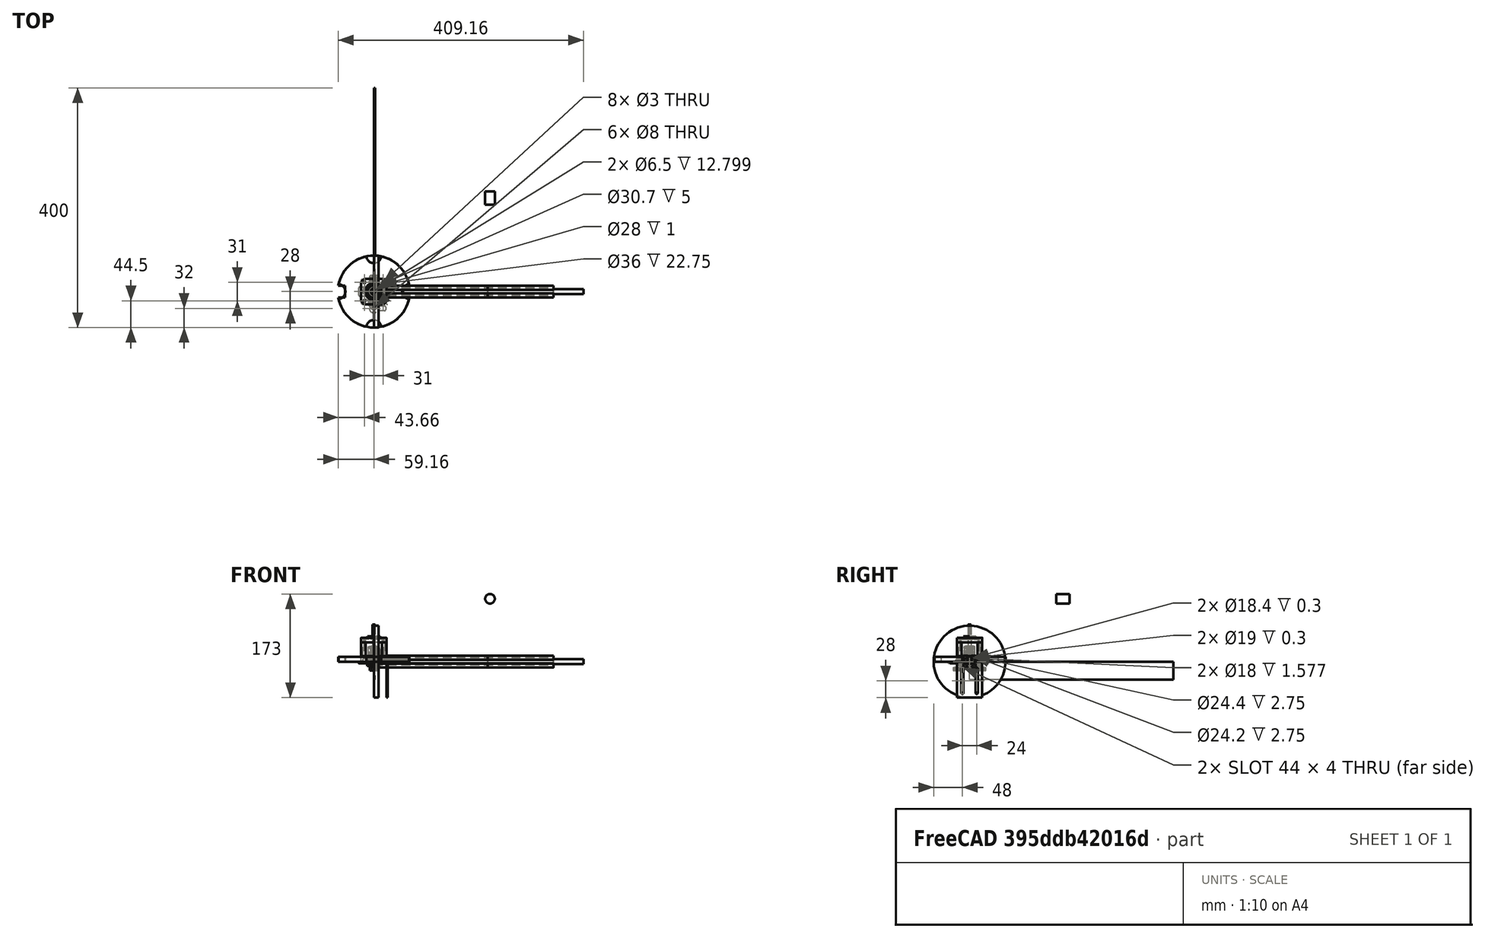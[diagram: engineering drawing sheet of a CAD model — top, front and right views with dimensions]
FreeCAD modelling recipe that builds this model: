
FCSTD DOCUMENT  (FreeCAD 0.19R)
Label: soloRuedas
License: All rights reserved
LicenseURL: http://en.wikipedia.org/wiki/All_rights_reserved
objects: Sketcher::SketchObject×358, PartDesign::Body×267, PartDesign::Pad×215, PartDesign::Fillet×183, App::Part×128, PartDesign::Pocket×123, PartDesign::FeatureBase×92, PartDesign::Revolution×52, App::DocumentObjectGroup×42, App::LinkGroup×30, PartDesign::PolarPattern×29, PartDesign::Chamfer×21, PartDesign::Groove×8, Part::FeaturePython×8, PartDesign::Mirrored×6, PartDesign::ShapeBinder×5, PartDesign::Hole×2, PartDesign::Draft×2, PartDesign::LinearPattern×2, PartDesign::Plane×2, +5 more types
note: 1994 computed .brp shape members not serialized (recipe doc carries the construction recipe); baked Part::Feature solids carry a one-line shape summary decoded from their .brp

FEATURE [Sketcher::SketchObject] Sketch001
  FullyConstrained = false
  MapMode = 5
  Support = -> [XY_Plane003]
  sketch-geometry (46):
    g0: LineSegment StartX=3.4 StartY=2.65 StartZ=0 EndX=3.4 EndY=-2.6657 EndZ=0
    g1: LineSegment StartX=2.63162 StartY=-3.4 StartZ=0 EndX=-2.65 EndY=-3.4 EndZ=0
    g2: LineSegment StartX=-3.4 StartY=-2.63136 StartZ=0 EndX=-3.4 EndY=2.61487 EndZ=0
    g3: LineSegment StartX=-10 StartY=10 StartZ=0 EndX=-3.125 EndY=10 EndZ=0
    g4: LineSegment StartX=10 StartY=10 StartZ=0 EndX=10 EndY=3.125 EndZ=0
    g5: LineSegment StartX=10 StartY=-10 StartZ=0 EndX=3.125 EndY=-10 EndZ=0
    g6: LineSegment StartX=-10 StartY=-10 StartZ=0 EndX=-10 EndY=-3.125 EndZ=0
    g7: GeomPoint X=3e-16 Y=0 Z=0
    g8: Circle CenterX=3e-16 CenterY=0 CenterZ=0 NormalX=0 NormalY=0 NormalZ=1 AngleXU=0 Radius=2.1
    g9: LineSegment StartX=-4.76483 StartY=8.08721 StartZ=0 EndX=-3.55 EndY=8.08721 EndZ=0
    g10: LineSegment StartX=8.24722 StartY=4.75 StartZ=0 EndX=8.24722 EndY=3.55 EndZ=0
    g11: LineSegment StartX=-8.2 StartY=-4.73729 StartZ=0 EndX=-8.2 EndY=-3.55 EndZ=0
    g12: LineSegment StartX=5.5 StartY=4.75 StartZ=0 EndX=8.24722 EndY=4.75 EndZ=0
    g13: LineSegment StartX=4.75 StartY=5.50457 StartZ=0 EndX=2.65 EndY=3.4 EndZ=0
    g14: LineSegment StartX=4.75 StartY=5.50457 StartZ=0 EndX=4.75 EndY=8.08721 EndZ=0
    g15: LineSegment StartX=3.4 StartY=2.65 StartZ=0 EndX=5.5 EndY=4.75 EndZ=0
    g16: LineSegment StartX=-4.76483 StartY=5.50457 StartZ=0 EndX=-2.66166 EndY=3.4 EndZ=0
    g17: LineSegment StartX=-5.5 StartY=4.70904 StartZ=0 EndX=-3.4 EndY=2.61487 EndZ=0
    g18: LineSegment StartX=-4.76483 StartY=5.50457 StartZ=0 EndX=-4.76483 EndY=8.08721 EndZ=0
    g19: LineSegment StartX=-5.5 StartY=4.70904 StartZ=0 EndX=-8.2 EndY=4.70904 EndZ=0
    g20: LineSegment StartX=-10 StartY=3.125 StartZ=0 EndX=-10 EndY=10 EndZ=0
    g21: LineSegment StartX=-8.2 StartY=3.55 StartZ=0 EndX=-8.2 EndY=4.70904 EndZ=0
    g22: LineSegment StartX=3.55 StartY=8.08721 StartZ=0 EndX=4.75 EndY=8.08721 EndZ=0
    g23: LineSegment StartX=3.125 StartY=10 StartZ=0 EndX=10 EndY=10 EndZ=0
    g24: LineSegment StartX=-5.5 StartY=-4.73729 StartZ=0 EndX=-8.2 EndY=-4.73729 EndZ=0
    g25: LineSegment StartX=-4.75 StartY=-5.5 StartZ=0 EndX=-2.65 EndY=-3.4 EndZ=0
    g26: LineSegment StartX=-4.75 StartY=-5.5 StartZ=0 EndX=-4.75 EndY=-8.2 EndZ=0
    g27: LineSegment StartX=4.73747 StartY=-5.5 StartZ=0 EndX=4.73747 EndY=-8.2 EndZ=0
    g28: LineSegment StartX=5.5 StartY=-4.7671 StartZ=0 EndX=8.24722 EndY=-4.7671 EndZ=0
    g29: LineSegment StartX=-3.125 StartY=-10 StartZ=0 EndX=-10 EndY=-10 EndZ=0
    g30: LineSegment StartX=-3.55 StartY=-8.2 StartZ=0 EndX=-4.75 EndY=-8.2 EndZ=0
    g31: LineSegment StartX=4.73747 StartY=-8.2 StartZ=0 EndX=3.55 EndY=-8.2 EndZ=0
    g32: LineSegment StartX=10 StartY=-3.125 StartZ=0 EndX=10 EndY=-10 EndZ=0
    g33: LineSegment StartX=8.24722 StartY=-3.55 StartZ=0 EndX=8.24722 EndY=-4.7671 EndZ=0
    g34: LineSegment StartX=-2.66166 StartY=3.4 StartZ=0 EndX=2.65 EndY=3.4 EndZ=0
    g35: LineSegment StartX=-3.4 StartY=-2.63136 StartZ=0 EndX=-5.5 EndY=-4.73729 EndZ=0
    g36: LineSegment StartX=3.4 StartY=-2.6657 StartZ=0 EndX=5.5 EndY=-4.7671 EndZ=0
    g37: LineSegment StartX=2.63162 StartY=-3.4 StartZ=0 EndX=4.73747 EndY=-5.5 EndZ=0
    g38: LineSegment StartX=-3.55 StartY=-8.2 StartZ=0 EndX=-3.125 EndY=-10 EndZ=0
    g39: LineSegment StartX=3.55 StartY=-8.2 StartZ=0 EndX=3.125 EndY=-10 EndZ=0
    g40: LineSegment StartX=-3.125 StartY=10 StartZ=0 EndX=-3.55 EndY=8.08721 EndZ=0
    g41: LineSegment StartX=3.125 StartY=10 StartZ=0 EndX=3.55 EndY=8.08721 EndZ=0
    g42: LineSegment StartX=8.24722 StartY=3.55 StartZ=0 EndX=10 EndY=3.125 EndZ=0
    g43: LineSegment StartX=10 StartY=-3.125 StartZ=0 EndX=8.24722 EndY=-3.55 EndZ=0
    g44: LineSegment StartX=-10 StartY=-3.125 StartZ=0 EndX=-8.2 EndY=-3.55 EndZ=0
    g45: LineSegment StartX=-10 StartY=3.125 StartZ=0 EndX=-8.2 EndY=3.55 EndZ=0
  constraints (61):
    c: Horizontal(g1)
    c: Vertical(g0)
    c: Vertical(g2)
    c: Coincident(g23,g4)
    c: Coincident(g32,g5)
    c: Coincident(g29,g6)
    c: Coincident(g20,g3)
    c: Horizontal(g3)
    c: Horizontal(g5)
    c: Vertical(g4)
    c: Vertical(g6)
    c: PointOnObject(g7,g-1)
    c: DistanceX(g3,g7) = 10
    c: DistanceX(g-1,g23) = 10
    c: DistanceY(g7,g3) = 10
    c: DistanceX(g3,g-1) = 10
    c: DistanceY(g32,g7) = 10
    c: Coincident(g8,g7)
    c: Radius(g8) = 2.1
    c: Horizontal(g9)
    c: Vertical(g10)
    c: Vertical(g11)
    c: Coincident(g12,g15)
    c: Horizontal(g12)
    c: Coincident(g14,g13)
    c: Vertical(g14)
    c: Coincident(g15,g0)
    c: Coincident(g13,g34)
    c: Coincident(g14,g22)
    c: Coincident(g18,g16)
    c: Vertical(g18)
    c: Coincident(g19,g17)
    c: Horizontal(g19)
    c: Coincident(g9,g18)
    c: Coincident(g21,g19)
    c: Coincident(g24,g35)
    c: Horizontal(g24)
    c: Coincident(g26,g25)
    c: Vertical(g26)
    c: Coincident(g27,g37)
    c: Vertical(g27)
    c: Coincident(g28,g36)
    c: Horizontal(g28)
    c: Coincident(g11,g24)
    c: Coincident(g26,g30)
    c: Coincident(g31,g27)
    c: Coincident(g12,g10)
    c: Coincident(g28,g33)
    c: Coincident(g25,g1)
    c: Coincident(g35,g2)
    c: Coincident(g17,g2)
    c: Coincident(g16,g34)
    c: Coincident(g1,g37)
    c: Coincident(g0,g36)
    c: Coincident(g39,g5)
    c: Coincident(g40,g3)
    c: Coincident(g42,g4)
    c: Coincident(g44,g6)
    c: Coincident(g21,g45)
    c: Coincident(g33,g43)
    c: Coincident(g10,g42)
FEATURE [PartDesign::Pad] Pad001
  Direction = (0,0,1)
  Length = 300
  Length2 = 10
  Profile = -> Sketch001
  Type = 0
FEATURE [PartDesign::Fillet] Fillet011
  Base = -> Pad001 [Edge53]
  BaseFeature = -> Pad001
  Radius = 1
  SupportTransform = false
FEATURE [PartDesign::Fillet] Fillet012
  Base = -> Fillet011 [Edge114]
  BaseFeature = -> Fillet011
  Radius = 1
  SupportTransform = false
FEATURE [PartDesign::Fillet] Fillet013
  Base = -> Fillet012 [Edge137,Edge95]
  BaseFeature = -> Fillet012
  Radius = 0.5
  SupportTransform = false
FEATURE [PartDesign::Fillet] Fillet014
  Base = -> Fillet013 [Edge103]
  BaseFeature = -> Fillet013
  Radius = 0.5
  SupportTransform = false
FEATURE [PartDesign::Fillet] Fillet015
  Base = -> Fillet014 [Edge96]
  BaseFeature = -> Fillet014
  Radius = 0.5
  SupportTransform = false
FEATURE [PartDesign::Fillet] Fillet016
  Base = -> Fillet015 [Edge77]
  BaseFeature = -> Fillet015
  Radius = 0.5
  SupportTransform = false
FEATURE [PartDesign::Fillet] Fillet017
  Base = -> Fillet016 [Edge102]
  BaseFeature = -> Fillet016
  Radius = 0.5
  SupportTransform = false
FEATURE [PartDesign::Fillet] Fillet018
  Base = -> Fillet017 [Edge85]
  BaseFeature = -> Fillet017
  Radius = 0.5
  SupportTransform = false
FEATURE [PartDesign::Fillet] Fillet019
  Base = -> Fillet018 [Edge78]
  BaseFeature = -> Fillet018
  Radius = 0.5
  SupportTransform = false
FEATURE [PartDesign::Fillet] Fillet020
  Base = -> Fillet019 [Edge107]
  BaseFeature = -> Fillet019
  Radius = 0.5
  SupportTransform = false
FEATURE [PartDesign::Fillet] Fillet021
  Base = -> Fillet020 [Edge74]
  BaseFeature = -> Fillet020
  Radius = 0.5
  SupportTransform = false
FEATURE [PartDesign::Body] Body001
  Group = -> [Sketch001,Pad001,Fillet011,Fillet012,Fillet013,Fillet014,Fillet015,Fillet016,Fillet017,Fillet018,Fillet019,Fillet020,Fillet021]
  Origin = -> Origin003
  Placement = pos=(0,0,0) rot=(0,1,0;1.5708rad)
  Tip = -> Fillet021
FEATURE [App::Part] Part001  label="2020-300-002"
  Group = -> [Body001]
  Origin = -> Origin002
  Placement = pos=(20,330,10) rot=(0,0,1;0rad)
FEATURE [Sketcher::SketchObject] Sketch002
  FullyConstrained = false
  MapMode = 5
  Support = -> [XY_Plane005]
  sketch-geometry (46):
    g0: LineSegment StartX=3.4 StartY=2.65 StartZ=0 EndX=3.4 EndY=-2.6657 EndZ=0
    g1: LineSegment StartX=2.63162 StartY=-3.4 StartZ=0 EndX=-2.65 EndY=-3.4 EndZ=0
    g2: LineSegment StartX=-3.4 StartY=-2.63136 StartZ=0 EndX=-3.4 EndY=2.61487 EndZ=0
    g3: LineSegment StartX=-10 StartY=10 StartZ=0 EndX=-3.125 EndY=10 EndZ=0
    g4: LineSegment StartX=10 StartY=10 StartZ=0 EndX=10 EndY=3.125 EndZ=0
    g5: LineSegment StartX=10 StartY=-10 StartZ=0 EndX=3.125 EndY=-10 EndZ=0
    g6: LineSegment StartX=-10 StartY=-10 StartZ=0 EndX=-10 EndY=-3.125 EndZ=0
    g7: GeomPoint X=3e-16 Y=0 Z=0
    g8: Circle CenterX=3e-16 CenterY=0 CenterZ=0 NormalX=0 NormalY=0 NormalZ=1 AngleXU=0 Radius=2.1
    g9: LineSegment StartX=-4.76483 StartY=8.08721 StartZ=0 EndX=-3.55 EndY=8.08721 EndZ=0
    g10: LineSegment StartX=8.24722 StartY=4.75 StartZ=0 EndX=8.24722 EndY=3.55 EndZ=0
    g11: LineSegment StartX=-8.2 StartY=-4.73729 StartZ=0 EndX=-8.2 EndY=-3.55 EndZ=0
    g12: LineSegment StartX=5.5 StartY=4.75 StartZ=0 EndX=8.24722 EndY=4.75 EndZ=0
    g13: LineSegment StartX=4.75 StartY=5.50457 StartZ=0 EndX=2.65 EndY=3.4 EndZ=0
    g14: LineSegment StartX=4.75 StartY=5.50457 StartZ=0 EndX=4.75 EndY=8.08721 EndZ=0
    g15: LineSegment StartX=3.4 StartY=2.65 StartZ=0 EndX=5.5 EndY=4.75 EndZ=0
    g16: LineSegment StartX=-4.76483 StartY=5.50457 StartZ=0 EndX=-2.66166 EndY=3.4 EndZ=0
    g17: LineSegment StartX=-5.5 StartY=4.70904 StartZ=0 EndX=-3.4 EndY=2.61487 EndZ=0
    g18: LineSegment StartX=-4.76483 StartY=5.50457 StartZ=0 EndX=-4.76483 EndY=8.08721 EndZ=0
    g19: LineSegment StartX=-5.5 StartY=4.70904 StartZ=0 EndX=-8.2 EndY=4.70904 EndZ=0
    g20: LineSegment StartX=-10 StartY=3.125 StartZ=0 EndX=-10 EndY=10 EndZ=0
    g21: LineSegment StartX=-8.2 StartY=3.55 StartZ=0 EndX=-8.2 EndY=4.70904 EndZ=0
    g22: LineSegment StartX=3.55 StartY=8.08721 StartZ=0 EndX=4.75 EndY=8.08721 EndZ=0
    g23: LineSegment StartX=3.125 StartY=10 StartZ=0 EndX=10 EndY=10 EndZ=0
    g24: LineSegment StartX=-5.5 StartY=-4.73729 StartZ=0 EndX=-8.2 EndY=-4.73729 EndZ=0
    g25: LineSegment StartX=-4.75 StartY=-5.5 StartZ=0 EndX=-2.65 EndY=-3.4 EndZ=0
    g26: LineSegment StartX=-4.75 StartY=-5.5 StartZ=0 EndX=-4.75 EndY=-8.2 EndZ=0
    g27: LineSegment StartX=4.73747 StartY=-5.5 StartZ=0 EndX=4.73747 EndY=-8.2 EndZ=0
    g28: LineSegment StartX=5.5 StartY=-4.7671 StartZ=0 EndX=8.24722 EndY=-4.7671 EndZ=0
    g29: LineSegment StartX=-3.125 StartY=-10 StartZ=0 EndX=-10 EndY=-10 EndZ=0
    g30: LineSegment StartX=-3.55 StartY=-8.2 StartZ=0 EndX=-4.75 EndY=-8.2 EndZ=0
    g31: LineSegment StartX=4.73747 StartY=-8.2 StartZ=0 EndX=3.55 EndY=-8.2 EndZ=0
    g32: LineSegment StartX=10 StartY=-3.125 StartZ=0 EndX=10 EndY=-10 EndZ=0
    g33: LineSegment StartX=8.24722 StartY=-3.55 StartZ=0 EndX=8.24722 EndY=-4.7671 EndZ=0
    g34: LineSegment StartX=-2.66166 StartY=3.4 StartZ=0 EndX=2.65 EndY=3.4 EndZ=0
    g35: LineSegment StartX=-3.4 StartY=-2.63136 StartZ=0 EndX=-5.5 EndY=-4.73729 EndZ=0
    g36: LineSegment StartX=3.4 StartY=-2.6657 StartZ=0 EndX=5.5 EndY=-4.7671 EndZ=0
    g37: LineSegment StartX=2.63162 StartY=-3.4 StartZ=0 EndX=4.73747 EndY=-5.5 EndZ=0
    g38: LineSegment StartX=-3.55 StartY=-8.2 StartZ=0 EndX=-3.125 EndY=-10 EndZ=0
    g39: LineSegment StartX=3.55 StartY=-8.2 StartZ=0 EndX=3.125 EndY=-10 EndZ=0
    g40: LineSegment StartX=-3.125 StartY=10 StartZ=0 EndX=-3.55 EndY=8.08721 EndZ=0
    g41: LineSegment StartX=3.125 StartY=10 StartZ=0 EndX=3.55 EndY=8.08721 EndZ=0
    g42: LineSegment StartX=8.24722 StartY=3.55 StartZ=0 EndX=10 EndY=3.125 EndZ=0
    g43: LineSegment StartX=10 StartY=-3.125 StartZ=0 EndX=8.24722 EndY=-3.55 EndZ=0
    g44: LineSegment StartX=-10 StartY=-3.125 StartZ=0 EndX=-8.2 EndY=-3.55 EndZ=0
    g45: LineSegment StartX=-10 StartY=3.125 StartZ=0 EndX=-8.2 EndY=3.55 EndZ=0
  constraints (61):
    c: Horizontal(g1)
    c: Vertical(g0)
    c: Vertical(g2)
    c: Coincident(g23,g4)
    c: Coincident(g32,g5)
    c: Coincident(g29,g6)
    c: Coincident(g20,g3)
    c: Horizontal(g3)
    c: Horizontal(g5)
    c: Vertical(g4)
    c: Vertical(g6)
    c: PointOnObject(g7,g-1)
    c: DistanceX(g3,g7) = 10
    c: DistanceX(g-1,g23) = 10
    c: DistanceY(g7,g3) = 10
    c: DistanceX(g3,g-1) = 10
    c: DistanceY(g32,g7) = 10
    c: Coincident(g8,g7)
    c: Radius(g8) = 2.1
    c: Horizontal(g9)
    c: Vertical(g10)
    c: Vertical(g11)
    c: Coincident(g12,g15)
    c: Horizontal(g12)
    c: Coincident(g14,g13)
    c: Vertical(g14)
    c: Coincident(g15,g0)
    c: Coincident(g13,g34)
    c: Coincident(g14,g22)
    c: Coincident(g18,g16)
    c: Vertical(g18)
    c: Coincident(g19,g17)
    c: Horizontal(g19)
    c: Coincident(g9,g18)
    c: Coincident(g21,g19)
    c: Coincident(g24,g35)
    c: Horizontal(g24)
    c: Coincident(g26,g25)
    c: Vertical(g26)
    c: Coincident(g27,g37)
    c: Vertical(g27)
    c: Coincident(g28,g36)
    c: Horizontal(g28)
    c: Coincident(g11,g24)
    c: Coincident(g26,g30)
    c: Coincident(g31,g27)
    c: Coincident(g12,g10)
    c: Coincident(g28,g33)
    c: Coincident(g25,g1)
    c: Coincident(g35,g2)
    c: Coincident(g17,g2)
    c: Coincident(g16,g34)
    c: Coincident(g1,g37)
    c: Coincident(g0,g36)
    c: Coincident(g39,g5)
    c: Coincident(g40,g3)
    c: Coincident(g42,g4)
    c: Coincident(g44,g6)
    c: Coincident(g21,g45)
    c: Coincident(g33,g43)
    c: Coincident(g10,g42)
FEATURE [PartDesign::Pad] Pad002
  Direction = (0,0,1)
  Length = 300
  Length2 = 10
  Profile = -> Sketch002
  Type = 0
FEATURE [PartDesign::Fillet] Fillet022
  Base = -> Pad002 [Edge53]
  BaseFeature = -> Pad002
  Radius = 1
  SupportTransform = false
FEATURE [PartDesign::Fillet] Fillet023
  Base = -> Fillet022 [Edge114]
  BaseFeature = -> Fillet022
  Radius = 1
  SupportTransform = false
FEATURE [PartDesign::Fillet] Fillet024
  Base = -> Fillet023 [Edge137,Edge95]
  BaseFeature = -> Fillet023
  Radius = 0.5
  SupportTransform = false
FEATURE [PartDesign::Fillet] Fillet025
  Base = -> Fillet024 [Edge103]
  BaseFeature = -> Fillet024
  Radius = 0.5
  SupportTransform = false
FEATURE [PartDesign::Fillet] Fillet026
  Base = -> Fillet025 [Edge96]
  BaseFeature = -> Fillet025
  Radius = 0.5
  SupportTransform = false
FEATURE [PartDesign::Fillet] Fillet027
  Base = -> Fillet026 [Edge77]
  BaseFeature = -> Fillet026
  Radius = 0.5
  SupportTransform = false
FEATURE [PartDesign::Fillet] Fillet028
  Base = -> Fillet027 [Edge102]
  BaseFeature = -> Fillet027
  Radius = 0.5
  SupportTransform = false
FEATURE [PartDesign::Fillet] Fillet029
  Base = -> Fillet028 [Edge85]
  BaseFeature = -> Fillet028
  Radius = 0.5
  SupportTransform = false
FEATURE [PartDesign::Fillet] Fillet030
  Base = -> Fillet029 [Edge78]
  BaseFeature = -> Fillet029
  Radius = 0.5
  SupportTransform = false
FEATURE [PartDesign::Fillet] Fillet031
  Base = -> Fillet030 [Edge107]
  BaseFeature = -> Fillet030
  Radius = 0.5
  SupportTransform = false
FEATURE [PartDesign::Fillet] Fillet032
  Base = -> Fillet031 [Edge74]
  BaseFeature = -> Fillet031
  Radius = 0.5
  SupportTransform = false
FEATURE [PartDesign::Body] Body002
  Group = -> [Sketch002,Pad002,Fillet022,Fillet023,Fillet024,Fillet025,Fillet026,Fillet027,Fillet028,Fillet029,Fillet030,Fillet031,Fillet032]
  Origin = -> Origin005
  Placement = pos=(0,0,0) rot=(0,1,0;1.5708rad)
  Tip = -> Fillet032
FEATURE [App::Part] Part002  label="2020-300-003"
  Group = -> [Body002]
  Origin = -> Origin004
  Placement = pos=(10,20,10) rot=(0,0,1;1.5708rad)
FEATURE [Sketcher::SketchObject] Sketch003
  FullyConstrained = false
  MapMode = 5
  Support = -> [XY_Plane007]
  sketch-geometry (46):
    g0: LineSegment StartX=3.4 StartY=2.65 StartZ=0 EndX=3.4 EndY=-2.6657 EndZ=0
    g1: LineSegment StartX=2.63162 StartY=-3.4 StartZ=0 EndX=-2.65 EndY=-3.4 EndZ=0
    g2: LineSegment StartX=-3.4 StartY=-2.63136 StartZ=0 EndX=-3.4 EndY=2.61487 EndZ=0
    g3: LineSegment StartX=-10 StartY=10 StartZ=0 EndX=-3.125 EndY=10 EndZ=0
    g4: LineSegment StartX=10 StartY=10 StartZ=0 EndX=10 EndY=3.125 EndZ=0
    g5: LineSegment StartX=10 StartY=-10 StartZ=0 EndX=3.125 EndY=-10 EndZ=0
    g6: LineSegment StartX=-10 StartY=-10 StartZ=0 EndX=-10 EndY=-3.125 EndZ=0
    g7: GeomPoint X=3e-16 Y=0 Z=0
    g8: Circle CenterX=3e-16 CenterY=0 CenterZ=0 NormalX=0 NormalY=0 NormalZ=1 AngleXU=0 Radius=2.1
    g9: LineSegment StartX=-4.76483 StartY=8.08721 StartZ=0 EndX=-3.55 EndY=8.08721 EndZ=0
    g10: LineSegment StartX=8.24722 StartY=4.75 StartZ=0 EndX=8.24722 EndY=3.55 EndZ=0
    g11: LineSegment StartX=-8.2 StartY=-4.73729 StartZ=0 EndX=-8.2 EndY=-3.55 EndZ=0
    g12: LineSegment StartX=5.5 StartY=4.75 StartZ=0 EndX=8.24722 EndY=4.75 EndZ=0
    g13: LineSegment StartX=4.75 StartY=5.50457 StartZ=0 EndX=2.65 EndY=3.4 EndZ=0
    g14: LineSegment StartX=4.75 StartY=5.50457 StartZ=0 EndX=4.75 EndY=8.08721 EndZ=0
    g15: LineSegment StartX=3.4 StartY=2.65 StartZ=0 EndX=5.5 EndY=4.75 EndZ=0
    g16: LineSegment StartX=-4.76483 StartY=5.50457 StartZ=0 EndX=-2.66166 EndY=3.4 EndZ=0
    g17: LineSegment StartX=-5.5 StartY=4.70904 StartZ=0 EndX=-3.4 EndY=2.61487 EndZ=0
    g18: LineSegment StartX=-4.76483 StartY=5.50457 StartZ=0 EndX=-4.76483 EndY=8.08721 EndZ=0
    g19: LineSegment StartX=-5.5 StartY=4.70904 StartZ=0 EndX=-8.2 EndY=4.70904 EndZ=0
    g20: LineSegment StartX=-10 StartY=3.125 StartZ=0 EndX=-10 EndY=10 EndZ=0
    g21: LineSegment StartX=-8.2 StartY=3.55 StartZ=0 EndX=-8.2 EndY=4.70904 EndZ=0
    g22: LineSegment StartX=3.55 StartY=8.08721 StartZ=0 EndX=4.75 EndY=8.08721 EndZ=0
    g23: LineSegment StartX=3.125 StartY=10 StartZ=0 EndX=10 EndY=10 EndZ=0
    g24: LineSegment StartX=-5.5 StartY=-4.73729 StartZ=0 EndX=-8.2 EndY=-4.73729 EndZ=0
    g25: LineSegment StartX=-4.75 StartY=-5.5 StartZ=0 EndX=-2.65 EndY=-3.4 EndZ=0
    g26: LineSegment StartX=-4.75 StartY=-5.5 StartZ=0 EndX=-4.75 EndY=-8.2 EndZ=0
    g27: LineSegment StartX=4.73747 StartY=-5.5 StartZ=0 EndX=4.73747 EndY=-8.2 EndZ=0
    g28: LineSegment StartX=5.5 StartY=-4.7671 StartZ=0 EndX=8.24722 EndY=-4.7671 EndZ=0
    g29: LineSegment StartX=-3.125 StartY=-10 StartZ=0 EndX=-10 EndY=-10 EndZ=0
    g30: LineSegment StartX=-3.55 StartY=-8.2 StartZ=0 EndX=-4.75 EndY=-8.2 EndZ=0
    g31: LineSegment StartX=4.73747 StartY=-8.2 StartZ=0 EndX=3.55 EndY=-8.2 EndZ=0
    g32: LineSegment StartX=10 StartY=-3.125 StartZ=0 EndX=10 EndY=-10 EndZ=0
    g33: LineSegment StartX=8.24722 StartY=-3.55 StartZ=0 EndX=8.24722 EndY=-4.7671 EndZ=0
    g34: LineSegment StartX=-2.66166 StartY=3.4 StartZ=0 EndX=2.65 EndY=3.4 EndZ=0
    g35: LineSegment StartX=-3.4 StartY=-2.63136 StartZ=0 EndX=-5.5 EndY=-4.73729 EndZ=0
    g36: LineSegment StartX=3.4 StartY=-2.6657 StartZ=0 EndX=5.5 EndY=-4.7671 EndZ=0
    g37: LineSegment StartX=2.63162 StartY=-3.4 StartZ=0 EndX=4.73747 EndY=-5.5 EndZ=0
    g38: LineSegment StartX=-3.55 StartY=-8.2 StartZ=0 EndX=-3.125 EndY=-10 EndZ=0
    g39: LineSegment StartX=3.55 StartY=-8.2 StartZ=0 EndX=3.125 EndY=-10 EndZ=0
    g40: LineSegment StartX=-3.125 StartY=10 StartZ=0 EndX=-3.55 EndY=8.08721 EndZ=0
    g41: LineSegment StartX=3.125 StartY=10 StartZ=0 EndX=3.55 EndY=8.08721 EndZ=0
    g42: LineSegment StartX=8.24722 StartY=3.55 StartZ=0 EndX=10 EndY=3.125 EndZ=0
    g43: LineSegment StartX=10 StartY=-3.125 StartZ=0 EndX=8.24722 EndY=-3.55 EndZ=0
    g44: LineSegment StartX=-10 StartY=-3.125 StartZ=0 EndX=-8.2 EndY=-3.55 EndZ=0
    g45: LineSegment StartX=-10 StartY=3.125 StartZ=0 EndX=-8.2 EndY=3.55 EndZ=0
  constraints (61):
    c: Horizontal(g1)
    c: Vertical(g0)
    c: Vertical(g2)
    c: Coincident(g23,g4)
    c: Coincident(g32,g5)
    c: Coincident(g29,g6)
    c: Coincident(g20,g3)
    c: Horizontal(g3)
    c: Horizontal(g5)
    c: Vertical(g4)
    c: Vertical(g6)
    c: PointOnObject(g7,g-1)
    c: DistanceX(g3,g7) = 10
    c: DistanceX(g-1,g23) = 10
    c: DistanceY(g7,g3) = 10
    c: DistanceX(g3,g-1) = 10
    c: DistanceY(g32,g7) = 10
    c: Coincident(g8,g7)
    c: Radius(g8) = 2.1
    c: Horizontal(g9)
    c: Vertical(g10)
    c: Vertical(g11)
    c: Coincident(g12,g15)
    c: Horizontal(g12)
    c: Coincident(g14,g13)
    c: Vertical(g14)
    c: Coincident(g15,g0)
    c: Coincident(g13,g34)
    c: Coincident(g14,g22)
    c: Coincident(g18,g16)
    c: Vertical(g18)
    c: Coincident(g19,g17)
    c: Horizontal(g19)
    c: Coincident(g9,g18)
    c: Coincident(g21,g19)
    c: Coincident(g24,g35)
    c: Horizontal(g24)
    c: Coincident(g26,g25)
    c: Vertical(g26)
    c: Coincident(g27,g37)
    c: Vertical(g27)
    c: Coincident(g28,g36)
    c: Horizontal(g28)
    c: Coincident(g11,g24)
    c: Coincident(g26,g30)
    c: Coincident(g31,g27)
    c: Coincident(g12,g10)
    c: Coincident(g28,g33)
    c: Coincident(g25,g1)
    c: Coincident(g35,g2)
    c: Coincident(g17,g2)
    c: Coincident(g16,g34)
    c: Coincident(g1,g37)
    c: Coincident(g0,g36)
    c: Coincident(g39,g5)
    c: Coincident(g40,g3)
    c: Coincident(g42,g4)
    c: Coincident(g44,g6)
    c: Coincident(g21,g45)
    c: Coincident(g33,g43)
    c: Coincident(g10,g42)
FEATURE [PartDesign::Pad] Pad003
  Direction = (0,0,1)
  Length = 300
  Length2 = 10
  Profile = -> Sketch003
  Type = 0
FEATURE [PartDesign::Fillet] Fillet033
  Base = -> Pad003 [Edge53]
  BaseFeature = -> Pad003
  Radius = 1
  SupportTransform = false
FEATURE [PartDesign::Fillet] Fillet034
  Base = -> Fillet033 [Edge114]
  BaseFeature = -> Fillet033
  Radius = 1
  SupportTransform = false
FEATURE [PartDesign::Fillet] Fillet035
  Base = -> Fillet034 [Edge137,Edge95]
  BaseFeature = -> Fillet034
  Radius = 0.5
  SupportTransform = false
FEATURE [PartDesign::Fillet] Fillet036
  Base = -> Fillet035 [Edge103]
  BaseFeature = -> Fillet035
  Radius = 0.5
  SupportTransform = false
FEATURE [PartDesign::Fillet] Fillet037
  Base = -> Fillet036 [Edge96]
  BaseFeature = -> Fillet036
  Radius = 0.5
  SupportTransform = false
FEATURE [PartDesign::Fillet] Fillet038
  Base = -> Fillet037 [Edge77]
  BaseFeature = -> Fillet037
  Radius = 0.5
  SupportTransform = false
FEATURE [PartDesign::Fillet] Fillet039
  Base = -> Fillet038 [Edge102]
  BaseFeature = -> Fillet038
  Radius = 0.5
  SupportTransform = false
FEATURE [PartDesign::Fillet] Fillet040
  Base = -> Fillet039 [Edge85]
  BaseFeature = -> Fillet039
  Radius = 0.5
  SupportTransform = false
FEATURE [PartDesign::Fillet] Fillet041
  Base = -> Fillet040 [Edge78]
  BaseFeature = -> Fillet040
  Radius = 0.5
  SupportTransform = false
FEATURE [PartDesign::Fillet] Fillet042
  Base = -> Fillet041 [Edge107]
  BaseFeature = -> Fillet041
  Radius = 0.5
  SupportTransform = false
FEATURE [PartDesign::Fillet] Fillet043
  Base = -> Fillet042 [Edge74]
  BaseFeature = -> Fillet042
  Radius = 0.5
  SupportTransform = false
FEATURE [PartDesign::Body] Body003
  Group = -> [Sketch003,Pad003,Fillet033,Fillet034,Fillet035,Fillet036,Fillet037,Fillet038,Fillet039,Fillet040,Fillet041,Fillet042,Fillet043]
  Origin = -> Origin007
  Placement = pos=(0,0,0) rot=(0,1,0;1.5708rad)
  Tip = -> Fillet043
FEATURE [App::Part] Part003  label="2020-300-004"
  Group = -> [Body003]
  Origin = -> Origin006
  Placement = pos=(330,20,10) rot=(0,0,1;1.5708rad)
FEATURE [Sketcher::SketchObject] Sketch004
  FullyConstrained = false
  MapMode = 5
  Support = -> [XY_Plane009]
  sketch-geometry (46):
    g0: LineSegment StartX=3.4 StartY=2.65 StartZ=0 EndX=3.4 EndY=-2.6657 EndZ=0
    g1: LineSegment StartX=2.63162 StartY=-3.4 StartZ=0 EndX=-2.65 EndY=-3.4 EndZ=0
    g2: LineSegment StartX=-3.4 StartY=-2.63136 StartZ=0 EndX=-3.4 EndY=2.61487 EndZ=0
    g3: LineSegment StartX=-10 StartY=10 StartZ=0 EndX=-3.125 EndY=10 EndZ=0
    g4: LineSegment StartX=10 StartY=10 StartZ=0 EndX=10 EndY=3.125 EndZ=0
    g5: LineSegment StartX=10 StartY=-10 StartZ=0 EndX=3.125 EndY=-10 EndZ=0
    g6: LineSegment StartX=-10 StartY=-10 StartZ=0 EndX=-10 EndY=-3.125 EndZ=0
    g7: GeomPoint X=3e-16 Y=0 Z=0
    g8: Circle CenterX=3e-16 CenterY=0 CenterZ=0 NormalX=0 NormalY=0 NormalZ=1 AngleXU=0 Radius=2.1
    g9: LineSegment StartX=-4.76483 StartY=8.08721 StartZ=0 EndX=-3.55 EndY=8.08721 EndZ=0
    g10: LineSegment StartX=8.24722 StartY=4.75 StartZ=0 EndX=8.24722 EndY=3.55 EndZ=0
    g11: LineSegment StartX=-8.2 StartY=-4.73729 StartZ=0 EndX=-8.2 EndY=-3.55 EndZ=0
    g12: LineSegment StartX=5.5 StartY=4.75 StartZ=0 EndX=8.24722 EndY=4.75 EndZ=0
    g13: LineSegment StartX=4.75 StartY=5.50457 StartZ=0 EndX=2.65 EndY=3.4 EndZ=0
    g14: LineSegment StartX=4.75 StartY=5.50457 StartZ=0 EndX=4.75 EndY=8.08721 EndZ=0
    g15: LineSegment StartX=3.4 StartY=2.65 StartZ=0 EndX=5.5 EndY=4.75 EndZ=0
    g16: LineSegment StartX=-4.76483 StartY=5.50457 StartZ=0 EndX=-2.66166 EndY=3.4 EndZ=0
    g17: LineSegment StartX=-5.5 StartY=4.70904 StartZ=0 EndX=-3.4 EndY=2.61487 EndZ=0
    g18: LineSegment StartX=-4.76483 StartY=5.50457 StartZ=0 EndX=-4.76483 EndY=8.08721 EndZ=0
    g19: LineSegment StartX=-5.5 StartY=4.70904 StartZ=0 EndX=-8.2 EndY=4.70904 EndZ=0
    g20: LineSegment StartX=-10 StartY=3.125 StartZ=0 EndX=-10 EndY=10 EndZ=0
    g21: LineSegment StartX=-8.2 StartY=3.55 StartZ=0 EndX=-8.2 EndY=4.70904 EndZ=0
    g22: LineSegment StartX=3.55 StartY=8.08721 StartZ=0 EndX=4.75 EndY=8.08721 EndZ=0
    g23: LineSegment StartX=3.125 StartY=10 StartZ=0 EndX=10 EndY=10 EndZ=0
    g24: LineSegment StartX=-5.5 StartY=-4.73729 StartZ=0 EndX=-8.2 EndY=-4.73729 EndZ=0
    g25: LineSegment StartX=-4.75 StartY=-5.5 StartZ=0 EndX=-2.65 EndY=-3.4 EndZ=0
    g26: LineSegment StartX=-4.75 StartY=-5.5 StartZ=0 EndX=-4.75 EndY=-8.2 EndZ=0
    g27: LineSegment StartX=4.73747 StartY=-5.5 StartZ=0 EndX=4.73747 EndY=-8.2 EndZ=0
    g28: LineSegment StartX=5.5 StartY=-4.7671 StartZ=0 EndX=8.24722 EndY=-4.7671 EndZ=0
    g29: LineSegment StartX=-3.125 StartY=-10 StartZ=0 EndX=-10 EndY=-10 EndZ=0
    g30: LineSegment StartX=-3.55 StartY=-8.2 StartZ=0 EndX=-4.75 EndY=-8.2 EndZ=0
    g31: LineSegment StartX=4.73747 StartY=-8.2 StartZ=0 EndX=3.55 EndY=-8.2 EndZ=0
    g32: LineSegment StartX=10 StartY=-3.125 StartZ=0 EndX=10 EndY=-10 EndZ=0
    g33: LineSegment StartX=8.24722 StartY=-3.55 StartZ=0 EndX=8.24722 EndY=-4.7671 EndZ=0
    g34: LineSegment StartX=-2.66166 StartY=3.4 StartZ=0 EndX=2.65 EndY=3.4 EndZ=0
    g35: LineSegment StartX=-3.4 StartY=-2.63136 StartZ=0 EndX=-5.5 EndY=-4.73729 EndZ=0
    g36: LineSegment StartX=3.4 StartY=-2.6657 StartZ=0 EndX=5.5 EndY=-4.7671 EndZ=0
    g37: LineSegment StartX=2.63162 StartY=-3.4 StartZ=0 EndX=4.73747 EndY=-5.5 EndZ=0
    g38: LineSegment StartX=-3.55 StartY=-8.2 StartZ=0 EndX=-3.125 EndY=-10 EndZ=0
    g39: LineSegment StartX=3.55 StartY=-8.2 StartZ=0 EndX=3.125 EndY=-10 EndZ=0
    g40: LineSegment StartX=-3.125 StartY=10 StartZ=0 EndX=-3.55 EndY=8.08721 EndZ=0
    g41: LineSegment StartX=3.125 StartY=10 StartZ=0 EndX=3.55 EndY=8.08721 EndZ=0
    g42: LineSegment StartX=8.24722 StartY=3.55 StartZ=0 EndX=10 EndY=3.125 EndZ=0
    g43: LineSegment StartX=10 StartY=-3.125 StartZ=0 EndX=8.24722 EndY=-3.55 EndZ=0
    g44: LineSegment StartX=-10 StartY=-3.125 StartZ=0 EndX=-8.2 EndY=-3.55 EndZ=0
    g45: LineSegment StartX=-10 StartY=3.125 StartZ=0 EndX=-8.2 EndY=3.55 EndZ=0
  constraints (61):
    c: Horizontal(g1)
    c: Vertical(g0)
    c: Vertical(g2)
    c: Coincident(g23,g4)
    c: Coincident(g32,g5)
    c: Coincident(g29,g6)
    c: Coincident(g20,g3)
    c: Horizontal(g3)
    c: Horizontal(g5)
    c: Vertical(g4)
    c: Vertical(g6)
    c: PointOnObject(g7,g-1)
    c: DistanceX(g3,g7) = 10
    c: DistanceX(g-1,g23) = 10
    c: DistanceY(g7,g3) = 10
    c: DistanceX(g3,g-1) = 10
    c: DistanceY(g32,g7) = 10
    c: Coincident(g8,g7)
    c: Radius(g8) = 2.1
    c: Horizontal(g9)
    c: Vertical(g10)
    c: Vertical(g11)
    c: Coincident(g12,g15)
    c: Horizontal(g12)
    c: Coincident(g14,g13)
    c: Vertical(g14)
    c: Coincident(g15,g0)
    c: Coincident(g13,g34)
    c: Coincident(g14,g22)
    c: Coincident(g18,g16)
    c: Vertical(g18)
    c: Coincident(g19,g17)
    c: Horizontal(g19)
    c: Coincident(g9,g18)
    c: Coincident(g21,g19)
    c: Coincident(g24,g35)
    c: Horizontal(g24)
    c: Coincident(g26,g25)
    c: Vertical(g26)
    c: Coincident(g27,g37)
    c: Vertical(g27)
    c: Coincident(g28,g36)
    c: Horizontal(g28)
    c: Coincident(g11,g24)
    c: Coincident(g26,g30)
    c: Coincident(g31,g27)
    c: Coincident(g12,g10)
    c: Coincident(g28,g33)
    c: Coincident(g25,g1)
    c: Coincident(g35,g2)
    c: Coincident(g17,g2)
    c: Coincident(g16,g34)
    c: Coincident(g1,g37)
    c: Coincident(g0,g36)
    c: Coincident(g39,g5)
    c: Coincident(g40,g3)
    c: Coincident(g42,g4)
    c: Coincident(g44,g6)
    c: Coincident(g21,g45)
    c: Coincident(g33,g43)
    c: Coincident(g10,g42)
FEATURE [PartDesign::Pad] Pad004
  Direction = (0,0,1)
  Length = 190
  Length2 = 10
  Profile = -> Sketch004
  Type = 0
FEATURE [PartDesign::Fillet] Fillet044
  Base = -> Pad004 [Edge53]
  BaseFeature = -> Pad004
  Radius = 1
  SupportTransform = false
FEATURE [PartDesign::Fillet] Fillet045
  Base = -> Fillet044 [Edge114]
  BaseFeature = -> Fillet044
  Radius = 1
  SupportTransform = false
FEATURE [PartDesign::Fillet] Fillet046
  Base = -> Fillet045 [Edge137,Edge95]
  BaseFeature = -> Fillet045
  Radius = 0.5
  SupportTransform = false
FEATURE [PartDesign::Fillet] Fillet047
  Base = -> Fillet046 [Edge103]
  BaseFeature = -> Fillet046
  Radius = 0.5
  SupportTransform = false
FEATURE [PartDesign::Fillet] Fillet048
  Base = -> Fillet047 [Edge96]
  BaseFeature = -> Fillet047
  Radius = 0.5
  SupportTransform = false
FEATURE [PartDesign::Fillet] Fillet049
  Base = -> Fillet048 [Edge77]
  BaseFeature = -> Fillet048
  Radius = 0.5
  SupportTransform = false
FEATURE [PartDesign::Fillet] Fillet050
  Base = -> Fillet049 [Edge102]
  BaseFeature = -> Fillet049
  Radius = 0.5
  SupportTransform = false
FEATURE [PartDesign::Fillet] Fillet051
  Base = -> Fillet050 [Edge85]
  BaseFeature = -> Fillet050
  Radius = 0.5
  SupportTransform = false
FEATURE [PartDesign::Fillet] Fillet052
  Base = -> Fillet051 [Edge78]
  BaseFeature = -> Fillet051
  Radius = 0.5
  SupportTransform = false
FEATURE [PartDesign::Fillet] Fillet053
  Base = -> Fillet052 [Edge107]
  BaseFeature = -> Fillet052
  Radius = 0.5
  SupportTransform = false
FEATURE [PartDesign::Fillet] Fillet054
  Base = -> Fillet053 [Edge74]
  BaseFeature = -> Fillet053
  Radius = 0.5
  SupportTransform = false
FEATURE [PartDesign::Body] Body004
  Group = -> [Sketch004,Pad004,Fillet044,Fillet045,Fillet046,Fillet047,Fillet048,Fillet049,Fillet050,Fillet051,Fillet052,Fillet053,Fillet054]
  Origin = -> Origin009
  Placement = pos=(0,0,0) rot=(0,1,0;1.5708rad)
  Tip = -> Fillet054
FEATURE [Sketcher::SketchObject] Sketch
  FullyConstrained = false
  MapMode = 4
  Placement = pos=(0,0,0) rot=(0.707107,0.707107,0;3.14159rad)
  Support = -> [Body004]
  sketch-geometry (46):
    g0: LineSegment StartX=3.4 StartY=2.65 StartZ=0 EndX=3.4 EndY=-2.6657 EndZ=0
    g1: LineSegment StartX=2.63162 StartY=-3.4 StartZ=0 EndX=-2.65 EndY=-3.4 EndZ=0
    g2: LineSegment StartX=-3.4 StartY=-2.63136 StartZ=0 EndX=-3.4 EndY=2.61487 EndZ=0
    g3: LineSegment StartX=-10 StartY=10 StartZ=0 EndX=-3.125 EndY=10 EndZ=0
    g4: LineSegment StartX=10 StartY=10 StartZ=0 EndX=10 EndY=3.125 EndZ=0
    g5: LineSegment StartX=10 StartY=-10 StartZ=0 EndX=3.125 EndY=-10 EndZ=0
    g6: LineSegment StartX=-10 StartY=-10 StartZ=0 EndX=-10 EndY=-3.125 EndZ=0
    g7: GeomPoint X=3e-16 Y=0 Z=0
    g8: Circle CenterX=3e-16 CenterY=0 CenterZ=0 NormalX=0 NormalY=0 NormalZ=1 AngleXU=0 Radius=2.1
    g9: LineSegment StartX=-4.76483 StartY=8.08721 StartZ=0 EndX=-3.55 EndY=8.08721 EndZ=0
    g10: LineSegment StartX=8.24722 StartY=4.75 StartZ=0 EndX=8.24722 EndY=3.55 EndZ=0
    g11: LineSegment StartX=-8.2 StartY=-4.73729 StartZ=0 EndX=-8.2 EndY=-3.55 EndZ=0
    g12: LineSegment StartX=5.5 StartY=4.75 StartZ=0 EndX=8.24722 EndY=4.75 EndZ=0
    g13: LineSegment StartX=4.75 StartY=5.50457 StartZ=0 EndX=2.65 EndY=3.4 EndZ=0
    g14: LineSegment StartX=4.75 StartY=5.50457 StartZ=0 EndX=4.75 EndY=8.08721 EndZ=0
    g15: LineSegment StartX=3.4 StartY=2.65 StartZ=0 EndX=5.5 EndY=4.75 EndZ=0
    g16: LineSegment StartX=-4.76483 StartY=5.50457 StartZ=0 EndX=-2.66166 EndY=3.4 EndZ=0
    g17: LineSegment StartX=-5.5 StartY=4.70904 StartZ=0 EndX=-3.4 EndY=2.61487 EndZ=0
    g18: LineSegment StartX=-4.76483 StartY=5.50457 StartZ=0 EndX=-4.76483 EndY=8.08721 EndZ=0
    g19: LineSegment StartX=-5.5 StartY=4.70904 StartZ=0 EndX=-8.2 EndY=4.70904 EndZ=0
    g20: LineSegment StartX=-10 StartY=3.125 StartZ=0 EndX=-10 EndY=10 EndZ=0
    g21: LineSegment StartX=-8.2 StartY=3.55 StartZ=0 EndX=-8.2 EndY=4.70904 EndZ=0
    g22: LineSegment StartX=3.55 StartY=8.08721 StartZ=0 EndX=4.75 EndY=8.08721 EndZ=0
    g23: LineSegment StartX=3.125 StartY=10 StartZ=0 EndX=10 EndY=10 EndZ=0
    g24: LineSegment StartX=-5.5 StartY=-4.73729 StartZ=0 EndX=-8.2 EndY=-4.73729 EndZ=0
    g25: LineSegment StartX=-4.75 StartY=-5.5 StartZ=0 EndX=-2.65 EndY=-3.4 EndZ=0
    g26: LineSegment StartX=-4.75 StartY=-5.5 StartZ=0 EndX=-4.75 EndY=-8.2 EndZ=0
    g27: LineSegment StartX=4.73747 StartY=-5.5 StartZ=0 EndX=4.73747 EndY=-8.2 EndZ=0
    g28: LineSegment StartX=5.5 StartY=-4.7671 StartZ=0 EndX=8.24722 EndY=-4.7671 EndZ=0
    g29: LineSegment StartX=-3.125 StartY=-10 StartZ=0 EndX=-10 EndY=-10 EndZ=0
    g30: LineSegment StartX=-3.55 StartY=-8.2 StartZ=0 EndX=-4.75 EndY=-8.2 EndZ=0
    g31: LineSegment StartX=4.73747 StartY=-8.2 StartZ=0 EndX=3.55 EndY=-8.2 EndZ=0
    g32: LineSegment StartX=10 StartY=-3.125 StartZ=0 EndX=10 EndY=-10 EndZ=0
    g33: LineSegment StartX=8.24722 StartY=-3.55 StartZ=0 EndX=8.24722 EndY=-4.7671 EndZ=0
    g34: LineSegment StartX=-2.66166 StartY=3.4 StartZ=0 EndX=2.65 EndY=3.4 EndZ=0
    g35: LineSegment StartX=-3.4 StartY=-2.63136 StartZ=0 EndX=-5.5 EndY=-4.73729 EndZ=0
    g36: LineSegment StartX=3.4 StartY=-2.6657 StartZ=0 EndX=5.5 EndY=-4.7671 EndZ=0
    g37: LineSegment StartX=2.63162 StartY=-3.4 StartZ=0 EndX=4.73747 EndY=-5.5 EndZ=0
    g38: LineSegment StartX=-3.55 StartY=-8.2 StartZ=0 EndX=-3.125 EndY=-10 EndZ=0
    g39: LineSegment StartX=3.55 StartY=-8.2 StartZ=0 EndX=3.125 EndY=-10 EndZ=0
    g40: LineSegment StartX=-3.125 StartY=10 StartZ=0 EndX=-3.55 EndY=8.08721 EndZ=0
    g41: LineSegment StartX=3.125 StartY=10 StartZ=0 EndX=3.55 EndY=8.08721 EndZ=0
    g42: LineSegment StartX=8.24722 StartY=3.55 StartZ=0 EndX=10 EndY=3.125 EndZ=0
    g43: LineSegment StartX=10 StartY=-3.125 StartZ=0 EndX=8.24722 EndY=-3.55 EndZ=0
    g44: LineSegment StartX=-10 StartY=-3.125 StartZ=0 EndX=-8.2 EndY=-3.55 EndZ=0
    g45: LineSegment StartX=-10 StartY=3.125 StartZ=0 EndX=-8.2 EndY=3.55 EndZ=0
  constraints (61):
    c: Horizontal(g1)
    c: Vertical(g0)
    c: Vertical(g2)
    c: Coincident(g23,g4)
    c: Coincident(g32,g5)
    c: Coincident(g29,g6)
    c: Coincident(g20,g3)
    c: Horizontal(g3)
    c: Horizontal(g5)
    c: Vertical(g4)
    c: Vertical(g6)
    c: PointOnObject(g7,g-1)
    c: DistanceX(g3,g7) = 10
    c: DistanceX(g-1,g23) = 10
    c: DistanceY(g7,g3) = 10
    c: DistanceX(g3,g-1) = 10
    c: DistanceY(g32,g7) = 10
    c: Coincident(g8,g7)
    c: Radius(g8) = 2.1
    c: Horizontal(g9)
    c: Vertical(g10)
    c: Vertical(g11)
    c: Coincident(g12,g15)
    c: Horizontal(g12)
    c: Coincident(g14,g13)
    c: Vertical(g14)
    c: Coincident(g15,g0)
    c: Coincident(g13,g34)
    c: Coincident(g14,g22)
    c: Coincident(g18,g16)
    c: Vertical(g18)
    c: Coincident(g19,g17)
    c: Horizontal(g19)
    c: Coincident(g9,g18)
    c: Coincident(g21,g19)
    c: Coincident(g24,g35)
    c: Horizontal(g24)
    c: Coincident(g26,g25)
    c: Vertical(g26)
    c: Coincident(g27,g37)
    c: Vertical(g27)
    c: Coincident(g28,g36)
    c: Horizontal(g28)
    c: Coincident(g11,g24)
    c: Coincident(g26,g30)
    c: Coincident(g31,g27)
    c: Coincident(g12,g10)
    c: Coincident(g28,g33)
    c: Coincident(g25,g1)
    c: Coincident(g35,g2)
    c: Coincident(g17,g2)
    c: Coincident(g16,g34)
    c: Coincident(g1,g37)
    c: Coincident(g0,g36)
    c: Coincident(g39,g5)
    c: Coincident(g40,g3)
    c: Coincident(g42,g4)
    c: Coincident(g44,g6)
    c: Coincident(g21,g45)
    c: Coincident(g33,g43)
    c: Coincident(g10,g42)
FEATURE [PartDesign::Pad] Pad
  Direction = (2e-16,0,-1)
  Length = 300
  Length2 = 10
  Placement = pos=(0,0,0) rot=(0,1,0;1.5708rad)
  Profile = -> Sketch
  Type = 0
FEATURE [PartDesign::Fillet] Fillet
  Base = -> Pad [Edge53]
  BaseFeature = -> Pad
  Placement = pos=(0,0,0) rot=(0,1,0;1.5708rad)
  Radius = 1
  SupportTransform = false
FEATURE [PartDesign::Fillet] Fillet001
  Base = -> Fillet [Edge114]
  BaseFeature = -> Fillet
  Placement = pos=(0,0,0) rot=(0,1,0;1.5708rad)
  Radius = 1
  SupportTransform = false
FEATURE [PartDesign::Fillet] Fillet002
  Base = -> Fillet001 [Edge137,Edge95]
  BaseFeature = -> Fillet001
  Placement = pos=(0,0,0) rot=(0,1,0;1.5708rad)
  Radius = 0.5
  SupportTransform = false
FEATURE [PartDesign::Fillet] Fillet003
  Base = -> Fillet002 [Edge103]
  BaseFeature = -> Fillet002
  Placement = pos=(0,0,0) rot=(0.57735,0.57735,0.57735;2.0944rad)
  Radius = 0.5
  SupportTransform = false
FEATURE [PartDesign::Fillet] Fillet004
  Base = -> Fillet003 [Edge96]
  BaseFeature = -> Fillet003
  Placement = pos=(0,0,0) rot=(0.57735,0.57735,0.57735;2.0944rad)
  Radius = 0.5
  SupportTransform = false
FEATURE [PartDesign::Fillet] Fillet005
  Base = -> Fillet004 [Edge77]
  BaseFeature = -> Fillet004
  Placement = pos=(0,0,0) rot=(0.57735,0.57735,0.57735;2.0944rad)
  Radius = 0.5
  SupportTransform = false
FEATURE [PartDesign::Fillet] Fillet006
  Base = -> Fillet005 [Edge102]
  BaseFeature = -> Fillet005
  Placement = pos=(0,0,0) rot=(0.57735,0.57735,0.57735;2.0944rad)
  Radius = 0.5
  SupportTransform = false
FEATURE [PartDesign::Fillet] Fillet007
  Base = -> Fillet006 [Edge85]
  BaseFeature = -> Fillet006
  Placement = pos=(0,0,0) rot=(0.57735,0.57735,0.57735;2.0944rad)
  Radius = 0.5
  SupportTransform = false
FEATURE [PartDesign::Fillet] Fillet008
  Base = -> Fillet007 [Edge78]
  BaseFeature = -> Fillet007
  Placement = pos=(0,0,0) rot=(0.57735,0.57735,0.57735;2.0944rad)
  Radius = 0.5
  SupportTransform = false
FEATURE [PartDesign::Fillet] Fillet009
  Base = -> Fillet008 [Edge107]
  BaseFeature = -> Fillet008
  Placement = pos=(0,0,0) rot=(0.57735,0.57735,0.57735;2.0944rad)
  Radius = 0.5
  SupportTransform = false
FEATURE [PartDesign::Fillet] Fillet010
  Base = -> Fillet009 [Edge74]
  BaseFeature = -> Fillet009
  Radius = 0.5
  SupportTransform = false
FEATURE [PartDesign::Body] Body
  Group = -> [Sketch,Pad,Fillet,Fillet001,Fillet002,Fillet003,Fillet004,Fillet005,Fillet006,Fillet007,Fillet008,Fillet009,Fillet010]
  Origin = -> Origin001
  Placement = pos=(0,0,0) rot=(0,1,0;1.5708rad)
  Tip = -> Fillet010
FEATURE [App::Part] Part  label="2020-300-001"
  Group = -> [Body]
  Origin = -> Origin
  Placement = pos=(20,10,10) rot=(0,0,1;0rad)
FEATURE [App::Part] Part004  label="2020-300-005"
  Group = -> [Body004]
  Origin = -> Origin008
  Placement = pos=(10,10,0) rot=(0,1,0;4.71239rad)
FEATURE [Sketcher::SketchObject] Sketch005
  FullyConstrained = false
  MapMode = 5
  Support = -> [XY_Plane011]
  sketch-geometry (46):
    g0: LineSegment StartX=3.4 StartY=2.65 StartZ=0 EndX=3.4 EndY=-2.6657 EndZ=0
    g1: LineSegment StartX=2.63162 StartY=-3.4 StartZ=0 EndX=-2.65 EndY=-3.4 EndZ=0
    g2: LineSegment StartX=-3.4 StartY=-2.63136 StartZ=0 EndX=-3.4 EndY=2.61487 EndZ=0
    g3: LineSegment StartX=-10 StartY=10 StartZ=0 EndX=-3.125 EndY=10 EndZ=0
    g4: LineSegment StartX=10 StartY=10 StartZ=0 EndX=10 EndY=3.125 EndZ=0
    g5: LineSegment StartX=10 StartY=-10 StartZ=0 EndX=3.125 EndY=-10 EndZ=0
    g6: LineSegment StartX=-10 StartY=-10 StartZ=0 EndX=-10 EndY=-3.125 EndZ=0
    g7: GeomPoint X=3e-16 Y=0 Z=0
    g8: Circle CenterX=3e-16 CenterY=0 CenterZ=0 NormalX=0 NormalY=0 NormalZ=1 AngleXU=0 Radius=2.1
    g9: LineSegment StartX=-4.76483 StartY=8.08721 StartZ=0 EndX=-3.55 EndY=8.08721 EndZ=0
    g10: LineSegment StartX=8.24722 StartY=4.75 StartZ=0 EndX=8.24722 EndY=3.55 EndZ=0
    g11: LineSegment StartX=-8.2 StartY=-4.73729 StartZ=0 EndX=-8.2 EndY=-3.55 EndZ=0
    g12: LineSegment StartX=5.5 StartY=4.75 StartZ=0 EndX=8.24722 EndY=4.75 EndZ=0
    g13: LineSegment StartX=4.75 StartY=5.50457 StartZ=0 EndX=2.65 EndY=3.4 EndZ=0
    g14: LineSegment StartX=4.75 StartY=5.50457 StartZ=0 EndX=4.75 EndY=8.08721 EndZ=0
    g15: LineSegment StartX=3.4 StartY=2.65 StartZ=0 EndX=5.5 EndY=4.75 EndZ=0
    g16: LineSegment StartX=-4.76483 StartY=5.50457 StartZ=0 EndX=-2.66166 EndY=3.4 EndZ=0
    g17: LineSegment StartX=-5.5 StartY=4.70904 StartZ=0 EndX=-3.4 EndY=2.61487 EndZ=0
    g18: LineSegment StartX=-4.76483 StartY=5.50457 StartZ=0 EndX=-4.76483 EndY=8.08721 EndZ=0
    g19: LineSegment StartX=-5.5 StartY=4.70904 StartZ=0 EndX=-8.2 EndY=4.70904 EndZ=0
    g20: LineSegment StartX=-10 StartY=3.125 StartZ=0 EndX=-10 EndY=10 EndZ=0
    g21: LineSegment StartX=-8.2 StartY=3.55 StartZ=0 EndX=-8.2 EndY=4.70904 EndZ=0
    g22: LineSegment StartX=3.55 StartY=8.08721 StartZ=0 EndX=4.75 EndY=8.08721 EndZ=0
    g23: LineSegment StartX=3.125 StartY=10 StartZ=0 EndX=10 EndY=10 EndZ=0
    g24: LineSegment StartX=-5.5 StartY=-4.73729 StartZ=0 EndX=-8.2 EndY=-4.73729 EndZ=0
    g25: LineSegment StartX=-4.75 StartY=-5.5 StartZ=0 EndX=-2.65 EndY=-3.4 EndZ=0
    g26: LineSegment StartX=-4.75 StartY=-5.5 StartZ=0 EndX=-4.75 EndY=-8.2 EndZ=0
    g27: LineSegment StartX=4.73747 StartY=-5.5 StartZ=0 EndX=4.73747 EndY=-8.2 EndZ=0
    g28: LineSegment StartX=5.5 StartY=-4.7671 StartZ=0 EndX=8.24722 EndY=-4.7671 EndZ=0
    g29: LineSegment StartX=-3.125 StartY=-10 StartZ=0 EndX=-10 EndY=-10 EndZ=0
    g30: LineSegment StartX=-3.55 StartY=-8.2 StartZ=0 EndX=-4.75 EndY=-8.2 EndZ=0
    g31: LineSegment StartX=4.73747 StartY=-8.2 StartZ=0 EndX=3.55 EndY=-8.2 EndZ=0
    g32: LineSegment StartX=10 StartY=-3.125 StartZ=0 EndX=10 EndY=-10 EndZ=0
    g33: LineSegment StartX=8.24722 StartY=-3.55 StartZ=0 EndX=8.24722 EndY=-4.7671 EndZ=0
    g34: LineSegment StartX=-2.66166 StartY=3.4 StartZ=0 EndX=2.65 EndY=3.4 EndZ=0
    g35: LineSegment StartX=-3.4 StartY=-2.63136 StartZ=0 EndX=-5.5 EndY=-4.73729 EndZ=0
    g36: LineSegment StartX=3.4 StartY=-2.6657 StartZ=0 EndX=5.5 EndY=-4.7671 EndZ=0
    g37: LineSegment StartX=2.63162 StartY=-3.4 StartZ=0 EndX=4.73747 EndY=-5.5 EndZ=0
    g38: LineSegment StartX=-3.55 StartY=-8.2 StartZ=0 EndX=-3.125 EndY=-10 EndZ=0
    g39: LineSegment StartX=3.55 StartY=-8.2 StartZ=0 EndX=3.125 EndY=-10 EndZ=0
    g40: LineSegment StartX=-3.125 StartY=10 StartZ=0 EndX=-3.55 EndY=8.08721 EndZ=0
    g41: LineSegment StartX=3.125 StartY=10 StartZ=0 EndX=3.55 EndY=8.08721 EndZ=0
    g42: LineSegment StartX=8.24722 StartY=3.55 StartZ=0 EndX=10 EndY=3.125 EndZ=0
    g43: LineSegment StartX=10 StartY=-3.125 StartZ=0 EndX=8.24722 EndY=-3.55 EndZ=0
    g44: LineSegment StartX=-10 StartY=-3.125 StartZ=0 EndX=-8.2 EndY=-3.55 EndZ=0
    g45: LineSegment StartX=-10 StartY=3.125 StartZ=0 EndX=-8.2 EndY=3.55 EndZ=0
  constraints (61):
    c: Horizontal(g1)
    c: Vertical(g0)
    c: Vertical(g2)
    c: Coincident(g23,g4)
    c: Coincident(g32,g5)
    c: Coincident(g29,g6)
    c: Coincident(g20,g3)
    c: Horizontal(g3)
    c: Horizontal(g5)
    c: Vertical(g4)
    c: Vertical(g6)
    c: PointOnObject(g7,g-1)
    c: DistanceX(g3,g7) = 10
    c: DistanceX(g-1,g23) = 10
    c: DistanceY(g7,g3) = 10
    c: DistanceX(g3,g-1) = 10
    c: DistanceY(g32,g7) = 10
    c: Coincident(g8,g7)
    c: Radius(g8) = 2.1
    c: Horizontal(g9)
    c: Vertical(g10)
    c: Vertical(g11)
    c: Coincident(g12,g15)
    c: Horizontal(g12)
    c: Coincident(g14,g13)
    c: Vertical(g14)
    c: Coincident(g15,g0)
    c: Coincident(g13,g34)
    c: Coincident(g14,g22)
    c: Coincident(g18,g16)
    c: Vertical(g18)
    c: Coincident(g19,g17)
    c: Horizontal(g19)
    c: Coincident(g9,g18)
    c: Coincident(g21,g19)
    c: Coincident(g24,g35)
    c: Horizontal(g24)
    c: Coincident(g26,g25)
    c: Vertical(g26)
    c: Coincident(g27,g37)
    c: Vertical(g27)
    c: Coincident(g28,g36)
    c: Horizontal(g28)
    c: Coincident(g11,g24)
    c: Coincident(g26,g30)
    c: Coincident(g31,g27)
    c: Coincident(g12,g10)
    c: Coincident(g28,g33)
    c: Coincident(g25,g1)
    c: Coincident(g35,g2)
    c: Coincident(g17,g2)
    c: Coincident(g16,g34)
    c: Coincident(g1,g37)
    c: Coincident(g0,g36)
    c: Coincident(g39,g5)
    c: Coincident(g40,g3)
    c: Coincident(g42,g4)
    c: Coincident(g44,g6)
    c: Coincident(g21,g45)
    c: Coincident(g33,g43)
    c: Coincident(g10,g42)
FEATURE [PartDesign::Pad] Pad005
  Direction = (0,0,1)
  Length = 190
  Length2 = 10
  Profile = -> Sketch005
  Type = 0
FEATURE [PartDesign::Fillet] Fillet055
  Base = -> Pad005 [Edge53]
  BaseFeature = -> Pad005
  Radius = 1
  SupportTransform = false
FEATURE [PartDesign::Fillet] Fillet056
  Base = -> Fillet055 [Edge114]
  BaseFeature = -> Fillet055
  Radius = 1
  SupportTransform = false
FEATURE [PartDesign::Fillet] Fillet057
  Base = -> Fillet056 [Edge137,Edge95]
  BaseFeature = -> Fillet056
  Radius = 0.5
  SupportTransform = false
FEATURE [PartDesign::Fillet] Fillet058
  Base = -> Fillet057 [Edge103]
  BaseFeature = -> Fillet057
  Radius = 0.5
  SupportTransform = false
FEATURE [PartDesign::Fillet] Fillet059
  Base = -> Fillet058 [Edge96]
  BaseFeature = -> Fillet058
  Radius = 0.5
  SupportTransform = false
FEATURE [PartDesign::Fillet] Fillet060
  Base = -> Fillet059 [Edge77]
  BaseFeature = -> Fillet059
  Radius = 0.5
  SupportTransform = false
FEATURE [PartDesign::Fillet] Fillet061
  Base = -> Fillet060 [Edge102]
  BaseFeature = -> Fillet060
  Radius = 0.5
  SupportTransform = false
FEATURE [PartDesign::Fillet] Fillet062
  Base = -> Fillet061 [Edge85]
  BaseFeature = -> Fillet061
  Radius = 0.5
  SupportTransform = false
FEATURE [PartDesign::Fillet] Fillet063
  Base = -> Fillet062 [Edge78]
  BaseFeature = -> Fillet062
  Radius = 0.5
  SupportTransform = false
FEATURE [PartDesign::Fillet] Fillet064
  Base = -> Fillet063 [Edge107]
  BaseFeature = -> Fillet063
  Radius = 0.5
  SupportTransform = false
FEATURE [PartDesign::Fillet] Fillet065
  Base = -> Fillet064 [Edge74]
  BaseFeature = -> Fillet064
  Radius = 0.5
  SupportTransform = false
FEATURE [PartDesign::Body] Body005
  Group = -> [Sketch005,Pad005,Fillet055,Fillet056,Fillet057,Fillet058,Fillet059,Fillet060,Fillet061,Fillet062,Fillet063,Fillet064,Fillet065]
  Origin = -> Origin011
  Placement = pos=(0,0,0) rot=(0,1,0;1.5708rad)
  Tip = -> Fillet065
FEATURE [App::Part] Part005  label="2020-300-006"
  Group = -> [Body005]
  Origin = -> Origin010
  Placement = pos=(10,330,0) rot=(0,1,0;4.71239rad)
FEATURE [Sketcher::SketchObject] Sketch006
  FullyConstrained = false
  MapMode = 5
  Support = -> [XY_Plane013]
  sketch-geometry (46):
    g0: LineSegment StartX=3.4 StartY=2.65 StartZ=0 EndX=3.4 EndY=-2.6657 EndZ=0
    g1: LineSegment StartX=2.63162 StartY=-3.4 StartZ=0 EndX=-2.65 EndY=-3.4 EndZ=0
    g2: LineSegment StartX=-3.4 StartY=-2.63136 StartZ=0 EndX=-3.4 EndY=2.61487 EndZ=0
    g3: LineSegment StartX=-10 StartY=10 StartZ=0 EndX=-3.125 EndY=10 EndZ=0
    g4: LineSegment StartX=10 StartY=10 StartZ=0 EndX=10 EndY=3.125 EndZ=0
    g5: LineSegment StartX=10 StartY=-10 StartZ=0 EndX=3.125 EndY=-10 EndZ=0
    g6: LineSegment StartX=-10 StartY=-10 StartZ=0 EndX=-10 EndY=-3.125 EndZ=0
    g7: GeomPoint X=3e-16 Y=0 Z=0
    g8: Circle CenterX=3e-16 CenterY=0 CenterZ=0 NormalX=0 NormalY=0 NormalZ=1 AngleXU=0 Radius=2.1
    g9: LineSegment StartX=-4.76483 StartY=8.08721 StartZ=0 EndX=-3.55 EndY=8.08721 EndZ=0
    g10: LineSegment StartX=8.24722 StartY=4.75 StartZ=0 EndX=8.24722 EndY=3.55 EndZ=0
    g11: LineSegment StartX=-8.2 StartY=-4.73729 StartZ=0 EndX=-8.2 EndY=-3.55 EndZ=0
    g12: LineSegment StartX=5.5 StartY=4.75 StartZ=0 EndX=8.24722 EndY=4.75 EndZ=0
    g13: LineSegment StartX=4.75 StartY=5.50457 StartZ=0 EndX=2.65 EndY=3.4 EndZ=0
    g14: LineSegment StartX=4.75 StartY=5.50457 StartZ=0 EndX=4.75 EndY=8.08721 EndZ=0
    g15: LineSegment StartX=3.4 StartY=2.65 StartZ=0 EndX=5.5 EndY=4.75 EndZ=0
    g16: LineSegment StartX=-4.76483 StartY=5.50457 StartZ=0 EndX=-2.66166 EndY=3.4 EndZ=0
    g17: LineSegment StartX=-5.5 StartY=4.70904 StartZ=0 EndX=-3.4 EndY=2.61487 EndZ=0
    g18: LineSegment StartX=-4.76483 StartY=5.50457 StartZ=0 EndX=-4.76483 EndY=8.08721 EndZ=0
    g19: LineSegment StartX=-5.5 StartY=4.70904 StartZ=0 EndX=-8.2 EndY=4.70904 EndZ=0
    g20: LineSegment StartX=-10 StartY=3.125 StartZ=0 EndX=-10 EndY=10 EndZ=0
    g21: LineSegment StartX=-8.2 StartY=3.55 StartZ=0 EndX=-8.2 EndY=4.70904 EndZ=0
    g22: LineSegment StartX=3.55 StartY=8.08721 StartZ=0 EndX=4.75 EndY=8.08721 EndZ=0
    g23: LineSegment StartX=3.125 StartY=10 StartZ=0 EndX=10 EndY=10 EndZ=0
    g24: LineSegment StartX=-5.5 StartY=-4.73729 StartZ=0 EndX=-8.2 EndY=-4.73729 EndZ=0
    g25: LineSegment StartX=-4.75 StartY=-5.5 StartZ=0 EndX=-2.65 EndY=-3.4 EndZ=0
    g26: LineSegment StartX=-4.75 StartY=-5.5 StartZ=0 EndX=-4.75 EndY=-8.2 EndZ=0
    g27: LineSegment StartX=4.73747 StartY=-5.5 StartZ=0 EndX=4.73747 EndY=-8.2 EndZ=0
    g28: LineSegment StartX=5.5 StartY=-4.7671 StartZ=0 EndX=8.24722 EndY=-4.7671 EndZ=0
    g29: LineSegment StartX=-3.125 StartY=-10 StartZ=0 EndX=-10 EndY=-10 EndZ=0
    g30: LineSegment StartX=-3.55 StartY=-8.2 StartZ=0 EndX=-4.75 EndY=-8.2 EndZ=0
    g31: LineSegment StartX=4.73747 StartY=-8.2 StartZ=0 EndX=3.55 EndY=-8.2 EndZ=0
    g32: LineSegment StartX=10 StartY=-3.125 StartZ=0 EndX=10 EndY=-10 EndZ=0
    g33: LineSegment StartX=8.24722 StartY=-3.55 StartZ=0 EndX=8.24722 EndY=-4.7671 EndZ=0
    g34: LineSegment StartX=-2.66166 StartY=3.4 StartZ=0 EndX=2.65 EndY=3.4 EndZ=0
    g35: LineSegment StartX=-3.4 StartY=-2.63136 StartZ=0 EndX=-5.5 EndY=-4.73729 EndZ=0
    g36: LineSegment StartX=3.4 StartY=-2.6657 StartZ=0 EndX=5.5 EndY=-4.7671 EndZ=0
    g37: LineSegment StartX=2.63162 StartY=-3.4 StartZ=0 EndX=4.73747 EndY=-5.5 EndZ=0
    g38: LineSegment StartX=-3.55 StartY=-8.2 StartZ=0 EndX=-3.125 EndY=-10 EndZ=0
    g39: LineSegment StartX=3.55 StartY=-8.2 StartZ=0 EndX=3.125 EndY=-10 EndZ=0
    g40: LineSegment StartX=-3.125 StartY=10 StartZ=0 EndX=-3.55 EndY=8.08721 EndZ=0
    g41: LineSegment StartX=3.125 StartY=10 StartZ=0 EndX=3.55 EndY=8.08721 EndZ=0
    g42: LineSegment StartX=8.24722 StartY=3.55 StartZ=0 EndX=10 EndY=3.125 EndZ=0
    g43: LineSegment StartX=10 StartY=-3.125 StartZ=0 EndX=8.24722 EndY=-3.55 EndZ=0
    g44: LineSegment StartX=-10 StartY=-3.125 StartZ=0 EndX=-8.2 EndY=-3.55 EndZ=0
    g45: LineSegment StartX=-10 StartY=3.125 StartZ=0 EndX=-8.2 EndY=3.55 EndZ=0
  constraints (61):
    c: Horizontal(g1)
    c: Vertical(g0)
    c: Vertical(g2)
    c: Coincident(g23,g4)
    c: Coincident(g32,g5)
    c: Coincident(g29,g6)
    c: Coincident(g20,g3)
    c: Horizontal(g3)
    c: Horizontal(g5)
    c: Vertical(g4)
    c: Vertical(g6)
    c: PointOnObject(g7,g-1)
    c: DistanceX(g3,g7) = 10
    c: DistanceX(g-1,g23) = 10
    c: DistanceY(g7,g3) = 10
    c: DistanceX(g3,g-1) = 10
    c: DistanceY(g32,g7) = 10
    c: Coincident(g8,g7)
    c: Radius(g8) = 2.1
    c: Horizontal(g9)
    c: Vertical(g10)
    c: Vertical(g11)
    c: Coincident(g12,g15)
    c: Horizontal(g12)
    c: Coincident(g14,g13)
    c: Vertical(g14)
    c: Coincident(g15,g0)
    c: Coincident(g13,g34)
    c: Coincident(g14,g22)
    c: Coincident(g18,g16)
    c: Vertical(g18)
    c: Coincident(g19,g17)
    c: Horizontal(g19)
    c: Coincident(g9,g18)
    c: Coincident(g21,g19)
    c: Coincident(g24,g35)
    c: Horizontal(g24)
    c: Coincident(g26,g25)
    c: Vertical(g26)
    c: Coincident(g27,g37)
    c: Vertical(g27)
    c: Coincident(g28,g36)
    c: Horizontal(g28)
    c: Coincident(g11,g24)
    c: Coincident(g26,g30)
    c: Coincident(g31,g27)
    c: Coincident(g12,g10)
    c: Coincident(g28,g33)
    c: Coincident(g25,g1)
    c: Coincident(g35,g2)
    c: Coincident(g17,g2)
    c: Coincident(g16,g34)
    c: Coincident(g1,g37)
    c: Coincident(g0,g36)
    c: Coincident(g39,g5)
    c: Coincident(g40,g3)
    c: Coincident(g42,g4)
    c: Coincident(g44,g6)
    c: Coincident(g21,g45)
    c: Coincident(g33,g43)
    c: Coincident(g10,g42)
FEATURE [PartDesign::Pad] Pad006
  Direction = (0,0,1)
  Length = 190
  Length2 = 10
  Profile = -> Sketch006
  Type = 0
FEATURE [PartDesign::Fillet] Fillet066
  Base = -> Pad006 [Edge53]
  BaseFeature = -> Pad006
  Radius = 1
  SupportTransform = false
FEATURE [PartDesign::Fillet] Fillet067
  Base = -> Fillet066 [Edge114]
  BaseFeature = -> Fillet066
  Radius = 1
  SupportTransform = false
FEATURE [PartDesign::Fillet] Fillet068
  Base = -> Fillet067 [Edge137,Edge95]
  BaseFeature = -> Fillet067
  Radius = 0.5
  SupportTransform = false
FEATURE [PartDesign::Fillet] Fillet069
  Base = -> Fillet068 [Edge103]
  BaseFeature = -> Fillet068
  Radius = 0.5
  SupportTransform = false
FEATURE [PartDesign::Fillet] Fillet070
  Base = -> Fillet069 [Edge96]
  BaseFeature = -> Fillet069
  Radius = 0.5
  SupportTransform = false
FEATURE [PartDesign::Fillet] Fillet071
  Base = -> Fillet070 [Edge77]
  BaseFeature = -> Fillet070
  Radius = 0.5
  SupportTransform = false
FEATURE [PartDesign::Fillet] Fillet072
  Base = -> Fillet071 [Edge102]
  BaseFeature = -> Fillet071
  Radius = 0.5
  SupportTransform = false
FEATURE [PartDesign::Fillet] Fillet073
  Base = -> Fillet072 [Edge85]
  BaseFeature = -> Fillet072
  Radius = 0.5
  SupportTransform = false
FEATURE [PartDesign::Fillet] Fillet074
  Base = -> Fillet073 [Edge78]
  BaseFeature = -> Fillet073
  Radius = 0.5
  SupportTransform = false
FEATURE [PartDesign::Fillet] Fillet075
  Base = -> Fillet074 [Edge107]
  BaseFeature = -> Fillet074
  Radius = 0.5
  SupportTransform = false
FEATURE [PartDesign::Fillet] Fillet076
  Base = -> Fillet075 [Edge74]
  BaseFeature = -> Fillet075
  Radius = 0.5
  SupportTransform = false
FEATURE [PartDesign::Body] Body006
  Group = -> [Sketch006,Pad006,Fillet066,Fillet067,Fillet068,Fillet069,Fillet070,Fillet071,Fillet072,Fillet073,Fillet074,Fillet075,Fillet076]
  Origin = -> Origin013
  Placement = pos=(0,0,0) rot=(0,1,0;1.5708rad)
  Tip = -> Fillet076
FEATURE [App::Part] Part006  label="2020-300-007"
  Group = -> [Body006]
  Origin = -> Origin012
  Placement = pos=(330,10,0) rot=(0,1,0;4.71239rad)
FEATURE [Sketcher::SketchObject] Sketch007
  FullyConstrained = false
  MapMode = 5
  Support = -> [XY_Plane015]
  sketch-geometry (46):
    g0: LineSegment StartX=3.4 StartY=2.65 StartZ=0 EndX=3.4 EndY=-2.6657 EndZ=0
    g1: LineSegment StartX=2.63162 StartY=-3.4 StartZ=0 EndX=-2.65 EndY=-3.4 EndZ=0
    g2: LineSegment StartX=-3.4 StartY=-2.63136 StartZ=0 EndX=-3.4 EndY=2.61487 EndZ=0
    g3: LineSegment StartX=-10 StartY=10 StartZ=0 EndX=-3.125 EndY=10 EndZ=0
    g4: LineSegment StartX=10 StartY=10 StartZ=0 EndX=10 EndY=3.125 EndZ=0
    g5: LineSegment StartX=10 StartY=-10 StartZ=0 EndX=3.125 EndY=-10 EndZ=0
    g6: LineSegment StartX=-10 StartY=-10 StartZ=0 EndX=-10 EndY=-3.125 EndZ=0
    g7: GeomPoint X=3e-16 Y=0 Z=0
    g8: Circle CenterX=3e-16 CenterY=0 CenterZ=0 NormalX=0 NormalY=0 NormalZ=1 AngleXU=0 Radius=2.1
    g9: LineSegment StartX=-4.76483 StartY=8.08721 StartZ=0 EndX=-3.55 EndY=8.08721 EndZ=0
    g10: LineSegment StartX=8.24722 StartY=4.75 StartZ=0 EndX=8.24722 EndY=3.55 EndZ=0
    g11: LineSegment StartX=-8.2 StartY=-4.73729 StartZ=0 EndX=-8.2 EndY=-3.55 EndZ=0
    g12: LineSegment StartX=5.5 StartY=4.75 StartZ=0 EndX=8.24722 EndY=4.75 EndZ=0
    g13: LineSegment StartX=4.75 StartY=5.50457 StartZ=0 EndX=2.65 EndY=3.4 EndZ=0
    g14: LineSegment StartX=4.75 StartY=5.50457 StartZ=0 EndX=4.75 EndY=8.08721 EndZ=0
    g15: LineSegment StartX=3.4 StartY=2.65 StartZ=0 EndX=5.5 EndY=4.75 EndZ=0
    g16: LineSegment StartX=-4.76483 StartY=5.50457 StartZ=0 EndX=-2.66166 EndY=3.4 EndZ=0
    g17: LineSegment StartX=-5.5 StartY=4.70904 StartZ=0 EndX=-3.4 EndY=2.61487 EndZ=0
    g18: LineSegment StartX=-4.76483 StartY=5.50457 StartZ=0 EndX=-4.76483 EndY=8.08721 EndZ=0
    g19: LineSegment StartX=-5.5 StartY=4.70904 StartZ=0 EndX=-8.2 EndY=4.70904 EndZ=0
    g20: LineSegment StartX=-10 StartY=3.125 StartZ=0 EndX=-10 EndY=10 EndZ=0
    g21: LineSegment StartX=-8.2 StartY=3.55 StartZ=0 EndX=-8.2 EndY=4.70904 EndZ=0
    g22: LineSegment StartX=3.55 StartY=8.08721 StartZ=0 EndX=4.75 EndY=8.08721 EndZ=0
    g23: LineSegment StartX=3.125 StartY=10 StartZ=0 EndX=10 EndY=10 EndZ=0
    g24: LineSegment StartX=-5.5 StartY=-4.73729 StartZ=0 EndX=-8.2 EndY=-4.73729 EndZ=0
    g25: LineSegment StartX=-4.75 StartY=-5.5 StartZ=0 EndX=-2.65 EndY=-3.4 EndZ=0
    g26: LineSegment StartX=-4.75 StartY=-5.5 StartZ=0 EndX=-4.75 EndY=-8.2 EndZ=0
    g27: LineSegment StartX=4.73747 StartY=-5.5 StartZ=0 EndX=4.73747 EndY=-8.2 EndZ=0
    g28: LineSegment StartX=5.5 StartY=-4.7671 StartZ=0 EndX=8.24722 EndY=-4.7671 EndZ=0
    g29: LineSegment StartX=-3.125 StartY=-10 StartZ=0 EndX=-10 EndY=-10 EndZ=0
    g30: LineSegment StartX=-3.55 StartY=-8.2 StartZ=0 EndX=-4.75 EndY=-8.2 EndZ=0
    g31: LineSegment StartX=4.73747 StartY=-8.2 StartZ=0 EndX=3.55 EndY=-8.2 EndZ=0
    g32: LineSegment StartX=10 StartY=-3.125 StartZ=0 EndX=10 EndY=-10 EndZ=0
    g33: LineSegment StartX=8.24722 StartY=-3.55 StartZ=0 EndX=8.24722 EndY=-4.7671 EndZ=0
    g34: LineSegment StartX=-2.66166 StartY=3.4 StartZ=0 EndX=2.65 EndY=3.4 EndZ=0
    g35: LineSegment StartX=-3.4 StartY=-2.63136 StartZ=0 EndX=-5.5 EndY=-4.73729 EndZ=0
    g36: LineSegment StartX=3.4 StartY=-2.6657 StartZ=0 EndX=5.5 EndY=-4.7671 EndZ=0
    g37: LineSegment StartX=2.63162 StartY=-3.4 StartZ=0 EndX=4.73747 EndY=-5.5 EndZ=0
    g38: LineSegment StartX=-3.55 StartY=-8.2 StartZ=0 EndX=-3.125 EndY=-10 EndZ=0
    g39: LineSegment StartX=3.55 StartY=-8.2 StartZ=0 EndX=3.125 EndY=-10 EndZ=0
    g40: LineSegment StartX=-3.125 StartY=10 StartZ=0 EndX=-3.55 EndY=8.08721 EndZ=0
    g41: LineSegment StartX=3.125 StartY=10 StartZ=0 EndX=3.55 EndY=8.08721 EndZ=0
    g42: LineSegment StartX=8.24722 StartY=3.55 StartZ=0 EndX=10 EndY=3.125 EndZ=0
    g43: LineSegment StartX=10 StartY=-3.125 StartZ=0 EndX=8.24722 EndY=-3.55 EndZ=0
    g44: LineSegment StartX=-10 StartY=-3.125 StartZ=0 EndX=-8.2 EndY=-3.55 EndZ=0
    g45: LineSegment StartX=-10 StartY=3.125 StartZ=0 EndX=-8.2 EndY=3.55 EndZ=0
  constraints (61):
    c: Horizontal(g1)
    c: Vertical(g0)
    c: Vertical(g2)
    c: Coincident(g23,g4)
    c: Coincident(g32,g5)
    c: Coincident(g29,g6)
    c: Coincident(g20,g3)
    c: Horizontal(g3)
    c: Horizontal(g5)
    c: Vertical(g4)
    c: Vertical(g6)
    c: PointOnObject(g7,g-1)
    c: DistanceX(g3,g7) = 10
    c: DistanceX(g-1,g23) = 10
    c: DistanceY(g7,g3) = 10
    c: DistanceX(g3,g-1) = 10
    c: DistanceY(g32,g7) = 10
    c: Coincident(g8,g7)
    c: Radius(g8) = 2.1
    c: Horizontal(g9)
    c: Vertical(g10)
    c: Vertical(g11)
    c: Coincident(g12,g15)
    c: Horizontal(g12)
    c: Coincident(g14,g13)
    c: Vertical(g14)
    c: Coincident(g15,g0)
    c: Coincident(g13,g34)
    c: Coincident(g14,g22)
    c: Coincident(g18,g16)
    c: Vertical(g18)
    c: Coincident(g19,g17)
    c: Horizontal(g19)
    c: Coincident(g9,g18)
    c: Coincident(g21,g19)
    c: Coincident(g24,g35)
    c: Horizontal(g24)
    c: Coincident(g26,g25)
    c: Vertical(g26)
    c: Coincident(g27,g37)
    c: Vertical(g27)
    c: Coincident(g28,g36)
    c: Horizontal(g28)
    c: Coincident(g11,g24)
    c: Coincident(g26,g30)
    c: Coincident(g31,g27)
    c: Coincident(g12,g10)
    c: Coincident(g28,g33)
    c: Coincident(g25,g1)
    c: Coincident(g35,g2)
    c: Coincident(g17,g2)
    c: Coincident(g16,g34)
    c: Coincident(g1,g37)
    c: Coincident(g0,g36)
    c: Coincident(g39,g5)
    c: Coincident(g40,g3)
    c: Coincident(g42,g4)
    c: Coincident(g44,g6)
    c: Coincident(g21,g45)
    c: Coincident(g33,g43)
    c: Coincident(g10,g42)
FEATURE [PartDesign::Pad] Pad007
  Direction = (0,0,1)
  Length = 190
  Length2 = 10
  Profile = -> Sketch007
  Type = 0
FEATURE [PartDesign::Fillet] Fillet077
  Base = -> Pad007 [Edge53]
  BaseFeature = -> Pad007
  Radius = 1
  SupportTransform = false
FEATURE [PartDesign::Fillet] Fillet078
  Base = -> Fillet077 [Edge114]
  BaseFeature = -> Fillet077
  Radius = 1
  SupportTransform = false
FEATURE [PartDesign::Fillet] Fillet079
  Base = -> Fillet078 [Edge137,Edge95]
  BaseFeature = -> Fillet078
  Radius = 0.5
  SupportTransform = false
FEATURE [PartDesign::Fillet] Fillet080
  Base = -> Fillet079 [Edge103]
  BaseFeature = -> Fillet079
  Radius = 0.5
  SupportTransform = false
FEATURE [PartDesign::Fillet] Fillet081
  Base = -> Fillet080 [Edge96]
  BaseFeature = -> Fillet080
  Radius = 0.5
  SupportTransform = false
FEATURE [PartDesign::Fillet] Fillet082
  Base = -> Fillet081 [Edge77]
  BaseFeature = -> Fillet081
  Radius = 0.5
  SupportTransform = false
FEATURE [PartDesign::Fillet] Fillet083
  Base = -> Fillet082 [Edge102]
  BaseFeature = -> Fillet082
  Radius = 0.5
  SupportTransform = false
FEATURE [PartDesign::Fillet] Fillet084
  Base = -> Fillet083 [Edge85]
  BaseFeature = -> Fillet083
  Radius = 0.5
  SupportTransform = false
FEATURE [PartDesign::Fillet] Fillet085
  Base = -> Fillet084 [Edge78]
  BaseFeature = -> Fillet084
  Radius = 0.5
  SupportTransform = false
FEATURE [PartDesign::Fillet] Fillet086
  Base = -> Fillet085 [Edge107]
  BaseFeature = -> Fillet085
  Radius = 0.5
  SupportTransform = false
FEATURE [PartDesign::Fillet] Fillet087
  Base = -> Fillet086 [Edge74]
  BaseFeature = -> Fillet086
  Radius = 0.5
  SupportTransform = false
FEATURE [PartDesign::Body] Body007
  Group = -> [Sketch007,Pad007,Fillet077,Fillet078,Fillet079,Fillet080,Fillet081,Fillet082,Fillet083,Fillet084,Fillet085,Fillet086,Fillet087]
  Origin = -> Origin015
  Placement = pos=(0,0,0) rot=(0,1,0;1.5708rad)
  Tip = -> Fillet087
FEATURE [App::Part] Part007  label="2020-300-008"
  Group = -> [Body007]
  Origin = -> Origin014
  Placement = pos=(330,330,0) rot=(0,1,0;4.71239rad)
FEATURE [Sketcher::SketchObject] Sketch008
  FullyConstrained = false
  MapMode = 5
  Support = -> [XY_Plane017]
  sketch-geometry (46):
    g0: LineSegment StartX=3.4 StartY=2.65 StartZ=0 EndX=3.4 EndY=-2.6657 EndZ=0
    g1: LineSegment StartX=2.63162 StartY=-3.4 StartZ=0 EndX=-2.65 EndY=-3.4 EndZ=0
    g2: LineSegment StartX=-3.4 StartY=-2.63136 StartZ=0 EndX=-3.4 EndY=2.61487 EndZ=0
    g3: LineSegment StartX=-10 StartY=10 StartZ=0 EndX=-3.125 EndY=10 EndZ=0
    g4: LineSegment StartX=10 StartY=10 StartZ=0 EndX=10 EndY=3.125 EndZ=0
    g5: LineSegment StartX=10 StartY=-10 StartZ=0 EndX=3.125 EndY=-10 EndZ=0
    g6: LineSegment StartX=-10 StartY=-10 StartZ=0 EndX=-10 EndY=-3.125 EndZ=0
    g7: GeomPoint X=3e-16 Y=0 Z=0
    g8: Circle CenterX=3e-16 CenterY=0 CenterZ=0 NormalX=0 NormalY=0 NormalZ=1 AngleXU=0 Radius=2.1
    g9: LineSegment StartX=-4.76483 StartY=8.08721 StartZ=0 EndX=-3.55 EndY=8.08721 EndZ=0
    g10: LineSegment StartX=8.24722 StartY=4.75 StartZ=0 EndX=8.24722 EndY=3.55 EndZ=0
    g11: LineSegment StartX=-8.2 StartY=-4.73729 StartZ=0 EndX=-8.2 EndY=-3.55 EndZ=0
    g12: LineSegment StartX=5.5 StartY=4.75 StartZ=0 EndX=8.24722 EndY=4.75 EndZ=0
    g13: LineSegment StartX=4.75 StartY=5.50457 StartZ=0 EndX=2.65 EndY=3.4 EndZ=0
    g14: LineSegment StartX=4.75 StartY=5.50457 StartZ=0 EndX=4.75 EndY=8.08721 EndZ=0
    g15: LineSegment StartX=3.4 StartY=2.65 StartZ=0 EndX=5.5 EndY=4.75 EndZ=0
    g16: LineSegment StartX=-4.76483 StartY=5.50457 StartZ=0 EndX=-2.66166 EndY=3.4 EndZ=0
    g17: LineSegment StartX=-5.5 StartY=4.70904 StartZ=0 EndX=-3.4 EndY=2.61487 EndZ=0
    g18: LineSegment StartX=-4.76483 StartY=5.50457 StartZ=0 EndX=-4.76483 EndY=8.08721 EndZ=0
    g19: LineSegment StartX=-5.5 StartY=4.70904 StartZ=0 EndX=-8.2 EndY=4.70904 EndZ=0
    g20: LineSegment StartX=-10 StartY=3.125 StartZ=0 EndX=-10 EndY=10 EndZ=0
    g21: LineSegment StartX=-8.2 StartY=3.55 StartZ=0 EndX=-8.2 EndY=4.70904 EndZ=0
    g22: LineSegment StartX=3.55 StartY=8.08721 StartZ=0 EndX=4.75 EndY=8.08721 EndZ=0
    g23: LineSegment StartX=3.125 StartY=10 StartZ=0 EndX=10 EndY=10 EndZ=0
    g24: LineSegment StartX=-5.5 StartY=-4.73729 StartZ=0 EndX=-8.2 EndY=-4.73729 EndZ=0
    g25: LineSegment StartX=-4.75 StartY=-5.5 StartZ=0 EndX=-2.65 EndY=-3.4 EndZ=0
    g26: LineSegment StartX=-4.75 StartY=-5.5 StartZ=0 EndX=-4.75 EndY=-8.2 EndZ=0
    g27: LineSegment StartX=4.73747 StartY=-5.5 StartZ=0 EndX=4.73747 EndY=-8.2 EndZ=0
    g28: LineSegment StartX=5.5 StartY=-4.7671 StartZ=0 EndX=8.24722 EndY=-4.7671 EndZ=0
    g29: LineSegment StartX=-3.125 StartY=-10 StartZ=0 EndX=-10 EndY=-10 EndZ=0
    g30: LineSegment StartX=-3.55 StartY=-8.2 StartZ=0 EndX=-4.75 EndY=-8.2 EndZ=0
    g31: LineSegment StartX=4.73747 StartY=-8.2 StartZ=0 EndX=3.55 EndY=-8.2 EndZ=0
    g32: LineSegment StartX=10 StartY=-3.125 StartZ=0 EndX=10 EndY=-10 EndZ=0
    g33: LineSegment StartX=8.24722 StartY=-3.55 StartZ=0 EndX=8.24722 EndY=-4.7671 EndZ=0
    g34: LineSegment StartX=-2.66166 StartY=3.4 StartZ=0 EndX=2.65 EndY=3.4 EndZ=0
    g35: LineSegment StartX=-3.4 StartY=-2.63136 StartZ=0 EndX=-5.5 EndY=-4.73729 EndZ=0
    g36: LineSegment StartX=3.4 StartY=-2.6657 StartZ=0 EndX=5.5 EndY=-4.7671 EndZ=0
    g37: LineSegment StartX=2.63162 StartY=-3.4 StartZ=0 EndX=4.73747 EndY=-5.5 EndZ=0
    g38: LineSegment StartX=-3.55 StartY=-8.2 StartZ=0 EndX=-3.125 EndY=-10 EndZ=0
    g39: LineSegment StartX=3.55 StartY=-8.2 StartZ=0 EndX=3.125 EndY=-10 EndZ=0
    g40: LineSegment StartX=-3.125 StartY=10 StartZ=0 EndX=-3.55 EndY=8.08721 EndZ=0
    g41: LineSegment StartX=3.125 StartY=10 StartZ=0 EndX=3.55 EndY=8.08721 EndZ=0
    g42: LineSegment StartX=8.24722 StartY=3.55 StartZ=0 EndX=10 EndY=3.125 EndZ=0
    g43: LineSegment StartX=10 StartY=-3.125 StartZ=0 EndX=8.24722 EndY=-3.55 EndZ=0
    g44: LineSegment StartX=-10 StartY=-3.125 StartZ=0 EndX=-8.2 EndY=-3.55 EndZ=0
    g45: LineSegment StartX=-10 StartY=3.125 StartZ=0 EndX=-8.2 EndY=3.55 EndZ=0
  constraints (61):
    c: Horizontal(g1)
    c: Vertical(g0)
    c: Vertical(g2)
    c: Coincident(g23,g4)
    c: Coincident(g32,g5)
    c: Coincident(g29,g6)
    c: Coincident(g20,g3)
    c: Horizontal(g3)
    c: Horizontal(g5)
    c: Vertical(g4)
    c: Vertical(g6)
    c: PointOnObject(g7,g-1)
    c: DistanceX(g3,g7) = 10
    c: DistanceX(g-1,g23) = 10
    c: DistanceY(g7,g3) = 10
    c: DistanceX(g3,g-1) = 10
    c: DistanceY(g32,g7) = 10
    c: Coincident(g8,g7)
    c: Radius(g8) = 2.1
    c: Horizontal(g9)
    c: Vertical(g10)
    c: Vertical(g11)
    c: Coincident(g12,g15)
    c: Horizontal(g12)
    c: Coincident(g14,g13)
    c: Vertical(g14)
    c: Coincident(g15,g0)
    c: Coincident(g13,g34)
    c: Coincident(g14,g22)
    c: Coincident(g18,g16)
    c: Vertical(g18)
    c: Coincident(g19,g17)
    c: Horizontal(g19)
    c: Coincident(g9,g18)
    c: Coincident(g21,g19)
    c: Coincident(g24,g35)
    c: Horizontal(g24)
    c: Coincident(g26,g25)
    c: Vertical(g26)
    c: Coincident(g27,g37)
    c: Vertical(g27)
    c: Coincident(g28,g36)
    c: Horizontal(g28)
    c: Coincident(g11,g24)
    c: Coincident(g26,g30)
    c: Coincident(g31,g27)
    c: Coincident(g12,g10)
    c: Coincident(g28,g33)
    c: Coincident(g25,g1)
    c: Coincident(g35,g2)
    c: Coincident(g17,g2)
    c: Coincident(g16,g34)
    c: Coincident(g1,g37)
    c: Coincident(g0,g36)
    c: Coincident(g39,g5)
    c: Coincident(g40,g3)
    c: Coincident(g42,g4)
    c: Coincident(g44,g6)
    c: Coincident(g21,g45)
    c: Coincident(g33,g43)
    c: Coincident(g10,g42)
FEATURE [PartDesign::Pad] Pad008
  Direction = (0,0,1)
  Length = 300
  Length2 = 10
  Profile = -> Sketch008
  Type = 0
FEATURE [PartDesign::Fillet] Fillet088
  Base = -> Pad008 [Edge53]
  BaseFeature = -> Pad008
  Radius = 1
  SupportTransform = false
FEATURE [PartDesign::Fillet] Fillet089
  Base = -> Fillet088 [Edge114]
  BaseFeature = -> Fillet088
  Radius = 1
  SupportTransform = false
FEATURE [PartDesign::Fillet] Fillet090
  Base = -> Fillet089 [Edge137,Edge95]
  BaseFeature = -> Fillet089
  Radius = 0.5
  SupportTransform = false
FEATURE [PartDesign::Fillet] Fillet091
  Base = -> Fillet090 [Edge103]
  BaseFeature = -> Fillet090
  Radius = 0.5
  SupportTransform = false
FEATURE [PartDesign::Fillet] Fillet092
  Base = -> Fillet091 [Edge96]
  BaseFeature = -> Fillet091
  Radius = 0.5
  SupportTransform = false
FEATURE [PartDesign::Fillet] Fillet093
  Base = -> Fillet092 [Edge77]
  BaseFeature = -> Fillet092
  Radius = 0.5
  SupportTransform = false
FEATURE [PartDesign::Fillet] Fillet094
  Base = -> Fillet093 [Edge102]
  BaseFeature = -> Fillet093
  Radius = 0.5
  SupportTransform = false
FEATURE [PartDesign::Fillet] Fillet095
  Base = -> Fillet094 [Edge85]
  BaseFeature = -> Fillet094
  Radius = 0.5
  SupportTransform = false
FEATURE [PartDesign::Fillet] Fillet096
  Base = -> Fillet095 [Edge78]
  BaseFeature = -> Fillet095
  Radius = 0.5
  SupportTransform = false
FEATURE [PartDesign::Fillet] Fillet097
  Base = -> Fillet096 [Edge107]
  BaseFeature = -> Fillet096
  Radius = 0.5
  SupportTransform = false
FEATURE [PartDesign::Fillet] Fillet098
  Base = -> Fillet097 [Edge74]
  BaseFeature = -> Fillet097
  Radius = 0.5
  SupportTransform = false
FEATURE [PartDesign::Body] Body008
  Group = -> [Sketch008,Pad008,Fillet088,Fillet089,Fillet090,Fillet091,Fillet092,Fillet093,Fillet094,Fillet095,Fillet096,Fillet097,Fillet098]
  Origin = -> Origin017
  Placement = pos=(0,0,0) rot=(0,1,0;1.5708rad)
  Tip = -> Fillet098
FEATURE [App::Part] Part008  label="2020-300-009"
  Group = -> [Body008]
  Origin = -> Origin016
  Placement = pos=(20,330,180) rot=(0,0,1;0rad)
FEATURE [Sketcher::SketchObject] Sketch009
  FullyConstrained = false
  MapMode = 5
  Support = -> [XY_Plane019]
  sketch-geometry (46):
    g0: LineSegment StartX=3.4 StartY=2.65 StartZ=0 EndX=3.4 EndY=-2.6657 EndZ=0
    g1: LineSegment StartX=2.63162 StartY=-3.4 StartZ=0 EndX=-2.65 EndY=-3.4 EndZ=0
    g2: LineSegment StartX=-3.4 StartY=-2.63136 StartZ=0 EndX=-3.4 EndY=2.61487 EndZ=0
    g3: LineSegment StartX=-10 StartY=10 StartZ=0 EndX=-3.125 EndY=10 EndZ=0
    g4: LineSegment StartX=10 StartY=10 StartZ=0 EndX=10 EndY=3.125 EndZ=0
    g5: LineSegment StartX=10 StartY=-10 StartZ=0 EndX=3.125 EndY=-10 EndZ=0
    g6: LineSegment StartX=-10 StartY=-10 StartZ=0 EndX=-10 EndY=-3.125 EndZ=0
    g7: GeomPoint X=3e-16 Y=0 Z=0
    g8: Circle CenterX=3e-16 CenterY=0 CenterZ=0 NormalX=0 NormalY=0 NormalZ=1 AngleXU=0 Radius=2.1
    g9: LineSegment StartX=-4.76483 StartY=8.08721 StartZ=0 EndX=-3.55 EndY=8.08721 EndZ=0
    g10: LineSegment StartX=8.24722 StartY=4.75 StartZ=0 EndX=8.24722 EndY=3.55 EndZ=0
    g11: LineSegment StartX=-8.2 StartY=-4.73729 StartZ=0 EndX=-8.2 EndY=-3.55 EndZ=0
    g12: LineSegment StartX=5.5 StartY=4.75 StartZ=0 EndX=8.24722 EndY=4.75 EndZ=0
    g13: LineSegment StartX=4.75 StartY=5.50457 StartZ=0 EndX=2.65 EndY=3.4 EndZ=0
    g14: LineSegment StartX=4.75 StartY=5.50457 StartZ=0 EndX=4.75 EndY=8.08721 EndZ=0
    g15: LineSegment StartX=3.4 StartY=2.65 StartZ=0 EndX=5.5 EndY=4.75 EndZ=0
    g16: LineSegment StartX=-4.76483 StartY=5.50457 StartZ=0 EndX=-2.66166 EndY=3.4 EndZ=0
    g17: LineSegment StartX=-5.5 StartY=4.70904 StartZ=0 EndX=-3.4 EndY=2.61487 EndZ=0
    g18: LineSegment StartX=-4.76483 StartY=5.50457 StartZ=0 EndX=-4.76483 EndY=8.08721 EndZ=0
    g19: LineSegment StartX=-5.5 StartY=4.70904 StartZ=0 EndX=-8.2 EndY=4.70904 EndZ=0
    g20: LineSegment StartX=-10 StartY=3.125 StartZ=0 EndX=-10 EndY=10 EndZ=0
    g21: LineSegment StartX=-8.2 StartY=3.55 StartZ=0 EndX=-8.2 EndY=4.70904 EndZ=0
    g22: LineSegment StartX=3.55 StartY=8.08721 StartZ=0 EndX=4.75 EndY=8.08721 EndZ=0
    g23: LineSegment StartX=3.125 StartY=10 StartZ=0 EndX=10 EndY=10 EndZ=0
    g24: LineSegment StartX=-5.5 StartY=-4.73729 StartZ=0 EndX=-8.2 EndY=-4.73729 EndZ=0
    g25: LineSegment StartX=-4.75 StartY=-5.5 StartZ=0 EndX=-2.65 EndY=-3.4 EndZ=0
    g26: LineSegment StartX=-4.75 StartY=-5.5 StartZ=0 EndX=-4.75 EndY=-8.2 EndZ=0
    g27: LineSegment StartX=4.73747 StartY=-5.5 StartZ=0 EndX=4.73747 EndY=-8.2 EndZ=0
    g28: LineSegment StartX=5.5 StartY=-4.7671 StartZ=0 EndX=8.24722 EndY=-4.7671 EndZ=0
    g29: LineSegment StartX=-3.125 StartY=-10 StartZ=0 EndX=-10 EndY=-10 EndZ=0
    g30: LineSegment StartX=-3.55 StartY=-8.2 StartZ=0 EndX=-4.75 EndY=-8.2 EndZ=0
    g31: LineSegment StartX=4.73747 StartY=-8.2 StartZ=0 EndX=3.55 EndY=-8.2 EndZ=0
    g32: LineSegment StartX=10 StartY=-3.125 StartZ=0 EndX=10 EndY=-10 EndZ=0
    g33: LineSegment StartX=8.24722 StartY=-3.55 StartZ=0 EndX=8.24722 EndY=-4.7671 EndZ=0
    g34: LineSegment StartX=-2.66166 StartY=3.4 StartZ=0 EndX=2.65 EndY=3.4 EndZ=0
    g35: LineSegment StartX=-3.4 StartY=-2.63136 StartZ=0 EndX=-5.5 EndY=-4.73729 EndZ=0
    g36: LineSegment StartX=3.4 StartY=-2.6657 StartZ=0 EndX=5.5 EndY=-4.7671 EndZ=0
    g37: LineSegment StartX=2.63162 StartY=-3.4 StartZ=0 EndX=4.73747 EndY=-5.5 EndZ=0
    g38: LineSegment StartX=-3.55 StartY=-8.2 StartZ=0 EndX=-3.125 EndY=-10 EndZ=0
    g39: LineSegment StartX=3.55 StartY=-8.2 StartZ=0 EndX=3.125 EndY=-10 EndZ=0
    g40: LineSegment StartX=-3.125 StartY=10 StartZ=0 EndX=-3.55 EndY=8.08721 EndZ=0
    g41: LineSegment StartX=3.125 StartY=10 StartZ=0 EndX=3.55 EndY=8.08721 EndZ=0
    g42: LineSegment StartX=8.24722 StartY=3.55 StartZ=0 EndX=10 EndY=3.125 EndZ=0
    g43: LineSegment StartX=10 StartY=-3.125 StartZ=0 EndX=8.24722 EndY=-3.55 EndZ=0
    g44: LineSegment StartX=-10 StartY=-3.125 StartZ=0 EndX=-8.2 EndY=-3.55 EndZ=0
    g45: LineSegment StartX=-10 StartY=3.125 StartZ=0 EndX=-8.2 EndY=3.55 EndZ=0
  constraints (61):
    c: Horizontal(g1)
    c: Vertical(g0)
    c: Vertical(g2)
    c: Coincident(g23,g4)
    c: Coincident(g32,g5)
    c: Coincident(g29,g6)
    c: Coincident(g20,g3)
    c: Horizontal(g3)
    c: Horizontal(g5)
    c: Vertical(g4)
    c: Vertical(g6)
    c: PointOnObject(g7,g-1)
    c: DistanceX(g3,g7) = 10
    c: DistanceX(g-1,g23) = 10
    c: DistanceY(g7,g3) = 10
    c: DistanceX(g3,g-1) = 10
    c: DistanceY(g32,g7) = 10
    c: Coincident(g8,g7)
    c: Radius(g8) = 2.1
    c: Horizontal(g9)
    c: Vertical(g10)
    c: Vertical(g11)
    c: Coincident(g12,g15)
    c: Horizontal(g12)
    c: Coincident(g14,g13)
    c: Vertical(g14)
    c: Coincident(g15,g0)
    c: Coincident(g13,g34)
    c: Coincident(g14,g22)
    c: Coincident(g18,g16)
    c: Vertical(g18)
    c: Coincident(g19,g17)
    c: Horizontal(g19)
    c: Coincident(g9,g18)
    c: Coincident(g21,g19)
    c: Coincident(g24,g35)
    c: Horizontal(g24)
    c: Coincident(g26,g25)
    c: Vertical(g26)
    c: Coincident(g27,g37)
    c: Vertical(g27)
    c: Coincident(g28,g36)
    c: Horizontal(g28)
    c: Coincident(g11,g24)
    c: Coincident(g26,g30)
    c: Coincident(g31,g27)
    c: Coincident(g12,g10)
    c: Coincident(g28,g33)
    c: Coincident(g25,g1)
    c: Coincident(g35,g2)
    c: Coincident(g17,g2)
    c: Coincident(g16,g34)
    c: Coincident(g1,g37)
    c: Coincident(g0,g36)
    c: Coincident(g39,g5)
    c: Coincident(g40,g3)
    c: Coincident(g42,g4)
    c: Coincident(g44,g6)
    c: Coincident(g21,g45)
    c: Coincident(g33,g43)
    c: Coincident(g10,g42)
FEATURE [PartDesign::Pad] Pad009
  Direction = (0,0,1)
  Length = 300
  Length2 = 10
  Profile = -> Sketch009
  Type = 0
FEATURE [PartDesign::Fillet] Fillet099
  Base = -> Pad009 [Edge53]
  BaseFeature = -> Pad009
  Radius = 1
  SupportTransform = false
FEATURE [PartDesign::Fillet] Fillet100
  Base = -> Fillet099 [Edge114]
  BaseFeature = -> Fillet099
  Radius = 1
  SupportTransform = false
FEATURE [PartDesign::Fillet] Fillet101
  Base = -> Fillet100 [Edge137,Edge95]
  BaseFeature = -> Fillet100
  Radius = 0.5
  SupportTransform = false
FEATURE [PartDesign::Fillet] Fillet102
  Base = -> Fillet101 [Edge103]
  BaseFeature = -> Fillet101
  Radius = 0.5
  SupportTransform = false
FEATURE [PartDesign::Fillet] Fillet103
  Base = -> Fillet102 [Edge96]
  BaseFeature = -> Fillet102
  Radius = 0.5
  SupportTransform = false
FEATURE [PartDesign::Fillet] Fillet104
  Base = -> Fillet103 [Edge77]
  BaseFeature = -> Fillet103
  Radius = 0.5
  SupportTransform = false
FEATURE [PartDesign::Fillet] Fillet105
  Base = -> Fillet104 [Edge102]
  BaseFeature = -> Fillet104
  Radius = 0.5
  SupportTransform = false
FEATURE [PartDesign::Fillet] Fillet106
  Base = -> Fillet105 [Edge85]
  BaseFeature = -> Fillet105
  Radius = 0.5
  SupportTransform = false
FEATURE [PartDesign::Fillet] Fillet107
  Base = -> Fillet106 [Edge78]
  BaseFeature = -> Fillet106
  Radius = 0.5
  SupportTransform = false
FEATURE [PartDesign::Fillet] Fillet108
  Base = -> Fillet107 [Edge107]
  BaseFeature = -> Fillet107
  Radius = 0.5
  SupportTransform = false
FEATURE [PartDesign::Fillet] Fillet109
  Base = -> Fillet108 [Edge74]
  BaseFeature = -> Fillet108
  Radius = 0.5
  SupportTransform = false
FEATURE [PartDesign::Body] Body009
  Group = -> [Sketch009,Pad009,Fillet099,Fillet100,Fillet101,Fillet102,Fillet103,Fillet104,Fillet105,Fillet106,Fillet107,Fillet108,Fillet109]
  Origin = -> Origin019
  Placement = pos=(0,0,0) rot=(0,1,0;1.5708rad)
  Tip = -> Fillet109
FEATURE [App::Part] Part009  label="2020-300-010"
  Group = -> [Body009]
  Origin = -> Origin018
  Placement = pos=(20,10,180) rot=(0,0,1;0rad)
FEATURE [Sketcher::SketchObject] Sketch010
  FullyConstrained = false
  MapMode = 5
  Support = -> [XY_Plane021]
  sketch-geometry (46):
    g0: LineSegment StartX=3.4 StartY=2.65 StartZ=0 EndX=3.4 EndY=-2.6657 EndZ=0
    g1: LineSegment StartX=2.63162 StartY=-3.4 StartZ=0 EndX=-2.65 EndY=-3.4 EndZ=0
    g2: LineSegment StartX=-3.4 StartY=-2.63136 StartZ=0 EndX=-3.4 EndY=2.61487 EndZ=0
    g3: LineSegment StartX=-10 StartY=10 StartZ=0 EndX=-3.125 EndY=10 EndZ=0
    g4: LineSegment StartX=10 StartY=10 StartZ=0 EndX=10 EndY=3.125 EndZ=0
    g5: LineSegment StartX=10 StartY=-10 StartZ=0 EndX=3.125 EndY=-10 EndZ=0
    g6: LineSegment StartX=-10 StartY=-10 StartZ=0 EndX=-10 EndY=-3.125 EndZ=0
    g7: GeomPoint X=3e-16 Y=0 Z=0
    g8: Circle CenterX=3e-16 CenterY=0 CenterZ=0 NormalX=0 NormalY=0 NormalZ=1 AngleXU=0 Radius=2.1
    g9: LineSegment StartX=-4.76483 StartY=8.08721 StartZ=0 EndX=-3.55 EndY=8.08721 EndZ=0
    g10: LineSegment StartX=8.24722 StartY=4.75 StartZ=0 EndX=8.24722 EndY=3.55 EndZ=0
    g11: LineSegment StartX=-8.2 StartY=-4.73729 StartZ=0 EndX=-8.2 EndY=-3.55 EndZ=0
    g12: LineSegment StartX=5.5 StartY=4.75 StartZ=0 EndX=8.24722 EndY=4.75 EndZ=0
    g13: LineSegment StartX=4.75 StartY=5.50457 StartZ=0 EndX=2.65 EndY=3.4 EndZ=0
    g14: LineSegment StartX=4.75 StartY=5.50457 StartZ=0 EndX=4.75 EndY=8.08721 EndZ=0
    g15: LineSegment StartX=3.4 StartY=2.65 StartZ=0 EndX=5.5 EndY=4.75 EndZ=0
    g16: LineSegment StartX=-4.76483 StartY=5.50457 StartZ=0 EndX=-2.66166 EndY=3.4 EndZ=0
    g17: LineSegment StartX=-5.5 StartY=4.70904 StartZ=0 EndX=-3.4 EndY=2.61487 EndZ=0
    g18: LineSegment StartX=-4.76483 StartY=5.50457 StartZ=0 EndX=-4.76483 EndY=8.08721 EndZ=0
    g19: LineSegment StartX=-5.5 StartY=4.70904 StartZ=0 EndX=-8.2 EndY=4.70904 EndZ=0
    g20: LineSegment StartX=-10 StartY=3.125 StartZ=0 EndX=-10 EndY=10 EndZ=0
    g21: LineSegment StartX=-8.2 StartY=3.55 StartZ=0 EndX=-8.2 EndY=4.70904 EndZ=0
    g22: LineSegment StartX=3.55 StartY=8.08721 StartZ=0 EndX=4.75 EndY=8.08721 EndZ=0
    g23: LineSegment StartX=3.125 StartY=10 StartZ=0 EndX=10 EndY=10 EndZ=0
    g24: LineSegment StartX=-5.5 StartY=-4.73729 StartZ=0 EndX=-8.2 EndY=-4.73729 EndZ=0
    g25: LineSegment StartX=-4.75 StartY=-5.5 StartZ=0 EndX=-2.65 EndY=-3.4 EndZ=0
    g26: LineSegment StartX=-4.75 StartY=-5.5 StartZ=0 EndX=-4.75 EndY=-8.2 EndZ=0
    g27: LineSegment StartX=4.73747 StartY=-5.5 StartZ=0 EndX=4.73747 EndY=-8.2 EndZ=0
    g28: LineSegment StartX=5.5 StartY=-4.7671 StartZ=0 EndX=8.24722 EndY=-4.7671 EndZ=0
    g29: LineSegment StartX=-3.125 StartY=-10 StartZ=0 EndX=-10 EndY=-10 EndZ=0
    g30: LineSegment StartX=-3.55 StartY=-8.2 StartZ=0 EndX=-4.75 EndY=-8.2 EndZ=0
    g31: LineSegment StartX=4.73747 StartY=-8.2 StartZ=0 EndX=3.55 EndY=-8.2 EndZ=0
    g32: LineSegment StartX=10 StartY=-3.125 StartZ=0 EndX=10 EndY=-10 EndZ=0
    g33: LineSegment StartX=8.24722 StartY=-3.55 StartZ=0 EndX=8.24722 EndY=-4.7671 EndZ=0
    g34: LineSegment StartX=-2.66166 StartY=3.4 StartZ=0 EndX=2.65 EndY=3.4 EndZ=0
    g35: LineSegment StartX=-3.4 StartY=-2.63136 StartZ=0 EndX=-5.5 EndY=-4.73729 EndZ=0
    g36: LineSegment StartX=3.4 StartY=-2.6657 StartZ=0 EndX=5.5 EndY=-4.7671 EndZ=0
    g37: LineSegment StartX=2.63162 StartY=-3.4 StartZ=0 EndX=4.73747 EndY=-5.5 EndZ=0
    g38: LineSegment StartX=-3.55 StartY=-8.2 StartZ=0 EndX=-3.125 EndY=-10 EndZ=0
    g39: LineSegment StartX=3.55 StartY=-8.2 StartZ=0 EndX=3.125 EndY=-10 EndZ=0
    g40: LineSegment StartX=-3.125 StartY=10 StartZ=0 EndX=-3.55 EndY=8.08721 EndZ=0
    g41: LineSegment StartX=3.125 StartY=10 StartZ=0 EndX=3.55 EndY=8.08721 EndZ=0
    g42: LineSegment StartX=8.24722 StartY=3.55 StartZ=0 EndX=10 EndY=3.125 EndZ=0
    g43: LineSegment StartX=10 StartY=-3.125 StartZ=0 EndX=8.24722 EndY=-3.55 EndZ=0
    g44: LineSegment StartX=-10 StartY=-3.125 StartZ=0 EndX=-8.2 EndY=-3.55 EndZ=0
    g45: LineSegment StartX=-10 StartY=3.125 StartZ=0 EndX=-8.2 EndY=3.55 EndZ=0
  constraints (61):
    c: Horizontal(g1)
    c: Vertical(g0)
    c: Vertical(g2)
    c: Coincident(g23,g4)
    c: Coincident(g32,g5)
    c: Coincident(g29,g6)
    c: Coincident(g20,g3)
    c: Horizontal(g3)
    c: Horizontal(g5)
    c: Vertical(g4)
    c: Vertical(g6)
    c: PointOnObject(g7,g-1)
    c: DistanceX(g3,g7) = 10
    c: DistanceX(g-1,g23) = 10
    c: DistanceY(g7,g3) = 10
    c: DistanceX(g3,g-1) = 10
    c: DistanceY(g32,g7) = 10
    c: Coincident(g8,g7)
    c: Radius(g8) = 2.1
    c: Horizontal(g9)
    c: Vertical(g10)
    c: Vertical(g11)
    c: Coincident(g12,g15)
    c: Horizontal(g12)
    c: Coincident(g14,g13)
    c: Vertical(g14)
    c: Coincident(g15,g0)
    c: Coincident(g13,g34)
    c: Coincident(g14,g22)
    c: Coincident(g18,g16)
    c: Vertical(g18)
    c: Coincident(g19,g17)
    c: Horizontal(g19)
    c: Coincident(g9,g18)
    c: Coincident(g21,g19)
    c: Coincident(g24,g35)
    c: Horizontal(g24)
    c: Coincident(g26,g25)
    c: Vertical(g26)
    c: Coincident(g27,g37)
    c: Vertical(g27)
    c: Coincident(g28,g36)
    c: Horizontal(g28)
    c: Coincident(g11,g24)
    c: Coincident(g26,g30)
    c: Coincident(g31,g27)
    c: Coincident(g12,g10)
    c: Coincident(g28,g33)
    c: Coincident(g25,g1)
    c: Coincident(g35,g2)
    c: Coincident(g17,g2)
    c: Coincident(g16,g34)
    c: Coincident(g1,g37)
    c: Coincident(g0,g36)
    c: Coincident(g39,g5)
    c: Coincident(g40,g3)
    c: Coincident(g42,g4)
    c: Coincident(g44,g6)
    c: Coincident(g21,g45)
    c: Coincident(g33,g43)
    c: Coincident(g10,g42)
FEATURE [PartDesign::Pad] Pad010
  Direction = (0,0,1)
  Length = 300
  Length2 = 10
  Profile = -> Sketch010
  Type = 0
FEATURE [PartDesign::Fillet] Fillet110
  Base = -> Pad010 [Edge53]
  BaseFeature = -> Pad010
  Radius = 1
  SupportTransform = false
FEATURE [PartDesign::Fillet] Fillet111
  Base = -> Fillet110 [Edge114]
  BaseFeature = -> Fillet110
  Radius = 1
  SupportTransform = false
FEATURE [PartDesign::Fillet] Fillet112
  Base = -> Fillet111 [Edge137,Edge95]
  BaseFeature = -> Fillet111
  Radius = 0.5
  SupportTransform = false
FEATURE [PartDesign::Fillet] Fillet113
  Base = -> Fillet112 [Edge103]
  BaseFeature = -> Fillet112
  Radius = 0.5
  SupportTransform = false
FEATURE [PartDesign::Fillet] Fillet114
  Base = -> Fillet113 [Edge96]
  BaseFeature = -> Fillet113
  Radius = 0.5
  SupportTransform = false
FEATURE [PartDesign::Fillet] Fillet115
  Base = -> Fillet114 [Edge77]
  BaseFeature = -> Fillet114
  Radius = 0.5
  SupportTransform = false
FEATURE [PartDesign::Fillet] Fillet116
  Base = -> Fillet115 [Edge102]
  BaseFeature = -> Fillet115
  Radius = 0.5
  SupportTransform = false
FEATURE [PartDesign::Fillet] Fillet117
  Base = -> Fillet116 [Edge85]
  BaseFeature = -> Fillet116
  Radius = 0.5
  SupportTransform = false
FEATURE [PartDesign::Fillet] Fillet118
  Base = -> Fillet117 [Edge78]
  BaseFeature = -> Fillet117
  Radius = 0.5
  SupportTransform = false
FEATURE [PartDesign::Fillet] Fillet119
  Base = -> Fillet118 [Edge107]
  BaseFeature = -> Fillet118
  Radius = 0.5
  SupportTransform = false
FEATURE [PartDesign::Fillet] Fillet120
  Base = -> Fillet119 [Edge74]
  BaseFeature = -> Fillet119
  Radius = 0.5
  SupportTransform = false
FEATURE [PartDesign::Body] Body010
  Group = -> [Sketch010,Pad010,Fillet110,Fillet111,Fillet112,Fillet113,Fillet114,Fillet115,Fillet116,Fillet117,Fillet118,Fillet119,Fillet120]
  Origin = -> Origin021
  Placement = pos=(0,0,0) rot=(0,1,0;1.5708rad)
  Tip = -> Fillet120
FEATURE [App::Part] Part010  label="2020-300-011"
  Group = -> [Body010]
  Origin = -> Origin020
  Placement = pos=(10,20,179) rot=(0,0,1;1.5708rad)
FEATURE [Sketcher::SketchObject] Sketch011
  FullyConstrained = false
  MapMode = 5
  Support = -> [XY_Plane023]
  sketch-geometry (46):
    g0: LineSegment StartX=3.4 StartY=2.65 StartZ=0 EndX=3.4 EndY=-2.6657 EndZ=0
    g1: LineSegment StartX=2.63162 StartY=-3.4 StartZ=0 EndX=-2.65 EndY=-3.4 EndZ=0
    g2: LineSegment StartX=-3.4 StartY=-2.63136 StartZ=0 EndX=-3.4 EndY=2.61487 EndZ=0
    g3: LineSegment StartX=-10 StartY=10 StartZ=0 EndX=-3.125 EndY=10 EndZ=0
    g4: LineSegment StartX=10 StartY=10 StartZ=0 EndX=10 EndY=3.125 EndZ=0
    g5: LineSegment StartX=10 StartY=-10 StartZ=0 EndX=3.125 EndY=-10 EndZ=0
    g6: LineSegment StartX=-10 StartY=-10 StartZ=0 EndX=-10 EndY=-3.125 EndZ=0
    g7: GeomPoint X=3e-16 Y=0 Z=0
    g8: Circle CenterX=3e-16 CenterY=0 CenterZ=0 NormalX=0 NormalY=0 NormalZ=1 AngleXU=0 Radius=2.1
    g9: LineSegment StartX=-4.76483 StartY=8.08721 StartZ=0 EndX=-3.55 EndY=8.08721 EndZ=0
    g10: LineSegment StartX=8.24722 StartY=4.75 StartZ=0 EndX=8.24722 EndY=3.55 EndZ=0
    g11: LineSegment StartX=-8.2 StartY=-4.73729 StartZ=0 EndX=-8.2 EndY=-3.55 EndZ=0
    g12: LineSegment StartX=5.5 StartY=4.75 StartZ=0 EndX=8.24722 EndY=4.75 EndZ=0
    g13: LineSegment StartX=4.75 StartY=5.50457 StartZ=0 EndX=2.65 EndY=3.4 EndZ=0
    g14: LineSegment StartX=4.75 StartY=5.50457 StartZ=0 EndX=4.75 EndY=8.08721 EndZ=0
    g15: LineSegment StartX=3.4 StartY=2.65 StartZ=0 EndX=5.5 EndY=4.75 EndZ=0
    g16: LineSegment StartX=-4.76483 StartY=5.50457 StartZ=0 EndX=-2.66166 EndY=3.4 EndZ=0
    g17: LineSegment StartX=-5.5 StartY=4.70904 StartZ=0 EndX=-3.4 EndY=2.61487 EndZ=0
    g18: LineSegment StartX=-4.76483 StartY=5.50457 StartZ=0 EndX=-4.76483 EndY=8.08721 EndZ=0
    g19: LineSegment StartX=-5.5 StartY=4.70904 StartZ=0 EndX=-8.2 EndY=4.70904 EndZ=0
    g20: LineSegment StartX=-10 StartY=3.125 StartZ=0 EndX=-10 EndY=10 EndZ=0
    g21: LineSegment StartX=-8.2 StartY=3.55 StartZ=0 EndX=-8.2 EndY=4.70904 EndZ=0
    g22: LineSegment StartX=3.55 StartY=8.08721 StartZ=0 EndX=4.75 EndY=8.08721 EndZ=0
    g23: LineSegment StartX=3.125 StartY=10 StartZ=0 EndX=10 EndY=10 EndZ=0
    g24: LineSegment StartX=-5.5 StartY=-4.73729 StartZ=0 EndX=-8.2 EndY=-4.73729 EndZ=0
    g25: LineSegment StartX=-4.75 StartY=-5.5 StartZ=0 EndX=-2.65 EndY=-3.4 EndZ=0
    g26: LineSegment StartX=-4.75 StartY=-5.5 StartZ=0 EndX=-4.75 EndY=-8.2 EndZ=0
    g27: LineSegment StartX=4.73747 StartY=-5.5 StartZ=0 EndX=4.73747 EndY=-8.2 EndZ=0
    g28: LineSegment StartX=5.5 StartY=-4.7671 StartZ=0 EndX=8.24722 EndY=-4.7671 EndZ=0
    g29: LineSegment StartX=-3.125 StartY=-10 StartZ=0 EndX=-10 EndY=-10 EndZ=0
    g30: LineSegment StartX=-3.55 StartY=-8.2 StartZ=0 EndX=-4.75 EndY=-8.2 EndZ=0
    g31: LineSegment StartX=4.73747 StartY=-8.2 StartZ=0 EndX=3.55 EndY=-8.2 EndZ=0
    g32: LineSegment StartX=10 StartY=-3.125 StartZ=0 EndX=10 EndY=-10 EndZ=0
    g33: LineSegment StartX=8.24722 StartY=-3.55 StartZ=0 EndX=8.24722 EndY=-4.7671 EndZ=0
    g34: LineSegment StartX=-2.66166 StartY=3.4 StartZ=0 EndX=2.65 EndY=3.4 EndZ=0
    g35: LineSegment StartX=-3.4 StartY=-2.63136 StartZ=0 EndX=-5.5 EndY=-4.73729 EndZ=0
    g36: LineSegment StartX=3.4 StartY=-2.6657 StartZ=0 EndX=5.5 EndY=-4.7671 EndZ=0
    g37: LineSegment StartX=2.63162 StartY=-3.4 StartZ=0 EndX=4.73747 EndY=-5.5 EndZ=0
    g38: LineSegment StartX=-3.55 StartY=-8.2 StartZ=0 EndX=-3.125 EndY=-10 EndZ=0
    g39: LineSegment StartX=3.55 StartY=-8.2 StartZ=0 EndX=3.125 EndY=-10 EndZ=0
    g40: LineSegment StartX=-3.125 StartY=10 StartZ=0 EndX=-3.55 EndY=8.08721 EndZ=0
    g41: LineSegment StartX=3.125 StartY=10 StartZ=0 EndX=3.55 EndY=8.08721 EndZ=0
    g42: LineSegment StartX=8.24722 StartY=3.55 StartZ=0 EndX=10 EndY=3.125 EndZ=0
    g43: LineSegment StartX=10 StartY=-3.125 StartZ=0 EndX=8.24722 EndY=-3.55 EndZ=0
    g44: LineSegment StartX=-10 StartY=-3.125 StartZ=0 EndX=-8.2 EndY=-3.55 EndZ=0
    g45: LineSegment StartX=-10 StartY=3.125 StartZ=0 EndX=-8.2 EndY=3.55 EndZ=0
  constraints (61):
    c: Horizontal(g1)
    c: Vertical(g0)
    c: Vertical(g2)
    c: Coincident(g23,g4)
    c: Coincident(g32,g5)
    c: Coincident(g29,g6)
    c: Coincident(g20,g3)
    c: Horizontal(g3)
    c: Horizontal(g5)
    c: Vertical(g4)
    c: Vertical(g6)
    c: PointOnObject(g7,g-1)
    c: DistanceX(g3,g7) = 10
    c: DistanceX(g-1,g23) = 10
    c: DistanceY(g7,g3) = 10
    c: DistanceX(g3,g-1) = 10
    c: DistanceY(g32,g7) = 10
    c: Coincident(g8,g7)
    c: Radius(g8) = 2.1
    c: Horizontal(g9)
    c: Vertical(g10)
    c: Vertical(g11)
    c: Coincident(g12,g15)
    c: Horizontal(g12)
    c: Coincident(g14,g13)
    c: Vertical(g14)
    c: Coincident(g15,g0)
    c: Coincident(g13,g34)
    c: Coincident(g14,g22)
    c: Coincident(g18,g16)
    c: Vertical(g18)
    c: Coincident(g19,g17)
    c: Horizontal(g19)
    c: Coincident(g9,g18)
    c: Coincident(g21,g19)
    c: Coincident(g24,g35)
    c: Horizontal(g24)
    c: Coincident(g26,g25)
    c: Vertical(g26)
    c: Coincident(g27,g37)
    c: Vertical(g27)
    c: Coincident(g28,g36)
    c: Horizontal(g28)
    c: Coincident(g11,g24)
    c: Coincident(g26,g30)
    c: Coincident(g31,g27)
    c: Coincident(g12,g10)
    c: Coincident(g28,g33)
    c: Coincident(g25,g1)
    c: Coincident(g35,g2)
    c: Coincident(g17,g2)
    c: Coincident(g16,g34)
    c: Coincident(g1,g37)
    c: Coincident(g0,g36)
    c: Coincident(g39,g5)
    c: Coincident(g40,g3)
    c: Coincident(g42,g4)
    c: Coincident(g44,g6)
    c: Coincident(g21,g45)
    c: Coincident(g33,g43)
    c: Coincident(g10,g42)
FEATURE [PartDesign::Pad] Pad011
  Direction = (0,0,1)
  Length = 300
  Length2 = 10
  Profile = -> Sketch011
  Type = 0
FEATURE [PartDesign::Fillet] Fillet121
  Base = -> Pad011 [Edge53]
  BaseFeature = -> Pad011
  Radius = 1
  SupportTransform = false
FEATURE [PartDesign::Fillet] Fillet122
  Base = -> Fillet121 [Edge114]
  BaseFeature = -> Fillet121
  Radius = 1
  SupportTransform = false
FEATURE [PartDesign::Fillet] Fillet123
  Base = -> Fillet122 [Edge137,Edge95]
  BaseFeature = -> Fillet122
  Radius = 0.5
  SupportTransform = false
FEATURE [PartDesign::Fillet] Fillet124
  Base = -> Fillet123 [Edge103]
  BaseFeature = -> Fillet123
  Radius = 0.5
  SupportTransform = false
FEATURE [PartDesign::Fillet] Fillet125
  Base = -> Fillet124 [Edge96]
  BaseFeature = -> Fillet124
  Radius = 0.5
  SupportTransform = false
FEATURE [PartDesign::Fillet] Fillet126
  Base = -> Fillet125 [Edge77]
  BaseFeature = -> Fillet125
  Radius = 0.5
  SupportTransform = false
FEATURE [PartDesign::Fillet] Fillet127
  Base = -> Fillet126 [Edge102]
  BaseFeature = -> Fillet126
  Radius = 0.5
  SupportTransform = false
FEATURE [PartDesign::Fillet] Fillet128
  Base = -> Fillet127 [Edge85]
  BaseFeature = -> Fillet127
  Radius = 0.5
  SupportTransform = false
FEATURE [PartDesign::Fillet] Fillet129
  Base = -> Fillet128 [Edge78]
  BaseFeature = -> Fillet128
  Radius = 0.5
  SupportTransform = false
FEATURE [PartDesign::Fillet] Fillet130
  Base = -> Fillet129 [Edge107]
  BaseFeature = -> Fillet129
  Radius = 0.5
  SupportTransform = false
FEATURE [PartDesign::Fillet] Fillet131
  Base = -> Fillet130 [Edge74]
  BaseFeature = -> Fillet130
  Radius = 0.5
  SupportTransform = false
FEATURE [PartDesign::Body] Body011
  Group = -> [Sketch011,Pad011,Fillet121,Fillet122,Fillet123,Fillet124,Fillet125,Fillet126,Fillet127,Fillet128,Fillet129,Fillet130,Fillet131]
  Origin = -> Origin023
  Placement = pos=(0,0,0) rot=(0,1,0;1.5708rad)
  Tip = -> Fillet131
FEATURE [App::Part] Part011  label="2020-300-012"
  Group = -> [Body011]
  Origin = -> Origin022
  Placement = pos=(330,20,180) rot=(0,0,1;1.5708rad)
FEATURE [Sketcher::SketchObject] Sketch012
  FullyConstrained = false
  MapMode = 5
  Support = -> [XY_Plane025]
  sketch-geometry (46):
    g0: LineSegment StartX=3.4 StartY=2.65 StartZ=0 EndX=3.4 EndY=-2.6657 EndZ=0
    g1: LineSegment StartX=2.63162 StartY=-3.4 StartZ=0 EndX=-2.65 EndY=-3.4 EndZ=0
    g2: LineSegment StartX=-3.4 StartY=-2.63136 StartZ=0 EndX=-3.4 EndY=2.61487 EndZ=0
    g3: LineSegment StartX=-10 StartY=10 StartZ=0 EndX=-3.125 EndY=10 EndZ=0
    g4: LineSegment StartX=10 StartY=10 StartZ=0 EndX=10 EndY=3.125 EndZ=0
    g5: LineSegment StartX=10 StartY=-10 StartZ=0 EndX=3.125 EndY=-10 EndZ=0
    g6: LineSegment StartX=-10 StartY=-10 StartZ=0 EndX=-10 EndY=-3.125 EndZ=0
    g7: GeomPoint X=3e-16 Y=0 Z=0
    g8: Circle CenterX=3e-16 CenterY=0 CenterZ=0 NormalX=0 NormalY=0 NormalZ=1 AngleXU=0 Radius=2.1
    g9: LineSegment StartX=-4.76483 StartY=8.08721 StartZ=0 EndX=-3.55 EndY=8.08721 EndZ=0
    g10: LineSegment StartX=8.24722 StartY=4.75 StartZ=0 EndX=8.24722 EndY=3.55 EndZ=0
    g11: LineSegment StartX=-8.2 StartY=-4.73729 StartZ=0 EndX=-8.2 EndY=-3.55 EndZ=0
    g12: LineSegment StartX=5.5 StartY=4.75 StartZ=0 EndX=8.24722 EndY=4.75 EndZ=0
    g13: LineSegment StartX=4.75 StartY=5.50457 StartZ=0 EndX=2.65 EndY=3.4 EndZ=0
    g14: LineSegment StartX=4.75 StartY=5.50457 StartZ=0 EndX=4.75 EndY=8.08721 EndZ=0
    g15: LineSegment StartX=3.4 StartY=2.65 StartZ=0 EndX=5.5 EndY=4.75 EndZ=0
    g16: LineSegment StartX=-4.76483 StartY=5.50457 StartZ=0 EndX=-2.66166 EndY=3.4 EndZ=0
    g17: LineSegment StartX=-5.5 StartY=4.70904 StartZ=0 EndX=-3.4 EndY=2.61487 EndZ=0
    g18: LineSegment StartX=-4.76483 StartY=5.50457 StartZ=0 EndX=-4.76483 EndY=8.08721 EndZ=0
    g19: LineSegment StartX=-5.5 StartY=4.70904 StartZ=0 EndX=-8.2 EndY=4.70904 EndZ=0
    g20: LineSegment StartX=-10 StartY=3.125 StartZ=0 EndX=-10 EndY=10 EndZ=0
    g21: LineSegment StartX=-8.2 StartY=3.55 StartZ=0 EndX=-8.2 EndY=4.70904 EndZ=0
    g22: LineSegment StartX=3.55 StartY=8.08721 StartZ=0 EndX=4.75 EndY=8.08721 EndZ=0
    g23: LineSegment StartX=3.125 StartY=10 StartZ=0 EndX=10 EndY=10 EndZ=0
    g24: LineSegment StartX=-5.5 StartY=-4.73729 StartZ=0 EndX=-8.2 EndY=-4.73729 EndZ=0
    g25: LineSegment StartX=-4.75 StartY=-5.5 StartZ=0 EndX=-2.65 EndY=-3.4 EndZ=0
    g26: LineSegment StartX=-4.75 StartY=-5.5 StartZ=0 EndX=-4.75 EndY=-8.2 EndZ=0
    g27: LineSegment StartX=4.73747 StartY=-5.5 StartZ=0 EndX=4.73747 EndY=-8.2 EndZ=0
    g28: LineSegment StartX=5.5 StartY=-4.7671 StartZ=0 EndX=8.24722 EndY=-4.7671 EndZ=0
    g29: LineSegment StartX=-3.125 StartY=-10 StartZ=0 EndX=-10 EndY=-10 EndZ=0
    g30: LineSegment StartX=-3.55 StartY=-8.2 StartZ=0 EndX=-4.75 EndY=-8.2 EndZ=0
    g31: LineSegment StartX=4.73747 StartY=-8.2 StartZ=0 EndX=3.55 EndY=-8.2 EndZ=0
    g32: LineSegment StartX=10 StartY=-3.125 StartZ=0 EndX=10 EndY=-10 EndZ=0
    g33: LineSegment StartX=8.24722 StartY=-3.55 StartZ=0 EndX=8.24722 EndY=-4.7671 EndZ=0
    g34: LineSegment StartX=-2.66166 StartY=3.4 StartZ=0 EndX=2.65 EndY=3.4 EndZ=0
    g35: LineSegment StartX=-3.4 StartY=-2.63136 StartZ=0 EndX=-5.5 EndY=-4.73729 EndZ=0
    g36: LineSegment StartX=3.4 StartY=-2.6657 StartZ=0 EndX=5.5 EndY=-4.7671 EndZ=0
    g37: LineSegment StartX=2.63162 StartY=-3.4 StartZ=0 EndX=4.73747 EndY=-5.5 EndZ=0
    g38: LineSegment StartX=-3.55 StartY=-8.2 StartZ=0 EndX=-3.125 EndY=-10 EndZ=0
    g39: LineSegment StartX=3.55 StartY=-8.2 StartZ=0 EndX=3.125 EndY=-10 EndZ=0
    g40: LineSegment StartX=-3.125 StartY=10 StartZ=0 EndX=-3.55 EndY=8.08721 EndZ=0
    g41: LineSegment StartX=3.125 StartY=10 StartZ=0 EndX=3.55 EndY=8.08721 EndZ=0
    g42: LineSegment StartX=8.24722 StartY=3.55 StartZ=0 EndX=10 EndY=3.125 EndZ=0
    g43: LineSegment StartX=10 StartY=-3.125 StartZ=0 EndX=8.24722 EndY=-3.55 EndZ=0
    g44: LineSegment StartX=-10 StartY=-3.125 StartZ=0 EndX=-8.2 EndY=-3.55 EndZ=0
    g45: LineSegment StartX=-10 StartY=3.125 StartZ=0 EndX=-8.2 EndY=3.55 EndZ=0
  constraints (61):
    c: Horizontal(g1)
    c: Vertical(g0)
    c: Vertical(g2)
    c: Coincident(g23,g4)
    c: Coincident(g32,g5)
    c: Coincident(g29,g6)
    c: Coincident(g20,g3)
    c: Horizontal(g3)
    c: Horizontal(g5)
    c: Vertical(g4)
    c: Vertical(g6)
    c: PointOnObject(g7,g-1)
    c: DistanceX(g3,g7) = 10
    c: DistanceX(g-1,g23) = 10
    c: DistanceY(g7,g3) = 10
    c: DistanceX(g3,g-1) = 10
    c: DistanceY(g32,g7) = 10
    c: Coincident(g8,g7)
    c: Radius(g8) = 2.1
    c: Horizontal(g9)
    c: Vertical(g10)
    c: Vertical(g11)
    c: Coincident(g12,g15)
    c: Horizontal(g12)
    c: Coincident(g14,g13)
    c: Vertical(g14)
    c: Coincident(g15,g0)
    c: Coincident(g13,g34)
    c: Coincident(g14,g22)
    c: Coincident(g18,g16)
    c: Vertical(g18)
    c: Coincident(g19,g17)
    c: Horizontal(g19)
    c: Coincident(g9,g18)
    c: Coincident(g21,g19)
    c: Coincident(g24,g35)
    c: Horizontal(g24)
    c: Coincident(g26,g25)
    c: Vertical(g26)
    c: Coincident(g27,g37)
    c: Vertical(g27)
    c: Coincident(g28,g36)
    c: Horizontal(g28)
    c: Coincident(g11,g24)
    c: Coincident(g26,g30)
    c: Coincident(g31,g27)
    c: Coincident(g12,g10)
    c: Coincident(g28,g33)
    c: Coincident(g25,g1)
    c: Coincident(g35,g2)
    c: Coincident(g17,g2)
    c: Coincident(g16,g34)
    c: Coincident(g1,g37)
    c: Coincident(g0,g36)
    c: Coincident(g39,g5)
    c: Coincident(g40,g3)
    c: Coincident(g42,g4)
    c: Coincident(g44,g6)
    c: Coincident(g21,g45)
    c: Coincident(g33,g43)
    c: Coincident(g10,g42)
FEATURE [PartDesign::Pad] Pad012
  Direction = (0,0,1)
  Length = 300
  Length2 = 10
  Profile = -> Sketch012
  Type = 0
FEATURE [PartDesign::Fillet] Fillet132
  Base = -> Pad012 [Edge53]
  BaseFeature = -> Pad012
  Radius = 1
  SupportTransform = false
FEATURE [PartDesign::Fillet] Fillet133
  Base = -> Fillet132 [Edge114]
  BaseFeature = -> Fillet132
  Radius = 1
  SupportTransform = false
FEATURE [PartDesign::Fillet] Fillet134
  Base = -> Fillet133 [Edge137,Edge95]
  BaseFeature = -> Fillet133
  Radius = 0.5
  SupportTransform = false
FEATURE [PartDesign::Fillet] Fillet135
  Base = -> Fillet134 [Edge103]
  BaseFeature = -> Fillet134
  Radius = 0.5
  SupportTransform = false
FEATURE [PartDesign::Fillet] Fillet136
  Base = -> Fillet135 [Edge96]
  BaseFeature = -> Fillet135
  Radius = 0.5
  SupportTransform = false
FEATURE [PartDesign::Fillet] Fillet137
  Base = -> Fillet136 [Edge77]
  BaseFeature = -> Fillet136
  Radius = 0.5
  SupportTransform = false
FEATURE [PartDesign::Fillet] Fillet138
  Base = -> Fillet137 [Edge102]
  BaseFeature = -> Fillet137
  Radius = 0.5
  SupportTransform = false
FEATURE [PartDesign::Fillet] Fillet139
  Base = -> Fillet138 [Edge85]
  BaseFeature = -> Fillet138
  Radius = 0.5
  SupportTransform = false
FEATURE [PartDesign::Fillet] Fillet140
  Base = -> Fillet139 [Edge78]
  BaseFeature = -> Fillet139
  Radius = 0.5
  SupportTransform = false
FEATURE [PartDesign::Fillet] Fillet141
  Base = -> Fillet140 [Edge107]
  BaseFeature = -> Fillet140
  Radius = 0.5
  SupportTransform = false
FEATURE [PartDesign::Fillet] Fillet142
  Base = -> Fillet141 [Edge74]
  BaseFeature = -> Fillet141
  Radius = 0.5
  SupportTransform = false
FEATURE [PartDesign::Body] Body012
  Group = -> [Sketch012,Pad012,Fillet132,Fillet133,Fillet134,Fillet135,Fillet136,Fillet137,Fillet138,Fillet139,Fillet140,Fillet141,Fillet142]
  Origin = -> Origin025
  Placement = pos=(0,0,0) rot=(0,1,0;1.5708rad)
  Tip = -> Fillet142
FEATURE [App::Part] Part012  label="2020-300-013"
  Group = -> [Body012]
  Origin = -> Origin024
  Placement = pos=(10,20,80) rot=(0,0,1;1.5708rad)
FEATURE [Sketcher::SketchObject] Sketch013
  FullyConstrained = false
  MapMode = 5
  Support = -> [XY_Plane027]
  sketch-geometry (46):
    g0: LineSegment StartX=3.4 StartY=2.65 StartZ=0 EndX=3.4 EndY=-2.6657 EndZ=0
    g1: LineSegment StartX=2.63162 StartY=-3.4 StartZ=0 EndX=-2.65 EndY=-3.4 EndZ=0
    g2: LineSegment StartX=-3.4 StartY=-2.63136 StartZ=0 EndX=-3.4 EndY=2.61487 EndZ=0
    g3: LineSegment StartX=-10 StartY=10 StartZ=0 EndX=-3.125 EndY=10 EndZ=0
    g4: LineSegment StartX=10 StartY=10 StartZ=0 EndX=10 EndY=3.125 EndZ=0
    g5: LineSegment StartX=10 StartY=-10 StartZ=0 EndX=3.125 EndY=-10 EndZ=0
    g6: LineSegment StartX=-10 StartY=-10 StartZ=0 EndX=-10 EndY=-3.125 EndZ=0
    g7: GeomPoint X=3e-16 Y=0 Z=0
    g8: Circle CenterX=3e-16 CenterY=0 CenterZ=0 NormalX=0 NormalY=0 NormalZ=1 AngleXU=0 Radius=2.1
    g9: LineSegment StartX=-4.76483 StartY=8.08721 StartZ=0 EndX=-3.55 EndY=8.08721 EndZ=0
    g10: LineSegment StartX=8.24722 StartY=4.75 StartZ=0 EndX=8.24722 EndY=3.55 EndZ=0
    g11: LineSegment StartX=-8.2 StartY=-4.73729 StartZ=0 EndX=-8.2 EndY=-3.55 EndZ=0
    g12: LineSegment StartX=5.5 StartY=4.75 StartZ=0 EndX=8.24722 EndY=4.75 EndZ=0
    g13: LineSegment StartX=4.75 StartY=5.50457 StartZ=0 EndX=2.65 EndY=3.4 EndZ=0
    g14: LineSegment StartX=4.75 StartY=5.50457 StartZ=0 EndX=4.75 EndY=8.08721 EndZ=0
    g15: LineSegment StartX=3.4 StartY=2.65 StartZ=0 EndX=5.5 EndY=4.75 EndZ=0
    g16: LineSegment StartX=-4.76483 StartY=5.50457 StartZ=0 EndX=-2.66166 EndY=3.4 EndZ=0
    g17: LineSegment StartX=-5.5 StartY=4.70904 StartZ=0 EndX=-3.4 EndY=2.61487 EndZ=0
    g18: LineSegment StartX=-4.76483 StartY=5.50457 StartZ=0 EndX=-4.76483 EndY=8.08721 EndZ=0
    g19: LineSegment StartX=-5.5 StartY=4.70904 StartZ=0 EndX=-8.2 EndY=4.70904 EndZ=0
    g20: LineSegment StartX=-10 StartY=3.125 StartZ=0 EndX=-10 EndY=10 EndZ=0
    g21: LineSegment StartX=-8.2 StartY=3.55 StartZ=0 EndX=-8.2 EndY=4.70904 EndZ=0
    g22: LineSegment StartX=3.55 StartY=8.08721 StartZ=0 EndX=4.75 EndY=8.08721 EndZ=0
    g23: LineSegment StartX=3.125 StartY=10 StartZ=0 EndX=10 EndY=10 EndZ=0
    g24: LineSegment StartX=-5.5 StartY=-4.73729 StartZ=0 EndX=-8.2 EndY=-4.73729 EndZ=0
    g25: LineSegment StartX=-4.75 StartY=-5.5 StartZ=0 EndX=-2.65 EndY=-3.4 EndZ=0
    g26: LineSegment StartX=-4.75 StartY=-5.5 StartZ=0 EndX=-4.75 EndY=-8.2 EndZ=0
    g27: LineSegment StartX=4.73747 StartY=-5.5 StartZ=0 EndX=4.73747 EndY=-8.2 EndZ=0
    g28: LineSegment StartX=5.5 StartY=-4.7671 StartZ=0 EndX=8.24722 EndY=-4.7671 EndZ=0
    g29: LineSegment StartX=-3.125 StartY=-10 StartZ=0 EndX=-10 EndY=-10 EndZ=0
    g30: LineSegment StartX=-3.55 StartY=-8.2 StartZ=0 EndX=-4.75 EndY=-8.2 EndZ=0
    g31: LineSegment StartX=4.73747 StartY=-8.2 StartZ=0 EndX=3.55 EndY=-8.2 EndZ=0
    g32: LineSegment StartX=10 StartY=-3.125 StartZ=0 EndX=10 EndY=-10 EndZ=0
    g33: LineSegment StartX=8.24722 StartY=-3.55 StartZ=0 EndX=8.24722 EndY=-4.7671 EndZ=0
    g34: LineSegment StartX=-2.66166 StartY=3.4 StartZ=0 EndX=2.65 EndY=3.4 EndZ=0
    g35: LineSegment StartX=-3.4 StartY=-2.63136 StartZ=0 EndX=-5.5 EndY=-4.73729 EndZ=0
    g36: LineSegment StartX=3.4 StartY=-2.6657 StartZ=0 EndX=5.5 EndY=-4.7671 EndZ=0
    g37: LineSegment StartX=2.63162 StartY=-3.4 StartZ=0 EndX=4.73747 EndY=-5.5 EndZ=0
    g38: LineSegment StartX=-3.55 StartY=-8.2 StartZ=0 EndX=-3.125 EndY=-10 EndZ=0
    g39: LineSegment StartX=3.55 StartY=-8.2 StartZ=0 EndX=3.125 EndY=-10 EndZ=0
    g40: LineSegment StartX=-3.125 StartY=10 StartZ=0 EndX=-3.55 EndY=8.08721 EndZ=0
    g41: LineSegment StartX=3.125 StartY=10 StartZ=0 EndX=3.55 EndY=8.08721 EndZ=0
    g42: LineSegment StartX=8.24722 StartY=3.55 StartZ=0 EndX=10 EndY=3.125 EndZ=0
    g43: LineSegment StartX=10 StartY=-3.125 StartZ=0 EndX=8.24722 EndY=-3.55 EndZ=0
    g44: LineSegment StartX=-10 StartY=-3.125 StartZ=0 EndX=-8.2 EndY=-3.55 EndZ=0
    g45: LineSegment StartX=-10 StartY=3.125 StartZ=0 EndX=-8.2 EndY=3.55 EndZ=0
  constraints (61):
    c: Horizontal(g1)
    c: Vertical(g0)
    c: Vertical(g2)
    c: Coincident(g23,g4)
    c: Coincident(g32,g5)
    c: Coincident(g29,g6)
    c: Coincident(g20,g3)
    c: Horizontal(g3)
    c: Horizontal(g5)
    c: Vertical(g4)
    c: Vertical(g6)
    c: PointOnObject(g7,g-1)
    c: DistanceX(g3,g7) = 10
    c: DistanceX(g-1,g23) = 10
    c: DistanceY(g7,g3) = 10
    c: DistanceX(g3,g-1) = 10
    c: DistanceY(g32,g7) = 10
    c: Coincident(g8,g7)
    c: Radius(g8) = 2.1
    c: Horizontal(g9)
    c: Vertical(g10)
    c: Vertical(g11)
    c: Coincident(g12,g15)
    c: Horizontal(g12)
    c: Coincident(g14,g13)
    c: Vertical(g14)
    c: Coincident(g15,g0)
    c: Coincident(g13,g34)
    c: Coincident(g14,g22)
    c: Coincident(g18,g16)
    c: Vertical(g18)
    c: Coincident(g19,g17)
    c: Horizontal(g19)
    c: Coincident(g9,g18)
    c: Coincident(g21,g19)
    c: Coincident(g24,g35)
    c: Horizontal(g24)
    c: Coincident(g26,g25)
    c: Vertical(g26)
    c: Coincident(g27,g37)
    c: Vertical(g27)
    c: Coincident(g28,g36)
    c: Horizontal(g28)
    c: Coincident(g11,g24)
    c: Coincident(g26,g30)
    c: Coincident(g31,g27)
    c: Coincident(g12,g10)
    c: Coincident(g28,g33)
    c: Coincident(g25,g1)
    c: Coincident(g35,g2)
    c: Coincident(g17,g2)
    c: Coincident(g16,g34)
    c: Coincident(g1,g37)
    c: Coincident(g0,g36)
    c: Coincident(g39,g5)
    c: Coincident(g40,g3)
    c: Coincident(g42,g4)
    c: Coincident(g44,g6)
    c: Coincident(g21,g45)
    c: Coincident(g33,g43)
    c: Coincident(g10,g42)
FEATURE [PartDesign::Pad] Pad013
  Direction = (0,0,1)
  Length = 300
  Length2 = 10
  Profile = -> Sketch013
  Type = 0
FEATURE [PartDesign::Fillet] Fillet143
  Base = -> Pad013 [Edge53]
  BaseFeature = -> Pad013
  Radius = 1
  SupportTransform = false
FEATURE [PartDesign::Fillet] Fillet144
  Base = -> Fillet143 [Edge114]
  BaseFeature = -> Fillet143
  Radius = 1
  SupportTransform = false
FEATURE [PartDesign::Fillet] Fillet145
  Base = -> Fillet144 [Edge137,Edge95]
  BaseFeature = -> Fillet144
  Radius = 0.5
  SupportTransform = false
FEATURE [PartDesign::Fillet] Fillet146
  Base = -> Fillet145 [Edge103]
  BaseFeature = -> Fillet145
  Radius = 0.5
  SupportTransform = false
FEATURE [PartDesign::Fillet] Fillet147
  Base = -> Fillet146 [Edge96]
  BaseFeature = -> Fillet146
  Radius = 0.5
  SupportTransform = false
FEATURE [PartDesign::Fillet] Fillet148
  Base = -> Fillet147 [Edge77]
  BaseFeature = -> Fillet147
  Radius = 0.5
  SupportTransform = false
FEATURE [PartDesign::Fillet] Fillet149
  Base = -> Fillet148 [Edge102]
  BaseFeature = -> Fillet148
  Radius = 0.5
  SupportTransform = false
FEATURE [PartDesign::Fillet] Fillet150
  Base = -> Fillet149 [Edge85]
  BaseFeature = -> Fillet149
  Radius = 0.5
  SupportTransform = false
FEATURE [PartDesign::Fillet] Fillet151
  Base = -> Fillet150 [Edge78]
  BaseFeature = -> Fillet150
  Radius = 0.5
  SupportTransform = false
FEATURE [PartDesign::Fillet] Fillet152
  Base = -> Fillet151 [Edge107]
  BaseFeature = -> Fillet151
  Radius = 0.5
  SupportTransform = false
FEATURE [PartDesign::Fillet] Fillet153
  Base = -> Fillet152 [Edge74]
  BaseFeature = -> Fillet152
  Radius = 0.5
  SupportTransform = false
FEATURE [PartDesign::Body] Body013
  Group = -> [Sketch013,Pad013,Fillet143,Fillet144,Fillet145,Fillet146,Fillet147,Fillet148,Fillet149,Fillet150,Fillet151,Fillet152,Fillet153]
  Origin = -> Origin027
  Placement = pos=(0,0,0) rot=(0,1,0;1.5708rad)
  Tip = -> Fillet153
FEATURE [App::Part] Part013  label="2020-300-014"
  Group = -> [Body013]
  Origin = -> Origin026
  Placement = pos=(330,20,80) rot=(0,0,1;1.5708rad)
FEATURE [Sketcher::SketchObject] Sketch014
  FullyConstrained = true
  MapMode = 5
  Placement = pos=(0,0,0) rot=(-0.57735,0.57735,0.57735;4.18879rad)
  Support = -> [YZ_Plane036]
  sketch-geometry (1):
    g0: Circle CenterX=0 CenterY=-7.5 CenterZ=0 NormalX=0 NormalY=0 NormalZ=1 AngleXU=0 Radius=0.25
  constraints (3):
    c: PointOnObject(g0,g-2)
    c: DistanceY(g0) = -7.5
    c: Diameter(g0) = 0.5
FEATURE [Sketcher::SketchObject] Sketch015
  FullyConstrained = true
  MapMode = 5
  Support = -> [XY_Plane029]
  sketch-geometry (2):
    g0: LineSegment StartX=0 StartY=5.5 StartZ=0 EndX=6e-16 EndY=9.5 EndZ=0
    g1: ArcOfCircle CenterX=0 CenterY=7.5 CenterZ=0 NormalX=0 NormalY=0 NormalZ=1 AngleXU=0 Radius=2 StartAngle=4.71239 EndAngle=7.85398
  constraints (7):
    c: PointOnObject(g0,g-2)
    c: PointOnObject(g0,g-2)
    c: PointOnObject(g1,g0)
    c: Coincident(g1,g0)
    c: Coincident(g1,g0)
    c: Radius(g1) = 2
    c: DistanceY(g1) = 7.5
FEATURE [PartDesign::Revolution] Revolution
  Angle = 360
  Axis = (0,1,0)
  Base = (0,0,0)
  Profile = -> Sketch015
  ReferenceAxis = -> Sketch015 [V_Axis]
  Reversed = true
FEATURE [PartDesign::Body] Body015  label="Ball 001"
  Group = -> [Sketch015,Revolution]
  Origin = -> Origin029
  Tip = -> Revolution
FEATURE [PartDesign::FeatureBase] Clone
  BaseFeature = -> Body015
FEATURE [PartDesign::Body] Body016  label="Ball 002"
  BaseFeature = -> Body015
  Group = -> [Clone]
  Origin = -> Origin030
  Placement = pos=(0,0,0) rot=(-1,0,0;0.897598rad)
  Tip = -> Clone
FEATURE [PartDesign::FeatureBase] Clone001
  BaseFeature = -> Body015
FEATURE [PartDesign::Body] Body017  label="Ball 003"
  BaseFeature = -> Body015
  Group = -> [Clone001]
  Origin = -> Origin031
  Placement = pos=(0,0,0) rot=(-1,0,0;1.7952rad)
  Tip = -> Clone001
FEATURE [PartDesign::FeatureBase] Clone002
  BaseFeature = -> Body015
FEATURE [PartDesign::Body] Body018  label="Ball 004"
  BaseFeature = -> Body015
  Group = -> [Clone002]
  Origin = -> Origin032
  Placement = pos=(0,0,0) rot=(1,0,0;3.59039rad)
  Tip = -> Clone002
FEATURE [PartDesign::FeatureBase] Clone003
  BaseFeature = -> Body015
FEATURE [PartDesign::Body] Body019  label="Ball 005"
  BaseFeature = -> Body015
  Group = -> [Clone003]
  Origin = -> Origin033
  Placement = pos=(0,0,0) rot=(1,0,0;2.69279rad)
  Tip = -> Clone003
FEATURE [PartDesign::FeatureBase] Clone004
  BaseFeature = -> Body015
FEATURE [PartDesign::Body] Body020  label="Ball 006"
  BaseFeature = -> Body015
  Group = -> [Clone004]
  Origin = -> Origin034
  Placement = pos=(0,0,0) rot=(1,0,0;1.7952rad)
  Tip = -> Clone004
FEATURE [PartDesign::FeatureBase] Clone005
  BaseFeature = -> Body015
FEATURE [PartDesign::Body] Body021  label="Ball 007"
  BaseFeature = -> Body015
  Group = -> [Clone005]
  Origin = -> Origin035
  Placement = pos=(0,0,0) rot=(1,0,0;0.897598rad)
  Tip = -> Clone005
FEATURE [App::DocumentObjectGroup] Group  label="Balls"
  Group = -> [Body015,Body016,Body017,Body018,Body019,Body020,Body021]
FEATURE [Sketcher::SketchObject] Sketch019
  FullyConstrained = true
  MapMode = 5
  Support = -> [XY_Plane038]
  sketch-geometry (7):
    g0: LineSegment StartX=-5 StartY=7.5 StartZ=0 EndX=5 EndY=7.5 EndZ=0
    g1: LineSegment StartX=-0.210977 StartY=7.5 StartZ=0 EndX=0.210977 EndY=7.5 EndZ=0
    g2: ArcOfCircle CenterX=0.25 CenterY=7.5 CenterZ=0 NormalX=0 NormalY=0 NormalZ=1 AngleXU=0 Radius=0.460977 StartAngle=2.43297 EndAngle=3.14159
    g3: ArcOfCircle CenterX=-0.25 CenterY=7.5 CenterZ=0 NormalX=0 NormalY=0 NormalZ=1 AngleXU=0 Radius=0.460977 StartAngle=9.792e-13 EndAngle=0.708626
    g4: LineSegment StartX=-0.1 StartY=7.8 StartZ=0 EndX=-0.1 EndY=7.75 EndZ=0
    g5: LineSegment StartX=-0.1 StartY=7.75 StartZ=0 EndX=0.1 EndY=7.75 EndZ=0
    g6: LineSegment StartX=0.1 StartY=7.75 StartZ=0 EndX=0.1 EndY=7.8 EndZ=0
  constraints (22):
    c: DistanceY(g-1,g0) = 7.5
    c: Symmetric(g0,g0,g-2)
    c: DistanceX(g0,g0) = 10
    c: PointOnObject(g1,g0)
    c: PointOnObject(g1,g0)
    c: Coincident(g3,g1)
    c: Coincident(g2,g1)
    c: Coincident(g2,g4)
    c: Coincident(g4,g5)
    c: Horizontal(g5)
    c: Coincident(g5,g6)
    c: Coincident(g6,g3)
    c: Vertical(g6)
    c: Equal(g3,g2)
    c: Vertical(g4)
    c: Symmetric(g2,g3,g-2)
    c: DistanceX(g5,g5) = 0.2
    c: Distance(g5,g1) = 0.25
    c: DistanceX(g3,g-1) = 0.25
    c: PointOnObject(g3,g1)
    c: PointOnObject(g2,g1)
    c: Distance(g3,g1) = 0.3
FEATURE [PartDesign::Revolution] Revolution005
  Angle = 360
  Axis = (10,0,0)
  Base = (-5,7.5,0)
  Profile = -> Sketch019
  ReferenceAxis = -> Sketch019 [Axis]
FEATURE [PartDesign::Body] Body024  label="Rivet 001"
  Group = -> [Sketch019,Revolution005]
  Origin = -> Origin038
  Placement = pos=(0,0,0) rot=(1,0,0;0.448799rad)
  Tip = -> Revolution005
FEATURE [PartDesign::FeatureBase] Clone007
  BaseFeature = -> Body024
  Placement = pos=(0,0,0) rot=(1,0,0;0.448799rad)
FEATURE [PartDesign::Body] Body025  label="Rivet 002"
  BaseFeature = -> Body024
  Group = -> [Clone007]
  Origin = -> Origin039
  Placement = pos=(0,0,0) rot=(1,0,0;0.897598rad)
  Tip = -> Clone007
FEATURE [PartDesign::FeatureBase] Clone008
  BaseFeature = -> Body024
  Placement = pos=(0,0,0) rot=(1,0,0;0.448799rad)
FEATURE [PartDesign::Body] Body026  label="Rivet 003"
  BaseFeature = -> Body024
  Group = -> [Clone008]
  Origin = -> Origin040
  Placement = pos=(0,0,0) rot=(1,0,0;1.7952rad)
  Tip = -> Clone008
FEATURE [PartDesign::FeatureBase] Clone009
  BaseFeature = -> Body024
  Placement = pos=(0,0,0) rot=(1,0,0;0.448799rad)
FEATURE [PartDesign::Body] Body027  label="Rivet 004"
  BaseFeature = -> Body024
  Group = -> [Clone009]
  Origin = -> Origin041
  Placement = pos=(0,0,0) rot=(1,0,0;2.69279rad)
  Tip = -> Clone009
FEATURE [PartDesign::FeatureBase] Clone010
  BaseFeature = -> Body024
  Placement = pos=(0,0,0) rot=(1,0,0;0.448799rad)
FEATURE [PartDesign::Body] Body028  label="Rivet 005"
  BaseFeature = -> Body024
  Group = -> [Clone010]
  Origin = -> Origin042
  Placement = pos=(0,0,0) rot=(1,0,0;3.59039rad)
  Tip = -> Clone010
FEATURE [PartDesign::FeatureBase] Clone011
  BaseFeature = -> Body024
  Placement = pos=(0,0,0) rot=(1,0,0;0.448799rad)
FEATURE [PartDesign::Body] Body029  label="Rivet 006"
  BaseFeature = -> Body024
  Group = -> [Clone011]
  Origin = -> Origin043
  Placement = pos=(0,0,0) rot=(-1,0,0;1.7952rad)
  Tip = -> Clone011
FEATURE [PartDesign::FeatureBase] Clone012
  BaseFeature = -> Body024
  Placement = pos=(0,0,0) rot=(1,0,0;0.448799rad)
FEATURE [PartDesign::Body] Body030  label="Rivet 007"
  BaseFeature = -> Body024
  Group = -> [Clone012]
  Origin = -> Origin044
  Placement = pos=(0,0,0) rot=(-1,0,0;0.897598rad)
  Tip = -> Clone012
FEATURE [App::DocumentObjectGroup] Group002  label="Rivets"
  Group = -> [Body024,Body025,Body026,Body027,Body028,Body029,Body030]
FEATURE [Sketcher::SketchObject] Sketch023
  FullyConstrained = true
  MapMode = 5
  Placement = pos=(0,0,0) rot=(1,0,0;1.5708rad)
  Support = -> [XZ_Plane036]
  sketch-geometry (4):
    g0: LineSegment StartX=0 StartY=8.5 StartZ=0 EndX=0.1 EndY=8.5 EndZ=0
    g1: LineSegment StartX=0.1 StartY=8.5 StartZ=0 EndX=0.1 EndY=6.5 EndZ=0
    g2: LineSegment StartX=0.1 StartY=6.5 StartZ=0 EndX=0 EndY=6.5 EndZ=0
    g3: LineSegment StartX=0 StartY=6.5 StartZ=0 EndX=0 EndY=8.5 EndZ=0
  constraints (12):
    c: Coincident(g0,g1)
    c: Coincident(g1,g2)
    c: Coincident(g2,g3)
    c: Coincident(g3,g0)
    c: Horizontal(g0)
    c: Horizontal(g2)
    c: Vertical(g1)
    c: Vertical(g3)
    c: PointOnObject(g0,g-2)
    c: DistanceX(g0,g0) = 0.1
    c: DistanceY(g0) = 8.5
    c: DistanceY(g1) = 6.5
FEATURE [PartDesign::Revolution] Revolution006
  Angle = 360
  Axis = (1,0,0)
  Base = (0,0,0)
  Placement = pos=(0,0,0) rot=(1,0,0;1.5708rad)
  Profile = -> Sketch023
  ReferenceAxis = -> Sketch023 [H_Axis]
FEATURE [Sketcher::SketchObject] Sketch025
  FullyConstrained = true
  MapMode = 5
  Placement = pos=(0,0,0) rot=(0.57735,0.57735,0.57735;2.0944rad)
  Support = -> [YZ_Plane036]
  sketch-geometry (5):
    g0: ArcOfCircle CenterX=0 CenterY=7.5 CenterZ=0 NormalX=0 NormalY=0 NormalZ=1 AngleXU=0 Radius=2.11 StartAngle=5.66076 EndAngle=6.65667
    g1: LineSegment StartX=5e-16 StartY=8.5 StartZ=0 EndX=0 EndY=6.26986 EndZ=0
    g2: ArcOfCircle CenterX=0 CenterY=0 CenterZ=0 NormalX=0 NormalY=0 NormalZ=1 AngleXU=0 Radius=6.5 StartAngle=1.3039 EndAngle=1.5708
    g3: LineSegment StartX=1.71431 StartY=6.26986 StartZ=0 EndX=0 EndY=6.26986 EndZ=0
    g4: ArcOfCircle CenterX=0 CenterY=0 CenterZ=0 NormalX=0 NormalY=0 NormalZ=1 AngleXU=0 Radius=8.5 StartAngle=1.33757 EndAngle=1.5708
  constraints (16):
    c: PointOnObject(g0,g-2)
    c: DistanceY(g0) = 7.5
    c: Radius(g0) = 2.11
    c: PointOnObject(g2,g1)
    c: DistanceY(g2) = 6.5
    c: Coincident(g2,g-1)
    c: Coincident(g3,g2)
    c: Horizontal(g3)
    c: Coincident(g0,g2)
    c: Coincident(g1,g3)
    c: PointOnObject(g1,g-2)
    c: PointOnObject(g1,g-2)
    c: Coincident(g4,g-1)
    c: Coincident(g4,g1)
    c: DistanceY(g1) = 8.5
    c: Coincident(g0,g4)
FEATURE [PartDesign::Revolution] Revolution007
  Angle = 180
  Axis = (-2e-16,3e-16,1)
  Base = (0,0,0)
  BaseFeature = -> Revolution006
  Placement = pos=(0,0,0) rot=(1,0,0;1.5708rad)
  Profile = -> Sketch025
  ReferenceAxis = -> Sketch025 [V_Axis]
  Reversed = true
FEATURE [PartDesign::PolarPattern] PolarPattern
  Angle = 360
  Axis = -> Sketch025 [N_Axis]
  BaseFeature = -> Revolution007
  Occurrences = 3
  Originals = -> [Revolution007]
  Placement = pos=(0,0,0) rot=(1,0,0;1.5708rad)
  Refine = true
FEATURE [Sketcher::SketchObject] Sketch026
  FullyConstrained = true
  MapMode = 5
  Placement = pos=(0,0,0) rot=(0.57735,0.57735,0.57735;2.0944rad)
  Support = -> [YZ_Plane036]
  sketch-geometry (4):
    g0: ArcOfCircle CenterX=0 CenterY=7.5 CenterZ=0 NormalX=0 NormalY=0 NormalZ=1 AngleXU=0 Radius=2.01 StartAngle=5.57985 EndAngle=6.86228
    g1: LineSegment StartX=0 StartY=6.2 StartZ=0 EndX=1.533 EndY=6.2 EndZ=0
    g2: LineSegment StartX=0 StartY=8.6 StartZ=0 EndX=0 EndY=6.2 EndZ=0
    g3: LineSegment StartX=0 StartY=8.6 StartZ=0 EndX=1.68229 EndY=8.6 EndZ=0
  constraints (13):
    c: PointOnObject(g0,g-2)
    c: DistanceY(g0) = 7.5
    c: Radius(g0) = 2.01
    c: PointOnObject(g1,g-2)
    c: Horizontal(g1)
    c: Coincident(g0,g1)
    c: DistanceY(g1) = 6.2
    c: DistanceY(g2) = 8.6
    c: Coincident(g2,g1)
    c: PointOnObject(g2,g-2)
    c: Coincident(g3,g2)
    c: Horizontal(g3)
    c: Coincident(g0,g3)
FEATURE [PartDesign::Groove] Groove
  Angle = 360
  Axis = (-2e-16,3e-16,1)
  Base = (0,0,0)
  BaseFeature = -> PolarPattern
  Placement = pos=(0,0,0) rot=(1,0,0;1.5708rad)
  Profile = -> Sketch026
  ReferenceAxis = -> Sketch026 [V_Axis]
FEATURE [PartDesign::PolarPattern] PolarPattern001
  Angle = 360
  Axis = -> Sketch026 [N_Axis]
  BaseFeature = -> Groove
  Occurrences = 3
  Originals = -> [Groove]
  Placement = pos=(0,0,0) rot=(1,0,0;1.5708rad)
FEATURE [PartDesign::Pocket] Pocket
  BaseFeature = -> PolarPattern001
  Length = 5
  Length2 = 100
  Placement = pos=(0,0,0) rot=(1,0,0;1.5708rad)
  Profile = -> Sketch014
  Type = 1
FEATURE [PartDesign::PolarPattern] PolarPattern002
  Angle = 360
  Axis = -> Sketch014 [N_Axis]
  BaseFeature = -> Pocket
  Occurrences = 3
  Originals = -> [Pocket]
  Placement = pos=(0,0,0) rot=(1,0,0;1.5708rad)
FEATURE [PartDesign::Body] Body022  label="Cage 001"
  Group = -> [Sketch023,Revolution006,Sketch025,Revolution007,PolarPattern,Sketch026,Groove,PolarPattern001,Sketch014,Pocket,PolarPattern002]
  Origin = -> Origin036
  Placement = pos=(0,0,0) rot=(-1,0,0;1.5708rad)
  Tip = -> PolarPattern002
FEATURE [PartDesign::FeatureBase] Clone006
  BaseFeature = -> Body022
  Placement = pos=(0,0,0) rot=(-1,0,0;1.5708rad)
FEATURE [PartDesign::Body] Body023  label="Cage 002"
  BaseFeature = -> Body022
  Group = -> [Clone006]
  Origin = -> Origin037
  Placement = pos=(0,0,0) rot=(0,1,0;3.14159rad)
  Tip = -> Clone006
FEATURE [App::DocumentObjectGroup] Group001  label="Cages"
  Group = -> [Body022,Body023]
FEATURE [Sketcher::SketchObject] Sketch027
  FullyConstrained = true
  MapMode = 5
  Support = -> [XY_Plane045]
  sketch-geometry (14):
    g0: ArcOfCircle CenterX=-1e-16 CenterY=7.5 CenterZ=0 NormalX=0 NormalY=0 NormalZ=1 AngleXU=0 Radius=2 StartAngle=0.848062 EndAngle=2.29353
    g1: LineSegment StartX=-3.5 StartY=11 StartZ=0 EndX=3.5 EndY=11 EndZ=0
    g2: LineSegment StartX=3.5 StartY=11 StartZ=0 EndX=3.5 EndY=9.2 EndZ=0
    g3: LineSegment StartX=2.9 StartY=9 StartZ=0 EndX=1.32288 EndY=9 EndZ=0
    g4: LineSegment StartX=-3.5 StartY=9.2 StartZ=0 EndX=-3.5 EndY=11 EndZ=0
    g5: LineSegment StartX=-1.32288 StartY=9 StartZ=0 EndX=-2.9 EndY=9 EndZ=0
    g6: LineSegment StartX=2.9 StartY=9 StartZ=0 EndX=2.9 EndY=9.5 EndZ=0
    g7: LineSegment StartX=2.9 StartY=9.5 StartZ=0 EndX=3.2 EndY=9.5 EndZ=0
    g8: LineSegment StartX=3.2 StartY=9.5 StartZ=0 EndX=3.2 EndY=9.2 EndZ=0
    g9: LineSegment StartX=3.2 StartY=9.2 StartZ=0 EndX=3.5 EndY=9.2 EndZ=0
    g10: LineSegment StartX=-3.5 StartY=9.2 StartZ=0 EndX=-3.2 EndY=9.2 EndZ=0
    g11: LineSegment StartX=-3.2 StartY=9.2 StartZ=0 EndX=-3.2 EndY=9.5 EndZ=0
    g12: LineSegment StartX=-3.2 StartY=9.5 StartZ=0 EndX=-2.9 EndY=9.5 EndZ=0
    g13: LineSegment StartX=-2.9 StartY=9.5 StartZ=0 EndX=-2.9 EndY=9 EndZ=0
  constraints (41):
    c: Coincident(g1,g2)
    c: Coincident(g4,g1)
    c: Horizontal(g3)
    c: Vertical(g2)
    c: Vertical(g4)
    c: Coincident(g0,g5)
    c: Coincident(g0,g3)
    c: DistanceY(g-1,g0) = 7.5
    c: Radius(g0) = 2
    c: Symmetric(g1,g1,g-2)
    c: Symmetric(g0,g0,g-2)
    c: DistanceY(g1) = 11
    c: DistanceX(g1,g1) = 7
    c: Vertical(g6)
    c: Coincident(g6,g7)
    c: Horizontal(g7)
    c: Coincident(g7,g8)
    c: Vertical(g8)
    c: Coincident(g8,g9)
    c: Coincident(g3,g6)
    c: Coincident(g2,g9)
    c: Horizontal(g10)
    c: Coincident(g10,g11)
    c: Coincident(g11,g12)
    c: Horizontal(g12)
    c: Coincident(g12,g13)
    c: Vertical(g13)
    c: Vertical(g11)
    c: Coincident(g4,g10)
    c: Coincident(g5,g13)
    c: DistanceY(g13,g13) = 0.5
    c: DistanceX(g12,g12) = 0.3
    c: DistanceY(g5,g10) = 0.2
    c: Symmetric(g5,g3,g-2)
    c: DistanceY(g3) = 9
    c: DistanceY(g6) = 9.5
    c: Equal(g7,g12)
    c: Equal(g13,g6)
    c: Horizontal(g9)
    c: Horizontal(g8,g10)
    c: Equal(g12,g10)
FEATURE [PartDesign::Revolution] Revolution008
  Angle = 360
  Axis = (1,0,0)
  Base = (0,0,0)
  Profile = -> Sketch027
  ReferenceAxis = -> X_Axis045
FEATURE [PartDesign::Fillet] Fillet154
  Base = -> Revolution008 [Edge14,Edge15]
  BaseFeature = -> Revolution008
  Radius = 0.3
  SupportTransform = false
FEATURE [PartDesign::Body] Body031  label="Outer Ring001"
  Group = -> [Sketch027,Revolution008,Fillet154]
  Origin = -> Origin045
  Tip = -> Fillet154
FEATURE [Sketcher::SketchObject] Sketch028
  FullyConstrained = true
  MapMode = 5
  Support = -> [XY_Plane046]
  sketch-geometry (14):
    g0: LineSegment StartX=-2.9 StartY=6 StartZ=0 EndX=-1.32288 EndY=6 EndZ=0
    g1: LineSegment StartX=-3.5 StartY=4 StartZ=0 EndX=-3.5 EndY=5.7 EndZ=0
    g2: ArcOfCircle CenterX=-1e-16 CenterY=7.5 CenterZ=0 NormalX=0 NormalY=0 NormalZ=1 AngleXU=0 Radius=2 StartAngle=3.98965 EndAngle=5.43512
    g3: LineSegment StartX=1.32288 StartY=6 StartZ=0 EndX=2.9 EndY=6 EndZ=0
    g4: LineSegment StartX=-3.5 StartY=5.7 StartZ=0 EndX=-3.2 EndY=5.7 EndZ=0
    g5: LineSegment StartX=-3.2 StartY=5.7 StartZ=0 EndX=-3.2 EndY=5.5 EndZ=0
    g6: LineSegment StartX=-3.2 StartY=5.5 StartZ=0 EndX=-2.9 EndY=5.5 EndZ=0
    g7: LineSegment StartX=-2.9 StartY=5.5 StartZ=0 EndX=-2.9 EndY=6 EndZ=0
    g8: LineSegment StartX=8.5 StartY=6 StartZ=0 EndX=3.2 EndY=6 EndZ=0
    g9: LineSegment StartX=3.2 StartY=6 StartZ=0 EndX=3.2 EndY=5.5 EndZ=0
    g10: LineSegment StartX=3.2 StartY=5.5 StartZ=0 EndX=2.9 EndY=5.5 EndZ=0
    g11: LineSegment StartX=2.9 StartY=5.5 StartZ=0 EndX=2.9 EndY=6 EndZ=0
    g12: LineSegment StartX=8.5 StartY=4 StartZ=0 EndX=8.5 EndY=6 EndZ=0
    g13: LineSegment StartX=-3.5 StartY=4 StartZ=0 EndX=8.5 EndY=4 EndZ=0
  constraints (43):
    c: Horizontal(g0)
    c: Vertical(g1)
    c: DistanceY(g1) = 4
    c: Coincident(g2,g0)
    c: Coincident(g2,g3)
    c: Horizontal(g3)
    c: Radius(g2) = 2
    c: DistanceY(g2) = 7.5
    c: Symmetric(g0,g2,g-2)
    c: Horizontal(g4)
    c: Coincident(g4,g5)
    c: Vertical(g5)
    c: Coincident(g5,g6)
    c: Horizontal(g6)
    c: Coincident(g6,g7)
    c: Vertical(g7)
    c: Horizontal(g8)
    c: Coincident(g8,g9)
    c: Vertical(g9)
    c: Coincident(g9,g10)
    c: Horizontal(g10)
    c: Coincident(g10,g11)
    c: Vertical(g11)
    c: Coincident(g3,g11)
    c: Coincident(g0,g7)
    c: Coincident(g1,g4)
    c: DistanceY(g3) = 6
    c: DistanceY(g6,g0) = 0.5
    c: DistanceX(g4,g4) = 0.3
    c: DistanceX(g6,g6) = 0.3
    c: DistanceY(g5,g4) = 0.2
    c: Vertical(g12)
    c: Equal(g11,g7)
    c: DistanceY(g1,g0) = 2
    c: DistanceX(g8,g8) = 5.3
    c: Coincident(g13,g1)
    c: Coincident(g13,g12)
    c: Horizontal(g13)
    c: DistanceX(g13,g13) = 12
    c: DistanceX(g1,g2) = 3.5
    c: Coincident(g8,g12)
    c: Equal(g7,g9)
    c: Equal(g6,g10)
FEATURE [PartDesign::Revolution] Revolution009
  Angle = 360
  Axis = (1,0,0)
  Base = (0,0,0)
  Profile = -> Sketch028
  ReferenceAxis = -> X_Axis046
FEATURE [PartDesign::Fillet] Fillet155
  Base = -> Revolution009 [Edge13,Edge11]
  BaseFeature = -> Revolution009
  Radius = 0.2
  SupportTransform = false
FEATURE [PartDesign::Body] Body032  label="Inner Ring001"
  Group = -> [Sketch028,Revolution009,Fillet155]
  Origin = -> Origin046
  Tip = -> Fillet155
FEATURE [App::DocumentObjectGroup] Group004  label="Rings"
  Group = -> [Body031,Body032]
FEATURE [Sketcher::SketchObject] Sketch029
  FullyConstrained = true
  MapMode = 5
  Placement = pos=(0,0,0) rot=(1,0,0;1.5708rad)
  Support = -> [XZ_Plane047]
  sketch-geometry (12):
    g0: LineSegment StartX=2.9 StartY=9.5 StartZ=0 EndX=2.9 EndY=8.5 EndZ=0
    g1: LineSegment StartX=2.9 StartY=8.5 StartZ=0 EndX=3.2 EndY=8.5 EndZ=0
    g2: LineSegment StartX=3.2 StartY=8.5 StartZ=0 EndX=3.2 EndY=6.5 EndZ=0
    g3: LineSegment StartX=3.2 StartY=6.5 StartZ=0 EndX=2.9 EndY=6.5 EndZ=0
    g4: LineSegment StartX=2.9 StartY=6.5 StartZ=0 EndX=2.9 EndY=5.5 EndZ=0
    g5: LineSegment StartX=2.9 StartY=5.5 StartZ=0 EndX=3.2 EndY=5.5 EndZ=0
    g6: LineSegment StartX=3.2 StartY=5.5 StartZ=0 EndX=3.2 EndY=6 EndZ=0
    g7: LineSegment StartX=3.2 StartY=6 StartZ=0 EndX=3.5 EndY=6 EndZ=0
    g8: LineSegment StartX=3.5 StartY=6 StartZ=0 EndX=3.5 EndY=9 EndZ=0
    g9: LineSegment StartX=3.5 StartY=9 StartZ=0 EndX=3.2 EndY=9 EndZ=0
    g10: LineSegment StartX=3.2 StartY=9 StartZ=0 EndX=3.2 EndY=9.5 EndZ=0
    g11: LineSegment StartX=3.2 StartY=9.5 StartZ=0 EndX=2.9 EndY=9.5 EndZ=0
  constraints (36):
    c: Vertical(g0)
    c: Coincident(g0,g1)
    c: Horizontal(g1)
    c: Coincident(g1,g2)
    c: Vertical(g2)
    c: Coincident(g2,g3)
    c: Horizontal(g3)
    c: Coincident(g3,g4)
    c: Vertical(g4)
    c: Coincident(g4,g5)
    c: Horizontal(g5)
    c: Coincident(g5,g6)
    c: Vertical(g6)
    c: Coincident(g6,g7)
    c: Horizontal(g7)
    c: Coincident(g7,g8)
    c: Vertical(g8)
    c: Coincident(g8,g9)
    c: Horizontal(g9)
    c: Coincident(g9,g10)
    c: Vertical(g10)
    c: Coincident(g10,g11)
    c: Coincident(g11,g0)
    c: Horizontal(g11)
    c: DistanceY(g4) = 5.5
    c: DistanceX(g4) = 2.9
    c: DistanceY(g5,g6) = 0.5
    c: DistanceY(g6,g2) = 0.5
    c: DistanceX(g5,g5) = 0.3
    c: Equal(g5,g7)
    c: Equal(g7,g3)
    c: Equal(g3,g1)
    c: Equal(g1,g9)
    c: Equal(g4,g0)
    c: Equal(g6,g10)
    c: DistanceY(g4,g0) = 4
FEATURE [PartDesign::Revolution] Revolution010
  Angle = 360
  Axis = (1,0,0)
  Base = (0,0,0)
  Placement = pos=(0,0,0) rot=(1,0,0;1.5708rad)
  Profile = -> Sketch029
  ReferenceAxis = -> Sketch029 [H_Axis]
FEATURE [PartDesign::Fillet] Fillet156
  Base = -> Revolution010 [Edge14,Edge12]
  BaseFeature = -> Revolution010
  Placement = pos=(0,0,0) rot=(1,0,0;1.5708rad)
  Radius = 0.2
  SupportTransform = false
FEATURE [PartDesign::Body] Body033  label="Seal 001"
  Group = -> [Sketch029,Revolution010,Fillet156]
  Origin = -> Origin047
  Tip = -> Fillet156
FEATURE [PartDesign::FeatureBase] Clone013
  BaseFeature = -> Body033
FEATURE [PartDesign::Body] Body034  label="Seal 002"
  BaseFeature = -> Body033
  Group = -> [Clone013]
  Origin = -> Origin048
  Placement = pos=(0,0,0) rot=(0,1,0;3.14159rad)
  Tip = -> Clone013
FEATURE [App::DocumentObjectGroup] Group003  label="Seals"
  Group = -> [Body033,Body034]
FEATURE [Sketcher::SketchObject] Sketch030
  AttachmentOffset = pos=(0,0,4) rot=(0,0,1;0rad)
  FullyConstrained = true
  MapMode = 5
  Placement = pos=(0,0,4) rot=(0,0,1;0rad)
  Support = -> [XY_Plane028]
  sketch-geometry (1):
    g0: Circle CenterX=6 CenterY=0 CenterZ=0 NormalX=0 NormalY=0 NormalZ=1 AngleXU=0 Radius=1.5
  constraints (3):
    c: PointOnObject(g0,g-1)
    c: Diameter(g0) = 3
    c: DistanceX(g-1,g0) = 6
FEATURE [PartDesign::Pad] Pad014
  Direction = (0,0,1)
  Length = 3
  Length2 = 100
  Profile = -> Sketch030
  Type = 0
FEATURE [Sketcher::SketchObject] Sketch031
  ExternalGeometry = -> [Pad014]
  FullyConstrained = true
  MapMode = 5
  Placement = pos=(0,0,7) rot=(0,0,1;0rad)
  Support = -> [Pad014]
  sketch-geometry (7):
    g0: LineSegment StartX=6.43301 StartY=-0.75 StartZ=0 EndX=6.86603 EndY=0 EndZ=0
    g1: LineSegment StartX=6.86603 StartY=0 StartZ=0 EndX=6.43301 EndY=0.75 EndZ=0
    g2: LineSegment StartX=6.43301 StartY=0.75 StartZ=0 EndX=5.56699 EndY=0.75 EndZ=0
    g3: LineSegment StartX=5.56699 StartY=0.75 StartZ=0 EndX=5.13397 EndY=-1e-16 EndZ=0
    g4: LineSegment StartX=5.13397 StartY=-1e-16 StartZ=0 EndX=5.56699 EndY=-0.75 EndZ=0
    g5: LineSegment StartX=5.56699 StartY=-0.75 StartZ=0 EndX=6.43301 EndY=-0.75 EndZ=0
    g6: Circle CenterX=6 CenterY=0 CenterZ=0 NormalX=0 NormalY=0 NormalZ=1 AngleXU=0 Radius=0.866025
  constraints (16):
    c: Coincident(g0,g1)
    c: Coincident(g1,g2)
    c: Coincident(g2,g3)
    c: Coincident(g3,g4)
    c: Coincident(g4,g5)
    c: Coincident(g5,g0)
    c: Equal(g0, g1-g5) x5
    c: PointOnObject(g0,g6)
    c: PointOnObject(g1,g6)
    c: PointOnObject(g2,g6)
    c: PointOnObject(g3,g6)
    c: PointOnObject(g4,g6)
    c: PointOnObject(g5,g6)
    c: Coincident(g6,g-3)
    c: Horizontal(g5)
    c: DistanceY(g4,g2) = 1.5
FEATURE [PartDesign::Pocket] Pocket001
  BaseFeature = -> Pad014
  Length = 0.9
  Length2 = 100
  Profile = -> Sketch031
  Type = 0
FEATURE [PartDesign::PolarPattern] PolarPattern003
  Angle = 120
  Axis = -> X_Axis028
  BaseFeature = -> Pocket001
  Occurrences = 3
  Originals = -> [Pad014,Pocket001]
FEATURE [PartDesign::Body] Body014
  Group = -> [Sketch030,Pad014,Sketch031,Pocket001,PolarPattern003]
  Origin = -> Origin028
  Tip = -> PolarPattern003
FEATURE [App::DocumentObjectGroup] Group005  label="Set screws"
  Group = -> [Body014]
FEATURE [Sketcher::SketchObject] Sketch032
  AttachmentOffset = pos=(0,0,-6.5) rot=(0,0,1;0rad)
  FullyConstrained = true
  MapMode = 5
  Placement = pos=(-6.5,1.4e-15,-1.4e-15) rot=(0.57735,0.57735,0.57735;2.0944rad)
  Support = -> [YZ_Plane049]
  sketch-geometry (14):
    g0: Circle CenterX=0 CenterY=0 CenterZ=0 NormalX=0 NormalY=0 NormalZ=1 AngleXU=0 Radius=11
    g1: ArcOfCircle CenterX=0 CenterY=0 CenterZ=0 NormalX=0 NormalY=0 NormalZ=1 AngleXU=0 Radius=13.5 StartAngle=0.0668757 EndAngle=3.07472
    g2: LineSegment StartX=-13.4698 StartY=0.902148 StartZ=0 EndX=-14.2 EndY=-10 EndZ=0
    g3: LineSegment StartX=-14.2 StartY=-10 StartZ=0 EndX=-27.5 EndY=-10 EndZ=0
    g4: LineSegment StartX=-27.5 StartY=-10 StartZ=0 EndX=-27.5 EndY=-15 EndZ=0
    g5: LineSegment StartX=-27.5 StartY=-15 StartZ=0 EndX=-12.3 EndY=-15 EndZ=0
    g6: LineSegment StartX=27.5 StartY=-15 StartZ=0 EndX=27.5 EndY=-10 EndZ=0
    g7: LineSegment StartX=27.5 StartY=-10 StartZ=0 EndX=14.2 EndY=-10 EndZ=0
    g8: LineSegment StartX=14.2 StartY=-10 StartZ=0 EndX=13.4698 EndY=0.902148 EndZ=0
    g9: LineSegment StartX=12.3 StartY=-15 StartZ=0 EndX=12.1995 EndY=-13.5 EndZ=0
    g10: LineSegment StartX=12.1995 StartY=-13.5 StartZ=0 EndX=-12.1995 EndY=-13.5 EndZ=0
    g11: LineSegment StartX=-12.1995 StartY=-13.5 StartZ=0 EndX=-12.3 EndY=-15 EndZ=0
    g12: LineSegment StartX=12.3 StartY=-15 StartZ=0 EndX=27.5 EndY=-15 EndZ=0
    g13: GeomPoint X=0 Y=13.5 Z=0
  constraints (39):
    c: Coincident(g0,g-1)
    c: Radius(g0) = 11
    c: Coincident(g1,g0)
    c: Coincident(g2,g3)
    c: Coincident(g3,g4)
    c: Coincident(g4,g5)
    c: Horizontal(g5)
    c: Coincident(g12,g6)
    c: Coincident(g6,g7)
    c: Horizontal(g7)
    c: Coincident(g7,g8)
    c: Coincident(g9,g10)
    c: Horizontal(g10)
    c: Coincident(g10,g11)
    c: Coincident(g5,g11)
    c: Coincident(g12,g9)
    c: Horizontal(g3)
    c: Vertical(g6)
    c: Vertical(g4)
    c: Equal(g9,g11)
    c: Horizontal(g12)
    c: Horizontal(g5,g9)
    c: Equal(g6,g4)
    c: Equal(g12,g5)
    c: Equal(g7,g3)
    c: DistanceX(g4,g6) = 55
    c: DistanceY(g6,g0) = 15
    c: Equal(g8,g2)
    c: DistanceY(g6,g6) = 5
    c: Parallel(g9,g8)
    c: DistanceY(g9,g9) = 1.5
    c: DistanceX(g5,g5) = 15.2
    c: Diameter(g1) = 27
    c: PointOnObject(g13,g1)
    c: PointOnObject(g13,g-2)
    c: DistanceY(g6,g13) = 28.5
    c: Tangent(g1,g2) = -1.5708
    c: Tangent(g1,g8) = -1.5708
    c: DistanceX(g3,g3) = 13.3
FEATURE [PartDesign::Pad] Pad015
  Direction = (1,-2e-16,3e-16)
  Length = 13
  Length2 = 100
  Placement = pos=(0,0,0) rot=(0.57735,0.57735,0.57735;2.0944rad)
  Profile = -> Sketch032
  Type = 0
FEATURE [Sketcher::SketchObject] Sketch033
  ExternalGeometry = -> [Pad015]
  FullyConstrained = true
  MapMode = 5
  Placement = pos=(4.2e-15,-6.6e-15,-15) rot=(0.707107,0.707107,0;3.14159rad)
  Support = -> [Pad015]
  sketch-geometry (7):
    g0: LineSegment StartX=-24.9 StartY=4.15 StartZ=0 EndX=-14.9 EndY=4.15 EndZ=0
    g1: LineSegment StartX=-14.9 StartY=4.15 StartZ=0 EndX=-14.9 EndY=-4.15 EndZ=0
    g2: LineSegment StartX=-14.9 StartY=-4.15 StartZ=0 EndX=-24.9 EndY=-4.15 EndZ=0
    g3: LineSegment StartX=-24.9 StartY=-4.15 StartZ=0 EndX=-24.9 EndY=4.15 EndZ=0
    g4: LineSegment StartX=-27.5 StartY=6.5 StartZ=0 EndX=-12.3 EndY=-6.5 EndZ=0
    g5: LineSegment StartX=-27.5 StartY=-6.5 StartZ=0 EndX=-12.3 EndY=6.5 EndZ=0
    g6: GeomPoint X=-19.9 Y=2.6e-15 Z=0
  constraints (17):
    c: Coincident(g0,g1)
    c: Coincident(g1,g2)
    c: Coincident(g2,g3)
    c: Coincident(g3,g0)
    c: Horizontal(g0)
    c: Horizontal(g2)
    c: Vertical(g1)
    c: Vertical(g3)
    c: DistanceX(g0,g0) = 10
    c: DistanceY(g1,g1) = 8.3
    c: Coincident(g4,g-3)
    c: Coincident(g4,g-4)
    c: Coincident(g5,g-4)
    c: Coincident(g5,g-3)
    c: PointOnObject(g6,g4)
    c: PointOnObject(g6,g5)
    c: Symmetric(g0,g1,g6)
FEATURE [PartDesign::Pocket] Pocket002
  BaseFeature = -> Pad015
  Length = 2.3
  Length2 = 100
  Placement = pos=(0,0,0) rot=(0.57735,0.57735,0.57735;2.0944rad)
  Profile = -> Sketch033
  Type = 0
FEATURE [Sketcher::SketchObject] Sketch034
  ExternalGeometry = -> [Pocket002]
  FullyConstrained = true
  MapMode = 5
  Placement = pos=(2.8e-15,-4.4e-15,-10) rot=(0,0,-1;1.5708rad)
  Support = -> [Pocket002]
  sketch-geometry (2):
    g0: Circle CenterX=21.2 CenterY=2.1e-15 CenterZ=0 NormalX=0 NormalY=0 NormalZ=1 AngleXU=0 Radius=2.5
    g1: LineSegment StartX=21.2 StartY=2.1e-15 StartZ=0 EndX=27.5 EndY=2.1e-15 EndZ=0
  constraints (5):
    c: Diameter(g0) = 5
    c: DistanceX(g0,g-3) = 6.3
    c: Coincident(g1,g0)
    c: Horizontal(g1)
    c: Symmetric(g-5,g-5,g1)
FEATURE [PartDesign::Pocket] Pocket003
  BaseFeature = -> Pocket002
  Length = 5
  Length2 = 100
  Placement = pos=(0,0,0) rot=(0.57735,0.57735,0.57735;2.0944rad)
  Profile = -> Sketch034
  Type = 2
FEATURE [Sketcher::SketchObject] Sketch035
  ExternalGeometry = -> [Pocket003]
  FullyConstrained = true
  MapMode = 5
  Placement = pos=(6.5,-1.4e-15,1.5e-15) rot=(0.57735,0.57735,0.57735;2.0944rad)
  Support = -> [Pocket003]
  sketch-geometry (6):
    g0: LineSegment StartX=-24.6 StartY=-13.7 StartZ=0 EndX=-24.6 EndY=-11.3 EndZ=0
    g1: LineSegment StartX=-24.6 StartY=-11.3 StartZ=0 EndX=-14.2 EndY=-11.3 EndZ=0
    g2: LineSegment StartX=-14.2 StartY=-11.3 StartZ=0 EndX=-14.2 EndY=-13.7 EndZ=0
    g3: LineSegment StartX=-14.2 StartY=-13.7 StartZ=0 EndX=-24.6 EndY=-13.7 EndZ=0
    g4: GeomPoint X=-19.4 Y=-12.5 Z=0
    g5: LineSegment StartX=-19.4 StartY=-12.5 StartZ=0 EndX=-27.5 EndY=-12.5 EndZ=0
  constraints (15):
    c: Coincident(g0,g1)
    c: Coincident(g1,g2)
    c: Coincident(g2,g3)
    c: Coincident(g3,g0)
    c: Horizontal(g1)
    c: Horizontal(g3)
    c: Vertical(g0)
    c: Vertical(g2)
    c: Symmetric(g1,g0,g4)
    c: DistanceX(g1,g1) = 10.4
    c: DistanceY(g2,g2) = 2.4
    c: DistanceX(g2,g-4) = 1.9
    c: Coincident(g5,g4)
    c: Horizontal(g5)
    c: Symmetric(g-5,g-5,g5)
FEATURE [PartDesign::Pocket] Pocket004
  BaseFeature = -> Pocket003
  Length = 0.4
  Length2 = 100
  Placement = pos=(0,0,0) rot=(0.57735,0.57735,0.57735;2.0944rad)
  Profile = -> Sketch035
  Type = 0
FEATURE [PartDesign::Mirrored] Mirrored
  BaseFeature = -> Pocket004
  MirrorPlane = -> Sketch033 [V_Axis]
  Originals = -> [Pocket002,Pocket003,Pocket004]
  Placement = pos=(0,0,0) rot=(0.57735,0.57735,0.57735;2.0944rad)
FEATURE [Sketcher::SketchObject] Sketch036
  ExternalGeometry = -> [Mirrored]
  FullyConstrained = true
  MapMode = 5
  Placement = pos=(0,0,0) rot=(1,0,0;1.5708rad)
  Support = -> [XZ_Plane049]
  sketch-geometry (9):
    g0: GeomPoint X=-6.5 Y=13.5 Z=0
    g1: LineSegment StartX=6.5 StartY=-10 StartZ=0 EndX=6.5 EndY=13.5 EndZ=0
    g2: LineSegment StartX=6.5 StartY=13.5 StartZ=0 EndX=4.75 EndY=13.5 EndZ=0
    g3: LineSegment StartX=-6.5 StartY=13.5 StartZ=0 EndX=-4.75 EndY=13.5 EndZ=0
    g4: LineSegment StartX=-6.5 StartY=-10 StartZ=0 EndX=-6.5 EndY=13.5 EndZ=0
    g5: LineSegment StartX=6.5 StartY=-10 StartZ=0 EndX=4.75 EndY=-1 EndZ=0
    g6: LineSegment StartX=4.75 StartY=-1 StartZ=0 EndX=4.75 EndY=13.5 EndZ=0
    g7: LineSegment StartX=-4.75 StartY=13.5 StartZ=0 EndX=-4.75 EndY=-1 EndZ=0
    g8: LineSegment StartX=-4.75 StartY=-1 StartZ=0 EndX=-6.5 EndY=-10 EndZ=0
  constraints (24):
    c: Vertical(g0,g-4)
    c: Horizontal(g-3,g0)
    c: Coincident(g1,g-3)
    c: Coincident(g1,g2)
    c: Horizontal(g2)
    c: Coincident(g3,g0)
    c: Horizontal(g3)
    c: Coincident(g4,g3)
    c: Vertical(g4,g-4)
    c: DistanceX(g3,g2) = 9.5
    c: Equal(g2,g3)
    c: Horizontal(g1,g4)
    c: Coincident(g1,g-5)
    c: Coincident(g1,g5)
    c: Coincident(g5,g6)
    c: Coincident(g6,g2)
    c: Vertical(g6)
    c: DistanceY(g1,g5) = 9
    c: Coincident(g3,g7)
    c: Vertical(g7)
    c: Coincident(g7,g8)
    c: Coincident(g8,g4)
    c: Horizontal(g7,g5)
    c: DistanceX(g2,g2) = 1.75
FEATURE [PartDesign::Pocket] Pocket005
  BaseFeature = -> Mirrored
  Length = 15
  Length2 = 15
  Placement = pos=(0,0,0) rot=(0.57735,0.57735,0.57735;2.0944rad)
  Profile = -> Sketch036
  Type = 4
FEATURE [Sketcher::SketchObject] Sketch037
  FullyConstrained = true
  MapMode = 5
  Placement = pos=(-6.5,1.4e-15,-1.5e-15) rot=(0.57735,0.57735,-0.57735;4.18879rad)
  Support = -> [Pocket005]
  sketch-geometry (1):
    g0: Circle CenterX=0 CenterY=0 CenterZ=0 NormalX=0 NormalY=0 NormalZ=1 AngleXU=0 Radius=12.2
  constraints (2):
    c: Coincident(g0,g-1)
    c: Diameter(g0) = 24.4
FEATURE [PartDesign::Pocket] Pocket006
  BaseFeature = -> Pocket005
  Length = 2.75
  Length2 = 100
  Placement = pos=(0,0,0) rot=(0.57735,0.57735,0.57735;2.0944rad)
  Profile = -> Sketch037
  Type = 0
FEATURE [Sketcher::SketchObject] Sketch038
  FullyConstrained = true
  MapMode = 5
  Placement = pos=(6.5,-1.4e-15,1.5e-15) rot=(0.57735,0.57735,0.57735;2.0944rad)
  Support = -> [Pocket006]
  sketch-geometry (1):
    g0: Circle CenterX=0 CenterY=0 CenterZ=0 NormalX=0 NormalY=0 NormalZ=1 AngleXU=0 Radius=12.1
  constraints (2):
    c: Coincident(g0,g-1)
    c: Diameter(g0) = 24.2
FEATURE [PartDesign::Pocket] Pocket007
  BaseFeature = -> Pocket006
  Length = 2.75
  Length2 = 100
  Placement = pos=(0,0,0) rot=(0.57735,0.57735,0.57735;2.0944rad)
  Profile = -> Sketch038
  Type = 0
FEATURE [Sketcher::SketchObject] Sketch039
  ExternalGeometry = -> [Pocket007]
  FullyConstrained = true
  MapMode = 5
  Placement = pos=(6.5,-1.4e-15,1.5e-15) rot=(0.57735,0.57735,0.57735;2.0944rad)
  Support = -> [Pocket007]
  sketch-geometry (6):
    g0: ArcOfCircle CenterX=0 CenterY=0 CenterZ=0 NormalX=0 NormalY=0 NormalZ=1 AngleXU=0 Radius=13.5 StartAngle=3.79664 EndAngle=5.62814
    g1: LineSegment StartX=-11.8698 StartY=-8.57666 StartZ=0 EndX=-12.3 EndY=-15 EndZ=0
    g2: LineSegment StartX=-12.3 StartY=-15 StartZ=0 EndX=12.3 EndY=-15 EndZ=0
    g3: LineSegment StartX=12.3 StartY=-15 StartZ=0 EndX=11.8698 EndY=-8.57666 EndZ=0
    g4: ArcOfCircle CenterX=11.2212 CenterY=-8.6201 CenterZ=0 NormalX=0 NormalY=0 NormalZ=1 AngleXU=0 Radius=0.65 StartAngle=0.0668757 EndAngle=2.48655
    g5: ArcOfCircle CenterX=-11.2212 CenterY=-8.6201 CenterZ=0 NormalX=0 NormalY=0 NormalZ=1 AngleXU=0 Radius=0.65 StartAngle=0.655044 EndAngle=3.07472
  constraints (14):
    c: Coincident(g0,g-1)
    c: Diameter(g0) = 27
    c: Coincident(g1,g2)
    c: Coincident(g2,g3)
    c: Coincident(g1,g-3)
    c: Coincident(g2,g-4)
    c: Tangent(g3,g4) = -1.5708
    c: Tangent(g0,g4) = 1.5708
    c: Tangent(g0,g5) = 1.5708
    c: Tangent(g1,g5) = -1.5708
    c: Equal(g4,g5)
    c: Horizontal(g4,g5)
    c: Parallel(g-4,g3)
    c: Radius(g4) = 0.65
FEATURE [PartDesign::Pocket] Pocket008
  BaseFeature = -> Pocket007
  Length = 5.25
  Length2 = 100
  Placement = pos=(0,0,0) rot=(0.57735,0.57735,0.57735;2.0944rad)
  Profile = -> Sketch039
  Type = 0
FEATURE [Sketcher::SketchObject] Sketch040
  ExternalGeometry = -> [Pocket008]
  FullyConstrained = true
  MapMode = 5
  Placement = pos=(-6.5,1.4e-15,-1.5e-15) rot=(0.57735,0.57735,-0.57735;4.18879rad)
  Support = -> [Pocket008]
  sketch-geometry (6):
    g0: ArcOfCircle CenterX=0 CenterY=0 CenterZ=0 NormalX=0 NormalY=0 NormalZ=1 AngleXU=0 Radius=13.5 StartAngle=0.655044 EndAngle=2.48655
    g1: LineSegment StartX=11.8698 StartY=8.57666 StartZ=0 EndX=12.3 EndY=15 EndZ=0
    g2: LineSegment StartX=12.3 StartY=15 StartZ=0 EndX=-12.3 EndY=15 EndZ=0
    g3: LineSegment StartX=-12.3 StartY=15 StartZ=0 EndX=-11.8698 EndY=8.57666 EndZ=0
    g4: ArcOfCircle CenterX=-11.2212 CenterY=8.6201 CenterZ=0 NormalX=0 NormalY=0 NormalZ=1 AngleXU=0 Radius=0.65 StartAngle=3.20847 EndAngle=5.62814
    g5: ArcOfCircle CenterX=11.2212 CenterY=8.6201 CenterZ=0 NormalX=0 NormalY=0 NormalZ=1 AngleXU=0 Radius=0.65 StartAngle=3.79664 EndAngle=6.21631
  constraints (14):
    c: Coincident(g0,g-1)
    c: Radius(g0) = 13.5
    c: Coincident(g1,g2)
    c: Coincident(g2,g-3)
    c: Coincident(g2,g3)
    c: Coincident(g-4,g1)
    c: Tangent(g3,g4) = -1.5708
    c: Tangent(g0,g4) = 1.5708
    c: Tangent(g0,g5) = 1.5708
    c: Tangent(g1,g5) = -1.5708
    c: Equal(g4,g5)
    c: Radius(g4) = 0.65
    c: Parallel(g-4,g1)
    c: Parallel(g3,g-3)
FEATURE [PartDesign::Pocket] Pocket009
  BaseFeature = -> Pocket008
  Length = 5.25
  Length2 = 100
  Placement = pos=(0,0,0) rot=(0.57735,0.57735,0.57735;2.0944rad)
  Profile = -> Sketch040
  Type = 0
FEATURE [PartDesign::Chamfer] Chamfer
  Angle = 45
  Base = -> Pocket009 [Edge159,Edge155,Edge22,Edge27]
  BaseFeature = -> Pocket009
  ChamferType = 0
  FlipDirection = false
  Placement = pos=(0,0,0) rot=(0.57735,0.57735,0.57735;2.0944rad)
  Size = 2
  Size2 = 1
  SupportTransform = false
FEATURE [Sketcher::SketchObject] Sketch041
  ExternalGeometry = -> [Chamfer]
  FullyConstrained = true
  MapMode = 5
  Placement = pos=(-3.75,5e-15,-2.7e-15) rot=(-0.57735,-0.57735,0.57735;2.0944rad)
  Support = -> [Chamfer]
  sketch-geometry (13):
    g0: ArcOfCircle CenterX=-6.9e-15 CenterY=-3.7e-15 CenterZ=0 NormalX=0 NormalY=0 NormalZ=1 AngleXU=0 Radius=11 StartAngle=5.75419 EndAngle=6.81218
    g1: ArcOfCircle CenterX=-6.9e-15 CenterY=-3.7e-15 CenterZ=0 NormalX=0 NormalY=0 NormalZ=1 AngleXU=0 Radius=12.2 StartAngle=5.94045 EndAngle=6.62592
    g2: ArcOfCircle CenterX=-6.9e-15 CenterY=-3.7e-15 CenterZ=0 NormalX=0 NormalY=0 NormalZ=1 AngleXU=0 Radius=11 StartAngle=2.6126 EndAngle=3.67059
    g3: ArcOfCircle CenterX=-6.9e-15 CenterY=-3.7e-15 CenterZ=0 NormalX=0 NormalY=0 NormalZ=1 AngleXU=0 Radius=12.2 StartAngle=2.79886 EndAngle=3.48433
    g4: Ellipse CenterX=-6.9e-15 CenterY=-3.7e-15 CenterZ=0 NormalX=0 NormalY=0 NormalZ=1 MajorRadius=13.5 MinorRadius=7.81051 AngleXU=-3e-16
    g5: LineSegment StartX=13.5 StartY=-7.4e-15 StartZ=0 EndX=-13.5 EndY=0 EndZ=0
    g6: LineSegment StartX=-4.8e-15 StartY=7.81051 StartZ=0 EndX=-9.1e-15 EndY=-7.81051 EndZ=0
    g7: GeomPoint X=11.0112 Y=-6.8e-15 Z=0
    g8: GeomPoint X=-11.0112 Y=-7e-16 Z=0
    g9: LineSegment StartX=-11.4904 StartY=4.1 StartZ=0 EndX=-9.49645 EndY=5.55135 EndZ=0
    g10: LineSegment StartX=-11.4904 StartY=-4.1 StartZ=0 EndX=-9.49645 EndY=-5.55135 EndZ=0
    g11: LineSegment StartX=9.49645 StartY=-5.55135 StartZ=0 EndX=11.4904 EndY=-4.1 EndZ=0
    g12: LineSegment StartX=11.4904 StartY=4.1 StartZ=0 EndX=9.49645 EndY=5.55135 EndZ=0
  constraints (29):
    c: Coincident(g0,g-4)
    c: PointOnObject(g0,g-4)
    c: Coincident(g1,g0)
    c: PointOnObject(g1,g-3)
    c: Coincident(g2,g0)
    c: PointOnObject(g2,g-4)
    c: Coincident(g3,g0)
    c: PointOnObject(g3,g-3)
    c: InternalAlignment(g5-g8 -> g4) x4
    c: Coincident(g4,g0)
    c: PointOnObject(g3,g4)
    c: PointOnObject(g2,g4)
    c: PointOnObject(g3,g4)
    c: PointOnObject(g2,g4)
    c: PointOnObject(g0,g4)
    c: PointOnObject(g1,g4)
    c: PointOnObject(g1,g4)
    c: PointOnObject(g0,g4)
    c: PointOnObject(g5,g-1)
    c: DistanceX(g5,g5) = 27
    c: DistanceY(g3,g3) = 8.2
    c: Coincident(g9,g3)
    c: Coincident(g9,g2)
    c: Coincident(g10,g3)
    c: Coincident(g10,g2)
    c: Coincident(g11,g0)
    c: Coincident(g11,g1)
    c: Coincident(g12,g1)
    c: Coincident(g12,g0)
FEATURE [PartDesign::Pocket] Pocket010
  BaseFeature = -> Chamfer
  Length = 5
  Length2 = 100
  Placement = pos=(0,0,0) rot=(0.57735,0.57735,0.57735;2.0944rad)
  Profile = -> Sketch041
  Type = 0
FEATURE [PartDesign::Body] Body035  label="Metal case"
  Group = -> [Sketch032,Pad015,Sketch033,Pocket002,Sketch034,Pocket003,Sketch035,Pocket004,Mirrored,Sketch036,Pocket005,Sketch037,Pocket006,Sketch038,Pocket007,Sketch039,Pocket008,Sketch040,Pocket009,Chamfer,Sketch041,Pocket010]
  Origin = -> Origin049
  Tip = -> Pocket010
FEATURE [App::DocumentObjectGroup] Group006  label="Case"
  Group = -> [Body035]
FEATURE [App::Part] Part014  label="KP08-001"
  Group = -> [Group,Body016,Body015,Body020,Body017,Body021,Body019,Body018,Group001,Body023,Body022,Group002,Body028,Body027,Body030,Body026,Body029,Body025,Body024,Group003,Body034,Body033,Group004,Body031,Body032,Group005,Body014,Group006,Body035]
  Origin = -> Origin050
  Placement = pos=(10,246,105) rot=(0,0,1;0rad)
FEATURE [Sketcher::SketchObject] Sketch042
  FullyConstrained = true
  MapMode = 5
  Placement = pos=(0,0,0) rot=(-0.57735,0.57735,0.57735;4.18879rad)
  Support = -> [YZ_Plane058]
  sketch-geometry (1):
    g0: Circle CenterX=0 CenterY=-7.5 CenterZ=0 NormalX=0 NormalY=0 NormalZ=1 AngleXU=0 Radius=0.25
  constraints (3):
    c: PointOnObject(g0,g-2)
    c: DistanceY(g0) = -7.5
    c: Diameter(g0) = 0.5
FEATURE [Sketcher::SketchObject] Sketch043
  FullyConstrained = true
  MapMode = 5
  Support = -> [XY_Plane051]
  sketch-geometry (2):
    g0: LineSegment StartX=0 StartY=5.5 StartZ=0 EndX=6e-16 EndY=9.5 EndZ=0
    g1: ArcOfCircle CenterX=0 CenterY=7.5 CenterZ=0 NormalX=0 NormalY=0 NormalZ=1 AngleXU=0 Radius=2 StartAngle=4.71239 EndAngle=7.85398
  constraints (7):
    c: PointOnObject(g0,g-2)
    c: PointOnObject(g0,g-2)
    c: PointOnObject(g1,g0)
    c: Coincident(g1,g0)
    c: Coincident(g1,g0)
    c: Radius(g1) = 2
    c: DistanceY(g1) = 7.5
FEATURE [PartDesign::Revolution] Revolution011
  Angle = 360
  Axis = (0,1,0)
  Base = (0,0,0)
  Profile = -> Sketch043
  ReferenceAxis = -> Sketch043 [V_Axis]
  Reversed = true
FEATURE [PartDesign::Body] Body037  label="Ball 008"
  Group = -> [Sketch043,Revolution011]
  Origin = -> Origin052
  Tip = -> Revolution011
FEATURE [PartDesign::FeatureBase] Clone014
  BaseFeature = -> Body037
FEATURE [PartDesign::Body] Body038  label="Ball 009"
  BaseFeature = -> Body037
  Group = -> [Clone014]
  Origin = -> Origin053
  Placement = pos=(0,0,0) rot=(-1,0,0;0.897598rad)
  Tip = -> Clone014
FEATURE [PartDesign::FeatureBase] Clone015
  BaseFeature = -> Body037
FEATURE [PartDesign::Body] Body039  label="Ball 010"
  BaseFeature = -> Body037
  Group = -> [Clone015]
  Origin = -> Origin054
  Placement = pos=(0,0,0) rot=(-1,0,0;1.7952rad)
  Tip = -> Clone015
FEATURE [PartDesign::FeatureBase] Clone016
  BaseFeature = -> Body037
FEATURE [PartDesign::Body] Body040  label="Ball 011"
  BaseFeature = -> Body037
  Group = -> [Clone016]
  Origin = -> Origin055
  Placement = pos=(0,0,0) rot=(1,0,0;3.59039rad)
  Tip = -> Clone016
FEATURE [PartDesign::FeatureBase] Clone017
  BaseFeature = -> Body037
FEATURE [PartDesign::Body] Body041  label="Ball 012"
  BaseFeature = -> Body037
  Group = -> [Clone017]
  Origin = -> Origin056
  Placement = pos=(0,0,0) rot=(1,0,0;2.69279rad)
  Tip = -> Clone017
FEATURE [PartDesign::FeatureBase] Clone018
  BaseFeature = -> Body037
FEATURE [PartDesign::Body] Body042  label="Ball 013"
  BaseFeature = -> Body037
  Group = -> [Clone018]
  Origin = -> Origin057
  Placement = pos=(0,0,0) rot=(1,0,0;1.7952rad)
  Tip = -> Clone018
FEATURE [PartDesign::FeatureBase] Clone019
  BaseFeature = -> Body037
FEATURE [PartDesign::Body] Body043  label="Ball 014"
  BaseFeature = -> Body037
  Group = -> [Clone019]
  Origin = -> Origin058
  Placement = pos=(0,0,0) rot=(1,0,0;0.897598rad)
  Tip = -> Clone019
FEATURE [App::DocumentObjectGroup] Group007  label="Balls001"
  Group = -> [Body037,Body038,Body039,Body040,Body041,Body042,Body043]
FEATURE [Sketcher::SketchObject] Sketch044
  FullyConstrained = true
  MapMode = 5
  Support = -> [XY_Plane060]
  sketch-geometry (7):
    g0: LineSegment StartX=-5 StartY=7.5 StartZ=0 EndX=5 EndY=7.5 EndZ=0
    g1: LineSegment StartX=-0.210977 StartY=7.5 StartZ=0 EndX=0.210977 EndY=7.5 EndZ=0
    g2: ArcOfCircle CenterX=0.25 CenterY=7.5 CenterZ=0 NormalX=0 NormalY=0 NormalZ=1 AngleXU=0 Radius=0.460977 StartAngle=2.43297 EndAngle=3.14159
    g3: ArcOfCircle CenterX=-0.25 CenterY=7.5 CenterZ=0 NormalX=0 NormalY=0 NormalZ=1 AngleXU=0 Radius=0.460977 StartAngle=9.792e-13 EndAngle=0.708626
    g4: LineSegment StartX=-0.1 StartY=7.8 StartZ=0 EndX=-0.1 EndY=7.75 EndZ=0
    g5: LineSegment StartX=-0.1 StartY=7.75 StartZ=0 EndX=0.1 EndY=7.75 EndZ=0
    g6: LineSegment StartX=0.1 StartY=7.75 StartZ=0 EndX=0.1 EndY=7.8 EndZ=0
  constraints (22):
    c: DistanceY(g-1,g0) = 7.5
    c: Symmetric(g0,g0,g-2)
    c: DistanceX(g0,g0) = 10
    c: PointOnObject(g1,g0)
    c: PointOnObject(g1,g0)
    c: Coincident(g3,g1)
    c: Coincident(g2,g1)
    c: Coincident(g2,g4)
    c: Coincident(g4,g5)
    c: Horizontal(g5)
    c: Coincident(g5,g6)
    c: Coincident(g6,g3)
    c: Vertical(g6)
    c: Equal(g3,g2)
    c: Vertical(g4)
    c: Symmetric(g2,g3,g-2)
    c: DistanceX(g5,g5) = 0.2
    c: Distance(g5,g1) = 0.25
    c: DistanceX(g3,g-1) = 0.25
    c: PointOnObject(g3,g1)
    c: PointOnObject(g2,g1)
    c: Distance(g3,g1) = 0.3
FEATURE [PartDesign::Revolution] Revolution012
  Angle = 360
  Axis = (10,0,0)
  Base = (-5,7.5,0)
  Profile = -> Sketch044
  ReferenceAxis = -> Sketch044 [Axis]
FEATURE [PartDesign::Body] Body046  label="Rivet 008"
  Group = -> [Sketch044,Revolution012]
  Origin = -> Origin061
  Placement = pos=(0,0,0) rot=(1,0,0;0.448799rad)
  Tip = -> Revolution012
FEATURE [PartDesign::FeatureBase] Clone021
  BaseFeature = -> Body046
  Placement = pos=(0,0,0) rot=(1,0,0;0.448799rad)
FEATURE [PartDesign::Body] Body047  label="Rivet 009"
  BaseFeature = -> Body046
  Group = -> [Clone021]
  Origin = -> Origin062
  Placement = pos=(0,0,0) rot=(1,0,0;0.897598rad)
  Tip = -> Clone021
FEATURE [PartDesign::FeatureBase] Clone022
  BaseFeature = -> Body046
  Placement = pos=(0,0,0) rot=(1,0,0;0.448799rad)
FEATURE [PartDesign::Body] Body048  label="Rivet 010"
  BaseFeature = -> Body046
  Group = -> [Clone022]
  Origin = -> Origin063
  Placement = pos=(0,0,0) rot=(1,0,0;1.7952rad)
  Tip = -> Clone022
FEATURE [PartDesign::FeatureBase] Clone023
  BaseFeature = -> Body046
  Placement = pos=(0,0,0) rot=(1,0,0;0.448799rad)
FEATURE [PartDesign::Body] Body049  label="Rivet 011"
  BaseFeature = -> Body046
  Group = -> [Clone023]
  Origin = -> Origin064
  Placement = pos=(0,0,0) rot=(1,0,0;2.69279rad)
  Tip = -> Clone023
FEATURE [PartDesign::FeatureBase] Clone024
  BaseFeature = -> Body046
  Placement = pos=(0,0,0) rot=(1,0,0;0.448799rad)
FEATURE [PartDesign::Body] Body050  label="Rivet 012"
  BaseFeature = -> Body046
  Group = -> [Clone024]
  Origin = -> Origin065
  Placement = pos=(0,0,0) rot=(1,0,0;3.59039rad)
  Tip = -> Clone024
FEATURE [PartDesign::FeatureBase] Clone025
  BaseFeature = -> Body046
  Placement = pos=(0,0,0) rot=(1,0,0;0.448799rad)
FEATURE [PartDesign::Body] Body051  label="Rivet 013"
  BaseFeature = -> Body046
  Group = -> [Clone025]
  Origin = -> Origin066
  Placement = pos=(0,0,0) rot=(-1,0,0;1.7952rad)
  Tip = -> Clone025
FEATURE [PartDesign::FeatureBase] Clone026
  BaseFeature = -> Body046
  Placement = pos=(0,0,0) rot=(1,0,0;0.448799rad)
FEATURE [PartDesign::Body] Body052  label="Rivet 014"
  BaseFeature = -> Body046
  Group = -> [Clone026]
  Origin = -> Origin067
  Placement = pos=(0,0,0) rot=(-1,0,0;0.897598rad)
  Tip = -> Clone026
FEATURE [App::DocumentObjectGroup] Group009  label="Rivets001"
  Group = -> [Body046,Body047,Body048,Body049,Body050,Body051,Body052]
FEATURE [Sketcher::SketchObject] Sketch045
  FullyConstrained = true
  MapMode = 5
  Placement = pos=(0,0,0) rot=(1,0,0;1.5708rad)
  Support = -> [XZ_Plane058]
  sketch-geometry (4):
    g0: LineSegment StartX=0 StartY=8.5 StartZ=0 EndX=0.1 EndY=8.5 EndZ=0
    g1: LineSegment StartX=0.1 StartY=8.5 StartZ=0 EndX=0.1 EndY=6.5 EndZ=0
    g2: LineSegment StartX=0.1 StartY=6.5 StartZ=0 EndX=0 EndY=6.5 EndZ=0
    g3: LineSegment StartX=0 StartY=6.5 StartZ=0 EndX=0 EndY=8.5 EndZ=0
  constraints (12):
    c: Coincident(g0,g1)
    c: Coincident(g1,g2)
    c: Coincident(g2,g3)
    c: Coincident(g3,g0)
    c: Horizontal(g0)
    c: Horizontal(g2)
    c: Vertical(g1)
    c: Vertical(g3)
    c: PointOnObject(g0,g-2)
    c: DistanceX(g0,g0) = 0.1
    c: DistanceY(g0) = 8.5
    c: DistanceY(g1) = 6.5
FEATURE [PartDesign::Revolution] Revolution013
  Angle = 360
  Axis = (1,0,0)
  Base = (0,0,0)
  Placement = pos=(0,0,0) rot=(1,0,0;1.5708rad)
  Profile = -> Sketch045
  ReferenceAxis = -> Sketch045 [H_Axis]
FEATURE [Sketcher::SketchObject] Sketch046
  FullyConstrained = true
  MapMode = 5
  Placement = pos=(0,0,0) rot=(0.57735,0.57735,0.57735;2.0944rad)
  Support = -> [YZ_Plane058]
  sketch-geometry (5):
    g0: ArcOfCircle CenterX=0 CenterY=7.5 CenterZ=0 NormalX=0 NormalY=0 NormalZ=1 AngleXU=0 Radius=2.11 StartAngle=5.66076 EndAngle=6.65667
    g1: LineSegment StartX=5e-16 StartY=8.5 StartZ=0 EndX=0 EndY=6.26986 EndZ=0
    g2: ArcOfCircle CenterX=0 CenterY=0 CenterZ=0 NormalX=0 NormalY=0 NormalZ=1 AngleXU=0 Radius=6.5 StartAngle=1.3039 EndAngle=1.5708
    g3: LineSegment StartX=1.71431 StartY=6.26986 StartZ=0 EndX=0 EndY=6.26986 EndZ=0
    g4: ArcOfCircle CenterX=0 CenterY=0 CenterZ=0 NormalX=0 NormalY=0 NormalZ=1 AngleXU=0 Radius=8.5 StartAngle=1.33757 EndAngle=1.5708
  constraints (16):
    c: PointOnObject(g0,g-2)
    c: DistanceY(g0) = 7.5
    c: Radius(g0) = 2.11
    c: PointOnObject(g2,g1)
    c: DistanceY(g2) = 6.5
    c: Coincident(g2,g-1)
    c: Coincident(g3,g2)
    c: Horizontal(g3)
    c: Coincident(g0,g2)
    c: Coincident(g1,g3)
    c: PointOnObject(g1,g-2)
    c: PointOnObject(g1,g-2)
    c: Coincident(g4,g-1)
    c: Coincident(g4,g1)
    c: DistanceY(g1) = 8.5
    c: Coincident(g0,g4)
FEATURE [PartDesign::Revolution] Revolution014
  Angle = 180
  Axis = (-2e-16,3e-16,1)
  Base = (0,0,0)
  BaseFeature = -> Revolution013
  Placement = pos=(0,0,0) rot=(1,0,0;1.5708rad)
  Profile = -> Sketch046
  ReferenceAxis = -> Sketch046 [V_Axis]
  Reversed = true
FEATURE [PartDesign::PolarPattern] PolarPattern004
  Angle = 360
  Axis = -> Sketch046 [N_Axis]
  BaseFeature = -> Revolution014
  Occurrences = 3
  Originals = -> [Revolution014]
  Placement = pos=(0,0,0) rot=(1,0,0;1.5708rad)
  Refine = true
FEATURE [Sketcher::SketchObject] Sketch047
  FullyConstrained = true
  MapMode = 5
  Placement = pos=(0,0,0) rot=(0.57735,0.57735,0.57735;2.0944rad)
  Support = -> [YZ_Plane058]
  sketch-geometry (4):
    g0: ArcOfCircle CenterX=0 CenterY=7.5 CenterZ=0 NormalX=0 NormalY=0 NormalZ=1 AngleXU=0 Radius=2.01 StartAngle=5.57985 EndAngle=6.86228
    g1: LineSegment StartX=0 StartY=6.2 StartZ=0 EndX=1.533 EndY=6.2 EndZ=0
    g2: LineSegment StartX=0 StartY=8.6 StartZ=0 EndX=0 EndY=6.2 EndZ=0
    g3: LineSegment StartX=0 StartY=8.6 StartZ=0 EndX=1.68229 EndY=8.6 EndZ=0
  constraints (13):
    c: PointOnObject(g0,g-2)
    c: DistanceY(g0) = 7.5
    c: Radius(g0) = 2.01
    c: PointOnObject(g1,g-2)
    c: Horizontal(g1)
    c: Coincident(g0,g1)
    c: DistanceY(g1) = 6.2
    c: DistanceY(g2) = 8.6
    c: Coincident(g2,g1)
    c: PointOnObject(g2,g-2)
    c: Coincident(g3,g2)
    c: Horizontal(g3)
    c: Coincident(g0,g3)
FEATURE [PartDesign::Groove] Groove001
  Angle = 360
  Axis = (-2e-16,3e-16,1)
  Base = (0,0,0)
  BaseFeature = -> PolarPattern004
  Placement = pos=(0,0,0) rot=(1,0,0;1.5708rad)
  Profile = -> Sketch047
  ReferenceAxis = -> Sketch047 [V_Axis]
FEATURE [PartDesign::PolarPattern] PolarPattern005
  Angle = 360
  Axis = -> Sketch047 [N_Axis]
  BaseFeature = -> Groove001
  Occurrences = 3
  Originals = -> [Groove001]
  Placement = pos=(0,0,0) rot=(1,0,0;1.5708rad)
FEATURE [PartDesign::Pocket] Pocket011
  BaseFeature = -> PolarPattern005
  Length = 5
  Length2 = 100
  Placement = pos=(0,0,0) rot=(1,0,0;1.5708rad)
  Profile = -> Sketch042
  Type = 1
FEATURE [PartDesign::PolarPattern] PolarPattern006
  Angle = 360
  Axis = -> Sketch042 [N_Axis]
  BaseFeature = -> Pocket011
  Occurrences = 3
  Originals = -> [Pocket011]
  Placement = pos=(0,0,0) rot=(1,0,0;1.5708rad)
FEATURE [PartDesign::Body] Body044  label="Cage 003"
  Group = -> [Sketch045,Revolution013,Sketch046,Revolution014,PolarPattern004,Sketch047,Groove001,PolarPattern005,Sketch042,Pocket011,PolarPattern006]
  Origin = -> Origin059
  Placement = pos=(0,0,0) rot=(-1,0,0;1.5708rad)
  Tip = -> PolarPattern006
FEATURE [PartDesign::FeatureBase] Clone020
  BaseFeature = -> Body044
  Placement = pos=(0,0,0) rot=(-1,0,0;1.5708rad)
FEATURE [PartDesign::Body] Body045  label="Cage 004"
  BaseFeature = -> Body044
  Group = -> [Clone020]
  Origin = -> Origin060
  Placement = pos=(0,0,0) rot=(0,1,0;3.14159rad)
  Tip = -> Clone020
FEATURE [App::DocumentObjectGroup] Group008  label="Cages001"
  Group = -> [Body044,Body045]
FEATURE [Sketcher::SketchObject] Sketch048
  FullyConstrained = true
  MapMode = 5
  Support = -> [XY_Plane067]
  sketch-geometry (14):
    g0: ArcOfCircle CenterX=-1e-16 CenterY=7.5 CenterZ=0 NormalX=0 NormalY=0 NormalZ=1 AngleXU=0 Radius=2 StartAngle=0.848062 EndAngle=2.29353
    g1: LineSegment StartX=-3.5 StartY=11 StartZ=0 EndX=3.5 EndY=11 EndZ=0
    g2: LineSegment StartX=3.5 StartY=11 StartZ=0 EndX=3.5 EndY=9.2 EndZ=0
    g3: LineSegment StartX=2.9 StartY=9 StartZ=0 EndX=1.32288 EndY=9 EndZ=0
    g4: LineSegment StartX=-3.5 StartY=9.2 StartZ=0 EndX=-3.5 EndY=11 EndZ=0
    g5: LineSegment StartX=-1.32288 StartY=9 StartZ=0 EndX=-2.9 EndY=9 EndZ=0
    g6: LineSegment StartX=2.9 StartY=9 StartZ=0 EndX=2.9 EndY=9.5 EndZ=0
    g7: LineSegment StartX=2.9 StartY=9.5 StartZ=0 EndX=3.2 EndY=9.5 EndZ=0
    g8: LineSegment StartX=3.2 StartY=9.5 StartZ=0 EndX=3.2 EndY=9.2 EndZ=0
    g9: LineSegment StartX=3.2 StartY=9.2 StartZ=0 EndX=3.5 EndY=9.2 EndZ=0
    g10: LineSegment StartX=-3.5 StartY=9.2 StartZ=0 EndX=-3.2 EndY=9.2 EndZ=0
    g11: LineSegment StartX=-3.2 StartY=9.2 StartZ=0 EndX=-3.2 EndY=9.5 EndZ=0
    g12: LineSegment StartX=-3.2 StartY=9.5 StartZ=0 EndX=-2.9 EndY=9.5 EndZ=0
    g13: LineSegment StartX=-2.9 StartY=9.5 StartZ=0 EndX=-2.9 EndY=9 EndZ=0
  constraints (41):
    c: Coincident(g1,g2)
    c: Coincident(g4,g1)
    c: Horizontal(g3)
    c: Vertical(g2)
    c: Vertical(g4)
    c: Coincident(g0,g5)
    c: Coincident(g0,g3)
    c: DistanceY(g-1,g0) = 7.5
    c: Radius(g0) = 2
    c: Symmetric(g1,g1,g-2)
    c: Symmetric(g0,g0,g-2)
    c: DistanceY(g1) = 11
    c: DistanceX(g1,g1) = 7
    c: Vertical(g6)
    c: Coincident(g6,g7)
    c: Horizontal(g7)
    c: Coincident(g7,g8)
    c: Vertical(g8)
    c: Coincident(g8,g9)
    c: Coincident(g3,g6)
    c: Coincident(g2,g9)
    c: Horizontal(g10)
    c: Coincident(g10,g11)
    c: Coincident(g11,g12)
    c: Horizontal(g12)
    c: Coincident(g12,g13)
    c: Vertical(g13)
    c: Vertical(g11)
    c: Coincident(g4,g10)
    c: Coincident(g5,g13)
    c: DistanceY(g13,g13) = 0.5
    c: DistanceX(g12,g12) = 0.3
    c: DistanceY(g5,g10) = 0.2
    c: Symmetric(g5,g3,g-2)
    c: DistanceY(g3) = 9
    c: DistanceY(g6) = 9.5
    c: Equal(g7,g12)
    c: Equal(g13,g6)
    c: Horizontal(g9)
    c: Horizontal(g8,g10)
    c: Equal(g12,g10)
FEATURE [PartDesign::Revolution] Revolution015
  Angle = 360
  Axis = (1,0,0)
  Base = (0,0,0)
  Profile = -> Sketch048
  ReferenceAxis = -> X_Axis067
FEATURE [PartDesign::Fillet] Fillet157
  Base = -> Revolution015 [Edge14,Edge15]
  BaseFeature = -> Revolution015
  Radius = 0.3
  SupportTransform = false
FEATURE [PartDesign::Body] Body053  label="Outer Ring002"
  Group = -> [Sketch048,Revolution015,Fillet157]
  Origin = -> Origin068
  Tip = -> Fillet157
FEATURE [Sketcher::SketchObject] Sketch049
  FullyConstrained = true
  MapMode = 5
  Support = -> [XY_Plane068]
  sketch-geometry (14):
    g0: LineSegment StartX=-2.9 StartY=6 StartZ=0 EndX=-1.32288 EndY=6 EndZ=0
    g1: LineSegment StartX=-3.5 StartY=4 StartZ=0 EndX=-3.5 EndY=5.7 EndZ=0
    g2: ArcOfCircle CenterX=-1e-16 CenterY=7.5 CenterZ=0 NormalX=0 NormalY=0 NormalZ=1 AngleXU=0 Radius=2 StartAngle=3.98965 EndAngle=5.43512
    g3: LineSegment StartX=1.32288 StartY=6 StartZ=0 EndX=2.9 EndY=6 EndZ=0
    g4: LineSegment StartX=-3.5 StartY=5.7 StartZ=0 EndX=-3.2 EndY=5.7 EndZ=0
    g5: LineSegment StartX=-3.2 StartY=5.7 StartZ=0 EndX=-3.2 EndY=5.5 EndZ=0
    g6: LineSegment StartX=-3.2 StartY=5.5 StartZ=0 EndX=-2.9 EndY=5.5 EndZ=0
    g7: LineSegment StartX=-2.9 StartY=5.5 StartZ=0 EndX=-2.9 EndY=6 EndZ=0
    g8: LineSegment StartX=8.5 StartY=6 StartZ=0 EndX=3.2 EndY=6 EndZ=0
    g9: LineSegment StartX=3.2 StartY=6 StartZ=0 EndX=3.2 EndY=5.5 EndZ=0
    g10: LineSegment StartX=3.2 StartY=5.5 StartZ=0 EndX=2.9 EndY=5.5 EndZ=0
    g11: LineSegment StartX=2.9 StartY=5.5 StartZ=0 EndX=2.9 EndY=6 EndZ=0
    g12: LineSegment StartX=8.5 StartY=4 StartZ=0 EndX=8.5 EndY=6 EndZ=0
    g13: LineSegment StartX=-3.5 StartY=4 StartZ=0 EndX=8.5 EndY=4 EndZ=0
  constraints (43):
    c: Horizontal(g0)
    c: Vertical(g1)
    c: DistanceY(g1) = 4
    c: Coincident(g2,g0)
    c: Coincident(g2,g3)
    c: Horizontal(g3)
    c: Radius(g2) = 2
    c: DistanceY(g2) = 7.5
    c: Symmetric(g0,g2,g-2)
    c: Horizontal(g4)
    c: Coincident(g4,g5)
    c: Vertical(g5)
    c: Coincident(g5,g6)
    c: Horizontal(g6)
    c: Coincident(g6,g7)
    c: Vertical(g7)
    c: Horizontal(g8)
    c: Coincident(g8,g9)
    c: Vertical(g9)
    c: Coincident(g9,g10)
    c: Horizontal(g10)
    c: Coincident(g10,g11)
    c: Vertical(g11)
    c: Coincident(g3,g11)
    c: Coincident(g0,g7)
    c: Coincident(g1,g4)
    c: DistanceY(g3) = 6
    c: DistanceY(g6,g0) = 0.5
    c: DistanceX(g4,g4) = 0.3
    c: DistanceX(g6,g6) = 0.3
    c: DistanceY(g5,g4) = 0.2
    c: Vertical(g12)
    c: Equal(g11,g7)
    c: DistanceY(g1,g0) = 2
    c: DistanceX(g8,g8) = 5.3
    c: Coincident(g13,g1)
    c: Coincident(g13,g12)
    c: Horizontal(g13)
    c: DistanceX(g13,g13) = 12
    c: DistanceX(g1,g2) = 3.5
    c: Coincident(g8,g12)
    c: Equal(g7,g9)
    c: Equal(g6,g10)
FEATURE [PartDesign::Revolution] Revolution016
  Angle = 360
  Axis = (1,0,0)
  Base = (0,0,0)
  Profile = -> Sketch049
  ReferenceAxis = -> X_Axis068
FEATURE [PartDesign::Fillet] Fillet158
  Base = -> Revolution016 [Edge13,Edge11]
  BaseFeature = -> Revolution016
  Radius = 0.2
  SupportTransform = false
FEATURE [PartDesign::Body] Body054  label="Inner Ring002"
  Group = -> [Sketch049,Revolution016,Fillet158]
  Origin = -> Origin069
  Tip = -> Fillet158
FEATURE [App::DocumentObjectGroup] Group011  label="Rings001"
  Group = -> [Body053,Body054]
FEATURE [Sketcher::SketchObject] Sketch050
  FullyConstrained = true
  MapMode = 5
  Placement = pos=(0,0,0) rot=(1,0,0;1.5708rad)
  Support = -> [XZ_Plane069]
  sketch-geometry (12):
    g0: LineSegment StartX=2.9 StartY=9.5 StartZ=0 EndX=2.9 EndY=8.5 EndZ=0
    g1: LineSegment StartX=2.9 StartY=8.5 StartZ=0 EndX=3.2 EndY=8.5 EndZ=0
    g2: LineSegment StartX=3.2 StartY=8.5 StartZ=0 EndX=3.2 EndY=6.5 EndZ=0
    g3: LineSegment StartX=3.2 StartY=6.5 StartZ=0 EndX=2.9 EndY=6.5 EndZ=0
    g4: LineSegment StartX=2.9 StartY=6.5 StartZ=0 EndX=2.9 EndY=5.5 EndZ=0
    g5: LineSegment StartX=2.9 StartY=5.5 StartZ=0 EndX=3.2 EndY=5.5 EndZ=0
    g6: LineSegment StartX=3.2 StartY=5.5 StartZ=0 EndX=3.2 EndY=6 EndZ=0
    g7: LineSegment StartX=3.2 StartY=6 StartZ=0 EndX=3.5 EndY=6 EndZ=0
    g8: LineSegment StartX=3.5 StartY=6 StartZ=0 EndX=3.5 EndY=9 EndZ=0
    g9: LineSegment StartX=3.5 StartY=9 StartZ=0 EndX=3.2 EndY=9 EndZ=0
    g10: LineSegment StartX=3.2 StartY=9 StartZ=0 EndX=3.2 EndY=9.5 EndZ=0
    g11: LineSegment StartX=3.2 StartY=9.5 StartZ=0 EndX=2.9 EndY=9.5 EndZ=0
  constraints (36):
    c: Vertical(g0)
    c: Coincident(g0,g1)
    c: Horizontal(g1)
    c: Coincident(g1,g2)
    c: Vertical(g2)
    c: Coincident(g2,g3)
    c: Horizontal(g3)
    c: Coincident(g3,g4)
    c: Vertical(g4)
    c: Coincident(g4,g5)
    c: Horizontal(g5)
    c: Coincident(g5,g6)
    c: Vertical(g6)
    c: Coincident(g6,g7)
    c: Horizontal(g7)
    c: Coincident(g7,g8)
    c: Vertical(g8)
    c: Coincident(g8,g9)
    c: Horizontal(g9)
    c: Coincident(g9,g10)
    c: Vertical(g10)
    c: Coincident(g10,g11)
    c: Coincident(g11,g0)
    c: Horizontal(g11)
    c: DistanceY(g4) = 5.5
    c: DistanceX(g4) = 2.9
    c: DistanceY(g5,g6) = 0.5
    c: DistanceY(g6,g2) = 0.5
    c: DistanceX(g5,g5) = 0.3
    c: Equal(g5,g7)
    c: Equal(g7,g3)
    c: Equal(g3,g1)
    c: Equal(g1,g9)
    c: Equal(g4,g0)
    c: Equal(g6,g10)
    c: DistanceY(g4,g0) = 4
FEATURE [PartDesign::Revolution] Revolution017
  Angle = 360
  Axis = (1,0,0)
  Base = (0,0,0)
  Placement = pos=(0,0,0) rot=(1,0,0;1.5708rad)
  Profile = -> Sketch050
  ReferenceAxis = -> Sketch050 [H_Axis]
FEATURE [PartDesign::Fillet] Fillet159
  Base = -> Revolution017 [Edge14,Edge12]
  BaseFeature = -> Revolution017
  Placement = pos=(0,0,0) rot=(1,0,0;1.5708rad)
  Radius = 0.2
  SupportTransform = false
FEATURE [PartDesign::Body] Body055  label="Seal 003"
  Group = -> [Sketch050,Revolution017,Fillet159]
  Origin = -> Origin070
  Tip = -> Fillet159
FEATURE [PartDesign::FeatureBase] Clone027
  BaseFeature = -> Body055
FEATURE [PartDesign::Body] Body056  label="Seal 004"
  BaseFeature = -> Body055
  Group = -> [Clone027]
  Origin = -> Origin071
  Placement = pos=(0,0,0) rot=(0,1,0;3.14159rad)
  Tip = -> Clone027
FEATURE [App::DocumentObjectGroup] Group010  label="Seals001"
  Group = -> [Body055,Body056]
FEATURE [Sketcher::SketchObject] Sketch051
  AttachmentOffset = pos=(0,0,4) rot=(0,0,1;0rad)
  FullyConstrained = true
  MapMode = 5
  Placement = pos=(0,0,4) rot=(0,0,1;0rad)
  Support = -> [XY_Plane050]
  sketch-geometry (1):
    g0: Circle CenterX=6 CenterY=0 CenterZ=0 NormalX=0 NormalY=0 NormalZ=1 AngleXU=0 Radius=1.5
  constraints (3):
    c: PointOnObject(g0,g-1)
    c: Diameter(g0) = 3
    c: DistanceX(g-1,g0) = 6
FEATURE [PartDesign::Pad] Pad016
  Direction = (0,0,1)
  Length = 3
  Length2 = 100
  Profile = -> Sketch051
  Type = 0
FEATURE [Sketcher::SketchObject] Sketch052
  ExternalGeometry = -> [Pad016]
  FullyConstrained = true
  MapMode = 5
  Placement = pos=(0,0,7) rot=(0,0,1;0rad)
  Support = -> [Pad016]
  sketch-geometry (7):
    g0: LineSegment StartX=6.43301 StartY=-0.75 StartZ=0 EndX=6.86603 EndY=0 EndZ=0
    g1: LineSegment StartX=6.86603 StartY=0 StartZ=0 EndX=6.43301 EndY=0.75 EndZ=0
    g2: LineSegment StartX=6.43301 StartY=0.75 StartZ=0 EndX=5.56699 EndY=0.75 EndZ=0
    g3: LineSegment StartX=5.56699 StartY=0.75 StartZ=0 EndX=5.13397 EndY=-1e-16 EndZ=0
    g4: LineSegment StartX=5.13397 StartY=-1e-16 StartZ=0 EndX=5.56699 EndY=-0.75 EndZ=0
    g5: LineSegment StartX=5.56699 StartY=-0.75 StartZ=0 EndX=6.43301 EndY=-0.75 EndZ=0
    g6: Circle CenterX=6 CenterY=0 CenterZ=0 NormalX=0 NormalY=0 NormalZ=1 AngleXU=0 Radius=0.866025
  constraints (16):
    c: Coincident(g0,g1)
    c: Coincident(g1,g2)
    c: Coincident(g2,g3)
    c: Coincident(g3,g4)
    c: Coincident(g4,g5)
    c: Coincident(g5,g0)
    c: Equal(g0, g1-g5) x5
    c: PointOnObject(g0,g6)
    c: PointOnObject(g1,g6)
    c: PointOnObject(g2,g6)
    c: PointOnObject(g3,g6)
    c: PointOnObject(g4,g6)
    c: PointOnObject(g5,g6)
    c: Coincident(g6,g-3)
    c: Horizontal(g5)
    c: DistanceY(g4,g2) = 1.5
FEATURE [PartDesign::Pocket] Pocket012
  BaseFeature = -> Pad016
  Length = 0.9
  Length2 = 100
  Profile = -> Sketch052
  Type = 0
FEATURE [PartDesign::PolarPattern] PolarPattern007
  Angle = 120
  Axis = -> X_Axis050
  BaseFeature = -> Pocket012
  Occurrences = 3
  Originals = -> [Pad016,Pocket012]
FEATURE [PartDesign::Body] Body036
  Group = -> [Sketch051,Pad016,Sketch052,Pocket012,PolarPattern007]
  Origin = -> Origin051
  Tip = -> PolarPattern007
FEATURE [App::DocumentObjectGroup] Group012  label="Set screws001"
  Group = -> [Body036]
FEATURE [Sketcher::SketchObject] Sketch053
  AttachmentOffset = pos=(0,0,-6.5) rot=(0,0,1;0rad)
  FullyConstrained = true
  MapMode = 5
  Placement = pos=(-6.5,1.4e-15,-1.4e-15) rot=(0.57735,0.57735,0.57735;2.0944rad)
  Support = -> [YZ_Plane071]
  sketch-geometry (14):
    g0: Circle CenterX=0 CenterY=0 CenterZ=0 NormalX=0 NormalY=0 NormalZ=1 AngleXU=0 Radius=11
    g1: ArcOfCircle CenterX=0 CenterY=0 CenterZ=0 NormalX=0 NormalY=0 NormalZ=1 AngleXU=0 Radius=13.5 StartAngle=0.0668757 EndAngle=3.07472
    g2: LineSegment StartX=-13.4698 StartY=0.902148 StartZ=0 EndX=-14.2 EndY=-10 EndZ=0
    g3: LineSegment StartX=-14.2 StartY=-10 StartZ=0 EndX=-27.5 EndY=-10 EndZ=0
    g4: LineSegment StartX=-27.5 StartY=-10 StartZ=0 EndX=-27.5 EndY=-15 EndZ=0
    g5: LineSegment StartX=-27.5 StartY=-15 StartZ=0 EndX=-12.3 EndY=-15 EndZ=0
    g6: LineSegment StartX=27.5 StartY=-15 StartZ=0 EndX=27.5 EndY=-10 EndZ=0
    g7: LineSegment StartX=27.5 StartY=-10 StartZ=0 EndX=14.2 EndY=-10 EndZ=0
    g8: LineSegment StartX=14.2 StartY=-10 StartZ=0 EndX=13.4698 EndY=0.902148 EndZ=0
    g9: LineSegment StartX=12.3 StartY=-15 StartZ=0 EndX=12.1995 EndY=-13.5 EndZ=0
    g10: LineSegment StartX=12.1995 StartY=-13.5 StartZ=0 EndX=-12.1995 EndY=-13.5 EndZ=0
    g11: LineSegment StartX=-12.1995 StartY=-13.5 StartZ=0 EndX=-12.3 EndY=-15 EndZ=0
    g12: LineSegment StartX=12.3 StartY=-15 StartZ=0 EndX=27.5 EndY=-15 EndZ=0
    g13: GeomPoint X=0 Y=13.5 Z=0
  constraints (39):
    c: Coincident(g0,g-1)
    c: Radius(g0) = 11
    c: Coincident(g1,g0)
    c: Coincident(g2,g3)
    c: Coincident(g3,g4)
    c: Coincident(g4,g5)
    c: Horizontal(g5)
    c: Coincident(g12,g6)
    c: Coincident(g6,g7)
    c: Horizontal(g7)
    c: Coincident(g7,g8)
    c: Coincident(g9,g10)
    c: Horizontal(g10)
    c: Coincident(g10,g11)
    c: Coincident(g5,g11)
    c: Coincident(g12,g9)
    c: Horizontal(g3)
    c: Vertical(g6)
    c: Vertical(g4)
    c: Equal(g9,g11)
    c: Horizontal(g12)
    c: Horizontal(g5,g9)
    c: Equal(g6,g4)
    c: Equal(g12,g5)
    c: Equal(g7,g3)
    c: DistanceX(g4,g6) = 55
    c: DistanceY(g6,g0) = 15
    c: Equal(g8,g2)
    c: DistanceY(g6,g6) = 5
    c: Parallel(g9,g8)
    c: DistanceY(g9,g9) = 1.5
    c: DistanceX(g5,g5) = 15.2
    c: Diameter(g1) = 27
    c: PointOnObject(g13,g1)
    c: PointOnObject(g13,g-2)
    c: DistanceY(g6,g13) = 28.5
    c: Tangent(g1,g2) = -1.5708
    c: Tangent(g1,g8) = -1.5708
    c: DistanceX(g3,g3) = 13.3
FEATURE [PartDesign::Pad] Pad017
  Direction = (1,-2e-16,3e-16)
  Length = 13
  Length2 = 100
  Placement = pos=(0,0,0) rot=(0.57735,0.57735,0.57735;2.0944rad)
  Profile = -> Sketch053
  Type = 0
FEATURE [Sketcher::SketchObject] Sketch054
  ExternalGeometry = -> [Pad017]
  FullyConstrained = true
  MapMode = 5
  Placement = pos=(4.2e-15,-6.6e-15,-15) rot=(0.707107,0.707107,0;3.14159rad)
  Support = -> [Pad017]
  sketch-geometry (7):
    g0: LineSegment StartX=-24.9 StartY=4.15 StartZ=0 EndX=-14.9 EndY=4.15 EndZ=0
    g1: LineSegment StartX=-14.9 StartY=4.15 StartZ=0 EndX=-14.9 EndY=-4.15 EndZ=0
    g2: LineSegment StartX=-14.9 StartY=-4.15 StartZ=0 EndX=-24.9 EndY=-4.15 EndZ=0
    g3: LineSegment StartX=-24.9 StartY=-4.15 StartZ=0 EndX=-24.9 EndY=4.15 EndZ=0
    g4: LineSegment StartX=-27.5 StartY=6.5 StartZ=0 EndX=-12.3 EndY=-6.5 EndZ=0
    g5: LineSegment StartX=-27.5 StartY=-6.5 StartZ=0 EndX=-12.3 EndY=6.5 EndZ=0
    g6: GeomPoint X=-19.9 Y=2.6e-15 Z=0
  constraints (17):
    c: Coincident(g0,g1)
    c: Coincident(g1,g2)
    c: Coincident(g2,g3)
    c: Coincident(g3,g0)
    c: Horizontal(g0)
    c: Horizontal(g2)
    c: Vertical(g1)
    c: Vertical(g3)
    c: DistanceX(g0,g0) = 10
    c: DistanceY(g1,g1) = 8.3
    c: Coincident(g4,g-3)
    c: Coincident(g4,g-4)
    c: Coincident(g5,g-4)
    c: Coincident(g5,g-3)
    c: PointOnObject(g6,g4)
    c: PointOnObject(g6,g5)
    c: Symmetric(g0,g1,g6)
FEATURE [PartDesign::Pocket] Pocket013
  BaseFeature = -> Pad017
  Length = 2.3
  Length2 = 100
  Placement = pos=(0,0,0) rot=(0.57735,0.57735,0.57735;2.0944rad)
  Profile = -> Sketch054
  Type = 0
FEATURE [Sketcher::SketchObject] Sketch055
  ExternalGeometry = -> [Pocket013]
  FullyConstrained = true
  MapMode = 5
  Placement = pos=(2.8e-15,-4.4e-15,-10) rot=(0,0,-1;1.5708rad)
  Support = -> [Pocket013]
  sketch-geometry (2):
    g0: Circle CenterX=21.2 CenterY=2.1e-15 CenterZ=0 NormalX=0 NormalY=0 NormalZ=1 AngleXU=0 Radius=2.5
    g1: LineSegment StartX=21.2 StartY=2.1e-15 StartZ=0 EndX=27.5 EndY=2.1e-15 EndZ=0
  constraints (5):
    c: Diameter(g0) = 5
    c: DistanceX(g0,g-3) = 6.3
    c: Coincident(g1,g0)
    c: Horizontal(g1)
    c: Symmetric(g-5,g-5,g1)
FEATURE [PartDesign::Pocket] Pocket014
  BaseFeature = -> Pocket013
  Length = 5
  Length2 = 100
  Placement = pos=(0,0,0) rot=(0.57735,0.57735,0.57735;2.0944rad)
  Profile = -> Sketch055
  Type = 2
FEATURE [Sketcher::SketchObject] Sketch056
  ExternalGeometry = -> [Pocket014]
  FullyConstrained = true
  MapMode = 5
  Placement = pos=(6.5,-1.4e-15,1.5e-15) rot=(0.57735,0.57735,0.57735;2.0944rad)
  Support = -> [Pocket014]
  sketch-geometry (6):
    g0: LineSegment StartX=-24.6 StartY=-13.7 StartZ=0 EndX=-24.6 EndY=-11.3 EndZ=0
    g1: LineSegment StartX=-24.6 StartY=-11.3 StartZ=0 EndX=-14.2 EndY=-11.3 EndZ=0
    g2: LineSegment StartX=-14.2 StartY=-11.3 StartZ=0 EndX=-14.2 EndY=-13.7 EndZ=0
    g3: LineSegment StartX=-14.2 StartY=-13.7 StartZ=0 EndX=-24.6 EndY=-13.7 EndZ=0
    g4: GeomPoint X=-19.4 Y=-12.5 Z=0
    g5: LineSegment StartX=-19.4 StartY=-12.5 StartZ=0 EndX=-27.5 EndY=-12.5 EndZ=0
  constraints (15):
    c: Coincident(g0,g1)
    c: Coincident(g1,g2)
    c: Coincident(g2,g3)
    c: Coincident(g3,g0)
    c: Horizontal(g1)
    c: Horizontal(g3)
    c: Vertical(g0)
    c: Vertical(g2)
    c: Symmetric(g1,g0,g4)
    c: DistanceX(g1,g1) = 10.4
    c: DistanceY(g2,g2) = 2.4
    c: DistanceX(g2,g-4) = 1.9
    c: Coincident(g5,g4)
    c: Horizontal(g5)
    c: Symmetric(g-5,g-5,g5)
FEATURE [PartDesign::Pocket] Pocket015
  BaseFeature = -> Pocket014
  Length = 0.4
  Length2 = 100
  Placement = pos=(0,0,0) rot=(0.57735,0.57735,0.57735;2.0944rad)
  Profile = -> Sketch056
  Type = 0
FEATURE [PartDesign::Mirrored] Mirrored001
  BaseFeature = -> Pocket015
  MirrorPlane = -> Sketch054 [V_Axis]
  Originals = -> [Pocket013,Pocket014,Pocket015]
  Placement = pos=(0,0,0) rot=(0.57735,0.57735,0.57735;2.0944rad)
FEATURE [Sketcher::SketchObject] Sketch057
  ExternalGeometry = -> [Mirrored001]
  FullyConstrained = true
  MapMode = 5
  Placement = pos=(0,0,0) rot=(1,0,0;1.5708rad)
  Support = -> [XZ_Plane071]
  sketch-geometry (9):
    g0: GeomPoint X=-6.5 Y=13.5 Z=0
    g1: LineSegment StartX=6.5 StartY=-10 StartZ=0 EndX=6.5 EndY=13.5 EndZ=0
    g2: LineSegment StartX=6.5 StartY=13.5 StartZ=0 EndX=4.75 EndY=13.5 EndZ=0
    g3: LineSegment StartX=-6.5 StartY=13.5 StartZ=0 EndX=-4.75 EndY=13.5 EndZ=0
    g4: LineSegment StartX=-6.5 StartY=-10 StartZ=0 EndX=-6.5 EndY=13.5 EndZ=0
    g5: LineSegment StartX=6.5 StartY=-10 StartZ=0 EndX=4.75 EndY=-1 EndZ=0
    g6: LineSegment StartX=4.75 StartY=-1 StartZ=0 EndX=4.75 EndY=13.5 EndZ=0
    g7: LineSegment StartX=-4.75 StartY=13.5 StartZ=0 EndX=-4.75 EndY=-1 EndZ=0
    g8: LineSegment StartX=-4.75 StartY=-1 StartZ=0 EndX=-6.5 EndY=-10 EndZ=0
  constraints (24):
    c: Vertical(g0,g-4)
    c: Horizontal(g-3,g0)
    c: Coincident(g1,g-3)
    c: Coincident(g1,g2)
    c: Horizontal(g2)
    c: Coincident(g3,g0)
    c: Horizontal(g3)
    c: Coincident(g4,g3)
    c: Vertical(g4,g-4)
    c: DistanceX(g3,g2) = 9.5
    c: Equal(g2,g3)
    c: Horizontal(g1,g4)
    c: Coincident(g1,g-5)
    c: Coincident(g1,g5)
    c: Coincident(g5,g6)
    c: Coincident(g6,g2)
    c: Vertical(g6)
    c: DistanceY(g1,g5) = 9
    c: Coincident(g3,g7)
    c: Vertical(g7)
    c: Coincident(g7,g8)
    c: Coincident(g8,g4)
    c: Horizontal(g7,g5)
    c: DistanceX(g2,g2) = 1.75
FEATURE [PartDesign::Pocket] Pocket016
  BaseFeature = -> Mirrored001
  Length = 15
  Length2 = 15
  Placement = pos=(0,0,0) rot=(0.57735,0.57735,0.57735;2.0944rad)
  Profile = -> Sketch057
  Type = 4
FEATURE [Sketcher::SketchObject] Sketch058
  FullyConstrained = true
  MapMode = 5
  Placement = pos=(-6.5,1.4e-15,-1.5e-15) rot=(0.57735,0.57735,-0.57735;4.18879rad)
  Support = -> [Pocket016]
  sketch-geometry (1):
    g0: Circle CenterX=0 CenterY=0 CenterZ=0 NormalX=0 NormalY=0 NormalZ=1 AngleXU=0 Radius=12.2
  constraints (2):
    c: Coincident(g0,g-1)
    c: Diameter(g0) = 24.4
FEATURE [PartDesign::Pocket] Pocket017
  BaseFeature = -> Pocket016
  Length = 2.75
  Length2 = 100
  Placement = pos=(0,0,0) rot=(0.57735,0.57735,0.57735;2.0944rad)
  Profile = -> Sketch058
  Type = 0
FEATURE [Sketcher::SketchObject] Sketch059
  FullyConstrained = true
  MapMode = 5
  Placement = pos=(6.5,-1.4e-15,1.5e-15) rot=(0.57735,0.57735,0.57735;2.0944rad)
  Support = -> [Pocket017]
  sketch-geometry (1):
    g0: Circle CenterX=0 CenterY=0 CenterZ=0 NormalX=0 NormalY=0 NormalZ=1 AngleXU=0 Radius=12.1
  constraints (2):
    c: Coincident(g0,g-1)
    c: Diameter(g0) = 24.2
FEATURE [PartDesign::Pocket] Pocket018
  BaseFeature = -> Pocket017
  Length = 2.75
  Length2 = 100
  Placement = pos=(0,0,0) rot=(0.57735,0.57735,0.57735;2.0944rad)
  Profile = -> Sketch059
  Type = 0
FEATURE [Sketcher::SketchObject] Sketch060
  ExternalGeometry = -> [Pocket018]
  FullyConstrained = true
  MapMode = 5
  Placement = pos=(6.5,-1.4e-15,1.5e-15) rot=(0.57735,0.57735,0.57735;2.0944rad)
  Support = -> [Pocket018]
  sketch-geometry (6):
    g0: ArcOfCircle CenterX=0 CenterY=0 CenterZ=0 NormalX=0 NormalY=0 NormalZ=1 AngleXU=0 Radius=13.5 StartAngle=3.79664 EndAngle=5.62814
    g1: LineSegment StartX=-11.8698 StartY=-8.57666 StartZ=0 EndX=-12.3 EndY=-15 EndZ=0
    g2: LineSegment StartX=-12.3 StartY=-15 StartZ=0 EndX=12.3 EndY=-15 EndZ=0
    g3: LineSegment StartX=12.3 StartY=-15 StartZ=0 EndX=11.8698 EndY=-8.57666 EndZ=0
    g4: ArcOfCircle CenterX=11.2212 CenterY=-8.6201 CenterZ=0 NormalX=0 NormalY=0 NormalZ=1 AngleXU=0 Radius=0.65 StartAngle=0.0668757 EndAngle=2.48655
    g5: ArcOfCircle CenterX=-11.2212 CenterY=-8.6201 CenterZ=0 NormalX=0 NormalY=0 NormalZ=1 AngleXU=0 Radius=0.65 StartAngle=0.655044 EndAngle=3.07472
  constraints (14):
    c: Coincident(g0,g-1)
    c: Diameter(g0) = 27
    c: Coincident(g1,g2)
    c: Coincident(g2,g3)
    c: Coincident(g1,g-3)
    c: Coincident(g2,g-4)
    c: Tangent(g3,g4) = -1.5708
    c: Tangent(g0,g4) = 1.5708
    c: Tangent(g0,g5) = 1.5708
    c: Tangent(g1,g5) = -1.5708
    c: Equal(g4,g5)
    c: Horizontal(g4,g5)
    c: Parallel(g-4,g3)
    c: Radius(g4) = 0.65
FEATURE [PartDesign::Pocket] Pocket019
  BaseFeature = -> Pocket018
  Length = 5.25
  Length2 = 100
  Placement = pos=(0,0,0) rot=(0.57735,0.57735,0.57735;2.0944rad)
  Profile = -> Sketch060
  Type = 0
FEATURE [Sketcher::SketchObject] Sketch061
  ExternalGeometry = -> [Pocket019]
  FullyConstrained = true
  MapMode = 5
  Placement = pos=(-6.5,1.4e-15,-1.5e-15) rot=(0.57735,0.57735,-0.57735;4.18879rad)
  Support = -> [Pocket019]
  sketch-geometry (6):
    g0: ArcOfCircle CenterX=0 CenterY=0 CenterZ=0 NormalX=0 NormalY=0 NormalZ=1 AngleXU=0 Radius=13.5 StartAngle=0.655044 EndAngle=2.48655
    g1: LineSegment StartX=11.8698 StartY=8.57666 StartZ=0 EndX=12.3 EndY=15 EndZ=0
    g2: LineSegment StartX=12.3 StartY=15 StartZ=0 EndX=-12.3 EndY=15 EndZ=0
    g3: LineSegment StartX=-12.3 StartY=15 StartZ=0 EndX=-11.8698 EndY=8.57666 EndZ=0
    g4: ArcOfCircle CenterX=-11.2212 CenterY=8.6201 CenterZ=0 NormalX=0 NormalY=0 NormalZ=1 AngleXU=0 Radius=0.65 StartAngle=3.20847 EndAngle=5.62814
    g5: ArcOfCircle CenterX=11.2212 CenterY=8.6201 CenterZ=0 NormalX=0 NormalY=0 NormalZ=1 AngleXU=0 Radius=0.65 StartAngle=3.79664 EndAngle=6.21631
  constraints (14):
    c: Coincident(g0,g-1)
    c: Radius(g0) = 13.5
    c: Coincident(g1,g2)
    c: Coincident(g2,g-3)
    c: Coincident(g2,g3)
    c: Coincident(g-4,g1)
    c: Tangent(g3,g4) = -1.5708
    c: Tangent(g0,g4) = 1.5708
    c: Tangent(g0,g5) = 1.5708
    c: Tangent(g1,g5) = -1.5708
    c: Equal(g4,g5)
    c: Radius(g4) = 0.65
    c: Parallel(g-4,g1)
    c: Parallel(g3,g-3)
FEATURE [PartDesign::Pocket] Pocket020
  BaseFeature = -> Pocket019
  Length = 5.25
  Length2 = 100
  Placement = pos=(0,0,0) rot=(0.57735,0.57735,0.57735;2.0944rad)
  Profile = -> Sketch061
  Type = 0
FEATURE [PartDesign::Chamfer] Chamfer001
  Angle = 45
  Base = -> Pocket020 [Edge159,Edge155,Edge22,Edge27]
  BaseFeature = -> Pocket020
  ChamferType = 0
  FlipDirection = false
  Placement = pos=(0,0,0) rot=(0.57735,0.57735,0.57735;2.0944rad)
  Size = 2
  Size2 = 1
  SupportTransform = false
FEATURE [Sketcher::SketchObject] Sketch062
  ExternalGeometry = -> [Chamfer001]
  FullyConstrained = true
  MapMode = 5
  Placement = pos=(-3.75,5e-15,-2.7e-15) rot=(-0.57735,-0.57735,0.57735;2.0944rad)
  Support = -> [Chamfer001]
  sketch-geometry (13):
    g0: ArcOfCircle CenterX=-6.9e-15 CenterY=-3.7e-15 CenterZ=0 NormalX=0 NormalY=0 NormalZ=1 AngleXU=0 Radius=11 StartAngle=5.75419 EndAngle=6.81218
    g1: ArcOfCircle CenterX=-6.9e-15 CenterY=-3.7e-15 CenterZ=0 NormalX=0 NormalY=0 NormalZ=1 AngleXU=0 Radius=12.2 StartAngle=5.94045 EndAngle=6.62592
    g2: ArcOfCircle CenterX=-6.9e-15 CenterY=-3.7e-15 CenterZ=0 NormalX=0 NormalY=0 NormalZ=1 AngleXU=0 Radius=11 StartAngle=2.6126 EndAngle=3.67059
    g3: ArcOfCircle CenterX=-6.9e-15 CenterY=-3.7e-15 CenterZ=0 NormalX=0 NormalY=0 NormalZ=1 AngleXU=0 Radius=12.2 StartAngle=2.79886 EndAngle=3.48433
    g4: Ellipse CenterX=-6.9e-15 CenterY=-3.7e-15 CenterZ=0 NormalX=0 NormalY=0 NormalZ=1 MajorRadius=13.5 MinorRadius=7.81051 AngleXU=-3e-16
    g5: LineSegment StartX=13.5 StartY=-7.4e-15 StartZ=0 EndX=-13.5 EndY=0 EndZ=0
    g6: LineSegment StartX=-4.8e-15 StartY=7.81051 StartZ=0 EndX=-9.1e-15 EndY=-7.81051 EndZ=0
    g7: GeomPoint X=11.0112 Y=-6.8e-15 Z=0
    g8: GeomPoint X=-11.0112 Y=-7e-16 Z=0
    g9: LineSegment StartX=-11.4904 StartY=4.1 StartZ=0 EndX=-9.49645 EndY=5.55135 EndZ=0
    g10: LineSegment StartX=-11.4904 StartY=-4.1 StartZ=0 EndX=-9.49645 EndY=-5.55135 EndZ=0
    g11: LineSegment StartX=9.49645 StartY=-5.55135 StartZ=0 EndX=11.4904 EndY=-4.1 EndZ=0
    g12: LineSegment StartX=11.4904 StartY=4.1 StartZ=0 EndX=9.49645 EndY=5.55135 EndZ=0
  constraints (29):
    c: Coincident(g0,g-4)
    c: PointOnObject(g0,g-4)
    c: Coincident(g1,g0)
    c: PointOnObject(g1,g-3)
    c: Coincident(g2,g0)
    c: PointOnObject(g2,g-4)
    c: Coincident(g3,g0)
    c: PointOnObject(g3,g-3)
    c: InternalAlignment(g5-g8 -> g4) x4
    c: Coincident(g4,g0)
    c: PointOnObject(g3,g4)
    c: PointOnObject(g2,g4)
    c: PointOnObject(g3,g4)
    c: PointOnObject(g2,g4)
    c: PointOnObject(g0,g4)
    c: PointOnObject(g1,g4)
    c: PointOnObject(g1,g4)
    c: PointOnObject(g0,g4)
    c: PointOnObject(g5,g-1)
    c: DistanceX(g5,g5) = 27
    c: DistanceY(g3,g3) = 8.2
    c: Coincident(g9,g3)
    c: Coincident(g9,g2)
    c: Coincident(g10,g3)
    c: Coincident(g10,g2)
    c: Coincident(g11,g0)
    c: Coincident(g11,g1)
    c: Coincident(g12,g1)
    c: Coincident(g12,g0)
FEATURE [PartDesign::Pocket] Pocket021
  BaseFeature = -> Chamfer001
  Length = 5
  Length2 = 100
  Placement = pos=(0,0,0) rot=(0.57735,0.57735,0.57735;2.0944rad)
  Profile = -> Sketch062
  Type = 0
FEATURE [PartDesign::Body] Body057  label="Metal case001"
  Group = -> [Sketch053,Pad017,Sketch054,Pocket013,Sketch055,Pocket014,Sketch056,Pocket015,Mirrored001,Sketch057,Pocket016,Sketch058,Pocket017,Sketch059,Pocket018,Sketch060,Pocket019,Sketch061,Pocket020,Chamfer001,Sketch062,Pocket021]
  Origin = -> Origin072
  Tip = -> Pocket021
FEATURE [App::DocumentObjectGroup] Group013  label="Case001"
  Group = -> [Body057]
FEATURE [App::Part] Part015  label="KP08-002"
  Group = -> [Group007,Body038,Body037,Body042,Body039,Body043,Body041,Body040,Group008,Body045,Body044,Group009,Body050,Body049,Body052,Body048,Body051,Body047,Body046,Group010,Body056,Body055,Group011,Body053,Body054,Group012,Body036,Group013,Body057]
  Origin = -> Origin073
  Placement = pos=(10,120,105) rot=(0,0,1;0rad)
FEATURE [Sketcher::SketchObject] Sketch063
  FullyConstrained = true
  MapMode = 5
  Placement = pos=(0,0,0) rot=(-0.57735,0.57735,0.57735;4.18879rad)
  Support = -> [YZ_Plane080]
  sketch-geometry (1):
    g0: Circle CenterX=0 CenterY=-7.5 CenterZ=0 NormalX=0 NormalY=0 NormalZ=1 AngleXU=0 Radius=0.25
  constraints (3):
    c: PointOnObject(g0,g-2)
    c: DistanceY(g0) = -7.5
    c: Diameter(g0) = 0.5
FEATURE [Sketcher::SketchObject] Sketch064
  FullyConstrained = true
  MapMode = 5
  Support = -> [XY_Plane073]
  sketch-geometry (2):
    g0: LineSegment StartX=0 StartY=5.5 StartZ=0 EndX=6e-16 EndY=9.5 EndZ=0
    g1: ArcOfCircle CenterX=0 CenterY=7.5 CenterZ=0 NormalX=0 NormalY=0 NormalZ=1 AngleXU=0 Radius=2 StartAngle=4.71239 EndAngle=7.85398
  constraints (7):
    c: PointOnObject(g0,g-2)
    c: PointOnObject(g0,g-2)
    c: PointOnObject(g1,g0)
    c: Coincident(g1,g0)
    c: Coincident(g1,g0)
    c: Radius(g1) = 2
    c: DistanceY(g1) = 7.5
FEATURE [PartDesign::Revolution] Revolution018
  Angle = 360
  Axis = (0,1,0)
  Base = (0,0,0)
  Profile = -> Sketch064
  ReferenceAxis = -> Sketch064 [V_Axis]
  Reversed = true
FEATURE [PartDesign::Body] Body059  label="Ball 015"
  Group = -> [Sketch064,Revolution018]
  Origin = -> Origin075
  Tip = -> Revolution018
FEATURE [PartDesign::FeatureBase] Clone028
  BaseFeature = -> Body059
FEATURE [PartDesign::Body] Body060  label="Ball 016"
  BaseFeature = -> Body059
  Group = -> [Clone028]
  Origin = -> Origin076
  Placement = pos=(0,0,0) rot=(-1,0,0;0.897598rad)
  Tip = -> Clone028
FEATURE [PartDesign::FeatureBase] Clone029
  BaseFeature = -> Body059
FEATURE [PartDesign::Body] Body061  label="Ball 017"
  BaseFeature = -> Body059
  Group = -> [Clone029]
  Origin = -> Origin077
  Placement = pos=(0,0,0) rot=(-1,0,0;1.7952rad)
  Tip = -> Clone029
FEATURE [PartDesign::FeatureBase] Clone030
  BaseFeature = -> Body059
FEATURE [PartDesign::Body] Body062  label="Ball 018"
  BaseFeature = -> Body059
  Group = -> [Clone030]
  Origin = -> Origin078
  Placement = pos=(0,0,0) rot=(1,0,0;3.59039rad)
  Tip = -> Clone030
FEATURE [PartDesign::FeatureBase] Clone031
  BaseFeature = -> Body059
FEATURE [PartDesign::Body] Body063  label="Ball 019"
  BaseFeature = -> Body059
  Group = -> [Clone031]
  Origin = -> Origin079
  Placement = pos=(0,0,0) rot=(1,0,0;2.69279rad)
  Tip = -> Clone031
FEATURE [PartDesign::FeatureBase] Clone032
  BaseFeature = -> Body059
FEATURE [PartDesign::Body] Body064  label="Ball 020"
  BaseFeature = -> Body059
  Group = -> [Clone032]
  Origin = -> Origin080
  Placement = pos=(0,0,0) rot=(1,0,0;1.7952rad)
  Tip = -> Clone032
FEATURE [PartDesign::FeatureBase] Clone033
  BaseFeature = -> Body059
FEATURE [PartDesign::Body] Body065  label="Ball 021"
  BaseFeature = -> Body059
  Group = -> [Clone033]
  Origin = -> Origin081
  Placement = pos=(0,0,0) rot=(1,0,0;0.897598rad)
  Tip = -> Clone033
FEATURE [App::DocumentObjectGroup] Group014  label="Balls002"
  Group = -> [Body059,Body060,Body061,Body062,Body063,Body064,Body065]
FEATURE [Sketcher::SketchObject] Sketch065
  FullyConstrained = true
  MapMode = 5
  Support = -> [XY_Plane082]
  sketch-geometry (7):
    g0: LineSegment StartX=-5 StartY=7.5 StartZ=0 EndX=5 EndY=7.5 EndZ=0
    g1: LineSegment StartX=-0.210977 StartY=7.5 StartZ=0 EndX=0.210977 EndY=7.5 EndZ=0
    g2: ArcOfCircle CenterX=0.25 CenterY=7.5 CenterZ=0 NormalX=0 NormalY=0 NormalZ=1 AngleXU=0 Radius=0.460977 StartAngle=2.43297 EndAngle=3.14159
    g3: ArcOfCircle CenterX=-0.25 CenterY=7.5 CenterZ=0 NormalX=0 NormalY=0 NormalZ=1 AngleXU=0 Radius=0.460977 StartAngle=9.792e-13 EndAngle=0.708626
    g4: LineSegment StartX=-0.1 StartY=7.8 StartZ=0 EndX=-0.1 EndY=7.75 EndZ=0
    g5: LineSegment StartX=-0.1 StartY=7.75 StartZ=0 EndX=0.1 EndY=7.75 EndZ=0
    g6: LineSegment StartX=0.1 StartY=7.75 StartZ=0 EndX=0.1 EndY=7.8 EndZ=0
  constraints (22):
    c: DistanceY(g-1,g0) = 7.5
    c: Symmetric(g0,g0,g-2)
    c: DistanceX(g0,g0) = 10
    c: PointOnObject(g1,g0)
    c: PointOnObject(g1,g0)
    c: Coincident(g3,g1)
    c: Coincident(g2,g1)
    c: Coincident(g2,g4)
    c: Coincident(g4,g5)
    c: Horizontal(g5)
    c: Coincident(g5,g6)
    c: Coincident(g6,g3)
    c: Vertical(g6)
    c: Equal(g3,g2)
    c: Vertical(g4)
    c: Symmetric(g2,g3,g-2)
    c: DistanceX(g5,g5) = 0.2
    c: Distance(g5,g1) = 0.25
    c: DistanceX(g3,g-1) = 0.25
    c: PointOnObject(g3,g1)
    c: PointOnObject(g2,g1)
    c: Distance(g3,g1) = 0.3
FEATURE [PartDesign::Revolution] Revolution019
  Angle = 360
  Axis = (10,0,0)
  Base = (-5,7.5,0)
  Profile = -> Sketch065
  ReferenceAxis = -> Sketch065 [Axis]
FEATURE [PartDesign::Body] Body068  label="Rivet 015"
  Group = -> [Sketch065,Revolution019]
  Origin = -> Origin084
  Placement = pos=(0,0,0) rot=(1,0,0;0.448799rad)
  Tip = -> Revolution019
FEATURE [PartDesign::FeatureBase] Clone035
  BaseFeature = -> Body068
  Placement = pos=(0,0,0) rot=(1,0,0;0.448799rad)
FEATURE [PartDesign::Body] Body069  label="Rivet 016"
  BaseFeature = -> Body068
  Group = -> [Clone035]
  Origin = -> Origin085
  Placement = pos=(0,0,0) rot=(1,0,0;0.897598rad)
  Tip = -> Clone035
FEATURE [PartDesign::FeatureBase] Clone036
  BaseFeature = -> Body068
  Placement = pos=(0,0,0) rot=(1,0,0;0.448799rad)
FEATURE [PartDesign::Body] Body070  label="Rivet 017"
  BaseFeature = -> Body068
  Group = -> [Clone036]
  Origin = -> Origin086
  Placement = pos=(0,0,0) rot=(1,0,0;1.7952rad)
  Tip = -> Clone036
FEATURE [PartDesign::FeatureBase] Clone037
  BaseFeature = -> Body068
  Placement = pos=(0,0,0) rot=(1,0,0;0.448799rad)
FEATURE [PartDesign::Body] Body071  label="Rivet 018"
  BaseFeature = -> Body068
  Group = -> [Clone037]
  Origin = -> Origin087
  Placement = pos=(0,0,0) rot=(1,0,0;2.69279rad)
  Tip = -> Clone037
FEATURE [PartDesign::FeatureBase] Clone038
  BaseFeature = -> Body068
  Placement = pos=(0,0,0) rot=(1,0,0;0.448799rad)
FEATURE [PartDesign::Body] Body072  label="Rivet 019"
  BaseFeature = -> Body068
  Group = -> [Clone038]
  Origin = -> Origin088
  Placement = pos=(0,0,0) rot=(1,0,0;3.59039rad)
  Tip = -> Clone038
FEATURE [PartDesign::FeatureBase] Clone039
  BaseFeature = -> Body068
  Placement = pos=(0,0,0) rot=(1,0,0;0.448799rad)
FEATURE [PartDesign::Body] Body073  label="Rivet 020"
  BaseFeature = -> Body068
  Group = -> [Clone039]
  Origin = -> Origin089
  Placement = pos=(0,0,0) rot=(-1,0,0;1.7952rad)
  Tip = -> Clone039
FEATURE [PartDesign::FeatureBase] Clone040
  BaseFeature = -> Body068
  Placement = pos=(0,0,0) rot=(1,0,0;0.448799rad)
FEATURE [PartDesign::Body] Body074  label="Rivet 021"
  BaseFeature = -> Body068
  Group = -> [Clone040]
  Origin = -> Origin090
  Placement = pos=(0,0,0) rot=(-1,0,0;0.897598rad)
  Tip = -> Clone040
FEATURE [App::DocumentObjectGroup] Group016  label="Rivets002"
  Group = -> [Body068,Body069,Body070,Body071,Body072,Body073,Body074]
FEATURE [Sketcher::SketchObject] Sketch066
  FullyConstrained = true
  MapMode = 5
  Placement = pos=(0,0,0) rot=(1,0,0;1.5708rad)
  Support = -> [XZ_Plane080]
  sketch-geometry (4):
    g0: LineSegment StartX=0 StartY=8.5 StartZ=0 EndX=0.1 EndY=8.5 EndZ=0
    g1: LineSegment StartX=0.1 StartY=8.5 StartZ=0 EndX=0.1 EndY=6.5 EndZ=0
    g2: LineSegment StartX=0.1 StartY=6.5 StartZ=0 EndX=0 EndY=6.5 EndZ=0
    g3: LineSegment StartX=0 StartY=6.5 StartZ=0 EndX=0 EndY=8.5 EndZ=0
  constraints (12):
    c: Coincident(g0,g1)
    c: Coincident(g1,g2)
    c: Coincident(g2,g3)
    c: Coincident(g3,g0)
    c: Horizontal(g0)
    c: Horizontal(g2)
    c: Vertical(g1)
    c: Vertical(g3)
    c: PointOnObject(g0,g-2)
    c: DistanceX(g0,g0) = 0.1
    c: DistanceY(g0) = 8.5
    c: DistanceY(g1) = 6.5
FEATURE [PartDesign::Revolution] Revolution020
  Angle = 360
  Axis = (1,0,0)
  Base = (0,0,0)
  Placement = pos=(0,0,0) rot=(1,0,0;1.5708rad)
  Profile = -> Sketch066
  ReferenceAxis = -> Sketch066 [H_Axis]
FEATURE [Sketcher::SketchObject] Sketch067
  FullyConstrained = true
  MapMode = 5
  Placement = pos=(0,0,0) rot=(0.57735,0.57735,0.57735;2.0944rad)
  Support = -> [YZ_Plane080]
  sketch-geometry (5):
    g0: ArcOfCircle CenterX=0 CenterY=7.5 CenterZ=0 NormalX=0 NormalY=0 NormalZ=1 AngleXU=0 Radius=2.11 StartAngle=5.66076 EndAngle=6.65667
    g1: LineSegment StartX=5e-16 StartY=8.5 StartZ=0 EndX=0 EndY=6.26986 EndZ=0
    g2: ArcOfCircle CenterX=0 CenterY=0 CenterZ=0 NormalX=0 NormalY=0 NormalZ=1 AngleXU=0 Radius=6.5 StartAngle=1.3039 EndAngle=1.5708
    g3: LineSegment StartX=1.71431 StartY=6.26986 StartZ=0 EndX=0 EndY=6.26986 EndZ=0
    g4: ArcOfCircle CenterX=0 CenterY=0 CenterZ=0 NormalX=0 NormalY=0 NormalZ=1 AngleXU=0 Radius=8.5 StartAngle=1.33757 EndAngle=1.5708
  constraints (16):
    c: PointOnObject(g0,g-2)
    c: DistanceY(g0) = 7.5
    c: Radius(g0) = 2.11
    c: PointOnObject(g2,g1)
    c: DistanceY(g2) = 6.5
    c: Coincident(g2,g-1)
    c: Coincident(g3,g2)
    c: Horizontal(g3)
    c: Coincident(g0,g2)
    c: Coincident(g1,g3)
    c: PointOnObject(g1,g-2)
    c: PointOnObject(g1,g-2)
    c: Coincident(g4,g-1)
    c: Coincident(g4,g1)
    c: DistanceY(g1) = 8.5
    c: Coincident(g0,g4)
FEATURE [PartDesign::Revolution] Revolution021
  Angle = 180
  Axis = (-2e-16,3e-16,1)
  Base = (0,0,0)
  BaseFeature = -> Revolution020
  Placement = pos=(0,0,0) rot=(1,0,0;1.5708rad)
  Profile = -> Sketch067
  ReferenceAxis = -> Sketch067 [V_Axis]
  Reversed = true
FEATURE [PartDesign::PolarPattern] PolarPattern008
  Angle = 360
  Axis = -> Sketch067 [N_Axis]
  BaseFeature = -> Revolution021
  Occurrences = 3
  Originals = -> [Revolution021]
  Placement = pos=(0,0,0) rot=(1,0,0;1.5708rad)
  Refine = true
FEATURE [Sketcher::SketchObject] Sketch068
  FullyConstrained = true
  MapMode = 5
  Placement = pos=(0,0,0) rot=(0.57735,0.57735,0.57735;2.0944rad)
  Support = -> [YZ_Plane080]
  sketch-geometry (4):
    g0: ArcOfCircle CenterX=0 CenterY=7.5 CenterZ=0 NormalX=0 NormalY=0 NormalZ=1 AngleXU=0 Radius=2.01 StartAngle=5.57985 EndAngle=6.86228
    g1: LineSegment StartX=0 StartY=6.2 StartZ=0 EndX=1.533 EndY=6.2 EndZ=0
    g2: LineSegment StartX=0 StartY=8.6 StartZ=0 EndX=0 EndY=6.2 EndZ=0
    g3: LineSegment StartX=0 StartY=8.6 StartZ=0 EndX=1.68229 EndY=8.6 EndZ=0
  constraints (13):
    c: PointOnObject(g0,g-2)
    c: DistanceY(g0) = 7.5
    c: Radius(g0) = 2.01
    c: PointOnObject(g1,g-2)
    c: Horizontal(g1)
    c: Coincident(g0,g1)
    c: DistanceY(g1) = 6.2
    c: DistanceY(g2) = 8.6
    c: Coincident(g2,g1)
    c: PointOnObject(g2,g-2)
    c: Coincident(g3,g2)
    c: Horizontal(g3)
    c: Coincident(g0,g3)
FEATURE [PartDesign::Groove] Groove002
  Angle = 360
  Axis = (-2e-16,3e-16,1)
  Base = (0,0,0)
  BaseFeature = -> PolarPattern008
  Placement = pos=(0,0,0) rot=(1,0,0;1.5708rad)
  Profile = -> Sketch068
  ReferenceAxis = -> Sketch068 [V_Axis]
FEATURE [PartDesign::PolarPattern] PolarPattern009
  Angle = 360
  Axis = -> Sketch068 [N_Axis]
  BaseFeature = -> Groove002
  Occurrences = 3
  Originals = -> [Groove002]
  Placement = pos=(0,0,0) rot=(1,0,0;1.5708rad)
FEATURE [PartDesign::Pocket] Pocket022
  BaseFeature = -> PolarPattern009
  Length = 5
  Length2 = 100
  Placement = pos=(0,0,0) rot=(1,0,0;1.5708rad)
  Profile = -> Sketch063
  Type = 1
FEATURE [PartDesign::PolarPattern] PolarPattern010
  Angle = 360
  Axis = -> Sketch063 [N_Axis]
  BaseFeature = -> Pocket022
  Occurrences = 3
  Originals = -> [Pocket022]
  Placement = pos=(0,0,0) rot=(1,0,0;1.5708rad)
FEATURE [PartDesign::Body] Body066  label="Cage 005"
  Group = -> [Sketch066,Revolution020,Sketch067,Revolution021,PolarPattern008,Sketch068,Groove002,PolarPattern009,Sketch063,Pocket022,PolarPattern010]
  Origin = -> Origin082
  Placement = pos=(0,0,0) rot=(-1,0,0;1.5708rad)
  Tip = -> PolarPattern010
FEATURE [PartDesign::FeatureBase] Clone034
  BaseFeature = -> Body066
  Placement = pos=(0,0,0) rot=(-1,0,0;1.5708rad)
FEATURE [PartDesign::Body] Body067  label="Cage 006"
  BaseFeature = -> Body066
  Group = -> [Clone034]
  Origin = -> Origin083
  Placement = pos=(0,0,0) rot=(0,1,0;3.14159rad)
  Tip = -> Clone034
FEATURE [App::DocumentObjectGroup] Group015  label="Cages002"
  Group = -> [Body066,Body067]
FEATURE [Sketcher::SketchObject] Sketch069
  FullyConstrained = true
  MapMode = 5
  Support = -> [XY_Plane089]
  sketch-geometry (14):
    g0: ArcOfCircle CenterX=-1e-16 CenterY=7.5 CenterZ=0 NormalX=0 NormalY=0 NormalZ=1 AngleXU=0 Radius=2 StartAngle=0.848062 EndAngle=2.29353
    g1: LineSegment StartX=-3.5 StartY=11 StartZ=0 EndX=3.5 EndY=11 EndZ=0
    g2: LineSegment StartX=3.5 StartY=11 StartZ=0 EndX=3.5 EndY=9.2 EndZ=0
    g3: LineSegment StartX=2.9 StartY=9 StartZ=0 EndX=1.32288 EndY=9 EndZ=0
    g4: LineSegment StartX=-3.5 StartY=9.2 StartZ=0 EndX=-3.5 EndY=11 EndZ=0
    g5: LineSegment StartX=-1.32288 StartY=9 StartZ=0 EndX=-2.9 EndY=9 EndZ=0
    g6: LineSegment StartX=2.9 StartY=9 StartZ=0 EndX=2.9 EndY=9.5 EndZ=0
    g7: LineSegment StartX=2.9 StartY=9.5 StartZ=0 EndX=3.2 EndY=9.5 EndZ=0
    g8: LineSegment StartX=3.2 StartY=9.5 StartZ=0 EndX=3.2 EndY=9.2 EndZ=0
    g9: LineSegment StartX=3.2 StartY=9.2 StartZ=0 EndX=3.5 EndY=9.2 EndZ=0
    g10: LineSegment StartX=-3.5 StartY=9.2 StartZ=0 EndX=-3.2 EndY=9.2 EndZ=0
    g11: LineSegment StartX=-3.2 StartY=9.2 StartZ=0 EndX=-3.2 EndY=9.5 EndZ=0
    g12: LineSegment StartX=-3.2 StartY=9.5 StartZ=0 EndX=-2.9 EndY=9.5 EndZ=0
    g13: LineSegment StartX=-2.9 StartY=9.5 StartZ=0 EndX=-2.9 EndY=9 EndZ=0
  constraints (41):
    c: Coincident(g1,g2)
    c: Coincident(g4,g1)
    c: Horizontal(g3)
    c: Vertical(g2)
    c: Vertical(g4)
    c: Coincident(g0,g5)
    c: Coincident(g0,g3)
    c: DistanceY(g-1,g0) = 7.5
    c: Radius(g0) = 2
    c: Symmetric(g1,g1,g-2)
    c: Symmetric(g0,g0,g-2)
    c: DistanceY(g1) = 11
    c: DistanceX(g1,g1) = 7
    c: Vertical(g6)
    c: Coincident(g6,g7)
    c: Horizontal(g7)
    c: Coincident(g7,g8)
    c: Vertical(g8)
    c: Coincident(g8,g9)
    c: Coincident(g3,g6)
    c: Coincident(g2,g9)
    c: Horizontal(g10)
    c: Coincident(g10,g11)
    c: Coincident(g11,g12)
    c: Horizontal(g12)
    c: Coincident(g12,g13)
    c: Vertical(g13)
    c: Vertical(g11)
    c: Coincident(g4,g10)
    c: Coincident(g5,g13)
    c: DistanceY(g13,g13) = 0.5
    c: DistanceX(g12,g12) = 0.3
    c: DistanceY(g5,g10) = 0.2
    c: Symmetric(g5,g3,g-2)
    c: DistanceY(g3) = 9
    c: DistanceY(g6) = 9.5
    c: Equal(g7,g12)
    c: Equal(g13,g6)
    c: Horizontal(g9)
    c: Horizontal(g8,g10)
    c: Equal(g12,g10)
FEATURE [PartDesign::Revolution] Revolution022
  Angle = 360
  Axis = (1,0,0)
  Base = (0,0,0)
  Profile = -> Sketch069
  ReferenceAxis = -> X_Axis089
FEATURE [PartDesign::Fillet] Fillet160
  Base = -> Revolution022 [Edge14,Edge15]
  BaseFeature = -> Revolution022
  Radius = 0.3
  SupportTransform = false
FEATURE [PartDesign::Body] Body075  label="Outer Ring003"
  Group = -> [Sketch069,Revolution022,Fillet160]
  Origin = -> Origin091
  Tip = -> Fillet160
FEATURE [Sketcher::SketchObject] Sketch070
  FullyConstrained = true
  MapMode = 5
  Support = -> [XY_Plane090]
  sketch-geometry (14):
    g0: LineSegment StartX=-2.9 StartY=6 StartZ=0 EndX=-1.32288 EndY=6 EndZ=0
    g1: LineSegment StartX=-3.5 StartY=4 StartZ=0 EndX=-3.5 EndY=5.7 EndZ=0
    g2: ArcOfCircle CenterX=-1e-16 CenterY=7.5 CenterZ=0 NormalX=0 NormalY=0 NormalZ=1 AngleXU=0 Radius=2 StartAngle=3.98965 EndAngle=5.43512
    g3: LineSegment StartX=1.32288 StartY=6 StartZ=0 EndX=2.9 EndY=6 EndZ=0
    g4: LineSegment StartX=-3.5 StartY=5.7 StartZ=0 EndX=-3.2 EndY=5.7 EndZ=0
    g5: LineSegment StartX=-3.2 StartY=5.7 StartZ=0 EndX=-3.2 EndY=5.5 EndZ=0
    g6: LineSegment StartX=-3.2 StartY=5.5 StartZ=0 EndX=-2.9 EndY=5.5 EndZ=0
    g7: LineSegment StartX=-2.9 StartY=5.5 StartZ=0 EndX=-2.9 EndY=6 EndZ=0
    g8: LineSegment StartX=8.5 StartY=6 StartZ=0 EndX=3.2 EndY=6 EndZ=0
    g9: LineSegment StartX=3.2 StartY=6 StartZ=0 EndX=3.2 EndY=5.5 EndZ=0
    g10: LineSegment StartX=3.2 StartY=5.5 StartZ=0 EndX=2.9 EndY=5.5 EndZ=0
    g11: LineSegment StartX=2.9 StartY=5.5 StartZ=0 EndX=2.9 EndY=6 EndZ=0
    g12: LineSegment StartX=8.5 StartY=4 StartZ=0 EndX=8.5 EndY=6 EndZ=0
    g13: LineSegment StartX=-3.5 StartY=4 StartZ=0 EndX=8.5 EndY=4 EndZ=0
  constraints (43):
    c: Horizontal(g0)
    c: Vertical(g1)
    c: DistanceY(g1) = 4
    c: Coincident(g2,g0)
    c: Coincident(g2,g3)
    c: Horizontal(g3)
    c: Radius(g2) = 2
    c: DistanceY(g2) = 7.5
    c: Symmetric(g0,g2,g-2)
    c: Horizontal(g4)
    c: Coincident(g4,g5)
    c: Vertical(g5)
    c: Coincident(g5,g6)
    c: Horizontal(g6)
    c: Coincident(g6,g7)
    c: Vertical(g7)
    c: Horizontal(g8)
    c: Coincident(g8,g9)
    c: Vertical(g9)
    c: Coincident(g9,g10)
    c: Horizontal(g10)
    c: Coincident(g10,g11)
    c: Vertical(g11)
    c: Coincident(g3,g11)
    c: Coincident(g0,g7)
    c: Coincident(g1,g4)
    c: DistanceY(g3) = 6
    c: DistanceY(g6,g0) = 0.5
    c: DistanceX(g4,g4) = 0.3
    c: DistanceX(g6,g6) = 0.3
    c: DistanceY(g5,g4) = 0.2
    c: Vertical(g12)
    c: Equal(g11,g7)
    c: DistanceY(g1,g0) = 2
    c: DistanceX(g8,g8) = 5.3
    c: Coincident(g13,g1)
    c: Coincident(g13,g12)
    c: Horizontal(g13)
    c: DistanceX(g13,g13) = 12
    c: DistanceX(g1,g2) = 3.5
    c: Coincident(g8,g12)
    c: Equal(g7,g9)
    c: Equal(g6,g10)
FEATURE [PartDesign::Revolution] Revolution023
  Angle = 360
  Axis = (1,0,0)
  Base = (0,0,0)
  Profile = -> Sketch070
  ReferenceAxis = -> X_Axis090
FEATURE [PartDesign::Fillet] Fillet161
  Base = -> Revolution023 [Edge13,Edge11]
  BaseFeature = -> Revolution023
  Radius = 0.2
  SupportTransform = false
FEATURE [PartDesign::Body] Body076  label="Inner Ring003"
  Group = -> [Sketch070,Revolution023,Fillet161]
  Origin = -> Origin092
  Tip = -> Fillet161
FEATURE [App::DocumentObjectGroup] Group018  label="Rings002"
  Group = -> [Body075,Body076]
FEATURE [Sketcher::SketchObject] Sketch071
  FullyConstrained = true
  MapMode = 5
  Placement = pos=(0,0,0) rot=(1,0,0;1.5708rad)
  Support = -> [XZ_Plane091]
  sketch-geometry (12):
    g0: LineSegment StartX=2.9 StartY=9.5 StartZ=0 EndX=2.9 EndY=8.5 EndZ=0
    g1: LineSegment StartX=2.9 StartY=8.5 StartZ=0 EndX=3.2 EndY=8.5 EndZ=0
    g2: LineSegment StartX=3.2 StartY=8.5 StartZ=0 EndX=3.2 EndY=6.5 EndZ=0
    g3: LineSegment StartX=3.2 StartY=6.5 StartZ=0 EndX=2.9 EndY=6.5 EndZ=0
    g4: LineSegment StartX=2.9 StartY=6.5 StartZ=0 EndX=2.9 EndY=5.5 EndZ=0
    g5: LineSegment StartX=2.9 StartY=5.5 StartZ=0 EndX=3.2 EndY=5.5 EndZ=0
    g6: LineSegment StartX=3.2 StartY=5.5 StartZ=0 EndX=3.2 EndY=6 EndZ=0
    g7: LineSegment StartX=3.2 StartY=6 StartZ=0 EndX=3.5 EndY=6 EndZ=0
    g8: LineSegment StartX=3.5 StartY=6 StartZ=0 EndX=3.5 EndY=9 EndZ=0
    g9: LineSegment StartX=3.5 StartY=9 StartZ=0 EndX=3.2 EndY=9 EndZ=0
    g10: LineSegment StartX=3.2 StartY=9 StartZ=0 EndX=3.2 EndY=9.5 EndZ=0
    g11: LineSegment StartX=3.2 StartY=9.5 StartZ=0 EndX=2.9 EndY=9.5 EndZ=0
  constraints (36):
    c: Vertical(g0)
    c: Coincident(g0,g1)
    c: Horizontal(g1)
    c: Coincident(g1,g2)
    c: Vertical(g2)
    c: Coincident(g2,g3)
    c: Horizontal(g3)
    c: Coincident(g3,g4)
    c: Vertical(g4)
    c: Coincident(g4,g5)
    c: Horizontal(g5)
    c: Coincident(g5,g6)
    c: Vertical(g6)
    c: Coincident(g6,g7)
    c: Horizontal(g7)
    c: Coincident(g7,g8)
    c: Vertical(g8)
    c: Coincident(g8,g9)
    c: Horizontal(g9)
    c: Coincident(g9,g10)
    c: Vertical(g10)
    c: Coincident(g10,g11)
    c: Coincident(g11,g0)
    c: Horizontal(g11)
    c: DistanceY(g4) = 5.5
    c: DistanceX(g4) = 2.9
    c: DistanceY(g5,g6) = 0.5
    c: DistanceY(g6,g2) = 0.5
    c: DistanceX(g5,g5) = 0.3
    c: Equal(g5,g7)
    c: Equal(g7,g3)
    c: Equal(g3,g1)
    c: Equal(g1,g9)
    c: Equal(g4,g0)
    c: Equal(g6,g10)
    c: DistanceY(g4,g0) = 4
FEATURE [PartDesign::Revolution] Revolution024
  Angle = 360
  Axis = (1,0,0)
  Base = (0,0,0)
  Placement = pos=(0,0,0) rot=(1,0,0;1.5708rad)
  Profile = -> Sketch071
  ReferenceAxis = -> Sketch071 [H_Axis]
FEATURE [PartDesign::Fillet] Fillet162
  Base = -> Revolution024 [Edge14,Edge12]
  BaseFeature = -> Revolution024
  Placement = pos=(0,0,0) rot=(1,0,0;1.5708rad)
  Radius = 0.2
  SupportTransform = false
FEATURE [PartDesign::Body] Body077  label="Seal 005"
  Group = -> [Sketch071,Revolution024,Fillet162]
  Origin = -> Origin093
  Tip = -> Fillet162
FEATURE [PartDesign::FeatureBase] Clone041
  BaseFeature = -> Body077
FEATURE [PartDesign::Body] Body078  label="Seal 006"
  BaseFeature = -> Body077
  Group = -> [Clone041]
  Origin = -> Origin094
  Placement = pos=(0,0,0) rot=(0,1,0;3.14159rad)
  Tip = -> Clone041
FEATURE [App::DocumentObjectGroup] Group017  label="Seals002"
  Group = -> [Body077,Body078]
FEATURE [Sketcher::SketchObject] Sketch072
  AttachmentOffset = pos=(0,0,4) rot=(0,0,1;0rad)
  FullyConstrained = true
  MapMode = 5
  Placement = pos=(0,0,4) rot=(0,0,1;0rad)
  Support = -> [XY_Plane072]
  sketch-geometry (1):
    g0: Circle CenterX=6 CenterY=0 CenterZ=0 NormalX=0 NormalY=0 NormalZ=1 AngleXU=0 Radius=1.5
  constraints (3):
    c: PointOnObject(g0,g-1)
    c: Diameter(g0) = 3
    c: DistanceX(g-1,g0) = 6
FEATURE [PartDesign::Pad] Pad018
  Direction = (0,0,1)
  Length = 3
  Length2 = 100
  Profile = -> Sketch072
  Type = 0
FEATURE [Sketcher::SketchObject] Sketch073
  ExternalGeometry = -> [Pad018]
  FullyConstrained = true
  MapMode = 5
  Placement = pos=(0,0,7) rot=(0,0,1;0rad)
  Support = -> [Pad018]
  sketch-geometry (7):
    g0: LineSegment StartX=6.43301 StartY=-0.75 StartZ=0 EndX=6.86603 EndY=0 EndZ=0
    g1: LineSegment StartX=6.86603 StartY=0 StartZ=0 EndX=6.43301 EndY=0.75 EndZ=0
    g2: LineSegment StartX=6.43301 StartY=0.75 StartZ=0 EndX=5.56699 EndY=0.75 EndZ=0
    g3: LineSegment StartX=5.56699 StartY=0.75 StartZ=0 EndX=5.13397 EndY=-1e-16 EndZ=0
    g4: LineSegment StartX=5.13397 StartY=-1e-16 StartZ=0 EndX=5.56699 EndY=-0.75 EndZ=0
    g5: LineSegment StartX=5.56699 StartY=-0.75 StartZ=0 EndX=6.43301 EndY=-0.75 EndZ=0
    g6: Circle CenterX=6 CenterY=0 CenterZ=0 NormalX=0 NormalY=0 NormalZ=1 AngleXU=0 Radius=0.866025
  constraints (16):
    c: Coincident(g0,g1)
    c: Coincident(g1,g2)
    c: Coincident(g2,g3)
    c: Coincident(g3,g4)
    c: Coincident(g4,g5)
    c: Coincident(g5,g0)
    c: Equal(g0, g1-g5) x5
    c: PointOnObject(g0,g6)
    c: PointOnObject(g1,g6)
    c: PointOnObject(g2,g6)
    c: PointOnObject(g3,g6)
    c: PointOnObject(g4,g6)
    c: PointOnObject(g5,g6)
    c: Coincident(g6,g-3)
    c: Horizontal(g5)
    c: DistanceY(g4,g2) = 1.5
FEATURE [PartDesign::Pocket] Pocket023
  BaseFeature = -> Pad018
  Length = 0.9
  Length2 = 100
  Profile = -> Sketch073
  Type = 0
FEATURE [PartDesign::PolarPattern] PolarPattern011
  Angle = 120
  Axis = -> X_Axis072
  BaseFeature = -> Pocket023
  Occurrences = 3
  Originals = -> [Pad018,Pocket023]
FEATURE [PartDesign::Body] Body058
  Group = -> [Sketch072,Pad018,Sketch073,Pocket023,PolarPattern011]
  Origin = -> Origin074
  Tip = -> PolarPattern011
FEATURE [App::DocumentObjectGroup] Group019  label="Set screws002"
  Group = -> [Body058]
FEATURE [Sketcher::SketchObject] Sketch074
  AttachmentOffset = pos=(0,0,-6.5) rot=(0,0,1;0rad)
  FullyConstrained = true
  MapMode = 5
  Placement = pos=(-6.5,1.4e-15,-1.4e-15) rot=(0.57735,0.57735,0.57735;2.0944rad)
  Support = -> [YZ_Plane093]
  sketch-geometry (14):
    g0: Circle CenterX=0 CenterY=0 CenterZ=0 NormalX=0 NormalY=0 NormalZ=1 AngleXU=0 Radius=11
    g1: ArcOfCircle CenterX=0 CenterY=0 CenterZ=0 NormalX=0 NormalY=0 NormalZ=1 AngleXU=0 Radius=13.5 StartAngle=0.0668757 EndAngle=3.07472
    g2: LineSegment StartX=-13.4698 StartY=0.902148 StartZ=0 EndX=-14.2 EndY=-10 EndZ=0
    g3: LineSegment StartX=-14.2 StartY=-10 StartZ=0 EndX=-27.5 EndY=-10 EndZ=0
    g4: LineSegment StartX=-27.5 StartY=-10 StartZ=0 EndX=-27.5 EndY=-15 EndZ=0
    g5: LineSegment StartX=-27.5 StartY=-15 StartZ=0 EndX=-12.3 EndY=-15 EndZ=0
    g6: LineSegment StartX=27.5 StartY=-15 StartZ=0 EndX=27.5 EndY=-10 EndZ=0
    g7: LineSegment StartX=27.5 StartY=-10 StartZ=0 EndX=14.2 EndY=-10 EndZ=0
    g8: LineSegment StartX=14.2 StartY=-10 StartZ=0 EndX=13.4698 EndY=0.902148 EndZ=0
    g9: LineSegment StartX=12.3 StartY=-15 StartZ=0 EndX=12.1995 EndY=-13.5 EndZ=0
    g10: LineSegment StartX=12.1995 StartY=-13.5 StartZ=0 EndX=-12.1995 EndY=-13.5 EndZ=0
    g11: LineSegment StartX=-12.1995 StartY=-13.5 StartZ=0 EndX=-12.3 EndY=-15 EndZ=0
    g12: LineSegment StartX=12.3 StartY=-15 StartZ=0 EndX=27.5 EndY=-15 EndZ=0
    g13: GeomPoint X=0 Y=13.5 Z=0
  constraints (39):
    c: Coincident(g0,g-1)
    c: Radius(g0) = 11
    c: Coincident(g1,g0)
    c: Coincident(g2,g3)
    c: Coincident(g3,g4)
    c: Coincident(g4,g5)
    c: Horizontal(g5)
    c: Coincident(g12,g6)
    c: Coincident(g6,g7)
    c: Horizontal(g7)
    c: Coincident(g7,g8)
    c: Coincident(g9,g10)
    c: Horizontal(g10)
    c: Coincident(g10,g11)
    c: Coincident(g5,g11)
    c: Coincident(g12,g9)
    c: Horizontal(g3)
    c: Vertical(g6)
    c: Vertical(g4)
    c: Equal(g9,g11)
    c: Horizontal(g12)
    c: Horizontal(g5,g9)
    c: Equal(g6,g4)
    c: Equal(g12,g5)
    c: Equal(g7,g3)
    c: DistanceX(g4,g6) = 55
    c: DistanceY(g6,g0) = 15
    c: Equal(g8,g2)
    c: DistanceY(g6,g6) = 5
    c: Parallel(g9,g8)
    c: DistanceY(g9,g9) = 1.5
    c: DistanceX(g5,g5) = 15.2
    c: Diameter(g1) = 27
    c: PointOnObject(g13,g1)
    c: PointOnObject(g13,g-2)
    c: DistanceY(g6,g13) = 28.5
    c: Tangent(g1,g2) = -1.5708
    c: Tangent(g1,g8) = -1.5708
    c: DistanceX(g3,g3) = 13.3
FEATURE [PartDesign::Pad] Pad019
  Direction = (1,-2e-16,3e-16)
  Length = 13
  Length2 = 100
  Placement = pos=(0,0,0) rot=(0.57735,0.57735,0.57735;2.0944rad)
  Profile = -> Sketch074
  Type = 0
FEATURE [Sketcher::SketchObject] Sketch075
  ExternalGeometry = -> [Pad019]
  FullyConstrained = true
  MapMode = 5
  Placement = pos=(4.2e-15,-6.6e-15,-15) rot=(0.707107,0.707107,0;3.14159rad)
  Support = -> [Pad019]
  sketch-geometry (7):
    g0: LineSegment StartX=-24.9 StartY=4.15 StartZ=0 EndX=-14.9 EndY=4.15 EndZ=0
    g1: LineSegment StartX=-14.9 StartY=4.15 StartZ=0 EndX=-14.9 EndY=-4.15 EndZ=0
    g2: LineSegment StartX=-14.9 StartY=-4.15 StartZ=0 EndX=-24.9 EndY=-4.15 EndZ=0
    g3: LineSegment StartX=-24.9 StartY=-4.15 StartZ=0 EndX=-24.9 EndY=4.15 EndZ=0
    g4: LineSegment StartX=-27.5 StartY=6.5 StartZ=0 EndX=-12.3 EndY=-6.5 EndZ=0
    g5: LineSegment StartX=-27.5 StartY=-6.5 StartZ=0 EndX=-12.3 EndY=6.5 EndZ=0
    g6: GeomPoint X=-19.9 Y=2.6e-15 Z=0
  constraints (17):
    c: Coincident(g0,g1)
    c: Coincident(g1,g2)
    c: Coincident(g2,g3)
    c: Coincident(g3,g0)
    c: Horizontal(g0)
    c: Horizontal(g2)
    c: Vertical(g1)
    c: Vertical(g3)
    c: DistanceX(g0,g0) = 10
    c: DistanceY(g1,g1) = 8.3
    c: Coincident(g4,g-3)
    c: Coincident(g4,g-4)
    c: Coincident(g5,g-4)
    c: Coincident(g5,g-3)
    c: PointOnObject(g6,g4)
    c: PointOnObject(g6,g5)
    c: Symmetric(g0,g1,g6)
FEATURE [PartDesign::Pocket] Pocket024
  BaseFeature = -> Pad019
  Length = 2.3
  Length2 = 100
  Placement = pos=(0,0,0) rot=(0.57735,0.57735,0.57735;2.0944rad)
  Profile = -> Sketch075
  Type = 0
FEATURE [Sketcher::SketchObject] Sketch076
  ExternalGeometry = -> [Pocket024]
  FullyConstrained = true
  MapMode = 5
  Placement = pos=(2.8e-15,-4.4e-15,-10) rot=(0,0,-1;1.5708rad)
  Support = -> [Pocket024]
  sketch-geometry (2):
    g0: Circle CenterX=21.2 CenterY=2.1e-15 CenterZ=0 NormalX=0 NormalY=0 NormalZ=1 AngleXU=0 Radius=2.5
    g1: LineSegment StartX=21.2 StartY=2.1e-15 StartZ=0 EndX=27.5 EndY=2.1e-15 EndZ=0
  constraints (5):
    c: Diameter(g0) = 5
    c: DistanceX(g0,g-3) = 6.3
    c: Coincident(g1,g0)
    c: Horizontal(g1)
    c: Symmetric(g-5,g-5,g1)
FEATURE [PartDesign::Pocket] Pocket025
  BaseFeature = -> Pocket024
  Length = 5
  Length2 = 100
  Placement = pos=(0,0,0) rot=(0.57735,0.57735,0.57735;2.0944rad)
  Profile = -> Sketch076
  Type = 2
FEATURE [Sketcher::SketchObject] Sketch077
  ExternalGeometry = -> [Pocket025]
  FullyConstrained = true
  MapMode = 5
  Placement = pos=(6.5,-1.4e-15,1.5e-15) rot=(0.57735,0.57735,0.57735;2.0944rad)
  Support = -> [Pocket025]
  sketch-geometry (6):
    g0: LineSegment StartX=-24.6 StartY=-13.7 StartZ=0 EndX=-24.6 EndY=-11.3 EndZ=0
    g1: LineSegment StartX=-24.6 StartY=-11.3 StartZ=0 EndX=-14.2 EndY=-11.3 EndZ=0
    g2: LineSegment StartX=-14.2 StartY=-11.3 StartZ=0 EndX=-14.2 EndY=-13.7 EndZ=0
    g3: LineSegment StartX=-14.2 StartY=-13.7 StartZ=0 EndX=-24.6 EndY=-13.7 EndZ=0
    g4: GeomPoint X=-19.4 Y=-12.5 Z=0
    g5: LineSegment StartX=-19.4 StartY=-12.5 StartZ=0 EndX=-27.5 EndY=-12.5 EndZ=0
  constraints (15):
    c: Coincident(g0,g1)
    c: Coincident(g1,g2)
    c: Coincident(g2,g3)
    c: Coincident(g3,g0)
    c: Horizontal(g1)
    c: Horizontal(g3)
    c: Vertical(g0)
    c: Vertical(g2)
    c: Symmetric(g1,g0,g4)
    c: DistanceX(g1,g1) = 10.4
    c: DistanceY(g2,g2) = 2.4
    c: DistanceX(g2,g-4) = 1.9
    c: Coincident(g5,g4)
    c: Horizontal(g5)
    c: Symmetric(g-5,g-5,g5)
FEATURE [PartDesign::Pocket] Pocket026
  BaseFeature = -> Pocket025
  Length = 0.4
  Length2 = 100
  Placement = pos=(0,0,0) rot=(0.57735,0.57735,0.57735;2.0944rad)
  Profile = -> Sketch077
  Type = 0
FEATURE [PartDesign::Mirrored] Mirrored002
  BaseFeature = -> Pocket026
  MirrorPlane = -> Sketch075 [V_Axis]
  Originals = -> [Pocket024,Pocket025,Pocket026]
  Placement = pos=(0,0,0) rot=(0.57735,0.57735,0.57735;2.0944rad)
FEATURE [Sketcher::SketchObject] Sketch078
  ExternalGeometry = -> [Mirrored002]
  FullyConstrained = true
  MapMode = 5
  Placement = pos=(0,0,0) rot=(1,0,0;1.5708rad)
  Support = -> [XZ_Plane093]
  sketch-geometry (9):
    g0: GeomPoint X=-6.5 Y=13.5 Z=0
    g1: LineSegment StartX=6.5 StartY=-10 StartZ=0 EndX=6.5 EndY=13.5 EndZ=0
    g2: LineSegment StartX=6.5 StartY=13.5 StartZ=0 EndX=4.75 EndY=13.5 EndZ=0
    g3: LineSegment StartX=-6.5 StartY=13.5 StartZ=0 EndX=-4.75 EndY=13.5 EndZ=0
    g4: LineSegment StartX=-6.5 StartY=-10 StartZ=0 EndX=-6.5 EndY=13.5 EndZ=0
    g5: LineSegment StartX=6.5 StartY=-10 StartZ=0 EndX=4.75 EndY=-1 EndZ=0
    g6: LineSegment StartX=4.75 StartY=-1 StartZ=0 EndX=4.75 EndY=13.5 EndZ=0
    g7: LineSegment StartX=-4.75 StartY=13.5 StartZ=0 EndX=-4.75 EndY=-1 EndZ=0
    g8: LineSegment StartX=-4.75 StartY=-1 StartZ=0 EndX=-6.5 EndY=-10 EndZ=0
  constraints (24):
    c: Vertical(g0,g-4)
    c: Horizontal(g-3,g0)
    c: Coincident(g1,g-3)
    c: Coincident(g1,g2)
    c: Horizontal(g2)
    c: Coincident(g3,g0)
    c: Horizontal(g3)
    c: Coincident(g4,g3)
    c: Vertical(g4,g-4)
    c: DistanceX(g3,g2) = 9.5
    c: Equal(g2,g3)
    c: Horizontal(g1,g4)
    c: Coincident(g1,g-5)
    c: Coincident(g1,g5)
    c: Coincident(g5,g6)
    c: Coincident(g6,g2)
    c: Vertical(g6)
    c: DistanceY(g1,g5) = 9
    c: Coincident(g3,g7)
    c: Vertical(g7)
    c: Coincident(g7,g8)
    c: Coincident(g8,g4)
    c: Horizontal(g7,g5)
    c: DistanceX(g2,g2) = 1.75
FEATURE [PartDesign::Pocket] Pocket027
  BaseFeature = -> Mirrored002
  Length = 15
  Length2 = 15
  Placement = pos=(0,0,0) rot=(0.57735,0.57735,0.57735;2.0944rad)
  Profile = -> Sketch078
  Type = 4
FEATURE [Sketcher::SketchObject] Sketch079
  FullyConstrained = true
  MapMode = 5
  Placement = pos=(-6.5,1.4e-15,-1.5e-15) rot=(0.57735,0.57735,-0.57735;4.18879rad)
  Support = -> [Pocket027]
  sketch-geometry (1):
    g0: Circle CenterX=0 CenterY=0 CenterZ=0 NormalX=0 NormalY=0 NormalZ=1 AngleXU=0 Radius=12.2
  constraints (2):
    c: Coincident(g0,g-1)
    c: Diameter(g0) = 24.4
FEATURE [PartDesign::Pocket] Pocket028
  BaseFeature = -> Pocket027
  Length = 2.75
  Length2 = 100
  Placement = pos=(0,0,0) rot=(0.57735,0.57735,0.57735;2.0944rad)
  Profile = -> Sketch079
  Type = 0
FEATURE [Sketcher::SketchObject] Sketch080
  FullyConstrained = true
  MapMode = 5
  Placement = pos=(6.5,-1.4e-15,1.5e-15) rot=(0.57735,0.57735,0.57735;2.0944rad)
  Support = -> [Pocket028]
  sketch-geometry (1):
    g0: Circle CenterX=0 CenterY=0 CenterZ=0 NormalX=0 NormalY=0 NormalZ=1 AngleXU=0 Radius=12.1
  constraints (2):
    c: Coincident(g0,g-1)
    c: Diameter(g0) = 24.2
FEATURE [PartDesign::Pocket] Pocket029
  BaseFeature = -> Pocket028
  Length = 2.75
  Length2 = 100
  Placement = pos=(0,0,0) rot=(0.57735,0.57735,0.57735;2.0944rad)
  Profile = -> Sketch080
  Type = 0
FEATURE [Sketcher::SketchObject] Sketch081
  ExternalGeometry = -> [Pocket029]
  FullyConstrained = true
  MapMode = 5
  Placement = pos=(6.5,-1.4e-15,1.5e-15) rot=(0.57735,0.57735,0.57735;2.0944rad)
  Support = -> [Pocket029]
  sketch-geometry (6):
    g0: ArcOfCircle CenterX=0 CenterY=0 CenterZ=0 NormalX=0 NormalY=0 NormalZ=1 AngleXU=0 Radius=13.5 StartAngle=3.79664 EndAngle=5.62814
    g1: LineSegment StartX=-11.8698 StartY=-8.57666 StartZ=0 EndX=-12.3 EndY=-15 EndZ=0
    g2: LineSegment StartX=-12.3 StartY=-15 StartZ=0 EndX=12.3 EndY=-15 EndZ=0
    g3: LineSegment StartX=12.3 StartY=-15 StartZ=0 EndX=11.8698 EndY=-8.57666 EndZ=0
    g4: ArcOfCircle CenterX=11.2212 CenterY=-8.6201 CenterZ=0 NormalX=0 NormalY=0 NormalZ=1 AngleXU=0 Radius=0.65 StartAngle=0.0668757 EndAngle=2.48655
    g5: ArcOfCircle CenterX=-11.2212 CenterY=-8.6201 CenterZ=0 NormalX=0 NormalY=0 NormalZ=1 AngleXU=0 Radius=0.65 StartAngle=0.655044 EndAngle=3.07472
  constraints (14):
    c: Coincident(g0,g-1)
    c: Diameter(g0) = 27
    c: Coincident(g1,g2)
    c: Coincident(g2,g3)
    c: Coincident(g1,g-3)
    c: Coincident(g2,g-4)
    c: Tangent(g3,g4) = -1.5708
    c: Tangent(g0,g4) = 1.5708
    c: Tangent(g0,g5) = 1.5708
    c: Tangent(g1,g5) = -1.5708
    c: Equal(g4,g5)
    c: Horizontal(g4,g5)
    c: Parallel(g-4,g3)
    c: Radius(g4) = 0.65
FEATURE [PartDesign::Pocket] Pocket030
  BaseFeature = -> Pocket029
  Length = 5.25
  Length2 = 100
  Placement = pos=(0,0,0) rot=(0.57735,0.57735,0.57735;2.0944rad)
  Profile = -> Sketch081
  Type = 0
FEATURE [Sketcher::SketchObject] Sketch082
  ExternalGeometry = -> [Pocket030]
  FullyConstrained = true
  MapMode = 5
  Placement = pos=(-6.5,1.4e-15,-1.5e-15) rot=(0.57735,0.57735,-0.57735;4.18879rad)
  Support = -> [Pocket030]
  sketch-geometry (6):
    g0: ArcOfCircle CenterX=0 CenterY=0 CenterZ=0 NormalX=0 NormalY=0 NormalZ=1 AngleXU=0 Radius=13.5 StartAngle=0.655044 EndAngle=2.48655
    g1: LineSegment StartX=11.8698 StartY=8.57666 StartZ=0 EndX=12.3 EndY=15 EndZ=0
    g2: LineSegment StartX=12.3 StartY=15 StartZ=0 EndX=-12.3 EndY=15 EndZ=0
    g3: LineSegment StartX=-12.3 StartY=15 StartZ=0 EndX=-11.8698 EndY=8.57666 EndZ=0
    g4: ArcOfCircle CenterX=-11.2212 CenterY=8.6201 CenterZ=0 NormalX=0 NormalY=0 NormalZ=1 AngleXU=0 Radius=0.65 StartAngle=3.20847 EndAngle=5.62814
    g5: ArcOfCircle CenterX=11.2212 CenterY=8.6201 CenterZ=0 NormalX=0 NormalY=0 NormalZ=1 AngleXU=0 Radius=0.65 StartAngle=3.79664 EndAngle=6.21631
  constraints (14):
    c: Coincident(g0,g-1)
    c: Radius(g0) = 13.5
    c: Coincident(g1,g2)
    c: Coincident(g2,g-3)
    c: Coincident(g2,g3)
    c: Coincident(g-4,g1)
    c: Tangent(g3,g4) = -1.5708
    c: Tangent(g0,g4) = 1.5708
    c: Tangent(g0,g5) = 1.5708
    c: Tangent(g1,g5) = -1.5708
    c: Equal(g4,g5)
    c: Radius(g4) = 0.65
    c: Parallel(g-4,g1)
    c: Parallel(g3,g-3)
FEATURE [PartDesign::Pocket] Pocket031
  BaseFeature = -> Pocket030
  Length = 5.25
  Length2 = 100
  Placement = pos=(0,0,0) rot=(0.57735,0.57735,0.57735;2.0944rad)
  Profile = -> Sketch082
  Type = 0
FEATURE [PartDesign::Chamfer] Chamfer002
  Angle = 45
  Base = -> Pocket031 [Edge159,Edge155,Edge22,Edge27]
  BaseFeature = -> Pocket031
  ChamferType = 0
  FlipDirection = false
  Placement = pos=(0,0,0) rot=(0.57735,0.57735,0.57735;2.0944rad)
  Size = 2
  Size2 = 1
  SupportTransform = false
FEATURE [Sketcher::SketchObject] Sketch083
  ExternalGeometry = -> [Chamfer002]
  FullyConstrained = true
  MapMode = 5
  Placement = pos=(-3.75,5e-15,-2.7e-15) rot=(-0.57735,-0.57735,0.57735;2.0944rad)
  Support = -> [Chamfer002]
  sketch-geometry (13):
    g0: ArcOfCircle CenterX=-6.9e-15 CenterY=-3.7e-15 CenterZ=0 NormalX=0 NormalY=0 NormalZ=1 AngleXU=0 Radius=11 StartAngle=5.75419 EndAngle=6.81218
    g1: ArcOfCircle CenterX=-6.9e-15 CenterY=-3.7e-15 CenterZ=0 NormalX=0 NormalY=0 NormalZ=1 AngleXU=0 Radius=12.2 StartAngle=5.94045 EndAngle=6.62592
    g2: ArcOfCircle CenterX=-6.9e-15 CenterY=-3.7e-15 CenterZ=0 NormalX=0 NormalY=0 NormalZ=1 AngleXU=0 Radius=11 StartAngle=2.6126 EndAngle=3.67059
    g3: ArcOfCircle CenterX=-6.9e-15 CenterY=-3.7e-15 CenterZ=0 NormalX=0 NormalY=0 NormalZ=1 AngleXU=0 Radius=12.2 StartAngle=2.79886 EndAngle=3.48433
    g4: Ellipse CenterX=-6.9e-15 CenterY=-3.7e-15 CenterZ=0 NormalX=0 NormalY=0 NormalZ=1 MajorRadius=13.5 MinorRadius=7.81051 AngleXU=-3e-16
    g5: LineSegment StartX=13.5 StartY=-7.4e-15 StartZ=0 EndX=-13.5 EndY=0 EndZ=0
    g6: LineSegment StartX=-4.8e-15 StartY=7.81051 StartZ=0 EndX=-9.1e-15 EndY=-7.81051 EndZ=0
    g7: GeomPoint X=11.0112 Y=-6.8e-15 Z=0
    g8: GeomPoint X=-11.0112 Y=-7e-16 Z=0
    g9: LineSegment StartX=-11.4904 StartY=4.1 StartZ=0 EndX=-9.49645 EndY=5.55135 EndZ=0
    g10: LineSegment StartX=-11.4904 StartY=-4.1 StartZ=0 EndX=-9.49645 EndY=-5.55135 EndZ=0
    g11: LineSegment StartX=9.49645 StartY=-5.55135 StartZ=0 EndX=11.4904 EndY=-4.1 EndZ=0
    g12: LineSegment StartX=11.4904 StartY=4.1 StartZ=0 EndX=9.49645 EndY=5.55135 EndZ=0
  constraints (29):
    c: Coincident(g0,g-4)
    c: PointOnObject(g0,g-4)
    c: Coincident(g1,g0)
    c: PointOnObject(g1,g-3)
    c: Coincident(g2,g0)
    c: PointOnObject(g2,g-4)
    c: Coincident(g3,g0)
    c: PointOnObject(g3,g-3)
    c: InternalAlignment(g5-g8 -> g4) x4
    c: Coincident(g4,g0)
    c: PointOnObject(g3,g4)
    c: PointOnObject(g2,g4)
    c: PointOnObject(g3,g4)
    c: PointOnObject(g2,g4)
    c: PointOnObject(g0,g4)
    c: PointOnObject(g1,g4)
    c: PointOnObject(g1,g4)
    c: PointOnObject(g0,g4)
    c: PointOnObject(g5,g-1)
    c: DistanceX(g5,g5) = 27
    c: DistanceY(g3,g3) = 8.2
    c: Coincident(g9,g3)
    c: Coincident(g9,g2)
    c: Coincident(g10,g3)
    c: Coincident(g10,g2)
    c: Coincident(g11,g0)
    c: Coincident(g11,g1)
    c: Coincident(g12,g1)
    c: Coincident(g12,g0)
FEATURE [PartDesign::Pocket] Pocket032
  BaseFeature = -> Chamfer002
  Length = 5
  Length2 = 100
  Placement = pos=(0,0,0) rot=(0.57735,0.57735,0.57735;2.0944rad)
  Profile = -> Sketch083
  Type = 0
FEATURE [PartDesign::Body] Body079  label="Metal case002"
  Group = -> [Sketch074,Pad019,Sketch075,Pocket024,Sketch076,Pocket025,Sketch077,Pocket026,Mirrored002,Sketch078,Pocket027,Sketch079,Pocket028,Sketch080,Pocket029,Sketch081,Pocket030,Sketch082,Pocket031,Chamfer002,Sketch083,Pocket032]
  Origin = -> Origin095
  Tip = -> Pocket032
FEATURE [App::DocumentObjectGroup] Group020  label="Case002"
  Group = -> [Body079]
FEATURE [App::Part] Part016  label="KP08-003"
  Group = -> [Group014,Body060,Body059,Body064,Body061,Body065,Body063,Body062,Group015,Body067,Body066,Group016,Body072,Body071,Body074,Body070,Body073,Body069,Body068,Group017,Body078,Body077,Group018,Body075,Body076,Group019,Body058,Group020,Body079]
  Origin = -> Origin096
  Placement = pos=(332,120,105) rot=(0,0,1;3.14159rad)
FEATURE [Sketcher::SketchObject] Sketch084
  FullyConstrained = true
  MapMode = 5
  Placement = pos=(0,0,0) rot=(-0.57735,0.57735,0.57735;4.18879rad)
  Support = -> [YZ_Plane102]
  sketch-geometry (1):
    g0: Circle CenterX=0 CenterY=-7.5 CenterZ=0 NormalX=0 NormalY=0 NormalZ=1 AngleXU=0 Radius=0.25
  constraints (3):
    c: PointOnObject(g0,g-2)
    c: DistanceY(g0) = -7.5
    c: Diameter(g0) = 0.5
FEATURE [Sketcher::SketchObject] Sketch085
  FullyConstrained = true
  MapMode = 5
  Support = -> [XY_Plane095]
  sketch-geometry (2):
    g0: LineSegment StartX=0 StartY=5.5 StartZ=0 EndX=6e-16 EndY=9.5 EndZ=0
    g1: ArcOfCircle CenterX=0 CenterY=7.5 CenterZ=0 NormalX=0 NormalY=0 NormalZ=1 AngleXU=0 Radius=2 StartAngle=4.71239 EndAngle=7.85398
  constraints (7):
    c: PointOnObject(g0,g-2)
    c: PointOnObject(g0,g-2)
    c: PointOnObject(g1,g0)
    c: Coincident(g1,g0)
    c: Coincident(g1,g0)
    c: Radius(g1) = 2
    c: DistanceY(g1) = 7.5
FEATURE [PartDesign::Revolution] Revolution025
  Angle = 360
  Axis = (0,1,0)
  Base = (0,0,0)
  Profile = -> Sketch085
  ReferenceAxis = -> Sketch085 [V_Axis]
  Reversed = true
FEATURE [PartDesign::Body] Body081  label="Ball 022"
  Group = -> [Sketch085,Revolution025]
  Origin = -> Origin098
  Tip = -> Revolution025
FEATURE [PartDesign::FeatureBase] Clone042
  BaseFeature = -> Body081
FEATURE [PartDesign::Body] Body082  label="Ball 023"
  BaseFeature = -> Body081
  Group = -> [Clone042]
  Origin = -> Origin099
  Placement = pos=(0,0,0) rot=(-1,0,0;0.897598rad)
  Tip = -> Clone042
FEATURE [PartDesign::FeatureBase] Clone043
  BaseFeature = -> Body081
FEATURE [PartDesign::Body] Body083  label="Ball 024"
  BaseFeature = -> Body081
  Group = -> [Clone043]
  Origin = -> Origin100
  Placement = pos=(0,0,0) rot=(-1,0,0;1.7952rad)
  Tip = -> Clone043
FEATURE [PartDesign::FeatureBase] Clone044
  BaseFeature = -> Body081
FEATURE [PartDesign::Body] Body084  label="Ball 025"
  BaseFeature = -> Body081
  Group = -> [Clone044]
  Origin = -> Origin101
  Placement = pos=(0,0,0) rot=(1,0,0;3.59039rad)
  Tip = -> Clone044
FEATURE [PartDesign::FeatureBase] Clone045
  BaseFeature = -> Body081
FEATURE [PartDesign::Body] Body085  label="Ball 026"
  BaseFeature = -> Body081
  Group = -> [Clone045]
  Origin = -> Origin102
  Placement = pos=(0,0,0) rot=(1,0,0;2.69279rad)
  Tip = -> Clone045
FEATURE [PartDesign::FeatureBase] Clone046
  BaseFeature = -> Body081
FEATURE [PartDesign::Body] Body086  label="Ball 027"
  BaseFeature = -> Body081
  Group = -> [Clone046]
  Origin = -> Origin103
  Placement = pos=(0,0,0) rot=(1,0,0;1.7952rad)
  Tip = -> Clone046
FEATURE [PartDesign::FeatureBase] Clone047
  BaseFeature = -> Body081
FEATURE [PartDesign::Body] Body087  label="Ball 028"
  BaseFeature = -> Body081
  Group = -> [Clone047]
  Origin = -> Origin104
  Placement = pos=(0,0,0) rot=(1,0,0;0.897598rad)
  Tip = -> Clone047
FEATURE [App::DocumentObjectGroup] Group021  label="Balls003"
  Group = -> [Body081,Body082,Body083,Body084,Body085,Body086,Body087]
FEATURE [Sketcher::SketchObject] Sketch086
  FullyConstrained = true
  MapMode = 5
  Support = -> [XY_Plane104]
  sketch-geometry (7):
    g0: LineSegment StartX=-5 StartY=7.5 StartZ=0 EndX=5 EndY=7.5 EndZ=0
    g1: LineSegment StartX=-0.210977 StartY=7.5 StartZ=0 EndX=0.210977 EndY=7.5 EndZ=0
    g2: ArcOfCircle CenterX=0.25 CenterY=7.5 CenterZ=0 NormalX=0 NormalY=0 NormalZ=1 AngleXU=0 Radius=0.460977 StartAngle=2.43297 EndAngle=3.14159
    g3: ArcOfCircle CenterX=-0.25 CenterY=7.5 CenterZ=0 NormalX=0 NormalY=0 NormalZ=1 AngleXU=0 Radius=0.460977 StartAngle=9.792e-13 EndAngle=0.708626
    g4: LineSegment StartX=-0.1 StartY=7.8 StartZ=0 EndX=-0.1 EndY=7.75 EndZ=0
    g5: LineSegment StartX=-0.1 StartY=7.75 StartZ=0 EndX=0.1 EndY=7.75 EndZ=0
    g6: LineSegment StartX=0.1 StartY=7.75 StartZ=0 EndX=0.1 EndY=7.8 EndZ=0
  constraints (22):
    c: DistanceY(g-1,g0) = 7.5
    c: Symmetric(g0,g0,g-2)
    c: DistanceX(g0,g0) = 10
    c: PointOnObject(g1,g0)
    c: PointOnObject(g1,g0)
    c: Coincident(g3,g1)
    c: Coincident(g2,g1)
    c: Coincident(g2,g4)
    c: Coincident(g4,g5)
    c: Horizontal(g5)
    c: Coincident(g5,g6)
    c: Coincident(g6,g3)
    c: Vertical(g6)
    c: Equal(g3,g2)
    c: Vertical(g4)
    c: Symmetric(g2,g3,g-2)
    c: DistanceX(g5,g5) = 0.2
    c: Distance(g5,g1) = 0.25
    c: DistanceX(g3,g-1) = 0.25
    c: PointOnObject(g3,g1)
    c: PointOnObject(g2,g1)
    c: Distance(g3,g1) = 0.3
FEATURE [PartDesign::Revolution] Revolution026
  Angle = 360
  Axis = (10,0,0)
  Base = (-5,7.5,0)
  Profile = -> Sketch086
  ReferenceAxis = -> Sketch086 [Axis]
FEATURE [PartDesign::Body] Body090  label="Rivet 022"
  Group = -> [Sketch086,Revolution026]
  Origin = -> Origin107
  Placement = pos=(0,0,0) rot=(1,0,0;0.448799rad)
  Tip = -> Revolution026
FEATURE [PartDesign::FeatureBase] Clone049
  BaseFeature = -> Body090
  Placement = pos=(0,0,0) rot=(1,0,0;0.448799rad)
FEATURE [PartDesign::Body] Body091  label="Rivet 023"
  BaseFeature = -> Body090
  Group = -> [Clone049]
  Origin = -> Origin108
  Placement = pos=(0,0,0) rot=(1,0,0;0.897598rad)
  Tip = -> Clone049
FEATURE [PartDesign::FeatureBase] Clone050
  BaseFeature = -> Body090
  Placement = pos=(0,0,0) rot=(1,0,0;0.448799rad)
FEATURE [PartDesign::Body] Body092  label="Rivet 024"
  BaseFeature = -> Body090
  Group = -> [Clone050]
  Origin = -> Origin109
  Placement = pos=(0,0,0) rot=(1,0,0;1.7952rad)
  Tip = -> Clone050
FEATURE [PartDesign::FeatureBase] Clone051
  BaseFeature = -> Body090
  Placement = pos=(0,0,0) rot=(1,0,0;0.448799rad)
FEATURE [PartDesign::Body] Body093  label="Rivet 025"
  BaseFeature = -> Body090
  Group = -> [Clone051]
  Origin = -> Origin110
  Placement = pos=(0,0,0) rot=(1,0,0;2.69279rad)
  Tip = -> Clone051
FEATURE [PartDesign::FeatureBase] Clone052
  BaseFeature = -> Body090
  Placement = pos=(0,0,0) rot=(1,0,0;0.448799rad)
FEATURE [PartDesign::Body] Body094  label="Rivet 026"
  BaseFeature = -> Body090
  Group = -> [Clone052]
  Origin = -> Origin111
  Placement = pos=(0,0,0) rot=(1,0,0;3.59039rad)
  Tip = -> Clone052
FEATURE [PartDesign::FeatureBase] Clone053
  BaseFeature = -> Body090
  Placement = pos=(0,0,0) rot=(1,0,0;0.448799rad)
FEATURE [PartDesign::Body] Body095  label="Rivet 027"
  BaseFeature = -> Body090
  Group = -> [Clone053]
  Origin = -> Origin112
  Placement = pos=(0,0,0) rot=(-1,0,0;1.7952rad)
  Tip = -> Clone053
FEATURE [PartDesign::FeatureBase] Clone054
  BaseFeature = -> Body090
  Placement = pos=(0,0,0) rot=(1,0,0;0.448799rad)
FEATURE [PartDesign::Body] Body096  label="Rivet 028"
  BaseFeature = -> Body090
  Group = -> [Clone054]
  Origin = -> Origin113
  Placement = pos=(0,0,0) rot=(-1,0,0;0.897598rad)
  Tip = -> Clone054
FEATURE [App::DocumentObjectGroup] Group023  label="Rivets003"
  Group = -> [Body090,Body091,Body092,Body093,Body094,Body095,Body096]
FEATURE [Sketcher::SketchObject] Sketch087
  FullyConstrained = true
  MapMode = 5
  Placement = pos=(0,0,0) rot=(1,0,0;1.5708rad)
  Support = -> [XZ_Plane102]
  sketch-geometry (4):
    g0: LineSegment StartX=0 StartY=8.5 StartZ=0 EndX=0.1 EndY=8.5 EndZ=0
    g1: LineSegment StartX=0.1 StartY=8.5 StartZ=0 EndX=0.1 EndY=6.5 EndZ=0
    g2: LineSegment StartX=0.1 StartY=6.5 StartZ=0 EndX=0 EndY=6.5 EndZ=0
    g3: LineSegment StartX=0 StartY=6.5 StartZ=0 EndX=0 EndY=8.5 EndZ=0
  constraints (12):
    c: Coincident(g0,g1)
    c: Coincident(g1,g2)
    c: Coincident(g2,g3)
    c: Coincident(g3,g0)
    c: Horizontal(g0)
    c: Horizontal(g2)
    c: Vertical(g1)
    c: Vertical(g3)
    c: PointOnObject(g0,g-2)
    c: DistanceX(g0,g0) = 0.1
    c: DistanceY(g0) = 8.5
    c: DistanceY(g1) = 6.5
FEATURE [PartDesign::Revolution] Revolution027
  Angle = 360
  Axis = (1,0,0)
  Base = (0,0,0)
  Placement = pos=(0,0,0) rot=(1,0,0;1.5708rad)
  Profile = -> Sketch087
  ReferenceAxis = -> Sketch087 [H_Axis]
FEATURE [Sketcher::SketchObject] Sketch088
  FullyConstrained = true
  MapMode = 5
  Placement = pos=(0,0,0) rot=(0.57735,0.57735,0.57735;2.0944rad)
  Support = -> [YZ_Plane102]
  sketch-geometry (5):
    g0: ArcOfCircle CenterX=0 CenterY=7.5 CenterZ=0 NormalX=0 NormalY=0 NormalZ=1 AngleXU=0 Radius=2.11 StartAngle=5.66076 EndAngle=6.65667
    g1: LineSegment StartX=5e-16 StartY=8.5 StartZ=0 EndX=0 EndY=6.26986 EndZ=0
    g2: ArcOfCircle CenterX=0 CenterY=0 CenterZ=0 NormalX=0 NormalY=0 NormalZ=1 AngleXU=0 Radius=6.5 StartAngle=1.3039 EndAngle=1.5708
    g3: LineSegment StartX=1.71431 StartY=6.26986 StartZ=0 EndX=0 EndY=6.26986 EndZ=0
    g4: ArcOfCircle CenterX=0 CenterY=0 CenterZ=0 NormalX=0 NormalY=0 NormalZ=1 AngleXU=0 Radius=8.5 StartAngle=1.33757 EndAngle=1.5708
  constraints (16):
    c: PointOnObject(g0,g-2)
    c: DistanceY(g0) = 7.5
    c: Radius(g0) = 2.11
    c: PointOnObject(g2,g1)
    c: DistanceY(g2) = 6.5
    c: Coincident(g2,g-1)
    c: Coincident(g3,g2)
    c: Horizontal(g3)
    c: Coincident(g0,g2)
    c: Coincident(g1,g3)
    c: PointOnObject(g1,g-2)
    c: PointOnObject(g1,g-2)
    c: Coincident(g4,g-1)
    c: Coincident(g4,g1)
    c: DistanceY(g1) = 8.5
    c: Coincident(g0,g4)
FEATURE [PartDesign::Revolution] Revolution028
  Angle = 180
  Axis = (-2e-16,3e-16,1)
  Base = (0,0,0)
  BaseFeature = -> Revolution027
  Placement = pos=(0,0,0) rot=(1,0,0;1.5708rad)
  Profile = -> Sketch088
  ReferenceAxis = -> Sketch088 [V_Axis]
  Reversed = true
FEATURE [PartDesign::PolarPattern] PolarPattern012
  Angle = 360
  Axis = -> Sketch088 [N_Axis]
  BaseFeature = -> Revolution028
  Occurrences = 3
  Originals = -> [Revolution028]
  Placement = pos=(0,0,0) rot=(1,0,0;1.5708rad)
  Refine = true
FEATURE [Sketcher::SketchObject] Sketch089
  FullyConstrained = true
  MapMode = 5
  Placement = pos=(0,0,0) rot=(0.57735,0.57735,0.57735;2.0944rad)
  Support = -> [YZ_Plane102]
  sketch-geometry (4):
    g0: ArcOfCircle CenterX=0 CenterY=7.5 CenterZ=0 NormalX=0 NormalY=0 NormalZ=1 AngleXU=0 Radius=2.01 StartAngle=5.57985 EndAngle=6.86228
    g1: LineSegment StartX=0 StartY=6.2 StartZ=0 EndX=1.533 EndY=6.2 EndZ=0
    g2: LineSegment StartX=0 StartY=8.6 StartZ=0 EndX=0 EndY=6.2 EndZ=0
    g3: LineSegment StartX=0 StartY=8.6 StartZ=0 EndX=1.68229 EndY=8.6 EndZ=0
  constraints (13):
    c: PointOnObject(g0,g-2)
    c: DistanceY(g0) = 7.5
    c: Radius(g0) = 2.01
    c: PointOnObject(g1,g-2)
    c: Horizontal(g1)
    c: Coincident(g0,g1)
    c: DistanceY(g1) = 6.2
    c: DistanceY(g2) = 8.6
    c: Coincident(g2,g1)
    c: PointOnObject(g2,g-2)
    c: Coincident(g3,g2)
    c: Horizontal(g3)
    c: Coincident(g0,g3)
FEATURE [PartDesign::Groove] Groove003
  Angle = 360
  Axis = (-2e-16,3e-16,1)
  Base = (0,0,0)
  BaseFeature = -> PolarPattern012
  Placement = pos=(0,0,0) rot=(1,0,0;1.5708rad)
  Profile = -> Sketch089
  ReferenceAxis = -> Sketch089 [V_Axis]
FEATURE [PartDesign::PolarPattern] PolarPattern013
  Angle = 360
  Axis = -> Sketch089 [N_Axis]
  BaseFeature = -> Groove003
  Occurrences = 3
  Originals = -> [Groove003]
  Placement = pos=(0,0,0) rot=(1,0,0;1.5708rad)
FEATURE [PartDesign::Pocket] Pocket033
  BaseFeature = -> PolarPattern013
  Length = 5
  Length2 = 100
  Placement = pos=(0,0,0) rot=(1,0,0;1.5708rad)
  Profile = -> Sketch084
  Type = 1
FEATURE [PartDesign::PolarPattern] PolarPattern014
  Angle = 360
  Axis = -> Sketch084 [N_Axis]
  BaseFeature = -> Pocket033
  Occurrences = 3
  Originals = -> [Pocket033]
  Placement = pos=(0,0,0) rot=(1,0,0;1.5708rad)
FEATURE [PartDesign::Body] Body088  label="Cage 007"
  Group = -> [Sketch087,Revolution027,Sketch088,Revolution028,PolarPattern012,Sketch089,Groove003,PolarPattern013,Sketch084,Pocket033,PolarPattern014]
  Origin = -> Origin105
  Placement = pos=(0,0,0) rot=(-1,0,0;1.5708rad)
  Tip = -> PolarPattern014
FEATURE [PartDesign::FeatureBase] Clone048
  BaseFeature = -> Body088
  Placement = pos=(0,0,0) rot=(-1,0,0;1.5708rad)
FEATURE [PartDesign::Body] Body089  label="Cage 008"
  BaseFeature = -> Body088
  Group = -> [Clone048]
  Origin = -> Origin106
  Placement = pos=(0,0,0) rot=(0,1,0;3.14159rad)
  Tip = -> Clone048
FEATURE [App::DocumentObjectGroup] Group022  label="Cages003"
  Group = -> [Body088,Body089]
FEATURE [Sketcher::SketchObject] Sketch090
  FullyConstrained = true
  MapMode = 5
  Support = -> [XY_Plane111]
  sketch-geometry (14):
    g0: ArcOfCircle CenterX=-1e-16 CenterY=7.5 CenterZ=0 NormalX=0 NormalY=0 NormalZ=1 AngleXU=0 Radius=2 StartAngle=0.848062 EndAngle=2.29353
    g1: LineSegment StartX=-3.5 StartY=11 StartZ=0 EndX=3.5 EndY=11 EndZ=0
    g2: LineSegment StartX=3.5 StartY=11 StartZ=0 EndX=3.5 EndY=9.2 EndZ=0
    g3: LineSegment StartX=2.9 StartY=9 StartZ=0 EndX=1.32288 EndY=9 EndZ=0
    g4: LineSegment StartX=-3.5 StartY=9.2 StartZ=0 EndX=-3.5 EndY=11 EndZ=0
    g5: LineSegment StartX=-1.32288 StartY=9 StartZ=0 EndX=-2.9 EndY=9 EndZ=0
    g6: LineSegment StartX=2.9 StartY=9 StartZ=0 EndX=2.9 EndY=9.5 EndZ=0
    g7: LineSegment StartX=2.9 StartY=9.5 StartZ=0 EndX=3.2 EndY=9.5 EndZ=0
    g8: LineSegment StartX=3.2 StartY=9.5 StartZ=0 EndX=3.2 EndY=9.2 EndZ=0
    g9: LineSegment StartX=3.2 StartY=9.2 StartZ=0 EndX=3.5 EndY=9.2 EndZ=0
    g10: LineSegment StartX=-3.5 StartY=9.2 StartZ=0 EndX=-3.2 EndY=9.2 EndZ=0
    g11: LineSegment StartX=-3.2 StartY=9.2 StartZ=0 EndX=-3.2 EndY=9.5 EndZ=0
    g12: LineSegment StartX=-3.2 StartY=9.5 StartZ=0 EndX=-2.9 EndY=9.5 EndZ=0
    g13: LineSegment StartX=-2.9 StartY=9.5 StartZ=0 EndX=-2.9 EndY=9 EndZ=0
  constraints (41):
    c: Coincident(g1,g2)
    c: Coincident(g4,g1)
    c: Horizontal(g3)
    c: Vertical(g2)
    c: Vertical(g4)
    c: Coincident(g0,g5)
    c: Coincident(g0,g3)
    c: DistanceY(g-1,g0) = 7.5
    c: Radius(g0) = 2
    c: Symmetric(g1,g1,g-2)
    c: Symmetric(g0,g0,g-2)
    c: DistanceY(g1) = 11
    c: DistanceX(g1,g1) = 7
    c: Vertical(g6)
    c: Coincident(g6,g7)
    c: Horizontal(g7)
    c: Coincident(g7,g8)
    c: Vertical(g8)
    c: Coincident(g8,g9)
    c: Coincident(g3,g6)
    c: Coincident(g2,g9)
    c: Horizontal(g10)
    c: Coincident(g10,g11)
    c: Coincident(g11,g12)
    c: Horizontal(g12)
    c: Coincident(g12,g13)
    c: Vertical(g13)
    c: Vertical(g11)
    c: Coincident(g4,g10)
    c: Coincident(g5,g13)
    c: DistanceY(g13,g13) = 0.5
    c: DistanceX(g12,g12) = 0.3
    c: DistanceY(g5,g10) = 0.2
    c: Symmetric(g5,g3,g-2)
    c: DistanceY(g3) = 9
    c: DistanceY(g6) = 9.5
    c: Equal(g7,g12)
    c: Equal(g13,g6)
    c: Horizontal(g9)
    c: Horizontal(g8,g10)
    c: Equal(g12,g10)
FEATURE [PartDesign::Revolution] Revolution029
  Angle = 360
  Axis = (1,0,0)
  Base = (0,0,0)
  Profile = -> Sketch090
  ReferenceAxis = -> X_Axis111
FEATURE [PartDesign::Fillet] Fillet163
  Base = -> Revolution029 [Edge14,Edge15]
  BaseFeature = -> Revolution029
  Radius = 0.3
  SupportTransform = false
FEATURE [PartDesign::Body] Body097  label="Outer Ring004"
  Group = -> [Sketch090,Revolution029,Fillet163]
  Origin = -> Origin114
  Tip = -> Fillet163
FEATURE [Sketcher::SketchObject] Sketch091
  FullyConstrained = true
  MapMode = 5
  Support = -> [XY_Plane112]
  sketch-geometry (14):
    g0: LineSegment StartX=-2.9 StartY=6 StartZ=0 EndX=-1.32288 EndY=6 EndZ=0
    g1: LineSegment StartX=-3.5 StartY=4 StartZ=0 EndX=-3.5 EndY=5.7 EndZ=0
    g2: ArcOfCircle CenterX=-1e-16 CenterY=7.5 CenterZ=0 NormalX=0 NormalY=0 NormalZ=1 AngleXU=0 Radius=2 StartAngle=3.98965 EndAngle=5.43512
    g3: LineSegment StartX=1.32288 StartY=6 StartZ=0 EndX=2.9 EndY=6 EndZ=0
    g4: LineSegment StartX=-3.5 StartY=5.7 StartZ=0 EndX=-3.2 EndY=5.7 EndZ=0
    g5: LineSegment StartX=-3.2 StartY=5.7 StartZ=0 EndX=-3.2 EndY=5.5 EndZ=0
    g6: LineSegment StartX=-3.2 StartY=5.5 StartZ=0 EndX=-2.9 EndY=5.5 EndZ=0
    g7: LineSegment StartX=-2.9 StartY=5.5 StartZ=0 EndX=-2.9 EndY=6 EndZ=0
    g8: LineSegment StartX=8.5 StartY=6 StartZ=0 EndX=3.2 EndY=6 EndZ=0
    g9: LineSegment StartX=3.2 StartY=6 StartZ=0 EndX=3.2 EndY=5.5 EndZ=0
    g10: LineSegment StartX=3.2 StartY=5.5 StartZ=0 EndX=2.9 EndY=5.5 EndZ=0
    g11: LineSegment StartX=2.9 StartY=5.5 StartZ=0 EndX=2.9 EndY=6 EndZ=0
    g12: LineSegment StartX=8.5 StartY=4 StartZ=0 EndX=8.5 EndY=6 EndZ=0
    g13: LineSegment StartX=-3.5 StartY=4 StartZ=0 EndX=8.5 EndY=4 EndZ=0
  constraints (43):
    c: Horizontal(g0)
    c: Vertical(g1)
    c: DistanceY(g1) = 4
    c: Coincident(g2,g0)
    c: Coincident(g2,g3)
    c: Horizontal(g3)
    c: Radius(g2) = 2
    c: DistanceY(g2) = 7.5
    c: Symmetric(g0,g2,g-2)
    c: Horizontal(g4)
    c: Coincident(g4,g5)
    c: Vertical(g5)
    c: Coincident(g5,g6)
    c: Horizontal(g6)
    c: Coincident(g6,g7)
    c: Vertical(g7)
    c: Horizontal(g8)
    c: Coincident(g8,g9)
    c: Vertical(g9)
    c: Coincident(g9,g10)
    c: Horizontal(g10)
    c: Coincident(g10,g11)
    c: Vertical(g11)
    c: Coincident(g3,g11)
    c: Coincident(g0,g7)
    c: Coincident(g1,g4)
    c: DistanceY(g3) = 6
    c: DistanceY(g6,g0) = 0.5
    c: DistanceX(g4,g4) = 0.3
    c: DistanceX(g6,g6) = 0.3
    c: DistanceY(g5,g4) = 0.2
    c: Vertical(g12)
    c: Equal(g11,g7)
    c: DistanceY(g1,g0) = 2
    c: DistanceX(g8,g8) = 5.3
    c: Coincident(g13,g1)
    c: Coincident(g13,g12)
    c: Horizontal(g13)
    c: DistanceX(g13,g13) = 12
    c: DistanceX(g1,g2) = 3.5
    c: Coincident(g8,g12)
    c: Equal(g7,g9)
    c: Equal(g6,g10)
FEATURE [PartDesign::Revolution] Revolution030
  Angle = 360
  Axis = (1,0,0)
  Base = (0,0,0)
  Profile = -> Sketch091
  ReferenceAxis = -> X_Axis112
FEATURE [PartDesign::Fillet] Fillet164
  Base = -> Revolution030 [Edge13,Edge11]
  BaseFeature = -> Revolution030
  Radius = 0.2
  SupportTransform = false
FEATURE [PartDesign::Body] Body098  label="Inner Ring004"
  Group = -> [Sketch091,Revolution030,Fillet164]
  Origin = -> Origin115
  Tip = -> Fillet164
FEATURE [App::DocumentObjectGroup] Group025  label="Rings003"
  Group = -> [Body097,Body098]
FEATURE [Sketcher::SketchObject] Sketch092
  FullyConstrained = true
  MapMode = 5
  Placement = pos=(0,0,0) rot=(1,0,0;1.5708rad)
  Support = -> [XZ_Plane113]
  sketch-geometry (12):
    g0: LineSegment StartX=2.9 StartY=9.5 StartZ=0 EndX=2.9 EndY=8.5 EndZ=0
    g1: LineSegment StartX=2.9 StartY=8.5 StartZ=0 EndX=3.2 EndY=8.5 EndZ=0
    g2: LineSegment StartX=3.2 StartY=8.5 StartZ=0 EndX=3.2 EndY=6.5 EndZ=0
    g3: LineSegment StartX=3.2 StartY=6.5 StartZ=0 EndX=2.9 EndY=6.5 EndZ=0
    g4: LineSegment StartX=2.9 StartY=6.5 StartZ=0 EndX=2.9 EndY=5.5 EndZ=0
    g5: LineSegment StartX=2.9 StartY=5.5 StartZ=0 EndX=3.2 EndY=5.5 EndZ=0
    g6: LineSegment StartX=3.2 StartY=5.5 StartZ=0 EndX=3.2 EndY=6 EndZ=0
    g7: LineSegment StartX=3.2 StartY=6 StartZ=0 EndX=3.5 EndY=6 EndZ=0
    g8: LineSegment StartX=3.5 StartY=6 StartZ=0 EndX=3.5 EndY=9 EndZ=0
    g9: LineSegment StartX=3.5 StartY=9 StartZ=0 EndX=3.2 EndY=9 EndZ=0
    g10: LineSegment StartX=3.2 StartY=9 StartZ=0 EndX=3.2 EndY=9.5 EndZ=0
    g11: LineSegment StartX=3.2 StartY=9.5 StartZ=0 EndX=2.9 EndY=9.5 EndZ=0
  constraints (36):
    c: Vertical(g0)
    c: Coincident(g0,g1)
    c: Horizontal(g1)
    c: Coincident(g1,g2)
    c: Vertical(g2)
    c: Coincident(g2,g3)
    c: Horizontal(g3)
    c: Coincident(g3,g4)
    c: Vertical(g4)
    c: Coincident(g4,g5)
    c: Horizontal(g5)
    c: Coincident(g5,g6)
    c: Vertical(g6)
    c: Coincident(g6,g7)
    c: Horizontal(g7)
    c: Coincident(g7,g8)
    c: Vertical(g8)
    c: Coincident(g8,g9)
    c: Horizontal(g9)
    c: Coincident(g9,g10)
    c: Vertical(g10)
    c: Coincident(g10,g11)
    c: Coincident(g11,g0)
    c: Horizontal(g11)
    c: DistanceY(g4) = 5.5
    c: DistanceX(g4) = 2.9
    c: DistanceY(g5,g6) = 0.5
    c: DistanceY(g6,g2) = 0.5
    c: DistanceX(g5,g5) = 0.3
    c: Equal(g5,g7)
    c: Equal(g7,g3)
    c: Equal(g3,g1)
    c: Equal(g1,g9)
    c: Equal(g4,g0)
    c: Equal(g6,g10)
    c: DistanceY(g4,g0) = 4
FEATURE [PartDesign::Revolution] Revolution031
  Angle = 360
  Axis = (1,0,0)
  Base = (0,0,0)
  Placement = pos=(0,0,0) rot=(1,0,0;1.5708rad)
  Profile = -> Sketch092
  ReferenceAxis = -> Sketch092 [H_Axis]
FEATURE [PartDesign::Fillet] Fillet165
  Base = -> Revolution031 [Edge14,Edge12]
  BaseFeature = -> Revolution031
  Placement = pos=(0,0,0) rot=(1,0,0;1.5708rad)
  Radius = 0.2
  SupportTransform = false
FEATURE [PartDesign::Body] Body099  label="Seal 007"
  Group = -> [Sketch092,Revolution031,Fillet165]
  Origin = -> Origin116
  Tip = -> Fillet165
FEATURE [PartDesign::FeatureBase] Clone055
  BaseFeature = -> Body099
FEATURE [PartDesign::Body] Body100  label="Seal 008"
  BaseFeature = -> Body099
  Group = -> [Clone055]
  Origin = -> Origin117
  Placement = pos=(0,0,0) rot=(0,1,0;3.14159rad)
  Tip = -> Clone055
FEATURE [App::DocumentObjectGroup] Group024  label="Seals003"
  Group = -> [Body099,Body100]
FEATURE [Sketcher::SketchObject] Sketch093
  AttachmentOffset = pos=(0,0,4) rot=(0,0,1;0rad)
  FullyConstrained = true
  MapMode = 5
  Placement = pos=(0,0,4) rot=(0,0,1;0rad)
  Support = -> [XY_Plane094]
  sketch-geometry (1):
    g0: Circle CenterX=6 CenterY=0 CenterZ=0 NormalX=0 NormalY=0 NormalZ=1 AngleXU=0 Radius=1.5
  constraints (3):
    c: PointOnObject(g0,g-1)
    c: Diameter(g0) = 3
    c: DistanceX(g-1,g0) = 6
FEATURE [PartDesign::Pad] Pad020
  Direction = (0,0,1)
  Length = 3
  Length2 = 100
  Profile = -> Sketch093
  Type = 0
FEATURE [Sketcher::SketchObject] Sketch094
  ExternalGeometry = -> [Pad020]
  FullyConstrained = true
  MapMode = 5
  Placement = pos=(0,0,7) rot=(0,0,1;0rad)
  Support = -> [Pad020]
  sketch-geometry (7):
    g0: LineSegment StartX=6.43301 StartY=-0.75 StartZ=0 EndX=6.86603 EndY=0 EndZ=0
    g1: LineSegment StartX=6.86603 StartY=0 StartZ=0 EndX=6.43301 EndY=0.75 EndZ=0
    g2: LineSegment StartX=6.43301 StartY=0.75 StartZ=0 EndX=5.56699 EndY=0.75 EndZ=0
    g3: LineSegment StartX=5.56699 StartY=0.75 StartZ=0 EndX=5.13397 EndY=-1e-16 EndZ=0
    g4: LineSegment StartX=5.13397 StartY=-1e-16 StartZ=0 EndX=5.56699 EndY=-0.75 EndZ=0
    g5: LineSegment StartX=5.56699 StartY=-0.75 StartZ=0 EndX=6.43301 EndY=-0.75 EndZ=0
    g6: Circle CenterX=6 CenterY=0 CenterZ=0 NormalX=0 NormalY=0 NormalZ=1 AngleXU=0 Radius=0.866025
  constraints (16):
    c: Coincident(g0,g1)
    c: Coincident(g1,g2)
    c: Coincident(g2,g3)
    c: Coincident(g3,g4)
    c: Coincident(g4,g5)
    c: Coincident(g5,g0)
    c: Equal(g0, g1-g5) x5
    c: PointOnObject(g0,g6)
    c: PointOnObject(g1,g6)
    c: PointOnObject(g2,g6)
    c: PointOnObject(g3,g6)
    c: PointOnObject(g4,g6)
    c: PointOnObject(g5,g6)
    c: Coincident(g6,g-3)
    c: Horizontal(g5)
    c: DistanceY(g4,g2) = 1.5
FEATURE [PartDesign::Pocket] Pocket034
  BaseFeature = -> Pad020
  Length = 0.9
  Length2 = 100
  Profile = -> Sketch094
  Type = 0
FEATURE [PartDesign::PolarPattern] PolarPattern015
  Angle = 120
  Axis = -> X_Axis094
  BaseFeature = -> Pocket034
  Occurrences = 3
  Originals = -> [Pad020,Pocket034]
FEATURE [PartDesign::Body] Body080
  Group = -> [Sketch093,Pad020,Sketch094,Pocket034,PolarPattern015]
  Origin = -> Origin097
  Tip = -> PolarPattern015
FEATURE [App::DocumentObjectGroup] Group026  label="Set screws003"
  Group = -> [Body080]
FEATURE [Sketcher::SketchObject] Sketch095
  AttachmentOffset = pos=(0,0,-6.5) rot=(0,0,1;0rad)
  FullyConstrained = true
  MapMode = 5
  Placement = pos=(-6.5,1.4e-15,-1.4e-15) rot=(0.57735,0.57735,0.57735;2.0944rad)
  Support = -> [YZ_Plane115]
  sketch-geometry (14):
    g0: Circle CenterX=0 CenterY=0 CenterZ=0 NormalX=0 NormalY=0 NormalZ=1 AngleXU=0 Radius=11
    g1: ArcOfCircle CenterX=0 CenterY=0 CenterZ=0 NormalX=0 NormalY=0 NormalZ=1 AngleXU=0 Radius=13.5 StartAngle=0.0668757 EndAngle=3.07472
    g2: LineSegment StartX=-13.4698 StartY=0.902148 StartZ=0 EndX=-14.2 EndY=-10 EndZ=0
    g3: LineSegment StartX=-14.2 StartY=-10 StartZ=0 EndX=-27.5 EndY=-10 EndZ=0
    g4: LineSegment StartX=-27.5 StartY=-10 StartZ=0 EndX=-27.5 EndY=-15 EndZ=0
    g5: LineSegment StartX=-27.5 StartY=-15 StartZ=0 EndX=-12.3 EndY=-15 EndZ=0
    g6: LineSegment StartX=27.5 StartY=-15 StartZ=0 EndX=27.5 EndY=-10 EndZ=0
    g7: LineSegment StartX=27.5 StartY=-10 StartZ=0 EndX=14.2 EndY=-10 EndZ=0
    g8: LineSegment StartX=14.2 StartY=-10 StartZ=0 EndX=13.4698 EndY=0.902148 EndZ=0
    g9: LineSegment StartX=12.3 StartY=-15 StartZ=0 EndX=12.1995 EndY=-13.5 EndZ=0
    g10: LineSegment StartX=12.1995 StartY=-13.5 StartZ=0 EndX=-12.1995 EndY=-13.5 EndZ=0
    g11: LineSegment StartX=-12.1995 StartY=-13.5 StartZ=0 EndX=-12.3 EndY=-15 EndZ=0
    g12: LineSegment StartX=12.3 StartY=-15 StartZ=0 EndX=27.5 EndY=-15 EndZ=0
    g13: GeomPoint X=0 Y=13.5 Z=0
  constraints (39):
    c: Coincident(g0,g-1)
    c: Radius(g0) = 11
    c: Coincident(g1,g0)
    c: Coincident(g2,g3)
    c: Coincident(g3,g4)
    c: Coincident(g4,g5)
    c: Horizontal(g5)
    c: Coincident(g12,g6)
    c: Coincident(g6,g7)
    c: Horizontal(g7)
    c: Coincident(g7,g8)
    c: Coincident(g9,g10)
    c: Horizontal(g10)
    c: Coincident(g10,g11)
    c: Coincident(g5,g11)
    c: Coincident(g12,g9)
    c: Horizontal(g3)
    c: Vertical(g6)
    c: Vertical(g4)
    c: Equal(g9,g11)
    c: Horizontal(g12)
    c: Horizontal(g5,g9)
    c: Equal(g6,g4)
    c: Equal(g12,g5)
    c: Equal(g7,g3)
    c: DistanceX(g4,g6) = 55
    c: DistanceY(g6,g0) = 15
    c: Equal(g8,g2)
    c: DistanceY(g6,g6) = 5
    c: Parallel(g9,g8)
    c: DistanceY(g9,g9) = 1.5
    c: DistanceX(g5,g5) = 15.2
    c: Diameter(g1) = 27
    c: PointOnObject(g13,g1)
    c: PointOnObject(g13,g-2)
    c: DistanceY(g6,g13) = 28.5
    c: Tangent(g1,g2) = -1.5708
    c: Tangent(g1,g8) = -1.5708
    c: DistanceX(g3,g3) = 13.3
FEATURE [PartDesign::Pad] Pad021
  Direction = (1,-2e-16,3e-16)
  Length = 13
  Length2 = 100
  Placement = pos=(0,0,0) rot=(0.57735,0.57735,0.57735;2.0944rad)
  Profile = -> Sketch095
  Type = 0
FEATURE [Sketcher::SketchObject] Sketch096
  ExternalGeometry = -> [Pad021]
  FullyConstrained = true
  MapMode = 5
  Placement = pos=(4.2e-15,-6.6e-15,-15) rot=(0.707107,0.707107,0;3.14159rad)
  Support = -> [Pad021]
  sketch-geometry (7):
    g0: LineSegment StartX=-24.9 StartY=4.15 StartZ=0 EndX=-14.9 EndY=4.15 EndZ=0
    g1: LineSegment StartX=-14.9 StartY=4.15 StartZ=0 EndX=-14.9 EndY=-4.15 EndZ=0
    g2: LineSegment StartX=-14.9 StartY=-4.15 StartZ=0 EndX=-24.9 EndY=-4.15 EndZ=0
    g3: LineSegment StartX=-24.9 StartY=-4.15 StartZ=0 EndX=-24.9 EndY=4.15 EndZ=0
    g4: LineSegment StartX=-27.5 StartY=6.5 StartZ=0 EndX=-12.3 EndY=-6.5 EndZ=0
    g5: LineSegment StartX=-27.5 StartY=-6.5 StartZ=0 EndX=-12.3 EndY=6.5 EndZ=0
    g6: GeomPoint X=-19.9 Y=2.6e-15 Z=0
  constraints (17):
    c: Coincident(g0,g1)
    c: Coincident(g1,g2)
    c: Coincident(g2,g3)
    c: Coincident(g3,g0)
    c: Horizontal(g0)
    c: Horizontal(g2)
    c: Vertical(g1)
    c: Vertical(g3)
    c: DistanceX(g0,g0) = 10
    c: DistanceY(g1,g1) = 8.3
    c: Coincident(g4,g-3)
    c: Coincident(g4,g-4)
    c: Coincident(g5,g-4)
    c: Coincident(g5,g-3)
    c: PointOnObject(g6,g4)
    c: PointOnObject(g6,g5)
    c: Symmetric(g0,g1,g6)
FEATURE [PartDesign::Pocket] Pocket035
  BaseFeature = -> Pad021
  Length = 2.3
  Length2 = 100
  Placement = pos=(0,0,0) rot=(0.57735,0.57735,0.57735;2.0944rad)
  Profile = -> Sketch096
  Type = 0
FEATURE [Sketcher::SketchObject] Sketch097
  ExternalGeometry = -> [Pocket035]
  FullyConstrained = true
  MapMode = 5
  Placement = pos=(2.8e-15,-4.4e-15,-10) rot=(0,0,-1;1.5708rad)
  Support = -> [Pocket035]
  sketch-geometry (2):
    g0: Circle CenterX=21.2 CenterY=2.1e-15 CenterZ=0 NormalX=0 NormalY=0 NormalZ=1 AngleXU=0 Radius=2.5
    g1: LineSegment StartX=21.2 StartY=2.1e-15 StartZ=0 EndX=27.5 EndY=2.1e-15 EndZ=0
  constraints (5):
    c: Diameter(g0) = 5
    c: DistanceX(g0,g-3) = 6.3
    c: Coincident(g1,g0)
    c: Horizontal(g1)
    c: Symmetric(g-5,g-5,g1)
FEATURE [PartDesign::Pocket] Pocket036
  BaseFeature = -> Pocket035
  Length = 5
  Length2 = 100
  Placement = pos=(0,0,0) rot=(0.57735,0.57735,0.57735;2.0944rad)
  Profile = -> Sketch097
  Type = 2
FEATURE [Sketcher::SketchObject] Sketch098
  ExternalGeometry = -> [Pocket036]
  FullyConstrained = true
  MapMode = 5
  Placement = pos=(6.5,-1.4e-15,1.5e-15) rot=(0.57735,0.57735,0.57735;2.0944rad)
  Support = -> [Pocket036]
  sketch-geometry (6):
    g0: LineSegment StartX=-24.6 StartY=-13.7 StartZ=0 EndX=-24.6 EndY=-11.3 EndZ=0
    g1: LineSegment StartX=-24.6 StartY=-11.3 StartZ=0 EndX=-14.2 EndY=-11.3 EndZ=0
    g2: LineSegment StartX=-14.2 StartY=-11.3 StartZ=0 EndX=-14.2 EndY=-13.7 EndZ=0
    g3: LineSegment StartX=-14.2 StartY=-13.7 StartZ=0 EndX=-24.6 EndY=-13.7 EndZ=0
    g4: GeomPoint X=-19.4 Y=-12.5 Z=0
    g5: LineSegment StartX=-19.4 StartY=-12.5 StartZ=0 EndX=-27.5 EndY=-12.5 EndZ=0
  constraints (15):
    c: Coincident(g0,g1)
    c: Coincident(g1,g2)
    c: Coincident(g2,g3)
    c: Coincident(g3,g0)
    c: Horizontal(g1)
    c: Horizontal(g3)
    c: Vertical(g0)
    c: Vertical(g2)
    c: Symmetric(g1,g0,g4)
    c: DistanceX(g1,g1) = 10.4
    c: DistanceY(g2,g2) = 2.4
    c: DistanceX(g2,g-4) = 1.9
    c: Coincident(g5,g4)
    c: Horizontal(g5)
    c: Symmetric(g-5,g-5,g5)
FEATURE [PartDesign::Pocket] Pocket037
  BaseFeature = -> Pocket036
  Length = 0.4
  Length2 = 100
  Placement = pos=(0,0,0) rot=(0.57735,0.57735,0.57735;2.0944rad)
  Profile = -> Sketch098
  Type = 0
FEATURE [PartDesign::Mirrored] Mirrored003
  BaseFeature = -> Pocket037
  MirrorPlane = -> Sketch096 [V_Axis]
  Originals = -> [Pocket035,Pocket036,Pocket037]
  Placement = pos=(0,0,0) rot=(0.57735,0.57735,0.57735;2.0944rad)
FEATURE [Sketcher::SketchObject] Sketch099
  ExternalGeometry = -> [Mirrored003]
  FullyConstrained = true
  MapMode = 5
  Placement = pos=(0,0,0) rot=(1,0,0;1.5708rad)
  Support = -> [XZ_Plane115]
  sketch-geometry (9):
    g0: GeomPoint X=-6.5 Y=13.5 Z=0
    g1: LineSegment StartX=6.5 StartY=-10 StartZ=0 EndX=6.5 EndY=13.5 EndZ=0
    g2: LineSegment StartX=6.5 StartY=13.5 StartZ=0 EndX=4.75 EndY=13.5 EndZ=0
    g3: LineSegment StartX=-6.5 StartY=13.5 StartZ=0 EndX=-4.75 EndY=13.5 EndZ=0
    g4: LineSegment StartX=-6.5 StartY=-10 StartZ=0 EndX=-6.5 EndY=13.5 EndZ=0
    g5: LineSegment StartX=6.5 StartY=-10 StartZ=0 EndX=4.75 EndY=-1 EndZ=0
    g6: LineSegment StartX=4.75 StartY=-1 StartZ=0 EndX=4.75 EndY=13.5 EndZ=0
    g7: LineSegment StartX=-4.75 StartY=13.5 StartZ=0 EndX=-4.75 EndY=-1 EndZ=0
    g8: LineSegment StartX=-4.75 StartY=-1 StartZ=0 EndX=-6.5 EndY=-10 EndZ=0
  constraints (24):
    c: Vertical(g0,g-4)
    c: Horizontal(g-3,g0)
    c: Coincident(g1,g-3)
    c: Coincident(g1,g2)
    c: Horizontal(g2)
    c: Coincident(g3,g0)
    c: Horizontal(g3)
    c: Coincident(g4,g3)
    c: Vertical(g4,g-4)
    c: DistanceX(g3,g2) = 9.5
    c: Equal(g2,g3)
    c: Horizontal(g1,g4)
    c: Coincident(g1,g-5)
    c: Coincident(g1,g5)
    c: Coincident(g5,g6)
    c: Coincident(g6,g2)
    c: Vertical(g6)
    c: DistanceY(g1,g5) = 9
    c: Coincident(g3,g7)
    c: Vertical(g7)
    c: Coincident(g7,g8)
    c: Coincident(g8,g4)
    c: Horizontal(g7,g5)
    c: DistanceX(g2,g2) = 1.75
FEATURE [PartDesign::Pocket] Pocket038
  BaseFeature = -> Mirrored003
  Length = 15
  Length2 = 15
  Placement = pos=(0,0,0) rot=(0.57735,0.57735,0.57735;2.0944rad)
  Profile = -> Sketch099
  Type = 4
FEATURE [Sketcher::SketchObject] Sketch100
  FullyConstrained = true
  MapMode = 5
  Placement = pos=(-6.5,1.4e-15,-1.5e-15) rot=(0.57735,0.57735,-0.57735;4.18879rad)
  Support = -> [Pocket038]
  sketch-geometry (1):
    g0: Circle CenterX=0 CenterY=0 CenterZ=0 NormalX=0 NormalY=0 NormalZ=1 AngleXU=0 Radius=12.2
  constraints (2):
    c: Coincident(g0,g-1)
    c: Diameter(g0) = 24.4
FEATURE [PartDesign::Pocket] Pocket039
  BaseFeature = -> Pocket038
  Length = 2.75
  Length2 = 100
  Placement = pos=(0,0,0) rot=(0.57735,0.57735,0.57735;2.0944rad)
  Profile = -> Sketch100
  Type = 0
FEATURE [Sketcher::SketchObject] Sketch101
  FullyConstrained = true
  MapMode = 5
  Placement = pos=(6.5,-1.4e-15,1.5e-15) rot=(0.57735,0.57735,0.57735;2.0944rad)
  Support = -> [Pocket039]
  sketch-geometry (1):
    g0: Circle CenterX=0 CenterY=0 CenterZ=0 NormalX=0 NormalY=0 NormalZ=1 AngleXU=0 Radius=12.1
  constraints (2):
    c: Coincident(g0,g-1)
    c: Diameter(g0) = 24.2
FEATURE [PartDesign::Pocket] Pocket040
  BaseFeature = -> Pocket039
  Length = 2.75
  Length2 = 100
  Placement = pos=(0,0,0) rot=(0.57735,0.57735,0.57735;2.0944rad)
  Profile = -> Sketch101
  Type = 0
FEATURE [Sketcher::SketchObject] Sketch102
  ExternalGeometry = -> [Pocket040]
  FullyConstrained = true
  MapMode = 5
  Placement = pos=(6.5,-1.4e-15,1.5e-15) rot=(0.57735,0.57735,0.57735;2.0944rad)
  Support = -> [Pocket040]
  sketch-geometry (6):
    g0: ArcOfCircle CenterX=0 CenterY=0 CenterZ=0 NormalX=0 NormalY=0 NormalZ=1 AngleXU=0 Radius=13.5 StartAngle=3.79664 EndAngle=5.62814
    g1: LineSegment StartX=-11.8698 StartY=-8.57666 StartZ=0 EndX=-12.3 EndY=-15 EndZ=0
    g2: LineSegment StartX=-12.3 StartY=-15 StartZ=0 EndX=12.3 EndY=-15 EndZ=0
    g3: LineSegment StartX=12.3 StartY=-15 StartZ=0 EndX=11.8698 EndY=-8.57666 EndZ=0
    g4: ArcOfCircle CenterX=11.2212 CenterY=-8.6201 CenterZ=0 NormalX=0 NormalY=0 NormalZ=1 AngleXU=0 Radius=0.65 StartAngle=0.0668757 EndAngle=2.48655
    g5: ArcOfCircle CenterX=-11.2212 CenterY=-8.6201 CenterZ=0 NormalX=0 NormalY=0 NormalZ=1 AngleXU=0 Radius=0.65 StartAngle=0.655044 EndAngle=3.07472
  constraints (14):
    c: Coincident(g0,g-1)
    c: Diameter(g0) = 27
    c: Coincident(g1,g2)
    c: Coincident(g2,g3)
    c: Coincident(g1,g-3)
    c: Coincident(g2,g-4)
    c: Tangent(g3,g4) = -1.5708
    c: Tangent(g0,g4) = 1.5708
    c: Tangent(g0,g5) = 1.5708
    c: Tangent(g1,g5) = -1.5708
    c: Equal(g4,g5)
    c: Horizontal(g4,g5)
    c: Parallel(g-4,g3)
    c: Radius(g4) = 0.65
FEATURE [PartDesign::Pocket] Pocket041
  BaseFeature = -> Pocket040
  Length = 5.25
  Length2 = 100
  Placement = pos=(0,0,0) rot=(0.57735,0.57735,0.57735;2.0944rad)
  Profile = -> Sketch102
  Type = 0
FEATURE [Sketcher::SketchObject] Sketch103
  ExternalGeometry = -> [Pocket041]
  FullyConstrained = true
  MapMode = 5
  Placement = pos=(-6.5,1.4e-15,-1.5e-15) rot=(0.57735,0.57735,-0.57735;4.18879rad)
  Support = -> [Pocket041]
  sketch-geometry (6):
    g0: ArcOfCircle CenterX=0 CenterY=0 CenterZ=0 NormalX=0 NormalY=0 NormalZ=1 AngleXU=0 Radius=13.5 StartAngle=0.655044 EndAngle=2.48655
    g1: LineSegment StartX=11.8698 StartY=8.57666 StartZ=0 EndX=12.3 EndY=15 EndZ=0
    g2: LineSegment StartX=12.3 StartY=15 StartZ=0 EndX=-12.3 EndY=15 EndZ=0
    g3: LineSegment StartX=-12.3 StartY=15 StartZ=0 EndX=-11.8698 EndY=8.57666 EndZ=0
    g4: ArcOfCircle CenterX=-11.2212 CenterY=8.6201 CenterZ=0 NormalX=0 NormalY=0 NormalZ=1 AngleXU=0 Radius=0.65 StartAngle=3.20847 EndAngle=5.62814
    g5: ArcOfCircle CenterX=11.2212 CenterY=8.6201 CenterZ=0 NormalX=0 NormalY=0 NormalZ=1 AngleXU=0 Radius=0.65 StartAngle=3.79664 EndAngle=6.21631
  constraints (14):
    c: Coincident(g0,g-1)
    c: Radius(g0) = 13.5
    c: Coincident(g1,g2)
    c: Coincident(g2,g-3)
    c: Coincident(g2,g3)
    c: Coincident(g-4,g1)
    c: Tangent(g3,g4) = -1.5708
    c: Tangent(g0,g4) = 1.5708
    c: Tangent(g0,g5) = 1.5708
    c: Tangent(g1,g5) = -1.5708
    c: Equal(g4,g5)
    c: Radius(g4) = 0.65
    c: Parallel(g-4,g1)
    c: Parallel(g3,g-3)
FEATURE [PartDesign::Pocket] Pocket042
  BaseFeature = -> Pocket041
  Length = 5.25
  Length2 = 100
  Placement = pos=(0,0,0) rot=(0.57735,0.57735,0.57735;2.0944rad)
  Profile = -> Sketch103
  Type = 0
FEATURE [PartDesign::Chamfer] Chamfer003
  Angle = 45
  Base = -> Pocket042 [Edge159,Edge155,Edge22,Edge27]
  BaseFeature = -> Pocket042
  ChamferType = 0
  FlipDirection = false
  Placement = pos=(0,0,0) rot=(0.57735,0.57735,0.57735;2.0944rad)
  Size = 2
  Size2 = 1
  SupportTransform = false
FEATURE [Sketcher::SketchObject] Sketch104
  ExternalGeometry = -> [Chamfer003]
  FullyConstrained = true
  MapMode = 5
  Placement = pos=(-3.75,5e-15,-2.7e-15) rot=(-0.57735,-0.57735,0.57735;2.0944rad)
  Support = -> [Chamfer003]
  sketch-geometry (13):
    g0: ArcOfCircle CenterX=-6.9e-15 CenterY=-3.7e-15 CenterZ=0 NormalX=0 NormalY=0 NormalZ=1 AngleXU=0 Radius=11 StartAngle=5.75419 EndAngle=6.81218
    g1: ArcOfCircle CenterX=-6.9e-15 CenterY=-3.7e-15 CenterZ=0 NormalX=0 NormalY=0 NormalZ=1 AngleXU=0 Radius=12.2 StartAngle=5.94045 EndAngle=6.62592
    g2: ArcOfCircle CenterX=-6.9e-15 CenterY=-3.7e-15 CenterZ=0 NormalX=0 NormalY=0 NormalZ=1 AngleXU=0 Radius=11 StartAngle=2.6126 EndAngle=3.67059
    g3: ArcOfCircle CenterX=-6.9e-15 CenterY=-3.7e-15 CenterZ=0 NormalX=0 NormalY=0 NormalZ=1 AngleXU=0 Radius=12.2 StartAngle=2.79886 EndAngle=3.48433
    g4: Ellipse CenterX=-6.9e-15 CenterY=-3.7e-15 CenterZ=0 NormalX=0 NormalY=0 NormalZ=1 MajorRadius=13.5 MinorRadius=7.81051 AngleXU=-3e-16
    g5: LineSegment StartX=13.5 StartY=-7.4e-15 StartZ=0 EndX=-13.5 EndY=0 EndZ=0
    g6: LineSegment StartX=-4.8e-15 StartY=7.81051 StartZ=0 EndX=-9.1e-15 EndY=-7.81051 EndZ=0
    g7: GeomPoint X=11.0112 Y=-6.8e-15 Z=0
    g8: GeomPoint X=-11.0112 Y=-7e-16 Z=0
    g9: LineSegment StartX=-11.4904 StartY=4.1 StartZ=0 EndX=-9.49645 EndY=5.55135 EndZ=0
    g10: LineSegment StartX=-11.4904 StartY=-4.1 StartZ=0 EndX=-9.49645 EndY=-5.55135 EndZ=0
    g11: LineSegment StartX=9.49645 StartY=-5.55135 StartZ=0 EndX=11.4904 EndY=-4.1 EndZ=0
    g12: LineSegment StartX=11.4904 StartY=4.1 StartZ=0 EndX=9.49645 EndY=5.55135 EndZ=0
  constraints (29):
    c: Coincident(g0,g-4)
    c: PointOnObject(g0,g-4)
    c: Coincident(g1,g0)
    c: PointOnObject(g1,g-3)
    c: Coincident(g2,g0)
    c: PointOnObject(g2,g-4)
    c: Coincident(g3,g0)
    c: PointOnObject(g3,g-3)
    c: InternalAlignment(g5-g8 -> g4) x4
    c: Coincident(g4,g0)
    c: PointOnObject(g3,g4)
    c: PointOnObject(g2,g4)
    c: PointOnObject(g3,g4)
    c: PointOnObject(g2,g4)
    c: PointOnObject(g0,g4)
    c: PointOnObject(g1,g4)
    c: PointOnObject(g1,g4)
    c: PointOnObject(g0,g4)
    c: PointOnObject(g5,g-1)
    c: DistanceX(g5,g5) = 27
    c: DistanceY(g3,g3) = 8.2
    c: Coincident(g9,g3)
    c: Coincident(g9,g2)
    c: Coincident(g10,g3)
    c: Coincident(g10,g2)
    c: Coincident(g11,g0)
    c: Coincident(g11,g1)
    c: Coincident(g12,g1)
    c: Coincident(g12,g0)
FEATURE [PartDesign::Pocket] Pocket043
  BaseFeature = -> Chamfer003
  Length = 5
  Length2 = 100
  Placement = pos=(0,0,0) rot=(0.57735,0.57735,0.57735;2.0944rad)
  Profile = -> Sketch104
  Type = 0
FEATURE [PartDesign::Body] Body101  label="Metal case003"
  Group = -> [Sketch095,Pad021,Sketch096,Pocket035,Sketch097,Pocket036,Sketch098,Pocket037,Mirrored003,Sketch099,Pocket038,Sketch100,Pocket039,Sketch101,Pocket040,Sketch102,Pocket041,Sketch103,Pocket042,Chamfer003,Sketch104,Pocket043]
  Origin = -> Origin118
  Tip = -> Pocket043
FEATURE [App::DocumentObjectGroup] Group027  label="Case003"
  Group = -> [Body101]
FEATURE [App::Part] Part017  label="KP08-004"
  Group = -> [Group021,Body082,Body081,Body086,Body083,Body087,Body085,Body084,Group022,Body089,Body088,Group023,Body094,Body093,Body096,Body092,Body095,Body091,Body090,Group024,Body100,Body099,Group025,Body097,Body098,Group026,Body080,Group027,Body101]
  Origin = -> Origin119
  Placement = pos=(332,246,105) rot=(0,0,1;3.14159rad)
FEATURE [Sketcher::SketchObject] Sketch105
  FullyConstrained = true
  MapMode = 5
  Placement = pos=(0,0,0) rot=(-0.57735,0.57735,0.57735;4.18879rad)
  Support = -> [YZ_Plane124]
  sketch-geometry (1):
    g0: Circle CenterX=0 CenterY=-7.5 CenterZ=0 NormalX=0 NormalY=0 NormalZ=1 AngleXU=0 Radius=0.25
  constraints (3):
    c: PointOnObject(g0,g-2)
    c: DistanceY(g0) = -7.5
    c: Diameter(g0) = 0.5
FEATURE [Sketcher::SketchObject] Sketch106
  FullyConstrained = true
  MapMode = 5
  Support = -> [XY_Plane117]
  sketch-geometry (2):
    g0: LineSegment StartX=0 StartY=5.5 StartZ=0 EndX=6e-16 EndY=9.5 EndZ=0
    g1: ArcOfCircle CenterX=0 CenterY=7.5 CenterZ=0 NormalX=0 NormalY=0 NormalZ=1 AngleXU=0 Radius=2 StartAngle=4.71239 EndAngle=7.85398
  constraints (7):
    c: PointOnObject(g0,g-2)
    c: PointOnObject(g0,g-2)
    c: PointOnObject(g1,g0)
    c: Coincident(g1,g0)
    c: Coincident(g1,g0)
    c: Radius(g1) = 2
    c: DistanceY(g1) = 7.5
FEATURE [PartDesign::Revolution] Revolution032
  Angle = 360
  Axis = (0,1,0)
  Base = (0,0,0)
  Profile = -> Sketch106
  ReferenceAxis = -> Sketch106 [V_Axis]
  Reversed = true
FEATURE [PartDesign::Body] Body103  label="Ball 029"
  Group = -> [Sketch106,Revolution032]
  Origin = -> Origin121
  Tip = -> Revolution032
FEATURE [PartDesign::FeatureBase] Clone056
  BaseFeature = -> Body103
FEATURE [PartDesign::Body] Body104  label="Ball 030"
  BaseFeature = -> Body103
  Group = -> [Clone056]
  Origin = -> Origin122
  Placement = pos=(0,0,0) rot=(-1,0,0;0.897598rad)
  Tip = -> Clone056
FEATURE [PartDesign::FeatureBase] Clone057
  BaseFeature = -> Body103
FEATURE [PartDesign::Body] Body105  label="Ball 031"
  BaseFeature = -> Body103
  Group = -> [Clone057]
  Origin = -> Origin123
  Placement = pos=(0,0,0) rot=(-1,0,0;1.7952rad)
  Tip = -> Clone057
FEATURE [PartDesign::FeatureBase] Clone058
  BaseFeature = -> Body103
FEATURE [PartDesign::Body] Body106  label="Ball 032"
  BaseFeature = -> Body103
  Group = -> [Clone058]
  Origin = -> Origin124
  Placement = pos=(0,0,0) rot=(1,0,0;3.59039rad)
  Tip = -> Clone058
FEATURE [PartDesign::FeatureBase] Clone059
  BaseFeature = -> Body103
FEATURE [PartDesign::Body] Body107  label="Ball 033"
  BaseFeature = -> Body103
  Group = -> [Clone059]
  Origin = -> Origin125
  Placement = pos=(0,0,0) rot=(1,0,0;2.69279rad)
  Tip = -> Clone059
FEATURE [PartDesign::FeatureBase] Clone060
  BaseFeature = -> Body103
FEATURE [PartDesign::Body] Body108  label="Ball 034"
  BaseFeature = -> Body103
  Group = -> [Clone060]
  Origin = -> Origin126
  Placement = pos=(0,0,0) rot=(1,0,0;1.7952rad)
  Tip = -> Clone060
FEATURE [PartDesign::FeatureBase] Clone061
  BaseFeature = -> Body103
FEATURE [PartDesign::Body] Body109  label="Ball 035"
  BaseFeature = -> Body103
  Group = -> [Clone061]
  Origin = -> Origin127
  Placement = pos=(0,0,0) rot=(1,0,0;0.897598rad)
  Tip = -> Clone061
FEATURE [App::DocumentObjectGroup] Group028  label="Balls004"
  Group = -> [Body103,Body104,Body105,Body106,Body107,Body108,Body109]
FEATURE [Sketcher::SketchObject] Sketch107
  FullyConstrained = true
  MapMode = 5
  Support = -> [XY_Plane126]
  sketch-geometry (7):
    g0: LineSegment StartX=-5 StartY=7.5 StartZ=0 EndX=5 EndY=7.5 EndZ=0
    g1: LineSegment StartX=-0.210977 StartY=7.5 StartZ=0 EndX=0.210977 EndY=7.5 EndZ=0
    g2: ArcOfCircle CenterX=0.25 CenterY=7.5 CenterZ=0 NormalX=0 NormalY=0 NormalZ=1 AngleXU=0 Radius=0.460977 StartAngle=2.43297 EndAngle=3.14159
    g3: ArcOfCircle CenterX=-0.25 CenterY=7.5 CenterZ=0 NormalX=0 NormalY=0 NormalZ=1 AngleXU=0 Radius=0.460977 StartAngle=9.792e-13 EndAngle=0.708626
    g4: LineSegment StartX=-0.1 StartY=7.8 StartZ=0 EndX=-0.1 EndY=7.75 EndZ=0
    g5: LineSegment StartX=-0.1 StartY=7.75 StartZ=0 EndX=0.1 EndY=7.75 EndZ=0
    g6: LineSegment StartX=0.1 StartY=7.75 StartZ=0 EndX=0.1 EndY=7.8 EndZ=0
  constraints (22):
    c: DistanceY(g-1,g0) = 7.5
    c: Symmetric(g0,g0,g-2)
    c: DistanceX(g0,g0) = 10
    c: PointOnObject(g1,g0)
    c: PointOnObject(g1,g0)
    c: Coincident(g3,g1)
    c: Coincident(g2,g1)
    c: Coincident(g2,g4)
    c: Coincident(g4,g5)
    c: Horizontal(g5)
    c: Coincident(g5,g6)
    c: Coincident(g6,g3)
    c: Vertical(g6)
    c: Equal(g3,g2)
    c: Vertical(g4)
    c: Symmetric(g2,g3,g-2)
    c: DistanceX(g5,g5) = 0.2
    c: Distance(g5,g1) = 0.25
    c: DistanceX(g3,g-1) = 0.25
    c: PointOnObject(g3,g1)
    c: PointOnObject(g2,g1)
    c: Distance(g3,g1) = 0.3
FEATURE [PartDesign::Revolution] Revolution033
  Angle = 360
  Axis = (10,0,0)
  Base = (-5,7.5,0)
  Profile = -> Sketch107
  ReferenceAxis = -> Sketch107 [Axis]
FEATURE [PartDesign::Body] Body112  label="Rivet 029"
  Group = -> [Sketch107,Revolution033]
  Origin = -> Origin130
  Placement = pos=(0,0,0) rot=(1,0,0;0.448799rad)
  Tip = -> Revolution033
FEATURE [PartDesign::FeatureBase] Clone063
  BaseFeature = -> Body112
  Placement = pos=(0,0,0) rot=(1,0,0;0.448799rad)
FEATURE [PartDesign::Body] Body113  label="Rivet 030"
  BaseFeature = -> Body112
  Group = -> [Clone063]
  Origin = -> Origin131
  Placement = pos=(0,0,0) rot=(1,0,0;0.897598rad)
  Tip = -> Clone063
FEATURE [PartDesign::FeatureBase] Clone064
  BaseFeature = -> Body112
  Placement = pos=(0,0,0) rot=(1,0,0;0.448799rad)
FEATURE [PartDesign::Body] Body114  label="Rivet 031"
  BaseFeature = -> Body112
  Group = -> [Clone064]
  Origin = -> Origin132
  Placement = pos=(0,0,0) rot=(1,0,0;1.7952rad)
  Tip = -> Clone064
FEATURE [PartDesign::FeatureBase] Clone065
  BaseFeature = -> Body112
  Placement = pos=(0,0,0) rot=(1,0,0;0.448799rad)
FEATURE [PartDesign::Body] Body115  label="Rivet 032"
  BaseFeature = -> Body112
  Group = -> [Clone065]
  Origin = -> Origin133
  Placement = pos=(0,0,0) rot=(1,0,0;2.69279rad)
  Tip = -> Clone065
FEATURE [PartDesign::FeatureBase] Clone066
  BaseFeature = -> Body112
  Placement = pos=(0,0,0) rot=(1,0,0;0.448799rad)
FEATURE [PartDesign::Body] Body116  label="Rivet 033"
  BaseFeature = -> Body112
  Group = -> [Clone066]
  Origin = -> Origin134
  Placement = pos=(0,0,0) rot=(1,0,0;3.59039rad)
  Tip = -> Clone066
FEATURE [PartDesign::FeatureBase] Clone067
  BaseFeature = -> Body112
  Placement = pos=(0,0,0) rot=(1,0,0;0.448799rad)
FEATURE [PartDesign::Body] Body117  label="Rivet 034"
  BaseFeature = -> Body112
  Group = -> [Clone067]
  Origin = -> Origin135
  Placement = pos=(0,0,0) rot=(-1,0,0;1.7952rad)
  Tip = -> Clone067
FEATURE [PartDesign::FeatureBase] Clone068
  BaseFeature = -> Body112
  Placement = pos=(0,0,0) rot=(1,0,0;0.448799rad)
FEATURE [PartDesign::Body] Body118  label="Rivet 035"
  BaseFeature = -> Body112
  Group = -> [Clone068]
  Origin = -> Origin136
  Placement = pos=(0,0,0) rot=(-1,0,0;0.897598rad)
  Tip = -> Clone068
FEATURE [App::DocumentObjectGroup] Group030  label="Rivets004"
  Group = -> [Body112,Body113,Body114,Body115,Body116,Body117,Body118]
FEATURE [Sketcher::SketchObject] Sketch108
  FullyConstrained = true
  MapMode = 5
  Placement = pos=(0,0,0) rot=(1,0,0;1.5708rad)
  Support = -> [XZ_Plane124]
  sketch-geometry (4):
    g0: LineSegment StartX=0 StartY=8.5 StartZ=0 EndX=0.1 EndY=8.5 EndZ=0
    g1: LineSegment StartX=0.1 StartY=8.5 StartZ=0 EndX=0.1 EndY=6.5 EndZ=0
    g2: LineSegment StartX=0.1 StartY=6.5 StartZ=0 EndX=0 EndY=6.5 EndZ=0
    g3: LineSegment StartX=0 StartY=6.5 StartZ=0 EndX=0 EndY=8.5 EndZ=0
  constraints (12):
    c: Coincident(g0,g1)
    c: Coincident(g1,g2)
    c: Coincident(g2,g3)
    c: Coincident(g3,g0)
    c: Horizontal(g0)
    c: Horizontal(g2)
    c: Vertical(g1)
    c: Vertical(g3)
    c: PointOnObject(g0,g-2)
    c: DistanceX(g0,g0) = 0.1
    c: DistanceY(g0) = 8.5
    c: DistanceY(g1) = 6.5
FEATURE [PartDesign::Revolution] Revolution034
  Angle = 360
  Axis = (1,0,0)
  Base = (0,0,0)
  Placement = pos=(0,0,0) rot=(1,0,0;1.5708rad)
  Profile = -> Sketch108
  ReferenceAxis = -> Sketch108 [H_Axis]
FEATURE [Sketcher::SketchObject] Sketch109
  FullyConstrained = true
  MapMode = 5
  Placement = pos=(0,0,0) rot=(0.57735,0.57735,0.57735;2.0944rad)
  Support = -> [YZ_Plane124]
  sketch-geometry (5):
    g0: ArcOfCircle CenterX=0 CenterY=7.5 CenterZ=0 NormalX=0 NormalY=0 NormalZ=1 AngleXU=0 Radius=2.11 StartAngle=5.66076 EndAngle=6.65667
    g1: LineSegment StartX=5e-16 StartY=8.5 StartZ=0 EndX=0 EndY=6.26986 EndZ=0
    g2: ArcOfCircle CenterX=0 CenterY=0 CenterZ=0 NormalX=0 NormalY=0 NormalZ=1 AngleXU=0 Radius=6.5 StartAngle=1.3039 EndAngle=1.5708
    g3: LineSegment StartX=1.71431 StartY=6.26986 StartZ=0 EndX=0 EndY=6.26986 EndZ=0
    g4: ArcOfCircle CenterX=0 CenterY=0 CenterZ=0 NormalX=0 NormalY=0 NormalZ=1 AngleXU=0 Radius=8.5 StartAngle=1.33757 EndAngle=1.5708
  constraints (16):
    c: PointOnObject(g0,g-2)
    c: DistanceY(g0) = 7.5
    c: Radius(g0) = 2.11
    c: PointOnObject(g2,g1)
    c: DistanceY(g2) = 6.5
    c: Coincident(g2,g-1)
    c: Coincident(g3,g2)
    c: Horizontal(g3)
    c: Coincident(g0,g2)
    c: Coincident(g1,g3)
    c: PointOnObject(g1,g-2)
    c: PointOnObject(g1,g-2)
    c: Coincident(g4,g-1)
    c: Coincident(g4,g1)
    c: DistanceY(g1) = 8.5
    c: Coincident(g0,g4)
FEATURE [PartDesign::Revolution] Revolution035
  Angle = 180
  Axis = (-2e-16,3e-16,1)
  Base = (0,0,0)
  BaseFeature = -> Revolution034
  Placement = pos=(0,0,0) rot=(1,0,0;1.5708rad)
  Profile = -> Sketch109
  ReferenceAxis = -> Sketch109 [V_Axis]
  Reversed = true
FEATURE [PartDesign::PolarPattern] PolarPattern016
  Angle = 360
  Axis = -> Sketch109 [N_Axis]
  BaseFeature = -> Revolution035
  Occurrences = 3
  Originals = -> [Revolution035]
  Placement = pos=(0,0,0) rot=(1,0,0;1.5708rad)
  Refine = true
FEATURE [Sketcher::SketchObject] Sketch110
  FullyConstrained = true
  MapMode = 5
  Placement = pos=(0,0,0) rot=(0.57735,0.57735,0.57735;2.0944rad)
  Support = -> [YZ_Plane124]
  sketch-geometry (4):
    g0: ArcOfCircle CenterX=0 CenterY=7.5 CenterZ=0 NormalX=0 NormalY=0 NormalZ=1 AngleXU=0 Radius=2.01 StartAngle=5.57985 EndAngle=6.86228
    g1: LineSegment StartX=0 StartY=6.2 StartZ=0 EndX=1.533 EndY=6.2 EndZ=0
    g2: LineSegment StartX=0 StartY=8.6 StartZ=0 EndX=0 EndY=6.2 EndZ=0
    g3: LineSegment StartX=0 StartY=8.6 StartZ=0 EndX=1.68229 EndY=8.6 EndZ=0
  constraints (13):
    c: PointOnObject(g0,g-2)
    c: DistanceY(g0) = 7.5
    c: Radius(g0) = 2.01
    c: PointOnObject(g1,g-2)
    c: Horizontal(g1)
    c: Coincident(g0,g1)
    c: DistanceY(g1) = 6.2
    c: DistanceY(g2) = 8.6
    c: Coincident(g2,g1)
    c: PointOnObject(g2,g-2)
    c: Coincident(g3,g2)
    c: Horizontal(g3)
    c: Coincident(g0,g3)
FEATURE [PartDesign::Groove] Groove004
  Angle = 360
  Axis = (-2e-16,3e-16,1)
  Base = (0,0,0)
  BaseFeature = -> PolarPattern016
  Placement = pos=(0,0,0) rot=(1,0,0;1.5708rad)
  Profile = -> Sketch110
  ReferenceAxis = -> Sketch110 [V_Axis]
FEATURE [PartDesign::PolarPattern] PolarPattern017
  Angle = 360
  Axis = -> Sketch110 [N_Axis]
  BaseFeature = -> Groove004
  Occurrences = 3
  Originals = -> [Groove004]
  Placement = pos=(0,0,0) rot=(1,0,0;1.5708rad)
FEATURE [PartDesign::Pocket] Pocket044
  BaseFeature = -> PolarPattern017
  Length = 5
  Length2 = 100
  Placement = pos=(0,0,0) rot=(1,0,0;1.5708rad)
  Profile = -> Sketch105
  Type = 1
FEATURE [PartDesign::PolarPattern] PolarPattern018
  Angle = 360
  Axis = -> Sketch105 [N_Axis]
  BaseFeature = -> Pocket044
  Occurrences = 3
  Originals = -> [Pocket044]
  Placement = pos=(0,0,0) rot=(1,0,0;1.5708rad)
FEATURE [PartDesign::Body] Body110  label="Cage 009"
  Group = -> [Sketch108,Revolution034,Sketch109,Revolution035,PolarPattern016,Sketch110,Groove004,PolarPattern017,Sketch105,Pocket044,PolarPattern018]
  Origin = -> Origin128
  Placement = pos=(0,0,0) rot=(-1,0,0;1.5708rad)
  Tip = -> PolarPattern018
FEATURE [PartDesign::FeatureBase] Clone062
  BaseFeature = -> Body110
  Placement = pos=(0,0,0) rot=(-1,0,0;1.5708rad)
FEATURE [PartDesign::Body] Body111  label="Cage 010"
  BaseFeature = -> Body110
  Group = -> [Clone062]
  Origin = -> Origin129
  Placement = pos=(0,0,0) rot=(0,1,0;3.14159rad)
  Tip = -> Clone062
FEATURE [App::DocumentObjectGroup] Group029  label="Cages004"
  Group = -> [Body110,Body111]
FEATURE [Sketcher::SketchObject] Sketch111
  FullyConstrained = true
  MapMode = 5
  Support = -> [XY_Plane133]
  sketch-geometry (14):
    g0: ArcOfCircle CenterX=-1e-16 CenterY=7.5 CenterZ=0 NormalX=0 NormalY=0 NormalZ=1 AngleXU=0 Radius=2 StartAngle=0.848062 EndAngle=2.29353
    g1: LineSegment StartX=-3.5 StartY=11 StartZ=0 EndX=3.5 EndY=11 EndZ=0
    g2: LineSegment StartX=3.5 StartY=11 StartZ=0 EndX=3.5 EndY=9.2 EndZ=0
    g3: LineSegment StartX=2.9 StartY=9 StartZ=0 EndX=1.32288 EndY=9 EndZ=0
    g4: LineSegment StartX=-3.5 StartY=9.2 StartZ=0 EndX=-3.5 EndY=11 EndZ=0
    g5: LineSegment StartX=-1.32288 StartY=9 StartZ=0 EndX=-2.9 EndY=9 EndZ=0
    g6: LineSegment StartX=2.9 StartY=9 StartZ=0 EndX=2.9 EndY=9.5 EndZ=0
    g7: LineSegment StartX=2.9 StartY=9.5 StartZ=0 EndX=3.2 EndY=9.5 EndZ=0
    g8: LineSegment StartX=3.2 StartY=9.5 StartZ=0 EndX=3.2 EndY=9.2 EndZ=0
    g9: LineSegment StartX=3.2 StartY=9.2 StartZ=0 EndX=3.5 EndY=9.2 EndZ=0
    g10: LineSegment StartX=-3.5 StartY=9.2 StartZ=0 EndX=-3.2 EndY=9.2 EndZ=0
    g11: LineSegment StartX=-3.2 StartY=9.2 StartZ=0 EndX=-3.2 EndY=9.5 EndZ=0
    g12: LineSegment StartX=-3.2 StartY=9.5 StartZ=0 EndX=-2.9 EndY=9.5 EndZ=0
    g13: LineSegment StartX=-2.9 StartY=9.5 StartZ=0 EndX=-2.9 EndY=9 EndZ=0
  constraints (41):
    c: Coincident(g1,g2)
    c: Coincident(g4,g1)
    c: Horizontal(g3)
    c: Vertical(g2)
    c: Vertical(g4)
    c: Coincident(g0,g5)
    c: Coincident(g0,g3)
    c: DistanceY(g-1,g0) = 7.5
    c: Radius(g0) = 2
    c: Symmetric(g1,g1,g-2)
    c: Symmetric(g0,g0,g-2)
    c: DistanceY(g1) = 11
    c: DistanceX(g1,g1) = 7
    c: Vertical(g6)
    c: Coincident(g6,g7)
    c: Horizontal(g7)
    c: Coincident(g7,g8)
    c: Vertical(g8)
    c: Coincident(g8,g9)
    c: Coincident(g3,g6)
    c: Coincident(g2,g9)
    c: Horizontal(g10)
    c: Coincident(g10,g11)
    c: Coincident(g11,g12)
    c: Horizontal(g12)
    c: Coincident(g12,g13)
    c: Vertical(g13)
    c: Vertical(g11)
    c: Coincident(g4,g10)
    c: Coincident(g5,g13)
    c: DistanceY(g13,g13) = 0.5
    c: DistanceX(g12,g12) = 0.3
    c: DistanceY(g5,g10) = 0.2
    c: Symmetric(g5,g3,g-2)
    c: DistanceY(g3) = 9
    c: DistanceY(g6) = 9.5
    c: Equal(g7,g12)
    c: Equal(g13,g6)
    c: Horizontal(g9)
    c: Horizontal(g8,g10)
    c: Equal(g12,g10)
FEATURE [PartDesign::Revolution] Revolution036
  Angle = 360
  Axis = (1,0,0)
  Base = (0,0,0)
  Profile = -> Sketch111
  ReferenceAxis = -> X_Axis133
FEATURE [PartDesign::Fillet] Fillet167
  Base = -> Revolution036 [Edge14,Edge15]
  BaseFeature = -> Revolution036
  Radius = 0.3
  SupportTransform = false
FEATURE [PartDesign::Body] Body119  label="Outer Ring005"
  Group = -> [Sketch111,Revolution036,Fillet167]
  Origin = -> Origin137
  Tip = -> Fillet167
FEATURE [Sketcher::SketchObject] Sketch112
  FullyConstrained = true
  MapMode = 5
  Support = -> [XY_Plane134]
  sketch-geometry (14):
    g0: LineSegment StartX=-2.9 StartY=6 StartZ=0 EndX=-1.32288 EndY=6 EndZ=0
    g1: LineSegment StartX=-3.5 StartY=4 StartZ=0 EndX=-3.5 EndY=5.7 EndZ=0
    g2: ArcOfCircle CenterX=1e-16 CenterY=7.5 CenterZ=0 NormalX=0 NormalY=0 NormalZ=1 AngleXU=0 Radius=2 StartAngle=3.98965 EndAngle=5.43512
    g3: LineSegment StartX=1.32288 StartY=6 StartZ=0 EndX=2.9 EndY=6 EndZ=0
    g4: LineSegment StartX=-3.5 StartY=5.7 StartZ=0 EndX=-3.2 EndY=5.7 EndZ=0
    g5: LineSegment StartX=-3.2 StartY=5.7 StartZ=0 EndX=-3.2 EndY=5.5 EndZ=0
    g6: LineSegment StartX=-3.2 StartY=5.5 StartZ=0 EndX=-2.9 EndY=5.5 EndZ=0
    g7: LineSegment StartX=-2.9 StartY=5.5 StartZ=0 EndX=-2.9 EndY=6 EndZ=0
    g8: LineSegment StartX=8.5 StartY=5.7 StartZ=0 EndX=3.2 EndY=5.7 EndZ=0
    g9: LineSegment StartX=3.2 StartY=5.7 StartZ=0 EndX=3.2 EndY=5.5 EndZ=0
    g10: LineSegment StartX=3.2 StartY=5.5 StartZ=0 EndX=2.9 EndY=5.5 EndZ=0
    g11: LineSegment StartX=2.9 StartY=5.5 StartZ=0 EndX=2.9 EndY=6 EndZ=0
    g12: LineSegment StartX=8.5 StartY=4 StartZ=0 EndX=8.5 EndY=5.7 EndZ=0
    g13: LineSegment StartX=-3.5 StartY=4 StartZ=0 EndX=8.5 EndY=4 EndZ=0
  constraints (43):
    c: Horizontal(g0)
    c: Vertical(g1)
    c: DistanceY(g1) = 4
    c: Coincident(g2,g0)
    c: Coincident(g2,g3)
    c: Horizontal(g3)
    c: Radius(g2) = 2
    c: DistanceY(g2) = 7.5
    c: Symmetric(g0,g2,g-2)
    c: Horizontal(g4)
    c: Coincident(g4,g5)
    c: Vertical(g5)
    c: Coincident(g5,g6)
    c: Horizontal(g6)
    c: Coincident(g6,g7)
    c: Vertical(g7)
    c: Horizontal(g8)
    c: Coincident(g8,g9)
    c: Vertical(g9)
    c: Coincident(g9,g10)
    c: Horizontal(g10)
    c: Coincident(g10,g11)
    c: Vertical(g11)
    c: Coincident(g3,g11)
    c: Coincident(g0,g7)
    c: Coincident(g1,g4)
    c: DistanceY(g3) = 6
    c: DistanceY(g6,g0) = 0.5
    c: DistanceX(g4,g4) = 0.3
    c: DistanceX(g6,g6) = 0.3
    c: DistanceY(g5,g4) = 0.2
    c: Vertical(g12)
    c: Equal(g11,g7)
    c: Equal(g5,g9)
    c: DistanceY(g1,g0) = 2
    c: Coincident(g13,g1)
    c: Coincident(g13,g12)
    c: Horizontal(g13)
    c: DistanceX(g13,g13) = 12
    c: DistanceX(g1,g2) = 3.5
    c: Coincident(g8,g12)
    c: DistanceX(g8,g8) = 5.3
    c: Equal(g6,g10)
FEATURE [PartDesign::Revolution] Revolution037
  Angle = 360
  Axis = (1,0,0)
  Base = (0,0,0)
  Profile = -> Sketch112
  ReferenceAxis = -> X_Axis134
FEATURE [PartDesign::Fillet] Fillet168
  Base = -> Revolution037 [Edge13,Edge11]
  BaseFeature = -> Revolution037
  Radius = 0.2
  SupportTransform = false
FEATURE [PartDesign::Body] Body120  label="Inner Ring005"
  Group = -> [Sketch112,Revolution037,Fillet168]
  Origin = -> Origin138
  Tip = -> Fillet168
FEATURE [App::DocumentObjectGroup] Group032  label="Rings004"
  Group = -> [Body119,Body120]
FEATURE [Sketcher::SketchObject] Sketch113
  FullyConstrained = true
  MapMode = 5
  Placement = pos=(0,0,0) rot=(1,0,0;1.5708rad)
  Support = -> [XZ_Plane135]
  sketch-geometry (12):
    g0: LineSegment StartX=2.9 StartY=9.5 StartZ=0 EndX=2.9 EndY=8.5 EndZ=0
    g1: LineSegment StartX=2.9 StartY=8.5 StartZ=0 EndX=3.2 EndY=8.5 EndZ=0
    g2: LineSegment StartX=3.2 StartY=8.5 StartZ=0 EndX=3.2 EndY=6.5 EndZ=0
    g3: LineSegment StartX=3.2 StartY=6.5 StartZ=0 EndX=2.9 EndY=6.5 EndZ=0
    g4: LineSegment StartX=2.9 StartY=6.5 StartZ=0 EndX=2.9 EndY=5.5 EndZ=0
    g5: LineSegment StartX=2.9 StartY=5.5 StartZ=0 EndX=3.2 EndY=5.5 EndZ=0
    g6: LineSegment StartX=3.2 StartY=5.5 StartZ=0 EndX=3.2 EndY=6 EndZ=0
    g7: LineSegment StartX=3.2 StartY=6 StartZ=0 EndX=3.5 EndY=6 EndZ=0
    g8: LineSegment StartX=3.5 StartY=6 StartZ=0 EndX=3.5 EndY=9 EndZ=0
    g9: LineSegment StartX=3.5 StartY=9 StartZ=0 EndX=3.2 EndY=9 EndZ=0
    g10: LineSegment StartX=3.2 StartY=9 StartZ=0 EndX=3.2 EndY=9.5 EndZ=0
    g11: LineSegment StartX=3.2 StartY=9.5 StartZ=0 EndX=2.9 EndY=9.5 EndZ=0
  constraints (36):
    c: Vertical(g0)
    c: Coincident(g0,g1)
    c: Horizontal(g1)
    c: Coincident(g1,g2)
    c: Vertical(g2)
    c: Coincident(g2,g3)
    c: Horizontal(g3)
    c: Coincident(g3,g4)
    c: Vertical(g4)
    c: Coincident(g4,g5)
    c: Horizontal(g5)
    c: Coincident(g5,g6)
    c: Vertical(g6)
    c: Coincident(g6,g7)
    c: Horizontal(g7)
    c: Coincident(g7,g8)
    c: Vertical(g8)
    c: Coincident(g8,g9)
    c: Horizontal(g9)
    c: Coincident(g9,g10)
    c: Vertical(g10)
    c: Coincident(g10,g11)
    c: Coincident(g11,g0)
    c: Horizontal(g11)
    c: DistanceY(g4) = 5.5
    c: DistanceX(g4) = 2.9
    c: DistanceY(g5,g6) = 0.5
    c: DistanceY(g6,g2) = 0.5
    c: DistanceX(g5,g5) = 0.3
    c: Equal(g5,g7)
    c: Equal(g7,g3)
    c: Equal(g3,g1)
    c: Equal(g1,g9)
    c: Equal(g4,g0)
    c: Equal(g6,g10)
    c: DistanceY(g4,g0) = 4
FEATURE [PartDesign::Revolution] Revolution038
  Angle = 360
  Axis = (1,0,0)
  Base = (0,0,0)
  Placement = pos=(0,0,0) rot=(1,0,0;1.5708rad)
  Profile = -> Sketch113
  ReferenceAxis = -> Sketch113 [H_Axis]
FEATURE [PartDesign::Fillet] Fillet169
  Base = -> Revolution038 [Edge14,Edge12]
  BaseFeature = -> Revolution038
  Placement = pos=(0,0,0) rot=(1,0,0;1.5708rad)
  Radius = 0.2
  SupportTransform = false
FEATURE [PartDesign::Body] Body121  label="Seal 009"
  Group = -> [Sketch113,Revolution038,Fillet169]
  Origin = -> Origin139
  Tip = -> Fillet169
FEATURE [PartDesign::FeatureBase] Clone069
  BaseFeature = -> Body121
FEATURE [PartDesign::Body] Body122  label="Seal 010"
  BaseFeature = -> Body121
  Group = -> [Clone069]
  Origin = -> Origin140
  Placement = pos=(0,0,0) rot=(0,1,0;3.14159rad)
  Tip = -> Clone069
FEATURE [App::DocumentObjectGroup] Group031  label="Seals004"
  Group = -> [Body121,Body122]
FEATURE [Sketcher::SketchObject] Sketch114
  AttachmentOffset = pos=(0,0,4) rot=(0,0,1;0rad)
  FullyConstrained = true
  MapMode = 5
  Placement = pos=(0,0,4) rot=(0,0,1;0rad)
  Support = -> [XY_Plane116]
  sketch-geometry (1):
    g0: Circle CenterX=6 CenterY=0 CenterZ=0 NormalX=0 NormalY=0 NormalZ=1 AngleXU=0 Radius=1.5
  constraints (3):
    c: PointOnObject(g0,g-1)
    c: Diameter(g0) = 3
    c: DistanceX(g0,g-3) = 2.5
FEATURE [PartDesign::Pad] Pad022
  Direction = (0,0,1)
  Length = 3
  Length2 = 100
  Profile = -> Sketch114
  Type = 0
FEATURE [Sketcher::SketchObject] Sketch115
  ExternalGeometry = -> [Pad022]
  FullyConstrained = true
  MapMode = 5
  Placement = pos=(0,0,7) rot=(0,0,1;0rad)
  Support = -> [Pad022]
  sketch-geometry (7):
    g0: LineSegment StartX=6.43301 StartY=-0.75 StartZ=0 EndX=6.86603 EndY=-5.43e-14 EndZ=0
    g1: LineSegment StartX=6.86603 StartY=-5.43e-14 StartZ=0 EndX=6.43301 EndY=0.75 EndZ=0
    g2: LineSegment StartX=6.43301 StartY=0.75 StartZ=0 EndX=5.56699 EndY=0.75 EndZ=0
    g3: LineSegment StartX=5.56699 StartY=0.75 StartZ=0 EndX=5.13397 EndY=1.086e-13 EndZ=0
    g4: LineSegment StartX=5.13397 StartY=1.086e-13 StartZ=0 EndX=5.56699 EndY=-0.75 EndZ=0
    g5: LineSegment StartX=5.56699 StartY=-0.75 StartZ=0 EndX=6.43301 EndY=-0.75 EndZ=0
    g6: Circle CenterX=6 CenterY=0 CenterZ=0 NormalX=0 NormalY=0 NormalZ=1 AngleXU=0 Radius=0.866025
  constraints (16):
    c: Coincident(g0,g1)
    c: Coincident(g1,g2)
    c: Coincident(g2,g3)
    c: Coincident(g3,g4)
    c: Coincident(g4,g5)
    c: Coincident(g5,g0)
    c: Equal(g0, g1-g5) x5
    c: PointOnObject(g0,g6)
    c: PointOnObject(g1,g6)
    c: PointOnObject(g2,g6)
    c: PointOnObject(g3,g6)
    c: PointOnObject(g4,g6)
    c: PointOnObject(g5,g6)
    c: Coincident(g6,g-3)
    c: Horizontal(g5)
    c: DistanceY(g4,g2) = 1.5
FEATURE [PartDesign::Pocket] Pocket045
  BaseFeature = -> Pad022
  Length = 1
  Length2 = 100
  Profile = -> Sketch115
  Type = 0
FEATURE [PartDesign::PolarPattern] PolarPattern019
  Angle = 120
  Axis = -> X_Axis116
  BaseFeature = -> Pocket045
  Occurrences = 3
  Originals = -> [Pad022,Pocket045]
FEATURE [PartDesign::Body] Body102
  Group = -> [Sketch114,Pad022,Sketch115,Pocket045,PolarPattern019]
  Origin = -> Origin120
  Tip = -> PolarPattern019
FEATURE [App::DocumentObjectGroup] Group033  label="Set screws004"
  Group = -> [Body102]
FEATURE [Sketcher::SketchObject] Sketch116
  AttachmentOffset = pos=(0,0,-4.1) rot=(0,0,1;0rad)
  FullyConstrained = true
  MapMode = 5
  Placement = pos=(-4.1,9e-16,-9e-16) rot=(0.57735,0.57735,0.57735;2.0944rad)
  Support = -> [YZ_Plane137]
  sketch-geometry (13):
    g0: ArcOfCircle CenterX=0 CenterY=0 CenterZ=0 NormalX=0 NormalY=0 NormalZ=1 AngleXU=0 Radius=13.5 StartAngle=1.12361 EndAngle=2.01799
    g1: ArcOfCircle CenterX=-18.5 CenterY=0 CenterZ=0 NormalX=0 NormalY=0 NormalZ=1 AngleXU=0 Radius=5.5 StartAngle=2.01799 EndAngle=4.2652
    g2: Circle CenterX=-18.5 CenterY=0 CenterZ=0 NormalX=0 NormalY=0 NormalZ=1 AngleXU=0 Radius=2.75
    g3: ArcOfCircle CenterX=18.5 CenterY=0 CenterZ=0 NormalX=0 NormalY=0 NormalZ=1 AngleXU=0 Radius=5.5 StartAngle=5.15958 EndAngle=7.40679
    g4: Circle CenterX=18.5 CenterY=0 CenterZ=0 NormalX=0 NormalY=0 NormalZ=1 AngleXU=0 Radius=2.75
    g5: Circle CenterX=0 CenterY=0 CenterZ=0 NormalX=0 NormalY=0 NormalZ=1 AngleXU=0 Radius=11
    g6: GeomPoint X=-24 Y=0 Z=0
    g7: GeomPoint X=24 Y=0 Z=0
    g8: LineSegment StartX=-20.8784 StartY=4.95916 StartZ=0 EndX=-5.83784 EndY=12.1725 EndZ=0
    g9: LineSegment StartX=-20.8784 StartY=-4.95916 StartZ=0 EndX=-5.83784 EndY=-12.1725 EndZ=0
    g10: LineSegment StartX=5.83784 StartY=-12.1725 StartZ=0 EndX=20.8784 EndY=-4.95916 EndZ=0
    g11: LineSegment StartX=20.8784 StartY=4.95916 StartZ=0 EndX=5.83784 EndY=12.1725 EndZ=0
    g12: ArcOfCircle CenterX=0 CenterY=0 CenterZ=0 NormalX=0 NormalY=0 NormalZ=1 AngleXU=0 Radius=13.5 StartAngle=4.2652 EndAngle=5.15958
  constraints (27):
    c: Coincident(g0,g-1)
    c: PointOnObject(g1,g-1)
    c: Coincident(g2,g1)
    c: Coincident(g4,g3)
    c: Equal(g2,g4)
    c: Equal(g1,g3)
    c: Coincident(g5,g0)
    c: Diameter(g0) = 27
    c: Diameter(g5) = 22
    c: Diameter(g4) = 5.5
    c: Symmetric(g3,g1,g0)
    c: DistanceX(g1,g3) = 37
    c: PointOnObject(g6,g1)
    c: PointOnObject(g7,g3)
    c: PointOnObject(g7,g-1)
    c: PointOnObject(g6,g-1)
    c: DistanceX(g6,g7) = 48
    c: Tangent(g3,g11) = -1.5708
    c: Tangent(g0,g11) = -1.5708
    c: Tangent(g3,g10) = -1.5708
    c: Tangent(g1,g9) = -1.5708
    c: Equal(g0,g12)
    c: Tangent(g12,g9) = -1.5708
    c: Coincident(g0,g12)
    c: Tangent(g0,g8) = 1.5708
    c: Tangent(g1,g8) = 1.5708
    c: Tangent(g12,g10) = -1.5708
FEATURE [PartDesign::Pad] Pad023
  Direction = (1,-2e-16,3e-16)
  Length = 3.3
  Length2 = 100
  Placement = pos=(0,0,0) rot=(0.57735,0.57735,0.57735;2.0944rad)
  Profile = -> Sketch116
  Type = 0
FEATURE [Sketcher::SketchObject] Sketch117
  ExternalGeometry = -> [Pad023]
  FullyConstrained = true
  MapMode = 5
  Placement = pos=(-4.1,9e-16,-1e-15) rot=(0.57735,0.57735,-0.57735;4.18879rad)
  Support = -> [Pad023]
  sketch-geometry (12):
    g0: ArcOfCircle CenterX=0 CenterY=0 CenterZ=0 NormalX=0 NormalY=0 NormalZ=1 AngleXU=0 Radius=12.3 StartAngle=4.2652 EndAngle=5.15958
    g1: ArcOfCircle CenterX=-18.5 CenterY=-1.04e-14 CenterZ=0 NormalX=0 NormalY=0 NormalZ=1 AngleXU=0 Radius=4.55 StartAngle=4.98418 EndAngle=7.58219
    g2: ArcOfCircle CenterX=18.5 CenterY=1.02e-14 CenterZ=0 NormalX=0 NormalY=0 NormalZ=1 AngleXU=0 Radius=4.55 StartAngle=1.84259 EndAngle=4.44059
    g3: LineSegment StartX=-17.3605 StartY=5.31545 StartZ=0 EndX=-5.31892 EndY=11.0905 EndZ=0
    g4: LineSegment StartX=-17.3605 StartY=-5.31545 StartZ=0 EndX=-5.31892 EndY=-11.0905 EndZ=0
    g5: LineSegment StartX=5.31892 StartY=-11.0905 StartZ=0 EndX=17.3605 EndY=-5.31545 EndZ=0
    g6: LineSegment StartX=17.3605 StartY=5.31545 StartZ=0 EndX=5.31892 EndY=11.0905 EndZ=0
    g7: ArcOfCircle CenterX=0 CenterY=0 CenterZ=0 NormalX=0 NormalY=0 NormalZ=1 AngleXU=0 Radius=12.3 StartAngle=1.12361 EndAngle=2.01799
    g8: ArcOfCircle CenterX=-17.1443 CenterY=4.86462 CenterZ=0 NormalX=0 NormalY=0 NormalZ=1 AngleXU=0 Radius=0.5 StartAngle=2.01799 EndAngle=4.44059
    g9: ArcOfCircle CenterX=-17.1443 CenterY=-4.86462 CenterZ=0 NormalX=0 NormalY=0 NormalZ=1 AngleXU=0 Radius=0.5 StartAngle=1.84259 EndAngle=4.2652
    g10: ArcOfCircle CenterX=17.1443 CenterY=-4.86462 CenterZ=0 NormalX=0 NormalY=0 NormalZ=1 AngleXU=0 Radius=0.5 StartAngle=5.15958 EndAngle=7.58219
    g11: ArcOfCircle CenterX=17.1443 CenterY=4.86462 CenterZ=0 NormalX=0 NormalY=0 NormalZ=1 AngleXU=0 Radius=0.5 StartAngle=4.98418 EndAngle=7.40679
  constraints (30):
    c: Coincident(g0,g-1)
    c: Coincident(g1,g-3)
    c: Coincident(g2,g-4)
    c: Equal(g2,g1)
    c: Parallel(g3,g-5)
    c: Distance(g3,g-5) = 1.2
    c: Coincident(g7,g3) = 1.5708
    c: Tangent(g0,g4) = -1.5708
    c: Equal(g0,g7)
    c: Tangent(g0,g5) = -1.5708
    c: Tangent(g7,g6) = -1.5708
    c: Coincident(g0,g7)
    c: Vertical(g0,g3)
    c: Tangent(g1,g8) = 1.5708
    c: Tangent(g3,g8) = 1.5708
    c: Tangent(g4,g9) = -1.5708
    c: Tangent(g1,g9) = 1.5708
    c: Tangent(g2,g10) = 1.5708
    c: Tangent(g5,g10) = -1.5708
    c: Tangent(g6,g11) = -1.5708
    c: Tangent(g2,g11) = 1.5708
    c: Equal(g8,g9)
    c: Equal(g9,g10)
    c: Equal(g10,g11)
    c: Parallel(g-6,g6)
    c: Parallel(g5,g3)
    c: Parallel(g4,g6)
    c: Radius(g-4) = 2.75
    c: Radius(g2) = 4.55
    c: Radius(g11) = 0.5
FEATURE [PartDesign::Pocket] Pocket046
  BaseFeature = -> Pad023
  Length = 0.6
  Length2 = 100
  Placement = pos=(0,0,0) rot=(0.57735,0.57735,0.57735;2.0944rad)
  Profile = -> Sketch117
  Type = 0
FEATURE [Sketcher::SketchObject] Sketch118
  ExternalGeometry = -> [Pocket046]
  FullyConstrained = true
  MapMode = 5
  Placement = pos=(-0.8,2e-16,-2e-16) rot=(0.57735,0.57735,0.57735;2.0944rad)
  Support = -> [Pocket046]
  sketch-geometry (7):
    g0: Circle CenterX=-18.5 CenterY=1.66e-14 CenterZ=0 NormalX=0 NormalY=0 NormalZ=1 AngleXU=0 Radius=2.75
    g1: LineSegment StartX=-20.8784 StartY=4.95916 StartZ=0 EndX=-14.8432 EndY=7.85358 EndZ=0
    g2: LineSegment StartX=-20.8784 StartY=-4.95916 StartZ=0 EndX=-14.8432 EndY=-7.85358 EndZ=0
    g3: ArcOfCircle CenterX=-18.5 CenterY=1.66e-14 CenterZ=0 NormalX=0 NormalY=0 NormalZ=1 AngleXU=0 Radius=5.5 StartAngle=2.01799 EndAngle=4.2652
    g4: ArcOfCircle CenterX=0 CenterY=0 CenterZ=0 NormalX=0 NormalY=0 NormalZ=1 AngleXU=0 Radius=15 StartAngle=2.69212 EndAngle=3.59107
    g5: ArcOfCircle CenterX=-14.4108 CenterY=6.95191 CenterZ=0 NormalX=0 NormalY=0 NormalZ=1 AngleXU=0 Radius=1 StartAngle=5.83371 EndAngle=8.30117
    g6: ArcOfCircle CenterX=-14.4108 CenterY=-6.95191 CenterZ=0 NormalX=0 NormalY=0 NormalZ=1 AngleXU=0 Radius=1 StartAngle=4.2652 EndAngle=6.73266
  constraints (17):
    c: Coincident(g0,g-6)
    c: Equal(g-5,g0)
    c: Coincident(g1,g-6)
    c: Coincident(g2,g-6)
    c: Coincident(g3,g0)
    c: Coincident(g3,g1)
    c: Coincident(g3,g2)
    c: Coincident(g4,g-1)
    c: Radius(g4) = 15
    c: Tangent(g1,g5) = 1.5708
    c: Tangent(g4,g5) = 1.5708
    c: Tangent(g2,g6) = -1.5708
    c: Tangent(g4,g6) = 1.5708
    c: Radius(g6) = 1
    c: PointOnObject(g2,g-4)
    c: Equal(g5,g6)
    c: PointOnObject(g1,g-3)
FEATURE [PartDesign::Pad] Pad024
  BaseFeature = -> Pocket046
  Direction = (1,-9e-16,6e-16)
  Length = 0.7
  Length2 = 100
  Placement = pos=(0,0,0) rot=(0.57735,0.57735,0.57735;2.0944rad)
  Profile = -> Sketch118
  Type = 0
FEATURE [PartDesign::Mirrored] Mirrored004
  BaseFeature = -> Pad024
  MirrorPlane = -> Sketch118 [V_Axis]
  Originals = -> [Pad024,XZ_Plane137]
  Placement = pos=(0,0,0) rot=(0.57735,0.57735,0.57735;2.0944rad)
FEATURE [Sketcher::SketchObject] Sketch119
  FullyConstrained = true
  MapMode = 5
  Placement = pos=(-0.8,2e-16,-2e-16) rot=(0.57735,0.57735,0.57735;2.0944rad)
  Support = -> [Mirrored004]
  sketch-geometry (2):
    g0: Circle CenterX=0 CenterY=0 CenterZ=0 NormalX=0 NormalY=0 NormalZ=1 AngleXU=0 Radius=11
    g1: Circle CenterX=0 CenterY=0 CenterZ=0 NormalX=0 NormalY=0 NormalZ=1 AngleXU=0 Radius=13.5
  constraints (4):
    c: Coincident(g0,g-1)
    c: Coincident(g1,g0)
    c: Diameter(g1) = 27
    c: Diameter(g0) = 22
FEATURE [PartDesign::Pad] Pad025
  BaseFeature = -> Mirrored004
  Direction = (1,-8e-16,6e-16)
  Length = 4.2
  Length2 = 100
  Placement = pos=(0,0,0) rot=(0.57735,0.57735,0.57735;2.0944rad)
  Profile = -> Sketch119
  Type = 0
FEATURE [Sketcher::SketchObject] Sketch120
  FullyConstrained = true
  MapMode = 5
  Placement = pos=(-3.5,1.5e-15,-1.5e-15) rot=(0.57735,0.57735,-0.57735;4.18879rad)
  Support = -> [Pad025]
  sketch-geometry (13):
    g0: Ellipse CenterX=0 CenterY=0 CenterZ=0 NormalX=0 NormalY=0 NormalZ=1 MajorRadius=15 MinorRadius=6.38796 AngleXU=0
    g1: LineSegment StartX=15 StartY=0 StartZ=0 EndX=-15 EndY=0 EndZ=0
    g2: LineSegment StartX=0 StartY=6.38796 StartZ=0 EndX=0 EndY=-6.38796 EndZ=0
    g3: GeomPoint X=13.5718 Y=0 Z=0
    g4: GeomPoint X=-13.5718 Y=0 Z=0
    g5: ArcOfCircle CenterX=0 CenterY=0 CenterZ=0 NormalX=0 NormalY=0 NormalZ=1 AngleXU=0 Radius=11 StartAngle=2.69004 EndAngle=3.59315
    g6: ArcOfCircle CenterX=0 CenterY=0 CenterZ=0 NormalX=0 NormalY=0 NormalZ=1 AngleXU=0 Radius=11.5 StartAngle=2.73643 EndAngle=3.54676
    g7: ArcOfCircle CenterX=0 CenterY=0 CenterZ=0 NormalX=0 NormalY=0 NormalZ=1 AngleXU=0 Radius=11 StartAngle=5.83163 EndAngle=6.73474
    g8: ArcOfCircle CenterX=0 CenterY=0 CenterZ=0 NormalX=0 NormalY=0 NormalZ=1 AngleXU=0 Radius=11.5 StartAngle=5.87802 EndAngle=6.68835
    g9: LineSegment StartX=10.5689 StartY=4.53296 StartZ=0 EndX=9.89747 EndY=4.8 EndZ=0
    g10: LineSegment StartX=9.89747 StartY=-4.8 StartZ=0 EndX=10.5689 EndY=-4.53296 EndZ=0
    g11: LineSegment StartX=-10.5689 StartY=4.53296 StartZ=0 EndX=-9.89747 EndY=4.8 EndZ=0
    g12: LineSegment StartX=-9.89747 StartY=-4.8 StartZ=0 EndX=-10.5689 EndY=-4.53296 EndZ=0
  constraints (29):
    c: InternalAlignment(g1-g4 -> g0) x4
    c: Coincident(g0,g-1)
    c: Coincident(g5,g0)
    c: PointOnObject(g5,g0)
    c: PointOnObject(g5,g0)
    c: Coincident(g6,g5)
    c: PointOnObject(g6,g0)
    c: PointOnObject(g6,g0)
    c: Coincident(g7,g5)
    c: PointOnObject(g7,g0)
    c: PointOnObject(g7,g0)
    c: Coincident(g8,g5)
    c: PointOnObject(g8,g0)
    c: PointOnObject(g8,g0)
    c: Radius(g7) = 11
    c: Radius(g8) = 11.5
    c: PointOnObject(g1,g-1)
    c: Radius(g5) = 11
    c: Radius(g6) = 11.5
    c: DistanceY(g5,g5) = 9.6
    c: DistanceX(g1) = 15
    c: Coincident(g9,g8)
    c: Coincident(g9,g7)
    c: Coincident(g10,g7)
    c: Coincident(g10,g8)
    c: Coincident(g11,g6)
    c: Coincident(g5,g11)
    c: Coincident(g12,g5)
    c: Coincident(g12,g6)
FEATURE [PartDesign::Pocket] Pocket047
  BaseFeature = -> Pad025
  Length = 3.3
  Length2 = 100
  Placement = pos=(0,0,0) rot=(0.57735,0.57735,0.57735;2.0944rad)
  Profile = -> Sketch120
  Type = 0
FEATURE [PartDesign::Fillet] Fillet166
  Base = -> Pocket047 [Edge13,Edge14,Edge10,Edge6,Edge3,Edge15,Edge17,Edge16,Edge37,Edge104,Edge94]
  BaseFeature = -> Pocket047
  Placement = pos=(0,0,0) rot=(0.57735,0.57735,0.57735;2.0944rad)
  Radius = 0.2
  SupportTransform = false
FEATURE [PartDesign::Body] Body123  label="Case004"
  Group = -> [Sketch116,Pad023,Sketch117,Pocket046,Sketch118,Pad024,Mirrored004,Sketch119,Pad025,Sketch120,Pocket047,Fillet166]
  Origin = -> Origin141
  Tip = -> Fillet166
FEATURE [App::DocumentObjectGroup] Group034  label="Case005"
  Group = -> [Body123]
FEATURE [App::Part] Part018  label="KFL08-001"
  Group = -> [Group028,Body103,Body104,Body105,Body106,Body107,Body108,Body109,Group029,Body110,Body111,Group030,Body112,Body113,Body114,Body115,Body116,Body117,Body118,Group031,Body121,Body122,Group032,Body119,Body120,Group033,Body102,Group034,Body123]
  Origin = -> Origin142
  Placement = pos=(316,120,80) rot=(0,0,1;3.14159rad)
FEATURE [Sketcher::SketchObject] Sketch121
  FullyConstrained = true
  MapMode = 5
  Placement = pos=(0,0,0) rot=(-0.57735,0.57735,0.57735;4.18879rad)
  Support = -> [YZ_Plane146]
  sketch-geometry (1):
    g0: Circle CenterX=0 CenterY=-7.5 CenterZ=0 NormalX=0 NormalY=0 NormalZ=1 AngleXU=0 Radius=0.25
  constraints (3):
    c: PointOnObject(g0,g-2)
    c: DistanceY(g0) = -7.5
    c: Diameter(g0) = 0.5
FEATURE [Sketcher::SketchObject] Sketch122
  FullyConstrained = true
  MapMode = 5
  Support = -> [XY_Plane139]
  sketch-geometry (2):
    g0: LineSegment StartX=0 StartY=5.5 StartZ=0 EndX=6e-16 EndY=9.5 EndZ=0
    g1: ArcOfCircle CenterX=0 CenterY=7.5 CenterZ=0 NormalX=0 NormalY=0 NormalZ=1 AngleXU=0 Radius=2 StartAngle=4.71239 EndAngle=7.85398
  constraints (7):
    c: PointOnObject(g0,g-2)
    c: PointOnObject(g0,g-2)
    c: PointOnObject(g1,g0)
    c: Coincident(g1,g0)
    c: Coincident(g1,g0)
    c: Radius(g1) = 2
    c: DistanceY(g1) = 7.5
FEATURE [PartDesign::Revolution] Revolution039
  Angle = 360
  Axis = (0,1,0)
  Base = (0,0,0)
  Profile = -> Sketch122
  ReferenceAxis = -> Sketch122 [V_Axis]
  Reversed = true
FEATURE [PartDesign::Body] Body125  label="Ball 036"
  Group = -> [Sketch122,Revolution039]
  Origin = -> Origin144
  Tip = -> Revolution039
FEATURE [PartDesign::FeatureBase] Clone070
  BaseFeature = -> Body125
FEATURE [PartDesign::Body] Body126  label="Ball 037"
  BaseFeature = -> Body125
  Group = -> [Clone070]
  Origin = -> Origin145
  Placement = pos=(0,0,0) rot=(-1,0,0;0.897598rad)
  Tip = -> Clone070
FEATURE [PartDesign::FeatureBase] Clone071
  BaseFeature = -> Body125
FEATURE [PartDesign::Body] Body127  label="Ball 038"
  BaseFeature = -> Body125
  Group = -> [Clone071]
  Origin = -> Origin146
  Placement = pos=(0,0,0) rot=(-1,0,0;1.7952rad)
  Tip = -> Clone071
FEATURE [PartDesign::FeatureBase] Clone072
  BaseFeature = -> Body125
FEATURE [PartDesign::Body] Body128  label="Ball 039"
  BaseFeature = -> Body125
  Group = -> [Clone072]
  Origin = -> Origin147
  Placement = pos=(0,0,0) rot=(1,0,0;3.59039rad)
  Tip = -> Clone072
FEATURE [PartDesign::FeatureBase] Clone073
  BaseFeature = -> Body125
FEATURE [PartDesign::Body] Body129  label="Ball 040"
  BaseFeature = -> Body125
  Group = -> [Clone073]
  Origin = -> Origin148
  Placement = pos=(0,0,0) rot=(1,0,0;2.69279rad)
  Tip = -> Clone073
FEATURE [PartDesign::FeatureBase] Clone074
  BaseFeature = -> Body125
FEATURE [PartDesign::Body] Body130  label="Ball 041"
  BaseFeature = -> Body125
  Group = -> [Clone074]
  Origin = -> Origin149
  Placement = pos=(0,0,0) rot=(1,0,0;1.7952rad)
  Tip = -> Clone074
FEATURE [PartDesign::FeatureBase] Clone075
  BaseFeature = -> Body125
FEATURE [PartDesign::Body] Body131  label="Ball 042"
  BaseFeature = -> Body125
  Group = -> [Clone075]
  Origin = -> Origin150
  Placement = pos=(0,0,0) rot=(1,0,0;0.897598rad)
  Tip = -> Clone075
FEATURE [App::DocumentObjectGroup] Group035  label="Balls005"
  Group = -> [Body125,Body126,Body127,Body128,Body129,Body130,Body131]
FEATURE [Sketcher::SketchObject] Sketch123
  FullyConstrained = true
  MapMode = 5
  Support = -> [XY_Plane148]
  sketch-geometry (7):
    g0: LineSegment StartX=-5 StartY=7.5 StartZ=0 EndX=5 EndY=7.5 EndZ=0
    g1: LineSegment StartX=-0.210977 StartY=7.5 StartZ=0 EndX=0.210977 EndY=7.5 EndZ=0
    g2: ArcOfCircle CenterX=0.25 CenterY=7.5 CenterZ=0 NormalX=0 NormalY=0 NormalZ=1 AngleXU=0 Radius=0.460977 StartAngle=2.43297 EndAngle=3.14159
    g3: ArcOfCircle CenterX=-0.25 CenterY=7.5 CenterZ=0 NormalX=0 NormalY=0 NormalZ=1 AngleXU=0 Radius=0.460977 StartAngle=9.792e-13 EndAngle=0.708626
    g4: LineSegment StartX=-0.1 StartY=7.8 StartZ=0 EndX=-0.1 EndY=7.75 EndZ=0
    g5: LineSegment StartX=-0.1 StartY=7.75 StartZ=0 EndX=0.1 EndY=7.75 EndZ=0
    g6: LineSegment StartX=0.1 StartY=7.75 StartZ=0 EndX=0.1 EndY=7.8 EndZ=0
  constraints (22):
    c: DistanceY(g-1,g0) = 7.5
    c: Symmetric(g0,g0,g-2)
    c: DistanceX(g0,g0) = 10
    c: PointOnObject(g1,g0)
    c: PointOnObject(g1,g0)
    c: Coincident(g3,g1)
    c: Coincident(g2,g1)
    c: Coincident(g2,g4)
    c: Coincident(g4,g5)
    c: Horizontal(g5)
    c: Coincident(g5,g6)
    c: Coincident(g6,g3)
    c: Vertical(g6)
    c: Equal(g3,g2)
    c: Vertical(g4)
    c: Symmetric(g2,g3,g-2)
    c: DistanceX(g5,g5) = 0.2
    c: Distance(g5,g1) = 0.25
    c: DistanceX(g3,g-1) = 0.25
    c: PointOnObject(g3,g1)
    c: PointOnObject(g2,g1)
    c: Distance(g3,g1) = 0.3
FEATURE [PartDesign::Revolution] Revolution040
  Angle = 360
  Axis = (10,0,0)
  Base = (-5,7.5,0)
  Profile = -> Sketch123
  ReferenceAxis = -> Sketch123 [Axis]
FEATURE [PartDesign::Body] Body134  label="Rivet 036"
  Group = -> [Sketch123,Revolution040]
  Origin = -> Origin153
  Placement = pos=(0,0,0) rot=(1,0,0;0.448799rad)
  Tip = -> Revolution040
FEATURE [PartDesign::FeatureBase] Clone077
  BaseFeature = -> Body134
  Placement = pos=(0,0,0) rot=(1,0,0;0.448799rad)
FEATURE [PartDesign::Body] Body135  label="Rivet 037"
  BaseFeature = -> Body134
  Group = -> [Clone077]
  Origin = -> Origin154
  Placement = pos=(0,0,0) rot=(1,0,0;0.897598rad)
  Tip = -> Clone077
FEATURE [PartDesign::FeatureBase] Clone078
  BaseFeature = -> Body134
  Placement = pos=(0,0,0) rot=(1,0,0;0.448799rad)
FEATURE [PartDesign::Body] Body136  label="Rivet 038"
  BaseFeature = -> Body134
  Group = -> [Clone078]
  Origin = -> Origin155
  Placement = pos=(0,0,0) rot=(1,0,0;1.7952rad)
  Tip = -> Clone078
FEATURE [PartDesign::FeatureBase] Clone079
  BaseFeature = -> Body134
  Placement = pos=(0,0,0) rot=(1,0,0;0.448799rad)
FEATURE [PartDesign::Body] Body137  label="Rivet 039"
  BaseFeature = -> Body134
  Group = -> [Clone079]
  Origin = -> Origin156
  Placement = pos=(0,0,0) rot=(1,0,0;2.69279rad)
  Tip = -> Clone079
FEATURE [PartDesign::FeatureBase] Clone080
  BaseFeature = -> Body134
  Placement = pos=(0,0,0) rot=(1,0,0;0.448799rad)
FEATURE [PartDesign::Body] Body138  label="Rivet 040"
  BaseFeature = -> Body134
  Group = -> [Clone080]
  Origin = -> Origin157
  Placement = pos=(0,0,0) rot=(1,0,0;3.59039rad)
  Tip = -> Clone080
FEATURE [PartDesign::FeatureBase] Clone081
  BaseFeature = -> Body134
  Placement = pos=(0,0,0) rot=(1,0,0;0.448799rad)
FEATURE [PartDesign::Body] Body139  label="Rivet 041"
  BaseFeature = -> Body134
  Group = -> [Clone081]
  Origin = -> Origin158
  Placement = pos=(0,0,0) rot=(-1,0,0;1.7952rad)
  Tip = -> Clone081
FEATURE [PartDesign::FeatureBase] Clone082
  BaseFeature = -> Body134
  Placement = pos=(0,0,0) rot=(1,0,0;0.448799rad)
FEATURE [PartDesign::Body] Body140  label="Rivet 042"
  BaseFeature = -> Body134
  Group = -> [Clone082]
  Origin = -> Origin159
  Placement = pos=(0,0,0) rot=(-1,0,0;0.897598rad)
  Tip = -> Clone082
FEATURE [App::DocumentObjectGroup] Group037  label="Rivets005"
  Group = -> [Body134,Body135,Body136,Body137,Body138,Body139,Body140]
FEATURE [Sketcher::SketchObject] Sketch124
  FullyConstrained = true
  MapMode = 5
  Placement = pos=(0,0,0) rot=(1,0,0;1.5708rad)
  Support = -> [XZ_Plane146]
  sketch-geometry (4):
    g0: LineSegment StartX=0 StartY=8.5 StartZ=0 EndX=0.1 EndY=8.5 EndZ=0
    g1: LineSegment StartX=0.1 StartY=8.5 StartZ=0 EndX=0.1 EndY=6.5 EndZ=0
    g2: LineSegment StartX=0.1 StartY=6.5 StartZ=0 EndX=0 EndY=6.5 EndZ=0
    g3: LineSegment StartX=0 StartY=6.5 StartZ=0 EndX=0 EndY=8.5 EndZ=0
  constraints (12):
    c: Coincident(g0,g1)
    c: Coincident(g1,g2)
    c: Coincident(g2,g3)
    c: Coincident(g3,g0)
    c: Horizontal(g0)
    c: Horizontal(g2)
    c: Vertical(g1)
    c: Vertical(g3)
    c: PointOnObject(g0,g-2)
    c: DistanceX(g0,g0) = 0.1
    c: DistanceY(g0) = 8.5
    c: DistanceY(g1) = 6.5
FEATURE [PartDesign::Revolution] Revolution041
  Angle = 360
  Axis = (1,0,0)
  Base = (0,0,0)
  Placement = pos=(0,0,0) rot=(1,0,0;1.5708rad)
  Profile = -> Sketch124
  ReferenceAxis = -> Sketch124 [H_Axis]
FEATURE [Sketcher::SketchObject] Sketch125
  FullyConstrained = true
  MapMode = 5
  Placement = pos=(0,0,0) rot=(0.57735,0.57735,0.57735;2.0944rad)
  Support = -> [YZ_Plane146]
  sketch-geometry (5):
    g0: ArcOfCircle CenterX=0 CenterY=7.5 CenterZ=0 NormalX=0 NormalY=0 NormalZ=1 AngleXU=0 Radius=2.11 StartAngle=5.66076 EndAngle=6.65667
    g1: LineSegment StartX=5e-16 StartY=8.5 StartZ=0 EndX=0 EndY=6.26986 EndZ=0
    g2: ArcOfCircle CenterX=0 CenterY=0 CenterZ=0 NormalX=0 NormalY=0 NormalZ=1 AngleXU=0 Radius=6.5 StartAngle=1.3039 EndAngle=1.5708
    g3: LineSegment StartX=1.71431 StartY=6.26986 StartZ=0 EndX=0 EndY=6.26986 EndZ=0
    g4: ArcOfCircle CenterX=0 CenterY=0 CenterZ=0 NormalX=0 NormalY=0 NormalZ=1 AngleXU=0 Radius=8.5 StartAngle=1.33757 EndAngle=1.5708
  constraints (16):
    c: PointOnObject(g0,g-2)
    c: DistanceY(g0) = 7.5
    c: Radius(g0) = 2.11
    c: PointOnObject(g2,g1)
    c: DistanceY(g2) = 6.5
    c: Coincident(g2,g-1)
    c: Coincident(g3,g2)
    c: Horizontal(g3)
    c: Coincident(g0,g2)
    c: Coincident(g1,g3)
    c: PointOnObject(g1,g-2)
    c: PointOnObject(g1,g-2)
    c: Coincident(g4,g-1)
    c: Coincident(g4,g1)
    c: DistanceY(g1) = 8.5
    c: Coincident(g0,g4)
FEATURE [PartDesign::Revolution] Revolution042
  Angle = 180
  Axis = (-2e-16,3e-16,1)
  Base = (0,0,0)
  BaseFeature = -> Revolution041
  Placement = pos=(0,0,0) rot=(1,0,0;1.5708rad)
  Profile = -> Sketch125
  ReferenceAxis = -> Sketch125 [V_Axis]
  Reversed = true
FEATURE [PartDesign::PolarPattern] PolarPattern020
  Angle = 360
  Axis = -> Sketch125 [N_Axis]
  BaseFeature = -> Revolution042
  Occurrences = 3
  Originals = -> [Revolution042]
  Placement = pos=(0,0,0) rot=(1,0,0;1.5708rad)
  Refine = true
FEATURE [Sketcher::SketchObject] Sketch126
  FullyConstrained = true
  MapMode = 5
  Placement = pos=(0,0,0) rot=(0.57735,0.57735,0.57735;2.0944rad)
  Support = -> [YZ_Plane146]
  sketch-geometry (4):
    g0: ArcOfCircle CenterX=0 CenterY=7.5 CenterZ=0 NormalX=0 NormalY=0 NormalZ=1 AngleXU=0 Radius=2.01 StartAngle=5.57985 EndAngle=6.86228
    g1: LineSegment StartX=0 StartY=6.2 StartZ=0 EndX=1.533 EndY=6.2 EndZ=0
    g2: LineSegment StartX=0 StartY=8.6 StartZ=0 EndX=0 EndY=6.2 EndZ=0
    g3: LineSegment StartX=0 StartY=8.6 StartZ=0 EndX=1.68229 EndY=8.6 EndZ=0
  constraints (13):
    c: PointOnObject(g0,g-2)
    c: DistanceY(g0) = 7.5
    c: Radius(g0) = 2.01
    c: PointOnObject(g1,g-2)
    c: Horizontal(g1)
    c: Coincident(g0,g1)
    c: DistanceY(g1) = 6.2
    c: DistanceY(g2) = 8.6
    c: Coincident(g2,g1)
    c: PointOnObject(g2,g-2)
    c: Coincident(g3,g2)
    c: Horizontal(g3)
    c: Coincident(g0,g3)
FEATURE [PartDesign::Groove] Groove005
  Angle = 360
  Axis = (-2e-16,3e-16,1)
  Base = (0,0,0)
  BaseFeature = -> PolarPattern020
  Placement = pos=(0,0,0) rot=(1,0,0;1.5708rad)
  Profile = -> Sketch126
  ReferenceAxis = -> Sketch126 [V_Axis]
FEATURE [PartDesign::PolarPattern] PolarPattern021
  Angle = 360
  Axis = -> Sketch126 [N_Axis]
  BaseFeature = -> Groove005
  Occurrences = 3
  Originals = -> [Groove005]
  Placement = pos=(0,0,0) rot=(1,0,0;1.5708rad)
FEATURE [PartDesign::Pocket] Pocket048
  BaseFeature = -> PolarPattern021
  Length = 5
  Length2 = 100
  Placement = pos=(0,0,0) rot=(1,0,0;1.5708rad)
  Profile = -> Sketch121
  Type = 1
FEATURE [PartDesign::PolarPattern] PolarPattern022
  Angle = 360
  Axis = -> Sketch121 [N_Axis]
  BaseFeature = -> Pocket048
  Occurrences = 3
  Originals = -> [Pocket048]
  Placement = pos=(0,0,0) rot=(1,0,0;1.5708rad)
FEATURE [PartDesign::Body] Body132  label="Cage 011"
  Group = -> [Sketch124,Revolution041,Sketch125,Revolution042,PolarPattern020,Sketch126,Groove005,PolarPattern021,Sketch121,Pocket048,PolarPattern022]
  Origin = -> Origin151
  Placement = pos=(0,0,0) rot=(-1,0,0;1.5708rad)
  Tip = -> PolarPattern022
FEATURE [PartDesign::FeatureBase] Clone076
  BaseFeature = -> Body132
  Placement = pos=(0,0,0) rot=(-1,0,0;1.5708rad)
FEATURE [PartDesign::Body] Body133  label="Cage 012"
  BaseFeature = -> Body132
  Group = -> [Clone076]
  Origin = -> Origin152
  Placement = pos=(0,0,0) rot=(0,1,0;3.14159rad)
  Tip = -> Clone076
FEATURE [App::DocumentObjectGroup] Group036  label="Cages005"
  Group = -> [Body132,Body133]
FEATURE [Sketcher::SketchObject] Sketch127
  FullyConstrained = true
  MapMode = 5
  Support = -> [XY_Plane155]
  sketch-geometry (14):
    g0: ArcOfCircle CenterX=-1e-16 CenterY=7.5 CenterZ=0 NormalX=0 NormalY=0 NormalZ=1 AngleXU=0 Radius=2 StartAngle=0.848062 EndAngle=2.29353
    g1: LineSegment StartX=-3.5 StartY=11 StartZ=0 EndX=3.5 EndY=11 EndZ=0
    g2: LineSegment StartX=3.5 StartY=11 StartZ=0 EndX=3.5 EndY=9.2 EndZ=0
    g3: LineSegment StartX=2.9 StartY=9 StartZ=0 EndX=1.32288 EndY=9 EndZ=0
    g4: LineSegment StartX=-3.5 StartY=9.2 StartZ=0 EndX=-3.5 EndY=11 EndZ=0
    g5: LineSegment StartX=-1.32288 StartY=9 StartZ=0 EndX=-2.9 EndY=9 EndZ=0
    g6: LineSegment StartX=2.9 StartY=9 StartZ=0 EndX=2.9 EndY=9.5 EndZ=0
    g7: LineSegment StartX=2.9 StartY=9.5 StartZ=0 EndX=3.2 EndY=9.5 EndZ=0
    g8: LineSegment StartX=3.2 StartY=9.5 StartZ=0 EndX=3.2 EndY=9.2 EndZ=0
    g9: LineSegment StartX=3.2 StartY=9.2 StartZ=0 EndX=3.5 EndY=9.2 EndZ=0
    g10: LineSegment StartX=-3.5 StartY=9.2 StartZ=0 EndX=-3.2 EndY=9.2 EndZ=0
    g11: LineSegment StartX=-3.2 StartY=9.2 StartZ=0 EndX=-3.2 EndY=9.5 EndZ=0
    g12: LineSegment StartX=-3.2 StartY=9.5 StartZ=0 EndX=-2.9 EndY=9.5 EndZ=0
    g13: LineSegment StartX=-2.9 StartY=9.5 StartZ=0 EndX=-2.9 EndY=9 EndZ=0
  constraints (41):
    c: Coincident(g1,g2)
    c: Coincident(g4,g1)
    c: Horizontal(g3)
    c: Vertical(g2)
    c: Vertical(g4)
    c: Coincident(g0,g5)
    c: Coincident(g0,g3)
    c: DistanceY(g-1,g0) = 7.5
    c: Radius(g0) = 2
    c: Symmetric(g1,g1,g-2)
    c: Symmetric(g0,g0,g-2)
    c: DistanceY(g1) = 11
    c: DistanceX(g1,g1) = 7
    c: Vertical(g6)
    c: Coincident(g6,g7)
    c: Horizontal(g7)
    c: Coincident(g7,g8)
    c: Vertical(g8)
    c: Coincident(g8,g9)
    c: Coincident(g3,g6)
    c: Coincident(g2,g9)
    c: Horizontal(g10)
    c: Coincident(g10,g11)
    c: Coincident(g11,g12)
    c: Horizontal(g12)
    c: Coincident(g12,g13)
    c: Vertical(g13)
    c: Vertical(g11)
    c: Coincident(g4,g10)
    c: Coincident(g5,g13)
    c: DistanceY(g13,g13) = 0.5
    c: DistanceX(g12,g12) = 0.3
    c: DistanceY(g5,g10) = 0.2
    c: Symmetric(g5,g3,g-2)
    c: DistanceY(g3) = 9
    c: DistanceY(g6) = 9.5
    c: Equal(g7,g12)
    c: Equal(g13,g6)
    c: Horizontal(g9)
    c: Horizontal(g8,g10)
    c: Equal(g12,g10)
FEATURE [PartDesign::Revolution] Revolution043
  Angle = 360
  Axis = (1,0,0)
  Base = (0,0,0)
  Profile = -> Sketch127
  ReferenceAxis = -> X_Axis155
FEATURE [PartDesign::Fillet] Fillet171
  Base = -> Revolution043 [Edge14,Edge15]
  BaseFeature = -> Revolution043
  Radius = 0.3
  SupportTransform = false
FEATURE [PartDesign::Body] Body141  label="Outer Ring006"
  Group = -> [Sketch127,Revolution043,Fillet171]
  Origin = -> Origin160
  Tip = -> Fillet171
FEATURE [Sketcher::SketchObject] Sketch128
  FullyConstrained = true
  MapMode = 5
  Support = -> [XY_Plane156]
  sketch-geometry (14):
    g0: LineSegment StartX=-2.9 StartY=6 StartZ=0 EndX=-1.32288 EndY=6 EndZ=0
    g1: LineSegment StartX=-3.5 StartY=4 StartZ=0 EndX=-3.5 EndY=5.7 EndZ=0
    g2: ArcOfCircle CenterX=1e-16 CenterY=7.5 CenterZ=0 NormalX=0 NormalY=0 NormalZ=1 AngleXU=0 Radius=2 StartAngle=3.98965 EndAngle=5.43512
    g3: LineSegment StartX=1.32288 StartY=6 StartZ=0 EndX=2.9 EndY=6 EndZ=0
    g4: LineSegment StartX=-3.5 StartY=5.7 StartZ=0 EndX=-3.2 EndY=5.7 EndZ=0
    g5: LineSegment StartX=-3.2 StartY=5.7 StartZ=0 EndX=-3.2 EndY=5.5 EndZ=0
    g6: LineSegment StartX=-3.2 StartY=5.5 StartZ=0 EndX=-2.9 EndY=5.5 EndZ=0
    g7: LineSegment StartX=-2.9 StartY=5.5 StartZ=0 EndX=-2.9 EndY=6 EndZ=0
    g8: LineSegment StartX=8.5 StartY=5.7 StartZ=0 EndX=3.2 EndY=5.7 EndZ=0
    g9: LineSegment StartX=3.2 StartY=5.7 StartZ=0 EndX=3.2 EndY=5.5 EndZ=0
    g10: LineSegment StartX=3.2 StartY=5.5 StartZ=0 EndX=2.9 EndY=5.5 EndZ=0
    g11: LineSegment StartX=2.9 StartY=5.5 StartZ=0 EndX=2.9 EndY=6 EndZ=0
    g12: LineSegment StartX=8.5 StartY=4 StartZ=0 EndX=8.5 EndY=5.7 EndZ=0
    g13: LineSegment StartX=-3.5 StartY=4 StartZ=0 EndX=8.5 EndY=4 EndZ=0
  constraints (43):
    c: Horizontal(g0)
    c: Vertical(g1)
    c: DistanceY(g1) = 4
    c: Coincident(g2,g0)
    c: Coincident(g2,g3)
    c: Horizontal(g3)
    c: Radius(g2) = 2
    c: DistanceY(g2) = 7.5
    c: Symmetric(g0,g2,g-2)
    c: Horizontal(g4)
    c: Coincident(g4,g5)
    c: Vertical(g5)
    c: Coincident(g5,g6)
    c: Horizontal(g6)
    c: Coincident(g6,g7)
    c: Vertical(g7)
    c: Horizontal(g8)
    c: Coincident(g8,g9)
    c: Vertical(g9)
    c: Coincident(g9,g10)
    c: Horizontal(g10)
    c: Coincident(g10,g11)
    c: Vertical(g11)
    c: Coincident(g3,g11)
    c: Coincident(g0,g7)
    c: Coincident(g1,g4)
    c: DistanceY(g3) = 6
    c: DistanceY(g6,g0) = 0.5
    c: DistanceX(g4,g4) = 0.3
    c: DistanceX(g6,g6) = 0.3
    c: DistanceY(g5,g4) = 0.2
    c: Vertical(g12)
    c: Equal(g11,g7)
    c: Equal(g5,g9)
    c: DistanceY(g1,g0) = 2
    c: Coincident(g13,g1)
    c: Coincident(g13,g12)
    c: Horizontal(g13)
    c: DistanceX(g13,g13) = 12
    c: DistanceX(g1,g2) = 3.5
    c: Coincident(g8,g12)
    c: DistanceX(g8,g8) = 5.3
    c: Equal(g6,g10)
FEATURE [PartDesign::Revolution] Revolution044
  Angle = 360
  Axis = (1,0,0)
  Base = (0,0,0)
  Profile = -> Sketch128
  ReferenceAxis = -> X_Axis156
FEATURE [PartDesign::Fillet] Fillet172
  Base = -> Revolution044 [Edge13,Edge11]
  BaseFeature = -> Revolution044
  Radius = 0.2
  SupportTransform = false
FEATURE [PartDesign::Body] Body142  label="Inner Ring006"
  Group = -> [Sketch128,Revolution044,Fillet172]
  Origin = -> Origin161
  Tip = -> Fillet172
FEATURE [App::DocumentObjectGroup] Group039  label="Rings005"
  Group = -> [Body141,Body142]
FEATURE [Sketcher::SketchObject] Sketch129
  FullyConstrained = true
  MapMode = 5
  Placement = pos=(0,0,0) rot=(1,0,0;1.5708rad)
  Support = -> [XZ_Plane157]
  sketch-geometry (12):
    g0: LineSegment StartX=2.9 StartY=9.5 StartZ=0 EndX=2.9 EndY=8.5 EndZ=0
    g1: LineSegment StartX=2.9 StartY=8.5 StartZ=0 EndX=3.2 EndY=8.5 EndZ=0
    g2: LineSegment StartX=3.2 StartY=8.5 StartZ=0 EndX=3.2 EndY=6.5 EndZ=0
    g3: LineSegment StartX=3.2 StartY=6.5 StartZ=0 EndX=2.9 EndY=6.5 EndZ=0
    g4: LineSegment StartX=2.9 StartY=6.5 StartZ=0 EndX=2.9 EndY=5.5 EndZ=0
    g5: LineSegment StartX=2.9 StartY=5.5 StartZ=0 EndX=3.2 EndY=5.5 EndZ=0
    g6: LineSegment StartX=3.2 StartY=5.5 StartZ=0 EndX=3.2 EndY=6 EndZ=0
    g7: LineSegment StartX=3.2 StartY=6 StartZ=0 EndX=3.5 EndY=6 EndZ=0
    g8: LineSegment StartX=3.5 StartY=6 StartZ=0 EndX=3.5 EndY=9 EndZ=0
    g9: LineSegment StartX=3.5 StartY=9 StartZ=0 EndX=3.2 EndY=9 EndZ=0
    g10: LineSegment StartX=3.2 StartY=9 StartZ=0 EndX=3.2 EndY=9.5 EndZ=0
    g11: LineSegment StartX=3.2 StartY=9.5 StartZ=0 EndX=2.9 EndY=9.5 EndZ=0
  constraints (36):
    c: Vertical(g0)
    c: Coincident(g0,g1)
    c: Horizontal(g1)
    c: Coincident(g1,g2)
    c: Vertical(g2)
    c: Coincident(g2,g3)
    c: Horizontal(g3)
    c: Coincident(g3,g4)
    c: Vertical(g4)
    c: Coincident(g4,g5)
    c: Horizontal(g5)
    c: Coincident(g5,g6)
    c: Vertical(g6)
    c: Coincident(g6,g7)
    c: Horizontal(g7)
    c: Coincident(g7,g8)
    c: Vertical(g8)
    c: Coincident(g8,g9)
    c: Horizontal(g9)
    c: Coincident(g9,g10)
    c: Vertical(g10)
    c: Coincident(g10,g11)
    c: Coincident(g11,g0)
    c: Horizontal(g11)
    c: DistanceY(g4) = 5.5
    c: DistanceX(g4) = 2.9
    c: DistanceY(g5,g6) = 0.5
    c: DistanceY(g6,g2) = 0.5
    c: DistanceX(g5,g5) = 0.3
    c: Equal(g5,g7)
    c: Equal(g7,g3)
    c: Equal(g3,g1)
    c: Equal(g1,g9)
    c: Equal(g4,g0)
    c: Equal(g6,g10)
    c: DistanceY(g4,g0) = 4
FEATURE [PartDesign::Revolution] Revolution045
  Angle = 360
  Axis = (1,0,0)
  Base = (0,0,0)
  Placement = pos=(0,0,0) rot=(1,0,0;1.5708rad)
  Profile = -> Sketch129
  ReferenceAxis = -> Sketch129 [H_Axis]
FEATURE [PartDesign::Fillet] Fillet173
  Base = -> Revolution045 [Edge14,Edge12]
  BaseFeature = -> Revolution045
  Placement = pos=(0,0,0) rot=(1,0,0;1.5708rad)
  Radius = 0.2
  SupportTransform = false
FEATURE [PartDesign::Body] Body143  label="Seal 011"
  Group = -> [Sketch129,Revolution045,Fillet173]
  Origin = -> Origin162
  Tip = -> Fillet173
FEATURE [PartDesign::FeatureBase] Clone083
  BaseFeature = -> Body143
FEATURE [PartDesign::Body] Body144  label="Seal 012"
  BaseFeature = -> Body143
  Group = -> [Clone083]
  Origin = -> Origin163
  Placement = pos=(0,0,0) rot=(0,1,0;3.14159rad)
  Tip = -> Clone083
FEATURE [App::DocumentObjectGroup] Group038  label="Seals005"
  Group = -> [Body143,Body144]
FEATURE [Sketcher::SketchObject] Sketch130
  AttachmentOffset = pos=(0,0,4) rot=(0,0,1;0rad)
  FullyConstrained = true
  MapMode = 5
  Placement = pos=(0,0,4) rot=(0,0,1;0rad)
  Support = -> [XY_Plane138]
  sketch-geometry (1):
    g0: Circle CenterX=6 CenterY=0 CenterZ=0 NormalX=0 NormalY=0 NormalZ=1 AngleXU=0 Radius=1.5
  constraints (3):
    c: PointOnObject(g0,g-1)
    c: Diameter(g0) = 3
    c: DistanceX(g0,g-3) = 2.5
FEATURE [PartDesign::Pad] Pad026
  Direction = (0,0,1)
  Length = 3
  Length2 = 100
  Profile = -> Sketch130
  Type = 0
FEATURE [Sketcher::SketchObject] Sketch131
  ExternalGeometry = -> [Pad026]
  FullyConstrained = true
  MapMode = 5
  Placement = pos=(0,0,7) rot=(0,0,1;0rad)
  Support = -> [Pad026]
  sketch-geometry (7):
    g0: LineSegment StartX=6.43301 StartY=-0.75 StartZ=0 EndX=6.86603 EndY=-5.43e-14 EndZ=0
    g1: LineSegment StartX=6.86603 StartY=-5.43e-14 StartZ=0 EndX=6.43301 EndY=0.75 EndZ=0
    g2: LineSegment StartX=6.43301 StartY=0.75 StartZ=0 EndX=5.56699 EndY=0.75 EndZ=0
    g3: LineSegment StartX=5.56699 StartY=0.75 StartZ=0 EndX=5.13397 EndY=1.086e-13 EndZ=0
    g4: LineSegment StartX=5.13397 StartY=1.086e-13 StartZ=0 EndX=5.56699 EndY=-0.75 EndZ=0
    g5: LineSegment StartX=5.56699 StartY=-0.75 StartZ=0 EndX=6.43301 EndY=-0.75 EndZ=0
    g6: Circle CenterX=6 CenterY=0 CenterZ=0 NormalX=0 NormalY=0 NormalZ=1 AngleXU=0 Radius=0.866025
  constraints (16):
    c: Coincident(g0,g1)
    c: Coincident(g1,g2)
    c: Coincident(g2,g3)
    c: Coincident(g3,g4)
    c: Coincident(g4,g5)
    c: Coincident(g5,g0)
    c: Equal(g0, g1-g5) x5
    c: PointOnObject(g0,g6)
    c: PointOnObject(g1,g6)
    c: PointOnObject(g2,g6)
    c: PointOnObject(g3,g6)
    c: PointOnObject(g4,g6)
    c: PointOnObject(g5,g6)
    c: Coincident(g6,g-3)
    c: Horizontal(g5)
    c: DistanceY(g4,g2) = 1.5
FEATURE [PartDesign::Pocket] Pocket049
  BaseFeature = -> Pad026
  Length = 1
  Length2 = 100
  Profile = -> Sketch131
  Type = 0
FEATURE [PartDesign::PolarPattern] PolarPattern023
  Angle = 120
  Axis = -> X_Axis138
  BaseFeature = -> Pocket049
  Occurrences = 3
  Originals = -> [Pad026,Pocket049]
FEATURE [PartDesign::Body] Body124
  Group = -> [Sketch130,Pad026,Sketch131,Pocket049,PolarPattern023]
  Origin = -> Origin143
  Tip = -> PolarPattern023
FEATURE [App::DocumentObjectGroup] Group040  label="Set screws005"
  Group = -> [Body124]
FEATURE [Sketcher::SketchObject] Sketch132
  AttachmentOffset = pos=(0,0,-4.1) rot=(0,0,1;0rad)
  FullyConstrained = true
  MapMode = 5
  Placement = pos=(-4.1,9e-16,-9e-16) rot=(0.57735,0.57735,0.57735;2.0944rad)
  Support = -> [YZ_Plane159]
  sketch-geometry (13):
    g0: ArcOfCircle CenterX=0 CenterY=0 CenterZ=0 NormalX=0 NormalY=0 NormalZ=1 AngleXU=0 Radius=13.5 StartAngle=1.12361 EndAngle=2.01799
    g1: ArcOfCircle CenterX=-18.5 CenterY=0 CenterZ=0 NormalX=0 NormalY=0 NormalZ=1 AngleXU=0 Radius=5.5 StartAngle=2.01799 EndAngle=4.2652
    g2: Circle CenterX=-18.5 CenterY=0 CenterZ=0 NormalX=0 NormalY=0 NormalZ=1 AngleXU=0 Radius=2.75
    g3: ArcOfCircle CenterX=18.5 CenterY=0 CenterZ=0 NormalX=0 NormalY=0 NormalZ=1 AngleXU=0 Radius=5.5 StartAngle=5.15958 EndAngle=7.40679
    g4: Circle CenterX=18.5 CenterY=0 CenterZ=0 NormalX=0 NormalY=0 NormalZ=1 AngleXU=0 Radius=2.75
    g5: Circle CenterX=0 CenterY=0 CenterZ=0 NormalX=0 NormalY=0 NormalZ=1 AngleXU=0 Radius=11
    g6: GeomPoint X=-24 Y=0 Z=0
    g7: GeomPoint X=24 Y=0 Z=0
    g8: LineSegment StartX=-20.8784 StartY=4.95916 StartZ=0 EndX=-5.83784 EndY=12.1725 EndZ=0
    g9: LineSegment StartX=-20.8784 StartY=-4.95916 StartZ=0 EndX=-5.83784 EndY=-12.1725 EndZ=0
    g10: LineSegment StartX=5.83784 StartY=-12.1725 StartZ=0 EndX=20.8784 EndY=-4.95916 EndZ=0
    g11: LineSegment StartX=20.8784 StartY=4.95916 StartZ=0 EndX=5.83784 EndY=12.1725 EndZ=0
    g12: ArcOfCircle CenterX=0 CenterY=0 CenterZ=0 NormalX=0 NormalY=0 NormalZ=1 AngleXU=0 Radius=13.5 StartAngle=4.2652 EndAngle=5.15958
  constraints (27):
    c: Coincident(g0,g-1)
    c: PointOnObject(g1,g-1)
    c: Coincident(g2,g1)
    c: Coincident(g4,g3)
    c: Equal(g2,g4)
    c: Equal(g1,g3)
    c: Coincident(g5,g0)
    c: Diameter(g0) = 27
    c: Diameter(g5) = 22
    c: Diameter(g4) = 5.5
    c: Symmetric(g3,g1,g0)
    c: DistanceX(g1,g3) = 37
    c: PointOnObject(g6,g1)
    c: PointOnObject(g7,g3)
    c: PointOnObject(g7,g-1)
    c: PointOnObject(g6,g-1)
    c: DistanceX(g6,g7) = 48
    c: Tangent(g3,g11) = -1.5708
    c: Tangent(g0,g11) = -1.5708
    c: Tangent(g3,g10) = -1.5708
    c: Tangent(g1,g9) = -1.5708
    c: Equal(g0,g12)
    c: Tangent(g12,g9) = -1.5708
    c: Coincident(g0,g12)
    c: Tangent(g0,g8) = 1.5708
    c: Tangent(g1,g8) = 1.5708
    c: Tangent(g12,g10) = -1.5708
FEATURE [PartDesign::Pad] Pad027
  Direction = (1,-2e-16,3e-16)
  Length = 3.3
  Length2 = 100
  Placement = pos=(0,0,0) rot=(0.57735,0.57735,0.57735;2.0944rad)
  Profile = -> Sketch132
  Type = 0
FEATURE [Sketcher::SketchObject] Sketch133
  ExternalGeometry = -> [Pad027]
  FullyConstrained = true
  MapMode = 5
  Placement = pos=(-4.1,9e-16,-1e-15) rot=(0.57735,0.57735,-0.57735;4.18879rad)
  Support = -> [Pad027]
  sketch-geometry (12):
    g0: ArcOfCircle CenterX=0 CenterY=0 CenterZ=0 NormalX=0 NormalY=0 NormalZ=1 AngleXU=0 Radius=12.3 StartAngle=4.2652 EndAngle=5.15958
    g1: ArcOfCircle CenterX=-18.5 CenterY=-1.04e-14 CenterZ=0 NormalX=0 NormalY=0 NormalZ=1 AngleXU=0 Radius=4.55 StartAngle=4.98418 EndAngle=7.58219
    g2: ArcOfCircle CenterX=18.5 CenterY=1.02e-14 CenterZ=0 NormalX=0 NormalY=0 NormalZ=1 AngleXU=0 Radius=4.55 StartAngle=1.84259 EndAngle=4.44059
    g3: LineSegment StartX=-17.3605 StartY=5.31545 StartZ=0 EndX=-5.31892 EndY=11.0905 EndZ=0
    g4: LineSegment StartX=-17.3605 StartY=-5.31545 StartZ=0 EndX=-5.31892 EndY=-11.0905 EndZ=0
    g5: LineSegment StartX=5.31892 StartY=-11.0905 StartZ=0 EndX=17.3605 EndY=-5.31545 EndZ=0
    g6: LineSegment StartX=17.3605 StartY=5.31545 StartZ=0 EndX=5.31892 EndY=11.0905 EndZ=0
    g7: ArcOfCircle CenterX=0 CenterY=0 CenterZ=0 NormalX=0 NormalY=0 NormalZ=1 AngleXU=0 Radius=12.3 StartAngle=1.12361 EndAngle=2.01799
    g8: ArcOfCircle CenterX=-17.1443 CenterY=4.86462 CenterZ=0 NormalX=0 NormalY=0 NormalZ=1 AngleXU=0 Radius=0.5 StartAngle=2.01799 EndAngle=4.44059
    g9: ArcOfCircle CenterX=-17.1443 CenterY=-4.86462 CenterZ=0 NormalX=0 NormalY=0 NormalZ=1 AngleXU=0 Radius=0.5 StartAngle=1.84259 EndAngle=4.2652
    g10: ArcOfCircle CenterX=17.1443 CenterY=-4.86462 CenterZ=0 NormalX=0 NormalY=0 NormalZ=1 AngleXU=0 Radius=0.5 StartAngle=5.15958 EndAngle=7.58219
    g11: ArcOfCircle CenterX=17.1443 CenterY=4.86462 CenterZ=0 NormalX=0 NormalY=0 NormalZ=1 AngleXU=0 Radius=0.5 StartAngle=4.98418 EndAngle=7.40679
  constraints (30):
    c: Coincident(g0,g-1)
    c: Coincident(g1,g-3)
    c: Coincident(g2,g-4)
    c: Equal(g2,g1)
    c: Parallel(g3,g-5)
    c: Distance(g3,g-5) = 1.2
    c: Coincident(g7,g3) = 1.5708
    c: Tangent(g0,g4) = -1.5708
    c: Equal(g0,g7)
    c: Tangent(g0,g5) = -1.5708
    c: Tangent(g7,g6) = -1.5708
    c: Coincident(g0,g7)
    c: Vertical(g0,g3)
    c: Tangent(g1,g8) = 1.5708
    c: Tangent(g3,g8) = 1.5708
    c: Tangent(g4,g9) = -1.5708
    c: Tangent(g1,g9) = 1.5708
    c: Tangent(g2,g10) = 1.5708
    c: Tangent(g5,g10) = -1.5708
    c: Tangent(g6,g11) = -1.5708
    c: Tangent(g2,g11) = 1.5708
    c: Equal(g8,g9)
    c: Equal(g9,g10)
    c: Equal(g10,g11)
    c: Parallel(g-6,g6)
    c: Parallel(g5,g3)
    c: Parallel(g4,g6)
    c: Radius(g-4) = 2.75
    c: Radius(g2) = 4.55
    c: Radius(g11) = 0.5
FEATURE [PartDesign::Pocket] Pocket050
  BaseFeature = -> Pad027
  Length = 0.6
  Length2 = 100
  Placement = pos=(0,0,0) rot=(0.57735,0.57735,0.57735;2.0944rad)
  Profile = -> Sketch133
  Type = 0
FEATURE [Sketcher::SketchObject] Sketch134
  ExternalGeometry = -> [Pocket050]
  FullyConstrained = true
  MapMode = 5
  Placement = pos=(-0.8,2e-16,-2e-16) rot=(0.57735,0.57735,0.57735;2.0944rad)
  Support = -> [Pocket050]
  sketch-geometry (7):
    g0: Circle CenterX=-18.5 CenterY=1.66e-14 CenterZ=0 NormalX=0 NormalY=0 NormalZ=1 AngleXU=0 Radius=2.75
    g1: LineSegment StartX=-20.8784 StartY=4.95916 StartZ=0 EndX=-14.8432 EndY=7.85358 EndZ=0
    g2: LineSegment StartX=-20.8784 StartY=-4.95916 StartZ=0 EndX=-14.8432 EndY=-7.85358 EndZ=0
    g3: ArcOfCircle CenterX=-18.5 CenterY=1.66e-14 CenterZ=0 NormalX=0 NormalY=0 NormalZ=1 AngleXU=0 Radius=5.5 StartAngle=2.01799 EndAngle=4.2652
    g4: ArcOfCircle CenterX=0 CenterY=0 CenterZ=0 NormalX=0 NormalY=0 NormalZ=1 AngleXU=0 Radius=15 StartAngle=2.69212 EndAngle=3.59107
    g5: ArcOfCircle CenterX=-14.4108 CenterY=6.95191 CenterZ=0 NormalX=0 NormalY=0 NormalZ=1 AngleXU=0 Radius=1 StartAngle=5.83371 EndAngle=8.30117
    g6: ArcOfCircle CenterX=-14.4108 CenterY=-6.95191 CenterZ=0 NormalX=0 NormalY=0 NormalZ=1 AngleXU=0 Radius=1 StartAngle=4.2652 EndAngle=6.73266
  constraints (17):
    c: Coincident(g0,g-6)
    c: Equal(g-5,g0)
    c: Coincident(g1,g-6)
    c: Coincident(g2,g-6)
    c: Coincident(g3,g0)
    c: Coincident(g3,g1)
    c: Coincident(g3,g2)
    c: Coincident(g4,g-1)
    c: Radius(g4) = 15
    c: Tangent(g1,g5) = 1.5708
    c: Tangent(g4,g5) = 1.5708
    c: Tangent(g2,g6) = -1.5708
    c: Tangent(g4,g6) = 1.5708
    c: Radius(g6) = 1
    c: PointOnObject(g2,g-4)
    c: Equal(g5,g6)
    c: PointOnObject(g1,g-3)
FEATURE [PartDesign::Pad] Pad028
  BaseFeature = -> Pocket050
  Direction = (1,-9e-16,6e-16)
  Length = 0.7
  Length2 = 100
  Placement = pos=(0,0,0) rot=(0.57735,0.57735,0.57735;2.0944rad)
  Profile = -> Sketch134
  Type = 0
FEATURE [PartDesign::Mirrored] Mirrored005
  BaseFeature = -> Pad028
  MirrorPlane = -> Sketch134 [V_Axis]
  Originals = -> [Pad028,XZ_Plane159]
  Placement = pos=(0,0,0) rot=(0.57735,0.57735,0.57735;2.0944rad)
FEATURE [Sketcher::SketchObject] Sketch135
  FullyConstrained = true
  MapMode = 5
  Placement = pos=(-0.8,2e-16,-2e-16) rot=(0.57735,0.57735,0.57735;2.0944rad)
  Support = -> [Mirrored005]
  sketch-geometry (2):
    g0: Circle CenterX=0 CenterY=0 CenterZ=0 NormalX=0 NormalY=0 NormalZ=1 AngleXU=0 Radius=11
    g1: Circle CenterX=0 CenterY=0 CenterZ=0 NormalX=0 NormalY=0 NormalZ=1 AngleXU=0 Radius=13.5
  constraints (4):
    c: Coincident(g0,g-1)
    c: Coincident(g1,g0)
    c: Diameter(g1) = 27
    c: Diameter(g0) = 22
FEATURE [PartDesign::Pad] Pad029
  BaseFeature = -> Mirrored005
  Direction = (1,-8e-16,6e-16)
  Length = 4.2
  Length2 = 100
  Placement = pos=(0,0,0) rot=(0.57735,0.57735,0.57735;2.0944rad)
  Profile = -> Sketch135
  Type = 0
FEATURE [Sketcher::SketchObject] Sketch136
  FullyConstrained = true
  MapMode = 5
  Placement = pos=(-3.5,1.5e-15,-1.5e-15) rot=(0.57735,0.57735,-0.57735;4.18879rad)
  Support = -> [Pad029]
  sketch-geometry (13):
    g0: Ellipse CenterX=0 CenterY=0 CenterZ=0 NormalX=0 NormalY=0 NormalZ=1 MajorRadius=15 MinorRadius=6.38796 AngleXU=0
    g1: LineSegment StartX=15 StartY=0 StartZ=0 EndX=-15 EndY=0 EndZ=0
    g2: LineSegment StartX=0 StartY=6.38796 StartZ=0 EndX=0 EndY=-6.38796 EndZ=0
    g3: GeomPoint X=13.5718 Y=0 Z=0
    g4: GeomPoint X=-13.5718 Y=0 Z=0
    g5: ArcOfCircle CenterX=0 CenterY=0 CenterZ=0 NormalX=0 NormalY=0 NormalZ=1 AngleXU=0 Radius=11 StartAngle=2.69004 EndAngle=3.59315
    g6: ArcOfCircle CenterX=0 CenterY=0 CenterZ=0 NormalX=0 NormalY=0 NormalZ=1 AngleXU=0 Radius=11.5 StartAngle=2.73643 EndAngle=3.54676
    g7: ArcOfCircle CenterX=0 CenterY=0 CenterZ=0 NormalX=0 NormalY=0 NormalZ=1 AngleXU=0 Radius=11 StartAngle=5.83163 EndAngle=6.73474
    g8: ArcOfCircle CenterX=0 CenterY=0 CenterZ=0 NormalX=0 NormalY=0 NormalZ=1 AngleXU=0 Radius=11.5 StartAngle=5.87802 EndAngle=6.68835
    g9: LineSegment StartX=10.5689 StartY=4.53296 StartZ=0 EndX=9.89747 EndY=4.8 EndZ=0
    g10: LineSegment StartX=9.89747 StartY=-4.8 StartZ=0 EndX=10.5689 EndY=-4.53296 EndZ=0
    g11: LineSegment StartX=-10.5689 StartY=4.53296 StartZ=0 EndX=-9.89747 EndY=4.8 EndZ=0
    g12: LineSegment StartX=-9.89747 StartY=-4.8 StartZ=0 EndX=-10.5689 EndY=-4.53296 EndZ=0
  constraints (29):
    c: InternalAlignment(g1-g4 -> g0) x4
    c: Coincident(g0,g-1)
    c: Coincident(g5,g0)
    c: PointOnObject(g5,g0)
    c: PointOnObject(g5,g0)
    c: Coincident(g6,g5)
    c: PointOnObject(g6,g0)
    c: PointOnObject(g6,g0)
    c: Coincident(g7,g5)
    c: PointOnObject(g7,g0)
    c: PointOnObject(g7,g0)
    c: Coincident(g8,g5)
    c: PointOnObject(g8,g0)
    c: PointOnObject(g8,g0)
    c: Radius(g7) = 11
    c: Radius(g8) = 11.5
    c: PointOnObject(g1,g-1)
    c: Radius(g5) = 11
    c: Radius(g6) = 11.5
    c: DistanceY(g5,g5) = 9.6
    c: DistanceX(g1) = 15
    c: Coincident(g9,g8)
    c: Coincident(g9,g7)
    c: Coincident(g10,g7)
    c: Coincident(g10,g8)
    c: Coincident(g11,g6)
    c: Coincident(g5,g11)
    c: Coincident(g12,g5)
    c: Coincident(g12,g6)
FEATURE [PartDesign::Pocket] Pocket051
  BaseFeature = -> Pad029
  Length = 3.3
  Length2 = 100
  Placement = pos=(0,0,0) rot=(0.57735,0.57735,0.57735;2.0944rad)
  Profile = -> Sketch136
  Type = 0
FEATURE [PartDesign::Fillet] Fillet170
  Base = -> Pocket051 [Edge13,Edge14,Edge10,Edge6,Edge3,Edge15,Edge17,Edge16,Edge37,Edge104,Edge94]
  BaseFeature = -> Pocket051
  Placement = pos=(0,0,0) rot=(0.57735,0.57735,0.57735;2.0944rad)
  Radius = 0.2
  SupportTransform = false
FEATURE [PartDesign::Body] Body145  label="Case006"
  Group = -> [Sketch132,Pad027,Sketch133,Pocket050,Sketch134,Pad028,Mirrored005,Sketch135,Pad029,Sketch136,Pocket051,Fillet170]
  Origin = -> Origin164
  Tip = -> Fillet170
FEATURE [App::DocumentObjectGroup] Group041  label="Case007"
  Group = -> [Body145]
FEATURE [App::Part] Part019  label="KFL08-002"
  Group = -> [Group035,Body125,Body126,Body127,Body128,Body129,Body130,Body131,Group036,Body132,Body133,Group037,Body134,Body135,Body136,Body137,Body138,Body139,Body140,Group038,Body143,Body144,Group039,Body141,Body142,Group040,Body124,Group041,Body145]
  Origin = -> Origin165
  Placement = pos=(24,120,80) rot=(0,0,1;0rad)
FEATURE [PartDesign::Body] Body150  label="Stator"
  Origin = -> Origin176
FEATURE [Part::FeaturePython] Screw  label="M2.5x25-Screw"  # Fasteners workbench fastener (typed FeaturePython)
  Placement = pos=(15.5,15.5,4) rot=(0,1,0;3.14159rad)
  diameter = 3
  invert = true
  length = 10
  matchOuter = true
  offset = 1
  thread = true
  type = 16
FEATURE [Part::FeaturePython] Screw001  label="M2.5x25-Screw006"  # Fasteners workbench fastener (typed FeaturePython)
  Placement = pos=(-15.5,-15.5,4) rot=(0,1,0;3.14159rad)
  diameter = 3
  invert = true
  length = 10
  matchOuter = true
  offset = 1
  thread = true
  type = 16
FEATURE [Part::FeaturePython] Screw002  label="M2.5x25-Screw005"  # Fasteners workbench fastener (typed FeaturePython)
  Placement = pos=(15.5,-15.5,4) rot=(0,1,0;3.14159rad)
  diameter = 3
  invert = true
  length = 10
  matchOuter = true
  offset = 1
  thread = true
  type = 16
FEATURE [Part::FeaturePython] Screw003  label="M2.5x25-Screw007"  # Fasteners workbench fastener (typed FeaturePython)
  Placement = pos=(-15.5,15.5,4) rot=(0,1,0;3.14159rad)
  diameter = 3
  invert = true
  length = 10
  matchOuter = true
  offset = 1
  thread = true
  type = 16
FEATURE [App::Part] Part025  label="Screw"
  Group = -> [Screw,Screw001,Screw002,Screw003]
  Origin = -> Origin175
FEATURE [Sketcher::SketchObject] Sketch137
  FullyConstrained = false
  MapMode = 5
  Support = -> [XY_Plane161]
  sketch-geometry (4):
    g0: LineSegment StartX=-21.15 StartY=21.15 StartZ=0 EndX=21.15 EndY=21.15 EndZ=0
    g1: LineSegment StartX=21.15 StartY=21.15 StartZ=0 EndX=21.15 EndY=-21.15 EndZ=0
    g2: LineSegment StartX=21.15 StartY=-21.15 StartZ=0 EndX=-21.15 EndY=-21.15 EndZ=0
    g3: LineSegment StartX=-21.15 StartY=-21.15 StartZ=0 EndX=-21.15 EndY=21.15 EndZ=0
  constraints (11):
    c: Coincident(g0,g1)
    c: Coincident(g1,g2)
    c: Coincident(g2,g3)
    c: Coincident(g3,g0)
    c: Horizontal(g0)
    c: Horizontal(g2)
    c: Vertical(g1)
    c: Vertical(g3)
    c: Symmetric(g0,g1,g-1)
    c: DistanceX(g0,g0) = 42.3
    c: Equal(g0,g3)
FEATURE [PartDesign::Pad] Pad030
  AllowMultiFace = false
  Direction = (1,1,1)
  Length = 9.6
  Length2 = 100
  Profile = -> Sketch137
  Refine = true
  Type = 0
FEATURE [Sketcher::SketchObject] Sketch138
  ExternalGeometry = -> [Pad030]
  FullyConstrained = false
  MapMode = 5
  Support = -> [XY_Plane161]
  sketch-geometry (4):
    g0: LineSegment StartX=21.15 StartY=8.2 StartZ=0 EndX=25.45 EndY=8.2 EndZ=0
    g1: LineSegment StartX=25.45 StartY=8.2 StartZ=0 EndX=25.45 EndY=-8.2 EndZ=0
    g2: LineSegment StartX=25.45 StartY=-8.2 StartZ=0 EndX=21.15 EndY=-8.2 EndZ=0
    g3: LineSegment StartX=21.15 StartY=-8.2 StartZ=0 EndX=21.15 EndY=8.2 EndZ=0
  constraints (11):
    c: Coincident(g0,g1)
    c: Coincident(g1,g2)
    c: Coincident(g2,g3)
    c: Coincident(g3,g0)
    c: Horizontal(g0)
    c: Horizontal(g2)
    c: Vertical(g3)
    c: PointOnObject(g0,g-3)
    c: Symmetric(g1,g0,g-1)
    c: DistanceX(g0,g0) = 4.3
    c: DistanceY(g1,g1) = 16.4
FEATURE [PartDesign::Pad] Pad031
  AllowMultiFace = false
  BaseFeature = -> Pad030
  Direction = (1,1,1)
  Length = 3.6
  Length2 = 100
  Profile = -> Sketch138
  Refine = true
  Type = 0
FEATURE [PartDesign::Chamfer] Chamfer004
  Angle = 45
  Base = -> Pad031 [Edge13,Edge5,Edge1,Edge2]
  BaseFeature = -> Pad031
  ChamferType = 0
  FlipDirection = false
  Size = 5
  Size2 = 1
  SupportTransform = false
FEATURE [PartDesign::Fillet] Fillet174
  Base = -> Chamfer004 [Edge33,Edge28,Edge18,Edge3,Edge2,Edge16,Edge30,Edge25]
  BaseFeature = -> Chamfer004
  Radius = 2
  SupportTransform = false
FEATURE [Sketcher::SketchObject] Sketch139
  FullyConstrained = false
  MapMode = 5
  Support = -> [XY_Plane162]
  sketch-geometry (4):
    g0: LineSegment StartX=-21 StartY=21 StartZ=0 EndX=21 EndY=21 EndZ=0
    g1: LineSegment StartX=21 StartY=21 StartZ=0 EndX=21 EndY=-21 EndZ=0
    g2: LineSegment StartX=21 StartY=-21 StartZ=0 EndX=-21 EndY=-21 EndZ=0
    g3: LineSegment StartX=-21 StartY=-21 StartZ=0 EndX=-21 EndY=21 EndZ=0
  constraints (11):
    c: Coincident(g0,g1)
    c: Coincident(g1,g2)
    c: Coincident(g2,g3)
    c: Coincident(g3,g0)
    c: Horizontal(g0)
    c: Horizontal(g2)
    c: Vertical(g1)
    c: Vertical(g3)
    c: DistanceX(g0,g0) = 42
    c: Symmetric(g0,g1,g-1)
    c: Equal(g0,g3)
FEATURE [PartDesign::Pad] Pad032
  AllowMultiFace = false
  Direction = (1,1,1)
  Length = 22.75
  Length2 = 100
  Profile = -> Sketch139
  Refine = true
  Type = 0
FEATURE [PartDesign::Chamfer] Chamfer005
  Angle = 45
  Base = -> Pad032 [Edge8,Edge1,Edge5,Edge2]
  BaseFeature = -> Pad032
  ChamferType = 0
  FlipDirection = false
  Size = 7.5
  Size2 = 1
  SupportTransform = false
FEATURE [Sketcher::SketchObject] Sketch140
  FullyConstrained = false
  MapMode = 5
  Support = -> [XY_Plane163]
  sketch-geometry (4):
    g0: LineSegment StartX=-21.15 StartY=21.15 StartZ=0 EndX=21.15 EndY=21.15 EndZ=0
    g1: LineSegment StartX=21.15 StartY=21.15 StartZ=0 EndX=21.15 EndY=-21.15 EndZ=0
    g2: LineSegment StartX=21.15 StartY=-21.15 StartZ=0 EndX=-21.15 EndY=-21.15 EndZ=0
    g3: LineSegment StartX=-21.15 StartY=-21.15 StartZ=0 EndX=-21.15 EndY=21.15 EndZ=0
  constraints (11):
    c: Coincident(g0,g1)
    c: Coincident(g1,g2)
    c: Coincident(g2,g3)
    c: Coincident(g3,g0)
    c: Horizontal(g0)
    c: Horizontal(g2)
    c: Vertical(g1)
    c: Vertical(g3)
    c: Symmetric(g0,g1,g-1)
    c: DistanceX(g0,g0) = 42.3
    c: Equal(g0,g3)
FEATURE [PartDesign::Pad] Pad033
  AllowMultiFace = false
  Direction = (1,1,1)
  Length = 7.75
  Length2 = 100
  Profile = -> Sketch140
  Refine = true
  Type = 0
FEATURE [PartDesign::Chamfer] Chamfer006
  Angle = 45
  Base = -> Pad033 [Edge8,Edge5,Edge2,Edge1]
  BaseFeature = -> Pad033
  ChamferType = 0
  FlipDirection = false
  Size = 5
  Size2 = 1
  SupportTransform = false
FEATURE [PartDesign::Fillet] Fillet175
  Base = -> Chamfer006 [Edge22,Edge24,Edge23,Edge21,Edge12,Edge2,Edge3,Edge14]
  BaseFeature = -> Chamfer006
  Radius = 2
  SupportTransform = false
FEATURE [Sketcher::SketchObject] Sketch141
  FullyConstrained = false
  MapMode = 5
  Placement = pos=(0,0,0) rot=(1,0,0;3.14159rad)
  Support = -> [Fillet174]
  sketch-geometry (8):
    g0: LineSegment StartX=-15.5 StartY=15.5 StartZ=0 EndX=15.5 EndY=15.5 EndZ=0
    g1: LineSegment StartX=15.5 StartY=15.5 StartZ=0 EndX=15.5 EndY=-15.5 EndZ=0
    g2: LineSegment StartX=15.5 StartY=-15.5 StartZ=0 EndX=-15.5 EndY=-15.5 EndZ=0
    g3: LineSegment StartX=-15.5 StartY=-15.5 StartZ=0 EndX=-15.5 EndY=15.5 EndZ=0
    g4: Circle CenterX=-15.5 CenterY=15.5 CenterZ=0 NormalX=0 NormalY=0 NormalZ=1 AngleXU=0 Radius=1.225
    g5: Circle CenterX=15.5 CenterY=15.5 CenterZ=0 NormalX=0 NormalY=0 NormalZ=1 AngleXU=0 Radius=1.225
    g6: Circle CenterX=15.5 CenterY=-15.5 CenterZ=0 NormalX=0 NormalY=0 NormalZ=1 AngleXU=0 Radius=1.225
    g7: Circle CenterX=-15.5 CenterY=-15.5 CenterZ=0 NormalX=0 NormalY=0 NormalZ=1 AngleXU=0 Radius=1.225
  constraints (19):
    c: Coincident(g0,g1)
    c: Coincident(g1,g2)
    c: Coincident(g2,g3)
    c: Coincident(g3,g0)
    c: Horizontal(g0)
    c: Horizontal(g2)
    c: Vertical(g1)
    c: Vertical(g3)
    c: Symmetric(g0,g1,g-1)
    c: DistanceX(g0,g0) = 31
    c: Equal(g3,g0)
    c: Coincident(g4,g0)
    c: Coincident(g5,g0)
    c: Coincident(g6,g1)
    c: Coincident(g7,g2)
    c: Equal(g6,g5)
    c: Equal(g5,g4)
    c: Equal(g4,g7)
    c: Radius(g4) = 1.225
FEATURE [PartDesign::Hole] Hole
  AllowMultiFace = false
  BaseFeature = -> Fillet174
  Depth = 25
  DepthType = 0
  Diameter = 3
  DrillForDepth = false
  DrillPoint = 1
  DrillPointAngle = 118
  HoleCutCountersinkAngle = 90
  HoleCutCustomValues = false
  HoleCutDepth = 5
  HoleCutDiameter = 5
  HoleCutType = 1
  ModelActualThread = false
  Profile = -> Sketch141
  Refine = true
  Tapered = false
  TaperedAngle = 90
  ThreadAngle = 0
  ThreadClass = 0
  ThreadCutOffInner = 0
  ThreadCutOffOuter = 0
  ThreadDirection = 0
  ThreadFit = 0
  ThreadPitch = 0
  ThreadSize = 0
  ThreadType = 0
  Threaded = false
FEATURE [Sketcher::SketchObject] Sketch142
  FullyConstrained = false
  MapMode = 5
  Placement = pos=(0,0,0) rot=(1,0,0;3.14159rad)
  Support = -> [Chamfer005]
  sketch-geometry (8):
    g0: LineSegment StartX=-15.5 StartY=15.5 StartZ=0 EndX=15.5 EndY=15.5 EndZ=0
    g1: LineSegment StartX=15.5 StartY=15.5 StartZ=0 EndX=15.5 EndY=-15.5 EndZ=0
    g2: LineSegment StartX=15.5 StartY=-15.5 StartZ=0 EndX=-15.5 EndY=-15.5 EndZ=0
    g3: LineSegment StartX=-15.5 StartY=-15.5 StartZ=0 EndX=-15.5 EndY=15.5 EndZ=0
    g4: Circle CenterX=-15.5 CenterY=15.5 CenterZ=0 NormalX=0 NormalY=0 NormalZ=1 AngleXU=0 Radius=1.22
    g5: Circle CenterX=15.5 CenterY=15.5 CenterZ=0 NormalX=0 NormalY=0 NormalZ=1 AngleXU=0 Radius=1.22
    g6: Circle CenterX=15.5 CenterY=-15.5 CenterZ=0 NormalX=0 NormalY=0 NormalZ=1 AngleXU=0 Radius=1.22
    g7: Circle CenterX=-15.5 CenterY=-15.5 CenterZ=0 NormalX=0 NormalY=0 NormalZ=1 AngleXU=0 Radius=1.22
  constraints (19):
    c: Coincident(g0,g1)
    c: Coincident(g1,g2)
    c: Coincident(g2,g3)
    c: Coincident(g3,g0)
    c: Horizontal(g0)
    c: Horizontal(g2)
    c: Vertical(g1)
    c: Vertical(g3)
    c: Equal(g0,g3)
    c: Symmetric(g0,g1,g-1)
    c: DistanceX(g0,g0) = 31
    c: Coincident(g4,g0)
    c: Coincident(g5,g0)
    c: Coincident(g6,g1)
    c: Coincident(g7,g2)
    c: Equal(g6,g5)
    c: Equal(g5,g4)
    c: Equal(g4,g7)
    c: Radius(g4) = 1.22
FEATURE [PartDesign::Pocket] Pocket053
  AllowMultiFace = false
  BaseFeature = -> Chamfer005
  Length = 5
  Length2 = 100
  Profile = -> Sketch142
  Refine = true
  Type = 1
FEATURE [Sketcher::SketchObject] Sketch143
  FullyConstrained = false
  MapMode = 5
  Placement = pos=(0,0,7.75) rot=(0,0,1;0rad)
  Support = -> [Fillet175]
  sketch-geometry (8):
    g0: LineSegment StartX=-15.5 StartY=15.5 StartZ=0 EndX=15.5 EndY=15.5 EndZ=0
    g1: LineSegment StartX=15.5 StartY=15.5 StartZ=0 EndX=15.5 EndY=-15.5 EndZ=0
    g2: LineSegment StartX=15.5 StartY=-15.5 StartZ=0 EndX=-15.5 EndY=-15.5 EndZ=0
    g3: LineSegment StartX=-15.5 StartY=-15.5 StartZ=0 EndX=-15.5 EndY=15.5 EndZ=0
    g4: Circle CenterX=-15.5 CenterY=15.5 CenterZ=0 NormalX=0 NormalY=0 NormalZ=1 AngleXU=0 Radius=1.225
    g5: Circle CenterX=15.5 CenterY=15.5 CenterZ=0 NormalX=0 NormalY=0 NormalZ=1 AngleXU=0 Radius=1.225
    g6: Circle CenterX=15.5 CenterY=-15.5 CenterZ=0 NormalX=0 NormalY=0 NormalZ=1 AngleXU=0 Radius=1.225
    g7: Circle CenterX=-15.5 CenterY=-15.5 CenterZ=0 NormalX=0 NormalY=0 NormalZ=1 AngleXU=0 Radius=1.225
  constraints (19):
    c: Coincident(g0,g1)
    c: Coincident(g1,g2)
    c: Coincident(g2,g3)
    c: Coincident(g3,g0)
    c: Horizontal(g0)
    c: Horizontal(g2)
    c: Vertical(g1)
    c: Vertical(g3)
    c: Equal(g0,g3)
    c: Symmetric(g0,g1,g-1)
    c: DistanceX(g0,g0) = 31
    c: Coincident(g4,g0)
    c: Coincident(g7,g2)
    c: Coincident(g0,g5)
    c: Coincident(g1,g6)
    c: Equal(g7,g4)
    c: Equal(g4,g5)
    c: Equal(g5,g6)
    c: Radius(g4) = 1.225
FEATURE [PartDesign::Pocket] Pocket054
  AllowMultiFace = false
  BaseFeature = -> Fillet175
  Length = 5
  Length2 = 100
  Profile = -> Sketch143
  Refine = true
  Type = 1
FEATURE [Sketcher::SketchObject] Sketch144
  FullyConstrained = false
  MapMode = 5
  Placement = pos=(0,0,7.75) rot=(0,0,1;0rad)
  Support = -> [Pocket054]
  sketch-geometry (1):
    g0: Circle CenterX=0 CenterY=0 CenterZ=0 NormalX=0 NormalY=0 NormalZ=1 AngleXU=0 Radius=14
  constraints (2):
    c: Coincident(g0,g-1)
    c: Radius(g0) = 14
FEATURE [PartDesign::Pocket] Pocket055
  AllowMultiFace = false
  BaseFeature = -> Pocket054
  Length = 1
  Length2 = 100
  Profile = -> Sketch144
  Refine = true
  Type = 0
FEATURE [Sketcher::SketchObject] Sketch145
  FullyConstrained = false
  MapMode = 5
  Placement = pos=(0,0,6.75) rot=(0,0,1;0rad)
  Support = -> [Pocket055]
  sketch-geometry (1):
    g0: Circle CenterX=0 CenterY=0 CenterZ=0 NormalX=0 NormalY=0 NormalZ=1 AngleXU=0 Radius=11
  constraints (2):
    c: Coincident(g0,g-1)
    c: Radius(g0) = 11
FEATURE [PartDesign::Pad] Pad034
  AllowMultiFace = false
  BaseFeature = -> Pocket055
  Direction = (1,1,1)
  Length = 3
  Length2 = 100
  Profile = -> Sketch145
  Refine = true
  Type = 0
FEATURE [PartDesign::Draft] Draft
  Angle = 10
  Base = -> Pad034 [Face25]
  BaseFeature = -> Pad034
  NeutralPlane = -> Pad034 [Face24]
  SupportTransform = false
FEATURE [Sketcher::SketchObject] Sketch146
  FullyConstrained = false
  MapMode = 5
  Placement = pos=(0,0,9.75) rot=(0,0,1;0rad)
  Support = -> [Draft]
  sketch-geometry (1):
    g0: Circle CenterX=0 CenterY=0 CenterZ=0 NormalX=0 NormalY=0 NormalZ=1 AngleXU=0 Radius=5
  constraints (2):
    c: Coincident(g0,g-1)
    c: Radius(g0) = 5
FEATURE [PartDesign::Pocket] Pocket056
  AllowMultiFace = false
  BaseFeature = -> Draft
  Length = 8
  Length2 = 100
  Profile = -> Sketch146
  Refine = true
  Type = 1
FEATURE [Sketcher::SketchObject] Sketch147
  FullyConstrained = false
  MapMode = 5
  Support = -> [XY_Plane164]
  sketch-geometry (1):
    g0: Circle CenterX=0 CenterY=0 CenterZ=0 NormalX=0 NormalY=0 NormalZ=1 AngleXU=0 Radius=2.5
  constraints (2):
    c: Coincident(g0,g-1)
    c: Radius(g0) = 2.5
FEATURE [PartDesign::Pad] Pad035
  AllowMultiFace = false
  Direction = (1,1,1)
  Length = 60
  Length2 = 100
  Profile = -> Sketch147
  Refine = true
  Type = 0
FEATURE [Sketcher::SketchObject] Sketch148
  FullyConstrained = false
  MapMode = 5
  Placement = pos=(0,0,60) rot=(0,0,1;0rad)
  Support = -> [Pad035]
  sketch-geometry (4):
    g0: LineSegment StartX=2 StartY=2 StartZ=0 EndX=6 EndY=2 EndZ=0
    g1: LineSegment StartX=6 StartY=2 StartZ=0 EndX=6 EndY=-2 EndZ=0
    g2: LineSegment StartX=6 StartY=-2 StartZ=0 EndX=2 EndY=-2 EndZ=0
    g3: LineSegment StartX=2 StartY=-2 StartZ=0 EndX=2 EndY=2 EndZ=0
  constraints (11):
    c: Coincident(g0,g1)
    c: Coincident(g1,g2)
    c: Coincident(g2,g3)
    c: Coincident(g3,g0)
    c: Horizontal(g0)
    c: Horizontal(g2)
    c: Vertical(g1)
    c: Symmetric(g2,g0,g-1)
    c: DistanceX(g-1,g0) = 2
    c: Equal(g0,g3)
    c: DistanceX(g0,g0) = 4
FEATURE [PartDesign::Pocket] Pocket057
  AllowMultiFace = false
  BaseFeature = -> Pad035
  Length = 16
  Length2 = 100
  Profile = -> Sketch148
  Refine = true
  Type = 0
FEATURE [PartDesign::Chamfer] Chamfer007
  Angle = 45
  Base = -> Pocket057 [Edge3,Edge5,Edge9]
  BaseFeature = -> Pocket057
  ChamferType = 0
  FlipDirection = false
  Size = 0.3
  Size2 = 1
  SupportTransform = false
FEATURE [PartDesign::Body] Body149  label="Rotor"
  Group = -> [Sketch147,Pad035,Sketch148,Pocket057,Chamfer007]
  Origin = -> Origin170
  Placement = pos=(0,0,2) rot=(0,0,1;0rad)
  Tip = -> Chamfer007
FEATURE [App::Part] Part024  label="Rotor001"
  Group = -> [Body149]
  Origin = -> Origin174
FEATURE [Sketcher::SketchObject] Sketch149
  FullyConstrained = false
  MapMode = 5
  Placement = pos=(0,0,22.75) rot=(0,0,1;0rad)
  Support = -> [Pocket053]
  sketch-geometry (1):
    g0: Circle CenterX=0 CenterY=0 CenterZ=0 NormalX=0 NormalY=0 NormalZ=1 AngleXU=0 Radius=18
  constraints (2):
    c: Coincident(g0,g-1)
    c: Radius(g0) = 18
FEATURE [PartDesign::Pocket] Pocket052
  AllowMultiFace = false
  BaseFeature = -> Pocket053
  Length = 5
  Length2 = 100
  Profile = -> Sketch149
  Refine = true
  Type = 1
FEATURE [PartDesign::Body] Body147
  Group = -> [Sketch139,Pad032,Chamfer005,Sketch142,Pocket053,Sketch149,Pocket052]
  Origin = -> Origin168
  Placement = pos=(0,0,9.6) rot=(0,0,1;0rad)
  Tip = -> Pocket052
FEATURE [App::Part] Part022  label="Body148"
  Group = -> [Body147,Body150]
  Origin = -> Origin172
FEATURE [Sketcher::SketchObject] Sketch150
  ExternalGeometry = -> [Hole]
  FullyConstrained = false
  MapMode = 5
  Placement = pos=(21.15,0,0) rot=(0.57735,0.57735,0.57735;2.0944rad)
  Support = -> [Hole]
  sketch-geometry (4):
    g0: LineSegment StartX=-8.2 StartY=3.6 StartZ=0 EndX=8.2 EndY=3.6 EndZ=0
    g1: LineSegment StartX=8.2 StartY=3.6 StartZ=0 EndX=8.2 EndY=9.6 EndZ=0
    g2: LineSegment StartX=8.2 StartY=9.6 StartZ=0 EndX=-8.2 EndY=9.6 EndZ=0
    g3: LineSegment StartX=-8.2 StartY=9.6 StartZ=0 EndX=-8.2 EndY=3.6 EndZ=0
  constraints (10):
    c: Coincident(g0,g1)
    c: Coincident(g1,g2)
    c: Coincident(g2,g3)
    c: Coincident(g3,g0)
    c: Horizontal(g0)
    c: Vertical(g1)
    c: Vertical(g3)
    c: Coincident(g0,g-3)
    c: PointOnObject(g1,g-5)
    c: Symmetric(g2,g1,g-2)
FEATURE [PartDesign::Pocket] Pocket058
  AllowMultiFace = false
  BaseFeature = -> Hole
  Length = 4
  Length2 = 100
  Profile = -> Sketch150
  Refine = true
  Type = 0
FEATURE [PartDesign::Body] Body146  label="Aluminium rear001"
  Group = -> [Sketch137,Pad030,Sketch138,Pad031,Chamfer004,Fillet174,Sketch141,Hole,Sketch150,Pocket058]
  Origin = -> Origin167
  Tip = -> Pocket058
FEATURE [App::Part] Part021  label="Aluminium rear"
  Group = -> [Body146]
  Origin = -> Origin171
FEATURE [Sketcher::SketchObject] Sketch151
  FullyConstrained = false
  MapMode = 5
  Placement = pos=(0,0,0) rot=(0.57735,0.57735,0.57735;2.0944rad)
  Support = -> [YZ_Plane172]
  sketch-geometry (4):
    g0: LineSegment StartX=-7.5 StartY=0 StartZ=0 EndX=7.5 EndY=0 EndZ=0
    g1: LineSegment StartX=7.5 StartY=0 StartZ=0 EndX=7.5 EndY=5 EndZ=0
    g2: LineSegment StartX=7.5 StartY=5 StartZ=0 EndX=-7.5 EndY=5 EndZ=0
    g3: LineSegment StartX=-7.5 StartY=5 StartZ=0 EndX=-7.5 EndY=0 EndZ=0
  constraints (11):
    c: Coincident(g0,g1)
    c: Coincident(g1,g2)
    c: Coincident(g2,g3)
    c: Coincident(g3,g0)
    c: Horizontal(g0)
    c: Horizontal(g2)
    c: Vertical(g1)
    c: Vertical(g3)
    c: Symmetric(g0,g0,g-1)
    c: DistanceX(g0,g0) = 15
    c: DistanceY(g3,g3) = 5
FEATURE [PartDesign::Pad] Pad036
  AllowMultiFace = false
  Direction = (1,1,1)
  Length = 10
  Length2 = 100
  Placement = pos=(0,0,0) rot=(0.57735,0.57735,0.57735;2.0944rad)
  Profile = -> Sketch151
  Refine = true
  Type = 0
FEATURE [Sketcher::SketchObject] Sketch152
  ExternalGeometry = -> [Pad036]
  FullyConstrained = false
  MapMode = 5
  Placement = pos=(10,-2.2e-15,2.2e-15) rot=(0.57735,0.57735,0.57735;2.0944rad)
  Support = -> [Pad036]
  sketch-geometry (8):
    g0: LineSegment StartX=-6.5 StartY=4 StartZ=0 EndX=6.5 EndY=4 EndZ=0
    g1: LineSegment StartX=6.5 StartY=4 StartZ=0 EndX=6.5 EndY=1 EndZ=0
    g2: LineSegment StartX=6.5 StartY=1 StartZ=0 EndX=-6.5 EndY=1 EndZ=0
    g3: LineSegment StartX=-6.5 StartY=1 StartZ=0 EndX=-6.5 EndY=4 EndZ=0
    g4: LineSegment StartX=-6.5 StartY=1 StartZ=0 EndX=-7.5 EndY=1 EndZ=0
    g5: LineSegment StartX=-6.5 StartY=1 StartZ=0 EndX=-6.5 EndY=0 EndZ=0
    g6: LineSegment StartX=6.5 StartY=4 StartZ=0 EndX=6.5 EndY=5 EndZ=0
    g7: LineSegment StartX=6.5 StartY=4 StartZ=0 EndX=7.5 EndY=4 EndZ=0
  constraints (23):
    c: Coincident(g0,g1)
    c: Coincident(g1,g2)
    c: Coincident(g2,g3)
    c: Coincident(g3,g0)
    c: Horizontal(g2)
    c: Vertical(g1)
    c: Vertical(g3)
    c: Symmetric(g0,g0,g-2)
    c: Coincident(g4,g2)
    c: PointOnObject(g4,g-4)
    c: Horizontal(g4)
    c: PointOnObject(g5,g-1)
    c: Vertical(g5)
    c: Coincident(g6,g0)
    c: Coincident(g7,g0)
    c: Horizontal(g7)
    c: Vertical(g6)
    c: PointOnObject(g6,g-5)
    c: Equal(g7,g6)
    c: Equal(g6,g4)
    c: Equal(g4,g5)
    c: DistanceX(g4,g4) = 1
    c: Coincident(g5,g2)
FEATURE [PartDesign::Pocket] Pocket059
  AllowMultiFace = false
  BaseFeature = -> Pad036
  Length = 6
  Length2 = 100
  Placement = pos=(0,0,0) rot=(0.57735,0.57735,0.57735;2.0944rad)
  Profile = -> Sketch152
  Refine = true
  Type = 0
FEATURE [Sketcher::SketchObject] Sketch016
  ExternalGeometry = -> [Pocket059]
  FullyConstrained = false
  MapMode = 5
  Placement = pos=(10,-2.2e-15,2.2e-15) rot=(0.57735,0.57735,0.57735;2.0944rad)
  Support = -> [Pocket059]
  sketch-geometry (4):
    g0: LineSegment StartX=-4 StartY=5 StartZ=0 EndX=4 EndY=5 EndZ=0
    g1: LineSegment StartX=4 StartY=5 StartZ=0 EndX=4 EndY=4 EndZ=0
    g2: LineSegment StartX=4 StartY=4 StartZ=0 EndX=-4 EndY=4 EndZ=0
    g3: LineSegment StartX=-4 StartY=4 StartZ=0 EndX=-4 EndY=5 EndZ=0
  constraints (11):
    c: Coincident(g0,g1)
    c: Coincident(g1,g2)
    c: Coincident(g2,g3)
    c: Coincident(g3,g0)
    c: Horizontal(g0)
    c: Vertical(g1)
    c: Vertical(g3)
    c: PointOnObject(g0,g-3)
    c: PointOnObject(g1,g-4)
    c: Symmetric(g1,g2,g-2)
    c: DistanceX(g0,g0) = 8
FEATURE [PartDesign::Pocket] Pocket060
  AllowMultiFace = false
  BaseFeature = -> Pocket059
  Length = 4.5
  Length2 = 100
  Placement = pos=(0,0,0) rot=(0.57735,0.57735,0.57735;2.0944rad)
  Profile = -> Sketch016
  Refine = true
  Type = 0
FEATURE [Sketcher::SketchObject] Sketch017
  ExternalGeometry = -> [Pocket060]
  FullyConstrained = false
  MapMode = 5
  Placement = pos=(-1.4e-15,2.2e-15,5) rot=(0,0,-1;1.5708rad)
  Support = -> [Pocket060]
  sketch-geometry (11):
    g0: LineSegment StartX=-6.49 StartY=8.99 StartZ=0 EndX=-5.01 EndY=8.99 EndZ=0
    g1: LineSegment StartX=-5.01 StartY=8.99 StartZ=0 EndX=-5.01 EndY=4.5 EndZ=0
    g2: LineSegment StartX=-5.01 StartY=4.5 StartZ=0 EndX=-6.49 EndY=4.5 EndZ=0
    g3: LineSegment StartX=-6.49 StartY=4.5 StartZ=0 EndX=-6.49 EndY=8.99 EndZ=0
    g4: LineSegment StartX=5.01 StartY=8.99 StartZ=0 EndX=6.49 EndY=8.99 EndZ=0
    g5: LineSegment StartX=6.49 StartY=8.99 StartZ=0 EndX=6.49 EndY=4.5 EndZ=0
    g6: LineSegment StartX=6.49 StartY=4.5 StartZ=0 EndX=5.01 EndY=4.5 EndZ=0
    g7: LineSegment StartX=5.01 StartY=4.5 StartZ=0 EndX=5.01 EndY=8.99 EndZ=0
    g8: LineSegment StartX=-7.5 StartY=8.99 StartZ=0 EndX=-6.49 EndY=8.99 EndZ=0
    g9: LineSegment StartX=-6.49 StartY=10 StartZ=0 EndX=-6.49 EndY=8.99 EndZ=0
    g10: LineSegment StartX=-5.01 StartY=8.99 StartZ=0 EndX=-4 EndY=8.99 EndZ=0
  constraints (32):
    c: Coincident(g0,g1)
    c: Coincident(g1,g2)
    c: Coincident(g2,g3)
    c: Coincident(g3,g0)
    c: Horizontal(g0)
    c: Horizontal(g2)
    c: Vertical(g1)
    c: Vertical(g3)
    c: Coincident(g4,g5)
    c: Coincident(g5,g6)
    c: Coincident(g6,g7)
    c: Coincident(g7,g4)
    c: Horizontal(g4)
    c: Horizontal(g6)
    c: Vertical(g5)
    c: Vertical(g7)
    c: DistanceX(g4,g4) = 1.48
    c: Equal(g0,g4)
    c: Equal(g7,g1)
    c: PointOnObject(g8,g-4)
    c: Coincident(g8,g0)
    c: Horizontal(g8)
    c: PointOnObject(g9,g-5)
    c: Coincident(g9,g0)
    c: Vertical(g9)
    c: Coincident(g10,g0)
    c: PointOnObject(g10,g-3)
    c: Horizontal(g10)
    c: Symmetric(g4,g0,g-2)
    c: Equal(g10,g9)
    c: Equal(g9,g8)
    c: DistanceY(g3,g3) = 4.49
FEATURE [PartDesign::Pocket] Pocket061
  AllowMultiFace = false
  BaseFeature = -> Pocket060
  Length = 2
  Length2 = 100
  Placement = pos=(0,0,0) rot=(0.57735,0.57735,0.57735;2.0944rad)
  Profile = -> Sketch017
  Refine = true
  Type = 0
FEATURE [PartDesign::Body] Body151  label="conector"
  Group = -> [Sketch151,Pad036,Sketch152,Pocket059,Sketch016,Pocket060,Sketch017,Pocket061]
  Origin = -> Origin178
  Tip = -> Pocket061
FEATURE [Sketcher::SketchObject] Sketch018
  FullyConstrained = false
  MapMode = 5
  Placement = pos=(0,0,0) rot=(0.57735,0.57735,0.57735;2.0944rad)
  Support = -> [YZ_Plane173]
  sketch-geometry (4):
    g0: LineSegment StartX=-5.5 StartY=1 StartZ=0 EndX=5.5 EndY=1 EndZ=0
    g1: LineSegment StartX=5.5 StartY=1 StartZ=0 EndX=5.5 EndY=0 EndZ=0
    g2: LineSegment StartX=5.5 StartY=0 StartZ=0 EndX=-5.5 EndY=0 EndZ=0
    g3: LineSegment StartX=-5.5 StartY=0 StartZ=0 EndX=-5.5 EndY=1 EndZ=0
  constraints (11):
    c: Coincident(g0,g1)
    c: Coincident(g1,g2)
    c: Coincident(g2,g3)
    c: Coincident(g3,g0)
    c: Horizontal(g0)
    c: Vertical(g1)
    c: Vertical(g3)
    c: PointOnObject(g1,g-1)
    c: DistanceY(g3,g3) = 1
    c: DistanceX(g2,g2) = 11
    c: Symmetric(g1,g2,g-2)
FEATURE [PartDesign::Pad] Pad037
  AllowMultiFace = false
  Direction = (1,1,1)
  Length = 1
  Length2 = 100
  Placement = pos=(0,0,0) rot=(0.57735,0.57735,0.57735;2.0944rad)
  Profile = -> Sketch018
  Refine = true
  Type = 0
FEATURE [Sketcher::SketchObject] Sketch153
  ExternalGeometry = -> [Pad037]
  FullyConstrained = false
  MapMode = 5
  Placement = pos=(-3e-16,4e-16,1) rot=(0,0,-1;1.5708rad)
  Support = -> [Pad037]
  sketch-geometry (7):
    g0: LineSegment StartX=-5.5 StartY=1 StartZ=0 EndX=-4.5 EndY=1 EndZ=0
    g1: LineSegment StartX=-4.5 StartY=1 StartZ=0 EndX=-4.5 EndY=8 EndZ=0
    g2: LineSegment StartX=-4.5 StartY=8 StartZ=0 EndX=-5.5 EndY=8 EndZ=0
    g3: LineSegment StartX=-5.5 StartY=8 StartZ=0 EndX=-5.5 EndY=1 EndZ=0
    g4: LineSegment StartX=-5.5 StartY=8 StartZ=0 EndX=-5.25 EndY=8.7 EndZ=0
    g5: LineSegment StartX=-5.25 StartY=8.7 StartZ=0 EndX=-4.75 EndY=8.7 EndZ=0
    g6: LineSegment StartX=-4.75 StartY=8.7 StartZ=0 EndX=-4.5 EndY=8 EndZ=0
  constraints (19):
    c: Coincident(g0,g1)
    c: Coincident(g1,g2)
    c: Coincident(g2,g3)
    c: Coincident(g3,g0)
    c: Horizontal(g0)
    c: Horizontal(g2)
    c: Vertical(g1)
    c: Vertical(g3)
    c: Coincident(g0,g-3)
    c: Coincident(g2,g4)
    c: Coincident(g4,g5)
    c: Horizontal(g5)
    c: Coincident(g5,g6)
    c: Coincident(g6,g1)
    c: DistanceY(g1,g5) = 0.7
    c: DistanceX(g5,g5) = 0.5
    c: Equal(g6,g4)
    c: DistanceX(g0,g0) = 1
    c: DistanceY(g3,g3) = 7
FEATURE [PartDesign::Pad] Pad038
  AllowMultiFace = false
  BaseFeature = -> Pad037
  Direction = (1,1,1)
  Length = 1
  Length2 = 100
  Placement = pos=(0,0,0) rot=(0.57735,0.57735,0.57735;2.0944rad)
  Profile = -> Sketch153
  Refine = true
  Reversed = true
  Type = 0
FEATURE [PartDesign::LinearPattern] LinearPattern
  BaseFeature = -> Pad038
  Direction = -> Pad038 [Edge10]
  Length = 10
  Occurrences = 3
  Originals = -> [Pad038]
  Placement = pos=(0,0,0) rot=(0.57735,0.57735,0.57735;2.0944rad)
  Refine = true
  Reversed = true
FEATURE [PartDesign::Body] Body152  label="pin"
  Group = -> [Sketch018,Pad037,Sketch153,Pad038,LinearPattern]
  Origin = -> Origin179
  Placement = pos=(0,0,2) rot=(0,0,1;0rad)
  Tip = -> LinearPattern
FEATURE [App::Part] Part026  label="Conector"
  Group = -> [Body151,Body152]
  Origin = -> Origin177
  Placement = pos=(17,0,4) rot=(0,0,1;0rad)
FEATURE [Sketcher::SketchObject] Sketch020
  FullyConstrained = false
  MapMode = 5
  Placement = pos=(0,0,0) rot=(1,0,0;3.14159rad)
  Support = -> [Pocket056]
  sketch-geometry (1):
    g0: Circle CenterX=0 CenterY=0 CenterZ=0 NormalX=0 NormalY=0 NormalZ=1 AngleXU=0 Radius=15.35
  constraints (2):
    c: Coincident(g0,g-1)
    c: Radius(g0) = 15.35
FEATURE [PartDesign::Pocket] Pocket062
  AllowMultiFace = false
  BaseFeature = -> Pocket056
  Length = 5
  Length2 = 100
  Profile = -> Sketch020
  Refine = true
  Type = 0
FEATURE [PartDesign::Body] Body148  label="Aluminum front001"
  Group = -> [Sketch140,Pad033,Chamfer006,Fillet175,Sketch143,Pocket054,Sketch144,Pocket055,Sketch145,Pad034,Draft,Sketch146,Pocket056,Sketch020,Pocket062]
  Origin = -> Origin169
  Placement = pos=(0,0,32.35) rot=(0,0,1;0rad)
  Tip = -> Pocket062
FEATURE [App::Part] Part023  label="Aluminum front"
  Group = -> [Body148]
  Origin = -> Origin173
FEATURE [App::Part] Part020  label="Nema 017-001"
  Group = -> [Part021,Part022,Part023,Part024,Part025,Part026]
  Origin = -> Origin166
  Placement = pos=(440,120,104.3) rot=(0,1,0;-1.5708rad)
FEATURE [PartDesign::Body] Body157  label="Stator001"
  Origin = -> Origin190
FEATURE [Part::FeaturePython] Screw004  label="M2.5x25-Screw008"  # Fasteners workbench fastener (typed FeaturePython)
  Placement = pos=(15.5,15.5,4) rot=(0,1,0;3.14159rad)
  diameter = 3
  invert = true
  length = 10
  matchOuter = true
  offset = 1
  thread = true
  type = 16
FEATURE [Part::FeaturePython] Screw005  label="M2.5x25-Screw009"  # Fasteners workbench fastener (typed FeaturePython)
  Placement = pos=(-15.5,-15.5,4) rot=(0,1,0;3.14159rad)
  diameter = 3
  invert = true
  length = 10
  matchOuter = true
  offset = 1
  thread = true
  type = 16
FEATURE [Part::FeaturePython] Screw006  label="M2.5x25-Screw010"  # Fasteners workbench fastener (typed FeaturePython)
  Placement = pos=(15.5,-15.5,4) rot=(0,1,0;3.14159rad)
  diameter = 3
  invert = true
  length = 10
  matchOuter = true
  offset = 1
  thread = true
  type = 16
FEATURE [Part::FeaturePython] Screw007  label="M2.5x25-Screw011"  # Fasteners workbench fastener (typed FeaturePython)
  Placement = pos=(-15.5,15.5,4) rot=(0,1,0;3.14159rad)
  diameter = 3
  invert = true
  length = 10
  matchOuter = true
  offset = 1
  thread = true
  type = 16
FEATURE [App::Part] Part032  label="Screw001"
  Group = -> [Screw004,Screw005,Screw006,Screw007]
  Origin = -> Origin189
FEATURE [Sketcher::SketchObject] Sketch156
  FullyConstrained = false
  MapMode = 5
  Placement = pos=(0,0,0) rot=(0.57735,0.57735,0.57735;2.0944rad)
  Support = -> [YZ_Plane187]
  sketch-geometry (4):
    g0: LineSegment StartX=-5.5 StartY=1 StartZ=0 EndX=5.5 EndY=1 EndZ=0
    g1: LineSegment StartX=5.5 StartY=1 StartZ=0 EndX=5.5 EndY=0 EndZ=0
    g2: LineSegment StartX=5.5 StartY=0 StartZ=0 EndX=-5.5 EndY=0 EndZ=0
    g3: LineSegment StartX=-5.5 StartY=0 StartZ=0 EndX=-5.5 EndY=1 EndZ=0
  constraints (11):
    c: Coincident(g0,g1)
    c: Coincident(g1,g2)
    c: Coincident(g2,g3)
    c: Coincident(g3,g0)
    c: Horizontal(g0)
    c: Vertical(g1)
    c: Vertical(g3)
    c: PointOnObject(g1,g-1)
    c: DistanceY(g3,g3) = 1
    c: DistanceX(g2,g2) = 11
    c: Symmetric(g1,g2,g-2)
FEATURE [PartDesign::Pad] Pad046
  AllowMultiFace = false
  Direction = (1,1,1)
  Length = 1
  Length2 = 100
  Placement = pos=(0,0,0) rot=(0.57735,0.57735,0.57735;2.0944rad)
  Profile = -> Sketch156
  Refine = true
  Type = 0
FEATURE [Sketcher::SketchObject] Sketch158
  FullyConstrained = false
  MapMode = 5
  Support = -> [XY_Plane175]
  sketch-geometry (4):
    g0: LineSegment StartX=-21.15 StartY=21.15 StartZ=0 EndX=21.15 EndY=21.15 EndZ=0
    g1: LineSegment StartX=21.15 StartY=21.15 StartZ=0 EndX=21.15 EndY=-21.15 EndZ=0
    g2: LineSegment StartX=21.15 StartY=-21.15 StartZ=0 EndX=-21.15 EndY=-21.15 EndZ=0
    g3: LineSegment StartX=-21.15 StartY=-21.15 StartZ=0 EndX=-21.15 EndY=21.15 EndZ=0
  constraints (11):
    c: Coincident(g0,g1)
    c: Coincident(g1,g2)
    c: Coincident(g2,g3)
    c: Coincident(g3,g0)
    c: Horizontal(g0)
    c: Horizontal(g2)
    c: Vertical(g1)
    c: Vertical(g3)
    c: Symmetric(g0,g1,g-1)
    c: DistanceX(g0,g0) = 42.3
    c: Equal(g0,g3)
FEATURE [PartDesign::Pad] Pad039
  AllowMultiFace = false
  Direction = (1,1,1)
  Length = 9.6
  Length2 = 100
  Profile = -> Sketch158
  Refine = true
  Type = 0
FEATURE [Sketcher::SketchObject] Sketch159
  ExternalGeometry = -> [Pad039]
  FullyConstrained = false
  MapMode = 5
  Support = -> [XY_Plane175]
  sketch-geometry (4):
    g0: LineSegment StartX=21.15 StartY=8.2 StartZ=0 EndX=25.45 EndY=8.2 EndZ=0
    g1: LineSegment StartX=25.45 StartY=8.2 StartZ=0 EndX=25.45 EndY=-8.2 EndZ=0
    g2: LineSegment StartX=25.45 StartY=-8.2 StartZ=0 EndX=21.15 EndY=-8.2 EndZ=0
    g3: LineSegment StartX=21.15 StartY=-8.2 StartZ=0 EndX=21.15 EndY=8.2 EndZ=0
  constraints (11):
    c: Coincident(g0,g1)
    c: Coincident(g1,g2)
    c: Coincident(g2,g3)
    c: Coincident(g3,g0)
    c: Horizontal(g0)
    c: Horizontal(g2)
    c: Vertical(g3)
    c: PointOnObject(g0,g-3)
    c: Symmetric(g1,g0,g-1)
    c: DistanceX(g0,g0) = 4.3
    c: DistanceY(g1,g1) = 16.4
FEATURE [PartDesign::Pad] Pad040
  AllowMultiFace = false
  BaseFeature = -> Pad039
  Direction = (1,1,1)
  Length = 3.6
  Length2 = 100
  Profile = -> Sketch159
  Refine = true
  Type = 0
FEATURE [PartDesign::Chamfer] Chamfer008
  Angle = 45
  Base = -> Pad040 [Edge13,Edge5,Edge1,Edge2]
  BaseFeature = -> Pad040
  ChamferType = 0
  FlipDirection = false
  Size = 5
  Size2 = 1
  SupportTransform = false
FEATURE [PartDesign::Fillet] Fillet176
  Base = -> Chamfer008 [Edge33,Edge28,Edge18,Edge3,Edge2,Edge16,Edge30,Edge25]
  BaseFeature = -> Chamfer008
  Radius = 2
  SupportTransform = false
FEATURE [Sketcher::SketchObject] Sketch160
  FullyConstrained = false
  MapMode = 5
  Support = -> [XY_Plane176]
  sketch-geometry (4):
    g0: LineSegment StartX=-21 StartY=21 StartZ=0 EndX=21 EndY=21 EndZ=0
    g1: LineSegment StartX=21 StartY=21 StartZ=0 EndX=21 EndY=-21 EndZ=0
    g2: LineSegment StartX=21 StartY=-21 StartZ=0 EndX=-21 EndY=-21 EndZ=0
    g3: LineSegment StartX=-21 StartY=-21 StartZ=0 EndX=-21 EndY=21 EndZ=0
  constraints (11):
    c: Coincident(g0,g1)
    c: Coincident(g1,g2)
    c: Coincident(g2,g3)
    c: Coincident(g3,g0)
    c: Horizontal(g0)
    c: Horizontal(g2)
    c: Vertical(g1)
    c: Vertical(g3)
    c: DistanceX(g0,g0) = 42
    c: Symmetric(g0,g1,g-1)
    c: Equal(g0,g3)
FEATURE [PartDesign::Pad] Pad041
  AllowMultiFace = false
  Direction = (1,1,1)
  Length = 22.75
  Length2 = 100
  Profile = -> Sketch160
  Refine = true
  Type = 0
FEATURE [PartDesign::Chamfer] Chamfer009
  Angle = 45
  Base = -> Pad041 [Edge8,Edge1,Edge5,Edge2]
  BaseFeature = -> Pad041
  ChamferType = 0
  FlipDirection = false
  Size = 7.5
  Size2 = 1
  SupportTransform = false
FEATURE [Sketcher::SketchObject] Sketch161
  FullyConstrained = false
  MapMode = 5
  Support = -> [XY_Plane177]
  sketch-geometry (4):
    g0: LineSegment StartX=-21.15 StartY=21.15 StartZ=0 EndX=21.15 EndY=21.15 EndZ=0
    g1: LineSegment StartX=21.15 StartY=21.15 StartZ=0 EndX=21.15 EndY=-21.15 EndZ=0
    g2: LineSegment StartX=21.15 StartY=-21.15 StartZ=0 EndX=-21.15 EndY=-21.15 EndZ=0
    g3: LineSegment StartX=-21.15 StartY=-21.15 StartZ=0 EndX=-21.15 EndY=21.15 EndZ=0
  constraints (11):
    c: Coincident(g0,g1)
    c: Coincident(g1,g2)
    c: Coincident(g2,g3)
    c: Coincident(g3,g0)
    c: Horizontal(g0)
    c: Horizontal(g2)
    c: Vertical(g1)
    c: Vertical(g3)
    c: Symmetric(g0,g1,g-1)
    c: DistanceX(g0,g0) = 42.3
    c: Equal(g0,g3)
FEATURE [PartDesign::Pad] Pad042
  AllowMultiFace = false
  Direction = (1,1,1)
  Length = 7.75
  Length2 = 100
  Profile = -> Sketch161
  Refine = true
  Type = 0
FEATURE [PartDesign::Chamfer] Chamfer010
  Angle = 45
  Base = -> Pad042 [Edge8,Edge5,Edge2,Edge1]
  BaseFeature = -> Pad042
  ChamferType = 0
  FlipDirection = false
  Size = 5
  Size2 = 1
  SupportTransform = false
FEATURE [PartDesign::Fillet] Fillet177
  Base = -> Chamfer010 [Edge22,Edge24,Edge23,Edge21,Edge12,Edge2,Edge3,Edge14]
  BaseFeature = -> Chamfer010
  Radius = 2
  SupportTransform = false
FEATURE [Sketcher::SketchObject] Sketch162
  FullyConstrained = false
  MapMode = 5
  Placement = pos=(0,0,0) rot=(1,0,0;3.14159rad)
  Support = -> [Fillet176]
  sketch-geometry (8):
    g0: LineSegment StartX=-15.5 StartY=15.5 StartZ=0 EndX=15.5 EndY=15.5 EndZ=0
    g1: LineSegment StartX=15.5 StartY=15.5 StartZ=0 EndX=15.5 EndY=-15.5 EndZ=0
    g2: LineSegment StartX=15.5 StartY=-15.5 StartZ=0 EndX=-15.5 EndY=-15.5 EndZ=0
    g3: LineSegment StartX=-15.5 StartY=-15.5 StartZ=0 EndX=-15.5 EndY=15.5 EndZ=0
    g4: Circle CenterX=-15.5 CenterY=15.5 CenterZ=0 NormalX=0 NormalY=0 NormalZ=1 AngleXU=0 Radius=1.225
    g5: Circle CenterX=15.5 CenterY=15.5 CenterZ=0 NormalX=0 NormalY=0 NormalZ=1 AngleXU=0 Radius=1.225
    g6: Circle CenterX=15.5 CenterY=-15.5 CenterZ=0 NormalX=0 NormalY=0 NormalZ=1 AngleXU=0 Radius=1.225
    g7: Circle CenterX=-15.5 CenterY=-15.5 CenterZ=0 NormalX=0 NormalY=0 NormalZ=1 AngleXU=0 Radius=1.225
  constraints (19):
    c: Coincident(g0,g1)
    c: Coincident(g1,g2)
    c: Coincident(g2,g3)
    c: Coincident(g3,g0)
    c: Horizontal(g0)
    c: Horizontal(g2)
    c: Vertical(g1)
    c: Vertical(g3)
    c: Symmetric(g0,g1,g-1)
    c: DistanceX(g0,g0) = 31
    c: Equal(g3,g0)
    c: Coincident(g4,g0)
    c: Coincident(g5,g0)
    c: Coincident(g6,g1)
    c: Coincident(g7,g2)
    c: Equal(g6,g5)
    c: Equal(g5,g4)
    c: Equal(g4,g7)
    c: Radius(g4) = 1.225
FEATURE [PartDesign::Hole] Hole001
  AllowMultiFace = false
  BaseFeature = -> Fillet176
  Depth = 25
  DepthType = 0
  Diameter = 3
  DrillForDepth = false
  DrillPoint = 1
  DrillPointAngle = 118
  HoleCutCountersinkAngle = 90
  HoleCutCustomValues = false
  HoleCutDepth = 5
  HoleCutDiameter = 5
  HoleCutType = 1
  ModelActualThread = false
  Profile = -> Sketch162
  Refine = true
  Tapered = false
  TaperedAngle = 90
  ThreadAngle = 0
  ThreadClass = 0
  ThreadCutOffInner = 0
  ThreadCutOffOuter = 0
  ThreadDirection = 0
  ThreadFit = 0
  ThreadPitch = 0
  ThreadSize = 0
  ThreadType = 0
  Threaded = false
FEATURE [Sketcher::SketchObject] Sketch163
  FullyConstrained = false
  MapMode = 5
  Placement = pos=(0,0,0) rot=(1,0,0;3.14159rad)
  Support = -> [Chamfer009]
  sketch-geometry (8):
    g0: LineSegment StartX=-15.5 StartY=15.5 StartZ=0 EndX=15.5 EndY=15.5 EndZ=0
    g1: LineSegment StartX=15.5 StartY=15.5 StartZ=0 EndX=15.5 EndY=-15.5 EndZ=0
    g2: LineSegment StartX=15.5 StartY=-15.5 StartZ=0 EndX=-15.5 EndY=-15.5 EndZ=0
    g3: LineSegment StartX=-15.5 StartY=-15.5 StartZ=0 EndX=-15.5 EndY=15.5 EndZ=0
    g4: Circle CenterX=-15.5 CenterY=15.5 CenterZ=0 NormalX=0 NormalY=0 NormalZ=1 AngleXU=0 Radius=1.22
    g5: Circle CenterX=15.5 CenterY=15.5 CenterZ=0 NormalX=0 NormalY=0 NormalZ=1 AngleXU=0 Radius=1.22
    g6: Circle CenterX=15.5 CenterY=-15.5 CenterZ=0 NormalX=0 NormalY=0 NormalZ=1 AngleXU=0 Radius=1.22
    g7: Circle CenterX=-15.5 CenterY=-15.5 CenterZ=0 NormalX=0 NormalY=0 NormalZ=1 AngleXU=0 Radius=1.22
  constraints (19):
    c: Coincident(g0,g1)
    c: Coincident(g1,g2)
    c: Coincident(g2,g3)
    c: Coincident(g3,g0)
    c: Horizontal(g0)
    c: Horizontal(g2)
    c: Vertical(g1)
    c: Vertical(g3)
    c: Equal(g0,g3)
    c: Symmetric(g0,g1,g-1)
    c: DistanceX(g0,g0) = 31
    c: Coincident(g4,g0)
    c: Coincident(g5,g0)
    c: Coincident(g6,g1)
    c: Coincident(g7,g2)
    c: Equal(g6,g5)
    c: Equal(g5,g4)
    c: Equal(g4,g7)
    c: Radius(g4) = 1.22
FEATURE [PartDesign::Pocket] Pocket064
  AllowMultiFace = false
  BaseFeature = -> Chamfer009
  Length = 5
  Length2 = 100
  Profile = -> Sketch163
  Refine = true
  Type = 1
FEATURE [Sketcher::SketchObject] Sketch164
  FullyConstrained = false
  MapMode = 5
  Placement = pos=(0,0,7.75) rot=(0,0,1;0rad)
  Support = -> [Fillet177]
  sketch-geometry (8):
    g0: LineSegment StartX=-15.5 StartY=15.5 StartZ=0 EndX=15.5 EndY=15.5 EndZ=0
    g1: LineSegment StartX=15.5 StartY=15.5 StartZ=0 EndX=15.5 EndY=-15.5 EndZ=0
    g2: LineSegment StartX=15.5 StartY=-15.5 StartZ=0 EndX=-15.5 EndY=-15.5 EndZ=0
    g3: LineSegment StartX=-15.5 StartY=-15.5 StartZ=0 EndX=-15.5 EndY=15.5 EndZ=0
    g4: Circle CenterX=-15.5 CenterY=15.5 CenterZ=0 NormalX=0 NormalY=0 NormalZ=1 AngleXU=0 Radius=1.225
    g5: Circle CenterX=15.5 CenterY=15.5 CenterZ=0 NormalX=0 NormalY=0 NormalZ=1 AngleXU=0 Radius=1.225
    g6: Circle CenterX=15.5 CenterY=-15.5 CenterZ=0 NormalX=0 NormalY=0 NormalZ=1 AngleXU=0 Radius=1.225
    g7: Circle CenterX=-15.5 CenterY=-15.5 CenterZ=0 NormalX=0 NormalY=0 NormalZ=1 AngleXU=0 Radius=1.225
  constraints (19):
    c: Coincident(g0,g1)
    c: Coincident(g1,g2)
    c: Coincident(g2,g3)
    c: Coincident(g3,g0)
    c: Horizontal(g0)
    c: Horizontal(g2)
    c: Vertical(g1)
    c: Vertical(g3)
    c: Equal(g0,g3)
    c: Symmetric(g0,g1,g-1)
    c: DistanceX(g0,g0) = 31
    c: Coincident(g4,g0)
    c: Coincident(g7,g2)
    c: Coincident(g0,g5)
    c: Coincident(g1,g6)
    c: Equal(g7,g4)
    c: Equal(g4,g5)
    c: Equal(g5,g6)
    c: Radius(g4) = 1.225
FEATURE [PartDesign::Pocket] Pocket065
  AllowMultiFace = false
  BaseFeature = -> Fillet177
  Length = 5
  Length2 = 100
  Profile = -> Sketch164
  Refine = true
  Type = 1
FEATURE [Sketcher::SketchObject] Sketch165
  FullyConstrained = false
  MapMode = 5
  Placement = pos=(0,0,7.75) rot=(0,0,1;0rad)
  Support = -> [Pocket065]
  sketch-geometry (1):
    g0: Circle CenterX=0 CenterY=0 CenterZ=0 NormalX=0 NormalY=0 NormalZ=1 AngleXU=0 Radius=14
  constraints (2):
    c: Coincident(g0,g-1)
    c: Radius(g0) = 14
FEATURE [PartDesign::Pocket] Pocket066
  AllowMultiFace = false
  BaseFeature = -> Pocket065
  Length = 1
  Length2 = 100
  Profile = -> Sketch165
  Refine = true
  Type = 0
FEATURE [Sketcher::SketchObject] Sketch166
  FullyConstrained = false
  MapMode = 5
  Placement = pos=(0,0,6.75) rot=(0,0,1;0rad)
  Support = -> [Pocket066]
  sketch-geometry (1):
    g0: Circle CenterX=0 CenterY=0 CenterZ=0 NormalX=0 NormalY=0 NormalZ=1 AngleXU=0 Radius=11
  constraints (2):
    c: Coincident(g0,g-1)
    c: Radius(g0) = 11
FEATURE [PartDesign::Pad] Pad043
  AllowMultiFace = false
  BaseFeature = -> Pocket066
  Direction = (1,1,1)
  Length = 3
  Length2 = 100
  Profile = -> Sketch166
  Refine = true
  Type = 0
FEATURE [PartDesign::Draft] Draft001
  Angle = 10
  Base = -> Pad043 [Face25]
  BaseFeature = -> Pad043
  NeutralPlane = -> Pad043 [Face24]
  SupportTransform = false
FEATURE [Sketcher::SketchObject] Sketch167
  FullyConstrained = false
  MapMode = 5
  Placement = pos=(0,0,9.75) rot=(0,0,1;0rad)
  Support = -> [Draft001]
  sketch-geometry (1):
    g0: Circle CenterX=0 CenterY=0 CenterZ=0 NormalX=0 NormalY=0 NormalZ=1 AngleXU=0 Radius=5
  constraints (2):
    c: Coincident(g0,g-1)
    c: Radius(g0) = 5
FEATURE [PartDesign::Pocket] Pocket067
  AllowMultiFace = false
  BaseFeature = -> Draft001
  Length = 8
  Length2 = 100
  Profile = -> Sketch167
  Refine = true
  Type = 1
FEATURE [Sketcher::SketchObject] Sketch157
  FullyConstrained = false
  MapMode = 5
  Placement = pos=(0,0,0) rot=(1,0,0;3.14159rad)
  Support = -> [Pocket067]
  sketch-geometry (1):
    g0: Circle CenterX=0 CenterY=0 CenterZ=0 NormalX=0 NormalY=0 NormalZ=1 AngleXU=0 Radius=15.35
  constraints (2):
    c: Coincident(g0,g-1)
    c: Radius(g0) = 15.35
FEATURE [PartDesign::Pocket] Pocket073
  AllowMultiFace = false
  BaseFeature = -> Pocket067
  Length = 5
  Length2 = 100
  Profile = -> Sketch157
  Refine = true
  Type = 0
FEATURE [PartDesign::Body] Body155  label="Aluminum front002"
  Group = -> [Sketch161,Pad042,Chamfer010,Fillet177,Sketch164,Pocket065,Sketch165,Pocket066,Sketch166,Pad043,Draft001,Sketch167,Pocket067,Sketch157,Pocket073]
  Origin = -> Origin183
  Placement = pos=(0,0,32.35) rot=(0,0,1;0rad)
  Tip = -> Pocket073
FEATURE [App::Part] Part030  label="Aluminum front003"
  Group = -> [Body155]
  Origin = -> Origin187
FEATURE [Sketcher::SketchObject] Sketch168
  FullyConstrained = false
  MapMode = 5
  Support = -> [XY_Plane178]
  sketch-geometry (1):
    g0: Circle CenterX=0 CenterY=0 CenterZ=0 NormalX=0 NormalY=0 NormalZ=1 AngleXU=0 Radius=2.5
  constraints (2):
    c: Coincident(g0,g-1)
    c: Radius(g0) = 2.5
FEATURE [PartDesign::Pad] Pad044
  AllowMultiFace = false
  Direction = (1,1,1)
  Length = 60
  Length2 = 100
  Profile = -> Sketch168
  Refine = true
  Type = 0
FEATURE [Sketcher::SketchObject] Sketch169
  FullyConstrained = false
  MapMode = 5
  Placement = pos=(0,0,60) rot=(0,0,1;0rad)
  Support = -> [Pad044]
  sketch-geometry (4):
    g0: LineSegment StartX=2 StartY=2 StartZ=0 EndX=6 EndY=2 EndZ=0
    g1: LineSegment StartX=6 StartY=2 StartZ=0 EndX=6 EndY=-2 EndZ=0
    g2: LineSegment StartX=6 StartY=-2 StartZ=0 EndX=2 EndY=-2 EndZ=0
    g3: LineSegment StartX=2 StartY=-2 StartZ=0 EndX=2 EndY=2 EndZ=0
  constraints (11):
    c: Coincident(g0,g1)
    c: Coincident(g1,g2)
    c: Coincident(g2,g3)
    c: Coincident(g3,g0)
    c: Horizontal(g0)
    c: Horizontal(g2)
    c: Vertical(g1)
    c: Symmetric(g2,g0,g-1)
    c: DistanceX(g-1,g0) = 2
    c: Equal(g0,g3)
    c: DistanceX(g0,g0) = 4
FEATURE [PartDesign::Pocket] Pocket068
  AllowMultiFace = false
  BaseFeature = -> Pad044
  Length = 16
  Length2 = 100
  Profile = -> Sketch169
  Refine = true
  Type = 0
FEATURE [PartDesign::Chamfer] Chamfer011
  Angle = 45
  Base = -> Pocket068 [Edge3,Edge5,Edge9]
  BaseFeature = -> Pocket068
  ChamferType = 0
  FlipDirection = false
  Size = 0.3
  Size2 = 1
  SupportTransform = false
FEATURE [PartDesign::Body] Body156  label="Rotor002"
  Group = -> [Sketch168,Pad044,Sketch169,Pocket068,Chamfer011]
  Origin = -> Origin184
  Placement = pos=(0,0,2) rot=(0,0,1;0rad)
  Tip = -> Chamfer011
FEATURE [App::Part] Part031  label="Rotor003"
  Group = -> [Body156]
  Origin = -> Origin188
FEATURE [Sketcher::SketchObject] Sketch170
  FullyConstrained = false
  MapMode = 5
  Placement = pos=(0,0,22.75) rot=(0,0,1;0rad)
  Support = -> [Pocket064]
  sketch-geometry (1):
    g0: Circle CenterX=0 CenterY=0 CenterZ=0 NormalX=0 NormalY=0 NormalZ=1 AngleXU=0 Radius=18
  constraints (2):
    c: Coincident(g0,g-1)
    c: Radius(g0) = 18
FEATURE [PartDesign::Pocket] Pocket063
  AllowMultiFace = false
  BaseFeature = -> Pocket064
  Length = 5
  Length2 = 100
  Profile = -> Sketch170
  Refine = true
  Type = 1
FEATURE [PartDesign::Body] Body154
  Group = -> [Sketch160,Pad041,Chamfer009,Sketch163,Pocket064,Sketch170,Pocket063]
  Origin = -> Origin182
  Placement = pos=(0,0,9.6) rot=(0,0,1;0rad)
  Tip = -> Pocket063
FEATURE [App::Part] Part029  label="Body155"
  Group = -> [Body154,Body157]
  Origin = -> Origin186
FEATURE [Sketcher::SketchObject] Sketch171
  ExternalGeometry = -> [Hole001]
  FullyConstrained = false
  MapMode = 5
  Placement = pos=(21.15,0,0) rot=(0.57735,0.57735,0.57735;2.0944rad)
  Support = -> [Hole001]
  sketch-geometry (4):
    g0: LineSegment StartX=-8.2 StartY=3.6 StartZ=0 EndX=8.2 EndY=3.6 EndZ=0
    g1: LineSegment StartX=8.2 StartY=3.6 StartZ=0 EndX=8.2 EndY=9.6 EndZ=0
    g2: LineSegment StartX=8.2 StartY=9.6 StartZ=0 EndX=-8.2 EndY=9.6 EndZ=0
    g3: LineSegment StartX=-8.2 StartY=9.6 StartZ=0 EndX=-8.2 EndY=3.6 EndZ=0
  constraints (10):
    c: Coincident(g0,g1)
    c: Coincident(g1,g2)
    c: Coincident(g2,g3)
    c: Coincident(g3,g0)
    c: Horizontal(g0)
    c: Vertical(g1)
    c: Vertical(g3)
    c: Coincident(g0,g-3)
    c: PointOnObject(g1,g-5)
    c: Symmetric(g2,g1,g-2)
FEATURE [PartDesign::Pocket] Pocket069
  AllowMultiFace = false
  BaseFeature = -> Hole001
  Length = 4
  Length2 = 100
  Profile = -> Sketch171
  Refine = true
  Type = 0
FEATURE [PartDesign::Body] Body153  label="Aluminium rear002"
  Group = -> [Sketch158,Pad039,Sketch159,Pad040,Chamfer008,Fillet176,Sketch162,Hole001,Sketch171,Pocket069]
  Origin = -> Origin181
  Tip = -> Pocket069
FEATURE [App::Part] Part028  label="Aluminium rear003"
  Group = -> [Body153]
  Origin = -> Origin185
FEATURE [Sketcher::SketchObject] Sketch172
  FullyConstrained = false
  MapMode = 5
  Placement = pos=(0,0,0) rot=(0.57735,0.57735,0.57735;2.0944rad)
  Support = -> [YZ_Plane186]
  sketch-geometry (4):
    g0: LineSegment StartX=-7.5 StartY=0 StartZ=0 EndX=7.5 EndY=0 EndZ=0
    g1: LineSegment StartX=7.5 StartY=0 StartZ=0 EndX=7.5 EndY=5 EndZ=0
    g2: LineSegment StartX=7.5 StartY=5 StartZ=0 EndX=-7.5 EndY=5 EndZ=0
    g3: LineSegment StartX=-7.5 StartY=5 StartZ=0 EndX=-7.5 EndY=0 EndZ=0
  constraints (11):
    c: Coincident(g0,g1)
    c: Coincident(g1,g2)
    c: Coincident(g2,g3)
    c: Coincident(g3,g0)
    c: Horizontal(g0)
    c: Horizontal(g2)
    c: Vertical(g1)
    c: Vertical(g3)
    c: Symmetric(g0,g0,g-1)
    c: DistanceX(g0,g0) = 15
    c: DistanceY(g3,g3) = 5
FEATURE [PartDesign::Pad] Pad045
  AllowMultiFace = false
  Direction = (1,1,1)
  Length = 10
  Length2 = 100
  Placement = pos=(0,0,0) rot=(0.57735,0.57735,0.57735;2.0944rad)
  Profile = -> Sketch172
  Refine = true
  Type = 0
FEATURE [Sketcher::SketchObject] Sketch173
  ExternalGeometry = -> [Pad045]
  FullyConstrained = false
  MapMode = 5
  Placement = pos=(10,-2.2e-15,2.2e-15) rot=(0.57735,0.57735,0.57735;2.0944rad)
  Support = -> [Pad045]
  sketch-geometry (8):
    g0: LineSegment StartX=-6.5 StartY=4 StartZ=0 EndX=6.5 EndY=4 EndZ=0
    g1: LineSegment StartX=6.5 StartY=4 StartZ=0 EndX=6.5 EndY=1 EndZ=0
    g2: LineSegment StartX=6.5 StartY=1 StartZ=0 EndX=-6.5 EndY=1 EndZ=0
    g3: LineSegment StartX=-6.5 StartY=1 StartZ=0 EndX=-6.5 EndY=4 EndZ=0
    g4: LineSegment StartX=-6.5 StartY=1 StartZ=0 EndX=-7.5 EndY=1 EndZ=0
    g5: LineSegment StartX=-6.5 StartY=1 StartZ=0 EndX=-6.5 EndY=0 EndZ=0
    g6: LineSegment StartX=6.5 StartY=4 StartZ=0 EndX=6.5 EndY=5 EndZ=0
    g7: LineSegment StartX=6.5 StartY=4 StartZ=0 EndX=7.5 EndY=4 EndZ=0
  constraints (23):
    c: Coincident(g0,g1)
    c: Coincident(g1,g2)
    c: Coincident(g2,g3)
    c: Coincident(g3,g0)
    c: Horizontal(g2)
    c: Vertical(g1)
    c: Vertical(g3)
    c: Symmetric(g0,g0,g-2)
    c: Coincident(g4,g2)
    c: PointOnObject(g4,g-4)
    c: Horizontal(g4)
    c: PointOnObject(g5,g-1)
    c: Vertical(g5)
    c: Coincident(g6,g0)
    c: Coincident(g7,g0)
    c: Horizontal(g7)
    c: Vertical(g6)
    c: PointOnObject(g6,g-5)
    c: Equal(g7,g6)
    c: Equal(g6,g4)
    c: Equal(g4,g5)
    c: DistanceX(g4,g4) = 1
    c: Coincident(g5,g2)
FEATURE [PartDesign::Pocket] Pocket070
  AllowMultiFace = false
  BaseFeature = -> Pad045
  Length = 6
  Length2 = 100
  Placement = pos=(0,0,0) rot=(0.57735,0.57735,0.57735;2.0944rad)
  Profile = -> Sketch173
  Refine = true
  Type = 0
FEATURE [Sketcher::SketchObject] Sketch154
  ExternalGeometry = -> [Pocket070]
  FullyConstrained = false
  MapMode = 5
  Placement = pos=(10,-2.2e-15,2.2e-15) rot=(0.57735,0.57735,0.57735;2.0944rad)
  Support = -> [Pocket070]
  sketch-geometry (4):
    g0: LineSegment StartX=-4 StartY=5 StartZ=0 EndX=4 EndY=5 EndZ=0
    g1: LineSegment StartX=4 StartY=5 StartZ=0 EndX=4 EndY=4 EndZ=0
    g2: LineSegment StartX=4 StartY=4 StartZ=0 EndX=-4 EndY=4 EndZ=0
    g3: LineSegment StartX=-4 StartY=4 StartZ=0 EndX=-4 EndY=5 EndZ=0
  constraints (11):
    c: Coincident(g0,g1)
    c: Coincident(g1,g2)
    c: Coincident(g2,g3)
    c: Coincident(g3,g0)
    c: Horizontal(g0)
    c: Vertical(g1)
    c: Vertical(g3)
    c: PointOnObject(g0,g-3)
    c: PointOnObject(g1,g-4)
    c: Symmetric(g1,g2,g-2)
    c: DistanceX(g0,g0) = 8
FEATURE [PartDesign::Pocket] Pocket071
  AllowMultiFace = false
  BaseFeature = -> Pocket070
  Length = 4.5
  Length2 = 100
  Placement = pos=(0,0,0) rot=(0.57735,0.57735,0.57735;2.0944rad)
  Profile = -> Sketch154
  Refine = true
  Type = 0
FEATURE [Sketcher::SketchObject] Sketch155
  ExternalGeometry = -> [Pocket071]
  FullyConstrained = false
  MapMode = 5
  Placement = pos=(-1.4e-15,2.2e-15,5) rot=(0,0,-1;1.5708rad)
  Support = -> [Pocket071]
  sketch-geometry (11):
    g0: LineSegment StartX=-6.49 StartY=8.99 StartZ=0 EndX=-5.01 EndY=8.99 EndZ=0
    g1: LineSegment StartX=-5.01 StartY=8.99 StartZ=0 EndX=-5.01 EndY=4.5 EndZ=0
    g2: LineSegment StartX=-5.01 StartY=4.5 StartZ=0 EndX=-6.49 EndY=4.5 EndZ=0
    g3: LineSegment StartX=-6.49 StartY=4.5 StartZ=0 EndX=-6.49 EndY=8.99 EndZ=0
    g4: LineSegment StartX=5.01 StartY=8.99 StartZ=0 EndX=6.49 EndY=8.99 EndZ=0
    g5: LineSegment StartX=6.49 StartY=8.99 StartZ=0 EndX=6.49 EndY=4.5 EndZ=0
    g6: LineSegment StartX=6.49 StartY=4.5 StartZ=0 EndX=5.01 EndY=4.5 EndZ=0
    g7: LineSegment StartX=5.01 StartY=4.5 StartZ=0 EndX=5.01 EndY=8.99 EndZ=0
    g8: LineSegment StartX=-7.5 StartY=8.99 StartZ=0 EndX=-6.49 EndY=8.99 EndZ=0
    g9: LineSegment StartX=-6.49 StartY=10 StartZ=0 EndX=-6.49 EndY=8.99 EndZ=0
    g10: LineSegment StartX=-5.01 StartY=8.99 StartZ=0 EndX=-4 EndY=8.99 EndZ=0
  constraints (32):
    c: Coincident(g0,g1)
    c: Coincident(g1,g2)
    c: Coincident(g2,g3)
    c: Coincident(g3,g0)
    c: Horizontal(g0)
    c: Horizontal(g2)
    c: Vertical(g1)
    c: Vertical(g3)
    c: Coincident(g4,g5)
    c: Coincident(g5,g6)
    c: Coincident(g6,g7)
    c: Coincident(g7,g4)
    c: Horizontal(g4)
    c: Horizontal(g6)
    c: Vertical(g5)
    c: Vertical(g7)
    c: DistanceX(g4,g4) = 1.48
    c: Equal(g0,g4)
    c: Equal(g7,g1)
    c: PointOnObject(g8,g-4)
    c: Coincident(g8,g0)
    c: Horizontal(g8)
    c: PointOnObject(g9,g-5)
    c: Coincident(g9,g0)
    c: Vertical(g9)
    c: Coincident(g10,g0)
    c: PointOnObject(g10,g-3)
    c: Horizontal(g10)
    c: Symmetric(g4,g0,g-2)
    c: Equal(g10,g9)
    c: Equal(g9,g8)
    c: DistanceY(g3,g3) = 4.49
FEATURE [PartDesign::Pocket] Pocket072
  AllowMultiFace = false
  BaseFeature = -> Pocket071
  Length = 2
  Length2 = 100
  Placement = pos=(0,0,0) rot=(0.57735,0.57735,0.57735;2.0944rad)
  Profile = -> Sketch155
  Refine = true
  Type = 0
FEATURE [PartDesign::Body] Body158  label="conector001"
  Group = -> [Sketch172,Pad045,Sketch173,Pocket070,Sketch154,Pocket071,Sketch155,Pocket072]
  Origin = -> Origin192
  Tip = -> Pocket072
FEATURE [Sketcher::SketchObject] Sketch174
  ExternalGeometry = -> [Pad046]
  FullyConstrained = false
  MapMode = 5
  Placement = pos=(-3e-16,4e-16,1) rot=(0,0,-1;1.5708rad)
  Support = -> [Pad046]
  sketch-geometry (7):
    g0: LineSegment StartX=-5.5 StartY=1 StartZ=0 EndX=-4.5 EndY=1 EndZ=0
    g1: LineSegment StartX=-4.5 StartY=1 StartZ=0 EndX=-4.5 EndY=8 EndZ=0
    g2: LineSegment StartX=-4.5 StartY=8 StartZ=0 EndX=-5.5 EndY=8 EndZ=0
    g3: LineSegment StartX=-5.5 StartY=8 StartZ=0 EndX=-5.5 EndY=1 EndZ=0
    g4: LineSegment StartX=-5.5 StartY=8 StartZ=0 EndX=-5.25 EndY=8.7 EndZ=0
    g5: LineSegment StartX=-5.25 StartY=8.7 StartZ=0 EndX=-4.75 EndY=8.7 EndZ=0
    g6: LineSegment StartX=-4.75 StartY=8.7 StartZ=0 EndX=-4.5 EndY=8 EndZ=0
  constraints (19):
    c: Coincident(g0,g1)
    c: Coincident(g1,g2)
    c: Coincident(g2,g3)
    c: Coincident(g3,g0)
    c: Horizontal(g0)
    c: Horizontal(g2)
    c: Vertical(g1)
    c: Vertical(g3)
    c: Coincident(g0,g-3)
    c: Coincident(g2,g4)
    c: Coincident(g4,g5)
    c: Horizontal(g5)
    c: Coincident(g5,g6)
    c: Coincident(g6,g1)
    c: DistanceY(g1,g5) = 0.7
    c: DistanceX(g5,g5) = 0.5
    c: Equal(g6,g4)
    c: DistanceX(g0,g0) = 1
    c: DistanceY(g3,g3) = 7
FEATURE [PartDesign::Pad] Pad047
  AllowMultiFace = false
  BaseFeature = -> Pad046
  Direction = (1,1,1)
  Length = 1
  Length2 = 100
  Placement = pos=(0,0,0) rot=(0.57735,0.57735,0.57735;2.0944rad)
  Profile = -> Sketch174
  Refine = true
  Reversed = true
  Type = 0
FEATURE [PartDesign::LinearPattern] LinearPattern001
  BaseFeature = -> Pad047
  Direction = -> Pad047 [Edge10]
  Length = 10
  Occurrences = 3
  Originals = -> [Pad047]
  Placement = pos=(0,0,0) rot=(0.57735,0.57735,0.57735;2.0944rad)
  Refine = true
  Reversed = true
FEATURE [PartDesign::Body] Body159  label="pin001"
  Group = -> [Sketch156,Pad046,Sketch174,Pad047,LinearPattern001]
  Origin = -> Origin193
  Placement = pos=(0,0,2) rot=(0,0,1;0rad)
  Tip = -> LinearPattern001
FEATURE [App::Part] Part033  label="Conector001"
  Group = -> [Body158,Body159]
  Origin = -> Origin191
  Placement = pos=(17,0,4) rot=(0,0,1;0rad)
FEATURE [App::Part] Part027  label="Nema 017-002"
  Group = -> [Part028,Part029,Part030,Part031,Part032,Part033]
  Origin = -> Origin180
  Placement = pos=(440,247,106) rot=(0,1,0;-1.5708rad)
FEATURE [Sketcher::SketchObject] Sketch175
  FullyConstrained = true
  MapMode = 5
  Placement = pos=(0,0,0) rot=(0.57735,0.57735,0.57735;2.0944rad)
  Support = -> [YZ_Plane189]
  sketch-geometry (1):
    g0: Circle CenterX=0 CenterY=0 CenterZ=0 NormalX=0 NormalY=0 NormalZ=1 AngleXU=0 Radius=4
  constraints (2):
    c: Coincident(g0,g-1)
    c: Radius(g0) = 4
FEATURE [PartDesign::Pad] Pad048
  Direction = (1,-2e-16,3e-16)
  Length = 350
  Length2 = 10
  Placement = pos=(0,0,0) rot=(0.57735,0.57735,0.57735;2.0944rad)
  Profile = -> Sketch175
  Type = 0
FEATURE [PartDesign::Body] Body160
  Group = -> [Sketch175,Pad048]
  Origin = -> Origin195
  Tip = -> Pad048
FEATURE [App::Part] Part034  label="eje-001"
  Group = -> [Body160]
  Origin = -> Origin194
  Placement = pos=(-21,120,105) rot=(0,0,1;0rad)
FEATURE [Sketcher::SketchObject] Sketch176
  FullyConstrained = true
  MapMode = 5
  Placement = pos=(0,0,0) rot=(0.57735,0.57735,0.57735;2.0944rad)
  Support = -> [YZ_Plane191]
  sketch-geometry (1):
    g0: Circle CenterX=0 CenterY=0 CenterZ=0 NormalX=0 NormalY=0 NormalZ=1 AngleXU=0 Radius=4
  constraints (2):
    c: Coincident(g0,g-1)
    c: Radius(g0) = 4
FEATURE [PartDesign::Pad] Pad049
  Direction = (1,-2e-16,3e-16)
  Length = 350
  Length2 = 10
  Placement = pos=(0,0,0) rot=(0.57735,0.57735,0.57735;2.0944rad)
  Profile = -> Sketch176
  Type = 0
FEATURE [PartDesign::Body] Body161
  Group = -> [Sketch176,Pad049]
  Origin = -> Origin197
  Tip = -> Pad049
FEATURE [App::Part] Part035  label="eje-002"
  Group = -> [Body161]
  Origin = -> Origin196
  Placement = pos=(-31,120,80) rot=(0,0,1;0rad)
FEATURE [Sketcher::SketchObject] Sketch177
  FullyConstrained = true
  MapMode = 5
  Placement = pos=(0,0,0) rot=(0.57735,0.57735,0.57735;2.0944rad)
  Support = -> [YZ_Plane193]
  sketch-geometry (1):
    g0: Circle CenterX=0 CenterY=0 CenterZ=0 NormalX=0 NormalY=0 NormalZ=1 AngleXU=0 Radius=4
  constraints (2):
    c: Coincident(g0,g-1)
    c: Radius(g0) = 4
FEATURE [PartDesign::Pad] Pad050
  Direction = (1,-2e-16,3e-16)
  Length = 350
  Length2 = 10
  Placement = pos=(0,0,0) rot=(0.57735,0.57735,0.57735;2.0944rad)
  Profile = -> Sketch177
  Type = 0
FEATURE [PartDesign::Body] Body162
  Group = -> [Sketch177,Pad050]
  Origin = -> Origin199
  Tip = -> Pad050
FEATURE [App::Part] Part036  label="eje-003"
  Group = -> [Body162]
  Origin = -> Origin198
  Placement = pos=(-18,246,105) rot=(0,0,1;0rad)
FEATURE [Sketcher::SketchObject] Sketch178
  FullyConstrained = true
  MapMode = 5
  Placement = pos=(0,0,0) rot=(0.57735,0.57735,0.57735;2.0944rad)
  Support = -> [YZ_Plane195]
  sketch-geometry (1):
    g0: Circle CenterX=0 CenterY=0 CenterZ=0 NormalX=0 NormalY=0 NormalZ=1 AngleXU=0 Radius=60
  constraints (2):
    c: Coincident(g0,g-1)
    c: Radius(g0) = 60
FEATURE [PartDesign::Pad] Pad051
  Direction = (1,-2e-16,3e-16)
  Length = 8
  Length2 = 10
  Placement = pos=(0,0,0) rot=(0.57735,0.57735,0.57735;2.0944rad)
  Profile = -> Sketch178
  Type = 0
FEATURE [PartDesign::Body] Body163
  Group = -> [Sketch178,Pad051]
  Origin = -> Origin201
  Tip = -> Pad051
FEATURE [App::Part] Part037  label="rueda-001"
  Group = -> [Body163]
  Origin = -> Origin200
  Placement = pos=(271,246,105) rot=(0,0,1;0rad)
FEATURE [Sketcher::SketchObject] Sketch179
  FullyConstrained = false
  MapMode = 5
  Placement = pos=(0,0,0) rot=(0.57735,0.57735,0.57735;2.0944rad)
  Support = -> [YZ_Plane197]
  sketch-geometry (8):
    g0: LineSegment StartX=3.44519 StartY=-3.62363 StartZ=0 EndX=4.86075 EndY=1.17181 EndZ=0
    g1: LineSegment StartX=4.86075 StartY=1.17181 StartZ=0 EndX=1.41556 EndY=4.79544 EndZ=0
    g2: LineSegment StartX=1.41556 StartY=4.79544 StartZ=0 EndX=-3.44519 EndY=3.62363 EndZ=0
    g3: LineSegment StartX=-3.44519 StartY=3.62363 StartZ=0 EndX=-4.86075 EndY=-1.17181 EndZ=0
    g4: LineSegment StartX=-4.86075 StartY=-1.17181 StartZ=0 EndX=-1.41556 EndY=-4.79544 EndZ=0
    g5: LineSegment StartX=-1.41556 StartY=-4.79544 StartZ=0 EndX=3.44519 EndY=-3.62363 EndZ=0
    g6: Circle CenterX=0 CenterY=0 CenterZ=0 NormalX=0 NormalY=0 NormalZ=1 AngleXU=0 Radius=5
    g7: Circle CenterX=0 CenterY=0 CenterZ=0 NormalX=0 NormalY=0 NormalZ=1 AngleXU=0 Radius=3
  constraints (17):
    c: Coincident(g0,g1)
    c: Coincident(g1,g2)
    c: Coincident(g2,g3)
    c: Coincident(g3,g4)
    c: Coincident(g4,g5)
    c: Coincident(g5,g0)
    c: Equal(g0, g1-g5) x5
    c: PointOnObject(g0,g6)
    c: PointOnObject(g1,g6)
    c: PointOnObject(g2,g6)
    c: PointOnObject(g3,g6)
    c: PointOnObject(g4,g6)
    c: PointOnObject(g5,g6)
    c: Coincident(g6,g-1)
    c: Coincident(g7,g6)
    c: Radius(g7) = 3
    c: Radius(g6) = 5
FEATURE [PartDesign::Pad] Pad052
  Direction = (1,-2e-16,3e-16)
  Length = 3
  Length2 = 10
  Placement = pos=(0,0,0) rot=(0.57735,0.57735,0.57735;2.0944rad)
  Profile = -> Sketch179
  Type = 0
FEATURE [PartDesign::Pad] Pad053
  BaseFeature = -> Pad052
  Direction = (1,-2e-16,6e-16)
  Length = 50
  Length2 = 10
  Placement = pos=(0,0,0) rot=(0.57735,0.57735,0.57735;2.0944rad)
  Profile = -> Pad052 [Edge20]
  Type = 0
FEATURE [PartDesign::Body] Body164
  Group = -> [Sketch179,Pad052,Pad053]
  Origin = -> Origin203
  Tip = -> Pad053
FEATURE [App::Part] Part038  label="tornillo M6-30-001"
  Group = -> [Body164]
  Origin = -> Origin202
  Placement = pos=(10,-4,181) rot=(0,0,1;1.5708rad)
FEATURE [Sketcher::SketchObject] Sketch180
  FullyConstrained = false
  MapMode = 5
  Placement = pos=(0,0,0) rot=(0.57735,0.57735,0.57735;2.0944rad)
  Support = -> [YZ_Plane199]
  sketch-geometry (8):
    g0: LineSegment StartX=3.44519 StartY=-3.62363 StartZ=0 EndX=4.86075 EndY=1.17181 EndZ=0
    g1: LineSegment StartX=4.86075 StartY=1.17181 StartZ=0 EndX=1.41556 EndY=4.79544 EndZ=0
    g2: LineSegment StartX=1.41556 StartY=4.79544 StartZ=0 EndX=-3.44519 EndY=3.62363 EndZ=0
    g3: LineSegment StartX=-3.44519 StartY=3.62363 StartZ=0 EndX=-4.86075 EndY=-1.17181 EndZ=0
    g4: LineSegment StartX=-4.86075 StartY=-1.17181 StartZ=0 EndX=-1.41556 EndY=-4.79544 EndZ=0
    g5: LineSegment StartX=-1.41556 StartY=-4.79544 StartZ=0 EndX=3.44519 EndY=-3.62363 EndZ=0
    g6: Circle CenterX=0 CenterY=0 CenterZ=0 NormalX=0 NormalY=0 NormalZ=1 AngleXU=0 Radius=5
    g7: Circle CenterX=0 CenterY=0 CenterZ=0 NormalX=0 NormalY=0 NormalZ=1 AngleXU=0 Radius=3
  constraints (17):
    c: Coincident(g0,g1)
    c: Coincident(g1,g2)
    c: Coincident(g2,g3)
    c: Coincident(g3,g4)
    c: Coincident(g4,g5)
    c: Coincident(g5,g0)
    c: Equal(g0, g1-g5) x5
    c: PointOnObject(g0,g6)
    c: PointOnObject(g1,g6)
    c: PointOnObject(g2,g6)
    c: PointOnObject(g3,g6)
    c: PointOnObject(g4,g6)
    c: PointOnObject(g5,g6)
    c: Coincident(g6,g-1)
    c: Coincident(g7,g6)
    c: Radius(g7) = 3
    c: Radius(g6) = 5
FEATURE [PartDesign::Pad] Pad054
  Direction = (1,-2e-16,3e-16)
  Length = 3
  Length2 = 10
  Placement = pos=(0,0,0) rot=(0.57735,0.57735,0.57735;2.0944rad)
  Profile = -> Sketch180
  Type = 0
FEATURE [PartDesign::Pad] Pad055
  BaseFeature = -> Pad054
  Direction = (1,-2e-16,6e-16)
  Length = 50
  Length2 = 10
  Placement = pos=(0,0,0) rot=(0.57735,0.57735,0.57735;2.0944rad)
  Profile = -> Pad054 [Edge20]
  Type = 0
FEATURE [PartDesign::Body] Body165
  Group = -> [Sketch180,Pad054,Pad055]
  Origin = -> Origin205
  Tip = -> Pad055
FEATURE [App::Part] Part039  label="tornillo M6-30-002"
  Group = -> [Body165]
  Origin = -> Origin204
  Placement = pos=(10,-4,10) rot=(0,0,1;1.5708rad)
FEATURE [Sketcher::SketchObject] Sketch181
  FullyConstrained = false
  MapMode = 5
  Placement = pos=(0,0,0) rot=(0.57735,0.57735,0.57735;2.0944rad)
  Support = -> [YZ_Plane201]
  sketch-geometry (8):
    g0: LineSegment StartX=3.44519 StartY=-3.62363 StartZ=0 EndX=4.86075 EndY=1.17181 EndZ=0
    g1: LineSegment StartX=4.86075 StartY=1.17181 StartZ=0 EndX=1.41556 EndY=4.79544 EndZ=0
    g2: LineSegment StartX=1.41556 StartY=4.79544 StartZ=0 EndX=-3.44519 EndY=3.62363 EndZ=0
    g3: LineSegment StartX=-3.44519 StartY=3.62363 StartZ=0 EndX=-4.86075 EndY=-1.17181 EndZ=0
    g4: LineSegment StartX=-4.86075 StartY=-1.17181 StartZ=0 EndX=-1.41556 EndY=-4.79544 EndZ=0
    g5: LineSegment StartX=-1.41556 StartY=-4.79544 StartZ=0 EndX=3.44519 EndY=-3.62363 EndZ=0
    g6: Circle CenterX=0 CenterY=0 CenterZ=0 NormalX=0 NormalY=0 NormalZ=1 AngleXU=0 Radius=5
    g7: Circle CenterX=0 CenterY=0 CenterZ=0 NormalX=0 NormalY=0 NormalZ=1 AngleXU=0 Radius=3
  constraints (17):
    c: Coincident(g0,g1)
    c: Coincident(g1,g2)
    c: Coincident(g2,g3)
    c: Coincident(g3,g4)
    c: Coincident(g4,g5)
    c: Coincident(g5,g0)
    c: Equal(g0, g1-g5) x5
    c: PointOnObject(g0,g6)
    c: PointOnObject(g1,g6)
    c: PointOnObject(g2,g6)
    c: PointOnObject(g3,g6)
    c: PointOnObject(g4,g6)
    c: PointOnObject(g5,g6)
    c: Coincident(g6,g-1)
    c: Coincident(g7,g6)
    c: Radius(g7) = 3
    c: Radius(g6) = 5
FEATURE [PartDesign::Pad] Pad056
  Direction = (1,-2e-16,3e-16)
  Length = 3
  Length2 = 10
  Placement = pos=(0,0,0) rot=(0.57735,0.57735,0.57735;2.0944rad)
  Profile = -> Sketch181
  Type = 0
FEATURE [PartDesign::Pad] Pad057
  BaseFeature = -> Pad056
  Direction = (1,-2e-16,6e-16)
  Length = 50
  Length2 = 10
  Placement = pos=(0,0,0) rot=(0.57735,0.57735,0.57735;2.0944rad)
  Profile = -> Pad056 [Edge20]
  Type = 0
FEATURE [PartDesign::Body] Body166
  Group = -> [Sketch181,Pad056,Pad057]
  Origin = -> Origin207
  Tip = -> Pad057
FEATURE [App::Part] Part040  label="tornillo M6-30-003"
  Group = -> [Body166]
  Origin = -> Origin206
  Placement = pos=(330,-4,9) rot=(0,0,1;1.5708rad)
FEATURE [Sketcher::SketchObject] Sketch182
  FullyConstrained = false
  MapMode = 5
  Placement = pos=(0,0,0) rot=(0.57735,0.57735,0.57735;2.0944rad)
  Support = -> [YZ_Plane203]
  sketch-geometry (8):
    g0: LineSegment StartX=3.44519 StartY=-3.62363 StartZ=0 EndX=4.86075 EndY=1.17181 EndZ=0
    g1: LineSegment StartX=4.86075 StartY=1.17181 StartZ=0 EndX=1.41556 EndY=4.79544 EndZ=0
    g2: LineSegment StartX=1.41556 StartY=4.79544 StartZ=0 EndX=-3.44519 EndY=3.62363 EndZ=0
    g3: LineSegment StartX=-3.44519 StartY=3.62363 StartZ=0 EndX=-4.86075 EndY=-1.17181 EndZ=0
    g4: LineSegment StartX=-4.86075 StartY=-1.17181 StartZ=0 EndX=-1.41556 EndY=-4.79544 EndZ=0
    g5: LineSegment StartX=-1.41556 StartY=-4.79544 StartZ=0 EndX=3.44519 EndY=-3.62363 EndZ=0
    g6: Circle CenterX=0 CenterY=0 CenterZ=0 NormalX=0 NormalY=0 NormalZ=1 AngleXU=0 Radius=5
    g7: Circle CenterX=0 CenterY=0 CenterZ=0 NormalX=0 NormalY=0 NormalZ=1 AngleXU=0 Radius=3
  constraints (17):
    c: Coincident(g0,g1)
    c: Coincident(g1,g2)
    c: Coincident(g2,g3)
    c: Coincident(g3,g4)
    c: Coincident(g4,g5)
    c: Coincident(g5,g0)
    c: Equal(g0, g1-g5) x5
    c: PointOnObject(g0,g6)
    c: PointOnObject(g1,g6)
    c: PointOnObject(g2,g6)
    c: PointOnObject(g3,g6)
    c: PointOnObject(g4,g6)
    c: PointOnObject(g5,g6)
    c: Coincident(g6,g-1)
    c: Coincident(g7,g6)
    c: Radius(g7) = 3
    c: Radius(g6) = 5
FEATURE [PartDesign::Pad] Pad058
  Direction = (1,-2e-16,3e-16)
  Length = 3
  Length2 = 10
  Placement = pos=(0,0,0) rot=(0.57735,0.57735,0.57735;2.0944rad)
  Profile = -> Sketch182
  Type = 0
FEATURE [PartDesign::Pad] Pad059
  BaseFeature = -> Pad058
  Direction = (1,-2e-16,6e-16)
  Length = 50
  Length2 = 10
  Placement = pos=(0,0,0) rot=(0.57735,0.57735,0.57735;2.0944rad)
  Profile = -> Pad058 [Edge20]
  Type = 0
FEATURE [PartDesign::Body] Body167
  Group = -> [Sketch182,Pad058,Pad059]
  Origin = -> Origin209
  Tip = -> Pad059
FEATURE [App::Part] Part041  label="tornillo M6-30-004"
  Group = -> [Body167]
  Origin = -> Origin208
  Placement = pos=(330,-4,181) rot=(0,0,1;1.5708rad)
FEATURE [Sketcher::SketchObject] Sketch183
  FullyConstrained = false
  MapMode = 5
  Placement = pos=(0,0,0) rot=(0.57735,0.57735,0.57735;2.0944rad)
  Support = -> [YZ_Plane205]
  sketch-geometry (8):
    g0: LineSegment StartX=3.44519 StartY=-3.62363 StartZ=0 EndX=4.86075 EndY=1.17181 EndZ=0
    g1: LineSegment StartX=4.86075 StartY=1.17181 StartZ=0 EndX=1.41556 EndY=4.79544 EndZ=0
    g2: LineSegment StartX=1.41556 StartY=4.79544 StartZ=0 EndX=-3.44519 EndY=3.62363 EndZ=0
    g3: LineSegment StartX=-3.44519 StartY=3.62363 StartZ=0 EndX=-4.86075 EndY=-1.17181 EndZ=0
    g4: LineSegment StartX=-4.86075 StartY=-1.17181 StartZ=0 EndX=-1.41556 EndY=-4.79544 EndZ=0
    g5: LineSegment StartX=-1.41556 StartY=-4.79544 StartZ=0 EndX=3.44519 EndY=-3.62363 EndZ=0
    g6: Circle CenterX=0 CenterY=0 CenterZ=0 NormalX=0 NormalY=0 NormalZ=1 AngleXU=0 Radius=5
    g7: Circle CenterX=0 CenterY=0 CenterZ=0 NormalX=0 NormalY=0 NormalZ=1 AngleXU=0 Radius=3
  constraints (17):
    c: Coincident(g0,g1)
    c: Coincident(g1,g2)
    c: Coincident(g2,g3)
    c: Coincident(g3,g4)
    c: Coincident(g4,g5)
    c: Coincident(g5,g0)
    c: Equal(g0, g1-g5) x5
    c: PointOnObject(g0,g6)
    c: PointOnObject(g1,g6)
    c: PointOnObject(g2,g6)
    c: PointOnObject(g3,g6)
    c: PointOnObject(g4,g6)
    c: PointOnObject(g5,g6)
    c: Coincident(g6,g-1)
    c: Coincident(g7,g6)
    c: Radius(g7) = 3
    c: Radius(g6) = 5
FEATURE [PartDesign::Pad] Pad060
  Direction = (1,-2e-16,3e-16)
  Length = 3
  Length2 = 10
  Placement = pos=(0,0,0) rot=(0.57735,0.57735,0.57735;2.0944rad)
  Profile = -> Sketch183
  Type = 0
FEATURE [PartDesign::Pad] Pad061
  BaseFeature = -> Pad060
  Direction = (1,-2e-16,6e-16)
  Length = 50
  Length2 = 10
  Placement = pos=(0,0,0) rot=(0.57735,0.57735,0.57735;2.0944rad)
  Profile = -> Pad060 [Edge20]
  Type = 0
FEATURE [PartDesign::Body] Body168
  Group = -> [Sketch183,Pad060,Pad061]
  Origin = -> Origin211
  Tip = -> Pad061
FEATURE [App::Part] Part042  label="tornillo M6-30-005"
  Group = -> [Body168]
  Origin = -> Origin210
  Placement = pos=(330,344,180) rot=(0,0,1;-1.5708rad)
FEATURE [Sketcher::SketchObject] Sketch184
  FullyConstrained = false
  MapMode = 5
  Placement = pos=(0,0,0) rot=(0.57735,0.57735,0.57735;2.0944rad)
  Support = -> [YZ_Plane207]
  sketch-geometry (8):
    g0: LineSegment StartX=3.44519 StartY=-3.62363 StartZ=0 EndX=4.86075 EndY=1.17181 EndZ=0
    g1: LineSegment StartX=4.86075 StartY=1.17181 StartZ=0 EndX=1.41556 EndY=4.79544 EndZ=0
    g2: LineSegment StartX=1.41556 StartY=4.79544 StartZ=0 EndX=-3.44519 EndY=3.62363 EndZ=0
    g3: LineSegment StartX=-3.44519 StartY=3.62363 StartZ=0 EndX=-4.86075 EndY=-1.17181 EndZ=0
    g4: LineSegment StartX=-4.86075 StartY=-1.17181 StartZ=0 EndX=-1.41556 EndY=-4.79544 EndZ=0
    g5: LineSegment StartX=-1.41556 StartY=-4.79544 StartZ=0 EndX=3.44519 EndY=-3.62363 EndZ=0
    g6: Circle CenterX=0 CenterY=0 CenterZ=0 NormalX=0 NormalY=0 NormalZ=1 AngleXU=0 Radius=5
    g7: Circle CenterX=0 CenterY=0 CenterZ=0 NormalX=0 NormalY=0 NormalZ=1 AngleXU=0 Radius=3
  constraints (17):
    c: Coincident(g0,g1)
    c: Coincident(g1,g2)
    c: Coincident(g2,g3)
    c: Coincident(g3,g4)
    c: Coincident(g4,g5)
    c: Coincident(g5,g0)
    c: Equal(g0, g1-g5) x5
    c: PointOnObject(g0,g6)
    c: PointOnObject(g1,g6)
    c: PointOnObject(g2,g6)
    c: PointOnObject(g3,g6)
    c: PointOnObject(g4,g6)
    c: PointOnObject(g5,g6)
    c: Coincident(g6,g-1)
    c: Coincident(g7,g6)
    c: Radius(g7) = 3
    c: Radius(g6) = 5
FEATURE [PartDesign::Pad] Pad062
  Direction = (1,-2e-16,3e-16)
  Length = 3
  Length2 = 10
  Placement = pos=(0,0,0) rot=(0.57735,0.57735,0.57735;2.0944rad)
  Profile = -> Sketch184
  Type = 0
FEATURE [PartDesign::Pad] Pad063
  BaseFeature = -> Pad062
  Direction = (1,-2e-16,6e-16)
  Length = 50
  Length2 = 10
  Placement = pos=(0,0,0) rot=(0.57735,0.57735,0.57735;2.0944rad)
  Profile = -> Pad062 [Edge20]
  Type = 0
FEATURE [PartDesign::Body] Body169
  Group = -> [Sketch184,Pad062,Pad063]
  Origin = -> Origin213
  Tip = -> Pad063
FEATURE [App::Part] Part043  label="tornillo M6-30-006"
  Group = -> [Body169]
  Origin = -> Origin212
  Placement = pos=(330,344,9) rot=(0,0,1;-1.5708rad)
FEATURE [Sketcher::SketchObject] Sketch185
  FullyConstrained = false
  MapMode = 5
  Placement = pos=(0,0,0) rot=(0.57735,0.57735,0.57735;2.0944rad)
  Support = -> [YZ_Plane209]
  sketch-geometry (8):
    g0: LineSegment StartX=3.44519 StartY=-3.62363 StartZ=0 EndX=4.86075 EndY=1.17181 EndZ=0
    g1: LineSegment StartX=4.86075 StartY=1.17181 StartZ=0 EndX=1.41556 EndY=4.79544 EndZ=0
    g2: LineSegment StartX=1.41556 StartY=4.79544 StartZ=0 EndX=-3.44519 EndY=3.62363 EndZ=0
    g3: LineSegment StartX=-3.44519 StartY=3.62363 StartZ=0 EndX=-4.86075 EndY=-1.17181 EndZ=0
    g4: LineSegment StartX=-4.86075 StartY=-1.17181 StartZ=0 EndX=-1.41556 EndY=-4.79544 EndZ=0
    g5: LineSegment StartX=-1.41556 StartY=-4.79544 StartZ=0 EndX=3.44519 EndY=-3.62363 EndZ=0
    g6: Circle CenterX=0 CenterY=0 CenterZ=0 NormalX=0 NormalY=0 NormalZ=1 AngleXU=0 Radius=5
    g7: Circle CenterX=0 CenterY=0 CenterZ=0 NormalX=0 NormalY=0 NormalZ=1 AngleXU=0 Radius=3
  constraints (17):
    c: Coincident(g0,g1)
    c: Coincident(g1,g2)
    c: Coincident(g2,g3)
    c: Coincident(g3,g4)
    c: Coincident(g4,g5)
    c: Coincident(g5,g0)
    c: Equal(g0, g1-g5) x5
    c: PointOnObject(g0,g6)
    c: PointOnObject(g1,g6)
    c: PointOnObject(g2,g6)
    c: PointOnObject(g3,g6)
    c: PointOnObject(g4,g6)
    c: PointOnObject(g5,g6)
    c: Coincident(g6,g-1)
    c: Coincident(g7,g6)
    c: Radius(g7) = 3
    c: Radius(g6) = 5
FEATURE [PartDesign::Pad] Pad064
  Direction = (1,-2e-16,3e-16)
  Length = 3
  Length2 = 10
  Placement = pos=(0,0,0) rot=(0.57735,0.57735,0.57735;2.0944rad)
  Profile = -> Sketch185
  Type = 0
FEATURE [PartDesign::Pad] Pad065
  BaseFeature = -> Pad064
  Direction = (1,-2e-16,6e-16)
  Length = 50
  Length2 = 10
  Placement = pos=(0,0,0) rot=(0.57735,0.57735,0.57735;2.0944rad)
  Profile = -> Pad064 [Edge20]
  Type = 0
FEATURE [PartDesign::Body] Body170
  Group = -> [Sketch185,Pad064,Pad065]
  Origin = -> Origin215
  Tip = -> Pad065
FEATURE [App::Part] Part044  label="tornillo M6-30-007"
  Group = -> [Body170]
  Origin = -> Origin214
  Placement = pos=(10,344,10) rot=(0,0,1;-1.5708rad)
FEATURE [Sketcher::SketchObject] Sketch186
  FullyConstrained = false
  MapMode = 5
  Placement = pos=(0,0,0) rot=(0.57735,0.57735,0.57735;2.0944rad)
  Support = -> [YZ_Plane211]
  sketch-geometry (8):
    g0: LineSegment StartX=3.44519 StartY=-3.62363 StartZ=0 EndX=4.86075 EndY=1.17181 EndZ=0
    g1: LineSegment StartX=4.86075 StartY=1.17181 StartZ=0 EndX=1.41556 EndY=4.79544 EndZ=0
    g2: LineSegment StartX=1.41556 StartY=4.79544 StartZ=0 EndX=-3.44519 EndY=3.62363 EndZ=0
    g3: LineSegment StartX=-3.44519 StartY=3.62363 StartZ=0 EndX=-4.86075 EndY=-1.17181 EndZ=0
    g4: LineSegment StartX=-4.86075 StartY=-1.17181 StartZ=0 EndX=-1.41556 EndY=-4.79544 EndZ=0
    g5: LineSegment StartX=-1.41556 StartY=-4.79544 StartZ=0 EndX=3.44519 EndY=-3.62363 EndZ=0
    g6: Circle CenterX=0 CenterY=0 CenterZ=0 NormalX=0 NormalY=0 NormalZ=1 AngleXU=0 Radius=5
    g7: Circle CenterX=0 CenterY=0 CenterZ=0 NormalX=0 NormalY=0 NormalZ=1 AngleXU=0 Radius=3
  constraints (17):
    c: Coincident(g0,g1)
    c: Coincident(g1,g2)
    c: Coincident(g2,g3)
    c: Coincident(g3,g4)
    c: Coincident(g4,g5)
    c: Coincident(g5,g0)
    c: Equal(g0, g1-g5) x5
    c: PointOnObject(g0,g6)
    c: PointOnObject(g1,g6)
    c: PointOnObject(g2,g6)
    c: PointOnObject(g3,g6)
    c: PointOnObject(g4,g6)
    c: PointOnObject(g5,g6)
    c: Coincident(g6,g-1)
    c: Coincident(g7,g6)
    c: Radius(g7) = 3
    c: Radius(g6) = 5
FEATURE [PartDesign::Pad] Pad066
  Direction = (1,-2e-16,3e-16)
  Length = 3
  Length2 = 10
  Placement = pos=(0,0,0) rot=(0.57735,0.57735,0.57735;2.0944rad)
  Profile = -> Sketch186
  Type = 0
FEATURE [PartDesign::Pad] Pad067
  BaseFeature = -> Pad066
  Direction = (1,-2e-16,6e-16)
  Length = 50
  Length2 = 10
  Placement = pos=(0,0,0) rot=(0.57735,0.57735,0.57735;2.0944rad)
  Profile = -> Pad066 [Edge20]
  Type = 0
FEATURE [PartDesign::Body] Body171
  Group = -> [Sketch186,Pad066,Pad067]
  Origin = -> Origin217
  Tip = -> Pad067
FEATURE [App::Part] Part045  label="tornillo M6-30-008"
  Group = -> [Body171]
  Origin = -> Origin216
  Placement = pos=(10,344,180) rot=(0,0,1;-1.5708rad)
FEATURE [Sketcher::SketchObject] Sketch187
  FullyConstrained = false
  MapMode = 5
  Placement = pos=(0,0,0) rot=(0.57735,0.57735,0.57735;2.0944rad)
  Support = -> [YZ_Plane213]
  sketch-geometry (8):
    g0: LineSegment StartX=2.8963 StartY=-2.75889 StartZ=0 EndX=3.83742 EndY=1.12882 EndZ=0
    g1: LineSegment StartX=3.83742 StartY=1.12882 StartZ=0 EndX=0.941117 EndY=3.88771 EndZ=0
    g2: LineSegment StartX=0.941117 StartY=3.88771 StartZ=0 EndX=-2.8963 EndY=2.75889 EndZ=0
    g3: LineSegment StartX=-2.8963 StartY=2.75889 StartZ=0 EndX=-3.83742 EndY=-1.12882 EndZ=0
    g4: LineSegment StartX=-3.83742 StartY=-1.12882 StartZ=0 EndX=-0.941117 EndY=-3.88771 EndZ=0
    g5: LineSegment StartX=-0.941117 StartY=-3.88771 StartZ=0 EndX=2.8963 EndY=-2.75889 EndZ=0
    g6: Circle CenterX=0 CenterY=0 CenterZ=0 NormalX=0 NormalY=0 NormalZ=1 AngleXU=0 Radius=4
    g7: Circle CenterX=0 CenterY=0 CenterZ=0 NormalX=0 NormalY=0 NormalZ=1 AngleXU=0 Radius=2.5
  constraints (17):
    c: Coincident(g0,g1)
    c: Coincident(g1,g2)
    c: Coincident(g2,g3)
    c: Coincident(g3,g4)
    c: Coincident(g4,g5)
    c: Coincident(g5,g0)
    c: Equal(g0, g1-g5) x5
    c: PointOnObject(g0,g6)
    c: PointOnObject(g1,g6)
    c: PointOnObject(g2,g6)
    c: PointOnObject(g3,g6)
    c: PointOnObject(g4,g6)
    c: PointOnObject(g5,g6)
    c: Coincident(g6,g-1)
    c: Coincident(g7,g6)
    c: Radius(g7) = 2.5
    c: Radius(g6) = 4
FEATURE [PartDesign::Pad] Pad068
  Direction = (1,-2e-16,3e-16)
  Length = 3
  Length2 = 10
  Placement = pos=(0,0,0) rot=(0.57735,0.57735,0.57735;2.0944rad)
  Profile = -> Sketch187
  Type = 0
FEATURE [PartDesign::Pad] Pad069
  BaseFeature = -> Pad068
  Direction = (1,-2e-16,6e-16)
  Length = 15
  Length2 = 10
  Placement = pos=(0,0,0) rot=(0.57735,0.57735,0.57735;2.0944rad)
  Profile = -> Pad068 [Edge20]
  Type = 0
FEATURE [PartDesign::Body] Body172
  Group = -> [Sketch187,Pad068,Pad069]
  Origin = -> Origin219
  Tip = -> Pad069
FEATURE [App::Part] Part046  label="tornillo M5-15-001"
  Group = -> [Body172]
  Origin = -> Origin218
  Placement = pos=(10,267,98) rot=(0,1,0;1.5708rad)
FEATURE [Sketcher::SketchObject] Sketch188
  FullyConstrained = false
  MapMode = 5
  Placement = pos=(0,0,0) rot=(0.57735,0.57735,0.57735;2.0944rad)
  Support = -> [YZ_Plane215]
  sketch-geometry (8):
    g0: LineSegment StartX=2.8963 StartY=-2.75889 StartZ=0 EndX=3.83742 EndY=1.12882 EndZ=0
    g1: LineSegment StartX=3.83742 StartY=1.12882 StartZ=0 EndX=0.941117 EndY=3.88771 EndZ=0
    g2: LineSegment StartX=0.941117 StartY=3.88771 StartZ=0 EndX=-2.8963 EndY=2.75889 EndZ=0
    g3: LineSegment StartX=-2.8963 StartY=2.75889 StartZ=0 EndX=-3.83742 EndY=-1.12882 EndZ=0
    g4: LineSegment StartX=-3.83742 StartY=-1.12882 StartZ=0 EndX=-0.941117 EndY=-3.88771 EndZ=0
    g5: LineSegment StartX=-0.941117 StartY=-3.88771 StartZ=0 EndX=2.8963 EndY=-2.75889 EndZ=0
    g6: Circle CenterX=0 CenterY=0 CenterZ=0 NormalX=0 NormalY=0 NormalZ=1 AngleXU=0 Radius=4
    g7: Circle CenterX=0 CenterY=0 CenterZ=0 NormalX=0 NormalY=0 NormalZ=1 AngleXU=0 Radius=2.5
  constraints (17):
    c: Coincident(g0,g1)
    c: Coincident(g1,g2)
    c: Coincident(g2,g3)
    c: Coincident(g3,g4)
    c: Coincident(g4,g5)
    c: Coincident(g5,g0)
    c: Equal(g0, g1-g5) x5
    c: PointOnObject(g0,g6)
    c: PointOnObject(g1,g6)
    c: PointOnObject(g2,g6)
    c: PointOnObject(g3,g6)
    c: PointOnObject(g4,g6)
    c: PointOnObject(g5,g6)
    c: Coincident(g6,g-1)
    c: Coincident(g7,g6)
    c: Radius(g7) = 2.5
    c: Radius(g6) = 4
FEATURE [PartDesign::Pad] Pad070
  Direction = (1,-2e-16,3e-16)
  Length = 3
  Length2 = 10
  Placement = pos=(0,0,0) rot=(0.57735,0.57735,0.57735;2.0944rad)
  Profile = -> Sketch188
  Type = 0
FEATURE [PartDesign::Pad] Pad071
  BaseFeature = -> Pad070
  Direction = (1,-2e-16,6e-16)
  Length = 15
  Length2 = 10
  Placement = pos=(0,0,0) rot=(0.57735,0.57735,0.57735;2.0944rad)
  Profile = -> Pad070 [Edge20]
  Type = 0
FEATURE [PartDesign::Body] Body173
  Group = -> [Sketch188,Pad070,Pad071]
  Origin = -> Origin221
  Tip = -> Pad071
FEATURE [App::Part] Part047  label="tornillo M5-15-002"
  Group = -> [Body173]
  Origin = -> Origin220
  Placement = pos=(10,99,98) rot=(0,1,0;1.5708rad)
FEATURE [Sketcher::SketchObject] Sketch189
  FullyConstrained = false
  MapMode = 5
  Placement = pos=(0,0,0) rot=(0.57735,0.57735,0.57735;2.0944rad)
  Support = -> [YZ_Plane217]
  sketch-geometry (8):
    g0: LineSegment StartX=2.8963 StartY=-2.75889 StartZ=0 EndX=3.83742 EndY=1.12882 EndZ=0
    g1: LineSegment StartX=3.83742 StartY=1.12882 StartZ=0 EndX=0.941117 EndY=3.88771 EndZ=0
    g2: LineSegment StartX=0.941117 StartY=3.88771 StartZ=0 EndX=-2.8963 EndY=2.75889 EndZ=0
    g3: LineSegment StartX=-2.8963 StartY=2.75889 StartZ=0 EndX=-3.83742 EndY=-1.12882 EndZ=0
    g4: LineSegment StartX=-3.83742 StartY=-1.12882 StartZ=0 EndX=-0.941117 EndY=-3.88771 EndZ=0
    g5: LineSegment StartX=-0.941117 StartY=-3.88771 StartZ=0 EndX=2.8963 EndY=-2.75889 EndZ=0
    g6: Circle CenterX=0 CenterY=0 CenterZ=0 NormalX=0 NormalY=0 NormalZ=1 AngleXU=0 Radius=4
    g7: Circle CenterX=0 CenterY=0 CenterZ=0 NormalX=0 NormalY=0 NormalZ=1 AngleXU=0 Radius=2.5
  constraints (17):
    c: Coincident(g0,g1)
    c: Coincident(g1,g2)
    c: Coincident(g2,g3)
    c: Coincident(g3,g4)
    c: Coincident(g4,g5)
    c: Coincident(g5,g0)
    c: Equal(g0, g1-g5) x5
    c: PointOnObject(g0,g6)
    c: PointOnObject(g1,g6)
    c: PointOnObject(g2,g6)
    c: PointOnObject(g3,g6)
    c: PointOnObject(g4,g6)
    c: PointOnObject(g5,g6)
    c: Coincident(g6,g-1)
    c: Coincident(g7,g6)
    c: Radius(g7) = 2.5
    c: Radius(g6) = 4
FEATURE [PartDesign::Pad] Pad072
  Direction = (1,-2e-16,3e-16)
  Length = 3
  Length2 = 10
  Placement = pos=(0,0,0) rot=(0.57735,0.57735,0.57735;2.0944rad)
  Profile = -> Sketch189
  Type = 0
FEATURE [PartDesign::Pad] Pad073
  BaseFeature = -> Pad072
  Direction = (1,-2e-16,6e-16)
  Length = 15
  Length2 = 10
  Placement = pos=(0,0,0) rot=(0.57735,0.57735,0.57735;2.0944rad)
  Profile = -> Pad072 [Edge20]
  Type = 0
FEATURE [PartDesign::Body] Body174
  Group = -> [Sketch189,Pad072,Pad073]
  Origin = -> Origin223
  Tip = -> Pad073
FEATURE [App::Part] Part048  label="tornillo M5-15-003"
  Group = -> [Body174]
  Origin = -> Origin222
  Placement = pos=(10,225,98) rot=(0,1,0;1.5708rad)
FEATURE [Sketcher::SketchObject] Sketch190
  FullyConstrained = false
  MapMode = 5
  Placement = pos=(0,0,0) rot=(0.57735,0.57735,0.57735;2.0944rad)
  Support = -> [YZ_Plane219]
  sketch-geometry (8):
    g0: LineSegment StartX=2.8963 StartY=-2.75889 StartZ=0 EndX=3.83742 EndY=1.12882 EndZ=0
    g1: LineSegment StartX=3.83742 StartY=1.12882 StartZ=0 EndX=0.941117 EndY=3.88771 EndZ=0
    g2: LineSegment StartX=0.941117 StartY=3.88771 StartZ=0 EndX=-2.8963 EndY=2.75889 EndZ=0
    g3: LineSegment StartX=-2.8963 StartY=2.75889 StartZ=0 EndX=-3.83742 EndY=-1.12882 EndZ=0
    g4: LineSegment StartX=-3.83742 StartY=-1.12882 StartZ=0 EndX=-0.941117 EndY=-3.88771 EndZ=0
    g5: LineSegment StartX=-0.941117 StartY=-3.88771 StartZ=0 EndX=2.8963 EndY=-2.75889 EndZ=0
    g6: Circle CenterX=0 CenterY=0 CenterZ=0 NormalX=0 NormalY=0 NormalZ=1 AngleXU=0 Radius=4
    g7: Circle CenterX=0 CenterY=0 CenterZ=0 NormalX=0 NormalY=0 NormalZ=1 AngleXU=0 Radius=2.5
  constraints (17):
    c: Coincident(g0,g1)
    c: Coincident(g1,g2)
    c: Coincident(g2,g3)
    c: Coincident(g3,g4)
    c: Coincident(g4,g5)
    c: Coincident(g5,g0)
    c: Equal(g0, g1-g5) x5
    c: PointOnObject(g0,g6)
    c: PointOnObject(g1,g6)
    c: PointOnObject(g2,g6)
    c: PointOnObject(g3,g6)
    c: PointOnObject(g4,g6)
    c: PointOnObject(g5,g6)
    c: Coincident(g6,g-1)
    c: Coincident(g7,g6)
    c: Radius(g7) = 2.5
    c: Radius(g6) = 4
FEATURE [PartDesign::Pad] Pad074
  Direction = (1,-2e-16,3e-16)
  Length = 3
  Length2 = 10
  Placement = pos=(0,0,0) rot=(0.57735,0.57735,0.57735;2.0944rad)
  Profile = -> Sketch190
  Type = 0
FEATURE [PartDesign::Pad] Pad075
  BaseFeature = -> Pad074
  Direction = (1,-2e-16,6e-16)
  Length = 15
  Length2 = 10
  Placement = pos=(0,0,0) rot=(0.57735,0.57735,0.57735;2.0944rad)
  Profile = -> Pad074 [Edge20]
  Type = 0
FEATURE [PartDesign::Body] Body175
  Group = -> [Sketch190,Pad074,Pad075]
  Origin = -> Origin225
  Tip = -> Pad075
FEATURE [App::Part] Part049  label="tornillo M5-15-004"
  Group = -> [Body175]
  Origin = -> Origin224
  Placement = pos=(10,141,98) rot=(0,1,0;1.5708rad)
FEATURE [Sketcher::SketchObject] Sketch191
  FullyConstrained = false
  MapMode = 5
  Placement = pos=(0,0,0) rot=(0.57735,0.57735,0.57735;2.0944rad)
  Support = -> [YZ_Plane221]
  sketch-geometry (8):
    g0: LineSegment StartX=2.8963 StartY=-2.75889 StartZ=0 EndX=3.83742 EndY=1.12882 EndZ=0
    g1: LineSegment StartX=3.83742 StartY=1.12882 StartZ=0 EndX=0.941117 EndY=3.88771 EndZ=0
    g2: LineSegment StartX=0.941117 StartY=3.88771 StartZ=0 EndX=-2.8963 EndY=2.75889 EndZ=0
    g3: LineSegment StartX=-2.8963 StartY=2.75889 StartZ=0 EndX=-3.83742 EndY=-1.12882 EndZ=0
    g4: LineSegment StartX=-3.83742 StartY=-1.12882 StartZ=0 EndX=-0.941117 EndY=-3.88771 EndZ=0
    g5: LineSegment StartX=-0.941117 StartY=-3.88771 StartZ=0 EndX=2.8963 EndY=-2.75889 EndZ=0
    g6: Circle CenterX=0 CenterY=0 CenterZ=0 NormalX=0 NormalY=0 NormalZ=1 AngleXU=0 Radius=4
    g7: Circle CenterX=0 CenterY=0 CenterZ=0 NormalX=0 NormalY=0 NormalZ=1 AngleXU=0 Radius=2.5
  constraints (17):
    c: Coincident(g0,g1)
    c: Coincident(g1,g2)
    c: Coincident(g2,g3)
    c: Coincident(g3,g4)
    c: Coincident(g4,g5)
    c: Coincident(g5,g0)
    c: Equal(g0, g1-g5) x5
    c: PointOnObject(g0,g6)
    c: PointOnObject(g1,g6)
    c: PointOnObject(g2,g6)
    c: PointOnObject(g3,g6)
    c: PointOnObject(g4,g6)
    c: PointOnObject(g5,g6)
    c: Coincident(g6,g-1)
    c: Coincident(g7,g6)
    c: Radius(g7) = 2.5
    c: Radius(g6) = 4
FEATURE [PartDesign::Pad] Pad076
  Direction = (1,-2e-16,3e-16)
  Length = 3
  Length2 = 10
  Placement = pos=(0,0,0) rot=(0.57735,0.57735,0.57735;2.0944rad)
  Profile = -> Sketch191
  Type = 0
FEATURE [PartDesign::Pad] Pad077
  BaseFeature = -> Pad076
  Direction = (1,-2e-16,6e-16)
  Length = 15
  Length2 = 10
  Placement = pos=(0,0,0) rot=(0.57735,0.57735,0.57735;2.0944rad)
  Profile = -> Pad076 [Edge20]
  Type = 0
FEATURE [PartDesign::Body] Body176
  Group = -> [Sketch191,Pad076,Pad077]
  Origin = -> Origin227
  Tip = -> Pad077
FEATURE [App::Part] Part050  label="tornillo M5-15-005"
  Group = -> [Body176]
  Origin = -> Origin226
  Placement = pos=(332,267,98) rot=(0,1,0;1.5708rad)
FEATURE [Sketcher::SketchObject] Sketch192
  FullyConstrained = false
  MapMode = 5
  Placement = pos=(0,0,0) rot=(0.57735,0.57735,0.57735;2.0944rad)
  Support = -> [YZ_Plane223]
  sketch-geometry (8):
    g0: LineSegment StartX=2.8963 StartY=-2.75889 StartZ=0 EndX=3.83742 EndY=1.12882 EndZ=0
    g1: LineSegment StartX=3.83742 StartY=1.12882 StartZ=0 EndX=0.941117 EndY=3.88771 EndZ=0
    g2: LineSegment StartX=0.941117 StartY=3.88771 StartZ=0 EndX=-2.8963 EndY=2.75889 EndZ=0
    g3: LineSegment StartX=-2.8963 StartY=2.75889 StartZ=0 EndX=-3.83742 EndY=-1.12882 EndZ=0
    g4: LineSegment StartX=-3.83742 StartY=-1.12882 StartZ=0 EndX=-0.941117 EndY=-3.88771 EndZ=0
    g5: LineSegment StartX=-0.941117 StartY=-3.88771 StartZ=0 EndX=2.8963 EndY=-2.75889 EndZ=0
    g6: Circle CenterX=0 CenterY=0 CenterZ=0 NormalX=0 NormalY=0 NormalZ=1 AngleXU=0 Radius=4
    g7: Circle CenterX=0 CenterY=0 CenterZ=0 NormalX=0 NormalY=0 NormalZ=1 AngleXU=0 Radius=2.5
  constraints (17):
    c: Coincident(g0,g1)
    c: Coincident(g1,g2)
    c: Coincident(g2,g3)
    c: Coincident(g3,g4)
    c: Coincident(g4,g5)
    c: Coincident(g5,g0)
    c: Equal(g0, g1-g5) x5
    c: PointOnObject(g0,g6)
    c: PointOnObject(g1,g6)
    c: PointOnObject(g2,g6)
    c: PointOnObject(g3,g6)
    c: PointOnObject(g4,g6)
    c: PointOnObject(g5,g6)
    c: Coincident(g6,g-1)
    c: Coincident(g7,g6)
    c: Radius(g7) = 2.5
    c: Radius(g6) = 4
FEATURE [PartDesign::Pad] Pad078
  Direction = (1,-2e-16,3e-16)
  Length = 3
  Length2 = 10
  Placement = pos=(0,0,0) rot=(0.57735,0.57735,0.57735;2.0944rad)
  Profile = -> Sketch192
  Type = 0
FEATURE [PartDesign::Pad] Pad079
  BaseFeature = -> Pad078
  Direction = (1,-2e-16,6e-16)
  Length = 15
  Length2 = 10
  Placement = pos=(0,0,0) rot=(0.57735,0.57735,0.57735;2.0944rad)
  Profile = -> Pad078 [Edge20]
  Type = 0
FEATURE [PartDesign::Body] Body177
  Group = -> [Sketch192,Pad078,Pad079]
  Origin = -> Origin229
  Tip = -> Pad079
FEATURE [App::Part] Part051  label="tornillo M5-15-006"
  Group = -> [Body177]
  Origin = -> Origin228
  Placement = pos=(332,225,98) rot=(0,1,0;1.5708rad)
FEATURE [Sketcher::SketchObject] Sketch193
  FullyConstrained = false
  MapMode = 5
  Placement = pos=(0,0,0) rot=(0.57735,0.57735,0.57735;2.0944rad)
  Support = -> [YZ_Plane225]
  sketch-geometry (8):
    g0: LineSegment StartX=2.8963 StartY=-2.75889 StartZ=0 EndX=3.83742 EndY=1.12882 EndZ=0
    g1: LineSegment StartX=3.83742 StartY=1.12882 StartZ=0 EndX=0.941117 EndY=3.88771 EndZ=0
    g2: LineSegment StartX=0.941117 StartY=3.88771 StartZ=0 EndX=-2.8963 EndY=2.75889 EndZ=0
    g3: LineSegment StartX=-2.8963 StartY=2.75889 StartZ=0 EndX=-3.83742 EndY=-1.12882 EndZ=0
    g4: LineSegment StartX=-3.83742 StartY=-1.12882 StartZ=0 EndX=-0.941117 EndY=-3.88771 EndZ=0
    g5: LineSegment StartX=-0.941117 StartY=-3.88771 StartZ=0 EndX=2.8963 EndY=-2.75889 EndZ=0
    g6: Circle CenterX=0 CenterY=0 CenterZ=0 NormalX=0 NormalY=0 NormalZ=1 AngleXU=0 Radius=4
    g7: Circle CenterX=0 CenterY=0 CenterZ=0 NormalX=0 NormalY=0 NormalZ=1 AngleXU=0 Radius=2.5
  constraints (17):
    c: Coincident(g0,g1)
    c: Coincident(g1,g2)
    c: Coincident(g2,g3)
    c: Coincident(g3,g4)
    c: Coincident(g4,g5)
    c: Coincident(g5,g0)
    c: Equal(g0, g1-g5) x5
    c: PointOnObject(g0,g6)
    c: PointOnObject(g1,g6)
    c: PointOnObject(g2,g6)
    c: PointOnObject(g3,g6)
    c: PointOnObject(g4,g6)
    c: PointOnObject(g5,g6)
    c: Coincident(g6,g-1)
    c: Coincident(g7,g6)
    c: Radius(g7) = 2.5
    c: Radius(g6) = 4
FEATURE [PartDesign::Pad] Pad080
  Direction = (1,-2e-16,3e-16)
  Length = 3
  Length2 = 10
  Placement = pos=(0,0,0) rot=(0.57735,0.57735,0.57735;2.0944rad)
  Profile = -> Sketch193
  Type = 0
FEATURE [PartDesign::Pad] Pad081
  BaseFeature = -> Pad080
  Direction = (1,-2e-16,6e-16)
  Length = 15
  Length2 = 10
  Placement = pos=(0,0,0) rot=(0.57735,0.57735,0.57735;2.0944rad)
  Profile = -> Pad080 [Edge20]
  Type = 0
FEATURE [PartDesign::Body] Body178
  Group = -> [Sketch193,Pad080,Pad081]
  Origin = -> Origin231
  Tip = -> Pad081
FEATURE [App::Part] Part052  label="tornillo M5-15-007"
  Group = -> [Body178]
  Origin = -> Origin230
  Placement = pos=(332,99,98) rot=(0,1,0;1.5708rad)
FEATURE [Sketcher::SketchObject] Sketch194
  FullyConstrained = false
  MapMode = 5
  Placement = pos=(0,0,0) rot=(0.57735,0.57735,0.57735;2.0944rad)
  Support = -> [YZ_Plane227]
  sketch-geometry (8):
    g0: LineSegment StartX=2.8963 StartY=-2.75889 StartZ=0 EndX=3.83742 EndY=1.12882 EndZ=0
    g1: LineSegment StartX=3.83742 StartY=1.12882 StartZ=0 EndX=0.941117 EndY=3.88771 EndZ=0
    g2: LineSegment StartX=0.941117 StartY=3.88771 StartZ=0 EndX=-2.8963 EndY=2.75889 EndZ=0
    g3: LineSegment StartX=-2.8963 StartY=2.75889 StartZ=0 EndX=-3.83742 EndY=-1.12882 EndZ=0
    g4: LineSegment StartX=-3.83742 StartY=-1.12882 StartZ=0 EndX=-0.941117 EndY=-3.88771 EndZ=0
    g5: LineSegment StartX=-0.941117 StartY=-3.88771 StartZ=0 EndX=2.8963 EndY=-2.75889 EndZ=0
    g6: Circle CenterX=0 CenterY=0 CenterZ=0 NormalX=0 NormalY=0 NormalZ=1 AngleXU=0 Radius=4
    g7: Circle CenterX=0 CenterY=0 CenterZ=0 NormalX=0 NormalY=0 NormalZ=1 AngleXU=0 Radius=2.5
  constraints (17):
    c: Coincident(g0,g1)
    c: Coincident(g1,g2)
    c: Coincident(g2,g3)
    c: Coincident(g3,g4)
    c: Coincident(g4,g5)
    c: Coincident(g5,g0)
    c: Equal(g0, g1-g5) x5
    c: PointOnObject(g0,g6)
    c: PointOnObject(g1,g6)
    c: PointOnObject(g2,g6)
    c: PointOnObject(g3,g6)
    c: PointOnObject(g4,g6)
    c: PointOnObject(g5,g6)
    c: Coincident(g6,g-1)
    c: Coincident(g7,g6)
    c: Radius(g7) = 2.5
    c: Radius(g6) = 4
FEATURE [PartDesign::Pad] Pad082
  Direction = (1,-2e-16,3e-16)
  Length = 3
  Length2 = 10
  Placement = pos=(0,0,0) rot=(0.57735,0.57735,0.57735;2.0944rad)
  Profile = -> Sketch194
  Type = 0
FEATURE [PartDesign::Pad] Pad083
  BaseFeature = -> Pad082
  Direction = (1,-2e-16,6e-16)
  Length = 15
  Length2 = 10
  Placement = pos=(0,0,0) rot=(0.57735,0.57735,0.57735;2.0944rad)
  Profile = -> Pad082 [Edge20]
  Type = 0
FEATURE [PartDesign::Body] Body179
  Group = -> [Sketch194,Pad082,Pad083]
  Origin = -> Origin233
  Tip = -> Pad083
FEATURE [App::Part] Part053  label="tornillo M5-15-008"
  Group = -> [Body179]
  Origin = -> Origin232
  Placement = pos=(332,141,98) rot=(0,1,0;1.5708rad)
FEATURE [Sketcher::SketchObject] Sketch195
  FullyConstrained = false
  MapMode = 5
  Placement = pos=(0,0,0) rot=(0.57735,0.57735,0.57735;2.0944rad)
  Support = -> [YZ_Plane229]
  sketch-geometry (8):
    g0: LineSegment StartX=2.8963 StartY=-2.75889 StartZ=0 EndX=3.83742 EndY=1.12882 EndZ=0
    g1: LineSegment StartX=3.83742 StartY=1.12882 StartZ=0 EndX=0.941117 EndY=3.88771 EndZ=0
    g2: LineSegment StartX=0.941117 StartY=3.88771 StartZ=0 EndX=-2.8963 EndY=2.75889 EndZ=0
    g3: LineSegment StartX=-2.8963 StartY=2.75889 StartZ=0 EndX=-3.83742 EndY=-1.12882 EndZ=0
    g4: LineSegment StartX=-3.83742 StartY=-1.12882 StartZ=0 EndX=-0.941117 EndY=-3.88771 EndZ=0
    g5: LineSegment StartX=-0.941117 StartY=-3.88771 StartZ=0 EndX=2.8963 EndY=-2.75889 EndZ=0
    g6: Circle CenterX=0 CenterY=0 CenterZ=0 NormalX=0 NormalY=0 NormalZ=1 AngleXU=0 Radius=4
    g7: Circle CenterX=0 CenterY=0 CenterZ=0 NormalX=0 NormalY=0 NormalZ=1 AngleXU=0 Radius=2.5
  constraints (17):
    c: Coincident(g0,g1)
    c: Coincident(g1,g2)
    c: Coincident(g2,g3)
    c: Coincident(g3,g4)
    c: Coincident(g4,g5)
    c: Coincident(g5,g0)
    c: Equal(g0, g1-g5) x5
    c: PointOnObject(g0,g6)
    c: PointOnObject(g1,g6)
    c: PointOnObject(g2,g6)
    c: PointOnObject(g3,g6)
    c: PointOnObject(g4,g6)
    c: PointOnObject(g5,g6)
    c: Coincident(g6,g-1)
    c: Coincident(g7,g6)
    c: Radius(g7) = 2.5
    c: Radius(g6) = 4
FEATURE [PartDesign::Pad] Pad084
  Direction = (1,-2e-16,3e-16)
  Length = 3
  Length2 = 10
  Placement = pos=(0,0,0) rot=(0.57735,0.57735,0.57735;2.0944rad)
  Profile = -> Sketch195
  Type = 0
FEATURE [PartDesign::Pad] Pad085
  BaseFeature = -> Pad084
  Direction = (1,-2e-16,6e-16)
  Length = 15
  Length2 = 10
  Placement = pos=(0,0,0) rot=(0.57735,0.57735,0.57735;2.0944rad)
  Profile = -> Pad084 [Edge20]
  Type = 0
FEATURE [PartDesign::Body] Body180
  Group = -> [Sketch195,Pad084,Pad085]
  Origin = -> Origin235
  Tip = -> Pad085
FEATURE [App::Part] Part054  label="tornillo M5-15-009"
  Group = -> [Body180]
  Origin = -> Origin234
  Placement = pos=(313,101,79) rot=(0,0,1;0rad)
FEATURE [Sketcher::SketchObject] Sketch196
  FullyConstrained = false
  MapMode = 5
  Placement = pos=(0,0,0) rot=(0.57735,0.57735,0.57735;2.0944rad)
  Support = -> [YZ_Plane231]
  sketch-geometry (8):
    g0: LineSegment StartX=2.8963 StartY=-2.75889 StartZ=0 EndX=3.83742 EndY=1.12882 EndZ=0
    g1: LineSegment StartX=3.83742 StartY=1.12882 StartZ=0 EndX=0.941117 EndY=3.88771 EndZ=0
    g2: LineSegment StartX=0.941117 StartY=3.88771 StartZ=0 EndX=-2.8963 EndY=2.75889 EndZ=0
    g3: LineSegment StartX=-2.8963 StartY=2.75889 StartZ=0 EndX=-3.83742 EndY=-1.12882 EndZ=0
    g4: LineSegment StartX=-3.83742 StartY=-1.12882 StartZ=0 EndX=-0.941117 EndY=-3.88771 EndZ=0
    g5: LineSegment StartX=-0.941117 StartY=-3.88771 StartZ=0 EndX=2.8963 EndY=-2.75889 EndZ=0
    g6: Circle CenterX=0 CenterY=0 CenterZ=0 NormalX=0 NormalY=0 NormalZ=1 AngleXU=0 Radius=4
    g7: Circle CenterX=0 CenterY=0 CenterZ=0 NormalX=0 NormalY=0 NormalZ=1 AngleXU=0 Radius=2.5
  constraints (17):
    c: Coincident(g0,g1)
    c: Coincident(g1,g2)
    c: Coincident(g2,g3)
    c: Coincident(g3,g4)
    c: Coincident(g4,g5)
    c: Coincident(g5,g0)
    c: Equal(g0, g1-g5) x5
    c: PointOnObject(g0,g6)
    c: PointOnObject(g1,g6)
    c: PointOnObject(g2,g6)
    c: PointOnObject(g3,g6)
    c: PointOnObject(g4,g6)
    c: PointOnObject(g5,g6)
    c: Coincident(g6,g-1)
    c: Coincident(g7,g6)
    c: Radius(g7) = 2.5
    c: Radius(g6) = 4
FEATURE [PartDesign::Pad] Pad086
  Direction = (1,-2e-16,3e-16)
  Length = 3
  Length2 = 10
  Placement = pos=(0,0,0) rot=(0.57735,0.57735,0.57735;2.0944rad)
  Profile = -> Sketch196
  Type = 0
FEATURE [PartDesign::Pad] Pad087
  BaseFeature = -> Pad086
  Direction = (1,-2e-16,6e-16)
  Length = 15
  Length2 = 10
  Placement = pos=(0,0,0) rot=(0.57735,0.57735,0.57735;2.0944rad)
  Profile = -> Pad086 [Edge20]
  Type = 0
FEATURE [PartDesign::Body] Body181
  Group = -> [Sketch196,Pad086,Pad087]
  Origin = -> Origin237
  Tip = -> Pad087
FEATURE [App::Part] Part055  label="tornillo M5-15-010"
  Group = -> [Body181]
  Origin = -> Origin236
  Placement = pos=(26,101,79) rot=(0,0,1;3.14159rad)
FEATURE [Sketcher::SketchObject] Sketch197
  FullyConstrained = false
  MapMode = 5
  Placement = pos=(0,0,0) rot=(0.57735,0.57735,0.57735;2.0944rad)
  Support = -> [YZ_Plane233]
  sketch-geometry (8):
    g0: LineSegment StartX=2.8963 StartY=-2.75889 StartZ=0 EndX=3.83742 EndY=1.12882 EndZ=0
    g1: LineSegment StartX=3.83742 StartY=1.12882 StartZ=0 EndX=0.941117 EndY=3.88771 EndZ=0
    g2: LineSegment StartX=0.941117 StartY=3.88771 StartZ=0 EndX=-2.8963 EndY=2.75889 EndZ=0
    g3: LineSegment StartX=-2.8963 StartY=2.75889 StartZ=0 EndX=-3.83742 EndY=-1.12882 EndZ=0
    g4: LineSegment StartX=-3.83742 StartY=-1.12882 StartZ=0 EndX=-0.941117 EndY=-3.88771 EndZ=0
    g5: LineSegment StartX=-0.941117 StartY=-3.88771 StartZ=0 EndX=2.8963 EndY=-2.75889 EndZ=0
    g6: Circle CenterX=0 CenterY=0 CenterZ=0 NormalX=0 NormalY=0 NormalZ=1 AngleXU=0 Radius=4
    g7: Circle CenterX=0 CenterY=0 CenterZ=0 NormalX=0 NormalY=0 NormalZ=1 AngleXU=0 Radius=2.5
  constraints (17):
    c: Coincident(g0,g1)
    c: Coincident(g1,g2)
    c: Coincident(g2,g3)
    c: Coincident(g3,g4)
    c: Coincident(g4,g5)
    c: Coincident(g5,g0)
    c: Equal(g0, g1-g5) x5
    c: PointOnObject(g0,g6)
    c: PointOnObject(g1,g6)
    c: PointOnObject(g2,g6)
    c: PointOnObject(g3,g6)
    c: PointOnObject(g4,g6)
    c: PointOnObject(g5,g6)
    c: Coincident(g6,g-1)
    c: Coincident(g7,g6)
    c: Radius(g7) = 2.5
    c: Radius(g6) = 4
FEATURE [PartDesign::Pad] Pad088
  Direction = (1,-2e-16,3e-16)
  Length = 3
  Length2 = 10
  Placement = pos=(0,0,0) rot=(0.57735,0.57735,0.57735;2.0944rad)
  Profile = -> Sketch197
  Type = 0
FEATURE [PartDesign::Pad] Pad089
  BaseFeature = -> Pad088
  Direction = (1,-2e-16,6e-16)
  Length = 15
  Length2 = 10
  Placement = pos=(0,0,0) rot=(0.57735,0.57735,0.57735;2.0944rad)
  Profile = -> Pad088 [Edge20]
  Type = 0
FEATURE [PartDesign::Body] Body182
  Group = -> [Sketch197,Pad088,Pad089]
  Origin = -> Origin239
  Tip = -> Pad089
FEATURE [App::Part] Part056  label="tornillo M5-15-011"
  Group = -> [Body182]
  Origin = -> Origin238
  Placement = pos=(26,139,79) rot=(0,0,1;3.14159rad)
FEATURE [Sketcher::SketchObject] Sketch198
  FullyConstrained = false
  MapMode = 5
  Placement = pos=(0,0,0) rot=(0.57735,0.57735,0.57735;2.0944rad)
  Support = -> [YZ_Plane235]
  sketch-geometry (8):
    g0: LineSegment StartX=2.8963 StartY=-2.75889 StartZ=0 EndX=3.83742 EndY=1.12882 EndZ=0
    g1: LineSegment StartX=3.83742 StartY=1.12882 StartZ=0 EndX=0.941117 EndY=3.88771 EndZ=0
    g2: LineSegment StartX=0.941117 StartY=3.88771 StartZ=0 EndX=-2.8963 EndY=2.75889 EndZ=0
    g3: LineSegment StartX=-2.8963 StartY=2.75889 StartZ=0 EndX=-3.83742 EndY=-1.12882 EndZ=0
    g4: LineSegment StartX=-3.83742 StartY=-1.12882 StartZ=0 EndX=-0.941117 EndY=-3.88771 EndZ=0
    g5: LineSegment StartX=-0.941117 StartY=-3.88771 StartZ=0 EndX=2.8963 EndY=-2.75889 EndZ=0
    g6: Circle CenterX=0 CenterY=0 CenterZ=0 NormalX=0 NormalY=0 NormalZ=1 AngleXU=0 Radius=4
    g7: Circle CenterX=0 CenterY=0 CenterZ=0 NormalX=0 NormalY=0 NormalZ=1 AngleXU=0 Radius=2.5
  constraints (17):
    c: Coincident(g0,g1)
    c: Coincident(g1,g2)
    c: Coincident(g2,g3)
    c: Coincident(g3,g4)
    c: Coincident(g4,g5)
    c: Coincident(g5,g0)
    c: Equal(g0, g1-g5) x5
    c: PointOnObject(g0,g6)
    c: PointOnObject(g1,g6)
    c: PointOnObject(g2,g6)
    c: PointOnObject(g3,g6)
    c: PointOnObject(g4,g6)
    c: PointOnObject(g5,g6)
    c: Coincident(g6,g-1)
    c: Coincident(g7,g6)
    c: Radius(g7) = 2.5
    c: Radius(g6) = 4
FEATURE [PartDesign::Pad] Pad090
  Direction = (1,-2e-16,3e-16)
  Length = 3
  Length2 = 10
  Placement = pos=(0,0,0) rot=(0.57735,0.57735,0.57735;2.0944rad)
  Profile = -> Sketch198
  Type = 0
FEATURE [PartDesign::Pad] Pad091
  BaseFeature = -> Pad090
  Direction = (1,-2e-16,6e-16)
  Length = 15
  Length2 = 10
  Placement = pos=(0,0,0) rot=(0.57735,0.57735,0.57735;2.0944rad)
  Profile = -> Pad090 [Edge20]
  Type = 0
FEATURE [PartDesign::Body] Body183
  Group = -> [Sketch198,Pad090,Pad091]
  Origin = -> Origin241
  Tip = -> Pad091
FEATURE [App::Part] Part057  label="tornillo M5-15-012"
  Group = -> [Body183]
  Origin = -> Origin240
  Placement = pos=(313,139,79) rot=(0,0,1;0rad)
FEATURE [Sketcher::SketchObject] Sketch199
  FullyConstrained = true
  MapMode = 5
  Placement = pos=(0,0,0) rot=(1,0,0;1.5708rad)
  Support = -> [XZ_Plane237]
  sketch-geometry (2):
    g0: Circle CenterX=0 CenterY=0 CenterZ=0 NormalX=0 NormalY=0 NormalZ=1 AngleXU=0 Radius=3
    g1: Circle CenterX=0 CenterY=0 CenterZ=0 NormalX=0 NormalY=0 NormalZ=1 AngleXU=0 Radius=9
  constraints (4):
    c: Coincident(g0,g-1)
    c: Coincident(g1,g0)
    c: Radius(g1) = 9
    c: Diameter(g0) = 6
FEATURE [PartDesign::Pad] Pad092
  Direction = (0,-1,2e-16)
  Length = 1
  Length2 = 10
  Placement = pos=(0,0,0) rot=(1,0,0;1.5708rad)
  Profile = -> Sketch199
  Type = 0
FEATURE [PartDesign::Body] Body184
  Group = -> [Sketch199,Pad092]
  Origin = -> Origin243
  Tip = -> Pad092
FEATURE [App::Part] Part058  label="Arandela M6-001"
  Group = -> [Body184]
  Origin = -> Origin242
  Placement = pos=(10,0,10) rot=(0,0,1;0rad)
FEATURE [Sketcher::SketchObject] Sketch200
  FullyConstrained = true
  MapMode = 5
  Placement = pos=(0,0,0) rot=(1,0,0;1.5708rad)
  Support = -> [XZ_Plane239]
  sketch-geometry (2):
    g0: Circle CenterX=0 CenterY=0 CenterZ=0 NormalX=0 NormalY=0 NormalZ=1 AngleXU=0 Radius=3
    g1: Circle CenterX=0 CenterY=0 CenterZ=0 NormalX=0 NormalY=0 NormalZ=1 AngleXU=0 Radius=9
  constraints (4):
    c: Coincident(g0,g-1)
    c: Coincident(g1,g0)
    c: Radius(g1) = 9
    c: Diameter(g0) = 6
FEATURE [PartDesign::Pad] Pad093
  Direction = (0,-1,2e-16)
  Length = 1
  Length2 = 10
  Placement = pos=(0,0,0) rot=(1,0,0;1.5708rad)
  Profile = -> Sketch200
  Type = 0
FEATURE [PartDesign::Body] Body185
  Group = -> [Sketch200,Pad093]
  Origin = -> Origin245
  Tip = -> Pad093
FEATURE [App::Part] Part059  label="Arandela M6-002"
  Group = -> [Body185]
  Origin = -> Origin244
  Placement = pos=(10,0,181) rot=(0,0,1;0rad)
FEATURE [Sketcher::SketchObject] Sketch201
  FullyConstrained = true
  MapMode = 5
  Placement = pos=(0,0,0) rot=(1,0,0;1.5708rad)
  Support = -> [XZ_Plane241]
  sketch-geometry (2):
    g0: Circle CenterX=0 CenterY=0 CenterZ=0 NormalX=0 NormalY=0 NormalZ=1 AngleXU=0 Radius=3
    g1: Circle CenterX=0 CenterY=0 CenterZ=0 NormalX=0 NormalY=0 NormalZ=1 AngleXU=0 Radius=9
  constraints (4):
    c: Coincident(g0,g-1)
    c: Coincident(g1,g0)
    c: Radius(g1) = 9
    c: Diameter(g0) = 6
FEATURE [PartDesign::Pad] Pad094
  Direction = (0,-1,2e-16)
  Length = 1
  Length2 = 10
  Placement = pos=(0,0,0) rot=(1,0,0;1.5708rad)
  Profile = -> Sketch201
  Type = 0
FEATURE [PartDesign::Body] Body186
  Group = -> [Sketch201,Pad094]
  Origin = -> Origin247
  Tip = -> Pad094
FEATURE [App::Part] Part060  label="Arandela M6-003"
  Group = -> [Body186]
  Origin = -> Origin246
  Placement = pos=(330,0,181) rot=(0,0,1;0rad)
FEATURE [Sketcher::SketchObject] Sketch202
  FullyConstrained = true
  MapMode = 5
  Placement = pos=(0,0,0) rot=(1,0,0;1.5708rad)
  Support = -> [XZ_Plane243]
  sketch-geometry (2):
    g0: Circle CenterX=0 CenterY=0 CenterZ=0 NormalX=0 NormalY=0 NormalZ=1 AngleXU=0 Radius=3
    g1: Circle CenterX=0 CenterY=0 CenterZ=0 NormalX=0 NormalY=0 NormalZ=1 AngleXU=0 Radius=9
  constraints (4):
    c: Coincident(g0,g-1)
    c: Coincident(g1,g0)
    c: Radius(g1) = 9
    c: Diameter(g0) = 6
FEATURE [PartDesign::Pad] Pad095
  Direction = (0,-1,2e-16)
  Length = 1
  Length2 = 10
  Placement = pos=(0,0,0) rot=(1,0,0;1.5708rad)
  Profile = -> Sketch202
  Type = 0
FEATURE [PartDesign::Body] Body187
  Group = -> [Sketch202,Pad095]
  Origin = -> Origin249
  Tip = -> Pad095
FEATURE [App::Part] Part061  label="Arandela M6-004"
  Group = -> [Body187]
  Origin = -> Origin248
  Placement = pos=(330,0,9) rot=(0,0,1;0rad)
FEATURE [Sketcher::SketchObject] Sketch203
  FullyConstrained = true
  MapMode = 5
  Placement = pos=(0,0,0) rot=(1,0,0;1.5708rad)
  Support = -> [XZ_Plane245]
  sketch-geometry (2):
    g0: Circle CenterX=0 CenterY=0 CenterZ=0 NormalX=0 NormalY=0 NormalZ=1 AngleXU=0 Radius=3
    g1: Circle CenterX=0 CenterY=0 CenterZ=0 NormalX=0 NormalY=0 NormalZ=1 AngleXU=0 Radius=9
  constraints (4):
    c: Coincident(g0,g-1)
    c: Coincident(g1,g0)
    c: Radius(g1) = 9
    c: Diameter(g0) = 6
FEATURE [PartDesign::Pad] Pad096
  Direction = (0,-1,2e-16)
  Length = 1
  Length2 = 10
  Placement = pos=(0,0,0) rot=(1,0,0;1.5708rad)
  Profile = -> Sketch203
  Type = 0
FEATURE [PartDesign::Body] Body188
  Group = -> [Sketch203,Pad096]
  Origin = -> Origin251
  Tip = -> Pad096
FEATURE [App::Part] Part062  label="Arandela M6-005"
  Group = -> [Body188]
  Origin = -> Origin250
  Placement = pos=(330,341,9) rot=(0,0,1;0rad)
FEATURE [Sketcher::SketchObject] Sketch204
  FullyConstrained = true
  MapMode = 5
  Placement = pos=(0,0,0) rot=(1,0,0;1.5708rad)
  Support = -> [XZ_Plane247]
  sketch-geometry (2):
    g0: Circle CenterX=0 CenterY=0 CenterZ=0 NormalX=0 NormalY=0 NormalZ=1 AngleXU=0 Radius=3
    g1: Circle CenterX=0 CenterY=0 CenterZ=0 NormalX=0 NormalY=0 NormalZ=1 AngleXU=0 Radius=9
  constraints (4):
    c: Coincident(g0,g-1)
    c: Coincident(g1,g0)
    c: Radius(g1) = 9
    c: Diameter(g0) = 6
FEATURE [PartDesign::Pad] Pad097
  Direction = (0,-1,2e-16)
  Length = 1
  Length2 = 10
  Placement = pos=(0,0,0) rot=(1,0,0;1.5708rad)
  Profile = -> Sketch204
  Type = 0
FEATURE [PartDesign::Body] Body189
  Group = -> [Sketch204,Pad097]
  Origin = -> Origin253
  Tip = -> Pad097
FEATURE [App::Part] Part063  label="Arandela M6-006"
  Group = -> [Body189]
  Origin = -> Origin252
  Placement = pos=(10,341,180) rot=(0,0,1;0rad)
FEATURE [Sketcher::SketchObject] Sketch205
  FullyConstrained = true
  MapMode = 5
  Placement = pos=(0,0,0) rot=(1,0,0;1.5708rad)
  Support = -> [XZ_Plane249]
  sketch-geometry (2):
    g0: Circle CenterX=0 CenterY=0 CenterZ=0 NormalX=0 NormalY=0 NormalZ=1 AngleXU=0 Radius=3
    g1: Circle CenterX=0 CenterY=0 CenterZ=0 NormalX=0 NormalY=0 NormalZ=1 AngleXU=0 Radius=9
  constraints (4):
    c: Coincident(g0,g-1)
    c: Coincident(g1,g0)
    c: Radius(g1) = 9
    c: Diameter(g0) = 6
FEATURE [PartDesign::Pad] Pad098
  Direction = (0,-1,2e-16)
  Length = 1
  Length2 = 10
  Placement = pos=(0,0,0) rot=(1,0,0;1.5708rad)
  Profile = -> Sketch205
  Type = 0
FEATURE [PartDesign::Body] Body190
  Group = -> [Sketch205,Pad098]
  Origin = -> Origin255
  Tip = -> Pad098
FEATURE [App::Part] Part064  label="Arandela M6-007"
  Group = -> [Body190]
  Origin = -> Origin254
  Placement = pos=(330,341,180) rot=(0,0,1;0rad)
FEATURE [Sketcher::SketchObject] Sketch206
  FullyConstrained = true
  MapMode = 5
  Placement = pos=(0,0,0) rot=(1,0,0;1.5708rad)
  Support = -> [XZ_Plane251]
  sketch-geometry (2):
    g0: Circle CenterX=0 CenterY=0 CenterZ=0 NormalX=0 NormalY=0 NormalZ=1 AngleXU=0 Radius=3
    g1: Circle CenterX=0 CenterY=0 CenterZ=0 NormalX=0 NormalY=0 NormalZ=1 AngleXU=0 Radius=9
  constraints (4):
    c: Coincident(g0,g-1)
    c: Coincident(g1,g0)
    c: Radius(g1) = 9
    c: Diameter(g0) = 6
FEATURE [PartDesign::Pad] Pad099
  Direction = (0,-1,2e-16)
  Length = 1
  Length2 = 10
  Placement = pos=(0,0,0) rot=(1,0,0;1.5708rad)
  Profile = -> Sketch206
  Type = 0
FEATURE [PartDesign::Body] Body191
  Group = -> [Sketch206,Pad099]
  Origin = -> Origin257
  Tip = -> Pad099
FEATURE [App::Part] Part065  label="Arandela M6-008"
  Group = -> [Body191]
  Origin = -> Origin256
  Placement = pos=(10,341,10) rot=(0,0,1;0rad)
FEATURE [Sketcher::SketchObject] Sketch207
  FullyConstrained = true
  MapMode = 5
  Placement = pos=(0,0,0) rot=(0.57735,0.57735,0.57735;2.0944rad)
  Support = -> [YZ_Plane253]
  sketch-geometry (4):
    g0: LineSegment StartX=0 StartY=0 StartZ=0 EndX=340 EndY=0 EndZ=0
    g1: LineSegment StartX=340 StartY=0 StartZ=0 EndX=340 EndY=-30 EndZ=0
    g2: LineSegment StartX=340 StartY=-30 StartZ=0 EndX=0 EndY=-30 EndZ=0
    g3: LineSegment StartX=0 StartY=-30 StartZ=0 EndX=0 EndY=0 EndZ=0
  constraints (11):
    c: Coincident(g0,g1)
    c: Coincident(g1,g2)
    c: Coincident(g2,g3)
    c: Coincident(g3,g0)
    c: Horizontal(g0)
    c: Horizontal(g2)
    c: Vertical(g1)
    c: Vertical(g3)
    c: Coincident(g0,g-1)
    c: DistanceY(g2,g0) = 30
    c: DistanceX(g2,g1) = 340
FEATURE [PartDesign::Pad] Pad100
  Direction = (1,-2e-16,3e-16)
  Length = 2
  Length2 = 10
  Placement = pos=(0,0,0) rot=(0.57735,0.57735,0.57735;2.0944rad)
  Profile = -> Sketch207
  Type = 0
FEATURE [PartDesign::Body] Body192
  Group = -> [Sketch207,Pad100]
  Origin = -> Origin259
  Tip = -> Pad100
FEATURE [Sketcher::SketchObject] Sketch208
  FullyConstrained = false
  MapMode = 5
  Support = -> [XY_Plane254]
  sketch-geometry (9):
    g0: LineSegment StartX=-50 StartY=12 StartZ=0 EndX=-50 EndY=328 EndZ=0
    g1: LineSegment StartX=2 StartY=339.974 StartZ=0 EndX=2 EndY=0 EndZ=0
    g2: GeomPoint X=-50 Y=328 Z=0
    g3: LineSegment StartX=-50 StartY=328 StartZ=0 EndX=2 EndY=340 EndZ=0
    g4: GeomPoint X=-50 Y=12 Z=0
    g5: LineSegment StartX=2 StartY=0 StartZ=0 EndX=-50 EndY=12 EndZ=0
    g6: GeomPoint X=2 Y=0 Z=0
    g7: GeomPoint X=2 Y=340 Z=0
    g8: LineSegment StartX=2 StartY=340 StartZ=0 EndX=2 EndY=339.974 EndZ=0
  constraints (18):
    c: Vertical(g0)
    c: Vertical(g1)
    c: PointOnObject(g2,g0)
    c: Coincident(g3,g2)
    c: PointOnObject(g0,g3)
    c: PointOnObject(g4,g0)
    c: Coincident(g5,g4)
    c: PointOnObject(g0,g5)
    c: PointOnObject(g6,g-1)
    c: DistanceX(g-1,g6) = 2
    c: Coincident(g5,g6)
    c: Coincident(g5,g1)
    c: DistanceX(g-1,g7) = 2
    c: DistanceY(g-1,g7) = 340
    c: Coincident(g8,g7)
    c: Coincident(g8,g1)
    c: Vertical(g8)
    c: Coincident(g3,g8)
FEATURE [PartDesign::Pad] Pad101
  Direction = (1,1,1)
  Length = 2
  Length2 = 10
  Profile = -> Sketch208
  Type = 0
FEATURE [PartDesign::Body] Body193
  Group = -> [Sketch208,Pad101]
  Origin = -> Origin260
  Placement = pos=(2,0,0) rot=(0,0,1;0rad)
  Tip = -> Pad101
FEATURE [App::Part] Part066  label="baseMotores"
  Group = -> [Body192,Body193]
  Origin = -> Origin258
  Placement = pos=(342,340,81) rot=(0,0,1;3.14159rad)
FEATURE [Sketcher::SketchObject] Sketch209
  FullyConstrained = false
  MapMode = 5
  Support = -> [XY_Plane256]
  sketch-geometry (8):
    g0: ArcOfCircle CenterX=0 CenterY=0 CenterZ=0 NormalX=0 NormalY=0 NormalZ=1 AngleXU=0 Radius=60 StartAngle=3.30904 EndAngle=6.11574
    g1: LineSegment StartX=-59.1608 StartY=10 StartZ=0 EndX=-48 EndY=10 EndZ=0
    g2: LineSegment StartX=-59.1608 StartY=-10 StartZ=0 EndX=-48 EndY=-10 EndZ=0
    g3: LineSegment StartX=-48 StartY=10 StartZ=0 EndX=-48 EndY=-10 EndZ=0
    g4: LineSegment StartX=48 StartY=10 StartZ=0 EndX=48 EndY=-10 EndZ=0
    g5: ArcOfCircle CenterX=0 CenterY=0 CenterZ=0 NormalX=0 NormalY=0 NormalZ=1 AngleXU=0 Radius=60 StartAngle=0.167448 EndAngle=2.97414
    g6: LineSegment StartX=48 StartY=10 StartZ=0 EndX=59.1608 EndY=10 EndZ=0
    g7: LineSegment StartX=48 StartY=-10 StartZ=0 EndX=59.1608 EndY=-10 EndZ=0
  constraints (16):
    c: Coincident(g0,g-1)
    c: Diameter(g0) = 120
    c: Horizontal(g1)
    c: Horizontal(g2)
    c: Vertical(g3)
    c: Vertical(g4)
    c: Coincident(g1,g5)
    c: Coincident(g2,g0)
    c: Equal(g0,g5)
    c: Coincident(g0,g5)
    c: Coincident(g6,g5)
    c: Coincident(g7,g0)
    c: Coincident(g1,g3)
    c: Coincident(g6,g4)
    c: Coincident(g2,g3)
    c: Coincident(g7,g4)
FEATURE [PartDesign::Pad] Pad102
  Direction = (0,0,1)
  Length = 8
  Length2 = 10
  Profile = -> Sketch209
  Type = 0
FEATURE [PartDesign::Body] Body194
  Group = -> [Sketch209,Pad102]
  Origin = -> Origin262
  Tip = -> Pad102
FEATURE [App::Part] Part067  label="rueda-002"
  Group = -> [Body194]
  Origin = -> Origin261
  Placement = pos=(110,246,105) rot=(0,1,0;1.5708rad)
FEATURE [Sketcher::SketchObject] Sketch211
  FullyConstrained = true
  MapMode = 5
  Support = -> [XY_Plane260]
  sketch-geometry (12):
    g0: ArcOfCircle CenterX=0 CenterY=0 CenterZ=0 NormalX=0 NormalY=0 NormalZ=1 AngleXU=0 Radius=60 StartAngle=1.77951 EndAngle=2.93288
    g1: GeomPoint X=0 Y=60 Z=0
    g2: GeomPoint X=0 Y=-60 Z=0
    g3: GeomPoint X=-60 Y=0 Z=0
    g4: GeomPoint X=60 Y=0 Z=0
    g5: ArcOfCircle CenterX=-60 CenterY=0 CenterZ=0 NormalX=0 NormalY=0 NormalZ=1 AngleXU=0 Radius=12.5 StartAngle=4.81674 EndAngle=7.74963
    g6: ArcOfCircle CenterX=0 CenterY=60 CenterZ=0 NormalX=0 NormalY=0 NormalZ=1 AngleXU=0 Radius=12.5 StartAngle=3.24595 EndAngle=6.17883
    g7: ArcOfCircle CenterX=60 CenterY=0 CenterZ=0 NormalX=0 NormalY=0 NormalZ=1 AngleXU=0 Radius=12.5 StartAngle=1.67515 EndAngle=4.60803
    g8: ArcOfCircle CenterX=0 CenterY=-60 CenterZ=0 NormalX=0 NormalY=0 NormalZ=1 AngleXU=0 Radius=12.5 StartAngle=0.104356 EndAngle=3.03724
    g9: ArcOfCircle CenterX=0 CenterY=0 CenterZ=0 NormalX=0 NormalY=0 NormalZ=1 AngleXU=0 Radius=60 StartAngle=3.3503 EndAngle=4.50368
    g10: ArcOfCircle CenterX=0 CenterY=0 CenterZ=0 NormalX=0 NormalY=0 NormalZ=1 AngleXU=0 Radius=60 StartAngle=4.9211 EndAngle=6.07447
    g11: ArcOfCircle CenterX=0 CenterY=0 CenterZ=0 NormalX=0 NormalY=0 NormalZ=1 AngleXU=0 Radius=60 StartAngle=0.208712 EndAngle=1.36208
  constraints (32):
    c: Coincident(g0,g-1)
    c: PointOnObject(g1,g0)
    c: PointOnObject(g2,g0)
    c: PointOnObject(g3,g0)
    c: PointOnObject(g4,g0)
    c: DistanceY(g-1,g3) = 0
    c: DistanceY(g-1,g4) = 0
    c: DistanceX(g1,g-1) = 0
    c: DistanceX(g2,g-1) = 0
    c: Coincident(g5,g3)
    c: Diameter(g5) = 25
    c: Coincident(g6,g1)
    c: Coincident(g7,g4)
    c: Coincident(g8,g2)
    c: Equal(g7,g6)
    c: Equal(g7,g8)
    c: Diameter(g7) = 25
    c: Coincident(g11,g6)
    c: Coincident(g0,g6)
    c: Equal(g0,g9)
    c: Coincident(g0,g5)
    c: Coincident(g9,g5)
    c: Coincident(g0,g9)
    c: Equal(g9,g10)
    c: Coincident(g9,g10)
    c: Coincident(g8,g9)
    c: Coincident(g8,g10)
    c: Equal(g10,g11)
    c: Coincident(g10,g11)
    c: Coincident(g7,g10)
    c: Coincident(g7,g11)
    c: Diameter(g0) = 120
FEATURE [PartDesign::Pad] Pad104
  Direction = (0,0,1)
  Length = 8
  Length2 = 10
  Profile = -> Sketch211
  Type = 0
FEATURE [PartDesign::Body] Body196
  Group = -> [Sketch211,Pad104]
  Origin = -> Origin266
  Tip = -> Pad104
FEATURE [App::Part] Part069  label="rueda-003"
  Group = -> [Body196]
  Origin = -> Origin265
  Placement = pos=(190,246,105) rot=(0,1,0;1.5708rad)
FEATURE [App::LinkGroup] LinkGroup  label="2020-base"
  ElementList = -> [Part003,Part002,Part001,Part]
  LinkMode = 0
FEATURE [App::LinkGroup] LinkGroup001  label="2020-columnas"
  ElementList = -> [Part004,Part005,Part006,Part007]
  LinkMode = 0
FEATURE [App::LinkGroup] LinkGroup002  label="2020-techo"
  ElementList = -> [Part008,Part009,Part010,Part011]
  LinkMode = 0
FEATURE [App::LinkGroup] LinkGroup003  label="2020-bases de ejes"
  ElementList = -> [Part012,Part013]
  LinkMode = 0
FEATURE [App::LinkGroup] LinkGroup004  label="soportes rulemanes"
  ElementList = -> [Part014,Part015,Part016,Part017,Part018,Part019]
  LinkMode = 0
FEATURE [App::LinkGroup] LinkGroup005  label="Motores"
  ElementList = -> [Part020,Part027]
  LinkMode = 0
FEATURE [App::LinkGroup] LinkGroup006  label="ejes"
  ElementList = -> [Part034,Part035,Part036]
  LinkMode = 0
  Placement = pos=(31,4.57764e-05,0) rot=(0,0,1;0rad)
FEATURE [App::LinkGroup] LinkGroup007  label="tornillos M6 estructura"
  ElementList = -> [Part038,Part039,Part040,Part041,Part042,Part043,Part044,Part045]
  LinkMode = 0
FEATURE [App::LinkGroup] LinkGroup008  label="tornillos M5 rulemanes"
  ElementList = -> [Part046,Part047,Part048,Part049,Part050,Part051,Part052,Part053,Part054,Part055,Part056,Part057]
  LinkMode = 0
FEATURE [App::LinkGroup] LinkGroup009  label="arandelas M6 estructura"
  ElementList = -> [Part046,Part047,Part048,Part049,Part050,Part051,Part052,Part053,Part054,Part055,Part056,Part057,Part058,Part059,Part060,Part061,Part062,Part063,Part064,Part065]
  LinkMode = 0
FEATURE [Sketcher::SketchObject] Sketch212
  FullyConstrained = true
  MapMode = 5
  Placement = pos=(0,0,0) rot=(0.57735,0.57735,0.57735;2.0944rad)
  Support = -> [YZ_Plane261]
  sketch-geometry (5):
    g0: LineSegment StartX=0 StartY=0 StartZ=0 EndX=0 EndY=20 EndZ=0
    g1: LineSegment StartX=0 StartY=20 StartZ=0 EndX=-3 EndY=20 EndZ=0
    g2: LineSegment StartX=-3 StartY=20 StartZ=0 EndX=-20 EndY=3 EndZ=0
    g3: LineSegment StartX=-20 StartY=3 StartZ=0 EndX=-20 EndY=0 EndZ=0
    g4: LineSegment StartX=-20 StartY=0 StartZ=0 EndX=0 EndY=0 EndZ=0
  constraints (14):
    c: Coincident(g-1,g0)
    c: PointOnObject(g0,g-2)
    c: Coincident(g0,g1)
    c: Horizontal(g1)
    c: Coincident(g1,g2)
    c: Coincident(g2,g3)
    c: PointOnObject(g3,g-1)
    c: Vertical(g3)
    c: Coincident(g3,g4)
    c: Coincident(g4,g0)
    c: DistanceY(g0,g0) = 20
    c: DistanceY(g3,g3) = 3
    c: DistanceX(g1,g1) = 3
    c: DistanceX(g4,g4) = 20
FEATURE [PartDesign::Pad] Pad105
  Direction = (1,1,1)
  Length = 17
  Length2 = 100
  Placement = pos=(0,0,0) rot=(0.57735,0.57735,0.57735;2.0944rad)
  Profile = -> Sketch212
  Type = 0
FEATURE [Sketcher::SketchObject] Sketch213
  ExternalGeometry = -> [Pad105]
  FullyConstrained = true
  MapMode = 5
  Placement = pos=(-8.8e-15,-20,4.4e-15) rot=(-0.57735,-0.57735,0.57735;4.18879rad)
  Support = -> [Pad105]
  sketch-geometry (4):
    g0: LineSegment StartX=-3 StartY=2 StartZ=0 EndX=-20 EndY=2 EndZ=0
    g1: LineSegment StartX=-20 StartY=2 StartZ=0 EndX=-20 EndY=15 EndZ=0
    g2: LineSegment StartX=-20 StartY=15 StartZ=0 EndX=-3 EndY=15 EndZ=0
    g3: LineSegment StartX=-3 StartY=15 StartZ=0 EndX=-3 EndY=2 EndZ=0
  constraints (12):
    c: Coincident(g0,g1)
    c: Coincident(g1,g2)
    c: Coincident(g2,g3)
    c: Coincident(g3,g0)
    c: Horizontal(g0)
    c: Horizontal(g2)
    c: Vertical(g1)
    c: Vertical(g3)
    c: PointOnObject(g0,g-3)
    c: DistanceY(g1,g-6) = 2
    c: DistanceY(g-6,g0) = 2
    c: PointOnObject(g1,g-6)
FEATURE [PartDesign::Pocket] Pocket074
  BaseFeature = -> Pad105
  Length = 17
  Length2 = 100
  Placement = pos=(0,0,0) rot=(0.57735,0.57735,0.57735;2.0944rad)
  Profile = -> Sketch213
  Type = 0
FEATURE [Sketcher::SketchObject] Sketch214
  ExternalGeometry = -> [Pocket074]
  FullyConstrained = true
  MapMode = 5
  Placement = pos=(-1.7e-15,-3,6e-16) rot=(-0.57735,-0.57735,0.57735;4.18879rad)
  Support = -> [Pocket074]
  sketch-geometry (5):
    g0: LineSegment StartX=-20 StartY=8.5 StartZ=0 EndX=-3 EndY=8.5 EndZ=0
    g1: ArcOfCircle CenterX=-10 CenterY=8.5 CenterZ=0 NormalX=0 NormalY=0 NormalZ=1 AngleXU=0 Radius=3 StartAngle=4.71239 EndAngle=7.85398
    g2: ArcOfCircle CenterX=-13 CenterY=8.5 CenterZ=0 NormalX=0 NormalY=0 NormalZ=1 AngleXU=0 Radius=3 StartAngle=1.5708 EndAngle=4.71239
    g3: LineSegment StartX=-10 StartY=11.5 StartZ=0 EndX=-13 EndY=11.5 EndZ=0
    g4: LineSegment StartX=-10 StartY=5.5 StartZ=0 EndX=-13 EndY=5.5 EndZ=0
  constraints (14):
    c: PointOnObject(g0,g-6)
    c: PointOnObject(g0,g-4)
    c: Horizontal(g0)
    c: DistanceY(g0,g-4) = 6.5
    c: Tangent(g1,g4) = 1.5708
    c: Tangent(g1,g3) = -1.5708
    c: Tangent(g3,g2) = -1.5708
    c: Tangent(g4,g2) = 1.5708
    c: Horizontal(g3)
    c: Equal(g1,g2)
    c: PointOnObject(g1,g0)
    c: Radius(g1) = 3
    c: DistanceX(g3,g3) = 3
    c: DistanceX(g0,g2) = 7
FEATURE [PartDesign::Pocket] Pocket075
  BaseFeature = -> Pocket074
  Length = 5
  Length2 = 100
  Placement = pos=(0,0,0) rot=(0.57735,0.57735,0.57735;2.0944rad)
  Profile = -> Sketch214
  Type = 2
FEATURE [Sketcher::SketchObject] Sketch215
  ExternalGeometry = -> [Pocket075]
  FullyConstrained = true
  MapMode = 5
  Placement = pos=(-3e-16,1.2e-15,3) rot=(0,0,-1;1.5708rad)
  Support = -> [Pocket075]
  sketch-geometry (5):
    g0: LineSegment StartX=3 StartY=8.5 StartZ=0 EndX=20 EndY=8.5 EndZ=0
    g1: ArcOfCircle CenterX=10 CenterY=8.5 CenterZ=0 NormalX=0 NormalY=0 NormalZ=1 AngleXU=0 Radius=3 StartAngle=1.5708 EndAngle=4.71239
    g2: ArcOfCircle CenterX=13 CenterY=8.5 CenterZ=0 NormalX=0 NormalY=0 NormalZ=1 AngleXU=0 Radius=3 StartAngle=4.71239 EndAngle=7.85398
    g3: LineSegment StartX=10 StartY=5.5 StartZ=0 EndX=13 EndY=5.5 EndZ=0
    g4: LineSegment StartX=10 StartY=11.5 StartZ=0 EndX=13 EndY=11.5 EndZ=0
  constraints (14):
    c: PointOnObject(g0,g-4)
    c: PointOnObject(g0,g-5)
    c: Horizontal(g0)
    c: DistanceY(g0,g-4) = 6.5
    c: Tangent(g1,g4) = 1.5708
    c: Tangent(g1,g3) = -1.5708
    c: Tangent(g3,g2) = -1.5708
    c: Tangent(g4,g2) = 1.5708
    c: Horizontal(g3)
    c: Equal(g1,g2)
    c: PointOnObject(g1,g0)
    c: Radius(g2) = 3
    c: DistanceX(g4,g4) = 3
    c: DistanceX(g2,g0) = 7
FEATURE [PartDesign::Pocket] Pocket076
  BaseFeature = -> Pocket075
  Length = 5
  Length2 = 100
  Placement = pos=(0,0,0) rot=(0.57735,0.57735,0.57735;2.0944rad)
  Profile = -> Sketch215
  Type = 2
FEATURE [Sketcher::SketchObject] Sketch216
  ExternalGeometry = -> [Pocket076]
  FullyConstrained = true
  MapMode = 5
  Placement = pos=(0,0,0) rot=(0.57735,0.57735,0.57735;4.18879rad)
  Support = -> [Pocket076]
  sketch-geometry (9):
    g0: LineSegment StartX=0 StartY=8.5 StartZ=0 EndX=20 EndY=8.5 EndZ=0
    g1: ArcOfCircle CenterX=3 CenterY=9.5 CenterZ=0 NormalX=0 NormalY=0 NormalZ=1 AngleXU=0 Radius=1 StartAngle=0 EndAngle=3.14159
    g2: ArcOfCircle CenterX=3 CenterY=7.5 CenterZ=0 NormalX=0 NormalY=0 NormalZ=1 AngleXU=0 Radius=1 StartAngle=3.14159 EndAngle=6.28319
    g3: LineSegment StartX=2 StartY=9.5 StartZ=0 EndX=2 EndY=7.5 EndZ=0
    g4: LineSegment StartX=4 StartY=9.5 StartZ=0 EndX=4 EndY=7.5 EndZ=0
    g5: ArcOfCircle CenterX=18 CenterY=9.5 CenterZ=0 NormalX=0 NormalY=0 NormalZ=1 AngleXU=0 Radius=1 StartAngle=-9e-16 EndAngle=3.14159
    g6: ArcOfCircle CenterX=18 CenterY=7.5 CenterZ=0 NormalX=0 NormalY=0 NormalZ=1 AngleXU=0 Radius=1 StartAngle=3.14159 EndAngle=6.28319
    g7: LineSegment StartX=17 StartY=9.5 StartZ=0 EndX=17 EndY=7.5 EndZ=0
    g8: LineSegment StartX=19 StartY=9.5 StartZ=0 EndX=19 EndY=7.5 EndZ=0
  constraints (24):
    c: PointOnObject(g0,g-2)
    c: PointOnObject(g0,g-5)
    c: Horizontal(g0)
    c: DistanceY(g0,g-3) = 8.5
    c: Tangent(g1,g4) = 1.5708
    c: Tangent(g1,g3) = -1.5708
    c: Tangent(g3,g2) = -1.5708
    c: Tangent(g4,g2) = 1.5708
    c: Vertical(g3)
    c: Equal(g1,g2)
    c: Tangent(g5,g8) = 1.5708
    c: Tangent(g5,g7) = -1.5708
    c: Tangent(g7,g6) = -1.5708
    c: Tangent(g8,g6) = 1.5708
    c: Vertical(g7)
    c: Equal(g5,g6)
    c: Equal(g1,g5)
    c: Equal(g4,g7)
    c: DistanceY(g4,g4) = 2
    c: Radius(g1) = 1
    c: Horizontal(g5,g1)
    c: DistanceX(g0,g1) = 3
    c: DistanceX(g5,g0) = 2
    c: DistanceY(g0,g1) = 1
FEATURE [PartDesign::Pad] Pad106
  BaseFeature = -> Pocket076
  Direction = (1,1,1)
  Length = 1
  Length2 = 100
  Placement = pos=(0,0,0) rot=(0.57735,0.57735,0.57735;2.0944rad)
  Profile = -> Sketch216
  Type = 0
FEATURE [Sketcher::SketchObject] Sketch217
  ExternalGeometry = -> [Pad106]
  FullyConstrained = true
  MapMode = 5
  Placement = pos=(0,0,1e-16) rot=(0.707107,0.707107,0;3.14159rad)
  Support = -> [Pad106]
  sketch-geometry (9):
    g0: LineSegment StartX=0 StartY=8.5 StartZ=0 EndX=-20 EndY=8.5 EndZ=0
    g1: ArcOfCircle CenterX=-3 CenterY=7.5 CenterZ=0 NormalX=0 NormalY=0 NormalZ=1 AngleXU=0 Radius=1 StartAngle=3.14159 EndAngle=6.28319
    g2: ArcOfCircle CenterX=-3 CenterY=9.5 CenterZ=0 NormalX=0 NormalY=0 NormalZ=1 AngleXU=0 Radius=1 StartAngle=3e-16 EndAngle=3.14159
    g3: LineSegment StartX=-2 StartY=7.5 StartZ=0 EndX=-2 EndY=9.5 EndZ=0
    g4: LineSegment StartX=-4 StartY=7.5 StartZ=0 EndX=-4 EndY=9.5 EndZ=0
    g5: ArcOfCircle CenterX=-18 CenterY=9.5 CenterZ=0 NormalX=0 NormalY=0 NormalZ=1 AngleXU=0 Radius=1 StartAngle=0 EndAngle=3.14159
    g6: ArcOfCircle CenterX=-18 CenterY=7.5 CenterZ=0 NormalX=0 NormalY=0 NormalZ=1 AngleXU=0 Radius=1 StartAngle=3.14159 EndAngle=6.28319
    g7: LineSegment StartX=-19 StartY=9.5 StartZ=0 EndX=-19 EndY=7.5 EndZ=0
    g8: LineSegment StartX=-17 StartY=9.5 StartZ=0 EndX=-17 EndY=7.5 EndZ=0
  constraints (24):
    c: PointOnObject(g0,g-2)
    c: PointOnObject(g0,g-4)
    c: Horizontal(g0)
    c: DistanceY(g0,g-3) = 8.5
    c: Tangent(g1,g4) = 1.5708
    c: Tangent(g1,g3) = -1.5708
    c: Tangent(g3,g2) = -1.5708
    c: Tangent(g4,g2) = 1.5708
    c: Vertical(g3)
    c: Equal(g1,g2)
    c: Radius(g2) = 1
    c: DistanceY(g4,g4) = 2
    c: DistanceY(g0,g2) = 1
    c: DistanceX(g2,g0) = 3
    c: Tangent(g5,g8) = 1.5708
    c: Tangent(g5,g7) = -1.5708
    c: Tangent(g7,g6) = -1.5708
    c: Tangent(g8,g6) = 1.5708
    c: Vertical(g7)
    c: Equal(g5,g6)
    c: Equal(g5,g2)
    c: Equal(g8,g4)
    c: Horizontal(g5,g2)
    c: DistanceX(g0,g5) = 2
FEATURE [PartDesign::Pad] Pad107
  BaseFeature = -> Pad106
  Direction = (1,1,1)
  Length = 1
  Length2 = 100
  Placement = pos=(0,0,0) rot=(0.57735,0.57735,0.57735;2.0944rad)
  Profile = -> Sketch217
  Type = 0
FEATURE [PartDesign::Body] Body197  label="Corner"
  Group = -> [Sketch212,Pad105,Sketch213,Pocket074,Sketch214,Pocket075,Sketch215,Pocket076,Sketch216,Pad106,Sketch217,Pad107]
  Origin = -> Origin267
  Tip = -> Pad107
FEATURE [App::Part] Part070  label="soporte90-001"
  Group = -> [Body197]
  Origin = -> Origin268
  Placement = pos=(20,18,170) rot=(0.707107,-0.707107,0;3.14159rad)
FEATURE [Sketcher::SketchObject] Sketch218
  FullyConstrained = true
  MapMode = 5
  Placement = pos=(0,0,0) rot=(0.57735,0.57735,0.57735;2.0944rad)
  Support = -> [YZ_Plane263]
  sketch-geometry (5):
    g0: LineSegment StartX=0 StartY=0 StartZ=0 EndX=0 EndY=20 EndZ=0
    g1: LineSegment StartX=0 StartY=20 StartZ=0 EndX=-3 EndY=20 EndZ=0
    g2: LineSegment StartX=-3 StartY=20 StartZ=0 EndX=-20 EndY=3 EndZ=0
    g3: LineSegment StartX=-20 StartY=3 StartZ=0 EndX=-20 EndY=0 EndZ=0
    g4: LineSegment StartX=-20 StartY=0 StartZ=0 EndX=0 EndY=0 EndZ=0
  constraints (14):
    c: Coincident(g-1,g0)
    c: PointOnObject(g0,g-2)
    c: Coincident(g0,g1)
    c: Horizontal(g1)
    c: Coincident(g1,g2)
    c: Coincident(g2,g3)
    c: PointOnObject(g3,g-1)
    c: Vertical(g3)
    c: Coincident(g3,g4)
    c: Coincident(g4,g0)
    c: DistanceY(g0,g0) = 20
    c: DistanceY(g3,g3) = 3
    c: DistanceX(g1,g1) = 3
    c: DistanceX(g4,g4) = 20
FEATURE [PartDesign::Pad] Pad108
  Direction = (1,1,1)
  Length = 17
  Length2 = 100
  Placement = pos=(0,0,0) rot=(0.57735,0.57735,0.57735;2.0944rad)
  Profile = -> Sketch218
  Type = 0
FEATURE [Sketcher::SketchObject] Sketch219
  ExternalGeometry = -> [Pad108]
  FullyConstrained = true
  MapMode = 5
  Placement = pos=(-8.8e-15,-20,4.4e-15) rot=(-0.57735,-0.57735,0.57735;4.18879rad)
  Support = -> [Pad108]
  sketch-geometry (4):
    g0: LineSegment StartX=-3 StartY=2 StartZ=0 EndX=-20 EndY=2 EndZ=0
    g1: LineSegment StartX=-20 StartY=2 StartZ=0 EndX=-20 EndY=15 EndZ=0
    g2: LineSegment StartX=-20 StartY=15 StartZ=0 EndX=-3 EndY=15 EndZ=0
    g3: LineSegment StartX=-3 StartY=15 StartZ=0 EndX=-3 EndY=2 EndZ=0
  constraints (12):
    c: Coincident(g0,g1)
    c: Coincident(g1,g2)
    c: Coincident(g2,g3)
    c: Coincident(g3,g0)
    c: Horizontal(g0)
    c: Horizontal(g2)
    c: Vertical(g1)
    c: Vertical(g3)
    c: PointOnObject(g0,g-3)
    c: DistanceY(g1,g-6) = 2
    c: DistanceY(g-6,g0) = 2
    c: PointOnObject(g1,g-6)
FEATURE [PartDesign::Pocket] Pocket077
  BaseFeature = -> Pad108
  Length = 17
  Length2 = 100
  Placement = pos=(0,0,0) rot=(0.57735,0.57735,0.57735;2.0944rad)
  Profile = -> Sketch219
  Type = 0
FEATURE [Sketcher::SketchObject] Sketch220
  ExternalGeometry = -> [Pocket077]
  FullyConstrained = true
  MapMode = 5
  Placement = pos=(-1.7e-15,-3,6e-16) rot=(-0.57735,-0.57735,0.57735;4.18879rad)
  Support = -> [Pocket077]
  sketch-geometry (5):
    g0: LineSegment StartX=-20 StartY=8.5 StartZ=0 EndX=-3 EndY=8.5 EndZ=0
    g1: ArcOfCircle CenterX=-10 CenterY=8.5 CenterZ=0 NormalX=0 NormalY=0 NormalZ=1 AngleXU=0 Radius=3 StartAngle=4.71239 EndAngle=7.85398
    g2: ArcOfCircle CenterX=-13 CenterY=8.5 CenterZ=0 NormalX=0 NormalY=0 NormalZ=1 AngleXU=0 Radius=3 StartAngle=1.5708 EndAngle=4.71239
    g3: LineSegment StartX=-10 StartY=11.5 StartZ=0 EndX=-13 EndY=11.5 EndZ=0
    g4: LineSegment StartX=-10 StartY=5.5 StartZ=0 EndX=-13 EndY=5.5 EndZ=0
  constraints (14):
    c: PointOnObject(g0,g-6)
    c: PointOnObject(g0,g-4)
    c: Horizontal(g0)
    c: DistanceY(g0,g-4) = 6.5
    c: Tangent(g1,g4) = 1.5708
    c: Tangent(g1,g3) = -1.5708
    c: Tangent(g3,g2) = -1.5708
    c: Tangent(g4,g2) = 1.5708
    c: Horizontal(g3)
    c: Equal(g1,g2)
    c: PointOnObject(g1,g0)
    c: Radius(g1) = 3
    c: DistanceX(g3,g3) = 3
    c: DistanceX(g0,g2) = 7
FEATURE [PartDesign::Pocket] Pocket078
  BaseFeature = -> Pocket077
  Length = 5
  Length2 = 100
  Placement = pos=(0,0,0) rot=(0.57735,0.57735,0.57735;2.0944rad)
  Profile = -> Sketch220
  Type = 2
FEATURE [Sketcher::SketchObject] Sketch221
  ExternalGeometry = -> [Pocket078]
  FullyConstrained = true
  MapMode = 5
  Placement = pos=(-3e-16,1.2e-15,3) rot=(0,0,-1;1.5708rad)
  Support = -> [Pocket078]
  sketch-geometry (5):
    g0: LineSegment StartX=3 StartY=8.5 StartZ=0 EndX=20 EndY=8.5 EndZ=0
    g1: ArcOfCircle CenterX=10 CenterY=8.5 CenterZ=0 NormalX=0 NormalY=0 NormalZ=1 AngleXU=0 Radius=3 StartAngle=1.5708 EndAngle=4.71239
    g2: ArcOfCircle CenterX=13 CenterY=8.5 CenterZ=0 NormalX=0 NormalY=0 NormalZ=1 AngleXU=0 Radius=3 StartAngle=4.71239 EndAngle=7.85398
    g3: LineSegment StartX=10 StartY=5.5 StartZ=0 EndX=13 EndY=5.5 EndZ=0
    g4: LineSegment StartX=10 StartY=11.5 StartZ=0 EndX=13 EndY=11.5 EndZ=0
  constraints (14):
    c: PointOnObject(g0,g-4)
    c: PointOnObject(g0,g-5)
    c: Horizontal(g0)
    c: DistanceY(g0,g-4) = 6.5
    c: Tangent(g1,g4) = 1.5708
    c: Tangent(g1,g3) = -1.5708
    c: Tangent(g3,g2) = -1.5708
    c: Tangent(g4,g2) = 1.5708
    c: Horizontal(g3)
    c: Equal(g1,g2)
    c: PointOnObject(g1,g0)
    c: Radius(g2) = 3
    c: DistanceX(g4,g4) = 3
    c: DistanceX(g2,g0) = 7
FEATURE [PartDesign::Pocket] Pocket079
  BaseFeature = -> Pocket078
  Length = 5
  Length2 = 100
  Placement = pos=(0,0,0) rot=(0.57735,0.57735,0.57735;2.0944rad)
  Profile = -> Sketch221
  Type = 2
FEATURE [Sketcher::SketchObject] Sketch222
  ExternalGeometry = -> [Pocket079]
  FullyConstrained = true
  MapMode = 5
  Placement = pos=(0,0,0) rot=(0.57735,0.57735,0.57735;4.18879rad)
  Support = -> [Pocket079]
  sketch-geometry (9):
    g0: LineSegment StartX=0 StartY=8.5 StartZ=0 EndX=20 EndY=8.5 EndZ=0
    g1: ArcOfCircle CenterX=3 CenterY=9.5 CenterZ=0 NormalX=0 NormalY=0 NormalZ=1 AngleXU=0 Radius=1 StartAngle=0 EndAngle=3.14159
    g2: ArcOfCircle CenterX=3 CenterY=7.5 CenterZ=0 NormalX=0 NormalY=0 NormalZ=1 AngleXU=0 Radius=1 StartAngle=3.14159 EndAngle=6.28319
    g3: LineSegment StartX=2 StartY=9.5 StartZ=0 EndX=2 EndY=7.5 EndZ=0
    g4: LineSegment StartX=4 StartY=9.5 StartZ=0 EndX=4 EndY=7.5 EndZ=0
    g5: ArcOfCircle CenterX=18 CenterY=9.5 CenterZ=0 NormalX=0 NormalY=0 NormalZ=1 AngleXU=0 Radius=1 StartAngle=-9e-16 EndAngle=3.14159
    g6: ArcOfCircle CenterX=18 CenterY=7.5 CenterZ=0 NormalX=0 NormalY=0 NormalZ=1 AngleXU=0 Radius=1 StartAngle=3.14159 EndAngle=6.28319
    g7: LineSegment StartX=17 StartY=9.5 StartZ=0 EndX=17 EndY=7.5 EndZ=0
    g8: LineSegment StartX=19 StartY=9.5 StartZ=0 EndX=19 EndY=7.5 EndZ=0
  constraints (24):
    c: PointOnObject(g0,g-2)
    c: PointOnObject(g0,g-5)
    c: Horizontal(g0)
    c: DistanceY(g0,g-3) = 8.5
    c: Tangent(g1,g4) = 1.5708
    c: Tangent(g1,g3) = -1.5708
    c: Tangent(g3,g2) = -1.5708
    c: Tangent(g4,g2) = 1.5708
    c: Vertical(g3)
    c: Equal(g1,g2)
    c: Tangent(g5,g8) = 1.5708
    c: Tangent(g5,g7) = -1.5708
    c: Tangent(g7,g6) = -1.5708
    c: Tangent(g8,g6) = 1.5708
    c: Vertical(g7)
    c: Equal(g5,g6)
    c: Equal(g1,g5)
    c: Equal(g4,g7)
    c: DistanceY(g4,g4) = 2
    c: Radius(g1) = 1
    c: Horizontal(g5,g1)
    c: DistanceX(g0,g1) = 3
    c: DistanceX(g5,g0) = 2
    c: DistanceY(g0,g1) = 1
FEATURE [PartDesign::Pad] Pad109
  BaseFeature = -> Pocket079
  Direction = (1,1,1)
  Length = 1
  Length2 = 100
  Placement = pos=(0,0,0) rot=(0.57735,0.57735,0.57735;2.0944rad)
  Profile = -> Sketch222
  Type = 0
FEATURE [Sketcher::SketchObject] Sketch223
  ExternalGeometry = -> [Pad109]
  FullyConstrained = true
  MapMode = 5
  Placement = pos=(0,0,1e-16) rot=(0.707107,0.707107,0;3.14159rad)
  Support = -> [Pad109]
  sketch-geometry (9):
    g0: LineSegment StartX=0 StartY=8.5 StartZ=0 EndX=-20 EndY=8.5 EndZ=0
    g1: ArcOfCircle CenterX=-3 CenterY=7.5 CenterZ=0 NormalX=0 NormalY=0 NormalZ=1 AngleXU=0 Radius=1 StartAngle=3.14159 EndAngle=6.28319
    g2: ArcOfCircle CenterX=-3 CenterY=9.5 CenterZ=0 NormalX=0 NormalY=0 NormalZ=1 AngleXU=0 Radius=1 StartAngle=3e-16 EndAngle=3.14159
    g3: LineSegment StartX=-2 StartY=7.5 StartZ=0 EndX=-2 EndY=9.5 EndZ=0
    g4: LineSegment StartX=-4 StartY=7.5 StartZ=0 EndX=-4 EndY=9.5 EndZ=0
    g5: ArcOfCircle CenterX=-18 CenterY=9.5 CenterZ=0 NormalX=0 NormalY=0 NormalZ=1 AngleXU=0 Radius=1 StartAngle=0 EndAngle=3.14159
    g6: ArcOfCircle CenterX=-18 CenterY=7.5 CenterZ=0 NormalX=0 NormalY=0 NormalZ=1 AngleXU=0 Radius=1 StartAngle=3.14159 EndAngle=6.28319
    g7: LineSegment StartX=-19 StartY=9.5 StartZ=0 EndX=-19 EndY=7.5 EndZ=0
    g8: LineSegment StartX=-17 StartY=9.5 StartZ=0 EndX=-17 EndY=7.5 EndZ=0
  constraints (24):
    c: PointOnObject(g0,g-2)
    c: PointOnObject(g0,g-4)
    c: Horizontal(g0)
    c: DistanceY(g0,g-3) = 8.5
    c: Tangent(g1,g4) = 1.5708
    c: Tangent(g1,g3) = -1.5708
    c: Tangent(g3,g2) = -1.5708
    c: Tangent(g4,g2) = 1.5708
    c: Vertical(g3)
    c: Equal(g1,g2)
    c: Radius(g2) = 1
    c: DistanceY(g4,g4) = 2
    c: DistanceY(g0,g2) = 1
    c: DistanceX(g2,g0) = 3
    c: Tangent(g5,g8) = 1.5708
    c: Tangent(g5,g7) = -1.5708
    c: Tangent(g7,g6) = -1.5708
    c: Tangent(g8,g6) = 1.5708
    c: Vertical(g7)
    c: Equal(g5,g6)
    c: Equal(g5,g2)
    c: Equal(g8,g4)
    c: Horizontal(g5,g2)
    c: DistanceX(g0,g5) = 2
FEATURE [PartDesign::Pad] Pad110
  BaseFeature = -> Pad109
  Direction = (1,1,1)
  Length = 1
  Length2 = 100
  Placement = pos=(0,0,0) rot=(0.57735,0.57735,0.57735;2.0944rad)
  Profile = -> Sketch223
  Type = 0
FEATURE [PartDesign::Body] Body198  label="Corner001"
  Group = -> [Sketch218,Pad108,Sketch219,Pocket077,Sketch220,Pocket078,Sketch221,Pocket079,Sketch222,Pad109,Sketch223,Pad110]
  Origin = -> Origin269
  Tip = -> Pad110
FEATURE [App::Part] Part071  label="soporte90-002"
  Group = -> [Body198]
  Origin = -> Origin270
  Placement = pos=(20,321,20) rot=(0,0,1;1.5708rad)
FEATURE [Sketcher::SketchObject] Sketch224
  FullyConstrained = true
  MapMode = 5
  Placement = pos=(0,0,0) rot=(0.57735,0.57735,0.57735;2.0944rad)
  Support = -> [YZ_Plane265]
  sketch-geometry (5):
    g0: LineSegment StartX=0 StartY=0 StartZ=0 EndX=0 EndY=20 EndZ=0
    g1: LineSegment StartX=0 StartY=20 StartZ=0 EndX=-3 EndY=20 EndZ=0
    g2: LineSegment StartX=-3 StartY=20 StartZ=0 EndX=-20 EndY=3 EndZ=0
    g3: LineSegment StartX=-20 StartY=3 StartZ=0 EndX=-20 EndY=0 EndZ=0
    g4: LineSegment StartX=-20 StartY=0 StartZ=0 EndX=0 EndY=0 EndZ=0
  constraints (14):
    c: Coincident(g-1,g0)
    c: PointOnObject(g0,g-2)
    c: Coincident(g0,g1)
    c: Horizontal(g1)
    c: Coincident(g1,g2)
    c: Coincident(g2,g3)
    c: PointOnObject(g3,g-1)
    c: Vertical(g3)
    c: Coincident(g3,g4)
    c: Coincident(g4,g0)
    c: DistanceY(g0,g0) = 20
    c: DistanceY(g3,g3) = 3
    c: DistanceX(g1,g1) = 3
    c: DistanceX(g4,g4) = 20
FEATURE [PartDesign::Pad] Pad111
  Direction = (1,1,1)
  Length = 17
  Length2 = 100
  Placement = pos=(0,0,0) rot=(0.57735,0.57735,0.57735;2.0944rad)
  Profile = -> Sketch224
  Type = 0
FEATURE [Sketcher::SketchObject] Sketch225
  ExternalGeometry = -> [Pad111]
  FullyConstrained = true
  MapMode = 5
  Placement = pos=(-8.8e-15,-20,4.4e-15) rot=(-0.57735,-0.57735,0.57735;4.18879rad)
  Support = -> [Pad111]
  sketch-geometry (4):
    g0: LineSegment StartX=-3 StartY=2 StartZ=0 EndX=-20 EndY=2 EndZ=0
    g1: LineSegment StartX=-20 StartY=2 StartZ=0 EndX=-20 EndY=15 EndZ=0
    g2: LineSegment StartX=-20 StartY=15 StartZ=0 EndX=-3 EndY=15 EndZ=0
    g3: LineSegment StartX=-3 StartY=15 StartZ=0 EndX=-3 EndY=2 EndZ=0
  constraints (12):
    c: Coincident(g0,g1)
    c: Coincident(g1,g2)
    c: Coincident(g2,g3)
    c: Coincident(g3,g0)
    c: Horizontal(g0)
    c: Horizontal(g2)
    c: Vertical(g1)
    c: Vertical(g3)
    c: PointOnObject(g0,g-3)
    c: DistanceY(g1,g-6) = 2
    c: DistanceY(g-6,g0) = 2
    c: PointOnObject(g1,g-6)
FEATURE [PartDesign::Pocket] Pocket080
  BaseFeature = -> Pad111
  Length = 17
  Length2 = 100
  Placement = pos=(0,0,0) rot=(0.57735,0.57735,0.57735;2.0944rad)
  Profile = -> Sketch225
  Type = 0
FEATURE [Sketcher::SketchObject] Sketch226
  ExternalGeometry = -> [Pocket080]
  FullyConstrained = true
  MapMode = 5
  Placement = pos=(-1.7e-15,-3,6e-16) rot=(-0.57735,-0.57735,0.57735;4.18879rad)
  Support = -> [Pocket080]
  sketch-geometry (5):
    g0: LineSegment StartX=-20 StartY=8.5 StartZ=0 EndX=-3 EndY=8.5 EndZ=0
    g1: ArcOfCircle CenterX=-10 CenterY=8.5 CenterZ=0 NormalX=0 NormalY=0 NormalZ=1 AngleXU=0 Radius=3 StartAngle=4.71239 EndAngle=7.85398
    g2: ArcOfCircle CenterX=-13 CenterY=8.5 CenterZ=0 NormalX=0 NormalY=0 NormalZ=1 AngleXU=0 Radius=3 StartAngle=1.5708 EndAngle=4.71239
    g3: LineSegment StartX=-10 StartY=11.5 StartZ=0 EndX=-13 EndY=11.5 EndZ=0
    g4: LineSegment StartX=-10 StartY=5.5 StartZ=0 EndX=-13 EndY=5.5 EndZ=0
  constraints (14):
    c: PointOnObject(g0,g-6)
    c: PointOnObject(g0,g-4)
    c: Horizontal(g0)
    c: DistanceY(g0,g-4) = 6.5
    c: Tangent(g1,g4) = 1.5708
    c: Tangent(g1,g3) = -1.5708
    c: Tangent(g3,g2) = -1.5708
    c: Tangent(g4,g2) = 1.5708
    c: Horizontal(g3)
    c: Equal(g1,g2)
    c: PointOnObject(g1,g0)
    c: Radius(g1) = 3
    c: DistanceX(g3,g3) = 3
    c: DistanceX(g0,g2) = 7
FEATURE [PartDesign::Pocket] Pocket081
  BaseFeature = -> Pocket080
  Length = 5
  Length2 = 100
  Placement = pos=(0,0,0) rot=(0.57735,0.57735,0.57735;2.0944rad)
  Profile = -> Sketch226
  Type = 2
FEATURE [Sketcher::SketchObject] Sketch227
  ExternalGeometry = -> [Pocket081]
  FullyConstrained = true
  MapMode = 5
  Placement = pos=(-3e-16,1.2e-15,3) rot=(0,0,-1;1.5708rad)
  Support = -> [Pocket081]
  sketch-geometry (5):
    g0: LineSegment StartX=3 StartY=8.5 StartZ=0 EndX=20 EndY=8.5 EndZ=0
    g1: ArcOfCircle CenterX=10 CenterY=8.5 CenterZ=0 NormalX=0 NormalY=0 NormalZ=1 AngleXU=0 Radius=3 StartAngle=1.5708 EndAngle=4.71239
    g2: ArcOfCircle CenterX=13 CenterY=8.5 CenterZ=0 NormalX=0 NormalY=0 NormalZ=1 AngleXU=0 Radius=3 StartAngle=4.71239 EndAngle=7.85398
    g3: LineSegment StartX=10 StartY=5.5 StartZ=0 EndX=13 EndY=5.5 EndZ=0
    g4: LineSegment StartX=10 StartY=11.5 StartZ=0 EndX=13 EndY=11.5 EndZ=0
  constraints (14):
    c: PointOnObject(g0,g-4)
    c: PointOnObject(g0,g-5)
    c: Horizontal(g0)
    c: DistanceY(g0,g-4) = 6.5
    c: Tangent(g1,g4) = 1.5708
    c: Tangent(g1,g3) = -1.5708
    c: Tangent(g3,g2) = -1.5708
    c: Tangent(g4,g2) = 1.5708
    c: Horizontal(g3)
    c: Equal(g1,g2)
    c: PointOnObject(g1,g0)
    c: Radius(g2) = 3
    c: DistanceX(g4,g4) = 3
    c: DistanceX(g2,g0) = 7
FEATURE [PartDesign::Pocket] Pocket082
  BaseFeature = -> Pocket081
  Length = 5
  Length2 = 100
  Placement = pos=(0,0,0) rot=(0.57735,0.57735,0.57735;2.0944rad)
  Profile = -> Sketch227
  Type = 2
FEATURE [Sketcher::SketchObject] Sketch228
  ExternalGeometry = -> [Pocket082]
  FullyConstrained = true
  MapMode = 5
  Placement = pos=(0,0,0) rot=(0.57735,0.57735,0.57735;4.18879rad)
  Support = -> [Pocket082]
  sketch-geometry (9):
    g0: LineSegment StartX=0 StartY=8.5 StartZ=0 EndX=20 EndY=8.5 EndZ=0
    g1: ArcOfCircle CenterX=3 CenterY=9.5 CenterZ=0 NormalX=0 NormalY=0 NormalZ=1 AngleXU=0 Radius=1 StartAngle=0 EndAngle=3.14159
    g2: ArcOfCircle CenterX=3 CenterY=7.5 CenterZ=0 NormalX=0 NormalY=0 NormalZ=1 AngleXU=0 Radius=1 StartAngle=3.14159 EndAngle=6.28319
    g3: LineSegment StartX=2 StartY=9.5 StartZ=0 EndX=2 EndY=7.5 EndZ=0
    g4: LineSegment StartX=4 StartY=9.5 StartZ=0 EndX=4 EndY=7.5 EndZ=0
    g5: ArcOfCircle CenterX=18 CenterY=9.5 CenterZ=0 NormalX=0 NormalY=0 NormalZ=1 AngleXU=0 Radius=1 StartAngle=-9e-16 EndAngle=3.14159
    g6: ArcOfCircle CenterX=18 CenterY=7.5 CenterZ=0 NormalX=0 NormalY=0 NormalZ=1 AngleXU=0 Radius=1 StartAngle=3.14159 EndAngle=6.28319
    g7: LineSegment StartX=17 StartY=9.5 StartZ=0 EndX=17 EndY=7.5 EndZ=0
    g8: LineSegment StartX=19 StartY=9.5 StartZ=0 EndX=19 EndY=7.5 EndZ=0
  constraints (24):
    c: PointOnObject(g0,g-2)
    c: PointOnObject(g0,g-5)
    c: Horizontal(g0)
    c: DistanceY(g0,g-3) = 8.5
    c: Tangent(g1,g4) = 1.5708
    c: Tangent(g1,g3) = -1.5708
    c: Tangent(g3,g2) = -1.5708
    c: Tangent(g4,g2) = 1.5708
    c: Vertical(g3)
    c: Equal(g1,g2)
    c: Tangent(g5,g8) = 1.5708
    c: Tangent(g5,g7) = -1.5708
    c: Tangent(g7,g6) = -1.5708
    c: Tangent(g8,g6) = 1.5708
    c: Vertical(g7)
    c: Equal(g5,g6)
    c: Equal(g1,g5)
    c: Equal(g4,g7)
    c: DistanceY(g4,g4) = 2
    c: Radius(g1) = 1
    c: Horizontal(g5,g1)
    c: DistanceX(g0,g1) = 3
    c: DistanceX(g5,g0) = 2
    c: DistanceY(g0,g1) = 1
FEATURE [PartDesign::Pad] Pad112
  BaseFeature = -> Pocket082
  Direction = (1,1,1)
  Length = 1
  Length2 = 100
  Placement = pos=(0,0,0) rot=(0.57735,0.57735,0.57735;2.0944rad)
  Profile = -> Sketch228
  Type = 0
FEATURE [Sketcher::SketchObject] Sketch229
  ExternalGeometry = -> [Pad112]
  FullyConstrained = true
  MapMode = 5
  Placement = pos=(0,0,1e-16) rot=(0.707107,0.707107,0;3.14159rad)
  Support = -> [Pad112]
  sketch-geometry (9):
    g0: LineSegment StartX=0 StartY=8.5 StartZ=0 EndX=-20 EndY=8.5 EndZ=0
    g1: ArcOfCircle CenterX=-3 CenterY=7.5 CenterZ=0 NormalX=0 NormalY=0 NormalZ=1 AngleXU=0 Radius=1 StartAngle=3.14159 EndAngle=6.28319
    g2: ArcOfCircle CenterX=-3 CenterY=9.5 CenterZ=0 NormalX=0 NormalY=0 NormalZ=1 AngleXU=0 Radius=1 StartAngle=3e-16 EndAngle=3.14159
    g3: LineSegment StartX=-2 StartY=7.5 StartZ=0 EndX=-2 EndY=9.5 EndZ=0
    g4: LineSegment StartX=-4 StartY=7.5 StartZ=0 EndX=-4 EndY=9.5 EndZ=0
    g5: ArcOfCircle CenterX=-18 CenterY=9.5 CenterZ=0 NormalX=0 NormalY=0 NormalZ=1 AngleXU=0 Radius=1 StartAngle=0 EndAngle=3.14159
    g6: ArcOfCircle CenterX=-18 CenterY=7.5 CenterZ=0 NormalX=0 NormalY=0 NormalZ=1 AngleXU=0 Radius=1 StartAngle=3.14159 EndAngle=6.28319
    g7: LineSegment StartX=-19 StartY=9.5 StartZ=0 EndX=-19 EndY=7.5 EndZ=0
    g8: LineSegment StartX=-17 StartY=9.5 StartZ=0 EndX=-17 EndY=7.5 EndZ=0
  constraints (24):
    c: PointOnObject(g0,g-2)
    c: PointOnObject(g0,g-4)
    c: Horizontal(g0)
    c: DistanceY(g0,g-3) = 8.5
    c: Tangent(g1,g4) = 1.5708
    c: Tangent(g1,g3) = -1.5708
    c: Tangent(g3,g2) = -1.5708
    c: Tangent(g4,g2) = 1.5708
    c: Vertical(g3)
    c: Equal(g1,g2)
    c: Radius(g2) = 1
    c: DistanceY(g4,g4) = 2
    c: DistanceY(g0,g2) = 1
    c: DistanceX(g2,g0) = 3
    c: Tangent(g5,g8) = 1.5708
    c: Tangent(g5,g7) = -1.5708
    c: Tangent(g7,g6) = -1.5708
    c: Tangent(g8,g6) = 1.5708
    c: Vertical(g7)
    c: Equal(g5,g6)
    c: Equal(g5,g2)
    c: Equal(g8,g4)
    c: Horizontal(g5,g2)
    c: DistanceX(g0,g5) = 2
FEATURE [PartDesign::Pad] Pad113
  BaseFeature = -> Pad112
  Direction = (1,1,1)
  Length = 1
  Length2 = 100
  Placement = pos=(0,0,0) rot=(0.57735,0.57735,0.57735;2.0944rad)
  Profile = -> Sketch229
  Type = 0
FEATURE [PartDesign::Body] Body199  label="Corner002"
  Group = -> [Sketch224,Pad111,Sketch225,Pocket080,Sketch226,Pocket081,Sketch227,Pocket082,Sketch228,Pad112,Sketch229,Pad113]
  Origin = -> Origin271
  Tip = -> Pad113
FEATURE [App::Part] Part072  label="soporte90-003"
  Group = -> [Body199]
  Origin = -> Origin272
  Placement = pos=(321,339,20) rot=(0,0,1;-1.5708rad)
FEATURE [Sketcher::SketchObject] Sketch230
  FullyConstrained = true
  MapMode = 5
  Placement = pos=(0,0,0) rot=(0.57735,0.57735,0.57735;2.0944rad)
  Support = -> [YZ_Plane267]
  sketch-geometry (5):
    g0: LineSegment StartX=0 StartY=0 StartZ=0 EndX=0 EndY=20 EndZ=0
    g1: LineSegment StartX=0 StartY=20 StartZ=0 EndX=-3 EndY=20 EndZ=0
    g2: LineSegment StartX=-3 StartY=20 StartZ=0 EndX=-20 EndY=3 EndZ=0
    g3: LineSegment StartX=-20 StartY=3 StartZ=0 EndX=-20 EndY=0 EndZ=0
    g4: LineSegment StartX=-20 StartY=0 StartZ=0 EndX=0 EndY=0 EndZ=0
  constraints (14):
    c: Coincident(g-1,g0)
    c: PointOnObject(g0,g-2)
    c: Coincident(g0,g1)
    c: Horizontal(g1)
    c: Coincident(g1,g2)
    c: Coincident(g2,g3)
    c: PointOnObject(g3,g-1)
    c: Vertical(g3)
    c: Coincident(g3,g4)
    c: Coincident(g4,g0)
    c: DistanceY(g0,g0) = 20
    c: DistanceY(g3,g3) = 3
    c: DistanceX(g1,g1) = 3
    c: DistanceX(g4,g4) = 20
FEATURE [PartDesign::Pad] Pad114
  Direction = (1,1,1)
  Length = 17
  Length2 = 100
  Placement = pos=(0,0,0) rot=(0.57735,0.57735,0.57735;2.0944rad)
  Profile = -> Sketch230
  Type = 0
FEATURE [Sketcher::SketchObject] Sketch231
  ExternalGeometry = -> [Pad114]
  FullyConstrained = true
  MapMode = 5
  Placement = pos=(-8.8e-15,-20,4.4e-15) rot=(-0.57735,-0.57735,0.57735;4.18879rad)
  Support = -> [Pad114]
  sketch-geometry (4):
    g0: LineSegment StartX=-3 StartY=2 StartZ=0 EndX=-20 EndY=2 EndZ=0
    g1: LineSegment StartX=-20 StartY=2 StartZ=0 EndX=-20 EndY=15 EndZ=0
    g2: LineSegment StartX=-20 StartY=15 StartZ=0 EndX=-3 EndY=15 EndZ=0
    g3: LineSegment StartX=-3 StartY=15 StartZ=0 EndX=-3 EndY=2 EndZ=0
  constraints (12):
    c: Coincident(g0,g1)
    c: Coincident(g1,g2)
    c: Coincident(g2,g3)
    c: Coincident(g3,g0)
    c: Horizontal(g0)
    c: Horizontal(g2)
    c: Vertical(g1)
    c: Vertical(g3)
    c: PointOnObject(g0,g-3)
    c: DistanceY(g1,g-6) = 2
    c: DistanceY(g-6,g0) = 2
    c: PointOnObject(g1,g-6)
FEATURE [PartDesign::Pocket] Pocket083
  BaseFeature = -> Pad114
  Length = 17
  Length2 = 100
  Placement = pos=(0,0,0) rot=(0.57735,0.57735,0.57735;2.0944rad)
  Profile = -> Sketch231
  Type = 0
FEATURE [Sketcher::SketchObject] Sketch232
  ExternalGeometry = -> [Pocket083]
  FullyConstrained = true
  MapMode = 5
  Placement = pos=(-1.7e-15,-3,6e-16) rot=(-0.57735,-0.57735,0.57735;4.18879rad)
  Support = -> [Pocket083]
  sketch-geometry (5):
    g0: LineSegment StartX=-20 StartY=8.5 StartZ=0 EndX=-3 EndY=8.5 EndZ=0
    g1: ArcOfCircle CenterX=-10 CenterY=8.5 CenterZ=0 NormalX=0 NormalY=0 NormalZ=1 AngleXU=0 Radius=3 StartAngle=4.71239 EndAngle=7.85398
    g2: ArcOfCircle CenterX=-13 CenterY=8.5 CenterZ=0 NormalX=0 NormalY=0 NormalZ=1 AngleXU=0 Radius=3 StartAngle=1.5708 EndAngle=4.71239
    g3: LineSegment StartX=-10 StartY=11.5 StartZ=0 EndX=-13 EndY=11.5 EndZ=0
    g4: LineSegment StartX=-10 StartY=5.5 StartZ=0 EndX=-13 EndY=5.5 EndZ=0
  constraints (14):
    c: PointOnObject(g0,g-6)
    c: PointOnObject(g0,g-4)
    c: Horizontal(g0)
    c: DistanceY(g0,g-4) = 6.5
    c: Tangent(g1,g4) = 1.5708
    c: Tangent(g1,g3) = -1.5708
    c: Tangent(g3,g2) = -1.5708
    c: Tangent(g4,g2) = 1.5708
    c: Horizontal(g3)
    c: Equal(g1,g2)
    c: PointOnObject(g1,g0)
    c: Radius(g1) = 3
    c: DistanceX(g3,g3) = 3
    c: DistanceX(g0,g2) = 7
FEATURE [PartDesign::Pocket] Pocket084
  BaseFeature = -> Pocket083
  Length = 5
  Length2 = 100
  Placement = pos=(0,0,0) rot=(0.57735,0.57735,0.57735;2.0944rad)
  Profile = -> Sketch232
  Type = 2
FEATURE [Sketcher::SketchObject] Sketch233
  ExternalGeometry = -> [Pocket084]
  FullyConstrained = true
  MapMode = 5
  Placement = pos=(-3e-16,1.2e-15,3) rot=(0,0,-1;1.5708rad)
  Support = -> [Pocket084]
  sketch-geometry (5):
    g0: LineSegment StartX=3 StartY=8.5 StartZ=0 EndX=20 EndY=8.5 EndZ=0
    g1: ArcOfCircle CenterX=10 CenterY=8.5 CenterZ=0 NormalX=0 NormalY=0 NormalZ=1 AngleXU=0 Radius=3 StartAngle=1.5708 EndAngle=4.71239
    g2: ArcOfCircle CenterX=13 CenterY=8.5 CenterZ=0 NormalX=0 NormalY=0 NormalZ=1 AngleXU=0 Radius=3 StartAngle=4.71239 EndAngle=7.85398
    g3: LineSegment StartX=10 StartY=5.5 StartZ=0 EndX=13 EndY=5.5 EndZ=0
    g4: LineSegment StartX=10 StartY=11.5 StartZ=0 EndX=13 EndY=11.5 EndZ=0
  constraints (14):
    c: PointOnObject(g0,g-4)
    c: PointOnObject(g0,g-5)
    c: Horizontal(g0)
    c: DistanceY(g0,g-4) = 6.5
    c: Tangent(g1,g4) = 1.5708
    c: Tangent(g1,g3) = -1.5708
    c: Tangent(g3,g2) = -1.5708
    c: Tangent(g4,g2) = 1.5708
    c: Horizontal(g3)
    c: Equal(g1,g2)
    c: PointOnObject(g1,g0)
    c: Radius(g2) = 3
    c: DistanceX(g4,g4) = 3
    c: DistanceX(g2,g0) = 7
FEATURE [PartDesign::Pocket] Pocket085
  BaseFeature = -> Pocket084
  Length = 5
  Length2 = 100
  Placement = pos=(0,0,0) rot=(0.57735,0.57735,0.57735;2.0944rad)
  Profile = -> Sketch233
  Type = 2
FEATURE [Sketcher::SketchObject] Sketch234
  ExternalGeometry = -> [Pocket085]
  FullyConstrained = true
  MapMode = 5
  Placement = pos=(0,0,0) rot=(0.57735,0.57735,0.57735;4.18879rad)
  Support = -> [Pocket085]
  sketch-geometry (9):
    g0: LineSegment StartX=0 StartY=8.5 StartZ=0 EndX=20 EndY=8.5 EndZ=0
    g1: ArcOfCircle CenterX=3 CenterY=9.5 CenterZ=0 NormalX=0 NormalY=0 NormalZ=1 AngleXU=0 Radius=1 StartAngle=0 EndAngle=3.14159
    g2: ArcOfCircle CenterX=3 CenterY=7.5 CenterZ=0 NormalX=0 NormalY=0 NormalZ=1 AngleXU=0 Radius=1 StartAngle=3.14159 EndAngle=6.28319
    g3: LineSegment StartX=2 StartY=9.5 StartZ=0 EndX=2 EndY=7.5 EndZ=0
    g4: LineSegment StartX=4 StartY=9.5 StartZ=0 EndX=4 EndY=7.5 EndZ=0
    g5: ArcOfCircle CenterX=18 CenterY=9.5 CenterZ=0 NormalX=0 NormalY=0 NormalZ=1 AngleXU=0 Radius=1 StartAngle=-9e-16 EndAngle=3.14159
    g6: ArcOfCircle CenterX=18 CenterY=7.5 CenterZ=0 NormalX=0 NormalY=0 NormalZ=1 AngleXU=0 Radius=1 StartAngle=3.14159 EndAngle=6.28319
    g7: LineSegment StartX=17 StartY=9.5 StartZ=0 EndX=17 EndY=7.5 EndZ=0
    g8: LineSegment StartX=19 StartY=9.5 StartZ=0 EndX=19 EndY=7.5 EndZ=0
  constraints (24):
    c: PointOnObject(g0,g-2)
    c: PointOnObject(g0,g-5)
    c: Horizontal(g0)
    c: DistanceY(g0,g-3) = 8.5
    c: Tangent(g1,g4) = 1.5708
    c: Tangent(g1,g3) = -1.5708
    c: Tangent(g3,g2) = -1.5708
    c: Tangent(g4,g2) = 1.5708
    c: Vertical(g3)
    c: Equal(g1,g2)
    c: Tangent(g5,g8) = 1.5708
    c: Tangent(g5,g7) = -1.5708
    c: Tangent(g7,g6) = -1.5708
    c: Tangent(g8,g6) = 1.5708
    c: Vertical(g7)
    c: Equal(g5,g6)
    c: Equal(g1,g5)
    c: Equal(g4,g7)
    c: DistanceY(g4,g4) = 2
    c: Radius(g1) = 1
    c: Horizontal(g5,g1)
    c: DistanceX(g0,g1) = 3
    c: DistanceX(g5,g0) = 2
    c: DistanceY(g0,g1) = 1
FEATURE [PartDesign::Pad] Pad115
  BaseFeature = -> Pocket085
  Direction = (1,1,1)
  Length = 1
  Length2 = 100
  Placement = pos=(0,0,0) rot=(0.57735,0.57735,0.57735;2.0944rad)
  Profile = -> Sketch234
  Type = 0
FEATURE [Sketcher::SketchObject] Sketch235
  ExternalGeometry = -> [Pad115]
  FullyConstrained = true
  MapMode = 5
  Placement = pos=(0,0,1e-16) rot=(0.707107,0.707107,0;3.14159rad)
  Support = -> [Pad115]
  sketch-geometry (9):
    g0: LineSegment StartX=0 StartY=8.5 StartZ=0 EndX=-20 EndY=8.5 EndZ=0
    g1: ArcOfCircle CenterX=-3 CenterY=7.5 CenterZ=0 NormalX=0 NormalY=0 NormalZ=1 AngleXU=0 Radius=1 StartAngle=3.14159 EndAngle=6.28319
    g2: ArcOfCircle CenterX=-3 CenterY=9.5 CenterZ=0 NormalX=0 NormalY=0 NormalZ=1 AngleXU=0 Radius=1 StartAngle=3e-16 EndAngle=3.14159
    g3: LineSegment StartX=-2 StartY=7.5 StartZ=0 EndX=-2 EndY=9.5 EndZ=0
    g4: LineSegment StartX=-4 StartY=7.5 StartZ=0 EndX=-4 EndY=9.5 EndZ=0
    g5: ArcOfCircle CenterX=-18 CenterY=9.5 CenterZ=0 NormalX=0 NormalY=0 NormalZ=1 AngleXU=0 Radius=1 StartAngle=0 EndAngle=3.14159
    g6: ArcOfCircle CenterX=-18 CenterY=7.5 CenterZ=0 NormalX=0 NormalY=0 NormalZ=1 AngleXU=0 Radius=1 StartAngle=3.14159 EndAngle=6.28319
    g7: LineSegment StartX=-19 StartY=9.5 StartZ=0 EndX=-19 EndY=7.5 EndZ=0
    g8: LineSegment StartX=-17 StartY=9.5 StartZ=0 EndX=-17 EndY=7.5 EndZ=0
  constraints (24):
    c: PointOnObject(g0,g-2)
    c: PointOnObject(g0,g-4)
    c: Horizontal(g0)
    c: DistanceY(g0,g-3) = 8.5
    c: Tangent(g1,g4) = 1.5708
    c: Tangent(g1,g3) = -1.5708
    c: Tangent(g3,g2) = -1.5708
    c: Tangent(g4,g2) = 1.5708
    c: Vertical(g3)
    c: Equal(g1,g2)
    c: Radius(g2) = 1
    c: DistanceY(g4,g4) = 2
    c: DistanceY(g0,g2) = 1
    c: DistanceX(g2,g0) = 3
    c: Tangent(g5,g8) = 1.5708
    c: Tangent(g5,g7) = -1.5708
    c: Tangent(g7,g6) = -1.5708
    c: Tangent(g8,g6) = 1.5708
    c: Vertical(g7)
    c: Equal(g5,g6)
    c: Equal(g5,g2)
    c: Equal(g8,g4)
    c: Horizontal(g5,g2)
    c: DistanceX(g0,g5) = 2
FEATURE [PartDesign::Pad] Pad116
  BaseFeature = -> Pad115
  Direction = (1,1,1)
  Length = 1
  Length2 = 100
  Placement = pos=(0,0,0) rot=(0.57735,0.57735,0.57735;2.0944rad)
  Profile = -> Sketch235
  Type = 0
FEATURE [PartDesign::Body] Body200  label="Corner003"
  Group = -> [Sketch230,Pad114,Sketch231,Pocket083,Sketch232,Pocket084,Sketch233,Pocket085,Sketch234,Pad115,Sketch235,Pad116]
  Origin = -> Origin273
  Tip = -> Pad116
FEATURE [App::Part] Part073  label="soporte90-004"
  Group = -> [Body200]
  Origin = -> Origin274
  Placement = pos=(20,1,20) rot=(0,0,1;1.5708rad)
FEATURE [Sketcher::SketchObject] Sketch236
  FullyConstrained = true
  MapMode = 5
  Placement = pos=(0,0,0) rot=(0.57735,0.57735,0.57735;2.0944rad)
  Support = -> [YZ_Plane269]
  sketch-geometry (5):
    g0: LineSegment StartX=0 StartY=0 StartZ=0 EndX=0 EndY=20 EndZ=0
    g1: LineSegment StartX=0 StartY=20 StartZ=0 EndX=-3 EndY=20 EndZ=0
    g2: LineSegment StartX=-3 StartY=20 StartZ=0 EndX=-20 EndY=3 EndZ=0
    g3: LineSegment StartX=-20 StartY=3 StartZ=0 EndX=-20 EndY=0 EndZ=0
    g4: LineSegment StartX=-20 StartY=0 StartZ=0 EndX=0 EndY=0 EndZ=0
  constraints (14):
    c: Coincident(g-1,g0)
    c: PointOnObject(g0,g-2)
    c: Coincident(g0,g1)
    c: Horizontal(g1)
    c: Coincident(g1,g2)
    c: Coincident(g2,g3)
    c: PointOnObject(g3,g-1)
    c: Vertical(g3)
    c: Coincident(g3,g4)
    c: Coincident(g4,g0)
    c: DistanceY(g0,g0) = 20
    c: DistanceY(g3,g3) = 3
    c: DistanceX(g1,g1) = 3
    c: DistanceX(g4,g4) = 20
FEATURE [PartDesign::Pad] Pad117
  Direction = (1,1,1)
  Length = 17
  Length2 = 100
  Placement = pos=(0,0,0) rot=(0.57735,0.57735,0.57735;2.0944rad)
  Profile = -> Sketch236
  Type = 0
FEATURE [Sketcher::SketchObject] Sketch237
  ExternalGeometry = -> [Pad117]
  FullyConstrained = true
  MapMode = 5
  Placement = pos=(-8.8e-15,-20,4.4e-15) rot=(-0.57735,-0.57735,0.57735;4.18879rad)
  Support = -> [Pad117]
  sketch-geometry (4):
    g0: LineSegment StartX=-3 StartY=2 StartZ=0 EndX=-20 EndY=2 EndZ=0
    g1: LineSegment StartX=-20 StartY=2 StartZ=0 EndX=-20 EndY=15 EndZ=0
    g2: LineSegment StartX=-20 StartY=15 StartZ=0 EndX=-3 EndY=15 EndZ=0
    g3: LineSegment StartX=-3 StartY=15 StartZ=0 EndX=-3 EndY=2 EndZ=0
  constraints (12):
    c: Coincident(g0,g1)
    c: Coincident(g1,g2)
    c: Coincident(g2,g3)
    c: Coincident(g3,g0)
    c: Horizontal(g0)
    c: Horizontal(g2)
    c: Vertical(g1)
    c: Vertical(g3)
    c: PointOnObject(g0,g-3)
    c: DistanceY(g1,g-6) = 2
    c: DistanceY(g-6,g0) = 2
    c: PointOnObject(g1,g-6)
FEATURE [PartDesign::Pocket] Pocket086
  BaseFeature = -> Pad117
  Length = 17
  Length2 = 100
  Placement = pos=(0,0,0) rot=(0.57735,0.57735,0.57735;2.0944rad)
  Profile = -> Sketch237
  Type = 0
FEATURE [Sketcher::SketchObject] Sketch238
  ExternalGeometry = -> [Pocket086]
  FullyConstrained = true
  MapMode = 5
  Placement = pos=(-1.7e-15,-3,6e-16) rot=(-0.57735,-0.57735,0.57735;4.18879rad)
  Support = -> [Pocket086]
  sketch-geometry (5):
    g0: LineSegment StartX=-20 StartY=8.5 StartZ=0 EndX=-3 EndY=8.5 EndZ=0
    g1: ArcOfCircle CenterX=-10 CenterY=8.5 CenterZ=0 NormalX=0 NormalY=0 NormalZ=1 AngleXU=0 Radius=3 StartAngle=4.71239 EndAngle=7.85398
    g2: ArcOfCircle CenterX=-13 CenterY=8.5 CenterZ=0 NormalX=0 NormalY=0 NormalZ=1 AngleXU=0 Radius=3 StartAngle=1.5708 EndAngle=4.71239
    g3: LineSegment StartX=-10 StartY=11.5 StartZ=0 EndX=-13 EndY=11.5 EndZ=0
    g4: LineSegment StartX=-10 StartY=5.5 StartZ=0 EndX=-13 EndY=5.5 EndZ=0
  constraints (14):
    c: PointOnObject(g0,g-6)
    c: PointOnObject(g0,g-4)
    c: Horizontal(g0)
    c: DistanceY(g0,g-4) = 6.5
    c: Tangent(g1,g4) = 1.5708
    c: Tangent(g1,g3) = -1.5708
    c: Tangent(g3,g2) = -1.5708
    c: Tangent(g4,g2) = 1.5708
    c: Horizontal(g3)
    c: Equal(g1,g2)
    c: PointOnObject(g1,g0)
    c: Radius(g1) = 3
    c: DistanceX(g3,g3) = 3
    c: DistanceX(g0,g2) = 7
FEATURE [PartDesign::Pocket] Pocket087
  BaseFeature = -> Pocket086
  Length = 5
  Length2 = 100
  Placement = pos=(0,0,0) rot=(0.57735,0.57735,0.57735;2.0944rad)
  Profile = -> Sketch238
  Type = 2
FEATURE [Sketcher::SketchObject] Sketch239
  ExternalGeometry = -> [Pocket087]
  FullyConstrained = true
  MapMode = 5
  Placement = pos=(-3e-16,1.2e-15,3) rot=(0,0,-1;1.5708rad)
  Support = -> [Pocket087]
  sketch-geometry (5):
    g0: LineSegment StartX=3 StartY=8.5 StartZ=0 EndX=20 EndY=8.5 EndZ=0
    g1: ArcOfCircle CenterX=10 CenterY=8.5 CenterZ=0 NormalX=0 NormalY=0 NormalZ=1 AngleXU=0 Radius=3 StartAngle=1.5708 EndAngle=4.71239
    g2: ArcOfCircle CenterX=13 CenterY=8.5 CenterZ=0 NormalX=0 NormalY=0 NormalZ=1 AngleXU=0 Radius=3 StartAngle=4.71239 EndAngle=7.85398
    g3: LineSegment StartX=10 StartY=5.5 StartZ=0 EndX=13 EndY=5.5 EndZ=0
    g4: LineSegment StartX=10 StartY=11.5 StartZ=0 EndX=13 EndY=11.5 EndZ=0
  constraints (14):
    c: PointOnObject(g0,g-4)
    c: PointOnObject(g0,g-5)
    c: Horizontal(g0)
    c: DistanceY(g0,g-4) = 6.5
    c: Tangent(g1,g4) = 1.5708
    c: Tangent(g1,g3) = -1.5708
    c: Tangent(g3,g2) = -1.5708
    c: Tangent(g4,g2) = 1.5708
    c: Horizontal(g3)
    c: Equal(g1,g2)
    c: PointOnObject(g1,g0)
    c: Radius(g2) = 3
    c: DistanceX(g4,g4) = 3
    c: DistanceX(g2,g0) = 7
FEATURE [PartDesign::Pocket] Pocket088
  BaseFeature = -> Pocket087
  Length = 5
  Length2 = 100
  Placement = pos=(0,0,0) rot=(0.57735,0.57735,0.57735;2.0944rad)
  Profile = -> Sketch239
  Type = 2
FEATURE [Sketcher::SketchObject] Sketch240
  ExternalGeometry = -> [Pocket088]
  FullyConstrained = true
  MapMode = 5
  Placement = pos=(0,0,0) rot=(0.57735,0.57735,0.57735;4.18879rad)
  Support = -> [Pocket088]
  sketch-geometry (9):
    g0: LineSegment StartX=0 StartY=8.5 StartZ=0 EndX=20 EndY=8.5 EndZ=0
    g1: ArcOfCircle CenterX=3 CenterY=9.5 CenterZ=0 NormalX=0 NormalY=0 NormalZ=1 AngleXU=0 Radius=1 StartAngle=0 EndAngle=3.14159
    g2: ArcOfCircle CenterX=3 CenterY=7.5 CenterZ=0 NormalX=0 NormalY=0 NormalZ=1 AngleXU=0 Radius=1 StartAngle=3.14159 EndAngle=6.28319
    g3: LineSegment StartX=2 StartY=9.5 StartZ=0 EndX=2 EndY=7.5 EndZ=0
    g4: LineSegment StartX=4 StartY=9.5 StartZ=0 EndX=4 EndY=7.5 EndZ=0
    g5: ArcOfCircle CenterX=18 CenterY=9.5 CenterZ=0 NormalX=0 NormalY=0 NormalZ=1 AngleXU=0 Radius=1 StartAngle=-9e-16 EndAngle=3.14159
    g6: ArcOfCircle CenterX=18 CenterY=7.5 CenterZ=0 NormalX=0 NormalY=0 NormalZ=1 AngleXU=0 Radius=1 StartAngle=3.14159 EndAngle=6.28319
    g7: LineSegment StartX=17 StartY=9.5 StartZ=0 EndX=17 EndY=7.5 EndZ=0
    g8: LineSegment StartX=19 StartY=9.5 StartZ=0 EndX=19 EndY=7.5 EndZ=0
  constraints (24):
    c: PointOnObject(g0,g-2)
    c: PointOnObject(g0,g-5)
    c: Horizontal(g0)
    c: DistanceY(g0,g-3) = 8.5
    c: Tangent(g1,g4) = 1.5708
    c: Tangent(g1,g3) = -1.5708
    c: Tangent(g3,g2) = -1.5708
    c: Tangent(g4,g2) = 1.5708
    c: Vertical(g3)
    c: Equal(g1,g2)
    c: Tangent(g5,g8) = 1.5708
    c: Tangent(g5,g7) = -1.5708
    c: Tangent(g7,g6) = -1.5708
    c: Tangent(g8,g6) = 1.5708
    c: Vertical(g7)
    c: Equal(g5,g6)
    c: Equal(g1,g5)
    c: Equal(g4,g7)
    c: DistanceY(g4,g4) = 2
    c: Radius(g1) = 1
    c: Horizontal(g5,g1)
    c: DistanceX(g0,g1) = 3
    c: DistanceX(g5,g0) = 2
    c: DistanceY(g0,g1) = 1
FEATURE [PartDesign::Pad] Pad118
  BaseFeature = -> Pocket088
  Direction = (1,1,1)
  Length = 1
  Length2 = 100
  Placement = pos=(0,0,0) rot=(0.57735,0.57735,0.57735;2.0944rad)
  Profile = -> Sketch240
  Type = 0
FEATURE [Sketcher::SketchObject] Sketch241
  ExternalGeometry = -> [Pad118]
  FullyConstrained = true
  MapMode = 5
  Placement = pos=(0,0,1e-16) rot=(0.707107,0.707107,0;3.14159rad)
  Support = -> [Pad118]
  sketch-geometry (9):
    g0: LineSegment StartX=0 StartY=8.5 StartZ=0 EndX=-20 EndY=8.5 EndZ=0
    g1: ArcOfCircle CenterX=-3 CenterY=7.5 CenterZ=0 NormalX=0 NormalY=0 NormalZ=1 AngleXU=0 Radius=1 StartAngle=3.14159 EndAngle=6.28319
    g2: ArcOfCircle CenterX=-3 CenterY=9.5 CenterZ=0 NormalX=0 NormalY=0 NormalZ=1 AngleXU=0 Radius=1 StartAngle=3e-16 EndAngle=3.14159
    g3: LineSegment StartX=-2 StartY=7.5 StartZ=0 EndX=-2 EndY=9.5 EndZ=0
    g4: LineSegment StartX=-4 StartY=7.5 StartZ=0 EndX=-4 EndY=9.5 EndZ=0
    g5: ArcOfCircle CenterX=-18 CenterY=9.5 CenterZ=0 NormalX=0 NormalY=0 NormalZ=1 AngleXU=0 Radius=1 StartAngle=0 EndAngle=3.14159
    g6: ArcOfCircle CenterX=-18 CenterY=7.5 CenterZ=0 NormalX=0 NormalY=0 NormalZ=1 AngleXU=0 Radius=1 StartAngle=3.14159 EndAngle=6.28319
    g7: LineSegment StartX=-19 StartY=9.5 StartZ=0 EndX=-19 EndY=7.5 EndZ=0
    g8: LineSegment StartX=-17 StartY=9.5 StartZ=0 EndX=-17 EndY=7.5 EndZ=0
  constraints (24):
    c: PointOnObject(g0,g-2)
    c: PointOnObject(g0,g-4)
    c: Horizontal(g0)
    c: DistanceY(g0,g-3) = 8.5
    c: Tangent(g1,g4) = 1.5708
    c: Tangent(g1,g3) = -1.5708
    c: Tangent(g3,g2) = -1.5708
    c: Tangent(g4,g2) = 1.5708
    c: Vertical(g3)
    c: Equal(g1,g2)
    c: Radius(g2) = 1
    c: DistanceY(g4,g4) = 2
    c: DistanceY(g0,g2) = 1
    c: DistanceX(g2,g0) = 3
    c: Tangent(g5,g8) = 1.5708
    c: Tangent(g5,g7) = -1.5708
    c: Tangent(g7,g6) = -1.5708
    c: Tangent(g8,g6) = 1.5708
    c: Vertical(g7)
    c: Equal(g5,g6)
    c: Equal(g5,g2)
    c: Equal(g8,g4)
    c: Horizontal(g5,g2)
    c: DistanceX(g0,g5) = 2
FEATURE [PartDesign::Pad] Pad119
  BaseFeature = -> Pad118
  Direction = (1,1,1)
  Length = 1
  Length2 = 100
  Placement = pos=(0,0,0) rot=(0.57735,0.57735,0.57735;2.0944rad)
  Profile = -> Sketch241
  Type = 0
FEATURE [PartDesign::Body] Body201  label="Corner004"
  Group = -> [Sketch236,Pad117,Sketch237,Pocket086,Sketch238,Pocket087,Sketch239,Pocket088,Sketch240,Pad118,Sketch241,Pad119]
  Origin = -> Origin275
  Tip = -> Pad119
FEATURE [App::Part] Part074  label="soporte90-005"
  Group = -> [Body201]
  Origin = -> Origin276
  Placement = pos=(20,340,170) rot=(0.707107,-0.707107,0;3.14159rad)
FEATURE [Sketcher::SketchObject] Sketch242
  FullyConstrained = true
  MapMode = 5
  Placement = pos=(0,0,0) rot=(0.57735,0.57735,0.57735;2.0944rad)
  Support = -> [YZ_Plane271]
  sketch-geometry (5):
    g0: LineSegment StartX=0 StartY=0 StartZ=0 EndX=0 EndY=20 EndZ=0
    g1: LineSegment StartX=0 StartY=20 StartZ=0 EndX=-3 EndY=20 EndZ=0
    g2: LineSegment StartX=-3 StartY=20 StartZ=0 EndX=-20 EndY=3 EndZ=0
    g3: LineSegment StartX=-20 StartY=3 StartZ=0 EndX=-20 EndY=0 EndZ=0
    g4: LineSegment StartX=-20 StartY=0 StartZ=0 EndX=0 EndY=0 EndZ=0
  constraints (14):
    c: Coincident(g-1,g0)
    c: PointOnObject(g0,g-2)
    c: Coincident(g0,g1)
    c: Horizontal(g1)
    c: Coincident(g1,g2)
    c: Coincident(g2,g3)
    c: PointOnObject(g3,g-1)
    c: Vertical(g3)
    c: Coincident(g3,g4)
    c: Coincident(g4,g0)
    c: DistanceY(g0,g0) = 20
    c: DistanceY(g3,g3) = 3
    c: DistanceX(g1,g1) = 3
    c: DistanceX(g4,g4) = 20
FEATURE [PartDesign::Pad] Pad120
  Direction = (1,1,1)
  Length = 17
  Length2 = 100
  Placement = pos=(0,0,0) rot=(0.57735,0.57735,0.57735;2.0944rad)
  Profile = -> Sketch242
  Type = 0
FEATURE [Sketcher::SketchObject] Sketch243
  ExternalGeometry = -> [Pad120]
  FullyConstrained = true
  MapMode = 5
  Placement = pos=(-8.8e-15,-20,4.4e-15) rot=(-0.57735,-0.57735,0.57735;4.18879rad)
  Support = -> [Pad120]
  sketch-geometry (4):
    g0: LineSegment StartX=-3 StartY=2 StartZ=0 EndX=-20 EndY=2 EndZ=0
    g1: LineSegment StartX=-20 StartY=2 StartZ=0 EndX=-20 EndY=15 EndZ=0
    g2: LineSegment StartX=-20 StartY=15 StartZ=0 EndX=-3 EndY=15 EndZ=0
    g3: LineSegment StartX=-3 StartY=15 StartZ=0 EndX=-3 EndY=2 EndZ=0
  constraints (12):
    c: Coincident(g0,g1)
    c: Coincident(g1,g2)
    c: Coincident(g2,g3)
    c: Coincident(g3,g0)
    c: Horizontal(g0)
    c: Horizontal(g2)
    c: Vertical(g1)
    c: Vertical(g3)
    c: PointOnObject(g0,g-3)
    c: DistanceY(g1,g-6) = 2
    c: DistanceY(g-6,g0) = 2
    c: PointOnObject(g1,g-6)
FEATURE [PartDesign::Pocket] Pocket089
  BaseFeature = -> Pad120
  Length = 17
  Length2 = 100
  Placement = pos=(0,0,0) rot=(0.57735,0.57735,0.57735;2.0944rad)
  Profile = -> Sketch243
  Type = 0
FEATURE [Sketcher::SketchObject] Sketch244
  ExternalGeometry = -> [Pocket089]
  FullyConstrained = true
  MapMode = 5
  Placement = pos=(-1.7e-15,-3,6e-16) rot=(-0.57735,-0.57735,0.57735;4.18879rad)
  Support = -> [Pocket089]
  sketch-geometry (5):
    g0: LineSegment StartX=-20 StartY=8.5 StartZ=0 EndX=-3 EndY=8.5 EndZ=0
    g1: ArcOfCircle CenterX=-10 CenterY=8.5 CenterZ=0 NormalX=0 NormalY=0 NormalZ=1 AngleXU=0 Radius=3 StartAngle=4.71239 EndAngle=7.85398
    g2: ArcOfCircle CenterX=-13 CenterY=8.5 CenterZ=0 NormalX=0 NormalY=0 NormalZ=1 AngleXU=0 Radius=3 StartAngle=1.5708 EndAngle=4.71239
    g3: LineSegment StartX=-10 StartY=11.5 StartZ=0 EndX=-13 EndY=11.5 EndZ=0
    g4: LineSegment StartX=-10 StartY=5.5 StartZ=0 EndX=-13 EndY=5.5 EndZ=0
  constraints (14):
    c: PointOnObject(g0,g-6)
    c: PointOnObject(g0,g-4)
    c: Horizontal(g0)
    c: DistanceY(g0,g-4) = 6.5
    c: Tangent(g1,g4) = 1.5708
    c: Tangent(g1,g3) = -1.5708
    c: Tangent(g3,g2) = -1.5708
    c: Tangent(g4,g2) = 1.5708
    c: Horizontal(g3)
    c: Equal(g1,g2)
    c: PointOnObject(g1,g0)
    c: Radius(g1) = 3
    c: DistanceX(g3,g3) = 3
    c: DistanceX(g0,g2) = 7
FEATURE [PartDesign::Pocket] Pocket090
  BaseFeature = -> Pocket089
  Length = 5
  Length2 = 100
  Placement = pos=(0,0,0) rot=(0.57735,0.57735,0.57735;2.0944rad)
  Profile = -> Sketch244
  Type = 2
FEATURE [Sketcher::SketchObject] Sketch245
  ExternalGeometry = -> [Pocket090]
  FullyConstrained = true
  MapMode = 5
  Placement = pos=(-3e-16,1.2e-15,3) rot=(0,0,-1;1.5708rad)
  Support = -> [Pocket090]
  sketch-geometry (5):
    g0: LineSegment StartX=3 StartY=8.5 StartZ=0 EndX=20 EndY=8.5 EndZ=0
    g1: ArcOfCircle CenterX=10 CenterY=8.5 CenterZ=0 NormalX=0 NormalY=0 NormalZ=1 AngleXU=0 Radius=3 StartAngle=1.5708 EndAngle=4.71239
    g2: ArcOfCircle CenterX=13 CenterY=8.5 CenterZ=0 NormalX=0 NormalY=0 NormalZ=1 AngleXU=0 Radius=3 StartAngle=4.71239 EndAngle=7.85398
    g3: LineSegment StartX=10 StartY=5.5 StartZ=0 EndX=13 EndY=5.5 EndZ=0
    g4: LineSegment StartX=10 StartY=11.5 StartZ=0 EndX=13 EndY=11.5 EndZ=0
  constraints (14):
    c: PointOnObject(g0,g-4)
    c: PointOnObject(g0,g-5)
    c: Horizontal(g0)
    c: DistanceY(g0,g-4) = 6.5
    c: Tangent(g1,g4) = 1.5708
    c: Tangent(g1,g3) = -1.5708
    c: Tangent(g3,g2) = -1.5708
    c: Tangent(g4,g2) = 1.5708
    c: Horizontal(g3)
    c: Equal(g1,g2)
    c: PointOnObject(g1,g0)
    c: Radius(g2) = 3
    c: DistanceX(g4,g4) = 3
    c: DistanceX(g2,g0) = 7
FEATURE [PartDesign::Pocket] Pocket091
  BaseFeature = -> Pocket090
  Length = 5
  Length2 = 100
  Placement = pos=(0,0,0) rot=(0.57735,0.57735,0.57735;2.0944rad)
  Profile = -> Sketch245
  Type = 2
FEATURE [Sketcher::SketchObject] Sketch246
  ExternalGeometry = -> [Pocket091]
  FullyConstrained = true
  MapMode = 5
  Placement = pos=(0,0,0) rot=(0.57735,0.57735,0.57735;4.18879rad)
  Support = -> [Pocket091]
  sketch-geometry (9):
    g0: LineSegment StartX=0 StartY=8.5 StartZ=0 EndX=20 EndY=8.5 EndZ=0
    g1: ArcOfCircle CenterX=3 CenterY=9.5 CenterZ=0 NormalX=0 NormalY=0 NormalZ=1 AngleXU=0 Radius=1 StartAngle=0 EndAngle=3.14159
    g2: ArcOfCircle CenterX=3 CenterY=7.5 CenterZ=0 NormalX=0 NormalY=0 NormalZ=1 AngleXU=0 Radius=1 StartAngle=3.14159 EndAngle=6.28319
    g3: LineSegment StartX=2 StartY=9.5 StartZ=0 EndX=2 EndY=7.5 EndZ=0
    g4: LineSegment StartX=4 StartY=9.5 StartZ=0 EndX=4 EndY=7.5 EndZ=0
    g5: ArcOfCircle CenterX=18 CenterY=9.5 CenterZ=0 NormalX=0 NormalY=0 NormalZ=1 AngleXU=0 Radius=1 StartAngle=-9e-16 EndAngle=3.14159
    g6: ArcOfCircle CenterX=18 CenterY=7.5 CenterZ=0 NormalX=0 NormalY=0 NormalZ=1 AngleXU=0 Radius=1 StartAngle=3.14159 EndAngle=6.28319
    g7: LineSegment StartX=17 StartY=9.5 StartZ=0 EndX=17 EndY=7.5 EndZ=0
    g8: LineSegment StartX=19 StartY=9.5 StartZ=0 EndX=19 EndY=7.5 EndZ=0
  constraints (24):
    c: PointOnObject(g0,g-2)
    c: PointOnObject(g0,g-5)
    c: Horizontal(g0)
    c: DistanceY(g0,g-3) = 8.5
    c: Tangent(g1,g4) = 1.5708
    c: Tangent(g1,g3) = -1.5708
    c: Tangent(g3,g2) = -1.5708
    c: Tangent(g4,g2) = 1.5708
    c: Vertical(g3)
    c: Equal(g1,g2)
    c: Tangent(g5,g8) = 1.5708
    c: Tangent(g5,g7) = -1.5708
    c: Tangent(g7,g6) = -1.5708
    c: Tangent(g8,g6) = 1.5708
    c: Vertical(g7)
    c: Equal(g5,g6)
    c: Equal(g1,g5)
    c: Equal(g4,g7)
    c: DistanceY(g4,g4) = 2
    c: Radius(g1) = 1
    c: Horizontal(g5,g1)
    c: DistanceX(g0,g1) = 3
    c: DistanceX(g5,g0) = 2
    c: DistanceY(g0,g1) = 1
FEATURE [PartDesign::Pad] Pad121
  BaseFeature = -> Pocket091
  Direction = (1,1,1)
  Length = 1
  Length2 = 100
  Placement = pos=(0,0,0) rot=(0.57735,0.57735,0.57735;2.0944rad)
  Profile = -> Sketch246
  Type = 0
FEATURE [Sketcher::SketchObject] Sketch247
  ExternalGeometry = -> [Pad121]
  FullyConstrained = true
  MapMode = 5
  Placement = pos=(0,0,1e-16) rot=(0.707107,0.707107,0;3.14159rad)
  Support = -> [Pad121]
  sketch-geometry (9):
    g0: LineSegment StartX=0 StartY=8.5 StartZ=0 EndX=-20 EndY=8.5 EndZ=0
    g1: ArcOfCircle CenterX=-3 CenterY=7.5 CenterZ=0 NormalX=0 NormalY=0 NormalZ=1 AngleXU=0 Radius=1 StartAngle=3.14159 EndAngle=6.28319
    g2: ArcOfCircle CenterX=-3 CenterY=9.5 CenterZ=0 NormalX=0 NormalY=0 NormalZ=1 AngleXU=0 Radius=1 StartAngle=3e-16 EndAngle=3.14159
    g3: LineSegment StartX=-2 StartY=7.5 StartZ=0 EndX=-2 EndY=9.5 EndZ=0
    g4: LineSegment StartX=-4 StartY=7.5 StartZ=0 EndX=-4 EndY=9.5 EndZ=0
    g5: ArcOfCircle CenterX=-18 CenterY=9.5 CenterZ=0 NormalX=0 NormalY=0 NormalZ=1 AngleXU=0 Radius=1 StartAngle=0 EndAngle=3.14159
    g6: ArcOfCircle CenterX=-18 CenterY=7.5 CenterZ=0 NormalX=0 NormalY=0 NormalZ=1 AngleXU=0 Radius=1 StartAngle=3.14159 EndAngle=6.28319
    g7: LineSegment StartX=-19 StartY=9.5 StartZ=0 EndX=-19 EndY=7.5 EndZ=0
    g8: LineSegment StartX=-17 StartY=9.5 StartZ=0 EndX=-17 EndY=7.5 EndZ=0
  constraints (24):
    c: PointOnObject(g0,g-2)
    c: PointOnObject(g0,g-4)
    c: Horizontal(g0)
    c: DistanceY(g0,g-3) = 8.5
    c: Tangent(g1,g4) = 1.5708
    c: Tangent(g1,g3) = -1.5708
    c: Tangent(g3,g2) = -1.5708
    c: Tangent(g4,g2) = 1.5708
    c: Vertical(g3)
    c: Equal(g1,g2)
    c: Radius(g2) = 1
    c: DistanceY(g4,g4) = 2
    c: DistanceY(g0,g2) = 1
    c: DistanceX(g2,g0) = 3
    c: Tangent(g5,g8) = 1.5708
    c: Tangent(g5,g7) = -1.5708
    c: Tangent(g7,g6) = -1.5708
    c: Tangent(g8,g6) = 1.5708
    c: Vertical(g7)
    c: Equal(g5,g6)
    c: Equal(g5,g2)
    c: Equal(g8,g4)
    c: Horizontal(g5,g2)
    c: DistanceX(g0,g5) = 2
FEATURE [PartDesign::Pad] Pad122
  BaseFeature = -> Pad121
  Direction = (1,1,1)
  Length = 1
  Length2 = 100
  Placement = pos=(0,0,0) rot=(0.57735,0.57735,0.57735;2.0944rad)
  Profile = -> Sketch247
  Type = 0
FEATURE [PartDesign::Body] Body202  label="Corner005"
  Group = -> [Sketch242,Pad120,Sketch243,Pocket089,Sketch244,Pocket090,Sketch245,Pocket091,Sketch246,Pad121,Sketch247,Pad122]
  Origin = -> Origin277
  Tip = -> Pad122
FEATURE [App::Part] Part075  label="soporte90-006"
  Group = -> [Body202]
  Origin = -> Origin278
  Placement = pos=(320,1,170) rot=(0.707107,0.707107,0;3.14159rad)
FEATURE [Sketcher::SketchObject] Sketch248
  FullyConstrained = true
  MapMode = 5
  Placement = pos=(0,0,0) rot=(0.57735,0.57735,0.57735;2.0944rad)
  Support = -> [YZ_Plane273]
  sketch-geometry (5):
    g0: LineSegment StartX=0 StartY=0 StartZ=0 EndX=0 EndY=20 EndZ=0
    g1: LineSegment StartX=0 StartY=20 StartZ=0 EndX=-3 EndY=20 EndZ=0
    g2: LineSegment StartX=-3 StartY=20 StartZ=0 EndX=-20 EndY=3 EndZ=0
    g3: LineSegment StartX=-20 StartY=3 StartZ=0 EndX=-20 EndY=0 EndZ=0
    g4: LineSegment StartX=-20 StartY=0 StartZ=0 EndX=0 EndY=0 EndZ=0
  constraints (14):
    c: Coincident(g-1,g0)
    c: PointOnObject(g0,g-2)
    c: Coincident(g0,g1)
    c: Horizontal(g1)
    c: Coincident(g1,g2)
    c: Coincident(g2,g3)
    c: PointOnObject(g3,g-1)
    c: Vertical(g3)
    c: Coincident(g3,g4)
    c: Coincident(g4,g0)
    c: DistanceY(g0,g0) = 20
    c: DistanceY(g3,g3) = 3
    c: DistanceX(g1,g1) = 3
    c: DistanceX(g4,g4) = 20
FEATURE [PartDesign::Pad] Pad123
  Direction = (1,1,1)
  Length = 17
  Length2 = 100
  Placement = pos=(0,0,0) rot=(0.57735,0.57735,0.57735;2.0944rad)
  Profile = -> Sketch248
  Type = 0
FEATURE [Sketcher::SketchObject] Sketch249
  ExternalGeometry = -> [Pad123]
  FullyConstrained = true
  MapMode = 5
  Placement = pos=(-8.8e-15,-20,4.4e-15) rot=(-0.57735,-0.57735,0.57735;4.18879rad)
  Support = -> [Pad123]
  sketch-geometry (4):
    g0: LineSegment StartX=-3 StartY=2 StartZ=0 EndX=-20 EndY=2 EndZ=0
    g1: LineSegment StartX=-20 StartY=2 StartZ=0 EndX=-20 EndY=15 EndZ=0
    g2: LineSegment StartX=-20 StartY=15 StartZ=0 EndX=-3 EndY=15 EndZ=0
    g3: LineSegment StartX=-3 StartY=15 StartZ=0 EndX=-3 EndY=2 EndZ=0
  constraints (12):
    c: Coincident(g0,g1)
    c: Coincident(g1,g2)
    c: Coincident(g2,g3)
    c: Coincident(g3,g0)
    c: Horizontal(g0)
    c: Horizontal(g2)
    c: Vertical(g1)
    c: Vertical(g3)
    c: PointOnObject(g0,g-3)
    c: DistanceY(g1,g-6) = 2
    c: DistanceY(g-6,g0) = 2
    c: PointOnObject(g1,g-6)
FEATURE [PartDesign::Pocket] Pocket092
  BaseFeature = -> Pad123
  Length = 17
  Length2 = 100
  Placement = pos=(0,0,0) rot=(0.57735,0.57735,0.57735;2.0944rad)
  Profile = -> Sketch249
  Type = 0
FEATURE [Sketcher::SketchObject] Sketch250
  ExternalGeometry = -> [Pocket092]
  FullyConstrained = true
  MapMode = 5
  Placement = pos=(-1.7e-15,-3,6e-16) rot=(-0.57735,-0.57735,0.57735;4.18879rad)
  Support = -> [Pocket092]
  sketch-geometry (5):
    g0: LineSegment StartX=-20 StartY=8.5 StartZ=0 EndX=-3 EndY=8.5 EndZ=0
    g1: ArcOfCircle CenterX=-10 CenterY=8.5 CenterZ=0 NormalX=0 NormalY=0 NormalZ=1 AngleXU=0 Radius=3 StartAngle=4.71239 EndAngle=7.85398
    g2: ArcOfCircle CenterX=-13 CenterY=8.5 CenterZ=0 NormalX=0 NormalY=0 NormalZ=1 AngleXU=0 Radius=3 StartAngle=1.5708 EndAngle=4.71239
    g3: LineSegment StartX=-10 StartY=11.5 StartZ=0 EndX=-13 EndY=11.5 EndZ=0
    g4: LineSegment StartX=-10 StartY=5.5 StartZ=0 EndX=-13 EndY=5.5 EndZ=0
  constraints (14):
    c: PointOnObject(g0,g-6)
    c: PointOnObject(g0,g-4)
    c: Horizontal(g0)
    c: DistanceY(g0,g-4) = 6.5
    c: Tangent(g1,g4) = 1.5708
    c: Tangent(g1,g3) = -1.5708
    c: Tangent(g3,g2) = -1.5708
    c: Tangent(g4,g2) = 1.5708
    c: Horizontal(g3)
    c: Equal(g1,g2)
    c: PointOnObject(g1,g0)
    c: Radius(g1) = 3
    c: DistanceX(g3,g3) = 3
    c: DistanceX(g0,g2) = 7
FEATURE [PartDesign::Pocket] Pocket093
  BaseFeature = -> Pocket092
  Length = 5
  Length2 = 100
  Placement = pos=(0,0,0) rot=(0.57735,0.57735,0.57735;2.0944rad)
  Profile = -> Sketch250
  Type = 2
FEATURE [Sketcher::SketchObject] Sketch251
  ExternalGeometry = -> [Pocket093]
  FullyConstrained = true
  MapMode = 5
  Placement = pos=(-3e-16,1.2e-15,3) rot=(0,0,-1;1.5708rad)
  Support = -> [Pocket093]
  sketch-geometry (5):
    g0: LineSegment StartX=3 StartY=8.5 StartZ=0 EndX=20 EndY=8.5 EndZ=0
    g1: ArcOfCircle CenterX=10 CenterY=8.5 CenterZ=0 NormalX=0 NormalY=0 NormalZ=1 AngleXU=0 Radius=3 StartAngle=1.5708 EndAngle=4.71239
    g2: ArcOfCircle CenterX=13 CenterY=8.5 CenterZ=0 NormalX=0 NormalY=0 NormalZ=1 AngleXU=0 Radius=3 StartAngle=4.71239 EndAngle=7.85398
    g3: LineSegment StartX=10 StartY=5.5 StartZ=0 EndX=13 EndY=5.5 EndZ=0
    g4: LineSegment StartX=10 StartY=11.5 StartZ=0 EndX=13 EndY=11.5 EndZ=0
  constraints (14):
    c: PointOnObject(g0,g-4)
    c: PointOnObject(g0,g-5)
    c: Horizontal(g0)
    c: DistanceY(g0,g-4) = 6.5
    c: Tangent(g1,g4) = 1.5708
    c: Tangent(g1,g3) = -1.5708
    c: Tangent(g3,g2) = -1.5708
    c: Tangent(g4,g2) = 1.5708
    c: Horizontal(g3)
    c: Equal(g1,g2)
    c: PointOnObject(g1,g0)
    c: Radius(g2) = 3
    c: DistanceX(g4,g4) = 3
    c: DistanceX(g2,g0) = 7
FEATURE [PartDesign::Pocket] Pocket094
  BaseFeature = -> Pocket093
  Length = 5
  Length2 = 100
  Placement = pos=(0,0,0) rot=(0.57735,0.57735,0.57735;2.0944rad)
  Profile = -> Sketch251
  Type = 2
FEATURE [Sketcher::SketchObject] Sketch252
  ExternalGeometry = -> [Pocket094]
  FullyConstrained = true
  MapMode = 5
  Placement = pos=(0,0,0) rot=(0.57735,0.57735,0.57735;4.18879rad)
  Support = -> [Pocket094]
  sketch-geometry (9):
    g0: LineSegment StartX=0 StartY=8.5 StartZ=0 EndX=20 EndY=8.5 EndZ=0
    g1: ArcOfCircle CenterX=3 CenterY=9.5 CenterZ=0 NormalX=0 NormalY=0 NormalZ=1 AngleXU=0 Radius=1 StartAngle=0 EndAngle=3.14159
    g2: ArcOfCircle CenterX=3 CenterY=7.5 CenterZ=0 NormalX=0 NormalY=0 NormalZ=1 AngleXU=0 Radius=1 StartAngle=3.14159 EndAngle=6.28319
    g3: LineSegment StartX=2 StartY=9.5 StartZ=0 EndX=2 EndY=7.5 EndZ=0
    g4: LineSegment StartX=4 StartY=9.5 StartZ=0 EndX=4 EndY=7.5 EndZ=0
    g5: ArcOfCircle CenterX=18 CenterY=9.5 CenterZ=0 NormalX=0 NormalY=0 NormalZ=1 AngleXU=0 Radius=1 StartAngle=-9e-16 EndAngle=3.14159
    g6: ArcOfCircle CenterX=18 CenterY=7.5 CenterZ=0 NormalX=0 NormalY=0 NormalZ=1 AngleXU=0 Radius=1 StartAngle=3.14159 EndAngle=6.28319
    g7: LineSegment StartX=17 StartY=9.5 StartZ=0 EndX=17 EndY=7.5 EndZ=0
    g8: LineSegment StartX=19 StartY=9.5 StartZ=0 EndX=19 EndY=7.5 EndZ=0
  constraints (24):
    c: PointOnObject(g0,g-2)
    c: PointOnObject(g0,g-5)
    c: Horizontal(g0)
    c: DistanceY(g0,g-3) = 8.5
    c: Tangent(g1,g4) = 1.5708
    c: Tangent(g1,g3) = -1.5708
    c: Tangent(g3,g2) = -1.5708
    c: Tangent(g4,g2) = 1.5708
    c: Vertical(g3)
    c: Equal(g1,g2)
    c: Tangent(g5,g8) = 1.5708
    c: Tangent(g5,g7) = -1.5708
    c: Tangent(g7,g6) = -1.5708
    c: Tangent(g8,g6) = 1.5708
    c: Vertical(g7)
    c: Equal(g5,g6)
    c: Equal(g1,g5)
    c: Equal(g4,g7)
    c: DistanceY(g4,g4) = 2
    c: Radius(g1) = 1
    c: Horizontal(g5,g1)
    c: DistanceX(g0,g1) = 3
    c: DistanceX(g5,g0) = 2
    c: DistanceY(g0,g1) = 1
FEATURE [PartDesign::Pad] Pad124
  BaseFeature = -> Pocket094
  Direction = (1,1,1)
  Length = 1
  Length2 = 100
  Placement = pos=(0,0,0) rot=(0.57735,0.57735,0.57735;2.0944rad)
  Profile = -> Sketch252
  Type = 0
FEATURE [Sketcher::SketchObject] Sketch253
  ExternalGeometry = -> [Pad124]
  FullyConstrained = true
  MapMode = 5
  Placement = pos=(0,0,1e-16) rot=(0.707107,0.707107,0;3.14159rad)
  Support = -> [Pad124]
  sketch-geometry (9):
    g0: LineSegment StartX=0 StartY=8.5 StartZ=0 EndX=-20 EndY=8.5 EndZ=0
    g1: ArcOfCircle CenterX=-3 CenterY=7.5 CenterZ=0 NormalX=0 NormalY=0 NormalZ=1 AngleXU=0 Radius=1 StartAngle=3.14159 EndAngle=6.28319
    g2: ArcOfCircle CenterX=-3 CenterY=9.5 CenterZ=0 NormalX=0 NormalY=0 NormalZ=1 AngleXU=0 Radius=1 StartAngle=3e-16 EndAngle=3.14159
    g3: LineSegment StartX=-2 StartY=7.5 StartZ=0 EndX=-2 EndY=9.5 EndZ=0
    g4: LineSegment StartX=-4 StartY=7.5 StartZ=0 EndX=-4 EndY=9.5 EndZ=0
    g5: ArcOfCircle CenterX=-18 CenterY=9.5 CenterZ=0 NormalX=0 NormalY=0 NormalZ=1 AngleXU=0 Radius=1 StartAngle=0 EndAngle=3.14159
    g6: ArcOfCircle CenterX=-18 CenterY=7.5 CenterZ=0 NormalX=0 NormalY=0 NormalZ=1 AngleXU=0 Radius=1 StartAngle=3.14159 EndAngle=6.28319
    g7: LineSegment StartX=-19 StartY=9.5 StartZ=0 EndX=-19 EndY=7.5 EndZ=0
    g8: LineSegment StartX=-17 StartY=9.5 StartZ=0 EndX=-17 EndY=7.5 EndZ=0
  constraints (24):
    c: PointOnObject(g0,g-2)
    c: PointOnObject(g0,g-4)
    c: Horizontal(g0)
    c: DistanceY(g0,g-3) = 8.5
    c: Tangent(g1,g4) = 1.5708
    c: Tangent(g1,g3) = -1.5708
    c: Tangent(g3,g2) = -1.5708
    c: Tangent(g4,g2) = 1.5708
    c: Vertical(g3)
    c: Equal(g1,g2)
    c: Radius(g2) = 1
    c: DistanceY(g4,g4) = 2
    c: DistanceY(g0,g2) = 1
    c: DistanceX(g2,g0) = 3
    c: Tangent(g5,g8) = 1.5708
    c: Tangent(g5,g7) = -1.5708
    c: Tangent(g7,g6) = -1.5708
    c: Tangent(g8,g6) = 1.5708
    c: Vertical(g7)
    c: Equal(g5,g6)
    c: Equal(g5,g2)
    c: Equal(g8,g4)
    c: Horizontal(g5,g2)
    c: DistanceX(g0,g5) = 2
FEATURE [PartDesign::Pad] Pad125
  BaseFeature = -> Pad124
  Direction = (1,1,1)
  Length = 1
  Length2 = 100
  Placement = pos=(0,0,0) rot=(0.57735,0.57735,0.57735;2.0944rad)
  Profile = -> Sketch253
  Type = 0
FEATURE [PartDesign::Body] Body203  label="Corner006"
  Group = -> [Sketch248,Pad123,Sketch249,Pocket092,Sketch250,Pocket093,Sketch251,Pocket094,Sketch252,Pad124,Sketch253,Pad125]
  Origin = -> Origin279
  Tip = -> Pad125
FEATURE [App::Part] Part076  label="soporte90-007"
  Group = -> [Body203]
  Origin = -> Origin280
  Placement = pos=(320,19,20) rot=(0,0,1;-1.5708rad)
FEATURE [Sketcher::SketchObject] Sketch254
  FullyConstrained = true
  MapMode = 5
  Placement = pos=(0,0,0) rot=(0.57735,0.57735,0.57735;2.0944rad)
  Support = -> [YZ_Plane275]
  sketch-geometry (5):
    g0: LineSegment StartX=0 StartY=0 StartZ=0 EndX=0 EndY=20 EndZ=0
    g1: LineSegment StartX=0 StartY=20 StartZ=0 EndX=-3 EndY=20 EndZ=0
    g2: LineSegment StartX=-3 StartY=20 StartZ=0 EndX=-20 EndY=3 EndZ=0
    g3: LineSegment StartX=-20 StartY=3 StartZ=0 EndX=-20 EndY=0 EndZ=0
    g4: LineSegment StartX=-20 StartY=0 StartZ=0 EndX=0 EndY=0 EndZ=0
  constraints (14):
    c: Coincident(g-1,g0)
    c: PointOnObject(g0,g-2)
    c: Coincident(g0,g1)
    c: Horizontal(g1)
    c: Coincident(g1,g2)
    c: Coincident(g2,g3)
    c: PointOnObject(g3,g-1)
    c: Vertical(g3)
    c: Coincident(g3,g4)
    c: Coincident(g4,g0)
    c: DistanceY(g0,g0) = 20
    c: DistanceY(g3,g3) = 3
    c: DistanceX(g1,g1) = 3
    c: DistanceX(g4,g4) = 20
FEATURE [PartDesign::Pad] Pad126
  Direction = (1,1,1)
  Length = 17
  Length2 = 100
  Placement = pos=(0,0,0) rot=(0.57735,0.57735,0.57735;2.0944rad)
  Profile = -> Sketch254
  Type = 0
FEATURE [Sketcher::SketchObject] Sketch255
  ExternalGeometry = -> [Pad126]
  FullyConstrained = true
  MapMode = 5
  Placement = pos=(-8.8e-15,-20,4.4e-15) rot=(-0.57735,-0.57735,0.57735;4.18879rad)
  Support = -> [Pad126]
  sketch-geometry (4):
    g0: LineSegment StartX=-3 StartY=2 StartZ=0 EndX=-20 EndY=2 EndZ=0
    g1: LineSegment StartX=-20 StartY=2 StartZ=0 EndX=-20 EndY=15 EndZ=0
    g2: LineSegment StartX=-20 StartY=15 StartZ=0 EndX=-3 EndY=15 EndZ=0
    g3: LineSegment StartX=-3 StartY=15 StartZ=0 EndX=-3 EndY=2 EndZ=0
  constraints (12):
    c: Coincident(g0,g1)
    c: Coincident(g1,g2)
    c: Coincident(g2,g3)
    c: Coincident(g3,g0)
    c: Horizontal(g0)
    c: Horizontal(g2)
    c: Vertical(g1)
    c: Vertical(g3)
    c: PointOnObject(g0,g-3)
    c: DistanceY(g1,g-6) = 2
    c: DistanceY(g-6,g0) = 2
    c: PointOnObject(g1,g-6)
FEATURE [PartDesign::Pocket] Pocket095
  BaseFeature = -> Pad126
  Length = 17
  Length2 = 100
  Placement = pos=(0,0,0) rot=(0.57735,0.57735,0.57735;2.0944rad)
  Profile = -> Sketch255
  Type = 0
FEATURE [Sketcher::SketchObject] Sketch256
  ExternalGeometry = -> [Pocket095]
  FullyConstrained = true
  MapMode = 5
  Placement = pos=(-1.7e-15,-3,6e-16) rot=(-0.57735,-0.57735,0.57735;4.18879rad)
  Support = -> [Pocket095]
  sketch-geometry (5):
    g0: LineSegment StartX=-20 StartY=8.5 StartZ=0 EndX=-3 EndY=8.5 EndZ=0
    g1: ArcOfCircle CenterX=-10 CenterY=8.5 CenterZ=0 NormalX=0 NormalY=0 NormalZ=1 AngleXU=0 Radius=3 StartAngle=4.71239 EndAngle=7.85398
    g2: ArcOfCircle CenterX=-13 CenterY=8.5 CenterZ=0 NormalX=0 NormalY=0 NormalZ=1 AngleXU=0 Radius=3 StartAngle=1.5708 EndAngle=4.71239
    g3: LineSegment StartX=-10 StartY=11.5 StartZ=0 EndX=-13 EndY=11.5 EndZ=0
    g4: LineSegment StartX=-10 StartY=5.5 StartZ=0 EndX=-13 EndY=5.5 EndZ=0
  constraints (14):
    c: PointOnObject(g0,g-6)
    c: PointOnObject(g0,g-4)
    c: Horizontal(g0)
    c: DistanceY(g0,g-4) = 6.5
    c: Tangent(g1,g4) = 1.5708
    c: Tangent(g1,g3) = -1.5708
    c: Tangent(g3,g2) = -1.5708
    c: Tangent(g4,g2) = 1.5708
    c: Horizontal(g3)
    c: Equal(g1,g2)
    c: PointOnObject(g1,g0)
    c: Radius(g1) = 3
    c: DistanceX(g3,g3) = 3
    c: DistanceX(g0,g2) = 7
FEATURE [PartDesign::Pocket] Pocket096
  BaseFeature = -> Pocket095
  Length = 5
  Length2 = 100
  Placement = pos=(0,0,0) rot=(0.57735,0.57735,0.57735;2.0944rad)
  Profile = -> Sketch256
  Type = 2
FEATURE [Sketcher::SketchObject] Sketch257
  ExternalGeometry = -> [Pocket096]
  FullyConstrained = true
  MapMode = 5
  Placement = pos=(-3e-16,1.2e-15,3) rot=(0,0,-1;1.5708rad)
  Support = -> [Pocket096]
  sketch-geometry (5):
    g0: LineSegment StartX=3 StartY=8.5 StartZ=0 EndX=20 EndY=8.5 EndZ=0
    g1: ArcOfCircle CenterX=10 CenterY=8.5 CenterZ=0 NormalX=0 NormalY=0 NormalZ=1 AngleXU=0 Radius=3 StartAngle=1.5708 EndAngle=4.71239
    g2: ArcOfCircle CenterX=13 CenterY=8.5 CenterZ=0 NormalX=0 NormalY=0 NormalZ=1 AngleXU=0 Radius=3 StartAngle=4.71239 EndAngle=7.85398
    g3: LineSegment StartX=10 StartY=5.5 StartZ=0 EndX=13 EndY=5.5 EndZ=0
    g4: LineSegment StartX=10 StartY=11.5 StartZ=0 EndX=13 EndY=11.5 EndZ=0
  constraints (14):
    c: PointOnObject(g0,g-4)
    c: PointOnObject(g0,g-5)
    c: Horizontal(g0)
    c: DistanceY(g0,g-4) = 6.5
    c: Tangent(g1,g4) = 1.5708
    c: Tangent(g1,g3) = -1.5708
    c: Tangent(g3,g2) = -1.5708
    c: Tangent(g4,g2) = 1.5708
    c: Horizontal(g3)
    c: Equal(g1,g2)
    c: PointOnObject(g1,g0)
    c: Radius(g2) = 3
    c: DistanceX(g4,g4) = 3
    c: DistanceX(g2,g0) = 7
FEATURE [PartDesign::Pocket] Pocket097
  BaseFeature = -> Pocket096
  Length = 5
  Length2 = 100
  Placement = pos=(0,0,0) rot=(0.57735,0.57735,0.57735;2.0944rad)
  Profile = -> Sketch257
  Type = 2
FEATURE [Sketcher::SketchObject] Sketch258
  ExternalGeometry = -> [Pocket097]
  FullyConstrained = true
  MapMode = 5
  Placement = pos=(0,0,0) rot=(0.57735,0.57735,0.57735;4.18879rad)
  Support = -> [Pocket097]
  sketch-geometry (9):
    g0: LineSegment StartX=0 StartY=8.5 StartZ=0 EndX=20 EndY=8.5 EndZ=0
    g1: ArcOfCircle CenterX=3 CenterY=9.5 CenterZ=0 NormalX=0 NormalY=0 NormalZ=1 AngleXU=0 Radius=1 StartAngle=0 EndAngle=3.14159
    g2: ArcOfCircle CenterX=3 CenterY=7.5 CenterZ=0 NormalX=0 NormalY=0 NormalZ=1 AngleXU=0 Radius=1 StartAngle=3.14159 EndAngle=6.28319
    g3: LineSegment StartX=2 StartY=9.5 StartZ=0 EndX=2 EndY=7.5 EndZ=0
    g4: LineSegment StartX=4 StartY=9.5 StartZ=0 EndX=4 EndY=7.5 EndZ=0
    g5: ArcOfCircle CenterX=18 CenterY=9.5 CenterZ=0 NormalX=0 NormalY=0 NormalZ=1 AngleXU=0 Radius=1 StartAngle=-9e-16 EndAngle=3.14159
    g6: ArcOfCircle CenterX=18 CenterY=7.5 CenterZ=0 NormalX=0 NormalY=0 NormalZ=1 AngleXU=0 Radius=1 StartAngle=3.14159 EndAngle=6.28319
    g7: LineSegment StartX=17 StartY=9.5 StartZ=0 EndX=17 EndY=7.5 EndZ=0
    g8: LineSegment StartX=19 StartY=9.5 StartZ=0 EndX=19 EndY=7.5 EndZ=0
  constraints (24):
    c: PointOnObject(g0,g-2)
    c: PointOnObject(g0,g-5)
    c: Horizontal(g0)
    c: DistanceY(g0,g-3) = 8.5
    c: Tangent(g1,g4) = 1.5708
    c: Tangent(g1,g3) = -1.5708
    c: Tangent(g3,g2) = -1.5708
    c: Tangent(g4,g2) = 1.5708
    c: Vertical(g3)
    c: Equal(g1,g2)
    c: Tangent(g5,g8) = 1.5708
    c: Tangent(g5,g7) = -1.5708
    c: Tangent(g7,g6) = -1.5708
    c: Tangent(g8,g6) = 1.5708
    c: Vertical(g7)
    c: Equal(g5,g6)
    c: Equal(g1,g5)
    c: Equal(g4,g7)
    c: DistanceY(g4,g4) = 2
    c: Radius(g1) = 1
    c: Horizontal(g5,g1)
    c: DistanceX(g0,g1) = 3
    c: DistanceX(g5,g0) = 2
    c: DistanceY(g0,g1) = 1
FEATURE [PartDesign::Pad] Pad127
  BaseFeature = -> Pocket097
  Direction = (1,1,1)
  Length = 1
  Length2 = 100
  Placement = pos=(0,0,0) rot=(0.57735,0.57735,0.57735;2.0944rad)
  Profile = -> Sketch258
  Type = 0
FEATURE [Sketcher::SketchObject] Sketch259
  ExternalGeometry = -> [Pad127]
  FullyConstrained = true
  MapMode = 5
  Placement = pos=(0,0,1e-16) rot=(0.707107,0.707107,0;3.14159rad)
  Support = -> [Pad127]
  sketch-geometry (9):
    g0: LineSegment StartX=0 StartY=8.5 StartZ=0 EndX=-20 EndY=8.5 EndZ=0
    g1: ArcOfCircle CenterX=-3 CenterY=7.5 CenterZ=0 NormalX=0 NormalY=0 NormalZ=1 AngleXU=0 Radius=1 StartAngle=3.14159 EndAngle=6.28319
    g2: ArcOfCircle CenterX=-3 CenterY=9.5 CenterZ=0 NormalX=0 NormalY=0 NormalZ=1 AngleXU=0 Radius=1 StartAngle=3e-16 EndAngle=3.14159
    g3: LineSegment StartX=-2 StartY=7.5 StartZ=0 EndX=-2 EndY=9.5 EndZ=0
    g4: LineSegment StartX=-4 StartY=7.5 StartZ=0 EndX=-4 EndY=9.5 EndZ=0
    g5: ArcOfCircle CenterX=-18 CenterY=9.5 CenterZ=0 NormalX=0 NormalY=0 NormalZ=1 AngleXU=0 Radius=1 StartAngle=0 EndAngle=3.14159
    g6: ArcOfCircle CenterX=-18 CenterY=7.5 CenterZ=0 NormalX=0 NormalY=0 NormalZ=1 AngleXU=0 Radius=1 StartAngle=3.14159 EndAngle=6.28319
    g7: LineSegment StartX=-19 StartY=9.5 StartZ=0 EndX=-19 EndY=7.5 EndZ=0
    g8: LineSegment StartX=-17 StartY=9.5 StartZ=0 EndX=-17 EndY=7.5 EndZ=0
  constraints (24):
    c: PointOnObject(g0,g-2)
    c: PointOnObject(g0,g-4)
    c: Horizontal(g0)
    c: DistanceY(g0,g-3) = 8.5
    c: Tangent(g1,g4) = 1.5708
    c: Tangent(g1,g3) = -1.5708
    c: Tangent(g3,g2) = -1.5708
    c: Tangent(g4,g2) = 1.5708
    c: Vertical(g3)
    c: Equal(g1,g2)
    c: Radius(g2) = 1
    c: DistanceY(g4,g4) = 2
    c: DistanceY(g0,g2) = 1
    c: DistanceX(g2,g0) = 3
    c: Tangent(g5,g8) = 1.5708
    c: Tangent(g5,g7) = -1.5708
    c: Tangent(g7,g6) = -1.5708
    c: Tangent(g8,g6) = 1.5708
    c: Vertical(g7)
    c: Equal(g5,g6)
    c: Equal(g5,g2)
    c: Equal(g8,g4)
    c: Horizontal(g5,g2)
    c: DistanceX(g0,g5) = 2
FEATURE [PartDesign::Pad] Pad128
  BaseFeature = -> Pad127
  Direction = (1,1,1)
  Length = 1
  Length2 = 100
  Placement = pos=(0,0,0) rot=(0.57735,0.57735,0.57735;2.0944rad)
  Profile = -> Sketch259
  Type = 0
FEATURE [PartDesign::Body] Body204  label="Corner007"
  Group = -> [Sketch254,Pad126,Sketch255,Pocket095,Sketch256,Pocket096,Sketch257,Pocket097,Sketch258,Pad127,Sketch259,Pad128]
  Origin = -> Origin281
  Tip = -> Pad128
FEATURE [App::Part] Part077  label="soporte90-008"
  Group = -> [Body204]
  Origin = -> Origin282
  Placement = pos=(320,321,170) rot=(0.707107,0.707107,0;3.14159rad)
FEATURE [Sketcher::SketchObject] Sketch260
  FullyConstrained = true
  MapMode = 5
  Placement = pos=(0,0,0) rot=(0.57735,0.57735,0.57735;2.0944rad)
  Support = -> [YZ_Plane277]
  sketch-geometry (5):
    g0: LineSegment StartX=0 StartY=0 StartZ=0 EndX=0 EndY=20 EndZ=0
    g1: LineSegment StartX=0 StartY=20 StartZ=0 EndX=-3 EndY=20 EndZ=0
    g2: LineSegment StartX=-3 StartY=20 StartZ=0 EndX=-20 EndY=3 EndZ=0
    g3: LineSegment StartX=-20 StartY=3 StartZ=0 EndX=-20 EndY=0 EndZ=0
    g4: LineSegment StartX=-20 StartY=0 StartZ=0 EndX=0 EndY=0 EndZ=0
  constraints (14):
    c: Coincident(g-1,g0)
    c: PointOnObject(g0,g-2)
    c: Coincident(g0,g1)
    c: Horizontal(g1)
    c: Coincident(g1,g2)
    c: Coincident(g2,g3)
    c: PointOnObject(g3,g-1)
    c: Vertical(g3)
    c: Coincident(g3,g4)
    c: Coincident(g4,g0)
    c: DistanceY(g0,g0) = 20
    c: DistanceY(g3,g3) = 3
    c: DistanceX(g1,g1) = 3
    c: DistanceX(g4,g4) = 20
FEATURE [PartDesign::Pad] Pad129
  Direction = (1,1,1)
  Length = 17
  Length2 = 100
  Placement = pos=(0,0,0) rot=(0.57735,0.57735,0.57735;2.0944rad)
  Profile = -> Sketch260
  Type = 0
FEATURE [Sketcher::SketchObject] Sketch261
  ExternalGeometry = -> [Pad129]
  FullyConstrained = true
  MapMode = 5
  Placement = pos=(-8.8e-15,-20,4.4e-15) rot=(-0.57735,-0.57735,0.57735;4.18879rad)
  Support = -> [Pad129]
  sketch-geometry (4):
    g0: LineSegment StartX=-3 StartY=2 StartZ=0 EndX=-20 EndY=2 EndZ=0
    g1: LineSegment StartX=-20 StartY=2 StartZ=0 EndX=-20 EndY=15 EndZ=0
    g2: LineSegment StartX=-20 StartY=15 StartZ=0 EndX=-3 EndY=15 EndZ=0
    g3: LineSegment StartX=-3 StartY=15 StartZ=0 EndX=-3 EndY=2 EndZ=0
  constraints (12):
    c: Coincident(g0,g1)
    c: Coincident(g1,g2)
    c: Coincident(g2,g3)
    c: Coincident(g3,g0)
    c: Horizontal(g0)
    c: Horizontal(g2)
    c: Vertical(g1)
    c: Vertical(g3)
    c: PointOnObject(g0,g-3)
    c: DistanceY(g1,g-6) = 2
    c: DistanceY(g-6,g0) = 2
    c: PointOnObject(g1,g-6)
FEATURE [PartDesign::Pocket] Pocket098
  BaseFeature = -> Pad129
  Length = 17
  Length2 = 100
  Placement = pos=(0,0,0) rot=(0.57735,0.57735,0.57735;2.0944rad)
  Profile = -> Sketch261
  Type = 0
FEATURE [Sketcher::SketchObject] Sketch262
  ExternalGeometry = -> [Pocket098]
  FullyConstrained = true
  MapMode = 5
  Placement = pos=(-1.7e-15,-3,6e-16) rot=(-0.57735,-0.57735,0.57735;4.18879rad)
  Support = -> [Pocket098]
  sketch-geometry (5):
    g0: LineSegment StartX=-20 StartY=8.5 StartZ=0 EndX=-3 EndY=8.5 EndZ=0
    g1: ArcOfCircle CenterX=-10 CenterY=8.5 CenterZ=0 NormalX=0 NormalY=0 NormalZ=1 AngleXU=0 Radius=3 StartAngle=4.71239 EndAngle=7.85398
    g2: ArcOfCircle CenterX=-13 CenterY=8.5 CenterZ=0 NormalX=0 NormalY=0 NormalZ=1 AngleXU=0 Radius=3 StartAngle=1.5708 EndAngle=4.71239
    g3: LineSegment StartX=-10 StartY=11.5 StartZ=0 EndX=-13 EndY=11.5 EndZ=0
    g4: LineSegment StartX=-10 StartY=5.5 StartZ=0 EndX=-13 EndY=5.5 EndZ=0
  constraints (14):
    c: PointOnObject(g0,g-6)
    c: PointOnObject(g0,g-4)
    c: Horizontal(g0)
    c: DistanceY(g0,g-4) = 6.5
    c: Tangent(g1,g4) = 1.5708
    c: Tangent(g1,g3) = -1.5708
    c: Tangent(g3,g2) = -1.5708
    c: Tangent(g4,g2) = 1.5708
    c: Horizontal(g3)
    c: Equal(g1,g2)
    c: PointOnObject(g1,g0)
    c: Radius(g1) = 3
    c: DistanceX(g3,g3) = 3
    c: DistanceX(g0,g2) = 7
FEATURE [PartDesign::Pocket] Pocket099
  BaseFeature = -> Pocket098
  Length = 5
  Length2 = 100
  Placement = pos=(0,0,0) rot=(0.57735,0.57735,0.57735;2.0944rad)
  Profile = -> Sketch262
  Type = 2
FEATURE [Sketcher::SketchObject] Sketch263
  ExternalGeometry = -> [Pocket099]
  FullyConstrained = true
  MapMode = 5
  Placement = pos=(-3e-16,1.2e-15,3) rot=(0,0,-1;1.5708rad)
  Support = -> [Pocket099]
  sketch-geometry (5):
    g0: LineSegment StartX=3 StartY=8.5 StartZ=0 EndX=20 EndY=8.5 EndZ=0
    g1: ArcOfCircle CenterX=10 CenterY=8.5 CenterZ=0 NormalX=0 NormalY=0 NormalZ=1 AngleXU=0 Radius=3 StartAngle=1.5708 EndAngle=4.71239
    g2: ArcOfCircle CenterX=13 CenterY=8.5 CenterZ=0 NormalX=0 NormalY=0 NormalZ=1 AngleXU=0 Radius=3 StartAngle=4.71239 EndAngle=7.85398
    g3: LineSegment StartX=10 StartY=5.5 StartZ=0 EndX=13 EndY=5.5 EndZ=0
    g4: LineSegment StartX=10 StartY=11.5 StartZ=0 EndX=13 EndY=11.5 EndZ=0
  constraints (14):
    c: PointOnObject(g0,g-4)
    c: PointOnObject(g0,g-5)
    c: Horizontal(g0)
    c: DistanceY(g0,g-4) = 6.5
    c: Tangent(g1,g4) = 1.5708
    c: Tangent(g1,g3) = -1.5708
    c: Tangent(g3,g2) = -1.5708
    c: Tangent(g4,g2) = 1.5708
    c: Horizontal(g3)
    c: Equal(g1,g2)
    c: PointOnObject(g1,g0)
    c: Radius(g2) = 3
    c: DistanceX(g4,g4) = 3
    c: DistanceX(g2,g0) = 7
FEATURE [PartDesign::Pocket] Pocket100
  BaseFeature = -> Pocket099
  Length = 5
  Length2 = 100
  Placement = pos=(0,0,0) rot=(0.57735,0.57735,0.57735;2.0944rad)
  Profile = -> Sketch263
  Type = 2
FEATURE [Sketcher::SketchObject] Sketch264
  ExternalGeometry = -> [Pocket100]
  FullyConstrained = true
  MapMode = 5
  Placement = pos=(0,0,0) rot=(0.57735,0.57735,0.57735;4.18879rad)
  Support = -> [Pocket100]
  sketch-geometry (9):
    g0: LineSegment StartX=0 StartY=8.5 StartZ=0 EndX=20 EndY=8.5 EndZ=0
    g1: ArcOfCircle CenterX=3 CenterY=9.5 CenterZ=0 NormalX=0 NormalY=0 NormalZ=1 AngleXU=0 Radius=1 StartAngle=0 EndAngle=3.14159
    g2: ArcOfCircle CenterX=3 CenterY=7.5 CenterZ=0 NormalX=0 NormalY=0 NormalZ=1 AngleXU=0 Radius=1 StartAngle=3.14159 EndAngle=6.28319
    g3: LineSegment StartX=2 StartY=9.5 StartZ=0 EndX=2 EndY=7.5 EndZ=0
    g4: LineSegment StartX=4 StartY=9.5 StartZ=0 EndX=4 EndY=7.5 EndZ=0
    g5: ArcOfCircle CenterX=18 CenterY=9.5 CenterZ=0 NormalX=0 NormalY=0 NormalZ=1 AngleXU=0 Radius=1 StartAngle=-9e-16 EndAngle=3.14159
    g6: ArcOfCircle CenterX=18 CenterY=7.5 CenterZ=0 NormalX=0 NormalY=0 NormalZ=1 AngleXU=0 Radius=1 StartAngle=3.14159 EndAngle=6.28319
    g7: LineSegment StartX=17 StartY=9.5 StartZ=0 EndX=17 EndY=7.5 EndZ=0
    g8: LineSegment StartX=19 StartY=9.5 StartZ=0 EndX=19 EndY=7.5 EndZ=0
  constraints (24):
    c: PointOnObject(g0,g-2)
    c: PointOnObject(g0,g-5)
    c: Horizontal(g0)
    c: DistanceY(g0,g-3) = 8.5
    c: Tangent(g1,g4) = 1.5708
    c: Tangent(g1,g3) = -1.5708
    c: Tangent(g3,g2) = -1.5708
    c: Tangent(g4,g2) = 1.5708
    c: Vertical(g3)
    c: Equal(g1,g2)
    c: Tangent(g5,g8) = 1.5708
    c: Tangent(g5,g7) = -1.5708
    c: Tangent(g7,g6) = -1.5708
    c: Tangent(g8,g6) = 1.5708
    c: Vertical(g7)
    c: Equal(g5,g6)
    c: Equal(g1,g5)
    c: Equal(g4,g7)
    c: DistanceY(g4,g4) = 2
    c: Radius(g1) = 1
    c: Horizontal(g5,g1)
    c: DistanceX(g0,g1) = 3
    c: DistanceX(g5,g0) = 2
    c: DistanceY(g0,g1) = 1
FEATURE [PartDesign::Pad] Pad130
  BaseFeature = -> Pocket100
  Direction = (1,1,1)
  Length = 1
  Length2 = 100
  Placement = pos=(0,0,0) rot=(0.57735,0.57735,0.57735;2.0944rad)
  Profile = -> Sketch264
  Type = 0
FEATURE [Sketcher::SketchObject] Sketch265
  ExternalGeometry = -> [Pad130]
  FullyConstrained = true
  MapMode = 5
  Placement = pos=(0,0,1e-16) rot=(0.707107,0.707107,0;3.14159rad)
  Support = -> [Pad130]
  sketch-geometry (9):
    g0: LineSegment StartX=0 StartY=8.5 StartZ=0 EndX=-20 EndY=8.5 EndZ=0
    g1: ArcOfCircle CenterX=-3 CenterY=7.5 CenterZ=0 NormalX=0 NormalY=0 NormalZ=1 AngleXU=0 Radius=1 StartAngle=3.14159 EndAngle=6.28319
    g2: ArcOfCircle CenterX=-3 CenterY=9.5 CenterZ=0 NormalX=0 NormalY=0 NormalZ=1 AngleXU=0 Radius=1 StartAngle=3e-16 EndAngle=3.14159
    g3: LineSegment StartX=-2 StartY=7.5 StartZ=0 EndX=-2 EndY=9.5 EndZ=0
    g4: LineSegment StartX=-4 StartY=7.5 StartZ=0 EndX=-4 EndY=9.5 EndZ=0
    g5: ArcOfCircle CenterX=-18 CenterY=9.5 CenterZ=0 NormalX=0 NormalY=0 NormalZ=1 AngleXU=0 Radius=1 StartAngle=0 EndAngle=3.14159
    g6: ArcOfCircle CenterX=-18 CenterY=7.5 CenterZ=0 NormalX=0 NormalY=0 NormalZ=1 AngleXU=0 Radius=1 StartAngle=3.14159 EndAngle=6.28319
    g7: LineSegment StartX=-19 StartY=9.5 StartZ=0 EndX=-19 EndY=7.5 EndZ=0
    g8: LineSegment StartX=-17 StartY=9.5 StartZ=0 EndX=-17 EndY=7.5 EndZ=0
  constraints (24):
    c: PointOnObject(g0,g-2)
    c: PointOnObject(g0,g-4)
    c: Horizontal(g0)
    c: DistanceY(g0,g-3) = 8.5
    c: Tangent(g1,g4) = 1.5708
    c: Tangent(g1,g3) = -1.5708
    c: Tangent(g3,g2) = -1.5708
    c: Tangent(g4,g2) = 1.5708
    c: Vertical(g3)
    c: Equal(g1,g2)
    c: Radius(g2) = 1
    c: DistanceY(g4,g4) = 2
    c: DistanceY(g0,g2) = 1
    c: DistanceX(g2,g0) = 3
    c: Tangent(g5,g8) = 1.5708
    c: Tangent(g5,g7) = -1.5708
    c: Tangent(g7,g6) = -1.5708
    c: Tangent(g8,g6) = 1.5708
    c: Vertical(g7)
    c: Equal(g5,g6)
    c: Equal(g5,g2)
    c: Equal(g8,g4)
    c: Horizontal(g5,g2)
    c: DistanceX(g0,g5) = 2
FEATURE [PartDesign::Pad] Pad131
  BaseFeature = -> Pad130
  Direction = (1,1,1)
  Length = 1
  Length2 = 100
  Placement = pos=(0,0,0) rot=(0.57735,0.57735,0.57735;2.0944rad)
  Profile = -> Sketch265
  Type = 0
FEATURE [PartDesign::Body] Body205  label="Corner008"
  Group = -> [Sketch260,Pad129,Sketch261,Pocket098,Sketch262,Pocket099,Sketch263,Pocket100,Sketch264,Pad130,Sketch265,Pad131]
  Origin = -> Origin283
  Tip = -> Pad131
FEATURE [App::Part] Part078  label="soporte90-009"
  Group = -> [Body205]
  Origin = -> Origin284
  Placement = pos=(3,20,70) rot=(1,0,0;3.14159rad)
FEATURE [Sketcher::SketchObject] Sketch266
  FullyConstrained = true
  MapMode = 5
  Placement = pos=(0,0,0) rot=(0.57735,0.57735,0.57735;2.0944rad)
  Support = -> [YZ_Plane279]
  sketch-geometry (5):
    g0: LineSegment StartX=0 StartY=0 StartZ=0 EndX=0 EndY=20 EndZ=0
    g1: LineSegment StartX=0 StartY=20 StartZ=0 EndX=-3 EndY=20 EndZ=0
    g2: LineSegment StartX=-3 StartY=20 StartZ=0 EndX=-20 EndY=3 EndZ=0
    g3: LineSegment StartX=-20 StartY=3 StartZ=0 EndX=-20 EndY=0 EndZ=0
    g4: LineSegment StartX=-20 StartY=0 StartZ=0 EndX=0 EndY=0 EndZ=0
  constraints (14):
    c: Coincident(g-1,g0)
    c: PointOnObject(g0,g-2)
    c: Coincident(g0,g1)
    c: Horizontal(g1)
    c: Coincident(g1,g2)
    c: Coincident(g2,g3)
    c: PointOnObject(g3,g-1)
    c: Vertical(g3)
    c: Coincident(g3,g4)
    c: Coincident(g4,g0)
    c: DistanceY(g0,g0) = 20
    c: DistanceY(g3,g3) = 3
    c: DistanceX(g1,g1) = 3
    c: DistanceX(g4,g4) = 20
FEATURE [PartDesign::Pad] Pad132
  Direction = (1,1,1)
  Length = 17
  Length2 = 100
  Placement = pos=(0,0,0) rot=(0.57735,0.57735,0.57735;2.0944rad)
  Profile = -> Sketch266
  Type = 0
FEATURE [Sketcher::SketchObject] Sketch267
  ExternalGeometry = -> [Pad132]
  FullyConstrained = true
  MapMode = 5
  Placement = pos=(-8.8e-15,-20,4.4e-15) rot=(-0.57735,-0.57735,0.57735;4.18879rad)
  Support = -> [Pad132]
  sketch-geometry (4):
    g0: LineSegment StartX=-3 StartY=2 StartZ=0 EndX=-20 EndY=2 EndZ=0
    g1: LineSegment StartX=-20 StartY=2 StartZ=0 EndX=-20 EndY=15 EndZ=0
    g2: LineSegment StartX=-20 StartY=15 StartZ=0 EndX=-3 EndY=15 EndZ=0
    g3: LineSegment StartX=-3 StartY=15 StartZ=0 EndX=-3 EndY=2 EndZ=0
  constraints (12):
    c: Coincident(g0,g1)
    c: Coincident(g1,g2)
    c: Coincident(g2,g3)
    c: Coincident(g3,g0)
    c: Horizontal(g0)
    c: Horizontal(g2)
    c: Vertical(g1)
    c: Vertical(g3)
    c: PointOnObject(g0,g-3)
    c: DistanceY(g1,g-6) = 2
    c: DistanceY(g-6,g0) = 2
    c: PointOnObject(g1,g-6)
FEATURE [PartDesign::Pocket] Pocket101
  BaseFeature = -> Pad132
  Length = 17
  Length2 = 100
  Placement = pos=(0,0,0) rot=(0.57735,0.57735,0.57735;2.0944rad)
  Profile = -> Sketch267
  Type = 0
FEATURE [Sketcher::SketchObject] Sketch268
  ExternalGeometry = -> [Pocket101]
  FullyConstrained = true
  MapMode = 5
  Placement = pos=(-1.7e-15,-3,6e-16) rot=(-0.57735,-0.57735,0.57735;4.18879rad)
  Support = -> [Pocket101]
  sketch-geometry (5):
    g0: LineSegment StartX=-20 StartY=8.5 StartZ=0 EndX=-3 EndY=8.5 EndZ=0
    g1: ArcOfCircle CenterX=-10 CenterY=8.5 CenterZ=0 NormalX=0 NormalY=0 NormalZ=1 AngleXU=0 Radius=3 StartAngle=4.71239 EndAngle=7.85398
    g2: ArcOfCircle CenterX=-13 CenterY=8.5 CenterZ=0 NormalX=0 NormalY=0 NormalZ=1 AngleXU=0 Radius=3 StartAngle=1.5708 EndAngle=4.71239
    g3: LineSegment StartX=-10 StartY=11.5 StartZ=0 EndX=-13 EndY=11.5 EndZ=0
    g4: LineSegment StartX=-10 StartY=5.5 StartZ=0 EndX=-13 EndY=5.5 EndZ=0
  constraints (14):
    c: PointOnObject(g0,g-6)
    c: PointOnObject(g0,g-4)
    c: Horizontal(g0)
    c: DistanceY(g0,g-4) = 6.5
    c: Tangent(g1,g4) = 1.5708
    c: Tangent(g1,g3) = -1.5708
    c: Tangent(g3,g2) = -1.5708
    c: Tangent(g4,g2) = 1.5708
    c: Horizontal(g3)
    c: Equal(g1,g2)
    c: PointOnObject(g1,g0)
    c: Radius(g1) = 3
    c: DistanceX(g3,g3) = 3
    c: DistanceX(g0,g2) = 7
FEATURE [PartDesign::Pocket] Pocket102
  BaseFeature = -> Pocket101
  Length = 5
  Length2 = 100
  Placement = pos=(0,0,0) rot=(0.57735,0.57735,0.57735;2.0944rad)
  Profile = -> Sketch268
  Type = 2
FEATURE [Sketcher::SketchObject] Sketch269
  ExternalGeometry = -> [Pocket102]
  FullyConstrained = true
  MapMode = 5
  Placement = pos=(-3e-16,1.2e-15,3) rot=(0,0,-1;1.5708rad)
  Support = -> [Pocket102]
  sketch-geometry (5):
    g0: LineSegment StartX=3 StartY=8.5 StartZ=0 EndX=20 EndY=8.5 EndZ=0
    g1: ArcOfCircle CenterX=10 CenterY=8.5 CenterZ=0 NormalX=0 NormalY=0 NormalZ=1 AngleXU=0 Radius=3 StartAngle=1.5708 EndAngle=4.71239
    g2: ArcOfCircle CenterX=13 CenterY=8.5 CenterZ=0 NormalX=0 NormalY=0 NormalZ=1 AngleXU=0 Radius=3 StartAngle=4.71239 EndAngle=7.85398
    g3: LineSegment StartX=10 StartY=5.5 StartZ=0 EndX=13 EndY=5.5 EndZ=0
    g4: LineSegment StartX=10 StartY=11.5 StartZ=0 EndX=13 EndY=11.5 EndZ=0
  constraints (14):
    c: PointOnObject(g0,g-4)
    c: PointOnObject(g0,g-5)
    c: Horizontal(g0)
    c: DistanceY(g0,g-4) = 6.5
    c: Tangent(g1,g4) = 1.5708
    c: Tangent(g1,g3) = -1.5708
    c: Tangent(g3,g2) = -1.5708
    c: Tangent(g4,g2) = 1.5708
    c: Horizontal(g3)
    c: Equal(g1,g2)
    c: PointOnObject(g1,g0)
    c: Radius(g2) = 3
    c: DistanceX(g4,g4) = 3
    c: DistanceX(g2,g0) = 7
FEATURE [PartDesign::Pocket] Pocket103
  BaseFeature = -> Pocket102
  Length = 5
  Length2 = 100
  Placement = pos=(0,0,0) rot=(0.57735,0.57735,0.57735;2.0944rad)
  Profile = -> Sketch269
  Type = 2
FEATURE [Sketcher::SketchObject] Sketch270
  ExternalGeometry = -> [Pocket103]
  FullyConstrained = true
  MapMode = 5
  Placement = pos=(0,0,0) rot=(0.57735,0.57735,0.57735;4.18879rad)
  Support = -> [Pocket103]
  sketch-geometry (9):
    g0: LineSegment StartX=0 StartY=8.5 StartZ=0 EndX=20 EndY=8.5 EndZ=0
    g1: ArcOfCircle CenterX=3 CenterY=9.5 CenterZ=0 NormalX=0 NormalY=0 NormalZ=1 AngleXU=0 Radius=1 StartAngle=0 EndAngle=3.14159
    g2: ArcOfCircle CenterX=3 CenterY=7.5 CenterZ=0 NormalX=0 NormalY=0 NormalZ=1 AngleXU=0 Radius=1 StartAngle=3.14159 EndAngle=6.28319
    g3: LineSegment StartX=2 StartY=9.5 StartZ=0 EndX=2 EndY=7.5 EndZ=0
    g4: LineSegment StartX=4 StartY=9.5 StartZ=0 EndX=4 EndY=7.5 EndZ=0
    g5: ArcOfCircle CenterX=18 CenterY=9.5 CenterZ=0 NormalX=0 NormalY=0 NormalZ=1 AngleXU=0 Radius=1 StartAngle=-9e-16 EndAngle=3.14159
    g6: ArcOfCircle CenterX=18 CenterY=7.5 CenterZ=0 NormalX=0 NormalY=0 NormalZ=1 AngleXU=0 Radius=1 StartAngle=3.14159 EndAngle=6.28319
    g7: LineSegment StartX=17 StartY=9.5 StartZ=0 EndX=17 EndY=7.5 EndZ=0
    g8: LineSegment StartX=19 StartY=9.5 StartZ=0 EndX=19 EndY=7.5 EndZ=0
  constraints (24):
    c: PointOnObject(g0,g-2)
    c: PointOnObject(g0,g-5)
    c: Horizontal(g0)
    c: DistanceY(g0,g-3) = 8.5
    c: Tangent(g1,g4) = 1.5708
    c: Tangent(g1,g3) = -1.5708
    c: Tangent(g3,g2) = -1.5708
    c: Tangent(g4,g2) = 1.5708
    c: Vertical(g3)
    c: Equal(g1,g2)
    c: Tangent(g5,g8) = 1.5708
    c: Tangent(g5,g7) = -1.5708
    c: Tangent(g7,g6) = -1.5708
    c: Tangent(g8,g6) = 1.5708
    c: Vertical(g7)
    c: Equal(g5,g6)
    c: Equal(g1,g5)
    c: Equal(g4,g7)
    c: DistanceY(g4,g4) = 2
    c: Radius(g1) = 1
    c: Horizontal(g5,g1)
    c: DistanceX(g0,g1) = 3
    c: DistanceX(g5,g0) = 2
    c: DistanceY(g0,g1) = 1
FEATURE [PartDesign::Pad] Pad133
  BaseFeature = -> Pocket103
  Direction = (1,1,1)
  Length = 1
  Length2 = 100
  Placement = pos=(0,0,0) rot=(0.57735,0.57735,0.57735;2.0944rad)
  Profile = -> Sketch270
  Type = 0
FEATURE [Sketcher::SketchObject] Sketch271
  ExternalGeometry = -> [Pad133]
  FullyConstrained = true
  MapMode = 5
  Placement = pos=(0,0,1e-16) rot=(0.707107,0.707107,0;3.14159rad)
  Support = -> [Pad133]
  sketch-geometry (9):
    g0: LineSegment StartX=0 StartY=8.5 StartZ=0 EndX=-20 EndY=8.5 EndZ=0
    g1: ArcOfCircle CenterX=-3 CenterY=7.5 CenterZ=0 NormalX=0 NormalY=0 NormalZ=1 AngleXU=0 Radius=1 StartAngle=3.14159 EndAngle=6.28319
    g2: ArcOfCircle CenterX=-3 CenterY=9.5 CenterZ=0 NormalX=0 NormalY=0 NormalZ=1 AngleXU=0 Radius=1 StartAngle=3e-16 EndAngle=3.14159
    g3: LineSegment StartX=-2 StartY=7.5 StartZ=0 EndX=-2 EndY=9.5 EndZ=0
    g4: LineSegment StartX=-4 StartY=7.5 StartZ=0 EndX=-4 EndY=9.5 EndZ=0
    g5: ArcOfCircle CenterX=-18 CenterY=9.5 CenterZ=0 NormalX=0 NormalY=0 NormalZ=1 AngleXU=0 Radius=1 StartAngle=0 EndAngle=3.14159
    g6: ArcOfCircle CenterX=-18 CenterY=7.5 CenterZ=0 NormalX=0 NormalY=0 NormalZ=1 AngleXU=0 Radius=1 StartAngle=3.14159 EndAngle=6.28319
    g7: LineSegment StartX=-19 StartY=9.5 StartZ=0 EndX=-19 EndY=7.5 EndZ=0
    g8: LineSegment StartX=-17 StartY=9.5 StartZ=0 EndX=-17 EndY=7.5 EndZ=0
  constraints (24):
    c: PointOnObject(g0,g-2)
    c: PointOnObject(g0,g-4)
    c: Horizontal(g0)
    c: DistanceY(g0,g-3) = 8.5
    c: Tangent(g1,g4) = 1.5708
    c: Tangent(g1,g3) = -1.5708
    c: Tangent(g3,g2) = -1.5708
    c: Tangent(g4,g2) = 1.5708
    c: Vertical(g3)
    c: Equal(g1,g2)
    c: Radius(g2) = 1
    c: DistanceY(g4,g4) = 2
    c: DistanceY(g0,g2) = 1
    c: DistanceX(g2,g0) = 3
    c: Tangent(g5,g8) = 1.5708
    c: Tangent(g5,g7) = -1.5708
    c: Tangent(g7,g6) = -1.5708
    c: Tangent(g8,g6) = 1.5708
    c: Vertical(g7)
    c: Equal(g5,g6)
    c: Equal(g5,g2)
    c: Equal(g8,g4)
    c: Horizontal(g5,g2)
    c: DistanceX(g0,g5) = 2
FEATURE [PartDesign::Pad] Pad134
  BaseFeature = -> Pad133
  Direction = (1,1,1)
  Length = 1
  Length2 = 100
  Placement = pos=(0,0,0) rot=(0.57735,0.57735,0.57735;2.0944rad)
  Profile = -> Sketch271
  Type = 0
FEATURE [PartDesign::Body] Body206  label="Corner009"
  Group = -> [Sketch266,Pad132,Sketch267,Pocket101,Sketch268,Pocket102,Sketch269,Pocket103,Sketch270,Pad133,Sketch271,Pad134]
  Origin = -> Origin285
  Tip = -> Pad134
FEATURE [App::Part] Part079  label="soporte90-010"
  Group = -> [Body206]
  Origin = -> Origin286
  Placement = pos=(3,320,70) rot=(1,0,0;1.5708rad)
FEATURE [Sketcher::SketchObject] Sketch272
  FullyConstrained = true
  MapMode = 5
  Placement = pos=(0,0,0) rot=(0.57735,0.57735,0.57735;2.0944rad)
  Support = -> [YZ_Plane281]
  sketch-geometry (5):
    g0: LineSegment StartX=0 StartY=0 StartZ=0 EndX=0 EndY=20 EndZ=0
    g1: LineSegment StartX=0 StartY=20 StartZ=0 EndX=-3 EndY=20 EndZ=0
    g2: LineSegment StartX=-3 StartY=20 StartZ=0 EndX=-20 EndY=3 EndZ=0
    g3: LineSegment StartX=-20 StartY=3 StartZ=0 EndX=-20 EndY=0 EndZ=0
    g4: LineSegment StartX=-20 StartY=0 StartZ=0 EndX=0 EndY=0 EndZ=0
  constraints (14):
    c: Coincident(g-1,g0)
    c: PointOnObject(g0,g-2)
    c: Coincident(g0,g1)
    c: Horizontal(g1)
    c: Coincident(g1,g2)
    c: Coincident(g2,g3)
    c: PointOnObject(g3,g-1)
    c: Vertical(g3)
    c: Coincident(g3,g4)
    c: Coincident(g4,g0)
    c: DistanceY(g0,g0) = 20
    c: DistanceY(g3,g3) = 3
    c: DistanceX(g1,g1) = 3
    c: DistanceX(g4,g4) = 20
FEATURE [PartDesign::Pad] Pad135
  Direction = (1,1,1)
  Length = 17
  Length2 = 100
  Placement = pos=(0,0,0) rot=(0.57735,0.57735,0.57735;2.0944rad)
  Profile = -> Sketch272
  Type = 0
FEATURE [Sketcher::SketchObject] Sketch273
  ExternalGeometry = -> [Pad135]
  FullyConstrained = true
  MapMode = 5
  Placement = pos=(-8.8e-15,-20,4.4e-15) rot=(-0.57735,-0.57735,0.57735;4.18879rad)
  Support = -> [Pad135]
  sketch-geometry (4):
    g0: LineSegment StartX=-3 StartY=2 StartZ=0 EndX=-20 EndY=2 EndZ=0
    g1: LineSegment StartX=-20 StartY=2 StartZ=0 EndX=-20 EndY=15 EndZ=0
    g2: LineSegment StartX=-20 StartY=15 StartZ=0 EndX=-3 EndY=15 EndZ=0
    g3: LineSegment StartX=-3 StartY=15 StartZ=0 EndX=-3 EndY=2 EndZ=0
  constraints (12):
    c: Coincident(g0,g1)
    c: Coincident(g1,g2)
    c: Coincident(g2,g3)
    c: Coincident(g3,g0)
    c: Horizontal(g0)
    c: Horizontal(g2)
    c: Vertical(g1)
    c: Vertical(g3)
    c: PointOnObject(g0,g-3)
    c: DistanceY(g1,g-6) = 2
    c: DistanceY(g-6,g0) = 2
    c: PointOnObject(g1,g-6)
FEATURE [PartDesign::Pocket] Pocket104
  BaseFeature = -> Pad135
  Length = 17
  Length2 = 100
  Placement = pos=(0,0,0) rot=(0.57735,0.57735,0.57735;2.0944rad)
  Profile = -> Sketch273
  Type = 0
FEATURE [Sketcher::SketchObject] Sketch274
  ExternalGeometry = -> [Pocket104]
  FullyConstrained = true
  MapMode = 5
  Placement = pos=(-1.7e-15,-3,6e-16) rot=(-0.57735,-0.57735,0.57735;4.18879rad)
  Support = -> [Pocket104]
  sketch-geometry (5):
    g0: LineSegment StartX=-20 StartY=8.5 StartZ=0 EndX=-3 EndY=8.5 EndZ=0
    g1: ArcOfCircle CenterX=-10 CenterY=8.5 CenterZ=0 NormalX=0 NormalY=0 NormalZ=1 AngleXU=0 Radius=3 StartAngle=4.71239 EndAngle=7.85398
    g2: ArcOfCircle CenterX=-13 CenterY=8.5 CenterZ=0 NormalX=0 NormalY=0 NormalZ=1 AngleXU=0 Radius=3 StartAngle=1.5708 EndAngle=4.71239
    g3: LineSegment StartX=-10 StartY=11.5 StartZ=0 EndX=-13 EndY=11.5 EndZ=0
    g4: LineSegment StartX=-10 StartY=5.5 StartZ=0 EndX=-13 EndY=5.5 EndZ=0
  constraints (14):
    c: PointOnObject(g0,g-6)
    c: PointOnObject(g0,g-4)
    c: Horizontal(g0)
    c: DistanceY(g0,g-4) = 6.5
    c: Tangent(g1,g4) = 1.5708
    c: Tangent(g1,g3) = -1.5708
    c: Tangent(g3,g2) = -1.5708
    c: Tangent(g4,g2) = 1.5708
    c: Horizontal(g3)
    c: Equal(g1,g2)
    c: PointOnObject(g1,g0)
    c: Radius(g1) = 3
    c: DistanceX(g3,g3) = 3
    c: DistanceX(g0,g2) = 7
FEATURE [PartDesign::Pocket] Pocket105
  BaseFeature = -> Pocket104
  Length = 5
  Length2 = 100
  Placement = pos=(0,0,0) rot=(0.57735,0.57735,0.57735;2.0944rad)
  Profile = -> Sketch274
  Type = 2
FEATURE [Sketcher::SketchObject] Sketch275
  ExternalGeometry = -> [Pocket105]
  FullyConstrained = true
  MapMode = 5
  Placement = pos=(-3e-16,1.2e-15,3) rot=(0,0,-1;1.5708rad)
  Support = -> [Pocket105]
  sketch-geometry (5):
    g0: LineSegment StartX=3 StartY=8.5 StartZ=0 EndX=20 EndY=8.5 EndZ=0
    g1: ArcOfCircle CenterX=10 CenterY=8.5 CenterZ=0 NormalX=0 NormalY=0 NormalZ=1 AngleXU=0 Radius=3 StartAngle=1.5708 EndAngle=4.71239
    g2: ArcOfCircle CenterX=13 CenterY=8.5 CenterZ=0 NormalX=0 NormalY=0 NormalZ=1 AngleXU=0 Radius=3 StartAngle=4.71239 EndAngle=7.85398
    g3: LineSegment StartX=10 StartY=5.5 StartZ=0 EndX=13 EndY=5.5 EndZ=0
    g4: LineSegment StartX=10 StartY=11.5 StartZ=0 EndX=13 EndY=11.5 EndZ=0
  constraints (14):
    c: PointOnObject(g0,g-4)
    c: PointOnObject(g0,g-5)
    c: Horizontal(g0)
    c: DistanceY(g0,g-4) = 6.5
    c: Tangent(g1,g4) = 1.5708
    c: Tangent(g1,g3) = -1.5708
    c: Tangent(g3,g2) = -1.5708
    c: Tangent(g4,g2) = 1.5708
    c: Horizontal(g3)
    c: Equal(g1,g2)
    c: PointOnObject(g1,g0)
    c: Radius(g2) = 3
    c: DistanceX(g4,g4) = 3
    c: DistanceX(g2,g0) = 7
FEATURE [PartDesign::Pocket] Pocket106
  BaseFeature = -> Pocket105
  Length = 5
  Length2 = 100
  Placement = pos=(0,0,0) rot=(0.57735,0.57735,0.57735;2.0944rad)
  Profile = -> Sketch275
  Type = 2
FEATURE [Sketcher::SketchObject] Sketch276
  ExternalGeometry = -> [Pocket106]
  FullyConstrained = true
  MapMode = 5
  Placement = pos=(0,0,0) rot=(0.57735,0.57735,0.57735;4.18879rad)
  Support = -> [Pocket106]
  sketch-geometry (9):
    g0: LineSegment StartX=0 StartY=8.5 StartZ=0 EndX=20 EndY=8.5 EndZ=0
    g1: ArcOfCircle CenterX=3 CenterY=9.5 CenterZ=0 NormalX=0 NormalY=0 NormalZ=1 AngleXU=0 Radius=1 StartAngle=0 EndAngle=3.14159
    g2: ArcOfCircle CenterX=3 CenterY=7.5 CenterZ=0 NormalX=0 NormalY=0 NormalZ=1 AngleXU=0 Radius=1 StartAngle=3.14159 EndAngle=6.28319
    g3: LineSegment StartX=2 StartY=9.5 StartZ=0 EndX=2 EndY=7.5 EndZ=0
    g4: LineSegment StartX=4 StartY=9.5 StartZ=0 EndX=4 EndY=7.5 EndZ=0
    g5: ArcOfCircle CenterX=18 CenterY=9.5 CenterZ=0 NormalX=0 NormalY=0 NormalZ=1 AngleXU=0 Radius=1 StartAngle=-9e-16 EndAngle=3.14159
    g6: ArcOfCircle CenterX=18 CenterY=7.5 CenterZ=0 NormalX=0 NormalY=0 NormalZ=1 AngleXU=0 Radius=1 StartAngle=3.14159 EndAngle=6.28319
    g7: LineSegment StartX=17 StartY=9.5 StartZ=0 EndX=17 EndY=7.5 EndZ=0
    g8: LineSegment StartX=19 StartY=9.5 StartZ=0 EndX=19 EndY=7.5 EndZ=0
  constraints (24):
    c: PointOnObject(g0,g-2)
    c: PointOnObject(g0,g-5)
    c: Horizontal(g0)
    c: DistanceY(g0,g-3) = 8.5
    c: Tangent(g1,g4) = 1.5708
    c: Tangent(g1,g3) = -1.5708
    c: Tangent(g3,g2) = -1.5708
    c: Tangent(g4,g2) = 1.5708
    c: Vertical(g3)
    c: Equal(g1,g2)
    c: Tangent(g5,g8) = 1.5708
    c: Tangent(g5,g7) = -1.5708
    c: Tangent(g7,g6) = -1.5708
    c: Tangent(g8,g6) = 1.5708
    c: Vertical(g7)
    c: Equal(g5,g6)
    c: Equal(g1,g5)
    c: Equal(g4,g7)
    c: DistanceY(g4,g4) = 2
    c: Radius(g1) = 1
    c: Horizontal(g5,g1)
    c: DistanceX(g0,g1) = 3
    c: DistanceX(g5,g0) = 2
    c: DistanceY(g0,g1) = 1
FEATURE [PartDesign::Pad] Pad136
  BaseFeature = -> Pocket106
  Direction = (1,1,1)
  Length = 1
  Length2 = 100
  Placement = pos=(0,0,0) rot=(0.57735,0.57735,0.57735;2.0944rad)
  Profile = -> Sketch276
  Type = 0
FEATURE [Sketcher::SketchObject] Sketch277
  ExternalGeometry = -> [Pad136]
  FullyConstrained = true
  MapMode = 5
  Placement = pos=(0,0,1e-16) rot=(0.707107,0.707107,0;3.14159rad)
  Support = -> [Pad136]
  sketch-geometry (9):
    g0: LineSegment StartX=0 StartY=8.5 StartZ=0 EndX=-20 EndY=8.5 EndZ=0
    g1: ArcOfCircle CenterX=-3 CenterY=7.5 CenterZ=0 NormalX=0 NormalY=0 NormalZ=1 AngleXU=0 Radius=1 StartAngle=3.14159 EndAngle=6.28319
    g2: ArcOfCircle CenterX=-3 CenterY=9.5 CenterZ=0 NormalX=0 NormalY=0 NormalZ=1 AngleXU=0 Radius=1 StartAngle=3e-16 EndAngle=3.14159
    g3: LineSegment StartX=-2 StartY=7.5 StartZ=0 EndX=-2 EndY=9.5 EndZ=0
    g4: LineSegment StartX=-4 StartY=7.5 StartZ=0 EndX=-4 EndY=9.5 EndZ=0
    g5: ArcOfCircle CenterX=-18 CenterY=9.5 CenterZ=0 NormalX=0 NormalY=0 NormalZ=1 AngleXU=0 Radius=1 StartAngle=0 EndAngle=3.14159
    g6: ArcOfCircle CenterX=-18 CenterY=7.5 CenterZ=0 NormalX=0 NormalY=0 NormalZ=1 AngleXU=0 Radius=1 StartAngle=3.14159 EndAngle=6.28319
    g7: LineSegment StartX=-19 StartY=9.5 StartZ=0 EndX=-19 EndY=7.5 EndZ=0
    g8: LineSegment StartX=-17 StartY=9.5 StartZ=0 EndX=-17 EndY=7.5 EndZ=0
  constraints (24):
    c: PointOnObject(g0,g-2)
    c: PointOnObject(g0,g-4)
    c: Horizontal(g0)
    c: DistanceY(g0,g-3) = 8.5
    c: Tangent(g1,g4) = 1.5708
    c: Tangent(g1,g3) = -1.5708
    c: Tangent(g3,g2) = -1.5708
    c: Tangent(g4,g2) = 1.5708
    c: Vertical(g3)
    c: Equal(g1,g2)
    c: Radius(g2) = 1
    c: DistanceY(g4,g4) = 2
    c: DistanceY(g0,g2) = 1
    c: DistanceX(g2,g0) = 3
    c: Tangent(g5,g8) = 1.5708
    c: Tangent(g5,g7) = -1.5708
    c: Tangent(g7,g6) = -1.5708
    c: Tangent(g8,g6) = 1.5708
    c: Vertical(g7)
    c: Equal(g5,g6)
    c: Equal(g5,g2)
    c: Equal(g8,g4)
    c: Horizontal(g5,g2)
    c: DistanceX(g0,g5) = 2
FEATURE [PartDesign::Pad] Pad137
  BaseFeature = -> Pad136
  Direction = (1,1,1)
  Length = 1
  Length2 = 100
  Placement = pos=(0,0,0) rot=(0.57735,0.57735,0.57735;2.0944rad)
  Profile = -> Sketch277
  Type = 0
FEATURE [PartDesign::Body] Body207  label="Corner010"
  Group = -> [Sketch272,Pad135,Sketch273,Pocket104,Sketch274,Pocket105,Sketch275,Pocket106,Sketch276,Pad136,Sketch277,Pad137]
  Origin = -> Origin287
  Tip = -> Pad137
FEATURE [App::Part] Part080  label="soporte90-011"
  Group = -> [Body207]
  Origin = -> Origin288
  Placement = pos=(322,320,70) rot=(1,0,0;1.5708rad)
FEATURE [Sketcher::SketchObject] Sketch278
  FullyConstrained = true
  MapMode = 5
  Placement = pos=(0,0,0) rot=(0.57735,0.57735,0.57735;2.0944rad)
  Support = -> [YZ_Plane283]
  sketch-geometry (5):
    g0: LineSegment StartX=0 StartY=0 StartZ=0 EndX=0 EndY=20 EndZ=0
    g1: LineSegment StartX=0 StartY=20 StartZ=0 EndX=-3 EndY=20 EndZ=0
    g2: LineSegment StartX=-3 StartY=20 StartZ=0 EndX=-20 EndY=3 EndZ=0
    g3: LineSegment StartX=-20 StartY=3 StartZ=0 EndX=-20 EndY=0 EndZ=0
    g4: LineSegment StartX=-20 StartY=0 StartZ=0 EndX=0 EndY=0 EndZ=0
  constraints (14):
    c: Coincident(g-1,g0)
    c: PointOnObject(g0,g-2)
    c: Coincident(g0,g1)
    c: Horizontal(g1)
    c: Coincident(g1,g2)
    c: Coincident(g2,g3)
    c: PointOnObject(g3,g-1)
    c: Vertical(g3)
    c: Coincident(g3,g4)
    c: Coincident(g4,g0)
    c: DistanceY(g0,g0) = 20
    c: DistanceY(g3,g3) = 3
    c: DistanceX(g1,g1) = 3
    c: DistanceX(g4,g4) = 20
FEATURE [PartDesign::Pad] Pad138
  Direction = (1,1,1)
  Length = 17
  Length2 = 100
  Placement = pos=(0,0,0) rot=(0.57735,0.57735,0.57735;2.0944rad)
  Profile = -> Sketch278
  Type = 0
FEATURE [Sketcher::SketchObject] Sketch279
  ExternalGeometry = -> [Pad138]
  FullyConstrained = true
  MapMode = 5
  Placement = pos=(-8.8e-15,-20,4.4e-15) rot=(-0.57735,-0.57735,0.57735;4.18879rad)
  Support = -> [Pad138]
  sketch-geometry (4):
    g0: LineSegment StartX=-3 StartY=2 StartZ=0 EndX=-20 EndY=2 EndZ=0
    g1: LineSegment StartX=-20 StartY=2 StartZ=0 EndX=-20 EndY=15 EndZ=0
    g2: LineSegment StartX=-20 StartY=15 StartZ=0 EndX=-3 EndY=15 EndZ=0
    g3: LineSegment StartX=-3 StartY=15 StartZ=0 EndX=-3 EndY=2 EndZ=0
  constraints (12):
    c: Coincident(g0,g1)
    c: Coincident(g1,g2)
    c: Coincident(g2,g3)
    c: Coincident(g3,g0)
    c: Horizontal(g0)
    c: Horizontal(g2)
    c: Vertical(g1)
    c: Vertical(g3)
    c: PointOnObject(g0,g-3)
    c: DistanceY(g1,g-6) = 2
    c: DistanceY(g-6,g0) = 2
    c: PointOnObject(g1,g-6)
FEATURE [PartDesign::Pocket] Pocket107
  BaseFeature = -> Pad138
  Length = 17
  Length2 = 100
  Placement = pos=(0,0,0) rot=(0.57735,0.57735,0.57735;2.0944rad)
  Profile = -> Sketch279
  Type = 0
FEATURE [Sketcher::SketchObject] Sketch280
  ExternalGeometry = -> [Pocket107]
  FullyConstrained = true
  MapMode = 5
  Placement = pos=(-1.7e-15,-3,6e-16) rot=(-0.57735,-0.57735,0.57735;4.18879rad)
  Support = -> [Pocket107]
  sketch-geometry (5):
    g0: LineSegment StartX=-20 StartY=8.5 StartZ=0 EndX=-3 EndY=8.5 EndZ=0
    g1: ArcOfCircle CenterX=-10 CenterY=8.5 CenterZ=0 NormalX=0 NormalY=0 NormalZ=1 AngleXU=0 Radius=3 StartAngle=4.71239 EndAngle=7.85398
    g2: ArcOfCircle CenterX=-13 CenterY=8.5 CenterZ=0 NormalX=0 NormalY=0 NormalZ=1 AngleXU=0 Radius=3 StartAngle=1.5708 EndAngle=4.71239
    g3: LineSegment StartX=-10 StartY=11.5 StartZ=0 EndX=-13 EndY=11.5 EndZ=0
    g4: LineSegment StartX=-10 StartY=5.5 StartZ=0 EndX=-13 EndY=5.5 EndZ=0
  constraints (14):
    c: PointOnObject(g0,g-6)
    c: PointOnObject(g0,g-4)
    c: Horizontal(g0)
    c: DistanceY(g0,g-4) = 6.5
    c: Tangent(g1,g4) = 1.5708
    c: Tangent(g1,g3) = -1.5708
    c: Tangent(g3,g2) = -1.5708
    c: Tangent(g4,g2) = 1.5708
    c: Horizontal(g3)
    c: Equal(g1,g2)
    c: PointOnObject(g1,g0)
    c: Radius(g1) = 3
    c: DistanceX(g3,g3) = 3
    c: DistanceX(g0,g2) = 7
FEATURE [PartDesign::Pocket] Pocket108
  BaseFeature = -> Pocket107
  Length = 5
  Length2 = 100
  Placement = pos=(0,0,0) rot=(0.57735,0.57735,0.57735;2.0944rad)
  Profile = -> Sketch280
  Type = 2
FEATURE [Sketcher::SketchObject] Sketch281
  ExternalGeometry = -> [Pocket108]
  FullyConstrained = true
  MapMode = 5
  Placement = pos=(-3e-16,1.2e-15,3) rot=(0,0,-1;1.5708rad)
  Support = -> [Pocket108]
  sketch-geometry (5):
    g0: LineSegment StartX=3 StartY=8.5 StartZ=0 EndX=20 EndY=8.5 EndZ=0
    g1: ArcOfCircle CenterX=10 CenterY=8.5 CenterZ=0 NormalX=0 NormalY=0 NormalZ=1 AngleXU=0 Radius=3 StartAngle=1.5708 EndAngle=4.71239
    g2: ArcOfCircle CenterX=13 CenterY=8.5 CenterZ=0 NormalX=0 NormalY=0 NormalZ=1 AngleXU=0 Radius=3 StartAngle=4.71239 EndAngle=7.85398
    g3: LineSegment StartX=10 StartY=5.5 StartZ=0 EndX=13 EndY=5.5 EndZ=0
    g4: LineSegment StartX=10 StartY=11.5 StartZ=0 EndX=13 EndY=11.5 EndZ=0
  constraints (14):
    c: PointOnObject(g0,g-4)
    c: PointOnObject(g0,g-5)
    c: Horizontal(g0)
    c: DistanceY(g0,g-4) = 6.5
    c: Tangent(g1,g4) = 1.5708
    c: Tangent(g1,g3) = -1.5708
    c: Tangent(g3,g2) = -1.5708
    c: Tangent(g4,g2) = 1.5708
    c: Horizontal(g3)
    c: Equal(g1,g2)
    c: PointOnObject(g1,g0)
    c: Radius(g2) = 3
    c: DistanceX(g4,g4) = 3
    c: DistanceX(g2,g0) = 7
FEATURE [PartDesign::Pocket] Pocket109
  BaseFeature = -> Pocket108
  Length = 5
  Length2 = 100
  Placement = pos=(0,0,0) rot=(0.57735,0.57735,0.57735;2.0944rad)
  Profile = -> Sketch281
  Type = 2
FEATURE [Sketcher::SketchObject] Sketch282
  ExternalGeometry = -> [Pocket109]
  FullyConstrained = true
  MapMode = 5
  Placement = pos=(0,0,0) rot=(0.57735,0.57735,0.57735;4.18879rad)
  Support = -> [Pocket109]
  sketch-geometry (9):
    g0: LineSegment StartX=0 StartY=8.5 StartZ=0 EndX=20 EndY=8.5 EndZ=0
    g1: ArcOfCircle CenterX=3 CenterY=9.5 CenterZ=0 NormalX=0 NormalY=0 NormalZ=1 AngleXU=0 Radius=1 StartAngle=0 EndAngle=3.14159
    g2: ArcOfCircle CenterX=3 CenterY=7.5 CenterZ=0 NormalX=0 NormalY=0 NormalZ=1 AngleXU=0 Radius=1 StartAngle=3.14159 EndAngle=6.28319
    g3: LineSegment StartX=2 StartY=9.5 StartZ=0 EndX=2 EndY=7.5 EndZ=0
    g4: LineSegment StartX=4 StartY=9.5 StartZ=0 EndX=4 EndY=7.5 EndZ=0
    g5: ArcOfCircle CenterX=18 CenterY=9.5 CenterZ=0 NormalX=0 NormalY=0 NormalZ=1 AngleXU=0 Radius=1 StartAngle=-9e-16 EndAngle=3.14159
    g6: ArcOfCircle CenterX=18 CenterY=7.5 CenterZ=0 NormalX=0 NormalY=0 NormalZ=1 AngleXU=0 Radius=1 StartAngle=3.14159 EndAngle=6.28319
    g7: LineSegment StartX=17 StartY=9.5 StartZ=0 EndX=17 EndY=7.5 EndZ=0
    g8: LineSegment StartX=19 StartY=9.5 StartZ=0 EndX=19 EndY=7.5 EndZ=0
  constraints (24):
    c: PointOnObject(g0,g-2)
    c: PointOnObject(g0,g-5)
    c: Horizontal(g0)
    c: DistanceY(g0,g-3) = 8.5
    c: Tangent(g1,g4) = 1.5708
    c: Tangent(g1,g3) = -1.5708
    c: Tangent(g3,g2) = -1.5708
    c: Tangent(g4,g2) = 1.5708
    c: Vertical(g3)
    c: Equal(g1,g2)
    c: Tangent(g5,g8) = 1.5708
    c: Tangent(g5,g7) = -1.5708
    c: Tangent(g7,g6) = -1.5708
    c: Tangent(g8,g6) = 1.5708
    c: Vertical(g7)
    c: Equal(g5,g6)
    c: Equal(g1,g5)
    c: Equal(g4,g7)
    c: DistanceY(g4,g4) = 2
    c: Radius(g1) = 1
    c: Horizontal(g5,g1)
    c: DistanceX(g0,g1) = 3
    c: DistanceX(g5,g0) = 2
    c: DistanceY(g0,g1) = 1
FEATURE [PartDesign::Pad] Pad139
  BaseFeature = -> Pocket109
  Direction = (1,1,1)
  Length = 1
  Length2 = 100
  Placement = pos=(0,0,0) rot=(0.57735,0.57735,0.57735;2.0944rad)
  Profile = -> Sketch282
  Type = 0
FEATURE [Sketcher::SketchObject] Sketch283
  ExternalGeometry = -> [Pad139]
  FullyConstrained = true
  MapMode = 5
  Placement = pos=(0,0,1e-16) rot=(0.707107,0.707107,0;3.14159rad)
  Support = -> [Pad139]
  sketch-geometry (9):
    g0: LineSegment StartX=0 StartY=8.5 StartZ=0 EndX=-20 EndY=8.5 EndZ=0
    g1: ArcOfCircle CenterX=-3 CenterY=7.5 CenterZ=0 NormalX=0 NormalY=0 NormalZ=1 AngleXU=0 Radius=1 StartAngle=3.14159 EndAngle=6.28319
    g2: ArcOfCircle CenterX=-3 CenterY=9.5 CenterZ=0 NormalX=0 NormalY=0 NormalZ=1 AngleXU=0 Radius=1 StartAngle=3e-16 EndAngle=3.14159
    g3: LineSegment StartX=-2 StartY=7.5 StartZ=0 EndX=-2 EndY=9.5 EndZ=0
    g4: LineSegment StartX=-4 StartY=7.5 StartZ=0 EndX=-4 EndY=9.5 EndZ=0
    g5: ArcOfCircle CenterX=-18 CenterY=9.5 CenterZ=0 NormalX=0 NormalY=0 NormalZ=1 AngleXU=0 Radius=1 StartAngle=0 EndAngle=3.14159
    g6: ArcOfCircle CenterX=-18 CenterY=7.5 CenterZ=0 NormalX=0 NormalY=0 NormalZ=1 AngleXU=0 Radius=1 StartAngle=3.14159 EndAngle=6.28319
    g7: LineSegment StartX=-19 StartY=9.5 StartZ=0 EndX=-19 EndY=7.5 EndZ=0
    g8: LineSegment StartX=-17 StartY=9.5 StartZ=0 EndX=-17 EndY=7.5 EndZ=0
  constraints (24):
    c: PointOnObject(g0,g-2)
    c: PointOnObject(g0,g-4)
    c: Horizontal(g0)
    c: DistanceY(g0,g-3) = 8.5
    c: Tangent(g1,g4) = 1.5708
    c: Tangent(g1,g3) = -1.5708
    c: Tangent(g3,g2) = -1.5708
    c: Tangent(g4,g2) = 1.5708
    c: Vertical(g3)
    c: Equal(g1,g2)
    c: Radius(g2) = 1
    c: DistanceY(g4,g4) = 2
    c: DistanceY(g0,g2) = 1
    c: DistanceX(g2,g0) = 3
    c: Tangent(g5,g8) = 1.5708
    c: Tangent(g5,g7) = -1.5708
    c: Tangent(g7,g6) = -1.5708
    c: Tangent(g8,g6) = 1.5708
    c: Vertical(g7)
    c: Equal(g5,g6)
    c: Equal(g5,g2)
    c: Equal(g8,g4)
    c: Horizontal(g5,g2)
    c: DistanceX(g0,g5) = 2
FEATURE [PartDesign::Pad] Pad140
  BaseFeature = -> Pad139
  Direction = (1,1,1)
  Length = 1
  Length2 = 100
  Placement = pos=(0,0,0) rot=(0.57735,0.57735,0.57735;2.0944rad)
  Profile = -> Sketch283
  Type = 0
FEATURE [PartDesign::Body] Body208  label="Corner011"
  Group = -> [Sketch278,Pad138,Sketch279,Pocket107,Sketch280,Pocket108,Sketch281,Pocket109,Sketch282,Pad139,Sketch283,Pad140]
  Origin = -> Origin289
  Tip = -> Pad140
FEATURE [App::Part] Part081  label="soporte90-012"
  Group = -> [Body208]
  Origin = -> Origin290
  Placement = pos=(319,20,70) rot=(1,0,0;3.14159rad)
FEATURE [App::LinkGroup] LinkGroup010  label="esquineros estructura"
  ElementList = -> [Part081,Part074,Part070,Part071,Part072,Part073,Part075,Part076,Part080,Part079,Part078,Part077]
  LinkMode = 0
FEATURE [Sketcher::SketchObject] Sketch284
  FullyConstrained = false
  MapMode = 5
  Support = -> [XY_Plane286]
  sketch-geometry (4):
    g0: ArcOfCircle CenterX=0 CenterY=4e-15 CenterZ=0 NormalX=0 NormalY=0 NormalZ=1 AngleXU=0 Radius=11 StartAngle=2.18335 EndAngle=3.14159
    g1: LineSegment StartX=-11 StartY=4e-15 StartZ=0 EndX=0 EndY=4e-15 EndZ=0
    g2: LineSegment StartX=0 StartY=9 StartZ=0 EndX=0 EndY=3.6e-15 EndZ=0
    g3: LineSegment StartX=0 StartY=9 StartZ=0 EndX=-6.32456 EndY=9 EndZ=0
  constraints (10):
    c: Coincident(g0,g-1)
    c: Diameter(g0) = 22
    c: Coincident(g1,g0)
    c: Horizontal(g1)
    c: Coincident(g0,g1)
    c: Coincident(g2,g0)
    c: Vertical(g2)
    c: Horizontal(g3)
    c: Coincident(g3,g2)
    c: Coincident(g3,g0)
FEATURE [PartDesign::Revolution] Revolution046
  Angle = 360
  Axis = (0,1,0)
  Base = (0,0,0)
  Profile = -> Sketch284
  ReferenceAxis = -> Sketch284 [V_Axis]
FEATURE [PartDesign::Body] Body209
  Group = -> [Sketch284,Revolution046]
  Origin = -> Origin292
  Tip = -> Revolution046
FEATURE [App::Part] Part082  label="tacoGoma-002"
  Group = -> [Body209]
  Origin = -> Origin291
  Placement = pos=(10,9,0) rot=(1,0,0;-1.5708rad)
FEATURE [Sketcher::SketchObject] Sketch285
  FullyConstrained = false
  MapMode = 5
  Support = -> [XY_Plane288]
  sketch-geometry (4):
    g0: ArcOfCircle CenterX=0 CenterY=4e-15 CenterZ=0 NormalX=0 NormalY=0 NormalZ=1 AngleXU=0 Radius=11 StartAngle=2.18335 EndAngle=3.14159
    g1: LineSegment StartX=-11 StartY=4e-15 StartZ=0 EndX=0 EndY=4e-15 EndZ=0
    g2: LineSegment StartX=0 StartY=9 StartZ=0 EndX=0 EndY=3.6e-15 EndZ=0
    g3: LineSegment StartX=0 StartY=9 StartZ=0 EndX=-6.32456 EndY=9 EndZ=0
  constraints (10):
    c: Coincident(g0,g-1)
    c: Diameter(g0) = 22
    c: Coincident(g1,g0)
    c: Horizontal(g1)
    c: Coincident(g0,g1)
    c: Coincident(g2,g0)
    c: Vertical(g2)
    c: Horizontal(g3)
    c: Coincident(g3,g2)
    c: Coincident(g3,g0)
FEATURE [PartDesign::Revolution] Revolution047
  Angle = 360
  Axis = (0,1,0)
  Base = (0,0,0)
  Profile = -> Sketch285
  ReferenceAxis = -> Sketch285 [V_Axis]
FEATURE [PartDesign::Body] Body210
  Group = -> [Sketch285,Revolution047]
  Origin = -> Origin294
  Tip = -> Revolution047
FEATURE [App::Part] Part083  label="tacoGoma001"
  Group = -> [Body210]
  Origin = -> Origin293
  Placement = pos=(10,331,0) rot=(1,0,0;-1.5708rad)
FEATURE [Sketcher::SketchObject] Sketch286
  FullyConstrained = false
  MapMode = 5
  Support = -> [XY_Plane290]
  sketch-geometry (4):
    g0: ArcOfCircle CenterX=0 CenterY=4e-15 CenterZ=0 NormalX=0 NormalY=0 NormalZ=1 AngleXU=0 Radius=11 StartAngle=2.18335 EndAngle=3.14159
    g1: LineSegment StartX=-11 StartY=4e-15 StartZ=0 EndX=0 EndY=4e-15 EndZ=0
    g2: LineSegment StartX=0 StartY=9 StartZ=0 EndX=0 EndY=3.6e-15 EndZ=0
    g3: LineSegment StartX=0 StartY=9 StartZ=0 EndX=-6.32456 EndY=9 EndZ=0
  constraints (10):
    c: Coincident(g0,g-1)
    c: Diameter(g0) = 22
    c: Coincident(g1,g0)
    c: Horizontal(g1)
    c: Coincident(g0,g1)
    c: Coincident(g2,g0)
    c: Vertical(g2)
    c: Horizontal(g3)
    c: Coincident(g3,g2)
    c: Coincident(g3,g0)
FEATURE [PartDesign::Revolution] Revolution048
  Angle = 360
  Axis = (0,1,0)
  Base = (0,0,0)
  Profile = -> Sketch286
  ReferenceAxis = -> Sketch286 [V_Axis]
FEATURE [PartDesign::Body] Body211
  Group = -> [Sketch286,Revolution048]
  Origin = -> Origin296
  Tip = -> Revolution048
FEATURE [App::Part] Part084  label="tacoGoma002"
  Group = -> [Body211]
  Origin = -> Origin295
  Placement = pos=(330,330,2e-16) rot=(1,0,0;-1.5708rad)
FEATURE [Sketcher::SketchObject] Sketch287
  FullyConstrained = false
  MapMode = 5
  Support = -> [XY_Plane292]
  sketch-geometry (4):
    g0: ArcOfCircle CenterX=0 CenterY=4e-15 CenterZ=0 NormalX=0 NormalY=0 NormalZ=1 AngleXU=0 Radius=11 StartAngle=2.18335 EndAngle=3.14159
    g1: LineSegment StartX=-11 StartY=4e-15 StartZ=0 EndX=0 EndY=4e-15 EndZ=0
    g2: LineSegment StartX=0 StartY=9 StartZ=0 EndX=0 EndY=3.6e-15 EndZ=0
    g3: LineSegment StartX=0 StartY=9 StartZ=0 EndX=-6.32456 EndY=9 EndZ=0
  constraints (10):
    c: Coincident(g0,g-1)
    c: Diameter(g0) = 22
    c: Coincident(g1,g0)
    c: Horizontal(g1)
    c: Coincident(g0,g1)
    c: Coincident(g2,g0)
    c: Vertical(g2)
    c: Horizontal(g3)
    c: Coincident(g3,g2)
    c: Coincident(g3,g0)
FEATURE [PartDesign::Revolution] Revolution049
  Angle = 360
  Axis = (0,1,0)
  Base = (0,0,0)
  Profile = -> Sketch287
  ReferenceAxis = -> Sketch287 [V_Axis]
FEATURE [PartDesign::Body] Body212
  Group = -> [Sketch287,Revolution049]
  Origin = -> Origin298
  Tip = -> Revolution049
FEATURE [App::Part] Part085  label="tacoGoma003"
  Group = -> [Body212]
  Origin = -> Origin297
  Placement = pos=(330,9,0) rot=(1,0,0;-1.5708rad)
FEATURE [App::LinkGroup] LinkGroup011  label="tacos de madera"
  ElementList = -> [Part082,Part083,Part084,Part085]
  LinkMode = 0
FEATURE [PartDesign::Plane] DatumPlane
  AttachmentOffset = pos=(0,0,0) rot=(0,1,0;0.174533rad)
  Length = 68.686
  MapMode = 5
  Placement = pos=(0,0,0) rot=(0.992433,0.086827,0.086827;1.57839rad)
  ResizeMode = 0
  Support = -> [XZ_Plane296]
  Width = 60.7632
FEATURE [Part::Helix] Helix001  label="Hélice001"
  Angle = 0
  AttacherType = Attacher::AttachEngine3D
  Height = 9.1
  LocalCoord = 0
  Pitch = 1.5
  Placement = pos=(0,0,7.35) rot=(0,0,1;0rad)
  Radius = 10
  Style = 1
FEATURE [PartDesign::ShapeBinder] ShapeBinder001
  Placement = pos=(0,0,7.35) rot=(0,0,1;0rad)
  Support = -> [Helix001]
  TraceSupport = false
FEATURE [Sketcher::SketchObject] Sketch289
  FullyConstrained = false
  MapMode = 5
  Placement = pos=(0,0,0) rot=(1,0,0;1.5708rad)
  Support = -> [XZ_Plane296]
  sketch-geometry (6):
    g0: LineSegment StartX=-9 StartY=25 StartZ=0 EndX=-4 EndY=25 EndZ=0
    g1: LineSegment StartX=-2.5 StartY=8 StartZ=0 EndX=-2.5 EndY=0 EndZ=0
    g2: LineSegment StartX=-2.5 StartY=0 StartZ=0 EndX=-9 EndY=0 EndZ=0
    g3: LineSegment StartX=-9 StartY=0 StartZ=0 EndX=-9 EndY=25 EndZ=0
    g4: LineSegment StartX=-2.5 StartY=8 StartZ=0 EndX=-4 EndY=8 EndZ=0
    g5: LineSegment StartX=-4 StartY=8 StartZ=0 EndX=-4 EndY=25 EndZ=0
  constraints (18):
    c: Coincident(g1,g2)
    c: Coincident(g2,g3)
    c: Coincident(g3,g0)
    c: Horizontal(g0)
    c: Horizontal(g2)
    c: Vertical(g1)
    c: Vertical(g3)
    c: PointOnObject(g1,g-1)
    c: DistanceX(g1,g-1) = 2.5
    c: DistanceX(g2,g-1) = 9
    c: DistanceY(g3,g3) = 25
    c: Horizontal(g4)
    c: Coincident(g5,g4)
    c: Vertical(g5)
    c: Coincident(g1,g4)
    c: Coincident(g0,g5)
    c: DistanceX(g0,g-1) = 4
    c: DistanceY(g5,g5) = 17
FEATURE [PartDesign::Revolution] Revolution050
  AllowMultiFace = false
  Angle = 360
  Axis = (0,-2e-16,1)
  Base = (0,0,0)
  Placement = pos=(0,0,0) rot=(1,0,0;1.5708rad)
  Profile = -> Sketch289
  ReferenceAxis = -> Sketch289 [V_Axis]
  Refine = true
FEATURE [Sketcher::SketchObject] Sketch290
  FullyConstrained = false
  MapMode = 5
  Placement = pos=(0,0,0) rot=(1,0,0;1.5708rad)
  Support = -> [XZ_Plane296]
  sketch-geometry (4):
    g0: LineSegment StartX=0.227639 StartY=16.7629 StartZ=0 EndX=11.1677 EndY=16.7629 EndZ=0
    g1: LineSegment StartX=11.1677 StartY=16.7629 StartZ=0 EndX=11.1677 EndY=16.2629 EndZ=0
    g2: LineSegment StartX=11.1677 StartY=16.2629 StartZ=0 EndX=0.227639 EndY=16.2629 EndZ=0
    g3: LineSegment StartX=0.227639 StartY=16.2629 StartZ=0 EndX=0.227639 EndY=16.7629 EndZ=0
  constraints (9):
    c: Coincident(g0,g1)
    c: Coincident(g1,g2)
    c: Coincident(g2,g3)
    c: Coincident(g3,g0)
    c: Horizontal(g0)
    c: Horizontal(g2)
    c: Vertical(g1)
    c: Vertical(g3)
    c: DistanceY(g1,g1) = 0.5
FEATURE [Sketcher::SketchObject] Sketch292
  FullyConstrained = false
  MapMode = 5
  Placement = pos=(0,0,0) rot=(1,0,0;1.5708rad)
  Support = -> [XZ_Plane297]
  sketch-geometry (4):
    g0: LineSegment StartX=0 StartY=0 StartZ=0 EndX=-2 EndY=0 EndZ=0
    g1: LineSegment StartX=-2 StartY=0 StartZ=0 EndX=-2 EndY=6 EndZ=0
    g2: LineSegment StartX=-2 StartY=6 StartZ=0 EndX=0 EndY=6 EndZ=0
    g3: LineSegment StartX=0 StartY=6 StartZ=0 EndX=0 EndY=0 EndZ=0
  constraints (11):
    c: Coincident(g0,g1)
    c: Coincident(g1,g2)
    c: Coincident(g2,g3)
    c: Coincident(g3,g0)
    c: Horizontal(g0)
    c: Horizontal(g2)
    c: Vertical(g1)
    c: Vertical(g3)
    c: Coincident(g0,g-1)
    c: DistanceX(g2,g2) = 2
    c: DistanceY(g1,g1) = 6
FEATURE [PartDesign::Revolution] Revolution001
  AllowMultiFace = false
  Angle = 360
  Axis = (0,2e-16,1)
  Base = (0,0,0)
  Placement = pos=(0,0,0) rot=(1,0,0;1.5708rad)
  Profile = -> Sketch292
  ReferenceAxis = -> Sketch292 [V_Axis]
  Refine = true
FEATURE [Sketcher::SketchObject] Sketch293
  FullyConstrained = false
  MapMode = 5
  Placement = pos=(0,2.6e-15,6) rot=(0,0,1;3.14159rad)
  Support = -> [Revolution001]
  sketch-geometry (7):
    g0: LineSegment StartX=-0.625 StartY=-1.08253 StartZ=0 EndX=0.625 EndY=-1.08253 EndZ=0
    g1: LineSegment StartX=0.625 StartY=-1.08253 StartZ=0 EndX=1.25 EndY=-1.44e-14 EndZ=0
    g2: LineSegment StartX=1.25 StartY=-1.44e-14 StartZ=0 EndX=0.625 EndY=1.08253 EndZ=0
    g3: LineSegment StartX=0.625 StartY=1.08253 StartZ=0 EndX=-0.625 EndY=1.08253 EndZ=0
    g4: LineSegment StartX=-0.625 StartY=1.08253 StartZ=0 EndX=-1.25 EndY=-1.44e-14 EndZ=0
    g5: LineSegment StartX=-1.25 StartY=-1.44e-14 StartZ=0 EndX=-0.625 EndY=-1.08253 EndZ=0
    g6: Circle CenterX=0 CenterY=0 CenterZ=0 NormalX=0 NormalY=0 NormalZ=1 AngleXU=0 Radius=1.25
  constraints (16):
    c: Coincident(g0,g1)
    c: Coincident(g1,g2)
    c: Coincident(g2,g3)
    c: Coincident(g3,g4)
    c: Coincident(g4,g5)
    c: Coincident(g5,g0)
    c: Equal(g0, g1-g5) x5
    c: PointOnObject(g0,g6)
    c: PointOnObject(g1,g6)
    c: PointOnObject(g2,g6)
    c: PointOnObject(g3,g6)
    c: PointOnObject(g4,g6)
    c: PointOnObject(g5,g6)
    c: Coincident(g6,g-1)
    c: Horizontal(g0)
    c: DistanceX(g4,g1) = 2.5
FEATURE [PartDesign::Pocket] Pocket112
  AllowMultiFace = false
  BaseFeature = -> Revolution001
  Length = 2
  Length2 = 100
  Placement = pos=(0,0,0) rot=(1,0,0;1.5708rad)
  Profile = -> Sketch293
  Refine = true
  Type = 0
FEATURE [PartDesign::Chamfer] Chamfer012
  Angle = 45
  Base = -> Pocket112 [Edge2]
  BaseFeature = -> Pocket112
  ChamferType = 0
  FlipDirection = false
  Placement = pos=(0,0,0) rot=(1,0,0;1.5708rad)
  Size = 0.35
  Size2 = 1
  SupportTransform = false
FEATURE [PartDesign::Chamfer] Chamfer013
  Angle = 45
  Base = -> Chamfer012 [Edge3]
  BaseFeature = -> Chamfer012
  ChamferType = 0
  FlipDirection = false
  Placement = pos=(0,0,0) rot=(1,0,0;1.5708rad)
  Size = 0.75
  Size2 = 1
  SupportTransform = false
FEATURE [PartDesign::Body] Body213  label="Set Screw"
  Group = -> [Sketch292,Revolution001,Sketch293,Pocket112,Chamfer012,Chamfer013]
  Origin = -> Origin303
  Tip = -> Chamfer013
FEATURE [PartDesign::FeatureBase] Clone084
  BaseFeature = -> Body213
FEATURE [PartDesign::Body] Body215  label="Clon1"
  BaseFeature = -> Body213
  Group = -> [Clone084]
  Origin = -> Origin304
  Placement = pos=(0,-3,4) rot=(1,0,0;1.5708rad)
  Tip = -> Clone084
FEATURE [PartDesign::FeatureBase] Clone085
  BaseFeature = -> Body215
  Placement = pos=(0,-4,4) rot=(1,0,0;1.5708rad)
FEATURE [PartDesign::Body] Body216  label="Clon2"
  BaseFeature = -> Body215
  Group = -> [Clone085]
  Origin = -> Origin305
  Placement = pos=(-0.173648,0.984808,17) rot=(0,0,1;0.174533rad)
  Tip = -> Clone085
FEATURE [PartDesign::FeatureBase] Clone086
  BaseFeature = -> Body215
  Placement = pos=(0,-4,4) rot=(1,0,0;1.5708rad)
FEATURE [PartDesign::Body] Body217  label="Clon3"
  BaseFeature = -> Body215
  Group = -> [Clone086]
  Origin = -> Origin306
  Placement = pos=(-1,0,0) rot=(0,0,1;1.5708rad)
  Tip = -> Clone086
FEATURE [PartDesign::FeatureBase] Clone087
  BaseFeature = -> Body216
  Placement = pos=(0,0,17) rot=(0,0,1;0.174533rad)
FEATURE [PartDesign::Body] Body218  label="Clon4"
  BaseFeature = -> Body216
  Group = -> [Clone087]
  Origin = -> Origin307
  Placement = pos=(-1,2e-16,0) rot=(0,0,1;1.5708rad)
  Tip = -> Clone087
FEATURE [App::Part] Part088  label="fastener"
  Group = -> [Body213,Body215,Body216,Body217,Body218]
  Origin = -> Origin301
FEATURE [PartDesign::SubtractivePipe] SubtractivePipe
  AllowMultiFace = false
  AuxilleryCurvelinear = true
  AuxillerySpineTangent = false
  BaseFeature = -> Revolution050
  Binormal = (0,0,0)
  Mode = 2
  Placement = pos=(0,0,0) rot=(1,0,0;1.5708rad)
  Profile = -> Sketch290
  Refine = true
  Spine = -> ShapeBinder001
  SpineTangent = false
  Transformation = 0
  Transition = 0
FEATURE [Sketcher::SketchObject] Sketch291
  ExternalGeometry = -> [SubtractivePipe]
  FullyConstrained = false
  MapMode = 5
  Placement = pos=(0,0,0) rot=(1,0,0;1.5708rad)
  Support = -> [XZ_Plane296]
  sketch-geometry (4):
    g0: Circle CenterX=0 CenterY=4 CenterZ=0 NormalX=0 NormalY=0 NormalZ=1 AngleXU=0 Radius=2
    g1: Circle CenterX=0 CenterY=21 CenterZ=0 NormalX=0 NormalY=0 NormalZ=1 AngleXU=0 Radius=2
    g2: LineSegment StartX=0 StartY=4 StartZ=0 EndX=0 EndY=0 EndZ=0
    g3: LineSegment StartX=0 StartY=21 StartZ=0 EndX=0 EndY=25 EndZ=0
  constraints (9):
    c: PointOnObject(g0,g-2)
    c: PointOnObject(g1,g-2)
    c: Radius(g1) = 2
    c: Equal(g0,g1)
    c: Coincident(g2,g0)
    c: Coincident(g2,g-1)
    c: Coincident(g3,g1)
    c: Vertical(g3)
    c: Equal(g3,g2)
FEATURE [PartDesign::Pocket] Pocket111
  AllowMultiFace = false
  BaseFeature = -> SubtractivePipe
  Length = 10
  Length2 = 100
  Placement = pos=(0,0,0) rot=(1,0,0;1.5708rad)
  Profile = -> Sketch291
  Refine = true
  Reversed = true
  Type = 0
FEATURE [Sketcher::SketchObject] Sketch288
  ExternalGeometry = -> [Pocket111]
  FullyConstrained = false
  MapMode = 5
  Placement = pos=(0,0,0) rot=(0.992433,0.086827,0.086827;1.57839rad)
  Support = -> [DatumPlane]
  sketch-geometry (1):
    g0: Circle CenterX=0 CenterY=21 CenterZ=0 NormalX=0 NormalY=0 NormalZ=1 AngleXU=0 Radius=2
  constraints (3):
    c: PointOnObject(g0,g-2)
    c: Radius(g0) = 2
    c: DistanceY(g0,g-3) = 4
FEATURE [PartDesign::Pocket] Pocket110
  AllowMultiFace = false
  BaseFeature = -> Pocket111
  Length = 10
  Length2 = 100
  Placement = pos=(0,0,0) rot=(1,0,0;1.5708rad)
  Profile = -> Sketch288
  Refine = true
  Reversed = true
  Type = 0
FEATURE [PartDesign::PolarPattern] PolarPattern024
  Angle = 90
  Axis = -> Sketch291 [V_Axis]
  BaseFeature = -> Pocket110
  Occurrences = 3
  Originals = -> [Pocket111,Pocket110]
  Placement = pos=(0,0,0) rot=(1,0,0;1.5708rad)
  Refine = true
FEATURE [PartDesign::Body] Body214  label="Beam coupling"
  Group = -> [Sketch289,Revolution050,ShapeBinder001,Sketch290,SubtractivePipe,Sketch291,Pocket111,DatumPlane,Sketch288,Pocket110,PolarPattern024]
  Origin = -> Origin302
  Tip = -> PolarPattern024
FEATURE [App::Part] Part087  label="Beam coupling "
  Group = -> [Body214,Helix001]
  Origin = -> Origin300
FEATURE [App::Part] Part086  label="Beam-coupling-8mm-5mm-002"
  Group = -> [Part087,Part088]
  Origin = -> Origin299
  Placement = pos=(385,116,105) rot=(0,1,0;-1.5708rad)
FEATURE [PartDesign::Plane] DatumPlane001
  AttachmentOffset = pos=(0,0,0) rot=(0,1,0;0.174533rad)
  Length = 68.686
  MapMode = 5
  Placement = pos=(0,0,0) rot=(0.992433,0.086827,0.086827;1.57839rad)
  ResizeMode = 0
  Support = -> [XZ_Plane305]
  Width = 60.7632
FEATURE [Part::Helix] Helix002  label="Hélice002"
  Angle = 0
  AttacherType = Attacher::AttachEngine3D
  Height = 9.1
  LocalCoord = 0
  Pitch = 1.5
  Placement = pos=(0,0,7.35) rot=(0,0,1;0rad)
  Radius = 10
  Style = 1
FEATURE [PartDesign::ShapeBinder] ShapeBinder002
  Placement = pos=(0,0,7.35) rot=(0,0,1;0rad)
  Support = -> [Helix002]
  TraceSupport = false
FEATURE [Sketcher::SketchObject] Sketch295
  FullyConstrained = false
  MapMode = 5
  Placement = pos=(0,0,0) rot=(1,0,0;1.5708rad)
  Support = -> [XZ_Plane305]
  sketch-geometry (6):
    g0: LineSegment StartX=-9 StartY=25 StartZ=0 EndX=-4 EndY=25 EndZ=0
    g1: LineSegment StartX=-2.5 StartY=8 StartZ=0 EndX=-2.5 EndY=0 EndZ=0
    g2: LineSegment StartX=-2.5 StartY=0 StartZ=0 EndX=-9 EndY=0 EndZ=0
    g3: LineSegment StartX=-9 StartY=0 StartZ=0 EndX=-9 EndY=25 EndZ=0
    g4: LineSegment StartX=-2.5 StartY=8 StartZ=0 EndX=-4 EndY=8 EndZ=0
    g5: LineSegment StartX=-4 StartY=8 StartZ=0 EndX=-4 EndY=25 EndZ=0
  constraints (18):
    c: Coincident(g1,g2)
    c: Coincident(g2,g3)
    c: Coincident(g3,g0)
    c: Horizontal(g0)
    c: Horizontal(g2)
    c: Vertical(g1)
    c: Vertical(g3)
    c: PointOnObject(g1,g-1)
    c: DistanceX(g1,g-1) = 2.5
    c: DistanceX(g2,g-1) = 9
    c: DistanceY(g3,g3) = 25
    c: Horizontal(g4)
    c: Coincident(g5,g4)
    c: Vertical(g5)
    c: Coincident(g1,g4)
    c: Coincident(g0,g5)
    c: DistanceX(g0,g-1) = 4
    c: DistanceY(g5,g5) = 17
FEATURE [PartDesign::Revolution] Revolution052
  AllowMultiFace = false
  Angle = 360
  Axis = (0,-2e-16,1)
  Base = (0,0,0)
  Placement = pos=(0,0,0) rot=(1,0,0;1.5708rad)
  Profile = -> Sketch295
  ReferenceAxis = -> Sketch295 [V_Axis]
  Refine = true
FEATURE [Sketcher::SketchObject] Sketch296
  FullyConstrained = false
  MapMode = 5
  Placement = pos=(0,0,0) rot=(1,0,0;1.5708rad)
  Support = -> [XZ_Plane305]
  sketch-geometry (4):
    g0: LineSegment StartX=0.227639 StartY=16.7629 StartZ=0 EndX=11.1677 EndY=16.7629 EndZ=0
    g1: LineSegment StartX=11.1677 StartY=16.7629 StartZ=0 EndX=11.1677 EndY=16.2629 EndZ=0
    g2: LineSegment StartX=11.1677 StartY=16.2629 StartZ=0 EndX=0.227639 EndY=16.2629 EndZ=0
    g3: LineSegment StartX=0.227639 StartY=16.2629 StartZ=0 EndX=0.227639 EndY=16.7629 EndZ=0
  constraints (9):
    c: Coincident(g0,g1)
    c: Coincident(g1,g2)
    c: Coincident(g2,g3)
    c: Coincident(g3,g0)
    c: Horizontal(g0)
    c: Horizontal(g2)
    c: Vertical(g1)
    c: Vertical(g3)
    c: DistanceY(g1,g1) = 0.5
FEATURE [Sketcher::SketchObject] Sketch298
  FullyConstrained = false
  MapMode = 5
  Placement = pos=(0,0,0) rot=(1,0,0;1.5708rad)
  Support = -> [XZ_Plane306]
  sketch-geometry (4):
    g0: LineSegment StartX=0 StartY=0 StartZ=0 EndX=-2 EndY=0 EndZ=0
    g1: LineSegment StartX=-2 StartY=0 StartZ=0 EndX=-2 EndY=6 EndZ=0
    g2: LineSegment StartX=-2 StartY=6 StartZ=0 EndX=0 EndY=6 EndZ=0
    g3: LineSegment StartX=0 StartY=6 StartZ=0 EndX=0 EndY=0 EndZ=0
  constraints (11):
    c: Coincident(g0,g1)
    c: Coincident(g1,g2)
    c: Coincident(g2,g3)
    c: Coincident(g3,g0)
    c: Horizontal(g0)
    c: Horizontal(g2)
    c: Vertical(g1)
    c: Vertical(g3)
    c: Coincident(g0,g-1)
    c: DistanceX(g2,g2) = 2
    c: DistanceY(g1,g1) = 6
FEATURE [PartDesign::Revolution] Revolution051
  AllowMultiFace = false
  Angle = 360
  Axis = (0,2e-16,1)
  Base = (0,0,0)
  Placement = pos=(0,0,0) rot=(1,0,0;1.5708rad)
  Profile = -> Sketch298
  ReferenceAxis = -> Sketch298 [V_Axis]
  Refine = true
FEATURE [Sketcher::SketchObject] Sketch299
  FullyConstrained = false
  MapMode = 5
  Placement = pos=(0,2.6e-15,6) rot=(0,0,1;3.14159rad)
  Support = -> [Revolution051]
  sketch-geometry (7):
    g0: LineSegment StartX=-0.625 StartY=-1.08253 StartZ=0 EndX=0.625 EndY=-1.08253 EndZ=0
    g1: LineSegment StartX=0.625 StartY=-1.08253 StartZ=0 EndX=1.25 EndY=-1.44e-14 EndZ=0
    g2: LineSegment StartX=1.25 StartY=-1.44e-14 StartZ=0 EndX=0.625 EndY=1.08253 EndZ=0
    g3: LineSegment StartX=0.625 StartY=1.08253 StartZ=0 EndX=-0.625 EndY=1.08253 EndZ=0
    g4: LineSegment StartX=-0.625 StartY=1.08253 StartZ=0 EndX=-1.25 EndY=-1.44e-14 EndZ=0
    g5: LineSegment StartX=-1.25 StartY=-1.44e-14 StartZ=0 EndX=-0.625 EndY=-1.08253 EndZ=0
    g6: Circle CenterX=0 CenterY=0 CenterZ=0 NormalX=0 NormalY=0 NormalZ=1 AngleXU=0 Radius=1.25
  constraints (16):
    c: Coincident(g0,g1)
    c: Coincident(g1,g2)
    c: Coincident(g2,g3)
    c: Coincident(g3,g4)
    c: Coincident(g4,g5)
    c: Coincident(g5,g0)
    c: Equal(g0, g1-g5) x5
    c: PointOnObject(g0,g6)
    c: PointOnObject(g1,g6)
    c: PointOnObject(g2,g6)
    c: PointOnObject(g3,g6)
    c: PointOnObject(g4,g6)
    c: PointOnObject(g5,g6)
    c: Coincident(g6,g-1)
    c: Horizontal(g0)
    c: DistanceX(g4,g1) = 2.5
FEATURE [PartDesign::Pocket] Pocket115
  AllowMultiFace = false
  BaseFeature = -> Revolution051
  Length = 2
  Length2 = 100
  Placement = pos=(0,0,0) rot=(1,0,0;1.5708rad)
  Profile = -> Sketch299
  Refine = true
  Type = 0
FEATURE [PartDesign::Chamfer] Chamfer014
  Angle = 45
  Base = -> Pocket115 [Edge2]
  BaseFeature = -> Pocket115
  ChamferType = 0
  FlipDirection = false
  Placement = pos=(0,0,0) rot=(1,0,0;1.5708rad)
  Size = 0.35
  Size2 = 1
  SupportTransform = false
FEATURE [PartDesign::Chamfer] Chamfer015
  Angle = 45
  Base = -> Chamfer014 [Edge3]
  BaseFeature = -> Chamfer014
  ChamferType = 0
  FlipDirection = false
  Placement = pos=(0,0,0) rot=(1,0,0;1.5708rad)
  Size = 0.75
  Size2 = 1
  SupportTransform = false
FEATURE [PartDesign::Body] Body219  label="Set Screw001"
  Group = -> [Sketch298,Revolution051,Sketch299,Pocket115,Chamfer014,Chamfer015]
  Origin = -> Origin312
  Tip = -> Chamfer015
FEATURE [PartDesign::FeatureBase] Clone088
  BaseFeature = -> Body219
FEATURE [PartDesign::Body] Body221  label="Clon005"
  BaseFeature = -> Body219
  Group = -> [Clone088]
  Origin = -> Origin313
  Placement = pos=(0,-3,4) rot=(1,0,0;1.5708rad)
  Tip = -> Clone088
FEATURE [PartDesign::FeatureBase] Clone089
  BaseFeature = -> Body221
  Placement = pos=(0,-4,4) rot=(1,0,0;1.5708rad)
FEATURE [PartDesign::Body] Body222  label="Clon006"
  BaseFeature = -> Body221
  Group = -> [Clone089]
  Origin = -> Origin314
  Placement = pos=(-0.173648,0.984808,17) rot=(0,0,1;0.174533rad)
  Tip = -> Clone089
FEATURE [PartDesign::FeatureBase] Clone090
  BaseFeature = -> Body221
  Placement = pos=(0,-4,4) rot=(1,0,0;1.5708rad)
FEATURE [PartDesign::Body] Body223  label="Clon007"
  BaseFeature = -> Body221
  Group = -> [Clone090]
  Origin = -> Origin315
  Placement = pos=(-1,0,0) rot=(0,0,1;1.5708rad)
  Tip = -> Clone090
FEATURE [PartDesign::FeatureBase] Clone091
  BaseFeature = -> Body222
  Placement = pos=(0,0,17) rot=(0,0,1;0.174533rad)
FEATURE [PartDesign::Body] Body224  label="Clon008"
  BaseFeature = -> Body222
  Group = -> [Clone091]
  Origin = -> Origin316
  Placement = pos=(-1,2e-16,0) rot=(0,0,1;1.5708rad)
  Tip = -> Clone091
FEATURE [App::Part] Part091  label="fastener001"
  Group = -> [Body219,Body221,Body222,Body223,Body224]
  Origin = -> Origin310
FEATURE [PartDesign::SubtractivePipe] SubtractivePipe001
  AllowMultiFace = false
  AuxilleryCurvelinear = true
  AuxillerySpineTangent = false
  BaseFeature = -> Revolution052
  Binormal = (0,0,0)
  Mode = 2
  Placement = pos=(0,0,0) rot=(1,0,0;1.5708rad)
  Profile = -> Sketch296
  Refine = true
  Spine = -> ShapeBinder002
  SpineTangent = false
  Transformation = 0
  Transition = 0
FEATURE [Sketcher::SketchObject] Sketch297
  ExternalGeometry = -> [SubtractivePipe001]
  FullyConstrained = false
  MapMode = 5
  Placement = pos=(0,0,0) rot=(1,0,0;1.5708rad)
  Support = -> [XZ_Plane305]
  sketch-geometry (4):
    g0: Circle CenterX=0 CenterY=4 CenterZ=0 NormalX=0 NormalY=0 NormalZ=1 AngleXU=0 Radius=2
    g1: Circle CenterX=0 CenterY=21 CenterZ=0 NormalX=0 NormalY=0 NormalZ=1 AngleXU=0 Radius=2
    g2: LineSegment StartX=0 StartY=4 StartZ=0 EndX=0 EndY=0 EndZ=0
    g3: LineSegment StartX=0 StartY=21 StartZ=0 EndX=0 EndY=25 EndZ=0
  constraints (9):
    c: PointOnObject(g0,g-2)
    c: PointOnObject(g1,g-2)
    c: Radius(g1) = 2
    c: Equal(g0,g1)
    c: Coincident(g2,g0)
    c: Coincident(g2,g-1)
    c: Coincident(g3,g1)
    c: Vertical(g3)
    c: Equal(g3,g2)
FEATURE [PartDesign::Pocket] Pocket114
  AllowMultiFace = false
  BaseFeature = -> SubtractivePipe001
  Length = 10
  Length2 = 100
  Placement = pos=(0,0,0) rot=(1,0,0;1.5708rad)
  Profile = -> Sketch297
  Refine = true
  Reversed = true
  Type = 0
FEATURE [Sketcher::SketchObject] Sketch294
  ExternalGeometry = -> [Pocket114]
  FullyConstrained = false
  MapMode = 5
  Placement = pos=(0,0,0) rot=(0.992433,0.086827,0.086827;1.57839rad)
  Support = -> [DatumPlane001]
  sketch-geometry (1):
    g0: Circle CenterX=0 CenterY=21 CenterZ=0 NormalX=0 NormalY=0 NormalZ=1 AngleXU=0 Radius=2
  constraints (3):
    c: PointOnObject(g0,g-2)
    c: Radius(g0) = 2
    c: DistanceY(g0,g-3) = 4
FEATURE [PartDesign::Pocket] Pocket113
  AllowMultiFace = false
  BaseFeature = -> Pocket114
  Length = 10
  Length2 = 100
  Placement = pos=(0,0,0) rot=(1,0,0;1.5708rad)
  Profile = -> Sketch294
  Refine = true
  Reversed = true
  Type = 0
FEATURE [PartDesign::PolarPattern] PolarPattern025
  Angle = 90
  Axis = -> Sketch297 [V_Axis]
  BaseFeature = -> Pocket113
  Occurrences = 3
  Originals = -> [Pocket114,Pocket113]
  Placement = pos=(0,0,0) rot=(1,0,0;1.5708rad)
  Refine = true
FEATURE [PartDesign::Body] Body220  label="Beam coupling001"
  Group = -> [Sketch295,Revolution052,ShapeBinder002,Sketch296,SubtractivePipe001,Sketch297,Pocket114,DatumPlane001,Sketch294,Pocket113,PolarPattern025]
  Origin = -> Origin311
  Tip = -> PolarPattern025
FEATURE [App::Part] Part090  label="Beam coupling 001"
  Group = -> [Body220,Helix002]
  Origin = -> Origin309
FEATURE [App::Part] Part089  label="Beam-coupling-8mm-5mm-001"
  Group = -> [Part090,Part091]
  Origin = -> Origin308
  Placement = pos=(384.965,242,105) rot=(0,1,0;4.72984rad)
FEATURE [Sketcher::SketchObject] Sketch304
  FullyConstrained = false
  MapMode = 3
  Placement = pos=(0,0,0) rot=(1,0,0;3.14159rad)
  sketch-geometry (9):
    g0: LineSegment StartX=-21.15 StartY=21.25 StartZ=0 EndX=21.15 EndY=21.25 EndZ=0
    g1: LineSegment StartX=21.15 StartY=21.25 StartZ=0 EndX=21.15 EndY=-21.15 EndZ=0
    g2: LineSegment StartX=21.15 StartY=-21.15 StartZ=0 EndX=-21.15 EndY=-21.15 EndZ=0
    g3: LineSegment StartX=-21.15 StartY=-21.15 StartZ=0 EndX=-21.15 EndY=21.25 EndZ=0
    g4: Circle CenterX=0 CenterY=0 CenterZ=0 NormalX=0 NormalY=0 NormalZ=1 AngleXU=0 Radius=11
    g5: Circle CenterX=-15.5 CenterY=15.5 CenterZ=0 NormalX=0 NormalY=0 NormalZ=1 AngleXU=0 Radius=1.5
    g6: Circle CenterX=15.5 CenterY=15.5 CenterZ=0 NormalX=0 NormalY=0 NormalZ=1 AngleXU=0 Radius=1.5
    g7: Circle CenterX=-15.5 CenterY=-15.5 CenterZ=0 NormalX=0 NormalY=0 NormalZ=1 AngleXU=0 Radius=1.5
    g8: Circle CenterX=15.5 CenterY=-15.5 CenterZ=0 NormalX=0 NormalY=0 NormalZ=1 AngleXU=0 Radius=1.5
  constraints (18):
    c: Coincident(g0,g1)
    c: Coincident(g1,g2)
    c: Coincident(g2,g3)
    c: Coincident(g3,g0)
    c: Horizontal(g0)
    c: Horizontal(g2)
    c: Vertical(g1)
    c: Vertical(g3)
    c: Coincident(g4,g-1)
    c: DistanceX(g0,g4) = 21.15
    c: DistanceX(g4,g0) = 21.15
    c: DistanceY(g4,g0) = 21.25
    c: DistanceY(g2,g4) = 21.15
    c: Equal(g5,g6)
    c: Equal(g5,g8)
    c: Equal(g5,g7)
    c: Diameter(g5) = 3
    c: Diameter(g4) = 22
FEATURE [PartDesign::Pad] Pad144
  Direction = (0,2e-16,-1)
  Length = 2
  Length2 = 10
  Placement = pos=(0,0,0) rot=(1,0,0;3.14159rad)
  Profile = -> Sketch304
  Type = 0
FEATURE [Sketcher::SketchObject] Sketch305
  FullyConstrained = false
  MapMode = 5
  Placement = pos=(21.15,0,0) rot=(0.57735,-0.57735,0.57735;4.18879rad)
  sketch-geometry (4):
    g0: LineSegment StartX=-21.15 StartY=0 StartZ=0 EndX=21.25 EndY=1.8e-15 EndZ=0
    g1: LineSegment StartX=21.25 StartY=1.8e-15 StartZ=0 EndX=21.25 EndY=60 EndZ=0
    g2: LineSegment StartX=21.25 StartY=60 StartZ=0 EndX=-21.15 EndY=60 EndZ=0
    g3: LineSegment StartX=-21.15 StartY=60 StartZ=0 EndX=-21.15 EndY=0 EndZ=0
  constraints (8):
    c: Coincident(g0,g1)
    c: Coincident(g1,g2)
    c: Coincident(g2,g3)
    c: Coincident(g3,g0)
    c: Horizontal(g2)
    c: Vertical(g1)
    c: Vertical(g3)
    c: DistanceY(g0,g2) = 60
FEATURE [PartDesign::Pad] Pad145
  BaseFeature = -> Pad144
  Direction = (1,-1e-16,-1e-16)
  Length = 2
  Length2 = 10
  Placement = pos=(0,0,0) rot=(1,0,0;3.14159rad)
  Profile = -> Sketch305
  Type = 0
FEATURE [Sketcher::SketchObject] Sketch303
  ExternalGeometry = -> [Pad145]
  FullyConstrained = false
  Placement = pos=(21.15,-4e-15,-3e-15) rot=(0.57735,0.57735,-0.57735;4.18879rad)
  sketch-geometry (8):
    g0: ArcOfCircle CenterX=-12 CenterY=52 CenterZ=0 NormalX=0 NormalY=0 NormalZ=1 AngleXU=0 Radius=2 StartAngle=0 EndAngle=3.14159
    g1: ArcOfCircle CenterX=-12 CenterY=12 CenterZ=0 NormalX=0 NormalY=0 NormalZ=1 AngleXU=0 Radius=2 StartAngle=3.14159 EndAngle=6.28319
    g2: LineSegment StartX=-10 StartY=52 StartZ=0 EndX=-10 EndY=12 EndZ=0
    g3: LineSegment StartX=-14 StartY=12 StartZ=0 EndX=-14 EndY=52 EndZ=0
    g4: ArcOfCircle CenterX=12 CenterY=52 CenterZ=0 NormalX=0 NormalY=0 NormalZ=1 AngleXU=0 Radius=2 StartAngle=0 EndAngle=3.14159
    g5: ArcOfCircle CenterX=12 CenterY=12 CenterZ=0 NormalX=0 NormalY=0 NormalZ=1 AngleXU=0 Radius=2 StartAngle=3.14159 EndAngle=6.28319
    g6: LineSegment StartX=10 StartY=52 StartZ=0 EndX=10 EndY=12 EndZ=0
    g7: LineSegment StartX=14 StartY=12 StartZ=0 EndX=14 EndY=52 EndZ=0
  constraints (16):
    c: Equal(g0,g1)
    c: Diameter(g1) = 4
    c: DistanceY(g0,g-3) = 8
    c: DistanceY(g1,g0) = 40
    c: DistanceX(g0,g-1) = 12
    c: DistanceX(g1,g-1) = 12
    c: Tangent(g1,g2) = 1.5708
    c: Tangent(g1,g3) = 1.5708
    c: Tangent(g0,g3) = 1.5708
    c: Tangent(g0,g2) = 1.5708
    c: Equal(g4,g5)
    c: Diameter(g5) = 4
    c: Tangent(g5,g6) = -1.5708
    c: Tangent(g5,g7) = -1.5708
    c: Tangent(g4,g7) = -1.5708
    c: Tangent(g4,g6) = -1.5708
FEATURE [PartDesign::Pocket] Pocket117
  BaseFeature = -> Pad145
  Length = 5
  Length2 = 5
  Placement = pos=(0,0,0) rot=(1,0,0;3.14159rad)
  Profile = -> Sketch303
  Type = 0
FEATURE [Sketcher::SketchObject] Sketch306
  FullyConstrained = true
  MapMode = 5
  Support = -> [XY_Plane316]
  sketch-geometry (3):
    g0: LineSegment StartX=0 StartY=0 StartZ=0 EndX=6 EndY=0 EndZ=0
    g1: LineSegment StartX=0 StartY=0 StartZ=0 EndX=0 EndY=6 EndZ=0
    g2: LineSegment StartX=0 StartY=6 StartZ=0 EndX=6 EndY=0 EndZ=0
  constraints (8):
    c: Coincident(g0,g-1)
    c: PointOnObject(g0,g-1)
    c: Coincident(g1,g0)
    c: PointOnObject(g1,g-2)
    c: Coincident(g2,g1)
    c: Coincident(g2,g0)
    c: DistanceX(g0,g0) = 6
    c: DistanceY(g0,g1) = 6
FEATURE [PartDesign::Pad] Pad143
  Direction = (0,0,1)
  Length = 2
  Length2 = 10
  Profile = -> Sketch306
  Type = 0
FEATURE [PartDesign::Body] Body226
  Group = -> [Sketch306,Pad143]
  Origin = -> Origin322
  Tip = -> Pad143
FEATURE [App::Part] Part093
  Group = -> [Body226]
  Origin = -> Origin319
  Placement = pos=(-2,21.15,-21.13) rot=(0.57735,-0.57735,0.57735;2.0944rad)
FEATURE [Sketcher::SketchObject] Sketch307
  FullyConstrained = true
  MapMode = 5
  Support = -> [XY_Plane318]
  sketch-geometry (3):
    g0: LineSegment StartX=0 StartY=0 StartZ=0 EndX=6 EndY=0 EndZ=0
    g1: LineSegment StartX=0 StartY=0 StartZ=0 EndX=0 EndY=6 EndZ=0
    g2: LineSegment StartX=0 StartY=6 StartZ=0 EndX=6 EndY=0 EndZ=0
  constraints (8):
    c: Coincident(g0,g-1)
    c: PointOnObject(g0,g-1)
    c: Coincident(g1,g0)
    c: PointOnObject(g1,g-2)
    c: Coincident(g2,g1)
    c: Coincident(g2,g0)
    c: DistanceX(g0,g0) = 6
    c: DistanceY(g0,g1) = 6
FEATURE [PartDesign::Pad] Pad146
  Direction = (0,0,1)
  Length = 2
  Length2 = 10
  Profile = -> Sketch307
  Type = 0
FEATURE [PartDesign::Body] Body228
  Group = -> [Sketch307,Pad146]
  Origin = -> Origin324
  Tip = -> Pad146
FEATURE [App::Part] Part095
  Group = -> [Body228]
  Origin = -> Origin323
  Placement = pos=(-2,-19.24,-21.13) rot=(0.57735,-0.57735,0.57735;2.0944rad)
FEATURE [PartDesign::Chamfer] Chamfer016
  Angle = 45
  Base = -> Pocket117 [Edge1]
  BaseFeature = -> Pocket117
  ChamferType = 0
  FlipDirection = false
  Placement = pos=(0,0,0) rot=(1,0,0;3.14159rad)
  Size = 2
  Size2 = 1
  SupportTransform = false
FEATURE [PartDesign::Chamfer] Chamfer017
  Angle = 45
  Base = -> Chamfer016 [Edge30]
  BaseFeature = -> Chamfer016
  ChamferType = 0
  FlipDirection = false
  Placement = pos=(0,0,0) rot=(1,0,0;3.14159rad)
  Size = 2
  Size2 = 1
  SupportTransform = false
FEATURE [Sketcher::SketchObject] Sketch309
  FullyConstrained = false
  MapMode = 3
  Placement = pos=(0,0,0) rot=(1,0,0;3.14159rad)
  sketch-geometry (9):
    g0: LineSegment StartX=-21.15 StartY=21.25 StartZ=0 EndX=21.15 EndY=21.25 EndZ=0
    g1: LineSegment StartX=21.15 StartY=21.25 StartZ=0 EndX=21.15 EndY=-21.15 EndZ=0
    g2: LineSegment StartX=21.15 StartY=-21.15 StartZ=0 EndX=-21.15 EndY=-21.15 EndZ=0
    g3: LineSegment StartX=-21.15 StartY=-21.15 StartZ=0 EndX=-21.15 EndY=21.25 EndZ=0
    g4: Circle CenterX=0 CenterY=0 CenterZ=0 NormalX=0 NormalY=0 NormalZ=1 AngleXU=0 Radius=11
    g5: Circle CenterX=-15.5 CenterY=15.5 CenterZ=0 NormalX=0 NormalY=0 NormalZ=1 AngleXU=0 Radius=1.5
    g6: Circle CenterX=15.5 CenterY=15.5 CenterZ=0 NormalX=0 NormalY=0 NormalZ=1 AngleXU=0 Radius=1.5
    g7: Circle CenterX=-15.5 CenterY=-15.5 CenterZ=0 NormalX=0 NormalY=0 NormalZ=1 AngleXU=0 Radius=1.5
    g8: Circle CenterX=15.5 CenterY=-15.5 CenterZ=0 NormalX=0 NormalY=0 NormalZ=1 AngleXU=0 Radius=1.5
  constraints (18):
    c: Coincident(g0,g1)
    c: Coincident(g1,g2)
    c: Coincident(g2,g3)
    c: Coincident(g3,g0)
    c: Horizontal(g0)
    c: Horizontal(g2)
    c: Vertical(g1)
    c: Vertical(g3)
    c: Coincident(g4,g-1)
    c: DistanceX(g0,g4) = 21.15
    c: DistanceX(g4,g0) = 21.15
    c: DistanceY(g4,g0) = 21.25
    c: DistanceY(g2,g4) = 21.15
    c: Equal(g5,g6)
    c: Equal(g5,g8)
    c: Equal(g5,g7)
    c: Diameter(g5) = 3
    c: Diameter(g4) = 22
FEATURE [PartDesign::Pad] Pad148
  Direction = (0,2e-16,-1)
  Length = 2
  Length2 = 10
  Placement = pos=(0,0,0) rot=(1,0,0;3.14159rad)
  Profile = -> Sketch309
  Type = 0
FEATURE [Sketcher::SketchObject] Sketch310
  FullyConstrained = false
  MapMode = 5
  Placement = pos=(21.15,0,0) rot=(0.57735,-0.57735,0.57735;4.18879rad)
  sketch-geometry (4):
    g0: LineSegment StartX=-21.15 StartY=0 StartZ=0 EndX=21.25 EndY=1.8e-15 EndZ=0
    g1: LineSegment StartX=21.25 StartY=1.8e-15 StartZ=0 EndX=21.25 EndY=60 EndZ=0
    g2: LineSegment StartX=21.25 StartY=60 StartZ=0 EndX=-21.15 EndY=60 EndZ=0
    g3: LineSegment StartX=-21.15 StartY=60 StartZ=0 EndX=-21.15 EndY=0 EndZ=0
  constraints (8):
    c: Coincident(g0,g1)
    c: Coincident(g1,g2)
    c: Coincident(g2,g3)
    c: Coincident(g3,g0)
    c: Horizontal(g2)
    c: Vertical(g1)
    c: Vertical(g3)
    c: DistanceY(g0,g2) = 60
FEATURE [PartDesign::Pad] Pad149
  BaseFeature = -> Pad148
  Direction = (1,-1e-16,-1e-16)
  Length = 2
  Length2 = 10
  Placement = pos=(0,0,0) rot=(1,0,0;3.14159rad)
  Profile = -> Sketch310
  Type = 0
FEATURE [Sketcher::SketchObject] Sketch308
  ExternalGeometry = -> [Pad149]
  FullyConstrained = false
  Placement = pos=(21.15,-4e-15,-3e-15) rot=(0.57735,0.57735,-0.57735;4.18879rad)
  sketch-geometry (8):
    g0: ArcOfCircle CenterX=-12 CenterY=52 CenterZ=0 NormalX=0 NormalY=0 NormalZ=1 AngleXU=0 Radius=2 StartAngle=0 EndAngle=3.14159
    g1: ArcOfCircle CenterX=-12 CenterY=12 CenterZ=0 NormalX=0 NormalY=0 NormalZ=1 AngleXU=0 Radius=2 StartAngle=3.14159 EndAngle=6.28319
    g2: LineSegment StartX=-10 StartY=52 StartZ=0 EndX=-10 EndY=12 EndZ=0
    g3: LineSegment StartX=-14 StartY=12 StartZ=0 EndX=-14 EndY=52 EndZ=0
    g4: ArcOfCircle CenterX=12 CenterY=52 CenterZ=0 NormalX=0 NormalY=0 NormalZ=1 AngleXU=0 Radius=2 StartAngle=0 EndAngle=3.14159
    g5: ArcOfCircle CenterX=12 CenterY=12 CenterZ=0 NormalX=0 NormalY=0 NormalZ=1 AngleXU=0 Radius=2 StartAngle=3.14159 EndAngle=6.28319
    g6: LineSegment StartX=10 StartY=52 StartZ=0 EndX=10 EndY=12 EndZ=0
    g7: LineSegment StartX=14 StartY=12 StartZ=0 EndX=14 EndY=52 EndZ=0
  constraints (16):
    c: Equal(g0,g1)
    c: Diameter(g1) = 4
    c: DistanceY(g0,g-3) = 8
    c: DistanceY(g1,g0) = 40
    c: DistanceX(g0,g-1) = 12
    c: DistanceX(g1,g-1) = 12
    c: Tangent(g1,g2) = 1.5708
    c: Tangent(g1,g3) = 1.5708
    c: Tangent(g0,g3) = 1.5708
    c: Tangent(g0,g2) = 1.5708
    c: Equal(g4,g5)
    c: Diameter(g5) = 4
    c: Tangent(g5,g6) = -1.5708
    c: Tangent(g5,g7) = -1.5708
    c: Tangent(g4,g7) = -1.5708
    c: Tangent(g4,g6) = -1.5708
FEATURE [PartDesign::Pocket] Pocket118
  BaseFeature = -> Pad149
  Length = 5
  Length2 = 5
  Placement = pos=(0,0,0) rot=(1,0,0;3.14159rad)
  Profile = -> Sketch308
  Type = 0
FEATURE [PartDesign::Chamfer] Chamfer018
  Angle = 45
  Base = -> Pocket118 [Edge1]
  BaseFeature = -> Pocket118
  ChamferType = 0
  FlipDirection = false
  Placement = pos=(0,0,0) rot=(1,0,0;3.14159rad)
  Size = 2
  Size2 = 1
  SupportTransform = false
FEATURE [PartDesign::Chamfer] Chamfer019
  Angle = 45
  Base = -> Chamfer018 [Edge30]
  BaseFeature = -> Chamfer018
  ChamferType = 0
  FlipDirection = false
  Placement = pos=(0,0,0) rot=(1,0,0;3.14159rad)
  Size = 2
  Size2 = 1
  SupportTransform = false
FEATURE [PartDesign::Body] Body230
  Group = -> [Sketch309,Pad148,Sketch310,Pad149,Sketch308,Pocket118,Chamfer018,Chamfer019]
  Origin = -> Origin327
  Tip = -> Chamfer019
FEATURE [App::Part] Part097  label="soporteNEMA019"
  Group = -> [Body230]
  Origin = -> Origin326
  Placement = pos=(0,0,0) rot=(0,1,0;1.5708rad)
  expr: .Placement.Rotation.Angle = 90°
FEATURE [Sketcher::SketchObject] Sketch311
  FullyConstrained = true
  MapMode = 5
  Support = -> [XY_Plane322]
  sketch-geometry (3):
    g0: LineSegment StartX=0 StartY=0 StartZ=0 EndX=6 EndY=0 EndZ=0
    g1: LineSegment StartX=0 StartY=0 StartZ=0 EndX=0 EndY=6 EndZ=0
    g2: LineSegment StartX=0 StartY=6 StartZ=0 EndX=6 EndY=0 EndZ=0
  constraints (8):
    c: Coincident(g0,g-1)
    c: PointOnObject(g0,g-1)
    c: Coincident(g1,g0)
    c: PointOnObject(g1,g-2)
    c: Coincident(g2,g1)
    c: Coincident(g2,g0)
    c: DistanceX(g0,g0) = 6
    c: DistanceY(g0,g1) = 6
FEATURE [PartDesign::Pad] Pad147
  Direction = (0,0,1)
  Length = 2
  Length2 = 10
  Profile = -> Sketch311
  Type = 0
FEATURE [PartDesign::Body] Body229
  Group = -> [Sketch311,Pad147]
  Origin = -> Origin328
  Tip = -> Pad147
FEATURE [App::Part] Part096
  Group = -> [Body229]
  Origin = -> Origin325
  Placement = pos=(-2,21.15,-21.13) rot=(0.57735,-0.57735,0.57735;2.0944rad)
FEATURE [Sketcher::SketchObject] Sketch312
  FullyConstrained = true
  MapMode = 5
  Support = -> [XY_Plane324]
  sketch-geometry (3):
    g0: LineSegment StartX=0 StartY=0 StartZ=0 EndX=6 EndY=0 EndZ=0
    g1: LineSegment StartX=0 StartY=0 StartZ=0 EndX=0 EndY=6 EndZ=0
    g2: LineSegment StartX=0 StartY=6 StartZ=0 EndX=6 EndY=0 EndZ=0
  constraints (8):
    c: Coincident(g0,g-1)
    c: PointOnObject(g0,g-1)
    c: Coincident(g1,g0)
    c: PointOnObject(g1,g-2)
    c: Coincident(g2,g1)
    c: Coincident(g2,g0)
    c: DistanceX(g0,g0) = 6
    c: DistanceY(g0,g1) = 6
FEATURE [PartDesign::Pad] Pad150
  Direction = (0,0,1)
  Length = 2
  Length2 = 10
  Profile = -> Sketch312
  Type = 0
FEATURE [PartDesign::Body] Body231
  Group = -> [Sketch312,Pad150]
  Origin = -> Origin330
  Tip = -> Pad150
FEATURE [App::Part] Part098
  Group = -> [Body231]
  Origin = -> Origin329
  Placement = pos=(-2,-19.24,-21.13) rot=(0.57735,-0.57735,0.57735;2.0944rad)
FEATURE [App::LinkGroup] LinkGroup013  label="SoporteNEMA018-002"
  ElementList = -> [Part097,Part096,Part098]
  LinkMode = 0
  Placement = pos=(400,247,106) rot=(0,0,1;0rad)
FEATURE [App::LinkGroup] LinkGroup014  label="ruedas"
  ElementList = -> [Part037,Part067,Part069]
  LinkMode = 0
FEATURE [App::LinkGroup] LinkGroup016  label="acoples-ejes-motores"
  ElementList = -> [Part086,Part089]
  LinkMode = 0
  Placement = pos=(-1.52588e-05,4.00001,3.8147e-06) rot=(0,0,1;0rad)
FEATURE [PartDesign::ShapeBinder] CopyFillet054
  TraceSupport = false
FEATURE [Sketcher::SketchObject] Sketch313
  FullyConstrained = true
  MapMode = 5
  Placement = pos=(0,-3.4,0) rot=(1,0,0;1.5708rad)
  Support = -> [CopyFillet054]
FEATURE [Sketcher::SketchObject] Sketch314
  FullyConstrained = true
  MapMode = 5
  Placement = pos=(0,0,0) rot=(1,0,0;1.5708rad)
  Support = -> [XZ_Plane315]
FEATURE [PartDesign::ShapeBinder] ReferencePad053
  Placement = pos=(0,0,0) rot=(0.57735,0.57735,0.57735;2.0944rad)
  Support = -> [Pad053]
  TraceSupport = false
FEATURE [Sketcher::SketchObject] Sketch315
  FullyConstrained = true
  MapMode = 5
  Placement = pos=(0,0,0) rot=(0.57735,0.57735,-0.57735;4.18879rad)
  Support = -> [ReferencePad053]
FEATURE [Sketcher::SketchObject] Sketch316
  FullyConstrained = true
  MapMode = 5
  Placement = pos=(0,0,0) rot=(0.57735,0.57735,0.57735;2.0944rad)
  Support = -> [YZ_Plane315]
FEATURE [PartDesign::Body] Body227
  Group = -> [Sketch304,Pad144,Sketch305,Pad145,Sketch303,Pocket117,Chamfer016,Chamfer017,CopyFillet054,Sketch313,Sketch314,ReferencePad053,Sketch315,Sketch316]
  Origin = -> Origin321
  Tip = -> Chamfer017
FEATURE [App::Part] Part094  label="soporteNEMA018"
  Group = -> [Body227]
  Origin = -> Origin320
  Placement = pos=(0,0,0) rot=(0,1,0;1.5708rad)
  expr: .Placement.Rotation.Angle = 90°
FEATURE [App::LinkGroup] LinkGroup012  label="SoporteNEMA017-001"
  ElementList = -> [Part094,Part093,Part095]
  LinkMode = 0
  Placement = pos=(400,121,106) rot=(0,0,1;0rad)
FEATURE [App::LinkGroup] LinkGroup015  label="bases"
  ElementList = -> [Part066,LinkGroup012,LinkGroup013]
  LinkMode = 0
FEATURE [Sketcher::SketchObject] Sketch317
  FullyConstrained = true
  MapMode = 5
  Placement = pos=(0,0,0) rot=(1,0,0;1.5708rad)
  Support = -> [XZ_Plane328]
  sketch-geometry (1):
    g0: Circle CenterX=5.4 CenterY=4.4 CenterZ=0 NormalX=0 NormalY=0 NormalZ=1 AngleXU=0 Radius=0.4
  constraints (3):
    c: Diameter(g0) = 0.8
    c: DistanceY(g0) = 4.4
    c: DistanceX(g0) = 5.4
FEATURE [PartDesign::AdditiveHelix] AdditiveHelix
  Angle = 0
  Axis = (0,-2e-16,1)
  Base = (0,0,0)
  HasBeenEdited = true
  Height = 17.3
  LeftHanded = false
  Mode = 2
  Outside = false
  Pitch = 2.1625
  Placement = pos=(0,0,0) rot=(1,0,0;1.5708rad)
  Profile = -> Sketch317
  ReferenceAxis = -> Sketch317 [V_Axis]
  Turns = 3
FEATURE [PartDesign::Body] Body234  label="Spring"
  Group = -> [Sketch317,AdditiveHelix]
  Origin = -> Origin334
  Tip = -> AdditiveHelix
FEATURE [Sketcher::SketchObject] Sketch318
  FullyConstrained = true
  MapMode = 5
  Placement = pos=(0,0,0) rot=(1,0,0;1.5708rad)
  Support = -> [XZ_Plane326]
  sketch-geometry (6):
    g0: LineSegment StartX=0 StartY=0 StartZ=0 EndX=0 EndY=15 EndZ=0
    g1: LineSegment StartX=0 StartY=15 StartZ=0 EndX=-5 EndY=15 EndZ=0
    g2: LineSegment StartX=-5 StartY=15 StartZ=0 EndX=-5 EndY=4 EndZ=0
    g3: LineSegment StartX=-5 StartY=4 StartZ=0 EndX=-11 EndY=4 EndZ=0
    g4: LineSegment StartX=-11 StartY=4 StartZ=0 EndX=-11 EndY=0 EndZ=0
    g5: LineSegment StartX=-11 StartY=0 StartZ=0 EndX=0 EndY=0 EndZ=0
  constraints (17):
    c: Coincident(g-1,g0)
    c: Coincident(g0,g1)
    c: Coincident(g1,g2)
    c: Coincident(g2,g3)
    c: Horizontal(g3)
    c: Coincident(g3,g4)
    c: Vertical(g4)
    c: Coincident(g4,g5)
    c: Coincident(g5,g0)
    c: Horizontal(g5)
    c: Horizontal(g1)
    c: Vertical(g2)
    c: Vertical(g0)
    c: DistanceY(g0,g0) = 15
    c: DistanceY(g4,g4) = 4
    c: DistanceX(g1,g1) = 5
    c: DistanceX(g5,g5) = 11
FEATURE [PartDesign::Revolution] Revolution053
  Angle = 360
  Axis = (0,2e-16,1)
  Base = (0,0,0)
  Placement = pos=(0,0,0) rot=(1,0,0;1.5708rad)
  Profile = -> Sketch318
  ReferenceAxis = -> Sketch318 [V_Axis]
FEATURE [Sketcher::SketchObject] Sketch319
  FullyConstrained = true
  MapMode = 5
  Placement = pos=(0,1.8e-15,4) rot=(0,0,1;3.14159rad)
  Support = -> [Revolution053]
  sketch-geometry (1):
    g0: Circle CenterX=8 CenterY=0 CenterZ=0 NormalX=0 NormalY=0 NormalZ=1 AngleXU=0 Radius=1.7
  constraints (3):
    c: PointOnObject(g0,g-1)
    c: Diameter(g0) = 3.4
    c: DistanceX(g0) = 8
FEATURE [PartDesign::Pocket] Pocket119
  BaseFeature = -> Revolution053
  Length = 5
  Length2 = 5
  Placement = pos=(0,0,0) rot=(1,0,0;1.5708rad)
  Profile = -> Sketch319
  Type = 2
FEATURE [PartDesign::Chamfer] Chamfer020
  Angle = 45
  Base = -> Pocket119 [Edge5]
  BaseFeature = -> Pocket119
  ChamferType = 0
  FlipDirection = false
  Placement = pos=(0,0,0) rot=(1,0,0;1.5708rad)
  Size = 0.25
  Size2 = 1
  SupportTransform = false
FEATURE [PartDesign::PolarPattern] PolarPattern026
  Angle = 360
  Axis = -> Sketch319 [N_Axis]
  BaseFeature = -> Chamfer020
  Occurrences = 3
  Originals = -> [Pocket119,Chamfer020]
  Placement = pos=(0,0,0) rot=(1,0,0;1.5708rad)
FEATURE [Sketcher::SketchObject] Sketch320
  FullyConstrained = true
  MapMode = 5
  Placement = pos=(0,6.6e-15,15) rot=(0,0,1;3.14159rad)
  Support = -> [PolarPattern026]
  sketch-geometry (1):
    g0: Circle CenterX=0 CenterY=0 CenterZ=0 NormalX=0 NormalY=0 NormalZ=1 AngleXU=0 Radius=3.25
  constraints (2):
    c: Coincident(g0,g-1)
    c: Diameter(g0) = 6.5
FEATURE [PartDesign::Pocket] Pocket120
  BaseFeature = -> PolarPattern026
  Length = 5
  Length2 = 5
  Placement = pos=(0,0,0) rot=(1,0,0;1.5708rad)
  Profile = -> Sketch320
  Type = 2
FEATURE [Sketcher::SketchObject] Sketch321
  ExternalGeometry = -> [Pocket120]
  FullyConstrained = true
  MapMode = 5
  Placement = pos=(0,0,0) rot=(0.57735,0.57735,0.57735;2.0944rad)
  Support = -> [YZ_Plane326]
  sketch-geometry (5):
    g0: LineSegment StartX=-1.7 StartY=11 StartZ=0 EndX=-1.7 EndY=15 EndZ=0
    g1: LineSegment StartX=-1.7 StartY=15 StartZ=0 EndX=1.7 EndY=15 EndZ=0
    g2: LineSegment StartX=1.7 StartY=15 StartZ=0 EndX=1.7 EndY=11 EndZ=0
    g3: LineSegment StartX=1.7 StartY=11 StartZ=0 EndX=-1.7 EndY=11 EndZ=0
    g4: GeomPoint X=0 Y=13 Z=0
  constraints (13):
    c: Coincident(g0,g1)
    c: Coincident(g1,g2)
    c: Coincident(g2,g3)
    c: Coincident(g3,g0)
    c: Horizontal(g1)
    c: Horizontal(g3)
    c: Vertical(g0)
    c: Vertical(g2)
    c: Symmetric(g1,g0,g4)
    c: PointOnObject(g4,g-2)
    c: PointOnObject(g1,g-3)
    c: DistanceX(g3,g3) = 3.4
    c: DistanceY(g2,g2) = 4
FEATURE [PartDesign::Pocket] Pocket121
  BaseFeature = -> Pocket120
  Length = 5
  Length2 = 5
  Midplane = true
  Placement = pos=(0,0,0) rot=(1,0,0;1.5708rad)
  Profile = -> Sketch321
  Type = 1
FEATURE [Sketcher::SketchObject] Sketch322
  FullyConstrained = true
  MapMode = 5
  Placement = pos=(0,0,0) rot=(1,0,0;1.5708rad)
  Support = -> [XZ_Plane327]
  sketch-geometry (6):
    g0: LineSegment StartX=0 StartY=11 StartZ=0 EndX=0 EndY=26 EndZ=0
    g1: LineSegment StartX=0 StartY=26 StartZ=0 EndX=-7 EndY=26 EndZ=0
    g2: LineSegment StartX=-7 StartY=26 StartZ=0 EndX=-7 EndY=22 EndZ=0
    g3: LineSegment StartX=-7 StartY=22 StartZ=0 EndX=-5 EndY=22 EndZ=0
    g4: LineSegment StartX=-5 StartY=22 StartZ=0 EndX=-5 EndY=11 EndZ=0
    g5: LineSegment StartX=-5 StartY=11 StartZ=0 EndX=0 EndY=11 EndZ=0
  constraints (18):
    c: PointOnObject(g0,g-2)
    c: Vertical(g0)
    c: Coincident(g0,g1)
    c: Horizontal(g1)
    c: Coincident(g1,g2)
    c: Vertical(g2)
    c: Coincident(g2,g3)
    c: Horizontal(g3)
    c: Coincident(g3,g4)
    c: Vertical(g4)
    c: Coincident(g4,g5)
    c: Coincident(g5,g0)
    c: Horizontal(g5)
    c: DistanceX(g1,g1) = 7
    c: DistanceX(g5,g5) = 5
    c: DistanceY(g2,g2) = 4
    c: DistanceY(g0,g0) = 15
    c: DistanceY(g0) = 11
FEATURE [PartDesign::Revolution] Revolution054
  Angle = 360
  Axis = (0,2e-16,1)
  Base = (0,0,0)
  Placement = pos=(0,0,0) rot=(1,0,0;1.5708rad)
  Profile = -> Sketch322
  ReferenceAxis = -> Sketch322 [V_Axis]
FEATURE [Sketcher::SketchObject] Sketch323
  FullyConstrained = true
  MapMode = 5
  Placement = pos=(0,1.14e-14,26) rot=(0,0,1;3.14159rad)
  Support = -> [Revolution054]
  sketch-geometry (1):
    g0: Circle CenterX=0 CenterY=0 CenterZ=0 NormalX=0 NormalY=0 NormalZ=1 AngleXU=0 Radius=3.25
  constraints (2):
    c: Coincident(g0,g-1)
    c: Diameter(g0) = 6.5
FEATURE [PartDesign::Pocket] Pocket122
  BaseFeature = -> Revolution054
  Length = 5
  Length2 = 5
  Placement = pos=(0,0,0) rot=(1,0,0;1.5708rad)
  Profile = -> Sketch323
  Type = 2
FEATURE [Sketcher::SketchObject] Sketch324
  ExternalGeometry = -> [Pocket122]
  FullyConstrained = true
  MapMode = 5
  Placement = pos=(0,0,0) rot=(1,0,0;1.5708rad)
  Support = -> [XZ_Plane327]
  sketch-geometry (5):
    g0: LineSegment StartX=-4.75 StartY=15 StartZ=0 EndX=-4.75 EndY=11 EndZ=0
    g1: LineSegment StartX=-4.75 StartY=11 StartZ=0 EndX=4.75 EndY=11 EndZ=0
    g2: LineSegment StartX=4.75 StartY=11 StartZ=0 EndX=4.75 EndY=15 EndZ=0
    g3: LineSegment StartX=4.75 StartY=15 StartZ=0 EndX=-4.75 EndY=15 EndZ=0
    g4: GeomPoint X=0 Y=13 Z=0
  constraints (13):
    c: Coincident(g0,g1)
    c: Coincident(g1,g2)
    c: Coincident(g2,g3)
    c: Coincident(g3,g0)
    c: Horizontal(g1)
    c: Horizontal(g3)
    c: Vertical(g0)
    c: Vertical(g2)
    c: Symmetric(g1,g0,g4)
    c: DistanceX(g1,g1) = 9.5
    c: DistanceY(g2,g2) = 4
    c: PointOnObject(g1,g-3)
    c: PointOnObject(g4,g-2)
FEATURE [PartDesign::Pocket] Pocket123
  BaseFeature = -> Pocket122
  Length = 5
  Length2 = 5
  Midplane = true
  Placement = pos=(0,0,0) rot=(1,0,0;1.5708rad)
  Profile = -> Sketch324
  Type = 1
FEATURE [Sketcher::SketchObject] Sketch325  label="ISO 2904"
  FullyConstrained = true
  MapMode = 5
  Placement = pos=(0,0,0) rot=(1,0,0;1.5708rad)
  Support = -> [XZ_Plane326]
  sketch-geometry (8):
    g0: LineSegment StartX=6.04904 StartY=0.75 StartZ=0 EndX=3.25 EndY=0 EndZ=0
    g1: LineSegment StartX=3.25 StartY=0 StartZ=0 EndX=6.04904 EndY=-0.75 EndZ=0
    g2: LineSegment StartX=6.04904 StartY=-0.75 StartZ=0 EndX=3.25 EndY=-1.5 EndZ=0
    g3: LineSegment StartX=3.25 StartY=-1.5 StartZ=0 EndX=6.04904 EndY=-2.25 EndZ=0
    g4: LineSegment StartX=3.25 StartY=0 StartZ=0 EndX=3.25 EndY=-1.5 EndZ=0
    g5: LineSegment StartX=3.25 StartY=-1.5 StartZ=0 EndX=4.15 EndY=-1.25885 EndZ=0
    g6: LineSegment StartX=4.15 StartY=-1.25885 StartZ=0 EndX=4.15 EndY=-0.241154 EndZ=0
    g7: LineSegment StartX=4.15 StartY=-0.241154 StartZ=0 EndX=3.25 EndY=0 EndZ=0
  constraints (23):
    c: PointOnObject(g0,g-1)
    c: Coincident(g0,g1)
    c: Coincident(g1,g2)
    c: Coincident(g2,g3)
    c: Vertical(g1,g0)
    c: Vertical(g0,g3)
    c: Vertical(g2,g0)
    c: Parallel(g0,g2)
    c: Parallel(g1,g3)
    c: Angle(g3,g2) = 0.523599
    c: Angle(g0,g-1) = 2.87979
    c: Coincident(g0,g4)
    c: Coincident(g4,g2)
    c: Coincident(g4,g5)
    c: PointOnObject(g5,g2)
    c: Coincident(g5,g6)
    c: PointOnObject(g6,g1)
    c: Vertical(g6)
    c: Coincident(g6,g7)
    c: Coincident(g7,g4)
    c: DistanceX(g4) = 3.25
    c: DistanceX(g6) = 4.15
    c: DistanceY(g3,g1) = 1.5
FEATURE [Sketcher::SketchObject] Sketch327
  FullyConstrained = true
  MapMode = 5
  Placement = pos=(0,0,0) rot=(1,0,0;1.5708rad)
  Support = -> [XZ_Plane327]
  sketch-geometry (8):
    g0: LineSegment StartX=6.04904 StartY=0.75 StartZ=0 EndX=3.25 EndY=-1e-16 EndZ=0
    g1: LineSegment StartX=3.25 StartY=-1e-16 StartZ=0 EndX=6.04904 EndY=-0.75 EndZ=0
    g2: LineSegment StartX=6.04904 StartY=-0.75 StartZ=0 EndX=3.25 EndY=-1.5 EndZ=0
    g3: LineSegment StartX=3.25 StartY=-1.5 StartZ=0 EndX=6.04904 EndY=-2.25 EndZ=0
    g4: LineSegment StartX=3.25 StartY=-1e-16 StartZ=0 EndX=3.25 EndY=-1.5 EndZ=0
    g5: LineSegment StartX=3.25 StartY=-1.5 StartZ=0 EndX=4.15 EndY=-1.25885 EndZ=0
    g6: LineSegment StartX=4.15 StartY=-1.25885 StartZ=0 EndX=4.15 EndY=-0.241154 EndZ=0
    g7: LineSegment StartX=4.15 StartY=-0.241154 StartZ=0 EndX=3.25 EndY=-1e-16 EndZ=0
  constraints (23):
    c: PointOnObject(g0,g-1)
    c: Coincident(g0,g1)
    c: Coincident(g1,g2)
    c: Coincident(g2,g3)
    c: Vertical(g3,g1)
    c: Vertical(g1,g0)
    c: Vertical(g0,g2)
    c: Parallel(g3,g1)
    c: Parallel(g2,g0)
    c: Angle(g3,g2) = 0.523599
    c: Angle(g0,g-1) = 2.87979
    c: Coincident(g0,g4)
    c: Coincident(g4,g2)
    c: Coincident(g4,g5)
    c: PointOnObject(g5,g2)
    c: Coincident(g5,g6)
    c: PointOnObject(g6,g1)
    c: Coincident(g6,g7)
    c: Coincident(g7,g4)
    c: Vertical(g6)
    c: DistanceX(g4) = 3.25
    c: DistanceX(g6) = 4.15
    c: DistanceY(g3,g1) = 1.5
FEATURE [Sketcher::SketchObject] Sketch331
  FullyConstrained = false
  MapMode = 5
  Support = -> [XY_Plane329]
  sketch-geometry (7):
    g0: LineSegment StartX=1.45322 StartY=-2.69828 StartZ=0 EndX=3.06339 EndY=-0.0906102 EndZ=0
    g1: LineSegment StartX=3.06339 StartY=-0.0906102 StartZ=0 EndX=1.61017 EndY=2.60767 EndZ=0
    g2: LineSegment StartX=1.61017 StartY=2.60767 StartZ=0 EndX=-1.45322 EndY=2.69828 EndZ=0
    g3: LineSegment StartX=-1.45322 StartY=2.69828 StartZ=0 EndX=-3.06339 EndY=0.0906102 EndZ=0
    g4: LineSegment StartX=-3.06339 StartY=0.0906102 StartZ=0 EndX=-1.61017 EndY=-2.60767 EndZ=0
    g5: LineSegment StartX=-1.61017 StartY=-2.60767 StartZ=0 EndX=1.45322 EndY=-2.69828 EndZ=0
    g6: Circle CenterX=0 CenterY=0 CenterZ=0 NormalX=0 NormalY=0 NormalZ=1 AngleXU=0 Radius=3.06473
  constraints (14):
    c: Coincident(g0,g1)
    c: Coincident(g1,g2)
    c: Coincident(g2,g3)
    c: Coincident(g3,g4)
    c: Coincident(g4,g5)
    c: Coincident(g5,g0)
    c: Equal(g0, g1-g5) x5
    c: PointOnObject(g0,g6)
    c: PointOnObject(g1,g6)
    c: PointOnObject(g2,g6)
    c: PointOnObject(g3,g6)
    c: PointOnObject(g4,g6)
    c: PointOnObject(g5,g6)
    c: Coincident(g6,g-1)
FEATURE [PartDesign::Pad] Pad154
  Direction = (0,0,1)
  Length = 4
  Length2 = 10
  Profile = -> Sketch331
  Refine = true
  Type = 0
FEATURE [Sketcher::SketchObject] Sketch332
  FullyConstrained = false
  MapMode = 5
  Support = -> [XY_Plane330]
  sketch-geometry (7):
    g0: LineSegment StartX=1.45322 StartY=-2.69828 StartZ=0 EndX=3.06339 EndY=-0.0906102 EndZ=0
    g1: LineSegment StartX=3.06339 StartY=-0.0906102 StartZ=0 EndX=1.61017 EndY=2.60767 EndZ=0
    g2: LineSegment StartX=1.61017 StartY=2.60767 StartZ=0 EndX=-1.45322 EndY=2.69828 EndZ=0
    g3: LineSegment StartX=-1.45322 StartY=2.69828 StartZ=0 EndX=-3.06339 EndY=0.0906102 EndZ=0
    g4: LineSegment StartX=-3.06339 StartY=0.0906102 StartZ=0 EndX=-1.61017 EndY=-2.60767 EndZ=0
    g5: LineSegment StartX=-1.61017 StartY=-2.60767 StartZ=0 EndX=1.45322 EndY=-2.69828 EndZ=0
    g6: Circle CenterX=0 CenterY=0 CenterZ=0 NormalX=0 NormalY=0 NormalZ=1 AngleXU=0 Radius=3.06473
  constraints (14):
    c: Coincident(g0,g1)
    c: Coincident(g1,g2)
    c: Coincident(g2,g3)
    c: Coincident(g3,g4)
    c: Coincident(g4,g5)
    c: Coincident(g5,g0)
    c: Equal(g0, g1-g5) x5
    c: PointOnObject(g0,g6)
    c: PointOnObject(g1,g6)
    c: PointOnObject(g2,g6)
    c: PointOnObject(g3,g6)
    c: PointOnObject(g4,g6)
    c: PointOnObject(g5,g6)
    c: Coincident(g6,g-1)
FEATURE [PartDesign::Pad] Pad155
  Direction = (0,0,1)
  Length = 4
  Length2 = 10
  Profile = -> Sketch332
  Refine = true
  Type = 0
FEATURE [PartDesign::Body] Body236
  Group = -> [Sketch332,Pad155]
  Origin = -> Origin336
  Placement = pos=(0,-8,-6.97) rot=(0,0,1;0rad)
  Tip = -> Pad155
FEATURE [Sketcher::SketchObject] Sketch333
  FullyConstrained = false
  MapMode = 5
  Support = -> [XY_Plane331]
  sketch-geometry (7):
    g0: LineSegment StartX=1.45322 StartY=-2.69828 StartZ=0 EndX=3.06339 EndY=-0.0906102 EndZ=0
    g1: LineSegment StartX=3.06339 StartY=-0.0906102 StartZ=0 EndX=1.61017 EndY=2.60767 EndZ=0
    g2: LineSegment StartX=1.61017 StartY=2.60767 StartZ=0 EndX=-1.45322 EndY=2.69828 EndZ=0
    g3: LineSegment StartX=-1.45322 StartY=2.69828 StartZ=0 EndX=-3.06339 EndY=0.0906102 EndZ=0
    g4: LineSegment StartX=-3.06339 StartY=0.0906102 StartZ=0 EndX=-1.61017 EndY=-2.60767 EndZ=0
    g5: LineSegment StartX=-1.61017 StartY=-2.60767 StartZ=0 EndX=1.45322 EndY=-2.69828 EndZ=0
    g6: Circle CenterX=0 CenterY=0 CenterZ=0 NormalX=0 NormalY=0 NormalZ=1 AngleXU=0 Radius=3.06473
  constraints (14):
    c: Coincident(g0,g1)
    c: Coincident(g1,g2)
    c: Coincident(g2,g3)
    c: Coincident(g3,g4)
    c: Coincident(g4,g5)
    c: Coincident(g5,g0)
    c: Equal(g0, g1-g5) x5
    c: PointOnObject(g0,g6)
    c: PointOnObject(g1,g6)
    c: PointOnObject(g2,g6)
    c: PointOnObject(g3,g6)
    c: PointOnObject(g4,g6)
    c: PointOnObject(g5,g6)
    c: Coincident(g6,g-1)
FEATURE [PartDesign::Pad] Pad156
  Direction = (0,0,1)
  Length = 4
  Length2 = 10
  Profile = -> Sketch333
  Refine = true
  Type = 0
FEATURE [PartDesign::Body] Body237
  Group = -> [Sketch333,Pad156]
  Origin = -> Origin337
  Placement = pos=(-0.04,8,-6.97) rot=(0,0,1;0rad)
  Tip = -> Pad156
FEATURE [Sketcher::SketchObject] Sketch334
  FullyConstrained = false
  MapMode = 5
  Support = -> [XY_Plane332]
  sketch-geometry (7):
    g0: LineSegment StartX=1.45322 StartY=-2.69828 StartZ=0 EndX=3.06339 EndY=-0.0906102 EndZ=0
    g1: LineSegment StartX=3.06339 StartY=-0.0906102 StartZ=0 EndX=1.61017 EndY=2.60767 EndZ=0
    g2: LineSegment StartX=1.61017 StartY=2.60767 StartZ=0 EndX=-1.45322 EndY=2.69828 EndZ=0
    g3: LineSegment StartX=-1.45322 StartY=2.69828 StartZ=0 EndX=-3.06339 EndY=0.0906102 EndZ=0
    g4: LineSegment StartX=-3.06339 StartY=0.0906102 StartZ=0 EndX=-1.61017 EndY=-2.60767 EndZ=0
    g5: LineSegment StartX=-1.61017 StartY=-2.60767 StartZ=0 EndX=1.45322 EndY=-2.69828 EndZ=0
    g6: Circle CenterX=0 CenterY=0 CenterZ=0 NormalX=0 NormalY=0 NormalZ=1 AngleXU=0 Radius=3.06473
  constraints (14):
    c: Coincident(g0,g1)
    c: Coincident(g1,g2)
    c: Coincident(g2,g3)
    c: Coincident(g3,g4)
    c: Coincident(g4,g5)
    c: Coincident(g5,g0)
    c: Equal(g0, g1-g5) x5
    c: PointOnObject(g0,g6)
    c: PointOnObject(g1,g6)
    c: PointOnObject(g2,g6)
    c: PointOnObject(g3,g6)
    c: PointOnObject(g4,g6)
    c: PointOnObject(g5,g6)
    c: Coincident(g6,g-1)
FEATURE [PartDesign::Pad] Pad157
  Direction = (0,0,1)
  Length = 4
  Length2 = 10
  Profile = -> Sketch334
  Refine = true
  Type = 0
FEATURE [PartDesign::Body] Body238
  Group = -> [Sketch334,Pad157]
  Origin = -> Origin338
  Placement = pos=(-8,-0.06,-6.97) rot=(0,0,1;0rad)
  Tip = -> Pad157
FEATURE [PartDesign::SubtractiveHelix] SubtractiveHelix
  Angle = 0
  Axis = (0,2e-16,1)
  Base = (0,0,0)
  BaseFeature = -> Pocket121
  HasBeenEdited = true
  Height = 20
  LeftHanded = false
  Mode = 0
  Outside = false
  Pitch = 8
  Placement = pos=(0,0,0) rot=(1,0,0;1.5708rad)
  Profile = -> Sketch325
  ReferenceAxis = -> Sketch325 [V_Axis]
  Turns = 3
FEATURE [PartDesign::PolarPattern] PolarPattern027
  Angle = 360
  Axis = -> Sketch325 [V_Axis]
  BaseFeature = -> SubtractiveHelix
  Occurrences = 3
  Originals = -> [SubtractiveHelix]
  Placement = pos=(0,0,0) rot=(1,0,0;1.5708rad)
FEATURE [Sketcher::SketchObject] Sketch326
  ExternalGeometry = -> [PolarPattern027]
  FullyConstrained = true
  MapMode = 5
  Placement = pos=(0,0,0) rot=(1,0,0;1.5708rad)
  Support = -> [XZ_Plane326]
  sketch-geometry (6):
    g0: LineSegment StartX=-4.25 StartY=0 StartZ=0 EndX=-3.25 EndY=0 EndZ=0
    g1: LineSegment StartX=-3.25 StartY=0 StartZ=0 EndX=-3.25 EndY=1 EndZ=0
    g2: LineSegment StartX=-3.25 StartY=1 StartZ=0 EndX=-4.25 EndY=0 EndZ=0
    g3: LineSegment StartX=-4.25 StartY=15 StartZ=0 EndX=-3.25 EndY=14 EndZ=0
    g4: LineSegment StartX=-3.25 StartY=14 StartZ=0 EndX=-3.25 EndY=15 EndZ=0
    g5: LineSegment StartX=-3.25 StartY=15 StartZ=0 EndX=-4.25 EndY=15 EndZ=0
  constraints (18):
    c: PointOnObject(g0,g-1)
    c: PointOnObject(g0,g-1)
    c: Coincident(g0,g1)
    c: Vertical(g1)
    c: Coincident(g1,g2)
    c: Coincident(g2,g0)
    c: PointOnObject(g3,g-3)
    c: Coincident(g3,g4)
    c: Vertical(g4)
    c: Coincident(g4,g5)
    c: Horizontal(g5)
    c: Coincident(g5,g3)
    c: Equal(g4,g5)
    c: Equal(g5,g1)
    c: Equal(g1,g0)
    c: DistanceX(g0,g0) = 1
    c: DistanceX(g0) = -3.25
    c: Vertical(g1,g3)
FEATURE [PartDesign::Groove] Groove006
  Angle = 360
  Axis = (0,2e-16,1)
  Base = (0,0,0)
  BaseFeature = -> PolarPattern027
  Placement = pos=(0,0,0) rot=(1,0,0;1.5708rad)
  Profile = -> Sketch326
  ReferenceAxis = -> Sketch326 [V_Axis]
  Reversed = true
FEATURE [Sketcher::SketchObject] Sketch329
  ExternalGeometry = -> [Groove006]
  FullyConstrained = false
  MapMode = 5
  Support = -> [XY_Plane326]
  sketch-geometry (22):
    g0: ArcOfCircle CenterX=0 CenterY=1.8e-15 CenterZ=0 NormalX=0 NormalY=0 NormalZ=1 AngleXU=0 Radius=12 StartAngle=6.12177 EndAngle=8.69593
    g1: Circle CenterX=0 CenterY=8 CenterZ=0 NormalX=0 NormalY=0 NormalZ=1 AngleXU=0 Radius=1.95
    g2: Circle CenterX=8 CenterY=4.4e-15 CenterZ=0 NormalX=0 NormalY=0 NormalZ=1 AngleXU=0 Radius=1.95
    g3: Circle CenterX=-8 CenterY=0 CenterZ=0 NormalX=0 NormalY=0 NormalZ=1 AngleXU=0 Radius=1.95
    g4: Circle CenterX=0 CenterY=-8 CenterZ=0 NormalX=0 NormalY=0 NormalZ=1 AngleXU=0 Radius=1.95
    g5: GeomPoint X=0 Y=1.8e-15 Z=0
    g6: GeomPoint X=0 Y=-25 Z=0
    g7: ArcOfCircle CenterX=0 CenterY=-25 CenterZ=0 NormalX=0 NormalY=0 NormalZ=1 AngleXU=0 Radius=7.5 StartAngle=3.3289 EndAngle=5.4508
    g8: Circle CenterX=0 CenterY=-25 CenterZ=0 NormalX=0 NormalY=0 NormalZ=1 AngleXU=0 Radius=4
    g9: LineSegment StartX=11.844 StartY=-1.92855 StartZ=0 EndX=8.25015 EndY=-24 EndZ=0
    g10: LineSegment StartX=-10.8555 StartY=-8.00001 StartZ=0 EndX=-7.36882 EndY=-26.3966 EndZ=0
    g11: LineSegment StartX=-25 StartY=7.99214 StartZ=0 EndX=-8.9513 EndY=7.99214 EndZ=0
    g12: LineSegment StartX=-25 StartY=-8 StartZ=0 EndX=-25 EndY=7.99214 EndZ=0
    g13: GeomPoint X=0 Y=12 Z=0
    g14: GeomPoint X=0 Y=-11 Z=0
    g15: LineSegment StartX=20 StartY=-30.5465 StartZ=0 EndX=5.04838 EndY=-30.5465 EndZ=0
    g16: LineSegment StartX=8.25015 StartY=-24 StartZ=0 EndX=20 EndY=-24 EndZ=0
    g17: LineSegment StartX=20 StartY=-24 StartZ=0 EndX=20 EndY=-30.5465 EndZ=0
    g18: GeomPoint X=1.59796e-10 Y=-29 Z=0
    g19: GeomPoint X=0 Y=-21 Z=0
    g20: LineSegment StartX=-10.8555 StartY=-8.00001 StartZ=0 EndX=-25 EndY=-8 EndZ=0
    g21: Circle CenterX=0 CenterY=1.8e-15 CenterZ=0 NormalX=0 NormalY=0 NormalZ=1 AngleXU=0 Radius=3.24154
  constraints (42):
    c: Coincident(g0,g-3)
    c: Coincident(g1,g-4)
    c: Coincident(g2,g-6)
    c: Coincident(g3,g-7)
    c: Coincident(g4,g-5)
    c: Equal(g1,g2)
    c: Equal(g2,g4)
    c: Equal(g4,g3)
    c: Diameter(g2) = 3.9
    c: Coincident(g5,g0)
    c: PointOnObject(g6,g-2)
    c: DistanceY(g6,g0) = 25
    c: Coincident(g7,g6)
    c: Coincident(g8,g7)
    c: Diameter(g8) = 8
    c: Diameter(g7) = 15
    c: Diameter(g-3) = 22
    c: Diameter(g0) = 24
    c: Tangent(g0,g9) = 1.5708
    c: Tangent(g7,g10) = -1.5708
    c: Coincident(g20,g12)
    c: Coincident(g12,g11)
    c: Horizontal(g11)
    c: Vertical(g12)
    c: PointOnObject(g13,g0)
    c: DistanceX(g13,g-1) = 0
    c: PointOnObject(g14,g-3)
    c: DistanceX(g11,g1) = 25
    c: Coincident(g16,g17)
    c: Coincident(g17,g15)
    c: Horizontal(g15)
    c: Horizontal(g16)
    c: Vertical(g17)
    c: PointOnObject(g18,g8)
    c: PointOnObject(g19,g8)
    c: DistanceX(g19,g-1) = 0
    c: DistanceX(g18,g15) = 20
    c: Coincident(g10,g20)
    c: Coincident(g0,g11)
    c: Coincident(g16,g9)
    c: Coincident(g15,g7)
    c: Coincident(g21,g0)
FEATURE [PartDesign::Pad] Pad151
  BaseFeature = -> Groove006
  Direction = (0,0,1)
  Length = 3
  Length2 = 10
  Placement = pos=(0,0,0) rot=(1,0,0;1.5708rad)
  Profile = -> Sketch329
  Refine = true
  Reversed = true
  Type = 0
  UseCustomVector = true
FEATURE [PartDesign::Fillet] Fillet178
  Base = -> Pad151 [Edge115]
  BaseFeature = -> Pad151
  Placement = pos=(0,0,0) rot=(1,0,0;1.5708rad)
  Radius = 1
  Refine = true
  SupportTransform = false
FEATURE [PartDesign::Fillet] Fillet179
  Base = -> Fillet178 [Edge19,Edge15]
  BaseFeature = -> Fillet178
  Placement = pos=(0,0,0) rot=(1,0,0;1.5708rad)
  Radius = 2
  Refine = true
  SupportTransform = false
FEATURE [PartDesign::Fillet] Fillet180
  Base = -> Fillet179 [Edge39]
  BaseFeature = -> Fillet179
  Placement = pos=(0,0,0) rot=(1,0,0;1.5708rad)
  Radius = 1
  Refine = true
  SupportTransform = false
FEATURE [PartDesign::Fillet] Fillet181
  Base = -> Fillet180 [Edge28,Edge24]
  BaseFeature = -> Fillet180
  Placement = pos=(0,0,0) rot=(1,0,0;1.5708rad)
  Radius = 2
  Refine = true
  SupportTransform = false
FEATURE [PartDesign::Fillet] Fillet182
  Base = -> Fillet181 [Edge34]
  BaseFeature = -> Fillet181
  Placement = pos=(0,0,0) rot=(1,0,0;1.5708rad)
  Radius = 1
  Refine = true
  SupportTransform = false
FEATURE [PartDesign::Pad] Pad152
  BaseFeature = -> Fillet182
  Direction = (0,0,1)
  Length = 15
  Length2 = 10
  Midplane = true
  Placement = pos=(0,0,0) rot=(1,0,0;1.5708rad)
  Refine = true
  Type = 0
FEATURE [Sketcher::SketchObject] Sketch330
  ExternalGeometry = -> [Pad152]
  FullyConstrained = true
  MapMode = 5
  Support = -> [XY_Plane326]
  sketch-geometry (4):
    g0: Circle CenterX=0 CenterY=8 CenterZ=0 NormalX=0 NormalY=0 NormalZ=1 AngleXU=0 Radius=2.25
    g1: Circle CenterX=8 CenterY=0 CenterZ=0 NormalX=0 NormalY=0 NormalZ=1 AngleXU=0 Radius=2.25
    g2: Circle CenterX=-8 CenterY=4.6e-15 CenterZ=0 NormalX=0 NormalY=0 NormalZ=1 AngleXU=0 Radius=2.25
    g3: Circle CenterX=0 CenterY=-8 CenterZ=0 NormalX=0 NormalY=0 NormalZ=1 AngleXU=0 Radius=2.25
  constraints (8):
    c: Coincident(g0,g-3)
    c: Coincident(g1,g-4)
    c: Coincident(g2,g-5)
    c: Coincident(g3,g-6)
    c: Diameter(g0) = 4.5
    c: Equal(g1,g2)
    c: Equal(g1,g3)
    c: Diameter(g1) = 4.5
FEATURE [PartDesign::Pad] Pad153
  BaseFeature = -> Pad152
  Direction = (0,0,1)
  Length = 8
  Length2 = 10
  Offset = 5
  Placement = pos=(0,0,0) rot=(1,0,0;1.5708rad)
  Profile = -> Sketch330
  Refine = true
  Type = 0
FEATURE [PartDesign::Body] Body232  label="Bottom"
  Group = -> [Sketch318,Revolution053,Sketch319,Pocket119,Chamfer020,PolarPattern026,Sketch320,Pocket120,Sketch321,Pocket121,Sketch325,SubtractiveHelix,PolarPattern027,Sketch326,Groove006,Sketch329,Pad151,Fillet178,Fillet179,Fillet180,Fillet181,Fillet182,Pad152,Sketch330,Pad153]
  Origin = -> Origin332
  Tip = -> Pad153
FEATURE [PartDesign::ShapeBinder] ReferencePad002
  Support = -> [Pad153]
  TraceSupport = false
FEATURE [PartDesign::Body] Body235
  Group = -> [Sketch331,Pad154,ReferencePad002]
  Origin = -> Origin335
  Placement = pos=(7.96,-0.06,-6.97) rot=(0,0,1;0rad)
  Tip = -> Pad154
FEATURE [PartDesign::SubtractiveHelix] SubtractiveHelix001
  Angle = 0
  Axis = (0,2e-16,1)
  Base = (0,0,0)
  BaseFeature = -> Pocket123
  HasBeenEdited = true
  Height = 30
  LeftHanded = false
  Mode = 0
  Outside = false
  Pitch = 8
  Placement = pos=(0,0,0) rot=(1,0,0;1.5708rad)
  Profile = -> Sketch327
  ReferenceAxis = -> Sketch327 [V_Axis]
  Turns = 3
FEATURE [PartDesign::PolarPattern] PolarPattern028
  Angle = 360
  Axis = -> Sketch327 [V_Axis]
  BaseFeature = -> SubtractiveHelix001
  Occurrences = 3
  Originals = -> [SubtractiveHelix001]
  Placement = pos=(0,0,0) rot=(1,0,0;1.5708rad)
FEATURE [Sketcher::SketchObject] Sketch328
  ExternalGeometry = -> [PolarPattern028]
  FullyConstrained = true
  MapMode = 5
  Placement = pos=(0,0,0) rot=(1,0,0;1.5708rad)
  Support = -> [XZ_Plane327]
  sketch-geometry (6):
    g0: LineSegment StartX=-4.25 StartY=26 StartZ=0 EndX=-3.25 EndY=26 EndZ=0
    g1: LineSegment StartX=-3.25 StartY=26 StartZ=0 EndX=-3.25 EndY=25 EndZ=0
    g2: LineSegment StartX=-3.25 StartY=25 StartZ=0 EndX=-4.25 EndY=26 EndZ=0
    g3: LineSegment StartX=-4.25 StartY=15 StartZ=0 EndX=-3.25 EndY=15 EndZ=0
    g4: LineSegment StartX=-3.25 StartY=15 StartZ=0 EndX=-3.25 EndY=16 EndZ=0
    g5: LineSegment StartX=-3.25 StartY=16 StartZ=0 EndX=-4.25 EndY=15 EndZ=0
  constraints (18):
    c: PointOnObject(g0,g-3)
    c: PointOnObject(g0,g-3)
    c: Coincident(g0,g1)
    c: Coincident(g1,g2)
    c: Coincident(g2,g0)
    c: PointOnObject(g3,g-4)
    c: PointOnObject(g3,g-4)
    c: Coincident(g3,g4)
    c: Vertical(g4)
    c: Coincident(g4,g5)
    c: Coincident(g5,g3)
    c: Vertical(g4,g1)
    c: Vertical(g1)
    c: Equal(g0,g1)
    c: Equal(g1,g3)
    c: Equal(g3,g4)
    c: DistanceX(g3,g3) = 1
    c: DistanceX(g3) = -3.25
FEATURE [PartDesign::Groove] Groove007
  Angle = 360
  Axis = (0,2e-16,1)
  Base = (0,0,0)
  BaseFeature = -> PolarPattern028
  Placement = pos=(0,0,0) rot=(1,0,0;1.5708rad)
  Profile = -> Sketch328
  ReferenceAxis = -> Sketch328 [V_Axis]
  Reversed = true
FEATURE [PartDesign::Body] Body233  label="Top"
  Group = -> [Sketch322,Revolution054,Sketch323,Pocket122,Sketch324,Pocket123,Sketch327,SubtractiveHelix001,PolarPattern028,Sketch328,Groove007]
  Origin = -> Origin333
  Tip = -> Groove007
FEATURE [App::Part] Part099  label="T8 antibacklash nut"
  Group = -> [Body232,Body233,Body234]
  Origin = -> Origin331
FEATURE [App::LinkGroup] LinkGroup017
  ElementList = -> [Body235,Body236,Body237,Body238]
  LinkMode = 0
FEATURE [App::LinkGroup] LinkGroup018  label="SoporteSensor"
  ElementList = -> [LinkGroup017,Part099]
  LinkMode = 0
  Placement = pos=(192.75,119.723,105.027) rot=(0.57735,-0.57735,-0.57735;2.0944rad)
FEATURE [Part::Cylinder] Cylinder  label="sensor"
  Angle = 360
  AttacherType = Attacher::AttachEngine3D
  Height = 22
  Placement = pos=(194,145,105) rot=(-1,0,0;1.5708rad)
  Radius = 8
FEATURE [App::LinkGroup] LinkGroup019  label="sensorSoporte"
  ElementList = -> [Cylinder,LinkGroup018]
  LinkMode = 0
  Placement = pos=(-9.91821e-05,0.299999,0) rot=(0,0,1;0rad)
FEATURE [Sketcher::SketchObject] Sketch335
  FullyConstrained = false
  MapMode = 5
  Placement = pos=(0,0,0) rot=(0.57735,0.57735,0.57735;2.0944rad)
  Support = -> [YZ_Plane334]
  sketch-geometry (8):
    g0: LineSegment StartX=2.8963 StartY=-2.75889 StartZ=0 EndX=3.83742 EndY=1.12882 EndZ=0
    g1: LineSegment StartX=3.83742 StartY=1.12882 StartZ=0 EndX=0.941117 EndY=3.88771 EndZ=0
    g2: LineSegment StartX=0.941117 StartY=3.88771 StartZ=0 EndX=-2.8963 EndY=2.75889 EndZ=0
    g3: LineSegment StartX=-2.8963 StartY=2.75889 StartZ=0 EndX=-3.83742 EndY=-1.12882 EndZ=0
    g4: LineSegment StartX=-3.83742 StartY=-1.12882 StartZ=0 EndX=-0.941117 EndY=-3.88771 EndZ=0
    g5: LineSegment StartX=-0.941117 StartY=-3.88771 StartZ=0 EndX=2.8963 EndY=-2.75889 EndZ=0
    g6: Circle CenterX=0 CenterY=0 CenterZ=0 NormalX=0 NormalY=0 NormalZ=1 AngleXU=0 Radius=4
    g7: Circle CenterX=0 CenterY=0 CenterZ=0 NormalX=0 NormalY=0 NormalZ=1 AngleXU=0 Radius=2.5
  constraints (17):
    c: Coincident(g0,g1)
    c: Coincident(g1,g2)
    c: Coincident(g2,g3)
    c: Coincident(g3,g4)
    c: Coincident(g4,g5)
    c: Coincident(g5,g0)
    c: Equal(g0, g1-g5) x5
    c: PointOnObject(g0,g6)
    c: PointOnObject(g1,g6)
    c: PointOnObject(g2,g6)
    c: PointOnObject(g3,g6)
    c: PointOnObject(g4,g6)
    c: PointOnObject(g5,g6)
    c: Coincident(g6,g-1)
    c: Coincident(g7,g6)
    c: Radius(g7) = 2.5
    c: Radius(g6) = 4
FEATURE [PartDesign::Pad] Pad158
  Direction = (1,-2e-16,3e-16)
  Length = 3
  Length2 = 10
  Placement = pos=(0,0,0) rot=(0.57735,0.57735,0.57735;2.0944rad)
  Profile = -> Sketch335
  Type = 0
FEATURE [PartDesign::Pad] Pad159
  BaseFeature = -> Pad158
  Direction = (1,-2e-16,6e-16)
  Length = 15
  Length2 = 10
  Placement = pos=(0,0,0) rot=(0.57735,0.57735,0.57735;2.0944rad)
  Profile = -> Pad158 [Edge20]
  Type = 0
FEATURE [PartDesign::Body] Body239
  Group = -> [Sketch335,Pad158,Pad159]
  Origin = -> Origin340
  Tip = -> Pad159
FEATURE [App::Part] Part100  label="tornillo M5-15-013"
  Group = -> [Body239]
  Origin = -> Origin339
  Placement = pos=(31,10,26) rot=(0,1,0;1.5708rad)
FEATURE [Sketcher::SketchObject] Sketch336
  FullyConstrained = false
  MapMode = 5
  Placement = pos=(0,0,0) rot=(0.57735,0.57735,0.57735;2.0944rad)
  Support = -> [YZ_Plane336]
  sketch-geometry (8):
    g0: LineSegment StartX=2.8963 StartY=-2.75889 StartZ=0 EndX=3.83742 EndY=1.12882 EndZ=0
    g1: LineSegment StartX=3.83742 StartY=1.12882 StartZ=0 EndX=0.941117 EndY=3.88771 EndZ=0
    g2: LineSegment StartX=0.941117 StartY=3.88771 StartZ=0 EndX=-2.8963 EndY=2.75889 EndZ=0
    g3: LineSegment StartX=-2.8963 StartY=2.75889 StartZ=0 EndX=-3.83742 EndY=-1.12882 EndZ=0
    g4: LineSegment StartX=-3.83742 StartY=-1.12882 StartZ=0 EndX=-0.941117 EndY=-3.88771 EndZ=0
    g5: LineSegment StartX=-0.941117 StartY=-3.88771 StartZ=0 EndX=2.8963 EndY=-2.75889 EndZ=0
    g6: Circle CenterX=0 CenterY=0 CenterZ=0 NormalX=0 NormalY=0 NormalZ=1 AngleXU=0 Radius=4
    g7: Circle CenterX=0 CenterY=0 CenterZ=0 NormalX=0 NormalY=0 NormalZ=1 AngleXU=0 Radius=2.5
  constraints (17):
    c: Coincident(g0,g1)
    c: Coincident(g1,g2)
    c: Coincident(g2,g3)
    c: Coincident(g3,g4)
    c: Coincident(g4,g5)
    c: Coincident(g5,g0)
    c: Equal(g0, g1-g5) x5
    c: PointOnObject(g0,g6)
    c: PointOnObject(g1,g6)
    c: PointOnObject(g2,g6)
    c: PointOnObject(g3,g6)
    c: PointOnObject(g4,g6)
    c: PointOnObject(g5,g6)
    c: Coincident(g6,g-1)
    c: Coincident(g7,g6)
    c: Radius(g7) = 2.5
    c: Radius(g6) = 4
FEATURE [PartDesign::Pad] Pad160
  Direction = (1,-2e-16,3e-16)
  Length = 3
  Length2 = 10
  Placement = pos=(0,0,0) rot=(0.57735,0.57735,0.57735;2.0944rad)
  Profile = -> Sketch336
  Type = 0
FEATURE [PartDesign::Pad] Pad161
  BaseFeature = -> Pad160
  Direction = (1,-2e-16,6e-16)
  Length = 15
  Length2 = 10
  Placement = pos=(0,0,0) rot=(0.57735,0.57735,0.57735;2.0944rad)
  Profile = -> Pad160 [Edge20]
  Type = 0
FEATURE [PartDesign::Body] Body240
  Group = -> [Sketch336,Pad160,Pad161]
  Origin = -> Origin342
  Tip = -> Pad161
FEATURE [App::Part] Part101  label="tornillo M5-15-014"
  Group = -> [Body240]
  Origin = -> Origin341
  Placement = pos=(26,10,33) rot=(0,1,0;3.14159rad)
FEATURE [Sketcher::SketchObject] Sketch337
  FullyConstrained = false
  MapMode = 5
  Placement = pos=(0,0,0) rot=(0.57735,0.57735,0.57735;2.0944rad)
  Support = -> [YZ_Plane337]
  sketch-geometry (8):
    g0: LineSegment StartX=2.8963 StartY=-2.75889 StartZ=0 EndX=3.83742 EndY=1.12882 EndZ=0
    g1: LineSegment StartX=3.83742 StartY=1.12882 StartZ=0 EndX=0.941117 EndY=3.88771 EndZ=0
    g2: LineSegment StartX=0.941117 StartY=3.88771 StartZ=0 EndX=-2.8963 EndY=2.75889 EndZ=0
    g3: LineSegment StartX=-2.8963 StartY=2.75889 StartZ=0 EndX=-3.83742 EndY=-1.12882 EndZ=0
    g4: LineSegment StartX=-3.83742 StartY=-1.12882 StartZ=0 EndX=-0.941117 EndY=-3.88771 EndZ=0
    g5: LineSegment StartX=-0.941117 StartY=-3.88771 StartZ=0 EndX=2.8963 EndY=-2.75889 EndZ=0
    g6: Circle CenterX=0 CenterY=0 CenterZ=0 NormalX=0 NormalY=0 NormalZ=1 AngleXU=0 Radius=4
    g7: Circle CenterX=0 CenterY=0 CenterZ=0 NormalX=0 NormalY=0 NormalZ=1 AngleXU=0 Radius=2.5
  constraints (17):
    c: Coincident(g0,g1)
    c: Coincident(g1,g2)
    c: Coincident(g2,g3)
    c: Coincident(g3,g4)
    c: Coincident(g4,g5)
    c: Coincident(g5,g0)
    c: Equal(g0, g1-g5) x5
    c: PointOnObject(g0,g6)
    c: PointOnObject(g1,g6)
    c: PointOnObject(g2,g6)
    c: PointOnObject(g3,g6)
    c: PointOnObject(g4,g6)
    c: PointOnObject(g5,g6)
    c: Coincident(g6,g-1)
    c: Coincident(g7,g6)
    c: Radius(g7) = 2.5
    c: Radius(g6) = 4
FEATURE [PartDesign::Pad] Pad162
  Direction = (1,-2e-16,3e-16)
  Length = 3
  Length2 = 10
  Placement = pos=(0,0,0) rot=(0.57735,0.57735,0.57735;2.0944rad)
  Profile = -> Sketch337
  Type = 0
FEATURE [PartDesign::Pad] Pad163
  BaseFeature = -> Pad162
  Direction = (1,-2e-16,6e-16)
  Length = 15
  Length2 = 10
  Placement = pos=(0,0,0) rot=(0.57735,0.57735,0.57735;2.0944rad)
  Profile = -> Pad162 [Edge20]
  Type = 0
FEATURE [PartDesign::Body] Body241
  Group = -> [Sketch337,Pad162,Pad163]
  Origin = -> Origin344
  Tip = -> Pad163
FEATURE [App::Part] Part102  label="tornillo M5-15-015"
  Group = -> [Body241]
  Origin = -> Origin343
  Placement = pos=(26,10,159) rot=(0,1,0;3.14159rad)
FEATURE [Sketcher::SketchObject] Sketch338
  FullyConstrained = false
  MapMode = 5
  Placement = pos=(0,0,0) rot=(0.57735,0.57735,0.57735;2.0944rad)
  Support = -> [YZ_Plane339]
  sketch-geometry (8):
    g0: LineSegment StartX=2.8963 StartY=-2.75889 StartZ=0 EndX=3.83742 EndY=1.12882 EndZ=0
    g1: LineSegment StartX=3.83742 StartY=1.12882 StartZ=0 EndX=0.941117 EndY=3.88771 EndZ=0
    g2: LineSegment StartX=0.941117 StartY=3.88771 StartZ=0 EndX=-2.8963 EndY=2.75889 EndZ=0
    g3: LineSegment StartX=-2.8963 StartY=2.75889 StartZ=0 EndX=-3.83742 EndY=-1.12882 EndZ=0
    g4: LineSegment StartX=-3.83742 StartY=-1.12882 StartZ=0 EndX=-0.941117 EndY=-3.88771 EndZ=0
    g5: LineSegment StartX=-0.941117 StartY=-3.88771 StartZ=0 EndX=2.8963 EndY=-2.75889 EndZ=0
    g6: Circle CenterX=0 CenterY=0 CenterZ=0 NormalX=0 NormalY=0 NormalZ=1 AngleXU=0 Radius=4
    g7: Circle CenterX=0 CenterY=0 CenterZ=0 NormalX=0 NormalY=0 NormalZ=1 AngleXU=0 Radius=2.5
  constraints (17):
    c: Coincident(g0,g1)
    c: Coincident(g1,g2)
    c: Coincident(g2,g3)
    c: Coincident(g3,g4)
    c: Coincident(g4,g5)
    c: Coincident(g5,g0)
    c: Equal(g0, g1-g5) x5
    c: PointOnObject(g0,g6)
    c: PointOnObject(g1,g6)
    c: PointOnObject(g2,g6)
    c: PointOnObject(g3,g6)
    c: PointOnObject(g4,g6)
    c: PointOnObject(g5,g6)
    c: Coincident(g6,g-1)
    c: Coincident(g7,g6)
    c: Radius(g7) = 2.5
    c: Radius(g6) = 4
FEATURE [PartDesign::Pad] Pad164
  Direction = (1,-2e-16,3e-16)
  Length = 3
  Length2 = 10
  Placement = pos=(0,0,0) rot=(0.57735,0.57735,0.57735;2.0944rad)
  Profile = -> Sketch338
  Type = 0
FEATURE [PartDesign::Pad] Pad165
  BaseFeature = -> Pad164
  Direction = (1,-2e-16,6e-16)
  Length = 15
  Length2 = 10
  Placement = pos=(0,0,0) rot=(0.57735,0.57735,0.57735;2.0944rad)
  Profile = -> Pad164 [Edge20]
  Type = 0
FEATURE [PartDesign::Body] Body242
  Group = -> [Sketch338,Pad164,Pad165]
  Origin = -> Origin346
  Tip = -> Pad165
FEATURE [App::Part] Part103  label="tornillo M5-15-016"
  Group = -> [Body242]
  Origin = -> Origin345
  Placement = pos=(28.2334,9.96532,164.125) rot=(0.44435,-0.754393,0.483161;1.89214rad)
FEATURE [Sketcher::SketchObject] Sketch339
  FullyConstrained = false
  MapMode = 5
  Placement = pos=(0,0,0) rot=(0.57735,0.57735,0.57735;2.0944rad)
  Support = -> [YZ_Plane342]
  sketch-geometry (8):
    g0: LineSegment StartX=2.8963 StartY=-2.75889 StartZ=0 EndX=3.83742 EndY=1.12882 EndZ=0
    g1: LineSegment StartX=3.83742 StartY=1.12882 StartZ=0 EndX=0.941117 EndY=3.88771 EndZ=0
    g2: LineSegment StartX=0.941117 StartY=3.88771 StartZ=0 EndX=-2.8963 EndY=2.75889 EndZ=0
    g3: LineSegment StartX=-2.8963 StartY=2.75889 StartZ=0 EndX=-3.83742 EndY=-1.12882 EndZ=0
    g4: LineSegment StartX=-3.83742 StartY=-1.12882 StartZ=0 EndX=-0.941117 EndY=-3.88771 EndZ=0
    g5: LineSegment StartX=-0.941117 StartY=-3.88771 StartZ=0 EndX=2.8963 EndY=-2.75889 EndZ=0
    g6: Circle CenterX=0 CenterY=0 CenterZ=0 NormalX=0 NormalY=0 NormalZ=1 AngleXU=0 Radius=4
    g7: Circle CenterX=0 CenterY=0 CenterZ=0 NormalX=0 NormalY=0 NormalZ=1 AngleXU=0 Radius=2.5
  constraints (17):
    c: Coincident(g0,g1)
    c: Coincident(g1,g2)
    c: Coincident(g2,g3)
    c: Coincident(g3,g4)
    c: Coincident(g4,g5)
    c: Coincident(g5,g0)
    c: Equal(g0, g1-g5) x5
    c: PointOnObject(g0,g6)
    c: PointOnObject(g1,g6)
    c: PointOnObject(g2,g6)
    c: PointOnObject(g3,g6)
    c: PointOnObject(g4,g6)
    c: PointOnObject(g5,g6)
    c: Coincident(g6,g-1)
    c: Coincident(g7,g6)
    c: Radius(g7) = 2.5
    c: Radius(g6) = 4
FEATURE [PartDesign::Pad] Pad167
  Direction = (1,-2e-16,3e-16)
  Length = 3
  Length2 = 10
  Placement = pos=(0,0,0) rot=(0.57735,0.57735,0.57735;2.0944rad)
  Profile = -> Sketch339
  Type = 0
FEATURE [PartDesign::Pad] Pad168
  BaseFeature = -> Pad167
  Direction = (1,-2e-16,6e-16)
  Length = 15
  Length2 = 10
  Placement = pos=(0,0,0) rot=(0.57735,0.57735,0.57735;2.0944rad)
  Profile = -> Pad167 [Edge20]
  Type = 0
FEATURE [PartDesign::Body] Body243
  Group = -> [Sketch339,Pad167,Pad168]
  Origin = -> Origin350
  Tip = -> Pad168
FEATURE [App::Part] Part104  label="tornillo M5-15-017"
  Group = -> [Body243]
  Origin = -> Origin348
  Placement = pos=(31,10,26) rot=(0,1,0;1.5708rad)
FEATURE [Sketcher::SketchObject] Sketch340
  FullyConstrained = false
  MapMode = 5
  Placement = pos=(0,0,0) rot=(0.57735,0.57735,0.57735;2.0944rad)
  Support = -> [YZ_Plane343]
  sketch-geometry (8):
    g0: LineSegment StartX=2.8963 StartY=-2.75889 StartZ=0 EndX=3.83742 EndY=1.12882 EndZ=0
    g1: LineSegment StartX=3.83742 StartY=1.12882 StartZ=0 EndX=0.941117 EndY=3.88771 EndZ=0
    g2: LineSegment StartX=0.941117 StartY=3.88771 StartZ=0 EndX=-2.8963 EndY=2.75889 EndZ=0
    g3: LineSegment StartX=-2.8963 StartY=2.75889 StartZ=0 EndX=-3.83742 EndY=-1.12882 EndZ=0
    g4: LineSegment StartX=-3.83742 StartY=-1.12882 StartZ=0 EndX=-0.941117 EndY=-3.88771 EndZ=0
    g5: LineSegment StartX=-0.941117 StartY=-3.88771 StartZ=0 EndX=2.8963 EndY=-2.75889 EndZ=0
    g6: Circle CenterX=0 CenterY=0 CenterZ=0 NormalX=0 NormalY=0 NormalZ=1 AngleXU=0 Radius=4
    g7: Circle CenterX=0 CenterY=0 CenterZ=0 NormalX=0 NormalY=0 NormalZ=1 AngleXU=0 Radius=2.5
  constraints (17):
    c: Coincident(g0,g1)
    c: Coincident(g1,g2)
    c: Coincident(g2,g3)
    c: Coincident(g3,g4)
    c: Coincident(g4,g5)
    c: Coincident(g5,g0)
    c: Equal(g0, g1-g5) x5
    c: PointOnObject(g0,g6)
    c: PointOnObject(g1,g6)
    c: PointOnObject(g2,g6)
    c: PointOnObject(g3,g6)
    c: PointOnObject(g4,g6)
    c: PointOnObject(g5,g6)
    c: Coincident(g6,g-1)
    c: Coincident(g7,g6)
    c: Radius(g7) = 2.5
    c: Radius(g6) = 4
FEATURE [PartDesign::Pad] Pad166
  Direction = (1,-2e-16,3e-16)
  Length = 3
  Length2 = 10
  Placement = pos=(0,0,0) rot=(0.57735,0.57735,0.57735;2.0944rad)
  Profile = -> Sketch340
  Type = 0
FEATURE [PartDesign::Pad] Pad170
  BaseFeature = -> Pad166
  Direction = (1,-2e-16,6e-16)
  Length = 15
  Length2 = 10
  Placement = pos=(0,0,0) rot=(0.57735,0.57735,0.57735;2.0944rad)
  Profile = -> Pad166 [Edge20]
  Type = 0
FEATURE [PartDesign::Body] Body244
  Group = -> [Sketch340,Pad166,Pad170]
  Origin = -> Origin349
  Tip = -> Pad170
FEATURE [App::Part] Part105  label="tornillo M5-15-018"
  Group = -> [Body244]
  Origin = -> Origin347
  Placement = pos=(26,10,33) rot=(0,1,0;3.14159rad)
FEATURE [Sketcher::SketchObject] Sketch341
  FullyConstrained = false
  MapMode = 5
  Placement = pos=(0,0,0) rot=(0.57735,0.57735,0.57735;2.0944rad)
  Support = -> [YZ_Plane344]
  sketch-geometry (8):
    g0: LineSegment StartX=2.8963 StartY=-2.75889 StartZ=0 EndX=3.83742 EndY=1.12882 EndZ=0
    g1: LineSegment StartX=3.83742 StartY=1.12882 StartZ=0 EndX=0.941117 EndY=3.88771 EndZ=0
    g2: LineSegment StartX=0.941117 StartY=3.88771 StartZ=0 EndX=-2.8963 EndY=2.75889 EndZ=0
    g3: LineSegment StartX=-2.8963 StartY=2.75889 StartZ=0 EndX=-3.83742 EndY=-1.12882 EndZ=0
    g4: LineSegment StartX=-3.83742 StartY=-1.12882 StartZ=0 EndX=-0.941117 EndY=-3.88771 EndZ=0
    g5: LineSegment StartX=-0.941117 StartY=-3.88771 StartZ=0 EndX=2.8963 EndY=-2.75889 EndZ=0
    g6: Circle CenterX=0 CenterY=0 CenterZ=0 NormalX=0 NormalY=0 NormalZ=1 AngleXU=0 Radius=4
    g7: Circle CenterX=0 CenterY=0 CenterZ=0 NormalX=0 NormalY=0 NormalZ=1 AngleXU=0 Radius=2.5
  constraints (17):
    c: Coincident(g0,g1)
    c: Coincident(g1,g2)
    c: Coincident(g2,g3)
    c: Coincident(g3,g4)
    c: Coincident(g4,g5)
    c: Coincident(g5,g0)
    c: Equal(g0, g1-g5) x5
    c: PointOnObject(g0,g6)
    c: PointOnObject(g1,g6)
    c: PointOnObject(g2,g6)
    c: PointOnObject(g3,g6)
    c: PointOnObject(g4,g6)
    c: PointOnObject(g5,g6)
    c: Coincident(g6,g-1)
    c: Coincident(g7,g6)
    c: Radius(g7) = 2.5
    c: Radius(g6) = 4
FEATURE [PartDesign::Pad] Pad169
  Direction = (1,-2e-16,3e-16)
  Length = 3
  Length2 = 10
  Placement = pos=(0,0,0) rot=(0.57735,0.57735,0.57735;2.0944rad)
  Profile = -> Sketch341
  Type = 0
FEATURE [PartDesign::Pad] Pad171
  BaseFeature = -> Pad169
  Direction = (1,-2e-16,6e-16)
  Length = 15
  Length2 = 10
  Placement = pos=(0,0,0) rot=(0.57735,0.57735,0.57735;2.0944rad)
  Profile = -> Pad169 [Edge20]
  Type = 0
FEATURE [PartDesign::Body] Body245
  Group = -> [Sketch341,Pad169,Pad171]
  Origin = -> Origin352
  Tip = -> Pad171
FEATURE [App::Part] Part107  label="tornillo M5-15-020"
  Group = -> [Body245]
  Origin = -> Origin351
  Placement = pos=(26,10,159) rot=(0,1,0;3.14159rad)
FEATURE [Sketcher::SketchObject] Sketch342
  FullyConstrained = false
  MapMode = 5
  Placement = pos=(0,0,0) rot=(0.57735,0.57735,0.57735;2.0944rad)
  Support = -> [YZ_Plane347]
  sketch-geometry (8):
    g0: LineSegment StartX=2.8963 StartY=-2.75889 StartZ=0 EndX=3.83742 EndY=1.12882 EndZ=0
    g1: LineSegment StartX=3.83742 StartY=1.12882 StartZ=0 EndX=0.941117 EndY=3.88771 EndZ=0
    g2: LineSegment StartX=0.941117 StartY=3.88771 StartZ=0 EndX=-2.8963 EndY=2.75889 EndZ=0
    g3: LineSegment StartX=-2.8963 StartY=2.75889 StartZ=0 EndX=-3.83742 EndY=-1.12882 EndZ=0
    g4: LineSegment StartX=-3.83742 StartY=-1.12882 StartZ=0 EndX=-0.941117 EndY=-3.88771 EndZ=0
    g5: LineSegment StartX=-0.941117 StartY=-3.88771 StartZ=0 EndX=2.8963 EndY=-2.75889 EndZ=0
    g6: Circle CenterX=0 CenterY=0 CenterZ=0 NormalX=0 NormalY=0 NormalZ=1 AngleXU=0 Radius=4
    g7: Circle CenterX=0 CenterY=0 CenterZ=0 NormalX=0 NormalY=0 NormalZ=1 AngleXU=0 Radius=2.5
  constraints (17):
    c: Coincident(g0,g1)
    c: Coincident(g1,g2)
    c: Coincident(g2,g3)
    c: Coincident(g3,g4)
    c: Coincident(g4,g5)
    c: Coincident(g5,g0)
    c: Equal(g0, g1-g5) x5
    c: PointOnObject(g0,g6)
    c: PointOnObject(g1,g6)
    c: PointOnObject(g2,g6)
    c: PointOnObject(g3,g6)
    c: PointOnObject(g4,g6)
    c: PointOnObject(g5,g6)
    c: Coincident(g6,g-1)
    c: Coincident(g7,g6)
    c: Radius(g7) = 2.5
    c: Radius(g6) = 4
FEATURE [PartDesign::Pad] Pad173
  Direction = (1,-2e-16,3e-16)
  Length = 3
  Length2 = 10
  Placement = pos=(0,0,0) rot=(0.57735,0.57735,0.57735;2.0944rad)
  Profile = -> Sketch342
  Type = 0
FEATURE [PartDesign::Pad] Pad172
  BaseFeature = -> Pad173
  Direction = (1,-2e-16,6e-16)
  Length = 15
  Length2 = 10
  Placement = pos=(0,0,0) rot=(0.57735,0.57735,0.57735;2.0944rad)
  Profile = -> Pad173 [Edge20]
  Type = 0
FEATURE [PartDesign::Body] Body246
  Group = -> [Sketch342,Pad173,Pad172]
  Origin = -> Origin354
  Tip = -> Pad172
FEATURE [App::Part] Part106  label="tornillo M5-15-019"
  Group = -> [Body246]
  Origin = -> Origin353
  Placement = pos=(28.2334,9.96532,164.125) rot=(0.44435,-0.754393,0.483161;1.89214rad)
FEATURE [App::LinkGroup] LinkGroup020
  ElementList = -> [Part104,Part105,Part106,Part107]
  LinkMode = 0
  Placement = pos=(339.888,20.1907,1.52588e-05) rot=(0,0,1;3.14159rad)
FEATURE [App::LinkGroup] LinkGroup021
  ElementList = -> [Part100,Part101,Part102,Part103,LinkGroup020]
  LinkMode = 0
FEATURE [Sketcher::SketchObject] Sketch343
  FullyConstrained = false
  MapMode = 5
  Placement = pos=(0,0,0) rot=(0.57735,0.57735,0.57735;2.0944rad)
  Support = -> [YZ_Plane350]
  sketch-geometry (8):
    g0: LineSegment StartX=2.8963 StartY=-2.75889 StartZ=0 EndX=3.83742 EndY=1.12882 EndZ=0
    g1: LineSegment StartX=3.83742 StartY=1.12882 StartZ=0 EndX=0.941117 EndY=3.88771 EndZ=0
    g2: LineSegment StartX=0.941117 StartY=3.88771 StartZ=0 EndX=-2.8963 EndY=2.75889 EndZ=0
    g3: LineSegment StartX=-2.8963 StartY=2.75889 StartZ=0 EndX=-3.83742 EndY=-1.12882 EndZ=0
    g4: LineSegment StartX=-3.83742 StartY=-1.12882 StartZ=0 EndX=-0.941117 EndY=-3.88771 EndZ=0
    g5: LineSegment StartX=-0.941117 StartY=-3.88771 StartZ=0 EndX=2.8963 EndY=-2.75889 EndZ=0
    g6: Circle CenterX=0 CenterY=0 CenterZ=0 NormalX=0 NormalY=0 NormalZ=1 AngleXU=0 Radius=4
    g7: Circle CenterX=0 CenterY=0 CenterZ=0 NormalX=0 NormalY=0 NormalZ=1 AngleXU=0 Radius=2.5
  constraints (17):
    c: Coincident(g0,g1)
    c: Coincident(g1,g2)
    c: Coincident(g2,g3)
    c: Coincident(g3,g4)
    c: Coincident(g4,g5)
    c: Coincident(g5,g0)
    c: Equal(g0, g1-g5) x5
    c: PointOnObject(g0,g6)
    c: PointOnObject(g1,g6)
    c: PointOnObject(g2,g6)
    c: PointOnObject(g3,g6)
    c: PointOnObject(g4,g6)
    c: PointOnObject(g5,g6)
    c: Coincident(g6,g-1)
    c: Coincident(g7,g6)
    c: Radius(g7) = 2.5
    c: Radius(g6) = 4
FEATURE [PartDesign::Pad] Pad175
  Direction = (1,-2e-16,3e-16)
  Length = 3
  Length2 = 10
  Placement = pos=(0,0,0) rot=(0.57735,0.57735,0.57735;2.0944rad)
  Profile = -> Sketch343
  Type = 0
FEATURE [PartDesign::Pad] Pad176
  BaseFeature = -> Pad175
  Direction = (1,-2e-16,6e-16)
  Length = 15
  Length2 = 10
  Placement = pos=(0,0,0) rot=(0.57735,0.57735,0.57735;2.0944rad)
  Profile = -> Pad175 [Edge20]
  Type = 0
FEATURE [PartDesign::Body] Body247
  Group = -> [Sketch343,Pad175,Pad176]
  Origin = -> Origin359
  Tip = -> Pad176
FEATURE [App::Part] Part108  label="tornillo M5-15-021"
  Group = -> [Body247]
  Origin = -> Origin357
  Placement = pos=(31,10,26) rot=(0,1,0;1.5708rad)
FEATURE [Sketcher::SketchObject] Sketch344
  FullyConstrained = false
  MapMode = 5
  Placement = pos=(0,0,0) rot=(0.57735,0.57735,0.57735;2.0944rad)
  Support = -> [YZ_Plane351]
  sketch-geometry (8):
    g0: LineSegment StartX=2.8963 StartY=-2.75889 StartZ=0 EndX=3.83742 EndY=1.12882 EndZ=0
    g1: LineSegment StartX=3.83742 StartY=1.12882 StartZ=0 EndX=0.941117 EndY=3.88771 EndZ=0
    g2: LineSegment StartX=0.941117 StartY=3.88771 StartZ=0 EndX=-2.8963 EndY=2.75889 EndZ=0
    g3: LineSegment StartX=-2.8963 StartY=2.75889 StartZ=0 EndX=-3.83742 EndY=-1.12882 EndZ=0
    g4: LineSegment StartX=-3.83742 StartY=-1.12882 StartZ=0 EndX=-0.941117 EndY=-3.88771 EndZ=0
    g5: LineSegment StartX=-0.941117 StartY=-3.88771 StartZ=0 EndX=2.8963 EndY=-2.75889 EndZ=0
    g6: Circle CenterX=0 CenterY=0 CenterZ=0 NormalX=0 NormalY=0 NormalZ=1 AngleXU=0 Radius=4
    g7: Circle CenterX=0 CenterY=0 CenterZ=0 NormalX=0 NormalY=0 NormalZ=1 AngleXU=0 Radius=2.5
  constraints (17):
    c: Coincident(g0,g1)
    c: Coincident(g1,g2)
    c: Coincident(g2,g3)
    c: Coincident(g3,g4)
    c: Coincident(g4,g5)
    c: Coincident(g5,g0)
    c: Equal(g0, g1-g5) x5
    c: PointOnObject(g0,g6)
    c: PointOnObject(g1,g6)
    c: PointOnObject(g2,g6)
    c: PointOnObject(g3,g6)
    c: PointOnObject(g4,g6)
    c: PointOnObject(g5,g6)
    c: Coincident(g6,g-1)
    c: Coincident(g7,g6)
    c: Radius(g7) = 2.5
    c: Radius(g6) = 4
FEATURE [PartDesign::Pad] Pad174
  Direction = (1,-2e-16,3e-16)
  Length = 3
  Length2 = 10
  Placement = pos=(0,0,0) rot=(0.57735,0.57735,0.57735;2.0944rad)
  Profile = -> Sketch344
  Type = 0
FEATURE [PartDesign::Pad] Pad178
  BaseFeature = -> Pad174
  Direction = (1,-2e-16,6e-16)
  Length = 15
  Length2 = 10
  Placement = pos=(0,0,0) rot=(0.57735,0.57735,0.57735;2.0944rad)
  Profile = -> Pad174 [Edge20]
  Type = 0
FEATURE [PartDesign::Body] Body248
  Group = -> [Sketch344,Pad174,Pad178]
  Origin = -> Origin358
  Tip = -> Pad178
FEATURE [App::Part] Part109  label="tornillo M5-15-022"
  Group = -> [Body248]
  Origin = -> Origin356
  Placement = pos=(26,10,33) rot=(0,1,0;3.14159rad)
FEATURE [Sketcher::SketchObject] Sketch345
  FullyConstrained = false
  MapMode = 5
  Placement = pos=(0,0,0) rot=(0.57735,0.57735,0.57735;2.0944rad)
  Support = -> [YZ_Plane363]
  sketch-geometry (8):
    g0: LineSegment StartX=2.8963 StartY=-2.75889 StartZ=0 EndX=3.83742 EndY=1.12882 EndZ=0
    g1: LineSegment StartX=3.83742 StartY=1.12882 StartZ=0 EndX=0.941117 EndY=3.88771 EndZ=0
    g2: LineSegment StartX=0.941117 StartY=3.88771 StartZ=0 EndX=-2.8963 EndY=2.75889 EndZ=0
    g3: LineSegment StartX=-2.8963 StartY=2.75889 StartZ=0 EndX=-3.83742 EndY=-1.12882 EndZ=0
    g4: LineSegment StartX=-3.83742 StartY=-1.12882 StartZ=0 EndX=-0.941117 EndY=-3.88771 EndZ=0
    g5: LineSegment StartX=-0.941117 StartY=-3.88771 StartZ=0 EndX=2.8963 EndY=-2.75889 EndZ=0
    g6: Circle CenterX=0 CenterY=0 CenterZ=0 NormalX=0 NormalY=0 NormalZ=1 AngleXU=0 Radius=4
    g7: Circle CenterX=0 CenterY=0 CenterZ=0 NormalX=0 NormalY=0 NormalZ=1 AngleXU=0 Radius=2.5
  constraints (17):
    c: Coincident(g0,g1)
    c: Coincident(g1,g2)
    c: Coincident(g2,g3)
    c: Coincident(g3,g4)
    c: Coincident(g4,g5)
    c: Coincident(g5,g0)
    c: Equal(g0, g1-g5) x5
    c: PointOnObject(g0,g6)
    c: PointOnObject(g1,g6)
    c: PointOnObject(g2,g6)
    c: PointOnObject(g3,g6)
    c: PointOnObject(g4,g6)
    c: PointOnObject(g5,g6)
    c: Coincident(g6,g-1)
    c: Coincident(g7,g6)
    c: Radius(g7) = 2.5
    c: Radius(g6) = 4
FEATURE [PartDesign::Pad] Pad180
  Direction = (1,-2e-16,3e-16)
  Length = 3
  Length2 = 10
  Placement = pos=(0,0,0) rot=(0.57735,0.57735,0.57735;2.0944rad)
  Profile = -> Sketch345
  Type = 0
FEATURE [Sketcher::SketchObject] Sketch346
  FullyConstrained = false
  MapMode = 5
  Placement = pos=(0,0,0) rot=(0.57735,0.57735,0.57735;2.0944rad)
  Support = -> [YZ_Plane352]
  sketch-geometry (8):
    g0: LineSegment StartX=2.8963 StartY=-2.75889 StartZ=0 EndX=3.83742 EndY=1.12882 EndZ=0
    g1: LineSegment StartX=3.83742 StartY=1.12882 StartZ=0 EndX=0.941117 EndY=3.88771 EndZ=0
    g2: LineSegment StartX=0.941117 StartY=3.88771 StartZ=0 EndX=-2.8963 EndY=2.75889 EndZ=0
    g3: LineSegment StartX=-2.8963 StartY=2.75889 StartZ=0 EndX=-3.83742 EndY=-1.12882 EndZ=0
    g4: LineSegment StartX=-3.83742 StartY=-1.12882 StartZ=0 EndX=-0.941117 EndY=-3.88771 EndZ=0
    g5: LineSegment StartX=-0.941117 StartY=-3.88771 StartZ=0 EndX=2.8963 EndY=-2.75889 EndZ=0
    g6: Circle CenterX=0 CenterY=0 CenterZ=0 NormalX=0 NormalY=0 NormalZ=1 AngleXU=0 Radius=4
    g7: Circle CenterX=0 CenterY=0 CenterZ=0 NormalX=0 NormalY=0 NormalZ=1 AngleXU=0 Radius=2.5
  constraints (17):
    c: Coincident(g0,g1)
    c: Coincident(g1,g2)
    c: Coincident(g2,g3)
    c: Coincident(g3,g4)
    c: Coincident(g4,g5)
    c: Coincident(g5,g0)
    c: Equal(g0, g1-g5) x5
    c: PointOnObject(g0,g6)
    c: PointOnObject(g1,g6)
    c: PointOnObject(g2,g6)
    c: PointOnObject(g3,g6)
    c: PointOnObject(g4,g6)
    c: PointOnObject(g5,g6)
    c: Coincident(g6,g-1)
    c: Coincident(g7,g6)
    c: Radius(g7) = 2.5
    c: Radius(g6) = 4
FEATURE [PartDesign::Pad] Pad177
  Direction = (1,-2e-16,3e-16)
  Length = 3
  Length2 = 10
  Placement = pos=(0,0,0) rot=(0.57735,0.57735,0.57735;2.0944rad)
  Profile = -> Sketch346
  Type = 0
FEATURE [PartDesign::Pad] Pad181
  BaseFeature = -> Pad177
  Direction = (1,-2e-16,6e-16)
  Length = 15
  Length2 = 10
  Placement = pos=(0,0,0) rot=(0.57735,0.57735,0.57735;2.0944rad)
  Profile = -> Pad177 [Edge20]
  Type = 0
FEATURE [PartDesign::Body] Body249
  Group = -> [Sketch346,Pad177,Pad181]
  Origin = -> Origin361
  Tip = -> Pad181
FEATURE [App::Part] Part111  label="tornillo M5-15-024"
  Group = -> [Body249]
  Origin = -> Origin360
  Placement = pos=(26,10,159) rot=(0,1,0;3.14159rad)
FEATURE [Sketcher::SketchObject] Sketch347
  FullyConstrained = false
  MapMode = 5
  Placement = pos=(0,0,0) rot=(0.57735,0.57735,0.57735;2.0944rad)
  Support = -> [YZ_Plane361]
  sketch-geometry (8):
    g0: LineSegment StartX=2.8963 StartY=-2.75889 StartZ=0 EndX=3.83742 EndY=1.12882 EndZ=0
    g1: LineSegment StartX=3.83742 StartY=1.12882 StartZ=0 EndX=0.941117 EndY=3.88771 EndZ=0
    g2: LineSegment StartX=0.941117 StartY=3.88771 StartZ=0 EndX=-2.8963 EndY=2.75889 EndZ=0
    g3: LineSegment StartX=-2.8963 StartY=2.75889 StartZ=0 EndX=-3.83742 EndY=-1.12882 EndZ=0
    g4: LineSegment StartX=-3.83742 StartY=-1.12882 StartZ=0 EndX=-0.941117 EndY=-3.88771 EndZ=0
    g5: LineSegment StartX=-0.941117 StartY=-3.88771 StartZ=0 EndX=2.8963 EndY=-2.75889 EndZ=0
    g6: Circle CenterX=0 CenterY=0 CenterZ=0 NormalX=0 NormalY=0 NormalZ=1 AngleXU=0 Radius=4
    g7: Circle CenterX=0 CenterY=0 CenterZ=0 NormalX=0 NormalY=0 NormalZ=1 AngleXU=0 Radius=2.5
  constraints (17):
    c: Coincident(g0,g1)
    c: Coincident(g1,g2)
    c: Coincident(g2,g3)
    c: Coincident(g3,g4)
    c: Coincident(g4,g5)
    c: Coincident(g5,g0)
    c: Equal(g0, g1-g5) x5
    c: PointOnObject(g0,g6)
    c: PointOnObject(g1,g6)
    c: PointOnObject(g2,g6)
    c: PointOnObject(g3,g6)
    c: PointOnObject(g4,g6)
    c: PointOnObject(g5,g6)
    c: Coincident(g6,g-1)
    c: Coincident(g7,g6)
    c: Radius(g7) = 2.5
    c: Radius(g6) = 4
FEATURE [PartDesign::Pad] Pad179
  Direction = (1,-2e-16,3e-16)
  Length = 3
  Length2 = 10
  Placement = pos=(0,0,0) rot=(0.57735,0.57735,0.57735;2.0944rad)
  Profile = -> Sketch347
  Type = 0
FEATURE [Sketcher::SketchObject] Sketch348
  FullyConstrained = false
  MapMode = 5
  Placement = pos=(0,0,0) rot=(0.57735,0.57735,0.57735;2.0944rad)
  Support = -> [YZ_Plane355]
  sketch-geometry (8):
    g0: LineSegment StartX=2.8963 StartY=-2.75889 StartZ=0 EndX=3.83742 EndY=1.12882 EndZ=0
    g1: LineSegment StartX=3.83742 StartY=1.12882 StartZ=0 EndX=0.941117 EndY=3.88771 EndZ=0
    g2: LineSegment StartX=0.941117 StartY=3.88771 StartZ=0 EndX=-2.8963 EndY=2.75889 EndZ=0
    g3: LineSegment StartX=-2.8963 StartY=2.75889 StartZ=0 EndX=-3.83742 EndY=-1.12882 EndZ=0
    g4: LineSegment StartX=-3.83742 StartY=-1.12882 StartZ=0 EndX=-0.941117 EndY=-3.88771 EndZ=0
    g5: LineSegment StartX=-0.941117 StartY=-3.88771 StartZ=0 EndX=2.8963 EndY=-2.75889 EndZ=0
    g6: Circle CenterX=0 CenterY=0 CenterZ=0 NormalX=0 NormalY=0 NormalZ=1 AngleXU=0 Radius=4
    g7: Circle CenterX=0 CenterY=0 CenterZ=0 NormalX=0 NormalY=0 NormalZ=1 AngleXU=0 Radius=2.5
  constraints (17):
    c: Coincident(g0,g1)
    c: Coincident(g1,g2)
    c: Coincident(g2,g3)
    c: Coincident(g3,g4)
    c: Coincident(g4,g5)
    c: Coincident(g5,g0)
    c: Equal(g0, g1-g5) x5
    c: PointOnObject(g0,g6)
    c: PointOnObject(g1,g6)
    c: PointOnObject(g2,g6)
    c: PointOnObject(g3,g6)
    c: PointOnObject(g4,g6)
    c: PointOnObject(g5,g6)
    c: Coincident(g6,g-1)
    c: Coincident(g7,g6)
    c: Radius(g7) = 2.5
    c: Radius(g6) = 4
FEATURE [PartDesign::Pad] Pad184
  Direction = (1,-2e-16,3e-16)
  Length = 3
  Length2 = 10
  Placement = pos=(0,0,0) rot=(0.57735,0.57735,0.57735;2.0944rad)
  Profile = -> Sketch348
  Type = 0
FEATURE [PartDesign::Pad] Pad183
  BaseFeature = -> Pad184
  Direction = (1,-2e-16,6e-16)
  Length = 15
  Length2 = 10
  Placement = pos=(0,0,0) rot=(0.57735,0.57735,0.57735;2.0944rad)
  Profile = -> Pad184 [Edge20]
  Type = 0
FEATURE [PartDesign::Body] Body253
  Group = -> [Sketch348,Pad184,Pad183]
  Origin = -> Origin363
  Tip = -> Pad183
FEATURE [App::Part] Part110  label="tornillo M5-15-023"
  Group = -> [Body253]
  Origin = -> Origin362
  Placement = pos=(28.2334,9.96532,164.125) rot=(0.44435,-0.754393,0.483161;1.89214rad)
FEATURE [PartDesign::Pad] Pad185
  BaseFeature = -> Pad180
  Direction = (1,-2e-16,6e-16)
  Length = 15
  Length2 = 10
  Placement = pos=(0,0,0) rot=(0.57735,0.57735,0.57735;2.0944rad)
  Profile = -> Pad180 [Edge20]
  Type = 0
FEATURE [PartDesign::Body] Body250
  Group = -> [Sketch345,Pad180,Pad185]
  Origin = -> Origin365
  Tip = -> Pad185
FEATURE [App::Part] Part113  label="tornillo M5-15-026"
  Group = -> [Body250]
  Origin = -> Origin367
  Placement = pos=(31,10,26) rot=(0,1,0;1.5708rad)
FEATURE [PartDesign::Pad] Pad186
  BaseFeature = -> Pad179
  Direction = (1,-2e-16,6e-16)
  Length = 15
  Length2 = 10
  Placement = pos=(0,0,0) rot=(0.57735,0.57735,0.57735;2.0944rad)
  Profile = -> Pad179 [Edge20]
  Type = 0
FEATURE [PartDesign::Body] Body251
  Group = -> [Sketch347,Pad179,Pad186]
  Origin = -> Origin366
  Tip = -> Pad186
FEATURE [App::Part] Part112  label="tornillo M5-15-025"
  Group = -> [Body251]
  Origin = -> Origin355
  Placement = pos=(26,10,33) rot=(0,1,0;3.14159rad)
FEATURE [Sketcher::SketchObject] Sketch349
  FullyConstrained = false
  MapMode = 5
  Placement = pos=(0,0,0) rot=(0.57735,0.57735,0.57735;2.0944rad)
  Support = -> [YZ_Plane358]
  sketch-geometry (8):
    g0: LineSegment StartX=2.8963 StartY=-2.75889 StartZ=0 EndX=3.83742 EndY=1.12882 EndZ=0
    g1: LineSegment StartX=3.83742 StartY=1.12882 StartZ=0 EndX=0.941117 EndY=3.88771 EndZ=0
    g2: LineSegment StartX=0.941117 StartY=3.88771 StartZ=0 EndX=-2.8963 EndY=2.75889 EndZ=0
    g3: LineSegment StartX=-2.8963 StartY=2.75889 StartZ=0 EndX=-3.83742 EndY=-1.12882 EndZ=0
    g4: LineSegment StartX=-3.83742 StartY=-1.12882 StartZ=0 EndX=-0.941117 EndY=-3.88771 EndZ=0
    g5: LineSegment StartX=-0.941117 StartY=-3.88771 StartZ=0 EndX=2.8963 EndY=-2.75889 EndZ=0
    g6: Circle CenterX=0 CenterY=0 CenterZ=0 NormalX=0 NormalY=0 NormalZ=1 AngleXU=0 Radius=4
    g7: Circle CenterX=0 CenterY=0 CenterZ=0 NormalX=0 NormalY=0 NormalZ=1 AngleXU=0 Radius=2.5
  constraints (17):
    c: Coincident(g0,g1)
    c: Coincident(g1,g2)
    c: Coincident(g2,g3)
    c: Coincident(g3,g4)
    c: Coincident(g4,g5)
    c: Coincident(g5,g0)
    c: Equal(g0, g1-g5) x5
    c: PointOnObject(g0,g6)
    c: PointOnObject(g1,g6)
    c: PointOnObject(g2,g6)
    c: PointOnObject(g3,g6)
    c: PointOnObject(g4,g6)
    c: PointOnObject(g5,g6)
    c: Coincident(g6,g-1)
    c: Coincident(g7,g6)
    c: Radius(g7) = 2.5
    c: Radius(g6) = 4
FEATURE [PartDesign::Pad] Pad182
  Direction = (1,-2e-16,3e-16)
  Length = 3
  Length2 = 10
  Placement = pos=(0,0,0) rot=(0.57735,0.57735,0.57735;2.0944rad)
  Profile = -> Sketch349
  Type = 0
FEATURE [PartDesign::Pad] Pad187
  BaseFeature = -> Pad182
  Direction = (1,-2e-16,6e-16)
  Length = 15
  Length2 = 10
  Placement = pos=(0,0,0) rot=(0.57735,0.57735,0.57735;2.0944rad)
  Profile = -> Pad182 [Edge20]
  Type = 0
FEATURE [PartDesign::Body] Body252
  Group = -> [Sketch349,Pad182,Pad187]
  Origin = -> Origin369
  Tip = -> Pad187
FEATURE [App::Part] Part115  label="tornillo M5-15-028"
  Group = -> [Body252]
  Origin = -> Origin368
  Placement = pos=(26,10,159) rot=(0,1,0;3.14159rad)
FEATURE [Sketcher::SketchObject] Sketch350
  FullyConstrained = false
  MapMode = 5
  Placement = pos=(0,0,0) rot=(0.57735,0.57735,0.57735;2.0944rad)
  Support = -> [YZ_Plane356]
  sketch-geometry (8):
    g0: LineSegment StartX=2.8963 StartY=-2.75889 StartZ=0 EndX=3.83742 EndY=1.12882 EndZ=0
    g1: LineSegment StartX=3.83742 StartY=1.12882 StartZ=0 EndX=0.941117 EndY=3.88771 EndZ=0
    g2: LineSegment StartX=0.941117 StartY=3.88771 StartZ=0 EndX=-2.8963 EndY=2.75889 EndZ=0
    g3: LineSegment StartX=-2.8963 StartY=2.75889 StartZ=0 EndX=-3.83742 EndY=-1.12882 EndZ=0
    g4: LineSegment StartX=-3.83742 StartY=-1.12882 StartZ=0 EndX=-0.941117 EndY=-3.88771 EndZ=0
    g5: LineSegment StartX=-0.941117 StartY=-3.88771 StartZ=0 EndX=2.8963 EndY=-2.75889 EndZ=0
    g6: Circle CenterX=0 CenterY=0 CenterZ=0 NormalX=0 NormalY=0 NormalZ=1 AngleXU=0 Radius=4
    g7: Circle CenterX=0 CenterY=0 CenterZ=0 NormalX=0 NormalY=0 NormalZ=1 AngleXU=0 Radius=2.5
  constraints (17):
    c: Coincident(g0,g1)
    c: Coincident(g1,g2)
    c: Coincident(g2,g3)
    c: Coincident(g3,g4)
    c: Coincident(g4,g5)
    c: Coincident(g5,g0)
    c: Equal(g0, g1-g5) x5
    c: PointOnObject(g0,g6)
    c: PointOnObject(g1,g6)
    c: PointOnObject(g2,g6)
    c: PointOnObject(g3,g6)
    c: PointOnObject(g4,g6)
    c: PointOnObject(g5,g6)
    c: Coincident(g6,g-1)
    c: Coincident(g7,g6)
    c: Radius(g7) = 2.5
    c: Radius(g6) = 4
FEATURE [PartDesign::Pad] Pad189
  Direction = (1,-2e-16,3e-16)
  Length = 3
  Length2 = 10
  Placement = pos=(0,0,0) rot=(0.57735,0.57735,0.57735;2.0944rad)
  Profile = -> Sketch350
  Type = 0
FEATURE [PartDesign::Pad] Pad188
  BaseFeature = -> Pad189
  Direction = (1,-2e-16,6e-16)
  Length = 15
  Length2 = 10
  Placement = pos=(0,0,0) rot=(0.57735,0.57735,0.57735;2.0944rad)
  Profile = -> Pad189 [Edge20]
  Type = 0
FEATURE [PartDesign::Body] Body254
  Group = -> [Sketch350,Pad189,Pad188]
  Origin = -> Origin370
  Tip = -> Pad188
FEATURE [App::Part] Part114  label="tornillo M5-15-027"
  Group = -> [Body254]
  Origin = -> Origin364
  Placement = pos=(28.2334,9.96532,164.125) rot=(0.44435,-0.754393,0.483161;1.89214rad)
FEATURE [App::LinkGroup] LinkGroup022
  ElementList = -> [Part113,Part112,Part114,Part115]
  LinkMode = 0
  Placement = pos=(339.888,20.1907,1.52588e-05) rot=(0,0,1;3.14159rad)
FEATURE [App::LinkGroup] LinkGroup023
  ElementList = -> [Part108,Part109,Part111,Part110,LinkGroup022]
  LinkMode = 0
  Placement = pos=(-1.52588e-05,319,-7.62939e-06) rot=(0,0,1;0rad)
FEATURE [Sketcher::SketchObject] Sketch351
  FullyConstrained = false
  MapMode = 5
  Placement = pos=(0,0,0) rot=(0.57735,0.57735,0.57735;2.0944rad)
  Support = -> [YZ_Plane366]
  sketch-geometry (8):
    g0: LineSegment StartX=2.8963 StartY=-2.75889 StartZ=0 EndX=3.83742 EndY=1.12882 EndZ=0
    g1: LineSegment StartX=3.83742 StartY=1.12882 StartZ=0 EndX=0.941117 EndY=3.88771 EndZ=0
    g2: LineSegment StartX=0.941117 StartY=3.88771 StartZ=0 EndX=-2.8963 EndY=2.75889 EndZ=0
    g3: LineSegment StartX=-2.8963 StartY=2.75889 StartZ=0 EndX=-3.83742 EndY=-1.12882 EndZ=0
    g4: LineSegment StartX=-3.83742 StartY=-1.12882 StartZ=0 EndX=-0.941117 EndY=-3.88771 EndZ=0
    g5: LineSegment StartX=-0.941117 StartY=-3.88771 StartZ=0 EndX=2.8963 EndY=-2.75889 EndZ=0
    g6: Circle CenterX=0 CenterY=0 CenterZ=0 NormalX=0 NormalY=0 NormalZ=1 AngleXU=0 Radius=4
    g7: Circle CenterX=0 CenterY=0 CenterZ=0 NormalX=0 NormalY=0 NormalZ=1 AngleXU=0 Radius=2.5
  constraints (17):
    c: Coincident(g0,g1)
    c: Coincident(g1,g2)
    c: Coincident(g2,g3)
    c: Coincident(g3,g4)
    c: Coincident(g4,g5)
    c: Coincident(g5,g0)
    c: Equal(g0, g1-g5) x5
    c: PointOnObject(g0,g6)
    c: PointOnObject(g1,g6)
    c: PointOnObject(g2,g6)
    c: PointOnObject(g3,g6)
    c: PointOnObject(g4,g6)
    c: PointOnObject(g5,g6)
    c: Coincident(g6,g-1)
    c: Coincident(g7,g6)
    c: Radius(g7) = 2.5
    c: Radius(g6) = 4
FEATURE [PartDesign::Pad] Pad190
  Direction = (1,-2e-16,3e-16)
  Length = 3
  Length2 = 10
  Placement = pos=(0,0,0) rot=(0.57735,0.57735,0.57735;2.0944rad)
  Profile = -> Sketch351
  Type = 0
FEATURE [PartDesign::Pad] Pad191
  BaseFeature = -> Pad190
  Direction = (1,-2e-16,6e-16)
  Length = 15
  Length2 = 10
  Placement = pos=(0,0,0) rot=(0.57735,0.57735,0.57735;2.0944rad)
  Profile = -> Pad190 [Edge20]
  Type = 0
FEATURE [PartDesign::Body] Body255
  Group = -> [Sketch351,Pad190,Pad191]
  Origin = -> Origin372
  Tip = -> Pad191
FEATURE [App::Part] Part116  label="tornillo M5-15-029"
  Group = -> [Body255]
  Origin = -> Origin371
  Placement = pos=(327,28,57) rot=(0.707107,-0.707107,0;3.14159rad)
FEATURE [Sketcher::SketchObject] Sketch352
  FullyConstrained = false
  MapMode = 5
  Placement = pos=(0,0,0) rot=(0.57735,0.57735,0.57735;2.0944rad)
  Support = -> [YZ_Plane367]
  sketch-geometry (8):
    g0: LineSegment StartX=2.8963 StartY=-2.75889 StartZ=0 EndX=3.83742 EndY=1.12882 EndZ=0
    g1: LineSegment StartX=3.83742 StartY=1.12882 StartZ=0 EndX=0.941117 EndY=3.88771 EndZ=0
    g2: LineSegment StartX=0.941117 StartY=3.88771 StartZ=0 EndX=-2.8963 EndY=2.75889 EndZ=0
    g3: LineSegment StartX=-2.8963 StartY=2.75889 StartZ=0 EndX=-3.83742 EndY=-1.12882 EndZ=0
    g4: LineSegment StartX=-3.83742 StartY=-1.12882 StartZ=0 EndX=-0.941117 EndY=-3.88771 EndZ=0
    g5: LineSegment StartX=-0.941117 StartY=-3.88771 StartZ=0 EndX=2.8963 EndY=-2.75889 EndZ=0
    g6: Circle CenterX=0 CenterY=0 CenterZ=0 NormalX=0 NormalY=0 NormalZ=1 AngleXU=0 Radius=4
    g7: Circle CenterX=0 CenterY=0 CenterZ=0 NormalX=0 NormalY=0 NormalZ=1 AngleXU=0 Radius=2.5
  constraints (17):
    c: Coincident(g0,g1)
    c: Coincident(g1,g2)
    c: Coincident(g2,g3)
    c: Coincident(g3,g4)
    c: Coincident(g4,g5)
    c: Coincident(g5,g0)
    c: Equal(g0, g1-g5) x5
    c: PointOnObject(g0,g6)
    c: PointOnObject(g1,g6)
    c: PointOnObject(g2,g6)
    c: PointOnObject(g3,g6)
    c: PointOnObject(g4,g6)
    c: PointOnObject(g5,g6)
    c: Coincident(g6,g-1)
    c: Coincident(g7,g6)
    c: Radius(g7) = 2.5
    c: Radius(g6) = 4
FEATURE [PartDesign::Pad] Pad192
  Direction = (1,-2e-16,3e-16)
  Length = 3
  Length2 = 10
  Placement = pos=(0,0,0) rot=(0.57735,0.57735,0.57735;2.0944rad)
  Profile = -> Sketch352
  Type = 0
FEATURE [PartDesign::Pad] Pad193
  BaseFeature = -> Pad192
  Direction = (1,-2e-16,6e-16)
  Length = 15
  Length2 = 10
  Placement = pos=(0,0,0) rot=(0.57735,0.57735,0.57735;2.0944rad)
  Profile = -> Pad192 [Edge20]
  Type = 0
FEATURE [PartDesign::Body] Body256
  Group = -> [Sketch352,Pad192,Pad193]
  Origin = -> Origin374
  Tip = -> Pad193
FEATURE [App::Part] Part117  label="tornillo M5-15-030"
  Group = -> [Body256]
  Origin = -> Origin373
  Placement = pos=(328,31,64) rot=(-0.57735,0.57735,-0.57735;4.18879rad)
FEATURE [App::LinkGroup] LinkGroup024
  ElementList = -> [Part116,Part117]
  LinkMode = 0
FEATURE [Sketcher::SketchObject] Sketch353
  FullyConstrained = false
  MapMode = 5
  Placement = pos=(0,0,0) rot=(0.57735,0.57735,0.57735;2.0944rad)
  Support = -> [YZ_Plane370]
  sketch-geometry (8):
    g0: LineSegment StartX=2.8963 StartY=-2.75889 StartZ=0 EndX=3.83742 EndY=1.12882 EndZ=0
    g1: LineSegment StartX=3.83742 StartY=1.12882 StartZ=0 EndX=0.941117 EndY=3.88771 EndZ=0
    g2: LineSegment StartX=0.941117 StartY=3.88771 StartZ=0 EndX=-2.8963 EndY=2.75889 EndZ=0
    g3: LineSegment StartX=-2.8963 StartY=2.75889 StartZ=0 EndX=-3.83742 EndY=-1.12882 EndZ=0
    g4: LineSegment StartX=-3.83742 StartY=-1.12882 StartZ=0 EndX=-0.941117 EndY=-3.88771 EndZ=0
    g5: LineSegment StartX=-0.941117 StartY=-3.88771 StartZ=0 EndX=2.8963 EndY=-2.75889 EndZ=0
    g6: Circle CenterX=0 CenterY=0 CenterZ=0 NormalX=0 NormalY=0 NormalZ=1 AngleXU=0 Radius=4
    g7: Circle CenterX=0 CenterY=0 CenterZ=0 NormalX=0 NormalY=0 NormalZ=1 AngleXU=0 Radius=2.5
  constraints (17):
    c: Coincident(g0,g1)
    c: Coincident(g1,g2)
    c: Coincident(g2,g3)
    c: Coincident(g3,g4)
    c: Coincident(g4,g5)
    c: Coincident(g5,g0)
    c: Equal(g0, g1-g5) x5
    c: PointOnObject(g0,g6)
    c: PointOnObject(g1,g6)
    c: PointOnObject(g2,g6)
    c: PointOnObject(g3,g6)
    c: PointOnObject(g4,g6)
    c: PointOnObject(g5,g6)
    c: Coincident(g6,g-1)
    c: Coincident(g7,g6)
    c: Radius(g7) = 2.5
    c: Radius(g6) = 4
FEATURE [PartDesign::Pad] Pad195
  Direction = (1,-2e-16,3e-16)
  Length = 3
  Length2 = 10
  Placement = pos=(0,0,0) rot=(0.57735,0.57735,0.57735;2.0944rad)
  Profile = -> Sketch353
  Type = 0
FEATURE [PartDesign::Pad] Pad196
  BaseFeature = -> Pad195
  Direction = (1,-2e-16,6e-16)
  Length = 15
  Length2 = 10
  Placement = pos=(0,0,0) rot=(0.57735,0.57735,0.57735;2.0944rad)
  Profile = -> Pad195 [Edge20]
  Type = 0
FEATURE [PartDesign::Body] Body258
  Group = -> [Sketch353,Pad195,Pad196]
  Origin = -> Origin378
  Tip = -> Pad196
FEATURE [App::Part] Part118  label="tornillo M5-15-031"
  Group = -> [Body258]
  Origin = -> Origin375
  Placement = pos=(327,28,57) rot=(0.707107,-0.707107,0;3.14159rad)
FEATURE [Sketcher::SketchObject] Sketch354
  FullyConstrained = false
  MapMode = 5
  Placement = pos=(0,0,0) rot=(0.57735,0.57735,0.57735;2.0944rad)
  Support = -> [YZ_Plane369]
  sketch-geometry (8):
    g0: LineSegment StartX=2.8963 StartY=-2.75889 StartZ=0 EndX=3.83742 EndY=1.12882 EndZ=0
    g1: LineSegment StartX=3.83742 StartY=1.12882 StartZ=0 EndX=0.941117 EndY=3.88771 EndZ=0
    g2: LineSegment StartX=0.941117 StartY=3.88771 StartZ=0 EndX=-2.8963 EndY=2.75889 EndZ=0
    g3: LineSegment StartX=-2.8963 StartY=2.75889 StartZ=0 EndX=-3.83742 EndY=-1.12882 EndZ=0
    g4: LineSegment StartX=-3.83742 StartY=-1.12882 StartZ=0 EndX=-0.941117 EndY=-3.88771 EndZ=0
    g5: LineSegment StartX=-0.941117 StartY=-3.88771 StartZ=0 EndX=2.8963 EndY=-2.75889 EndZ=0
    g6: Circle CenterX=0 CenterY=0 CenterZ=0 NormalX=0 NormalY=0 NormalZ=1 AngleXU=0 Radius=4
    g7: Circle CenterX=0 CenterY=0 CenterZ=0 NormalX=0 NormalY=0 NormalZ=1 AngleXU=0 Radius=2.5
  constraints (17):
    c: Coincident(g0,g1)
    c: Coincident(g1,g2)
    c: Coincident(g2,g3)
    c: Coincident(g3,g4)
    c: Coincident(g4,g5)
    c: Coincident(g5,g0)
    c: Equal(g0, g1-g5) x5
    c: PointOnObject(g0,g6)
    c: PointOnObject(g1,g6)
    c: PointOnObject(g2,g6)
    c: PointOnObject(g3,g6)
    c: PointOnObject(g4,g6)
    c: PointOnObject(g5,g6)
    c: Coincident(g6,g-1)
    c: Coincident(g7,g6)
    c: Radius(g7) = 2.5
    c: Radius(g6) = 4
FEATURE [PartDesign::Pad] Pad197
  Direction = (1,-2e-16,3e-16)
  Length = 3
  Length2 = 10
  Placement = pos=(0,0,0) rot=(0.57735,0.57735,0.57735;2.0944rad)
  Profile = -> Sketch354
  Type = 0
FEATURE [PartDesign::Pad] Pad194
  BaseFeature = -> Pad197
  Direction = (1,-2e-16,6e-16)
  Length = 15
  Length2 = 10
  Placement = pos=(0,0,0) rot=(0.57735,0.57735,0.57735;2.0944rad)
  Profile = -> Pad197 [Edge20]
  Type = 0
FEATURE [PartDesign::Body] Body257
  Group = -> [Sketch354,Pad197,Pad194]
  Origin = -> Origin377
  Tip = -> Pad194
FEATURE [App::Part] Part119  label="tornillo M5-15-032"
  Group = -> [Body257]
  Origin = -> Origin376
  Placement = pos=(328,31,64) rot=(-0.57735,0.57735,-0.57735;4.18879rad)
FEATURE [App::LinkGroup] LinkGroup025
  ElementList = -> [Part118,Part119]
  LinkMode = 0
  Placement = pos=(658,341.888,-7.62939e-06) rot=(0,0,1;3.14159rad)
FEATURE [Sketcher::SketchObject] Sketch355
  FullyConstrained = false
  MapMode = 5
  Placement = pos=(0,0,0) rot=(0.57735,0.57735,0.57735;2.0944rad)
  Support = -> [YZ_Plane374]
  sketch-geometry (8):
    g0: LineSegment StartX=2.8963 StartY=-2.75889 StartZ=0 EndX=3.83742 EndY=1.12882 EndZ=0
    g1: LineSegment StartX=3.83742 StartY=1.12882 StartZ=0 EndX=0.941117 EndY=3.88771 EndZ=0
    g2: LineSegment StartX=0.941117 StartY=3.88771 StartZ=0 EndX=-2.8963 EndY=2.75889 EndZ=0
    g3: LineSegment StartX=-2.8963 StartY=2.75889 StartZ=0 EndX=-3.83742 EndY=-1.12882 EndZ=0
    g4: LineSegment StartX=-3.83742 StartY=-1.12882 StartZ=0 EndX=-0.941117 EndY=-3.88771 EndZ=0
    g5: LineSegment StartX=-0.941117 StartY=-3.88771 StartZ=0 EndX=2.8963 EndY=-2.75889 EndZ=0
    g6: Circle CenterX=0 CenterY=0 CenterZ=0 NormalX=0 NormalY=0 NormalZ=1 AngleXU=0 Radius=4
    g7: Circle CenterX=0 CenterY=0 CenterZ=0 NormalX=0 NormalY=0 NormalZ=1 AngleXU=0 Radius=2.5
  constraints (17):
    c: Coincident(g0,g1)
    c: Coincident(g1,g2)
    c: Coincident(g2,g3)
    c: Coincident(g3,g4)
    c: Coincident(g4,g5)
    c: Coincident(g5,g0)
    c: Equal(g0, g1-g5) x5
    c: PointOnObject(g0,g6)
    c: PointOnObject(g1,g6)
    c: PointOnObject(g2,g6)
    c: PointOnObject(g3,g6)
    c: PointOnObject(g4,g6)
    c: PointOnObject(g5,g6)
    c: Coincident(g6,g-1)
    c: Coincident(g7,g6)
    c: Radius(g7) = 2.5
    c: Radius(g6) = 4
FEATURE [PartDesign::Pad] Pad198
  Direction = (1,-2e-16,3e-16)
  Length = 3
  Length2 = 10
  Placement = pos=(0,0,0) rot=(0.57735,0.57735,0.57735;2.0944rad)
  Profile = -> Sketch355
  Type = 0
FEATURE [PartDesign::Pad] Pad199
  BaseFeature = -> Pad198
  Direction = (1,-2e-16,6e-16)
  Length = 15
  Length2 = 10
  Placement = pos=(0,0,0) rot=(0.57735,0.57735,0.57735;2.0944rad)
  Profile = -> Pad198 [Edge20]
  Type = 0
FEATURE [PartDesign::Body] Body259
  Group = -> [Sketch355,Pad198,Pad199]
  Origin = -> Origin380
  Tip = -> Pad199
FEATURE [App::Part] Part120  label="tornillo M5-15-033"
  Group = -> [Body259]
  Origin = -> Origin379
  Placement = pos=(357,108,88) rot=(0,1,0;1.5708rad)
FEATURE [Sketcher::SketchObject] Sketch356
  FullyConstrained = false
  MapMode = 5
  Placement = pos=(0,0,0) rot=(0.57735,0.57735,0.57735;2.0944rad)
  Support = -> [YZ_Plane375]
  sketch-geometry (8):
    g0: LineSegment StartX=2.8963 StartY=-2.75889 StartZ=0 EndX=3.83742 EndY=1.12882 EndZ=0
    g1: LineSegment StartX=3.83742 StartY=1.12882 StartZ=0 EndX=0.941117 EndY=3.88771 EndZ=0
    g2: LineSegment StartX=0.941117 StartY=3.88771 StartZ=0 EndX=-2.8963 EndY=2.75889 EndZ=0
    g3: LineSegment StartX=-2.8963 StartY=2.75889 StartZ=0 EndX=-3.83742 EndY=-1.12882 EndZ=0
    g4: LineSegment StartX=-3.83742 StartY=-1.12882 StartZ=0 EndX=-0.941117 EndY=-3.88771 EndZ=0
    g5: LineSegment StartX=-0.941117 StartY=-3.88771 StartZ=0 EndX=2.8963 EndY=-2.75889 EndZ=0
    g6: Circle CenterX=0 CenterY=0 CenterZ=0 NormalX=0 NormalY=0 NormalZ=1 AngleXU=0 Radius=4
    g7: Circle CenterX=0 CenterY=0 CenterZ=0 NormalX=0 NormalY=0 NormalZ=1 AngleXU=0 Radius=2.5
  constraints (17):
    c: Coincident(g0,g1)
    c: Coincident(g1,g2)
    c: Coincident(g2,g3)
    c: Coincident(g3,g4)
    c: Coincident(g4,g5)
    c: Coincident(g5,g0)
    c: Equal(g0, g1-g5) x5
    c: PointOnObject(g0,g6)
    c: PointOnObject(g1,g6)
    c: PointOnObject(g2,g6)
    c: PointOnObject(g3,g6)
    c: PointOnObject(g4,g6)
    c: PointOnObject(g5,g6)
    c: Coincident(g6,g-1)
    c: Coincident(g7,g6)
    c: Radius(g7) = 2.5
    c: Radius(g6) = 4
FEATURE [PartDesign::Pad] Pad200
  Direction = (1,-2e-16,3e-16)
  Length = 3
  Length2 = 10
  Placement = pos=(0,0,0) rot=(0.57735,0.57735,0.57735;2.0944rad)
  Profile = -> Sketch356
  Type = 0
FEATURE [PartDesign::Pad] Pad201
  BaseFeature = -> Pad200
  Direction = (1,-2e-16,6e-16)
  Length = 15
  Length2 = 10
  Placement = pos=(0,0,0) rot=(0.57735,0.57735,0.57735;2.0944rad)
  Profile = -> Pad200 [Edge20]
  Type = 0
FEATURE [PartDesign::Body] Body260
  Group = -> [Sketch356,Pad200,Pad201]
  Origin = -> Origin382
  Tip = -> Pad201
FEATURE [App::Part] Part121  label="tornillo M5-15-034"
  Group = -> [Body260]
  Origin = -> Origin381
  Placement = pos=(379,108,88) rot=(0,1,0;1.5708rad)
FEATURE [Sketcher::SketchObject] Sketch357
  FullyConstrained = false
  MapMode = 5
  Placement = pos=(0,0,0) rot=(0.57735,0.57735,0.57735;2.0944rad)
  Support = -> [YZ_Plane380]
  sketch-geometry (8):
    g0: LineSegment StartX=2.8963 StartY=-2.75889 StartZ=0 EndX=3.83742 EndY=1.12882 EndZ=0
    g1: LineSegment StartX=3.83742 StartY=1.12882 StartZ=0 EndX=0.941117 EndY=3.88771 EndZ=0
    g2: LineSegment StartX=0.941117 StartY=3.88771 StartZ=0 EndX=-2.8963 EndY=2.75889 EndZ=0
    g3: LineSegment StartX=-2.8963 StartY=2.75889 StartZ=0 EndX=-3.83742 EndY=-1.12882 EndZ=0
    g4: LineSegment StartX=-3.83742 StartY=-1.12882 StartZ=0 EndX=-0.941117 EndY=-3.88771 EndZ=0
    g5: LineSegment StartX=-0.941117 StartY=-3.88771 StartZ=0 EndX=2.8963 EndY=-2.75889 EndZ=0
    g6: Circle CenterX=0 CenterY=0 CenterZ=0 NormalX=0 NormalY=0 NormalZ=1 AngleXU=0 Radius=4
    g7: Circle CenterX=0 CenterY=0 CenterZ=0 NormalX=0 NormalY=0 NormalZ=1 AngleXU=0 Radius=2.5
  constraints (17):
    c: Coincident(g0,g1)
    c: Coincident(g1,g2)
    c: Coincident(g2,g3)
    c: Coincident(g3,g4)
    c: Coincident(g4,g5)
    c: Coincident(g5,g0)
    c: Equal(g0, g1-g5) x5
    c: PointOnObject(g0,g6)
    c: PointOnObject(g1,g6)
    c: PointOnObject(g2,g6)
    c: PointOnObject(g3,g6)
    c: PointOnObject(g4,g6)
    c: PointOnObject(g5,g6)
    c: Coincident(g6,g-1)
    c: Coincident(g7,g6)
    c: Radius(g7) = 2.5
    c: Radius(g6) = 4
FEATURE [PartDesign::Pad] Pad202
  Direction = (1,-2e-16,3e-16)
  Length = 3
  Length2 = 10
  Placement = pos=(0,0,0) rot=(0.57735,0.57735,0.57735;2.0944rad)
  Profile = -> Sketch357
  Type = 0
FEATURE [Sketcher::SketchObject] Sketch358
  FullyConstrained = false
  MapMode = 5
  Placement = pos=(0,0,0) rot=(0.57735,0.57735,0.57735;2.0944rad)
  Support = -> [YZ_Plane378]
  sketch-geometry (8):
    g0: LineSegment StartX=2.8963 StartY=-2.75889 StartZ=0 EndX=3.83742 EndY=1.12882 EndZ=0
    g1: LineSegment StartX=3.83742 StartY=1.12882 StartZ=0 EndX=0.941117 EndY=3.88771 EndZ=0
    g2: LineSegment StartX=0.941117 StartY=3.88771 StartZ=0 EndX=-2.8963 EndY=2.75889 EndZ=0
    g3: LineSegment StartX=-2.8963 StartY=2.75889 StartZ=0 EndX=-3.83742 EndY=-1.12882 EndZ=0
    g4: LineSegment StartX=-3.83742 StartY=-1.12882 StartZ=0 EndX=-0.941117 EndY=-3.88771 EndZ=0
    g5: LineSegment StartX=-0.941117 StartY=-3.88771 StartZ=0 EndX=2.8963 EndY=-2.75889 EndZ=0
    g6: Circle CenterX=0 CenterY=0 CenterZ=0 NormalX=0 NormalY=0 NormalZ=1 AngleXU=0 Radius=4
    g7: Circle CenterX=0 CenterY=0 CenterZ=0 NormalX=0 NormalY=0 NormalZ=1 AngleXU=0 Radius=2.5
  constraints (17):
    c: Coincident(g0,g1)
    c: Coincident(g1,g2)
    c: Coincident(g2,g3)
    c: Coincident(g3,g4)
    c: Coincident(g4,g5)
    c: Coincident(g5,g0)
    c: Equal(g0, g1-g5) x5
    c: PointOnObject(g0,g6)
    c: PointOnObject(g1,g6)
    c: PointOnObject(g2,g6)
    c: PointOnObject(g3,g6)
    c: PointOnObject(g4,g6)
    c: PointOnObject(g5,g6)
    c: Coincident(g6,g-1)
    c: Coincident(g7,g6)
    c: Radius(g7) = 2.5
    c: Radius(g6) = 4
FEATURE [PartDesign::Pad] Pad203
  Direction = (1,-2e-16,3e-16)
  Length = 3
  Length2 = 10
  Placement = pos=(0,0,0) rot=(0.57735,0.57735,0.57735;2.0944rad)
  Profile = -> Sketch358
  Type = 0
FEATURE [PartDesign::Pad] Pad204
  BaseFeature = -> Pad203
  Direction = (1,-2e-16,6e-16)
  Length = 15
  Length2 = 10
  Placement = pos=(0,0,0) rot=(0.57735,0.57735,0.57735;2.0944rad)
  Profile = -> Pad203 [Edge20]
  Type = 0
FEATURE [PartDesign::Body] Body262
  Group = -> [Sketch358,Pad203,Pad204]
  Origin = -> Origin385
  Tip = -> Pad204
FEATURE [App::Part] Part122  label="tornillo M5-15-035"
  Group = -> [Body262]
  Origin = -> Origin383
  Placement = pos=(357,108,88) rot=(0,1,0;1.5708rad)
FEATURE [PartDesign::Pad] Pad205
  BaseFeature = -> Pad202
  Direction = (1,-2e-16,6e-16)
  Length = 15
  Length2 = 10
  Placement = pos=(0,0,0) rot=(0.57735,0.57735,0.57735;2.0944rad)
  Profile = -> Pad202 [Edge20]
  Type = 0
FEATURE [PartDesign::Body] Body261
  Group = -> [Sketch357,Pad202,Pad205]
  Origin = -> Origin384
  Tip = -> Pad205
FEATURE [App::Part] Part123  label="tornillo M5-15-036"
  Group = -> [Body261]
  Origin = -> Origin386
  Placement = pos=(379,108,88) rot=(0,1,0;1.5708rad)
FEATURE [App::LinkGroup] LinkGroup026
  ElementList = -> [Part122,Part123]
  LinkMode = 0
  Placement = pos=(0,25,0) rot=(0,0,1;0rad)
FEATURE [App::LinkGroup] LinkGroup027
  ElementList = -> [Part120,Part121,LinkGroup026]
  LinkMode = 0
FEATURE [Sketcher::SketchObject] Sketch359
  FullyConstrained = false
  MapMode = 5
  Placement = pos=(0,0,0) rot=(0.57735,0.57735,0.57735;2.0944rad)
  Support = -> [YZ_Plane383]
  sketch-geometry (8):
    g0: LineSegment StartX=2.8963 StartY=-2.75889 StartZ=0 EndX=3.83742 EndY=1.12882 EndZ=0
    g1: LineSegment StartX=3.83742 StartY=1.12882 StartZ=0 EndX=0.941117 EndY=3.88771 EndZ=0
    g2: LineSegment StartX=0.941117 StartY=3.88771 StartZ=0 EndX=-2.8963 EndY=2.75889 EndZ=0
    g3: LineSegment StartX=-2.8963 StartY=2.75889 StartZ=0 EndX=-3.83742 EndY=-1.12882 EndZ=0
    g4: LineSegment StartX=-3.83742 StartY=-1.12882 StartZ=0 EndX=-0.941117 EndY=-3.88771 EndZ=0
    g5: LineSegment StartX=-0.941117 StartY=-3.88771 StartZ=0 EndX=2.8963 EndY=-2.75889 EndZ=0
    g6: Circle CenterX=0 CenterY=0 CenterZ=0 NormalX=0 NormalY=0 NormalZ=1 AngleXU=0 Radius=4
    g7: Circle CenterX=0 CenterY=0 CenterZ=0 NormalX=0 NormalY=0 NormalZ=1 AngleXU=0 Radius=2.5
  constraints (17):
    c: Coincident(g0,g1)
    c: Coincident(g1,g2)
    c: Coincident(g2,g3)
    c: Coincident(g3,g4)
    c: Coincident(g4,g5)
    c: Coincident(g5,g0)
    c: Equal(g0, g1-g5) x5
    c: PointOnObject(g0,g6)
    c: PointOnObject(g1,g6)
    c: PointOnObject(g2,g6)
    c: PointOnObject(g3,g6)
    c: PointOnObject(g4,g6)
    c: PointOnObject(g5,g6)
    c: Coincident(g6,g-1)
    c: Coincident(g7,g6)
    c: Radius(g7) = 2.5
    c: Radius(g6) = 4
FEATURE [PartDesign::Pad] Pad208
  Direction = (1,-2e-16,3e-16)
  Length = 3
  Length2 = 10
  Placement = pos=(0,0,0) rot=(0.57735,0.57735,0.57735;2.0944rad)
  Profile = -> Sketch359
  Type = 0
FEATURE [Sketcher::SketchObject] Sketch360
  FullyConstrained = false
  MapMode = 5
  Placement = pos=(0,0,0) rot=(0.57735,0.57735,0.57735;2.0944rad)
  Support = -> [YZ_Plane386]
  sketch-geometry (8):
    g0: LineSegment StartX=2.8963 StartY=-2.75889 StartZ=0 EndX=3.83742 EndY=1.12882 EndZ=0
    g1: LineSegment StartX=3.83742 StartY=1.12882 StartZ=0 EndX=0.941117 EndY=3.88771 EndZ=0
    g2: LineSegment StartX=0.941117 StartY=3.88771 StartZ=0 EndX=-2.8963 EndY=2.75889 EndZ=0
    g3: LineSegment StartX=-2.8963 StartY=2.75889 StartZ=0 EndX=-3.83742 EndY=-1.12882 EndZ=0
    g4: LineSegment StartX=-3.83742 StartY=-1.12882 StartZ=0 EndX=-0.941117 EndY=-3.88771 EndZ=0
    g5: LineSegment StartX=-0.941117 StartY=-3.88771 StartZ=0 EndX=2.8963 EndY=-2.75889 EndZ=0
    g6: Circle CenterX=0 CenterY=0 CenterZ=0 NormalX=0 NormalY=0 NormalZ=1 AngleXU=0 Radius=4
    g7: Circle CenterX=0 CenterY=0 CenterZ=0 NormalX=0 NormalY=0 NormalZ=1 AngleXU=0 Radius=2.5
  constraints (17):
    c: Coincident(g0,g1)
    c: Coincident(g1,g2)
    c: Coincident(g2,g3)
    c: Coincident(g3,g4)
    c: Coincident(g4,g5)
    c: Coincident(g5,g0)
    c: Equal(g0, g1-g5) x5
    c: PointOnObject(g0,g6)
    c: PointOnObject(g1,g6)
    c: PointOnObject(g2,g6)
    c: PointOnObject(g3,g6)
    c: PointOnObject(g4,g6)
    c: PointOnObject(g5,g6)
    c: Coincident(g6,g-1)
    c: Coincident(g7,g6)
    c: Radius(g7) = 2.5
    c: Radius(g6) = 4
FEATURE [PartDesign::Pad] Pad206
  Direction = (1,-2e-16,3e-16)
  Length = 3
  Length2 = 10
  Placement = pos=(0,0,0) rot=(0.57735,0.57735,0.57735;2.0944rad)
  Profile = -> Sketch360
  Type = 0
FEATURE [Sketcher::SketchObject] Sketch361
  FullyConstrained = false
  MapMode = 5
  Placement = pos=(0,0,0) rot=(0.57735,0.57735,0.57735;2.0944rad)
  Support = -> [YZ_Plane388]
  sketch-geometry (8):
    g0: LineSegment StartX=2.8963 StartY=-2.75889 StartZ=0 EndX=3.83742 EndY=1.12882 EndZ=0
    g1: LineSegment StartX=3.83742 StartY=1.12882 StartZ=0 EndX=0.941117 EndY=3.88771 EndZ=0
    g2: LineSegment StartX=0.941117 StartY=3.88771 StartZ=0 EndX=-2.8963 EndY=2.75889 EndZ=0
    g3: LineSegment StartX=-2.8963 StartY=2.75889 StartZ=0 EndX=-3.83742 EndY=-1.12882 EndZ=0
    g4: LineSegment StartX=-3.83742 StartY=-1.12882 StartZ=0 EndX=-0.941117 EndY=-3.88771 EndZ=0
    g5: LineSegment StartX=-0.941117 StartY=-3.88771 StartZ=0 EndX=2.8963 EndY=-2.75889 EndZ=0
    g6: Circle CenterX=0 CenterY=0 CenterZ=0 NormalX=0 NormalY=0 NormalZ=1 AngleXU=0 Radius=4
    g7: Circle CenterX=0 CenterY=0 CenterZ=0 NormalX=0 NormalY=0 NormalZ=1 AngleXU=0 Radius=2.5
  constraints (17):
    c: Coincident(g0,g1)
    c: Coincident(g1,g2)
    c: Coincident(g2,g3)
    c: Coincident(g3,g4)
    c: Coincident(g4,g5)
    c: Coincident(g5,g0)
    c: Equal(g0, g1-g5) x5
    c: PointOnObject(g0,g6)
    c: PointOnObject(g1,g6)
    c: PointOnObject(g2,g6)
    c: PointOnObject(g3,g6)
    c: PointOnObject(g4,g6)
    c: PointOnObject(g5,g6)
    c: Coincident(g6,g-1)
    c: Coincident(g7,g6)
    c: Radius(g7) = 2.5
    c: Radius(g6) = 4
FEATURE [PartDesign::Pad] Pad210
  Direction = (1,-2e-16,3e-16)
  Length = 3
  Length2 = 10
  Placement = pos=(0,0,0) rot=(0.57735,0.57735,0.57735;2.0944rad)
  Profile = -> Sketch361
  Type = 0
FEATURE [PartDesign::Pad] Pad207
  BaseFeature = -> Pad210
  Direction = (1,-2e-16,6e-16)
  Length = 15
  Length2 = 10
  Placement = pos=(0,0,0) rot=(0.57735,0.57735,0.57735;2.0944rad)
  Profile = -> Pad210 [Edge20]
  Type = 0
FEATURE [Sketcher::SketchObject] Sketch362
  FullyConstrained = false
  MapMode = 5
  Placement = pos=(0,0,0) rot=(0.57735,0.57735,0.57735;2.0944rad)
  Support = -> [YZ_Plane382]
  sketch-geometry (8):
    g0: LineSegment StartX=2.8963 StartY=-2.75889 StartZ=0 EndX=3.83742 EndY=1.12882 EndZ=0
    g1: LineSegment StartX=3.83742 StartY=1.12882 StartZ=0 EndX=0.941117 EndY=3.88771 EndZ=0
    g2: LineSegment StartX=0.941117 StartY=3.88771 StartZ=0 EndX=-2.8963 EndY=2.75889 EndZ=0
    g3: LineSegment StartX=-2.8963 StartY=2.75889 StartZ=0 EndX=-3.83742 EndY=-1.12882 EndZ=0
    g4: LineSegment StartX=-3.83742 StartY=-1.12882 StartZ=0 EndX=-0.941117 EndY=-3.88771 EndZ=0
    g5: LineSegment StartX=-0.941117 StartY=-3.88771 StartZ=0 EndX=2.8963 EndY=-2.75889 EndZ=0
    g6: Circle CenterX=0 CenterY=0 CenterZ=0 NormalX=0 NormalY=0 NormalZ=1 AngleXU=0 Radius=4
    g7: Circle CenterX=0 CenterY=0 CenterZ=0 NormalX=0 NormalY=0 NormalZ=1 AngleXU=0 Radius=2.5
  constraints (17):
    c: Coincident(g0,g1)
    c: Coincident(g1,g2)
    c: Coincident(g2,g3)
    c: Coincident(g3,g4)
    c: Coincident(g4,g5)
    c: Coincident(g5,g0)
    c: Equal(g0, g1-g5) x5
    c: PointOnObject(g0,g6)
    c: PointOnObject(g1,g6)
    c: PointOnObject(g2,g6)
    c: PointOnObject(g3,g6)
    c: PointOnObject(g4,g6)
    c: PointOnObject(g5,g6)
    c: Coincident(g6,g-1)
    c: Coincident(g7,g6)
    c: Radius(g7) = 2.5
    c: Radius(g6) = 4
FEATURE [PartDesign::Pad] Pad209
  Direction = (1,-2e-16,3e-16)
  Length = 3
  Length2 = 10
  Placement = pos=(0,0,0) rot=(0.57735,0.57735,0.57735;2.0944rad)
  Profile = -> Sketch362
  Type = 0
FEATURE [PartDesign::Body] Body263
  Group = -> [Sketch361,Pad210,Pad207]
  Origin = -> Origin391
  Tip = -> Pad207
FEATURE [PartDesign::Pad] Pad211
  BaseFeature = -> Pad209
  Direction = (1,-2e-16,6e-16)
  Length = 15
  Length2 = 10
  Placement = pos=(0,0,0) rot=(0.57735,0.57735,0.57735;2.0944rad)
  Profile = -> Pad209 [Edge20]
  Type = 0
FEATURE [PartDesign::Body] Body265
  Group = -> [Sketch362,Pad209,Pad211]
  Origin = -> Origin393
  Tip = -> Pad211
FEATURE [App::Part] Part124  label="tornillo M5-15-037"
  Group = -> [Body265]
  Origin = -> Origin387
  Placement = pos=(357,108,88) rot=(0,1,0;1.5708rad)
FEATURE [PartDesign::Pad] Pad212
  BaseFeature = -> Pad208
  Direction = (1,-2e-16,6e-16)
  Length = 15
  Length2 = 10
  Placement = pos=(0,0,0) rot=(0.57735,0.57735,0.57735;2.0944rad)
  Profile = -> Pad208 [Edge20]
  Type = 0
FEATURE [PartDesign::Body] Body266
  Group = -> [Sketch359,Pad208,Pad212]
  Origin = -> Origin390
  Tip = -> Pad212
FEATURE [App::Part] Part125  label="tornillo M5-15-038"
  Group = -> [Body266]
  Origin = -> Origin392
  Placement = pos=(379,108,88) rot=(0,1,0;1.5708rad)
FEATURE [App::Part] Part127  label="tornillo M5-15-040"
  Group = -> [Body263]
  Origin = -> Origin389
  Placement = pos=(357,108,88) rot=(0,1,0;1.5708rad)
FEATURE [App::LinkGroup] LinkGroup028
  ElementList = -> [Part127,Part125]
  LinkMode = 0
  Placement = pos=(0,25,0) rot=(0,0,1;0rad)
FEATURE [PartDesign::Pad] Pad213
  BaseFeature = -> Pad206
  Direction = (1,-2e-16,6e-16)
  Length = 15
  Length2 = 10
  Placement = pos=(0,0,0) rot=(0.57735,0.57735,0.57735;2.0944rad)
  Profile = -> Pad206 [Edge20]
  Type = 0
FEATURE [PartDesign::Body] Body264
  Group = -> [Sketch360,Pad206,Pad213]
  Origin = -> Origin388
  Tip = -> Pad213
FEATURE [App::Part] Part126  label="tornillo M5-15-039"
  Group = -> [Body264]
  Origin = -> Origin394
  Placement = pos=(379,108,88) rot=(0,1,0;1.5708rad)
FEATURE [App::LinkGroup] LinkGroup029
  ElementList = -> [Part124,Part126,LinkGroup028]
  LinkMode = 0
  Placement = pos=(-3.05176e-05,126,-7.62939e-06) rot=(0,0,1;0rad)
FEATURE [Sketcher::SketchObject] Sketch363
  FullyConstrained = false
  MapMode = 5
  Placement = pos=(0,0,0) rot=(0.57735,0.57735,0.57735;2.0944rad)
  Support = -> [YZ_Plane389]
  sketch-geometry (8):
    g0: LineSegment StartX=2.8963 StartY=-2.75889 StartZ=0 EndX=3.83742 EndY=1.12882 EndZ=0
    g1: LineSegment StartX=3.83742 StartY=1.12882 StartZ=0 EndX=0.941117 EndY=3.88771 EndZ=0
    g2: LineSegment StartX=0.941117 StartY=3.88771 StartZ=0 EndX=-2.8963 EndY=2.75889 EndZ=0
    g3: LineSegment StartX=-2.8963 StartY=2.75889 StartZ=0 EndX=-3.83742 EndY=-1.12882 EndZ=0
    g4: LineSegment StartX=-3.83742 StartY=-1.12882 StartZ=0 EndX=-0.941117 EndY=-3.88771 EndZ=0
    g5: LineSegment StartX=-0.941117 StartY=-3.88771 StartZ=0 EndX=2.8963 EndY=-2.75889 EndZ=0
    g6: Circle CenterX=0 CenterY=0 CenterZ=0 NormalX=0 NormalY=0 NormalZ=1 AngleXU=0 Radius=4
    g7: Circle CenterX=0 CenterY=0 CenterZ=0 NormalX=0 NormalY=0 NormalZ=1 AngleXU=0 Radius=2.5
  constraints (17):
    c: Coincident(g0,g1)
    c: Coincident(g1,g2)
    c: Coincident(g2,g3)
    c: Coincident(g3,g4)
    c: Coincident(g4,g5)
    c: Coincident(g5,g0)
    c: Equal(g0, g1-g5) x5
    c: PointOnObject(g0,g6)
    c: PointOnObject(g1,g6)
    c: PointOnObject(g2,g6)
    c: PointOnObject(g3,g6)
    c: PointOnObject(g4,g6)
    c: PointOnObject(g5,g6)
    c: Coincident(g6,g-1)
    c: Coincident(g7,g6)
    c: Radius(g7) = 2.5
    c: Radius(g6) = 4
FEATURE [PartDesign::Pad] Pad214
  Direction = (1,-2e-16,3e-16)
  Length = 3
  Length2 = 10
  Placement = pos=(0,0,0) rot=(0.57735,0.57735,0.57735;2.0944rad)
  Profile = -> Sketch363
  Type = 0
FEATURE [PartDesign::Pad] Pad215
  BaseFeature = -> Pad214
  Direction = (1,-2e-16,6e-16)
  Length = 15
  Length2 = 10
  Placement = pos=(0,0,0) rot=(0.57735,0.57735,0.57735;2.0944rad)
  Profile = -> Pad214 [Edge20]
  Type = 0
FEATURE [PartDesign::Body] Body267
  Group = -> [Sketch363,Pad214,Pad215]
  Origin = -> Origin395
  Tip = -> Pad215
FEATURE [App::Part] Part128  label="tornillo M5-15-041"
  Group = -> [Body267]
  Origin = -> Origin396
  Placement = pos=(345,10,70) rot=(0,1,0;3.14159rad)
FEATURE [Sketcher::SketchObject] Sketch364
  FullyConstrained = false
  MapMode = 5
  Placement = pos=(0,0,0) rot=(0.57735,0.57735,0.57735;2.0944rad)
  Support = -> [YZ_Plane391]
  sketch-geometry (8):
    g0: LineSegment StartX=2.8963 StartY=-2.75889 StartZ=0 EndX=3.83742 EndY=1.12882 EndZ=0
    g1: LineSegment StartX=3.83742 StartY=1.12882 StartZ=0 EndX=0.941117 EndY=3.88771 EndZ=0
    g2: LineSegment StartX=0.941117 StartY=3.88771 StartZ=0 EndX=-2.8963 EndY=2.75889 EndZ=0
    g3: LineSegment StartX=-2.8963 StartY=2.75889 StartZ=0 EndX=-3.83742 EndY=-1.12882 EndZ=0
    g4: LineSegment StartX=-3.83742 StartY=-1.12882 StartZ=0 EndX=-0.941117 EndY=-3.88771 EndZ=0
    g5: LineSegment StartX=-0.941117 StartY=-3.88771 StartZ=0 EndX=2.8963 EndY=-2.75889 EndZ=0
    g6: Circle CenterX=0 CenterY=0 CenterZ=0 NormalX=0 NormalY=0 NormalZ=1 AngleXU=0 Radius=4
    g7: Circle CenterX=0 CenterY=0 CenterZ=0 NormalX=0 NormalY=0 NormalZ=1 AngleXU=0 Radius=2.5
  constraints (17):
    c: Coincident(g0,g1)
    c: Coincident(g1,g2)
    c: Coincident(g2,g3)
    c: Coincident(g3,g4)
    c: Coincident(g4,g5)
    c: Coincident(g5,g0)
    c: Equal(g0, g1-g5) x5
    c: PointOnObject(g0,g6)
    c: PointOnObject(g1,g6)
    c: PointOnObject(g2,g6)
    c: PointOnObject(g3,g6)
    c: PointOnObject(g4,g6)
    c: PointOnObject(g5,g6)
    c: Coincident(g6,g-1)
    c: Coincident(g7,g6)
    c: Radius(g7) = 2.5
    c: Radius(g6) = 4
FEATURE [PartDesign::Pad] Pad217
  Direction = (1,-2e-16,3e-16)
  Length = 3
  Length2 = 10
  Placement = pos=(0,0,0) rot=(0.57735,0.57735,0.57735;2.0944rad)
  Profile = -> Sketch364
  Type = 0
FEATURE [PartDesign::Pad] Pad216
  BaseFeature = -> Pad217
  Direction = (1,-2e-16,6e-16)
  Length = 15
  Length2 = 10
  Placement = pos=(0,0,0) rot=(0.57735,0.57735,0.57735;2.0944rad)
  Profile = -> Pad217 [Edge20]
  Type = 0
FEATURE [PartDesign::Body] Body268
  Group = -> [Sketch364,Pad217,Pad216]
  Origin = -> Origin398
  Tip = -> Pad216
FEATURE [App::Part] Part129  label="tornillo M5-15-042"
  Group = -> [Body268]
  Origin = -> Origin397
  Placement = pos=(345,330,70) rot=(0,1,0;3.14159rad)
